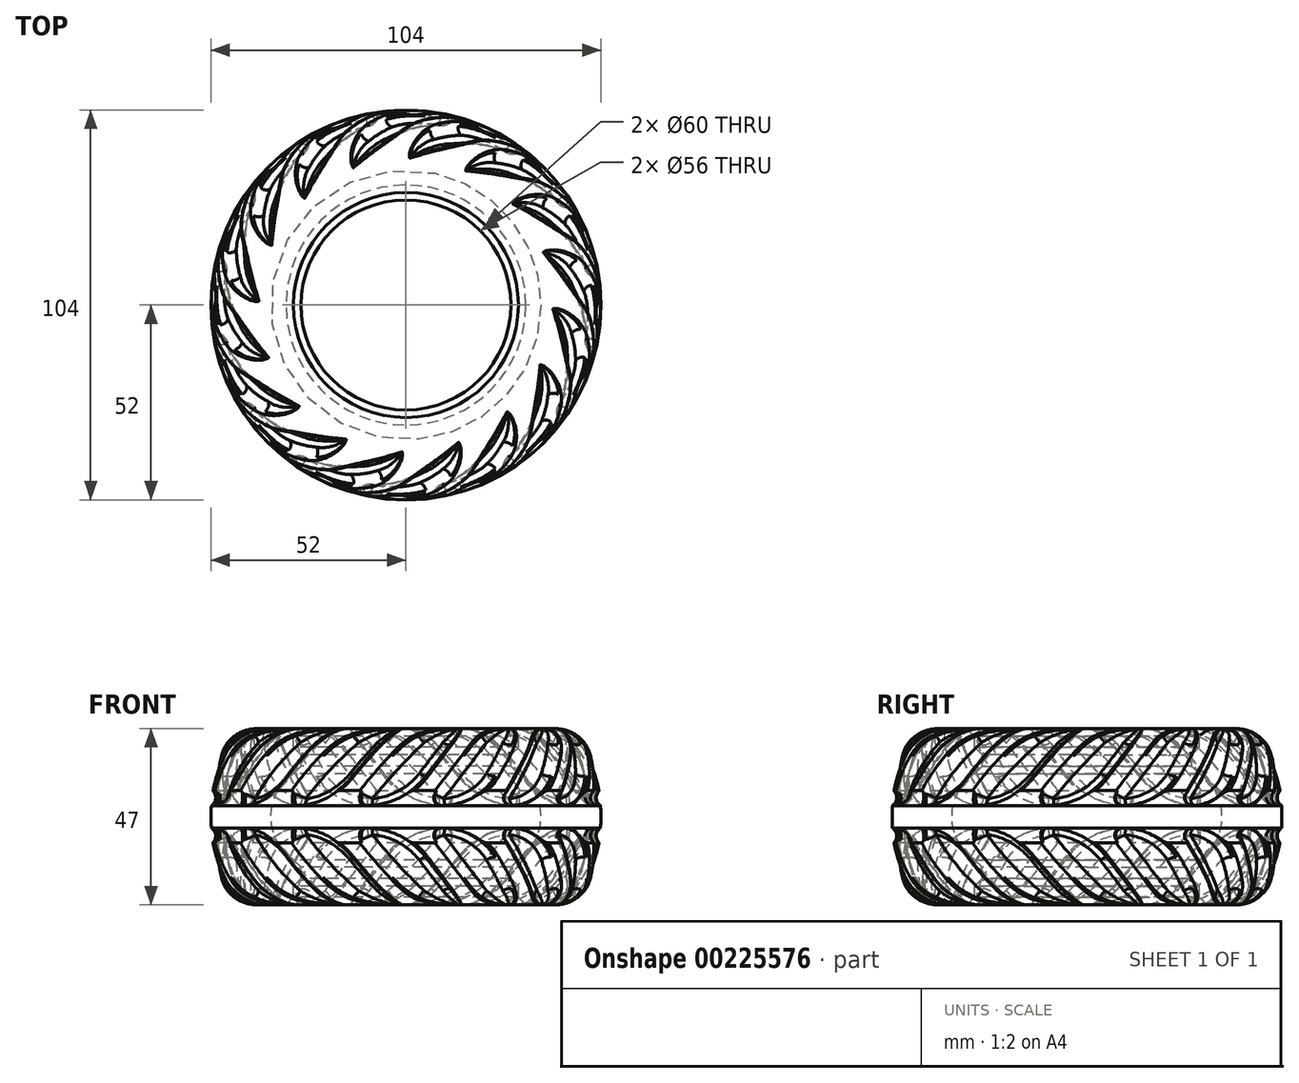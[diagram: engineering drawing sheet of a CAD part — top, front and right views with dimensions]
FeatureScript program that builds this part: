
annotation { "Feature Type Name" : "Feature", "Feature Type Description" : "" }
export const myFeature = defineFeature(function(context is Context, id is Id, definition is map)
    precondition{}
    {
        {
            var Q0;
            Q0=qCreatedBy(makeId("Front.planeOp"),FACE);
            var sketch = newSketch(context, id + "F0", { "sketchPlane" : qUnion([Q0])});
            skLineSegment(sketch, "E0", {"start": v(0, 0) * mm, "end": v(-62.9, 0) * mm, "construction": true});
            skCircle(sketch, "E1", {"center": v(-39.12, 17.25) * mm, "radius": 6.25 * mm});
            skCircle(sketch, "E2", {"center": v(0, 0) * mm, "radius": 55 * mm});
            skCircle(sketch, "E3", {"center": v(-39.12, -17.25) * mm, "radius": 6.25 * mm});
            skCircle(sketch, "E4", {"center": v(0, 0) * mm, "radius": 49 * mm});
            skLineSegment(sketch, "E5", {"start": v(-30, 23.5) * mm, "end": v(-39.12, 23.5) * mm});
            skLineSegment(sketch, "E6", {"start": v(-30, -23.5) * mm, "end": v(-39.12, -23.5) * mm});
            skLineSegment(sketch, "E7", {"start": v(0, 89.19) * mm, "end": v(0, -93.9) * mm, "construction": true});
            skLineSegment(sketch, "E8", {"start": v(-30, 23.5) * mm, "end": v(-30, 18.5) * mm});
            skLineSegment(sketch, "E9", {"start": v(-30, 18.5) * mm, "end": v(-28, 18.5) * mm});
            skLineSegment(sketch, "E10", {"start": v(-28, 18.5) * mm, "end": v(-28, 11.5) * mm});
            skLineSegment(sketch, "E11", {"start": v(-28, 11.5) * mm, "end": v(-30, 11.5) * mm});
            skLineSegment(sketch, "E12", {"start": v(-30, 11.5) * mm, "end": v(-30, -11.5) * mm});
            skLineSegment(sketch, "E13", {"start": v(-30, -11.5) * mm, "end": v(-28, -11.5) * mm});
            skLineSegment(sketch, "E14", {"start": v(-28, -11.5) * mm, "end": v(-28, -18.5) * mm});
            skLineSegment(sketch, "E15", {"start": v(-28, -18.5) * mm, "end": v(-30, -18.5) * mm});
            skLineSegment(sketch, "E16", {"start": v(-30, -18.5) * mm, "end": v(-30, -23.5) * mm});
            skArc(sketch, "E17", {"start": v(-30, 11.5) * mm, "mid": v(-36, 0) * mm, "end": v(-30, -11.5) * mm});
            skSolve(sketch);
        }
        {
            var Q0;
            {var subQ1=sQuery(id+"F0.wireOp",EDGE,"E5");Q0=makeQuery(id+"F0.imprint","IMPRINT",FACE,{"disambiguationData":[TD([[makeQuery(id+"F0.imprint","IMPRINT",EDGE,{"derivedFrom":subQ1}),1.0]])]});}
            var Q1;
            {var subQ0=sQuery(id+"F0.wireOp",EDGE,"E1");var subQ1=makeQuery(id+"F0.imprint","INTERSECT",VERTEX,{"derivedFrom":[subQ0,sQuery(id+"F0.wireOp",EDGE,"E5")]});Q1=makeQuery(id+"F0.imprint","IMPRINT",FACE,{"disambiguationData":[TD([[makeQuery(id+"F0.imprint","IMPRINT",EDGE,{"disambiguationData":[TD([[subQ1,-1.0]])],"derivedFrom":subQ0}),1.0]])]});}
            var Q2;
            {var subQ0=sQuery(id+"F0.wireOp",EDGE,"E3");var subQ1=makeQuery(id+"F0.imprint","INTERSECT",VERTEX,{"derivedFrom":[subQ0,sQuery(id+"F0.wireOp",EDGE,"E6")]});Q2=makeQuery(id+"F0.imprint","IMPRINT",FACE,{"disambiguationData":[TD([[makeQuery(id+"F0.imprint","IMPRINT",EDGE,{"disambiguationData":[TD([[subQ1,1.0]])],"derivedFrom":subQ0}),1.0]])]});}
            var Q3;
            Q3=sQuery(id+"F0.wireOp",EDGE,"E7");
            revolve(context, id + "F1", {"entities" : qUnion([Q0, Q1, Q2]), "axis" : qUnion([Q3]), "revolveType" : RevolveType.FULL});
        }
        {
            var Q0;
            Q0=qCreatedBy(makeId("Top.planeOp"),FACE);
            cPlane(context, id + "F2", {"entities" : qUnion([Q0]), "cplaneType" : CPlaneType.OFFSET, "offset" : 23.5 * mm, "width" : 150 * mm, "height" : 150 * mm});
        }
        {
            var Q0;
            Q0=qCreatedBy(makeId("Top.planeOp"),FACE);
            var sketch = newSketch(context, id + "F3", { "sketchPlane" : qUnion([Q0])});
            skLineSegment(sketch, "E18.bottom", {"start": v(-3, 40) * mm, "end": v(3, 40) * mm});
            skLineSegment(sketch, "E18.top", {"start": v(-3, 66) * mm, "end": v(3, 66) * mm});
            skLineSegment(sketch, "E18.left", {"start": v(-3, 40) * mm, "end": v(-3, 66) * mm});
            skLineSegment(sketch, "E18.right", {"start": v(3, 40) * mm, "end": v(3, 66) * mm});
            skLineSegment(sketch, "E19", {"start": v(0, 113.7) * mm, "end": v(0, -99.56) * mm, "construction": true});
            skLineSegment(sketch, "E20.1.0", {"start": v(-18.08, 35.8) * mm, "end": v(-28.03, 59.83) * mm});
            skLineSegment(sketch, "E20.1.1", {"start": v(-28.03, 59.83) * mm, "end": v(-22.49, 62.12) * mm});
            skLineSegment(sketch, "E20.1.2", {"start": v(-12.54, 38.1) * mm, "end": v(-22.49, 62.12) * mm});
            skLineSegment(sketch, "E20.1.3", {"start": v(-18.08, 35.8) * mm, "end": v(-12.54, 38.1) * mm});
            skLineSegment(sketch, "E20.2.0", {"start": v(-30.4, 26.16) * mm, "end": v(-48.8, 44.55) * mm});
            skLineSegment(sketch, "E20.2.1", {"start": v(-48.8, 44.55) * mm, "end": v(-44.55, 48.8) * mm});
            skLineSegment(sketch, "E20.2.2", {"start": v(-26.16, 30.4) * mm, "end": v(-44.55, 48.8) * mm});
            skLineSegment(sketch, "E20.2.3", {"start": v(-30.4, 26.16) * mm, "end": v(-26.16, 30.4) * mm});
            skLineSegment(sketch, "E20.3.0", {"start": v(-38.1, 12.54) * mm, "end": v(-62.12, 22.49) * mm});
            skLineSegment(sketch, "E20.3.1", {"start": v(-62.12, 22.49) * mm, "end": v(-59.83, 28.03) * mm});
            skLineSegment(sketch, "E20.3.2", {"start": v(-35.8, 18.08) * mm, "end": v(-59.83, 28.03) * mm});
            skLineSegment(sketch, "E20.3.3", {"start": v(-38.1, 12.54) * mm, "end": v(-35.8, 18.08) * mm});
            skLineSegment(sketch, "E20.4.0", {"start": v(-40, -3) * mm, "end": v(-66, -3) * mm});
            skLineSegment(sketch, "E20.4.1", {"start": v(-66, -3) * mm, "end": v(-66, 3) * mm});
            skLineSegment(sketch, "E20.4.2", {"start": v(-40, 3) * mm, "end": v(-66, 3) * mm});
            skLineSegment(sketch, "E20.4.3", {"start": v(-40, -3) * mm, "end": v(-40, 3) * mm});
            skLineSegment(sketch, "E20.5.0", {"start": v(-35.8, -18.08) * mm, "end": v(-59.83, -28.03) * mm});
            skLineSegment(sketch, "E20.5.1", {"start": v(-59.83, -28.03) * mm, "end": v(-62.12, -22.49) * mm});
            skLineSegment(sketch, "E20.5.2", {"start": v(-38.1, -12.54) * mm, "end": v(-62.12, -22.49) * mm});
            skLineSegment(sketch, "E20.5.3", {"start": v(-35.8, -18.08) * mm, "end": v(-38.1, -12.54) * mm});
            skLineSegment(sketch, "E20.6.0", {"start": v(-26.16, -30.4) * mm, "end": v(-44.55, -48.8) * mm});
            skLineSegment(sketch, "E20.6.1", {"start": v(-44.55, -48.8) * mm, "end": v(-48.8, -44.55) * mm});
            skLineSegment(sketch, "E20.6.2", {"start": v(-30.4, -26.16) * mm, "end": v(-48.8, -44.55) * mm});
            skLineSegment(sketch, "E20.6.3", {"start": v(-26.16, -30.4) * mm, "end": v(-30.4, -26.16) * mm});
            skLineSegment(sketch, "E20.7.0", {"start": v(-12.54, -38.1) * mm, "end": v(-22.49, -62.12) * mm});
            skLineSegment(sketch, "E20.7.1", {"start": v(-22.49, -62.12) * mm, "end": v(-28.03, -59.83) * mm});
            skLineSegment(sketch, "E20.7.2", {"start": v(-18.08, -35.8) * mm, "end": v(-28.03, -59.83) * mm});
            skLineSegment(sketch, "E20.7.3", {"start": v(-12.54, -38.1) * mm, "end": v(-18.08, -35.8) * mm});
            skLineSegment(sketch, "E20.8.0", {"start": v(3, -40) * mm, "end": v(3, -66) * mm});
            skLineSegment(sketch, "E20.8.1", {"start": v(3, -66) * mm, "end": v(-3, -66) * mm});
            skLineSegment(sketch, "E20.8.2", {"start": v(-3, -40) * mm, "end": v(-3, -66) * mm});
            skLineSegment(sketch, "E20.8.3", {"start": v(3, -40) * mm, "end": v(-3, -40) * mm});
            skLineSegment(sketch, "E20.9.0", {"start": v(18.08, -35.8) * mm, "end": v(28.03, -59.83) * mm});
            skLineSegment(sketch, "E20.9.1", {"start": v(28.03, -59.83) * mm, "end": v(22.49, -62.12) * mm});
            skLineSegment(sketch, "E20.9.2", {"start": v(12.54, -38.1) * mm, "end": v(22.49, -62.12) * mm});
            skLineSegment(sketch, "E20.9.3", {"start": v(18.08, -35.8) * mm, "end": v(12.54, -38.1) * mm});
            skLineSegment(sketch, "E20.10.0", {"start": v(30.4, -26.16) * mm, "end": v(48.8, -44.55) * mm});
            skLineSegment(sketch, "E20.10.1", {"start": v(48.8, -44.55) * mm, "end": v(44.55, -48.8) * mm});
            skLineSegment(sketch, "E20.10.2", {"start": v(26.16, -30.4) * mm, "end": v(44.55, -48.8) * mm});
            skLineSegment(sketch, "E20.10.3", {"start": v(30.4, -26.16) * mm, "end": v(26.16, -30.4) * mm});
            skLineSegment(sketch, "E20.11.0", {"start": v(38.1, -12.54) * mm, "end": v(62.12, -22.49) * mm});
            skLineSegment(sketch, "E20.11.1", {"start": v(62.12, -22.49) * mm, "end": v(59.83, -28.03) * mm});
            skLineSegment(sketch, "E20.11.2", {"start": v(35.8, -18.08) * mm, "end": v(59.83, -28.03) * mm});
            skLineSegment(sketch, "E20.11.3", {"start": v(38.1, -12.54) * mm, "end": v(35.8, -18.08) * mm});
            skLineSegment(sketch, "E20.12.0", {"start": v(40, 3) * mm, "end": v(66, 3) * mm});
            skLineSegment(sketch, "E20.12.1", {"start": v(66, 3) * mm, "end": v(66, -3) * mm});
            skLineSegment(sketch, "E20.12.2", {"start": v(40, -3) * mm, "end": v(66, -3) * mm});
            skLineSegment(sketch, "E20.12.3", {"start": v(40, 3) * mm, "end": v(40, -3) * mm});
            skLineSegment(sketch, "E20.13.0", {"start": v(35.8, 18.08) * mm, "end": v(59.83, 28.03) * mm});
            skLineSegment(sketch, "E20.13.1", {"start": v(59.83, 28.03) * mm, "end": v(62.12, 22.49) * mm});
            skLineSegment(sketch, "E20.13.2", {"start": v(38.1, 12.54) * mm, "end": v(62.12, 22.49) * mm});
            skLineSegment(sketch, "E20.13.3", {"start": v(35.8, 18.08) * mm, "end": v(38.1, 12.54) * mm});
            skLineSegment(sketch, "E20.14.0", {"start": v(26.16, 30.4) * mm, "end": v(44.55, 48.8) * mm});
            skLineSegment(sketch, "E20.14.1", {"start": v(44.55, 48.8) * mm, "end": v(48.8, 44.55) * mm});
            skLineSegment(sketch, "E20.14.2", {"start": v(30.4, 26.16) * mm, "end": v(48.8, 44.55) * mm});
            skLineSegment(sketch, "E20.14.3", {"start": v(26.16, 30.4) * mm, "end": v(30.4, 26.16) * mm});
            skLineSegment(sketch, "E20.15.0", {"start": v(12.54, 38.1) * mm, "end": v(22.49, 62.12) * mm});
            skLineSegment(sketch, "E20.15.1", {"start": v(22.49, 62.12) * mm, "end": v(28.03, 59.83) * mm});
            skLineSegment(sketch, "E20.15.2", {"start": v(18.08, 35.8) * mm, "end": v(28.03, 59.83) * mm});
            skLineSegment(sketch, "E20.15.3", {"start": v(12.54, 38.1) * mm, "end": v(18.08, 35.8) * mm});
            skPoint(sketch, "E20.center", {"position": v(0, 0) * mm});
            skSolve(sketch);
        }
        {
            var Q0;
            Q0=qCreatedBy(id+"F2.planeOp",FACE);
            var sketch = newSketch(context, id + "F4", { "sketchPlane" : qUnion([Q0])});
            skLineSegment(sketch, "E21", {"start": v(-21, 70) * mm, "end": v(-21, 30) * mm});
            skLineSegment(sketch, "E22", {"start": v(-21, 30) * mm, "end": v(-15, 30) * mm});
            skLineSegment(sketch, "E23", {"start": v(-21, 70) * mm, "end": v(-15, 70) * mm});
            skLineSegment(sketch, "E24", {"start": v(-15, 70) * mm, "end": v(-15, 30) * mm});
            skLineSegment(sketch, "E25", {"start": v(0, 99.7) * mm, "end": v(0, -107.8) * mm, "construction": true});
            skLineSegment(sketch, "E26.1.0", {"start": v(-46.19, 56.64) * mm, "end": v(-30.88, 19.68) * mm});
            skLineSegment(sketch, "E26.1.1", {"start": v(-40.65, 58.93) * mm, "end": v(-25.34, 21.98) * mm});
            skLineSegment(sketch, "E26.1.2", {"start": v(-30.88, 19.68) * mm, "end": v(-25.34, 21.98) * mm});
            skLineSegment(sketch, "E26.1.3", {"start": v(-46.19, 56.64) * mm, "end": v(-40.65, 58.93) * mm});
            skLineSegment(sketch, "E26.2.0", {"start": v(-64.35, 34.65) * mm, "end": v(-36.06, 6.36) * mm});
            skLineSegment(sketch, "E26.2.1", {"start": v(-60.1, 38.9) * mm, "end": v(-31.82, 10.6) * mm});
            skLineSegment(sketch, "E26.2.2", {"start": v(-36.06, 6.36) * mm, "end": v(-31.82, 10.6) * mm});
            skLineSegment(sketch, "E26.2.3", {"start": v(-64.35, 34.65) * mm, "end": v(-60.1, 38.9) * mm});
            skLineSegment(sketch, "E26.3.0", {"start": v(-72.7, 7.39) * mm, "end": v(-35.75, -7.92) * mm});
            skLineSegment(sketch, "E26.3.1", {"start": v(-70.41, 12.93) * mm, "end": v(-33.46, -2.38) * mm});
            skLineSegment(sketch, "E26.3.2", {"start": v(-35.75, -7.92) * mm, "end": v(-33.46, -2.38) * mm});
            skLineSegment(sketch, "E26.3.3", {"start": v(-72.7, 7.39) * mm, "end": v(-70.41, 12.93) * mm});
            skLineSegment(sketch, "E26.4.0", {"start": v(-70, -21) * mm, "end": v(-30, -21) * mm});
            skLineSegment(sketch, "E26.4.1", {"start": v(-70, -15) * mm, "end": v(-30, -15) * mm});
            skLineSegment(sketch, "E26.4.2", {"start": v(-30, -21) * mm, "end": v(-30, -15) * mm});
            skLineSegment(sketch, "E26.4.3", {"start": v(-70, -21) * mm, "end": v(-70, -15) * mm});
            skLineSegment(sketch, "E26.5.0", {"start": v(-56.64, -46.19) * mm, "end": v(-19.68, -30.88) * mm});
            skLineSegment(sketch, "E26.5.1", {"start": v(-58.93, -40.65) * mm, "end": v(-21.98, -25.34) * mm});
            skLineSegment(sketch, "E26.5.2", {"start": v(-19.68, -30.88) * mm, "end": v(-21.98, -25.34) * mm});
            skLineSegment(sketch, "E26.5.3", {"start": v(-56.64, -46.19) * mm, "end": v(-58.93, -40.65) * mm});
            skLineSegment(sketch, "E26.6.0", {"start": v(-34.65, -64.35) * mm, "end": v(-6.36, -36.06) * mm});
            skLineSegment(sketch, "E26.6.1", {"start": v(-38.9, -60.1) * mm, "end": v(-10.6, -31.82) * mm});
            skLineSegment(sketch, "E26.6.2", {"start": v(-6.36, -36.06) * mm, "end": v(-10.6, -31.82) * mm});
            skLineSegment(sketch, "E26.6.3", {"start": v(-34.65, -64.35) * mm, "end": v(-38.9, -60.1) * mm});
            skLineSegment(sketch, "E26.7.0", {"start": v(-7.39, -72.7) * mm, "end": v(7.92, -35.75) * mm});
            skLineSegment(sketch, "E26.7.1", {"start": v(-12.93, -70.41) * mm, "end": v(2.38, -33.46) * mm});
            skLineSegment(sketch, "E26.7.2", {"start": v(7.92, -35.75) * mm, "end": v(2.38, -33.46) * mm});
            skLineSegment(sketch, "E26.7.3", {"start": v(-7.39, -72.7) * mm, "end": v(-12.93, -70.41) * mm});
            skLineSegment(sketch, "E26.8.0", {"start": v(21, -70) * mm, "end": v(21, -30) * mm});
            skLineSegment(sketch, "E26.8.1", {"start": v(15, -70) * mm, "end": v(15, -30) * mm});
            skLineSegment(sketch, "E26.8.2", {"start": v(21, -30) * mm, "end": v(15, -30) * mm});
            skLineSegment(sketch, "E26.8.3", {"start": v(21, -70) * mm, "end": v(15, -70) * mm});
            skLineSegment(sketch, "E26.9.0", {"start": v(46.19, -56.64) * mm, "end": v(30.88, -19.68) * mm});
            skLineSegment(sketch, "E26.9.1", {"start": v(40.65, -58.93) * mm, "end": v(25.34, -21.98) * mm});
            skLineSegment(sketch, "E26.9.2", {"start": v(30.88, -19.68) * mm, "end": v(25.34, -21.98) * mm});
            skLineSegment(sketch, "E26.9.3", {"start": v(46.19, -56.64) * mm, "end": v(40.65, -58.93) * mm});
            skLineSegment(sketch, "E26.10.0", {"start": v(64.35, -34.65) * mm, "end": v(36.06, -6.36) * mm});
            skLineSegment(sketch, "E26.10.1", {"start": v(60.1, -38.9) * mm, "end": v(31.82, -10.6) * mm});
            skLineSegment(sketch, "E26.10.2", {"start": v(36.06, -6.36) * mm, "end": v(31.82, -10.6) * mm});
            skLineSegment(sketch, "E26.10.3", {"start": v(64.35, -34.65) * mm, "end": v(60.1, -38.9) * mm});
            skLineSegment(sketch, "E26.11.0", {"start": v(72.7, -7.39) * mm, "end": v(35.75, 7.92) * mm});
            skLineSegment(sketch, "E26.11.1", {"start": v(70.41, -12.93) * mm, "end": v(33.46, 2.38) * mm});
            skLineSegment(sketch, "E26.11.2", {"start": v(35.75, 7.92) * mm, "end": v(33.46, 2.38) * mm});
            skLineSegment(sketch, "E26.11.3", {"start": v(72.7, -7.39) * mm, "end": v(70.41, -12.93) * mm});
            skLineSegment(sketch, "E26.12.0", {"start": v(70, 21) * mm, "end": v(30, 21) * mm});
            skLineSegment(sketch, "E26.12.1", {"start": v(70, 15) * mm, "end": v(30, 15) * mm});
            skLineSegment(sketch, "E26.12.2", {"start": v(30, 21) * mm, "end": v(30, 15) * mm});
            skLineSegment(sketch, "E26.12.3", {"start": v(70, 21) * mm, "end": v(70, 15) * mm});
            skLineSegment(sketch, "E26.13.0", {"start": v(56.64, 46.19) * mm, "end": v(19.68, 30.88) * mm});
            skLineSegment(sketch, "E26.13.1", {"start": v(58.93, 40.65) * mm, "end": v(21.98, 25.34) * mm});
            skLineSegment(sketch, "E26.13.2", {"start": v(19.68, 30.88) * mm, "end": v(21.98, 25.34) * mm});
            skLineSegment(sketch, "E26.13.3", {"start": v(56.64, 46.19) * mm, "end": v(58.93, 40.65) * mm});
            skLineSegment(sketch, "E26.14.0", {"start": v(34.65, 64.35) * mm, "end": v(6.36, 36.06) * mm});
            skLineSegment(sketch, "E26.14.1", {"start": v(38.9, 60.1) * mm, "end": v(10.6, 31.82) * mm});
            skLineSegment(sketch, "E26.14.2", {"start": v(6.36, 36.06) * mm, "end": v(10.6, 31.82) * mm});
            skLineSegment(sketch, "E26.14.3", {"start": v(34.65, 64.35) * mm, "end": v(38.9, 60.1) * mm});
            skLineSegment(sketch, "E26.15.0", {"start": v(7.39, 72.7) * mm, "end": v(-7.92, 35.75) * mm});
            skLineSegment(sketch, "E26.15.1", {"start": v(12.93, 70.41) * mm, "end": v(-2.38, 33.46) * mm});
            skLineSegment(sketch, "E26.15.2", {"start": v(-7.92, 35.75) * mm, "end": v(-2.38, 33.46) * mm});
            skLineSegment(sketch, "E26.15.3", {"start": v(7.39, 72.7) * mm, "end": v(12.93, 70.41) * mm});
            skPoint(sketch, "E26.center", {"position": v(0, 0) * mm});
            skSolve(sketch);
        }
        {
            var Q2;
            Q2=makeQuery(id+"F3.imprint","IMPRINT",FACE,{"disambiguationData":[TD([[makeQuery(id+"F3.imprint","IMPRINT",EDGE,{"derivedFrom":sQuery(id+"F3.wireOp",EDGE,"E18.bottom")}),1.0]])]});
            var Q3;
            Q3=makeQuery(id+"F4.imprint","IMPRINT",FACE,{"disambiguationData":[TD([[makeQuery(id+"F4.imprint","IMPRINT",EDGE,{"derivedFrom":sQuery(id+"F4.wireOp",EDGE,"E21")}),1.0]])]});
            loft(context, id + "F5", {"operationType" : NewBodyOperationType.ADD, "sheetProfilesArray" : [{ "sheetProfileEntities" : qUnion([Q2]) }, { "sheetProfileEntities" : qUnion([Q3]) }]});
        }
        {
            var Q2;
            Q2=makeQuery(id+"F3.imprint","IMPRINT",FACE,{"disambiguationData":[TD([[makeQuery(id+"F3.imprint","IMPRINT",EDGE,{"derivedFrom":sQuery(id+"F3.wireOp",EDGE,"E20.15.0")}),-1.0]])]});
            var Q3;
            Q3=makeQuery(id+"F4.imprint","IMPRINT",FACE,{"disambiguationData":[TD([[makeQuery(id+"F4.imprint","IMPRINT",EDGE,{"derivedFrom":sQuery(id+"F4.wireOp",EDGE,"E26.15.0")}),1.0]])]});
            loft(context, id + "F6", {"operationType" : NewBodyOperationType.ADD, "sheetProfilesArray" : [{ "sheetProfileEntities" : qUnion([Q2]) }, { "sheetProfileEntities" : qUnion([Q3]) }]});
        }
        {
            var Q1;
            Q1=makeQuery(id+"F3.imprint","IMPRINT",FACE,{"disambiguationData":[TD([[makeQuery(id+"F3.imprint","IMPRINT",EDGE,{"derivedFrom":sQuery(id+"F3.wireOp",EDGE,"E20.14.0")}),-1.0]])]});
            var Q2;
            Q2=makeQuery(id+"F4.imprint","IMPRINT",FACE,{"disambiguationData":[TD([[makeQuery(id+"F4.imprint","IMPRINT",EDGE,{"derivedFrom":sQuery(id+"F4.wireOp",EDGE,"E26.14.0")}),1.0]])]});
            loft(context, id + "F7", {"operationType" : NewBodyOperationType.ADD, "sheetProfilesArray" : [{ "sheetProfileEntities" : qUnion([Q1]) }, { "sheetProfileEntities" : qUnion([Q2]) }]});
        }
        {
            var Q1;
            Q1=makeQuery(id+"F3.imprint","IMPRINT",FACE,{"disambiguationData":[TD([[makeQuery(id+"F3.imprint","IMPRINT",EDGE,{"derivedFrom":sQuery(id+"F3.wireOp",EDGE,"E20.13.0")}),-1.0]])]});
            var Q2;
            Q2=makeQuery(id+"F4.imprint","IMPRINT",FACE,{"disambiguationData":[TD([[makeQuery(id+"F4.imprint","IMPRINT",EDGE,{"derivedFrom":sQuery(id+"F4.wireOp",EDGE,"E26.13.0")}),1.0]])]});
            loft(context, id + "F8", {"operationType" : NewBodyOperationType.ADD, "sheetProfilesArray" : [{ "sheetProfileEntities" : qUnion([Q1]) }, { "sheetProfileEntities" : qUnion([Q2]) }]});
        }
        {
            var Q2;
            Q2=makeQuery(id+"F3.imprint","IMPRINT",FACE,{"disambiguationData":[TD([[makeQuery(id+"F3.imprint","IMPRINT",EDGE,{"derivedFrom":sQuery(id+"F3.wireOp",EDGE,"E20.12.0")}),-1.0]])]});
            var Q3;
            Q3=makeQuery(id+"F4.imprint","IMPRINT",FACE,{"disambiguationData":[TD([[makeQuery(id+"F4.imprint","IMPRINT",EDGE,{"derivedFrom":sQuery(id+"F4.wireOp",EDGE,"E26.12.0")}),1.0]])]});
            loft(context, id + "F9", {"operationType" : NewBodyOperationType.ADD, "sheetProfilesArray" : [{ "sheetProfileEntities" : qUnion([Q2]) }, { "sheetProfileEntities" : qUnion([Q3]) }]});
        }
        {
            var Q2;
            Q2=makeQuery(id+"F3.imprint","IMPRINT",FACE,{"disambiguationData":[TD([[makeQuery(id+"F3.imprint","IMPRINT",EDGE,{"derivedFrom":sQuery(id+"F3.wireOp",EDGE,"E20.11.0")}),-1.0]])]});
            var Q3;
            Q3=makeQuery(id+"F4.imprint","IMPRINT",FACE,{"disambiguationData":[TD([[makeQuery(id+"F4.imprint","IMPRINT",EDGE,{"derivedFrom":sQuery(id+"F4.wireOp",EDGE,"E26.11.0")}),1.0]])]});
            loft(context, id + "F10", {"operationType" : NewBodyOperationType.ADD, "sheetProfilesArray" : [{ "sheetProfileEntities" : qUnion([Q2]) }, { "sheetProfileEntities" : qUnion([Q3]) }]});
        }
        {
            var Q2;
            Q2=makeQuery(id+"F3.imprint","IMPRINT",FACE,{"disambiguationData":[TD([[makeQuery(id+"F3.imprint","IMPRINT",EDGE,{"derivedFrom":sQuery(id+"F3.wireOp",EDGE,"E20.10.0")}),-1.0]])]});
            var Q3;
            Q3=makeQuery(id+"F4.imprint","IMPRINT",FACE,{"disambiguationData":[TD([[makeQuery(id+"F4.imprint","IMPRINT",EDGE,{"derivedFrom":sQuery(id+"F4.wireOp",EDGE,"E26.10.0")}),1.0]])]});
            loft(context, id + "F11", {"operationType" : NewBodyOperationType.ADD, "sheetProfilesArray" : [{ "sheetProfileEntities" : qUnion([Q2]) }, { "sheetProfileEntities" : qUnion([Q3]) }]});
        }
        {
            var Q2;
            Q2=makeQuery(id+"F3.imprint","IMPRINT",FACE,{"disambiguationData":[TD([[makeQuery(id+"F3.imprint","IMPRINT",EDGE,{"derivedFrom":sQuery(id+"F3.wireOp",EDGE,"E20.9.0")}),-1.0]])]});
            var Q3;
            Q3=makeQuery(id+"F4.imprint","IMPRINT",FACE,{"disambiguationData":[TD([[makeQuery(id+"F4.imprint","IMPRINT",EDGE,{"derivedFrom":sQuery(id+"F4.wireOp",EDGE,"E26.9.0")}),1.0]])]});
            loft(context, id + "F12", {"operationType" : NewBodyOperationType.ADD, "sheetProfilesArray" : [{ "sheetProfileEntities" : qUnion([Q2]) }, { "sheetProfileEntities" : qUnion([Q3]) }]});
        }
        {
            var Q2;
            Q2=makeQuery(id+"F3.imprint","IMPRINT",FACE,{"disambiguationData":[TD([[makeQuery(id+"F3.imprint","IMPRINT",EDGE,{"derivedFrom":sQuery(id+"F3.wireOp",EDGE,"E20.8.0")}),-1.0]])]});
            var Q3;
            Q3=makeQuery(id+"F4.imprint","IMPRINT",FACE,{"disambiguationData":[TD([[makeQuery(id+"F4.imprint","IMPRINT",EDGE,{"derivedFrom":sQuery(id+"F4.wireOp",EDGE,"E26.8.0")}),1.0]])]});
            loft(context, id + "F13", {"operationType" : NewBodyOperationType.ADD, "sheetProfilesArray" : [{ "sheetProfileEntities" : qUnion([Q2]) }, { "sheetProfileEntities" : qUnion([Q3]) }]});
        }
        {
            var Q2;
            Q2=makeQuery(id+"F3.imprint","IMPRINT",FACE,{"disambiguationData":[TD([[makeQuery(id+"F3.imprint","IMPRINT",EDGE,{"derivedFrom":sQuery(id+"F3.wireOp",EDGE,"E20.7.0")}),-1.0]])]});
            var Q3;
            Q3=makeQuery(id+"F4.imprint","IMPRINT",FACE,{"disambiguationData":[TD([[makeQuery(id+"F4.imprint","IMPRINT",EDGE,{"derivedFrom":sQuery(id+"F4.wireOp",EDGE,"E26.7.0")}),1.0]])]});
            loft(context, id + "F14", {"operationType" : NewBodyOperationType.ADD, "sheetProfilesArray" : [{ "sheetProfileEntities" : qUnion([Q2]) }, { "sheetProfileEntities" : qUnion([Q3]) }]});
        }
        {
            var Q2;
            Q2=makeQuery(id+"F3.imprint","IMPRINT",FACE,{"disambiguationData":[TD([[makeQuery(id+"F3.imprint","IMPRINT",EDGE,{"derivedFrom":sQuery(id+"F3.wireOp",EDGE,"E20.6.0")}),-1.0]])]});
            var Q3;
            Q3=makeQuery(id+"F4.imprint","IMPRINT",FACE,{"disambiguationData":[TD([[makeQuery(id+"F4.imprint","IMPRINT",EDGE,{"derivedFrom":sQuery(id+"F4.wireOp",EDGE,"E26.6.0")}),1.0]])]});
            loft(context, id + "F15", {"operationType" : NewBodyOperationType.ADD, "sheetProfilesArray" : [{ "sheetProfileEntities" : qUnion([Q2]) }, { "sheetProfileEntities" : qUnion([Q3]) }]});
        }
        {
            var Q2;
            Q2=makeQuery(id+"F3.imprint","IMPRINT",FACE,{"disambiguationData":[TD([[makeQuery(id+"F3.imprint","IMPRINT",EDGE,{"derivedFrom":sQuery(id+"F3.wireOp",EDGE,"E20.5.0")}),-1.0]])]});
            var Q3;
            Q3=makeQuery(id+"F4.imprint","IMPRINT",FACE,{"disambiguationData":[TD([[makeQuery(id+"F4.imprint","IMPRINT",EDGE,{"derivedFrom":sQuery(id+"F4.wireOp",EDGE,"E26.5.0")}),1.0]])]});
            loft(context, id + "F16", {"operationType" : NewBodyOperationType.ADD, "sheetProfilesArray" : [{ "sheetProfileEntities" : qUnion([Q2]) }, { "sheetProfileEntities" : qUnion([Q3]) }]});
        }
        {
            var Q1;
            Q1=makeQuery(id+"F4.imprint","IMPRINT",FACE,{"disambiguationData":[TD([[makeQuery(id+"F4.imprint","IMPRINT",EDGE,{"derivedFrom":sQuery(id+"F4.wireOp",EDGE,"E26.4.0")}),1.0]])]});
            var Q2;
            Q2=makeQuery(id+"F3.imprint","IMPRINT",FACE,{"disambiguationData":[TD([[makeQuery(id+"F3.imprint","IMPRINT",EDGE,{"derivedFrom":sQuery(id+"F3.wireOp",EDGE,"E20.4.0")}),-1.0]])]});
            loft(context, id + "F17", {"operationType" : NewBodyOperationType.ADD, "sheetProfilesArray" : [{ "sheetProfileEntities" : qUnion([Q1]) }, { "sheetProfileEntities" : qUnion([Q2]) }]});
        }
        {
            var Q1;
            Q1=makeQuery(id+"F3.imprint","IMPRINT",FACE,{"disambiguationData":[TD([[makeQuery(id+"F3.imprint","IMPRINT",EDGE,{"derivedFrom":sQuery(id+"F3.wireOp",EDGE,"E20.3.0")}),-1.0]])]});
            var Q2;
            Q2=makeQuery(id+"F4.imprint","IMPRINT",FACE,{"disambiguationData":[TD([[makeQuery(id+"F4.imprint","IMPRINT",EDGE,{"derivedFrom":sQuery(id+"F4.wireOp",EDGE,"E26.3.0")}),1.0]])]});
            loft(context, id + "F18", {"operationType" : NewBodyOperationType.ADD, "sheetProfilesArray" : [{ "sheetProfileEntities" : qUnion([Q1]) }, { "sheetProfileEntities" : qUnion([Q2]) }]});
        }
        {
            var Q1;
            Q1=makeQuery(id+"F3.imprint","IMPRINT",FACE,{"disambiguationData":[TD([[makeQuery(id+"F3.imprint","IMPRINT",EDGE,{"derivedFrom":sQuery(id+"F3.wireOp",EDGE,"E20.2.0")}),-1.0]])]});
            var Q2;
            Q2=makeQuery(id+"F4.imprint","IMPRINT",FACE,{"disambiguationData":[TD([[makeQuery(id+"F4.imprint","IMPRINT",EDGE,{"derivedFrom":sQuery(id+"F4.wireOp",EDGE,"E26.2.0")}),1.0]])]});
            loft(context, id + "F19", {"operationType" : NewBodyOperationType.ADD, "sheetProfilesArray" : [{ "sheetProfileEntities" : qUnion([Q1]) }, { "sheetProfileEntities" : qUnion([Q2]) }]});
        }
        {
            var Q1;
            Q1=makeQuery(id+"F3.imprint","IMPRINT",FACE,{"disambiguationData":[TD([[makeQuery(id+"F3.imprint","IMPRINT",EDGE,{"derivedFrom":sQuery(id+"F3.wireOp",EDGE,"E20.1.0")}),-1.0]])]});
            var Q2;
            Q2=makeQuery(id+"F4.imprint","IMPRINT",FACE,{"disambiguationData":[TD([[makeQuery(id+"F4.imprint","IMPRINT",EDGE,{"derivedFrom":sQuery(id+"F4.wireOp",EDGE,"E26.1.0")}),1.0]])]});
            loft(context, id + "F20", {"operationType" : NewBodyOperationType.ADD, "sheetProfilesArray" : [{ "sheetProfileEntities" : qUnion([Q1]) }, { "sheetProfileEntities" : qUnion([Q2]) }]});
        }
        {
            var Q0;
            Q0=qCreatedBy(makeId("Top.planeOp"),FACE);
            cPlane(context, id + "F21", {"entities" : qUnion([Q0]), "cplaneType" : CPlaneType.OFFSET, "offset" : 23.5 * mm, "oppositeDirection" : true, "width" : 150 * mm, "height" : 150 * mm});
        }
        {
            var Q0;
            Q0=qCreatedBy(id+"F21.planeOp",FACE);
            var sketch = newSketch(context, id + "F22", { "sketchPlane" : qUnion([Q0])});
            skLineSegment(sketch, "E27.bottom", {"start": v(15, -70) * mm, "end": v(21, -70) * mm});
            skLineSegment(sketch, "E27.top", {"start": v(15, -30) * mm, "end": v(21, -30) * mm});
            skLineSegment(sketch, "E27.left", {"start": v(15, -70) * mm, "end": v(15, -30) * mm});
            skLineSegment(sketch, "E27.right", {"start": v(21, -70) * mm, "end": v(21, -30) * mm});
            skLineSegment(sketch, "E28.1.0", {"start": v(40.65, -58.93) * mm, "end": v(25.34, -21.98) * mm});
            skLineSegment(sketch, "E28.1.1", {"start": v(46.19, -56.64) * mm, "end": v(30.88, -19.68) * mm});
            skLineSegment(sketch, "E28.1.2", {"start": v(40.65, -58.93) * mm, "end": v(46.19, -56.64) * mm});
            skLineSegment(sketch, "E28.1.3", {"start": v(25.34, -21.98) * mm, "end": v(30.88, -19.68) * mm});
            skLineSegment(sketch, "E28.2.0", {"start": v(60.1, -38.9) * mm, "end": v(31.82, -10.6) * mm});
            skLineSegment(sketch, "E28.2.1", {"start": v(64.35, -34.65) * mm, "end": v(36.06, -6.36) * mm});
            skLineSegment(sketch, "E28.2.2", {"start": v(60.1, -38.9) * mm, "end": v(64.35, -34.65) * mm});
            skLineSegment(sketch, "E28.2.3", {"start": v(31.82, -10.6) * mm, "end": v(36.06, -6.36) * mm});
            skLineSegment(sketch, "E28.3.0", {"start": v(70.41, -12.93) * mm, "end": v(33.46, 2.38) * mm});
            skLineSegment(sketch, "E28.3.1", {"start": v(72.7, -7.39) * mm, "end": v(35.75, 7.92) * mm});
            skLineSegment(sketch, "E28.3.2", {"start": v(70.41, -12.93) * mm, "end": v(72.7, -7.39) * mm});
            skLineSegment(sketch, "E28.3.3", {"start": v(33.46, 2.38) * mm, "end": v(35.75, 7.92) * mm});
            skLineSegment(sketch, "E28.4.0", {"start": v(70, 15) * mm, "end": v(30, 15) * mm});
            skLineSegment(sketch, "E28.4.1", {"start": v(70, 21) * mm, "end": v(30, 21) * mm});
            skLineSegment(sketch, "E28.4.2", {"start": v(70, 15) * mm, "end": v(70, 21) * mm});
            skLineSegment(sketch, "E28.4.3", {"start": v(30, 15) * mm, "end": v(30, 21) * mm});
            skLineSegment(sketch, "E28.5.0", {"start": v(58.93, 40.65) * mm, "end": v(21.98, 25.34) * mm});
            skLineSegment(sketch, "E28.5.1", {"start": v(56.64, 46.19) * mm, "end": v(19.68, 30.88) * mm});
            skLineSegment(sketch, "E28.5.2", {"start": v(58.93, 40.65) * mm, "end": v(56.64, 46.19) * mm});
            skLineSegment(sketch, "E28.5.3", {"start": v(21.98, 25.34) * mm, "end": v(19.68, 30.88) * mm});
            skLineSegment(sketch, "E28.6.0", {"start": v(38.9, 60.1) * mm, "end": v(10.6, 31.82) * mm});
            skLineSegment(sketch, "E28.6.1", {"start": v(34.65, 64.35) * mm, "end": v(6.36, 36.06) * mm});
            skLineSegment(sketch, "E28.6.2", {"start": v(38.9, 60.1) * mm, "end": v(34.65, 64.35) * mm});
            skLineSegment(sketch, "E28.6.3", {"start": v(10.6, 31.82) * mm, "end": v(6.36, 36.06) * mm});
            skLineSegment(sketch, "E28.7.0", {"start": v(12.93, 70.41) * mm, "end": v(-2.38, 33.46) * mm});
            skLineSegment(sketch, "E28.7.1", {"start": v(7.39, 72.7) * mm, "end": v(-7.92, 35.75) * mm});
            skLineSegment(sketch, "E28.7.2", {"start": v(12.93, 70.41) * mm, "end": v(7.39, 72.7) * mm});
            skLineSegment(sketch, "E28.7.3", {"start": v(-2.38, 33.46) * mm, "end": v(-7.92, 35.75) * mm});
            skLineSegment(sketch, "E28.8.0", {"start": v(-15, 70) * mm, "end": v(-15, 30) * mm});
            skLineSegment(sketch, "E28.8.1", {"start": v(-21, 70) * mm, "end": v(-21, 30) * mm});
            skLineSegment(sketch, "E28.8.2", {"start": v(-15, 70) * mm, "end": v(-21, 70) * mm});
            skLineSegment(sketch, "E28.8.3", {"start": v(-15, 30) * mm, "end": v(-21, 30) * mm});
            skLineSegment(sketch, "E28.9.0", {"start": v(-40.65, 58.93) * mm, "end": v(-25.34, 21.98) * mm});
            skLineSegment(sketch, "E28.9.1", {"start": v(-46.19, 56.64) * mm, "end": v(-30.88, 19.68) * mm});
            skLineSegment(sketch, "E28.9.2", {"start": v(-40.65, 58.93) * mm, "end": v(-46.19, 56.64) * mm});
            skLineSegment(sketch, "E28.9.3", {"start": v(-25.34, 21.98) * mm, "end": v(-30.88, 19.68) * mm});
            skLineSegment(sketch, "E28.10.0", {"start": v(-60.1, 38.9) * mm, "end": v(-31.82, 10.6) * mm});
            skLineSegment(sketch, "E28.10.1", {"start": v(-64.35, 34.65) * mm, "end": v(-36.06, 6.36) * mm});
            skLineSegment(sketch, "E28.10.2", {"start": v(-60.1, 38.9) * mm, "end": v(-64.35, 34.65) * mm});
            skLineSegment(sketch, "E28.10.3", {"start": v(-31.82, 10.6) * mm, "end": v(-36.06, 6.36) * mm});
            skLineSegment(sketch, "E28.11.0", {"start": v(-70.41, 12.93) * mm, "end": v(-33.46, -2.38) * mm});
            skLineSegment(sketch, "E28.11.1", {"start": v(-72.7, 7.39) * mm, "end": v(-35.75, -7.92) * mm});
            skLineSegment(sketch, "E28.11.2", {"start": v(-70.41, 12.93) * mm, "end": v(-72.7, 7.39) * mm});
            skLineSegment(sketch, "E28.11.3", {"start": v(-33.46, -2.38) * mm, "end": v(-35.75, -7.92) * mm});
            skLineSegment(sketch, "E28.12.0", {"start": v(-70, -15) * mm, "end": v(-30, -15) * mm});
            skLineSegment(sketch, "E28.12.1", {"start": v(-70, -21) * mm, "end": v(-30, -21) * mm});
            skLineSegment(sketch, "E28.12.2", {"start": v(-70, -15) * mm, "end": v(-70, -21) * mm});
            skLineSegment(sketch, "E28.12.3", {"start": v(-30, -15) * mm, "end": v(-30, -21) * mm});
            skLineSegment(sketch, "E28.13.0", {"start": v(-58.93, -40.65) * mm, "end": v(-21.98, -25.34) * mm});
            skLineSegment(sketch, "E28.13.1", {"start": v(-56.64, -46.19) * mm, "end": v(-19.68, -30.88) * mm});
            skLineSegment(sketch, "E28.13.2", {"start": v(-58.93, -40.65) * mm, "end": v(-56.64, -46.19) * mm});
            skLineSegment(sketch, "E28.13.3", {"start": v(-21.98, -25.34) * mm, "end": v(-19.68, -30.88) * mm});
            skLineSegment(sketch, "E28.14.0", {"start": v(-38.9, -60.1) * mm, "end": v(-10.6, -31.82) * mm});
            skLineSegment(sketch, "E28.14.1", {"start": v(-34.65, -64.35) * mm, "end": v(-6.36, -36.06) * mm});
            skLineSegment(sketch, "E28.14.2", {"start": v(-38.9, -60.1) * mm, "end": v(-34.65, -64.35) * mm});
            skLineSegment(sketch, "E28.14.3", {"start": v(-10.6, -31.82) * mm, "end": v(-6.36, -36.06) * mm});
            skLineSegment(sketch, "E28.15.0", {"start": v(-12.93, -70.41) * mm, "end": v(2.38, -33.46) * mm});
            skLineSegment(sketch, "E28.15.1", {"start": v(-7.39, -72.7) * mm, "end": v(7.92, -35.75) * mm});
            skLineSegment(sketch, "E28.15.2", {"start": v(-12.93, -70.41) * mm, "end": v(-7.39, -72.7) * mm});
            skLineSegment(sketch, "E28.15.3", {"start": v(2.38, -33.46) * mm, "end": v(7.92, -35.75) * mm});
            skPoint(sketch, "E28.center", {"position": v(0, 0) * mm});
            skSolve(sketch);
        }
        {
            var Q1;
            Q1=makeQuery(id+"F22.imprint","IMPRINT",FACE,{"disambiguationData":[TD([[makeQuery(id+"F22.imprint","IMPRINT",EDGE,{"derivedFrom":sQuery(id+"F22.wireOp",EDGE,"E27.bottom")}),1.0]])]});
            var Q2;
            Q2=makeQuery(id+"F3.imprint","IMPRINT",FACE,{"disambiguationData":[TD([[makeQuery(id+"F3.imprint","IMPRINT",EDGE,{"derivedFrom":sQuery(id+"F3.wireOp",EDGE,"E20.8.0")}),-1.0]])]});
            loft(context, id + "F23", {"operationType" : NewBodyOperationType.ADD, "sheetProfilesArray" : [{ "sheetProfileEntities" : qUnion([Q1]) }, { "sheetProfileEntities" : qUnion([Q2]) }]});
        }
        {
            var Q1;
            Q1=makeQuery(id+"F22.imprint","IMPRINT",FACE,{"disambiguationData":[TD([[makeQuery(id+"F22.imprint","IMPRINT",EDGE,{"derivedFrom":sQuery(id+"F22.wireOp",EDGE,"E28.1.0")}),-1.0]])]});
            var Q2;
            Q2=makeQuery(id+"F3.imprint","IMPRINT",FACE,{"disambiguationData":[TD([[makeQuery(id+"F3.imprint","IMPRINT",EDGE,{"derivedFrom":sQuery(id+"F3.wireOp",EDGE,"E20.9.0")}),-1.0]])]});
            loft(context, id + "F24", {"operationType" : NewBodyOperationType.ADD, "sheetProfilesArray" : [{ "sheetProfileEntities" : qUnion([Q1]) }, { "sheetProfileEntities" : qUnion([Q2]) }]});
        }
        {
            var Q1;
            Q1=makeQuery(id+"F22.imprint","IMPRINT",FACE,{"disambiguationData":[TD([[makeQuery(id+"F22.imprint","IMPRINT",EDGE,{"derivedFrom":sQuery(id+"F22.wireOp",EDGE,"E28.2.0")}),-1.0]])]});
            var Q2;
            Q2=makeQuery(id+"F3.imprint","IMPRINT",FACE,{"disambiguationData":[TD([[makeQuery(id+"F3.imprint","IMPRINT",EDGE,{"derivedFrom":sQuery(id+"F3.wireOp",EDGE,"E20.10.0")}),-1.0]])]});
            loft(context, id + "F25", {"operationType" : NewBodyOperationType.ADD, "sheetProfilesArray" : [{ "sheetProfileEntities" : qUnion([Q1]) }, { "sheetProfileEntities" : qUnion([Q2]) }]});
        }
        {
            var Q1;
            Q1=makeQuery(id+"F22.imprint","IMPRINT",FACE,{"disambiguationData":[TD([[makeQuery(id+"F22.imprint","IMPRINT",EDGE,{"derivedFrom":sQuery(id+"F22.wireOp",EDGE,"E28.3.0")}),-1.0]])]});
            var Q2;
            Q2=makeQuery(id+"F3.imprint","IMPRINT",FACE,{"disambiguationData":[TD([[makeQuery(id+"F3.imprint","IMPRINT",EDGE,{"derivedFrom":sQuery(id+"F3.wireOp",EDGE,"E20.11.0")}),-1.0]])]});
            loft(context, id + "F26", {"operationType" : NewBodyOperationType.ADD, "sheetProfilesArray" : [{ "sheetProfileEntities" : qUnion([Q1]) }, { "sheetProfileEntities" : qUnion([Q2]) }]});
        }
        {
            var Q1;
            Q1=makeQuery(id+"F22.imprint","IMPRINT",FACE,{"disambiguationData":[TD([[makeQuery(id+"F22.imprint","IMPRINT",EDGE,{"derivedFrom":sQuery(id+"F22.wireOp",EDGE,"E28.4.0")}),-1.0]])]});
            var Q2;
            Q2=makeQuery(id+"F3.imprint","IMPRINT",FACE,{"disambiguationData":[TD([[makeQuery(id+"F3.imprint","IMPRINT",EDGE,{"derivedFrom":sQuery(id+"F3.wireOp",EDGE,"E20.12.0")}),-1.0]])]});
            loft(context, id + "F27", {"operationType" : NewBodyOperationType.ADD, "sheetProfilesArray" : [{ "sheetProfileEntities" : qUnion([Q1]) }, { "sheetProfileEntities" : qUnion([Q2]) }]});
        }
        {
            var Q1;
            Q1=makeQuery(id+"F22.imprint","IMPRINT",FACE,{"disambiguationData":[TD([[makeQuery(id+"F22.imprint","IMPRINT",EDGE,{"derivedFrom":sQuery(id+"F22.wireOp",EDGE,"E28.5.0")}),-1.0]])]});
            var Q2;
            Q2=makeQuery(id+"F3.imprint","IMPRINT",FACE,{"disambiguationData":[TD([[makeQuery(id+"F3.imprint","IMPRINT",EDGE,{"derivedFrom":sQuery(id+"F3.wireOp",EDGE,"E20.13.0")}),-1.0]])]});
            loft(context, id + "F28", {"operationType" : NewBodyOperationType.ADD, "sheetProfilesArray" : [{ "sheetProfileEntities" : qUnion([Q1]) }, { "sheetProfileEntities" : qUnion([Q2]) }]});
        }
        {
            var Q1;
            Q1=makeQuery(id+"F22.imprint","IMPRINT",FACE,{"disambiguationData":[TD([[makeQuery(id+"F22.imprint","IMPRINT",EDGE,{"derivedFrom":sQuery(id+"F22.wireOp",EDGE,"E28.6.0")}),-1.0]])]});
            var Q2;
            Q2=makeQuery(id+"F3.imprint","IMPRINT",FACE,{"disambiguationData":[TD([[makeQuery(id+"F3.imprint","IMPRINT",EDGE,{"derivedFrom":sQuery(id+"F3.wireOp",EDGE,"E20.14.0")}),-1.0]])]});
            loft(context, id + "F29", {"operationType" : NewBodyOperationType.ADD, "sheetProfilesArray" : [{ "sheetProfileEntities" : qUnion([Q1]) }, { "sheetProfileEntities" : qUnion([Q2]) }]});
        }
        {
            var Q1;
            Q1=makeQuery(id+"F22.imprint","IMPRINT",FACE,{"disambiguationData":[TD([[makeQuery(id+"F22.imprint","IMPRINT",EDGE,{"derivedFrom":sQuery(id+"F22.wireOp",EDGE,"E28.7.0")}),-1.0]])]});
            var Q2;
            Q2=makeQuery(id+"F3.imprint","IMPRINT",FACE,{"disambiguationData":[TD([[makeQuery(id+"F3.imprint","IMPRINT",EDGE,{"derivedFrom":sQuery(id+"F3.wireOp",EDGE,"E20.15.0")}),-1.0]])]});
            loft(context, id + "F30", {"operationType" : NewBodyOperationType.ADD, "sheetProfilesArray" : [{ "sheetProfileEntities" : qUnion([Q1]) }, { "sheetProfileEntities" : qUnion([Q2]) }]});
        }
        {
            var Q1;
            Q1=makeQuery(id+"F22.imprint","IMPRINT",FACE,{"disambiguationData":[TD([[makeQuery(id+"F22.imprint","IMPRINT",EDGE,{"derivedFrom":sQuery(id+"F22.wireOp",EDGE,"E28.8.0")}),-1.0]])]});
            var Q2;
            Q2=makeQuery(id+"F3.imprint","IMPRINT",FACE,{"disambiguationData":[TD([[makeQuery(id+"F3.imprint","IMPRINT",EDGE,{"derivedFrom":sQuery(id+"F3.wireOp",EDGE,"E18.bottom")}),1.0]])]});
            loft(context, id + "F31", {"operationType" : NewBodyOperationType.ADD, "sheetProfilesArray" : [{ "sheetProfileEntities" : qUnion([Q1]) }, { "sheetProfileEntities" : qUnion([Q2]) }]});
        }
        {
            var Q1;
            Q1=makeQuery(id+"F22.imprint","IMPRINT",FACE,{"disambiguationData":[TD([[makeQuery(id+"F22.imprint","IMPRINT",EDGE,{"derivedFrom":sQuery(id+"F22.wireOp",EDGE,"E28.9.0")}),-1.0]])]});
            var Q2;
            Q2=makeQuery(id+"F3.imprint","IMPRINT",FACE,{"disambiguationData":[TD([[makeQuery(id+"F3.imprint","IMPRINT",EDGE,{"derivedFrom":sQuery(id+"F3.wireOp",EDGE,"E20.1.0")}),-1.0]])]});
            loft(context, id + "F32", {"operationType" : NewBodyOperationType.ADD, "sheetProfilesArray" : [{ "sheetProfileEntities" : qUnion([Q1]) }, { "sheetProfileEntities" : qUnion([Q2]) }]});
        }
        {
            var Q1;
            Q1=makeQuery(id+"F22.imprint","IMPRINT",FACE,{"disambiguationData":[TD([[makeQuery(id+"F22.imprint","IMPRINT",EDGE,{"derivedFrom":sQuery(id+"F22.wireOp",EDGE,"E28.10.0")}),-1.0]])]});
            var Q2;
            Q2=makeQuery(id+"F3.imprint","IMPRINT",FACE,{"disambiguationData":[TD([[makeQuery(id+"F3.imprint","IMPRINT",EDGE,{"derivedFrom":sQuery(id+"F3.wireOp",EDGE,"E20.2.0")}),-1.0]])]});
            loft(context, id + "F33", {"operationType" : NewBodyOperationType.ADD, "sheetProfilesArray" : [{ "sheetProfileEntities" : qUnion([Q1]) }, { "sheetProfileEntities" : qUnion([Q2]) }]});
        }
        {
            var Q1;
            Q1=makeQuery(id+"F22.imprint","IMPRINT",FACE,{"disambiguationData":[TD([[makeQuery(id+"F22.imprint","IMPRINT",EDGE,{"derivedFrom":sQuery(id+"F22.wireOp",EDGE,"E28.11.0")}),-1.0]])]});
            var Q2;
            Q2=makeQuery(id+"F3.imprint","IMPRINT",FACE,{"disambiguationData":[TD([[makeQuery(id+"F3.imprint","IMPRINT",EDGE,{"derivedFrom":sQuery(id+"F3.wireOp",EDGE,"E20.3.0")}),-1.0]])]});
            loft(context, id + "F34", {"operationType" : NewBodyOperationType.ADD, "sheetProfilesArray" : [{ "sheetProfileEntities" : qUnion([Q1]) }, { "sheetProfileEntities" : qUnion([Q2]) }]});
        }
        {
            var Q1;
            Q1=makeQuery(id+"F22.imprint","IMPRINT",FACE,{"disambiguationData":[TD([[makeQuery(id+"F22.imprint","IMPRINT",EDGE,{"derivedFrom":sQuery(id+"F22.wireOp",EDGE,"E28.12.0")}),-1.0]])]});
            var Q2;
            Q2=makeQuery(id+"F3.imprint","IMPRINT",FACE,{"disambiguationData":[TD([[makeQuery(id+"F3.imprint","IMPRINT",EDGE,{"derivedFrom":sQuery(id+"F3.wireOp",EDGE,"E20.4.0")}),-1.0]])]});
            loft(context, id + "F35", {"operationType" : NewBodyOperationType.ADD, "sheetProfilesArray" : [{ "sheetProfileEntities" : qUnion([Q1]) }, { "sheetProfileEntities" : qUnion([Q2]) }]});
        }
        {
            var Q1;
            Q1=makeQuery(id+"F22.imprint","IMPRINT",FACE,{"disambiguationData":[TD([[makeQuery(id+"F22.imprint","IMPRINT",EDGE,{"derivedFrom":sQuery(id+"F22.wireOp",EDGE,"E28.13.0")}),-1.0]])]});
            var Q2;
            Q2=makeQuery(id+"F3.imprint","IMPRINT",FACE,{"disambiguationData":[TD([[makeQuery(id+"F3.imprint","IMPRINT",EDGE,{"derivedFrom":sQuery(id+"F3.wireOp",EDGE,"E20.5.0")}),-1.0]])]});
            loft(context, id + "F36", {"operationType" : NewBodyOperationType.ADD, "sheetProfilesArray" : [{ "sheetProfileEntities" : qUnion([Q1]) }, { "sheetProfileEntities" : qUnion([Q2]) }]});
        }
        {
            var Q1;
            Q1=makeQuery(id+"F22.imprint","IMPRINT",FACE,{"disambiguationData":[TD([[makeQuery(id+"F22.imprint","IMPRINT",EDGE,{"derivedFrom":sQuery(id+"F22.wireOp",EDGE,"E28.14.0")}),-1.0]])]});
            var Q2;
            Q2=makeQuery(id+"F3.imprint","IMPRINT",FACE,{"disambiguationData":[TD([[makeQuery(id+"F3.imprint","IMPRINT",EDGE,{"derivedFrom":sQuery(id+"F3.wireOp",EDGE,"E20.6.0")}),-1.0]])]});
            loft(context, id + "F37", {"operationType" : NewBodyOperationType.ADD, "sheetProfilesArray" : [{ "sheetProfileEntities" : qUnion([Q1]) }, { "sheetProfileEntities" : qUnion([Q2]) }]});
        }
        {
            var Q1;
            Q1=makeQuery(id+"F22.imprint","IMPRINT",FACE,{"disambiguationData":[TD([[makeQuery(id+"F22.imprint","IMPRINT",EDGE,{"derivedFrom":sQuery(id+"F22.wireOp",EDGE,"E28.15.0")}),-1.0]])]});
            var Q2;
            Q2=makeQuery(id+"F3.imprint","IMPRINT",FACE,{"disambiguationData":[TD([[makeQuery(id+"F3.imprint","IMPRINT",EDGE,{"derivedFrom":sQuery(id+"F3.wireOp",EDGE,"E20.7.0")}),-1.0]])]});
            loft(context, id + "F38", {"operationType" : NewBodyOperationType.ADD, "sheetProfilesArray" : [{ "sheetProfileEntities" : qUnion([Q1]) }, { "sheetProfileEntities" : qUnion([Q2]) }]});
        }
        {
            var Q0;
            Q0=qCreatedBy(makeId("Top.planeOp"),FACE);
            var sketch = newSketch(context, id + "F39", { "sketchPlane" : qUnion([Q0])});
            skCircle(sketch, "E29", {"center": v(0, 0) * mm, "radius": 47.5 * mm});
            skCircle(sketch, "E30", {"center": v(0, 0) * mm, "radius": 67.5 * mm});
            skSolve(sketch);
        }
        {
            var Q0;
            Q0=makeQuery(id+"F39.imprint","IMPRINT",FACE,{"disambiguationData":[TD([[makeQuery(id+"F39.imprint","IMPRINT",EDGE,{"derivedFrom":sQuery(id+"F39.wireOp",EDGE,"E29")}),-1.0]])]});
            extrude(context, id + "F40", {"entities" : qUnion([Q0]), "operationType" : NewBodyOperationType.ADD, "depth" : 6 * mm, "symmetric" : true});
        }
        {
            var Q0;
            Q0=qCreatedBy(makeId("Right.planeOp"),FACE);
            var sketch = newSketch(context, id + "F41", { "sketchPlane" : qUnion([Q0])});
            skLineSegment(sketch, "E31", {"start": v(0, 27) * mm, "end": v(0, -23.5) * mm, "construction": true});
            skCircle(sketch, "E32", {"center": v(0, 0) * mm, "radius": 52 * mm});
            skCircle(sketch, "E33", {"center": v(0, 0) * mm, "radius": 85 * mm});
            skLineSegment(sketch, "E34", {"start": v(0, 85) * mm, "end": v(0, -85) * mm});
            skLineSegment(sketch, "E35", {"start": v(51.53, 7) * mm, "end": v(48.91, 3) * mm});
            skLineSegment(sketch, "E36", {"start": v(48.91, 3) * mm, "end": v(51.91, 3) * mm});
            skLineSegment(sketch, "E37", {"start": v(51.91, -3) * mm, "end": v(48.91, -3) * mm});
            skLineSegment(sketch, "E38", {"start": v(48.91, -3) * mm, "end": v(51.53, -7) * mm});
            skSolve(sketch);
        }
        {
            var Q0;
            {var subQ0=sQuery(id+"F41.wireOp",EDGE,"E34");var subQ1=sQuery(id+"F41.wireOp",EDGE,"E32");var subQ2=makeQuery(id+"F41.imprint","INTERSECT",VERTEX,{"disambiguationData":[OD(0.0)],"derivedFrom":[subQ1,subQ0]});Q0=makeQuery(id+"F41.imprint","IMPRINT",FACE,{"disambiguationData":[TD([[makeQuery(id+"F41.imprint","IMPRINT",EDGE,{"disambiguationData":[TD([[subQ2,-1.0]])],"derivedFrom":subQ1}),-1.0]])]});}
            var Q1;
            {var subQ0=sQuery(id+"F41.wireOp",EDGE,"E37");Q1=makeQuery(id+"F41.imprint","IMPRINT",FACE,{"disambiguationData":[TD([[makeQuery(id+"F41.imprint","IMPRINT",EDGE,{"derivedFrom":subQ0}),1.0]])]});}
            var Q2;
            {var subQ0=sQuery(id+"F41.wireOp",EDGE,"E35");Q2=makeQuery(id+"F41.imprint","IMPRINT",FACE,{"disambiguationData":[TD([[makeQuery(id+"F41.imprint","IMPRINT",EDGE,{"derivedFrom":subQ0}),1.0]])]});}
            var Q3;
            Q3=sQuery(id+"F41.wireOp",EDGE,"E31");
            revolve(context, id + "F42", {"operationType" : NewBodyOperationType.REMOVE, "entities" : qUnion([Q0, Q1, Q2]), "axis" : qUnion([Q3]), "revolveType" : RevolveType.FULL, "oppositeDirection" : true});
        }
        {
            var Q0;
            Q0=makeQuery(id+"F42.boolean.opBoolean","INTERSECT",EDGE,{"disambiguationData":[OD(5.0)],"derivedFrom":[makeQuery(id+"F20.boolean.opBoolean","MERGE",FACE,{"derivedFrom":[makeQuery(id+"F19.boolean.opBoolean","MERGE",FACE,{"derivedFrom":[makeQuery(id+"F18.boolean.opBoolean","MERGE",FACE,{"derivedFrom":[makeQuery(id+"F17.boolean.opBoolean","MERGE",FACE,{"derivedFrom":[makeQuery(id+"F16.boolean.opBoolean","MERGE",FACE,{"derivedFrom":[makeQuery(id+"F15.boolean.opBoolean","MERGE",FACE,{"derivedFrom":[makeQuery(id+"F14.boolean.opBoolean","MERGE",FACE,{"derivedFrom":[makeQuery(id+"F13.boolean.opBoolean","MERGE",FACE,{"derivedFrom":[makeQuery(id+"F12.boolean.opBoolean","MERGE",FACE,{"derivedFrom":[makeQuery(id+"F11.boolean.opBoolean","MERGE",FACE,{"derivedFrom":[makeQuery(id+"F10.boolean.opBoolean","MERGE",FACE,{"derivedFrom":[makeQuery(id+"F9.boolean.opBoolean","MERGE",FACE,{"derivedFrom":[makeQuery(id+"F8.boolean.opBoolean","MERGE",FACE,{"derivedFrom":[makeQuery(id+"F7.boolean.opBoolean","MERGE",FACE,{"derivedFrom":[makeQuery(id+"F6.boolean.opBoolean","MERGE",FACE,{"derivedFrom":[makeQuery(id+"F5.boolean.opBoolean","MERGE",FACE,{"derivedFrom":[makeQuery(id+"F1.opRevolve","SWEPT_FACE",FACE,{"disambiguationData":[OSD([sQuery(id+"F0.wireOp",EDGE,"E5")])]}),makeQuery(id+"F5.opLoft","CAP_FACE",FACE,{"disambiguationData":[OSD([makeQuery(id+"F4.imprint","IMPRINT",FACE,{"disambiguationData":[TD([[makeQuery(id+"F4.imprint","IMPRINT",EDGE,{"derivedFrom":sQuery(id+"F4.wireOp",EDGE,"E21")}),1.0]])]})])],"isStart":true})]}),makeQuery(id+"F6.opLoft","CAP_FACE",FACE,{"disambiguationData":[OSD([makeQuery(id+"F4.imprint","IMPRINT",FACE,{"disambiguationData":[TD([[makeQuery(id+"F4.imprint","IMPRINT",EDGE,{"derivedFrom":sQuery(id+"F4.wireOp",EDGE,"E26.15.0")}),1.0]])]})])],"isStart":true})]}),makeQuery(id+"F7.opLoft","CAP_FACE",FACE,{"disambiguationData":[OSD([makeQuery(id+"F4.imprint","IMPRINT",FACE,{"disambiguationData":[TD([[makeQuery(id+"F4.imprint","IMPRINT",EDGE,{"derivedFrom":sQuery(id+"F4.wireOp",EDGE,"E26.14.0")}),1.0]])]})])],"isStart":true})]}),makeQuery(id+"F8.opLoft","CAP_FACE",FACE,{"disambiguationData":[OSD([makeQuery(id+"F4.imprint","IMPRINT",FACE,{"disambiguationData":[TD([[makeQuery(id+"F4.imprint","IMPRINT",EDGE,{"derivedFrom":sQuery(id+"F4.wireOp",EDGE,"E26.13.0")}),1.0]])]})])],"isStart":true})]}),makeQuery(id+"F9.opLoft","CAP_FACE",FACE,{"disambiguationData":[OSD([makeQuery(id+"F4.imprint","IMPRINT",FACE,{"disambiguationData":[TD([[makeQuery(id+"F4.imprint","IMPRINT",EDGE,{"derivedFrom":sQuery(id+"F4.wireOp",EDGE,"E26.12.0")}),1.0]])]})])],"isStart":true})]}),makeQuery(id+"F10.opLoft","CAP_FACE",FACE,{"disambiguationData":[OSD([makeQuery(id+"F4.imprint","IMPRINT",FACE,{"disambiguationData":[TD([[makeQuery(id+"F4.imprint","IMPRINT",EDGE,{"derivedFrom":sQuery(id+"F4.wireOp",EDGE,"E26.11.0")}),1.0]])]})])],"isStart":true})]}),makeQuery(id+"F11.opLoft","CAP_FACE",FACE,{"disambiguationData":[OSD([makeQuery(id+"F4.imprint","IMPRINT",FACE,{"disambiguationData":[TD([[makeQuery(id+"F4.imprint","IMPRINT",EDGE,{"derivedFrom":sQuery(id+"F4.wireOp",EDGE,"E26.10.0")}),1.0]])]})])],"isStart":true})]}),makeQuery(id+"F12.opLoft","CAP_FACE",FACE,{"disambiguationData":[OSD([makeQuery(id+"F4.imprint","IMPRINT",FACE,{"disambiguationData":[TD([[makeQuery(id+"F4.imprint","IMPRINT",EDGE,{"derivedFrom":sQuery(id+"F4.wireOp",EDGE,"E26.9.0")}),1.0]])]})])],"isStart":true})]}),makeQuery(id+"F13.opLoft","CAP_FACE",FACE,{"disambiguationData":[OSD([makeQuery(id+"F4.imprint","IMPRINT",FACE,{"disambiguationData":[TD([[makeQuery(id+"F4.imprint","IMPRINT",EDGE,{"derivedFrom":sQuery(id+"F4.wireOp",EDGE,"E26.8.0")}),1.0]])]})])],"isStart":true})]}),makeQuery(id+"F14.opLoft","CAP_FACE",FACE,{"disambiguationData":[OSD([makeQuery(id+"F4.imprint","IMPRINT",FACE,{"disambiguationData":[TD([[makeQuery(id+"F4.imprint","IMPRINT",EDGE,{"derivedFrom":sQuery(id+"F4.wireOp",EDGE,"E26.7.0")}),1.0]])]})])],"isStart":true})]}),makeQuery(id+"F15.opLoft","CAP_FACE",FACE,{"disambiguationData":[OSD([makeQuery(id+"F4.imprint","IMPRINT",FACE,{"disambiguationData":[TD([[makeQuery(id+"F4.imprint","IMPRINT",EDGE,{"derivedFrom":sQuery(id+"F4.wireOp",EDGE,"E26.6.0")}),1.0]])]})])],"isStart":true})]}),makeQuery(id+"F16.opLoft","CAP_FACE",FACE,{"disambiguationData":[OSD([makeQuery(id+"F4.imprint","IMPRINT",FACE,{"disambiguationData":[TD([[makeQuery(id+"F4.imprint","IMPRINT",EDGE,{"derivedFrom":sQuery(id+"F4.wireOp",EDGE,"E26.5.0")}),1.0]])]})])],"isStart":true})]}),makeQuery(id+"F17.opLoft","CAP_FACE",FACE,{"disambiguationData":[OSD([makeQuery(id+"F4.imprint","IMPRINT",FACE,{"disambiguationData":[TD([[makeQuery(id+"F4.imprint","IMPRINT",EDGE,{"derivedFrom":sQuery(id+"F4.wireOp",EDGE,"E26.4.0")}),1.0]])]})])],"isStart":true})]}),makeQuery(id+"F18.opLoft","CAP_FACE",FACE,{"disambiguationData":[OSD([makeQuery(id+"F4.imprint","IMPRINT",FACE,{"disambiguationData":[TD([[makeQuery(id+"F4.imprint","IMPRINT",EDGE,{"derivedFrom":sQuery(id+"F4.wireOp",EDGE,"E26.3.0")}),1.0]])]})])],"isStart":true})]}),makeQuery(id+"F19.opLoft","CAP_FACE",FACE,{"disambiguationData":[OSD([makeQuery(id+"F4.imprint","IMPRINT",FACE,{"disambiguationData":[TD([[makeQuery(id+"F4.imprint","IMPRINT",EDGE,{"derivedFrom":sQuery(id+"F4.wireOp",EDGE,"E26.2.0")}),1.0]])]})])],"isStart":true})]}),makeQuery(id+"F20.opLoft","CAP_FACE",FACE,{"disambiguationData":[OSD([makeQuery(id+"F4.imprint","IMPRINT",FACE,{"disambiguationData":[TD([[makeQuery(id+"F4.imprint","IMPRINT",EDGE,{"derivedFrom":sQuery(id+"F4.wireOp",EDGE,"E26.1.0")}),1.0]])]})])],"isStart":true})]}),makeQuery(id+"F42.opRevolve","SWEPT_FACE",FACE,{"disambiguationData":[OSD([sQuery(id+"F41.wireOp",EDGE,"E32")])]})]});
            var Q1;
            Q1=makeQuery(id+"F42.boolean.opBoolean","INTERSECT",EDGE,{"disambiguationData":[OD(4.0)],"derivedFrom":[makeQuery(id+"F20.boolean.opBoolean","MERGE",FACE,{"derivedFrom":[makeQuery(id+"F19.boolean.opBoolean","MERGE",FACE,{"derivedFrom":[makeQuery(id+"F18.boolean.opBoolean","MERGE",FACE,{"derivedFrom":[makeQuery(id+"F17.boolean.opBoolean","MERGE",FACE,{"derivedFrom":[makeQuery(id+"F16.boolean.opBoolean","MERGE",FACE,{"derivedFrom":[makeQuery(id+"F15.boolean.opBoolean","MERGE",FACE,{"derivedFrom":[makeQuery(id+"F14.boolean.opBoolean","MERGE",FACE,{"derivedFrom":[makeQuery(id+"F13.boolean.opBoolean","MERGE",FACE,{"derivedFrom":[makeQuery(id+"F12.boolean.opBoolean","MERGE",FACE,{"derivedFrom":[makeQuery(id+"F11.boolean.opBoolean","MERGE",FACE,{"derivedFrom":[makeQuery(id+"F10.boolean.opBoolean","MERGE",FACE,{"derivedFrom":[makeQuery(id+"F9.boolean.opBoolean","MERGE",FACE,{"derivedFrom":[makeQuery(id+"F8.boolean.opBoolean","MERGE",FACE,{"derivedFrom":[makeQuery(id+"F7.boolean.opBoolean","MERGE",FACE,{"derivedFrom":[makeQuery(id+"F6.boolean.opBoolean","MERGE",FACE,{"derivedFrom":[makeQuery(id+"F5.boolean.opBoolean","MERGE",FACE,{"derivedFrom":[makeQuery(id+"F1.opRevolve","SWEPT_FACE",FACE,{"disambiguationData":[OSD([sQuery(id+"F0.wireOp",EDGE,"E5")])]}),makeQuery(id+"F5.opLoft","CAP_FACE",FACE,{"disambiguationData":[OSD([makeQuery(id+"F4.imprint","IMPRINT",FACE,{"disambiguationData":[TD([[makeQuery(id+"F4.imprint","IMPRINT",EDGE,{"derivedFrom":sQuery(id+"F4.wireOp",EDGE,"E21")}),1.0]])]})])],"isStart":true})]}),makeQuery(id+"F6.opLoft","CAP_FACE",FACE,{"disambiguationData":[OSD([makeQuery(id+"F4.imprint","IMPRINT",FACE,{"disambiguationData":[TD([[makeQuery(id+"F4.imprint","IMPRINT",EDGE,{"derivedFrom":sQuery(id+"F4.wireOp",EDGE,"E26.15.0")}),1.0]])]})])],"isStart":true})]}),makeQuery(id+"F7.opLoft","CAP_FACE",FACE,{"disambiguationData":[OSD([makeQuery(id+"F4.imprint","IMPRINT",FACE,{"disambiguationData":[TD([[makeQuery(id+"F4.imprint","IMPRINT",EDGE,{"derivedFrom":sQuery(id+"F4.wireOp",EDGE,"E26.14.0")}),1.0]])]})])],"isStart":true})]}),makeQuery(id+"F8.opLoft","CAP_FACE",FACE,{"disambiguationData":[OSD([makeQuery(id+"F4.imprint","IMPRINT",FACE,{"disambiguationData":[TD([[makeQuery(id+"F4.imprint","IMPRINT",EDGE,{"derivedFrom":sQuery(id+"F4.wireOp",EDGE,"E26.13.0")}),1.0]])]})])],"isStart":true})]}),makeQuery(id+"F9.opLoft","CAP_FACE",FACE,{"disambiguationData":[OSD([makeQuery(id+"F4.imprint","IMPRINT",FACE,{"disambiguationData":[TD([[makeQuery(id+"F4.imprint","IMPRINT",EDGE,{"derivedFrom":sQuery(id+"F4.wireOp",EDGE,"E26.12.0")}),1.0]])]})])],"isStart":true})]}),makeQuery(id+"F10.opLoft","CAP_FACE",FACE,{"disambiguationData":[OSD([makeQuery(id+"F4.imprint","IMPRINT",FACE,{"disambiguationData":[TD([[makeQuery(id+"F4.imprint","IMPRINT",EDGE,{"derivedFrom":sQuery(id+"F4.wireOp",EDGE,"E26.11.0")}),1.0]])]})])],"isStart":true})]}),makeQuery(id+"F11.opLoft","CAP_FACE",FACE,{"disambiguationData":[OSD([makeQuery(id+"F4.imprint","IMPRINT",FACE,{"disambiguationData":[TD([[makeQuery(id+"F4.imprint","IMPRINT",EDGE,{"derivedFrom":sQuery(id+"F4.wireOp",EDGE,"E26.10.0")}),1.0]])]})])],"isStart":true})]}),makeQuery(id+"F12.opLoft","CAP_FACE",FACE,{"disambiguationData":[OSD([makeQuery(id+"F4.imprint","IMPRINT",FACE,{"disambiguationData":[TD([[makeQuery(id+"F4.imprint","IMPRINT",EDGE,{"derivedFrom":sQuery(id+"F4.wireOp",EDGE,"E26.9.0")}),1.0]])]})])],"isStart":true})]}),makeQuery(id+"F13.opLoft","CAP_FACE",FACE,{"disambiguationData":[OSD([makeQuery(id+"F4.imprint","IMPRINT",FACE,{"disambiguationData":[TD([[makeQuery(id+"F4.imprint","IMPRINT",EDGE,{"derivedFrom":sQuery(id+"F4.wireOp",EDGE,"E26.8.0")}),1.0]])]})])],"isStart":true})]}),makeQuery(id+"F14.opLoft","CAP_FACE",FACE,{"disambiguationData":[OSD([makeQuery(id+"F4.imprint","IMPRINT",FACE,{"disambiguationData":[TD([[makeQuery(id+"F4.imprint","IMPRINT",EDGE,{"derivedFrom":sQuery(id+"F4.wireOp",EDGE,"E26.7.0")}),1.0]])]})])],"isStart":true})]}),makeQuery(id+"F15.opLoft","CAP_FACE",FACE,{"disambiguationData":[OSD([makeQuery(id+"F4.imprint","IMPRINT",FACE,{"disambiguationData":[TD([[makeQuery(id+"F4.imprint","IMPRINT",EDGE,{"derivedFrom":sQuery(id+"F4.wireOp",EDGE,"E26.6.0")}),1.0]])]})])],"isStart":true})]}),makeQuery(id+"F16.opLoft","CAP_FACE",FACE,{"disambiguationData":[OSD([makeQuery(id+"F4.imprint","IMPRINT",FACE,{"disambiguationData":[TD([[makeQuery(id+"F4.imprint","IMPRINT",EDGE,{"derivedFrom":sQuery(id+"F4.wireOp",EDGE,"E26.5.0")}),1.0]])]})])],"isStart":true})]}),makeQuery(id+"F17.opLoft","CAP_FACE",FACE,{"disambiguationData":[OSD([makeQuery(id+"F4.imprint","IMPRINT",FACE,{"disambiguationData":[TD([[makeQuery(id+"F4.imprint","IMPRINT",EDGE,{"derivedFrom":sQuery(id+"F4.wireOp",EDGE,"E26.4.0")}),1.0]])]})])],"isStart":true})]}),makeQuery(id+"F18.opLoft","CAP_FACE",FACE,{"disambiguationData":[OSD([makeQuery(id+"F4.imprint","IMPRINT",FACE,{"disambiguationData":[TD([[makeQuery(id+"F4.imprint","IMPRINT",EDGE,{"derivedFrom":sQuery(id+"F4.wireOp",EDGE,"E26.3.0")}),1.0]])]})])],"isStart":true})]}),makeQuery(id+"F19.opLoft","CAP_FACE",FACE,{"disambiguationData":[OSD([makeQuery(id+"F4.imprint","IMPRINT",FACE,{"disambiguationData":[TD([[makeQuery(id+"F4.imprint","IMPRINT",EDGE,{"derivedFrom":sQuery(id+"F4.wireOp",EDGE,"E26.2.0")}),1.0]])]})])],"isStart":true})]}),makeQuery(id+"F20.opLoft","CAP_FACE",FACE,{"disambiguationData":[OSD([makeQuery(id+"F4.imprint","IMPRINT",FACE,{"disambiguationData":[TD([[makeQuery(id+"F4.imprint","IMPRINT",EDGE,{"derivedFrom":sQuery(id+"F4.wireOp",EDGE,"E26.1.0")}),1.0]])]})])],"isStart":true})]}),makeQuery(id+"F42.opRevolve","SWEPT_FACE",FACE,{"disambiguationData":[OSD([sQuery(id+"F41.wireOp",EDGE,"E32")])]})]});
            var Q2;
            Q2=makeQuery(id+"F42.boolean.opBoolean","INTERSECT",EDGE,{"disambiguationData":[OD(3.0)],"derivedFrom":[makeQuery(id+"F20.boolean.opBoolean","MERGE",FACE,{"derivedFrom":[makeQuery(id+"F19.boolean.opBoolean","MERGE",FACE,{"derivedFrom":[makeQuery(id+"F18.boolean.opBoolean","MERGE",FACE,{"derivedFrom":[makeQuery(id+"F17.boolean.opBoolean","MERGE",FACE,{"derivedFrom":[makeQuery(id+"F16.boolean.opBoolean","MERGE",FACE,{"derivedFrom":[makeQuery(id+"F15.boolean.opBoolean","MERGE",FACE,{"derivedFrom":[makeQuery(id+"F14.boolean.opBoolean","MERGE",FACE,{"derivedFrom":[makeQuery(id+"F13.boolean.opBoolean","MERGE",FACE,{"derivedFrom":[makeQuery(id+"F12.boolean.opBoolean","MERGE",FACE,{"derivedFrom":[makeQuery(id+"F11.boolean.opBoolean","MERGE",FACE,{"derivedFrom":[makeQuery(id+"F10.boolean.opBoolean","MERGE",FACE,{"derivedFrom":[makeQuery(id+"F9.boolean.opBoolean","MERGE",FACE,{"derivedFrom":[makeQuery(id+"F8.boolean.opBoolean","MERGE",FACE,{"derivedFrom":[makeQuery(id+"F7.boolean.opBoolean","MERGE",FACE,{"derivedFrom":[makeQuery(id+"F6.boolean.opBoolean","MERGE",FACE,{"derivedFrom":[makeQuery(id+"F5.boolean.opBoolean","MERGE",FACE,{"derivedFrom":[makeQuery(id+"F1.opRevolve","SWEPT_FACE",FACE,{"disambiguationData":[OSD([sQuery(id+"F0.wireOp",EDGE,"E5")])]}),makeQuery(id+"F5.opLoft","CAP_FACE",FACE,{"disambiguationData":[OSD([makeQuery(id+"F4.imprint","IMPRINT",FACE,{"disambiguationData":[TD([[makeQuery(id+"F4.imprint","IMPRINT",EDGE,{"derivedFrom":sQuery(id+"F4.wireOp",EDGE,"E21")}),1.0]])]})])],"isStart":true})]}),makeQuery(id+"F6.opLoft","CAP_FACE",FACE,{"disambiguationData":[OSD([makeQuery(id+"F4.imprint","IMPRINT",FACE,{"disambiguationData":[TD([[makeQuery(id+"F4.imprint","IMPRINT",EDGE,{"derivedFrom":sQuery(id+"F4.wireOp",EDGE,"E26.15.0")}),1.0]])]})])],"isStart":true})]}),makeQuery(id+"F7.opLoft","CAP_FACE",FACE,{"disambiguationData":[OSD([makeQuery(id+"F4.imprint","IMPRINT",FACE,{"disambiguationData":[TD([[makeQuery(id+"F4.imprint","IMPRINT",EDGE,{"derivedFrom":sQuery(id+"F4.wireOp",EDGE,"E26.14.0")}),1.0]])]})])],"isStart":true})]}),makeQuery(id+"F8.opLoft","CAP_FACE",FACE,{"disambiguationData":[OSD([makeQuery(id+"F4.imprint","IMPRINT",FACE,{"disambiguationData":[TD([[makeQuery(id+"F4.imprint","IMPRINT",EDGE,{"derivedFrom":sQuery(id+"F4.wireOp",EDGE,"E26.13.0")}),1.0]])]})])],"isStart":true})]}),makeQuery(id+"F9.opLoft","CAP_FACE",FACE,{"disambiguationData":[OSD([makeQuery(id+"F4.imprint","IMPRINT",FACE,{"disambiguationData":[TD([[makeQuery(id+"F4.imprint","IMPRINT",EDGE,{"derivedFrom":sQuery(id+"F4.wireOp",EDGE,"E26.12.0")}),1.0]])]})])],"isStart":true})]}),makeQuery(id+"F10.opLoft","CAP_FACE",FACE,{"disambiguationData":[OSD([makeQuery(id+"F4.imprint","IMPRINT",FACE,{"disambiguationData":[TD([[makeQuery(id+"F4.imprint","IMPRINT",EDGE,{"derivedFrom":sQuery(id+"F4.wireOp",EDGE,"E26.11.0")}),1.0]])]})])],"isStart":true})]}),makeQuery(id+"F11.opLoft","CAP_FACE",FACE,{"disambiguationData":[OSD([makeQuery(id+"F4.imprint","IMPRINT",FACE,{"disambiguationData":[TD([[makeQuery(id+"F4.imprint","IMPRINT",EDGE,{"derivedFrom":sQuery(id+"F4.wireOp",EDGE,"E26.10.0")}),1.0]])]})])],"isStart":true})]}),makeQuery(id+"F12.opLoft","CAP_FACE",FACE,{"disambiguationData":[OSD([makeQuery(id+"F4.imprint","IMPRINT",FACE,{"disambiguationData":[TD([[makeQuery(id+"F4.imprint","IMPRINT",EDGE,{"derivedFrom":sQuery(id+"F4.wireOp",EDGE,"E26.9.0")}),1.0]])]})])],"isStart":true})]}),makeQuery(id+"F13.opLoft","CAP_FACE",FACE,{"disambiguationData":[OSD([makeQuery(id+"F4.imprint","IMPRINT",FACE,{"disambiguationData":[TD([[makeQuery(id+"F4.imprint","IMPRINT",EDGE,{"derivedFrom":sQuery(id+"F4.wireOp",EDGE,"E26.8.0")}),1.0]])]})])],"isStart":true})]}),makeQuery(id+"F14.opLoft","CAP_FACE",FACE,{"disambiguationData":[OSD([makeQuery(id+"F4.imprint","IMPRINT",FACE,{"disambiguationData":[TD([[makeQuery(id+"F4.imprint","IMPRINT",EDGE,{"derivedFrom":sQuery(id+"F4.wireOp",EDGE,"E26.7.0")}),1.0]])]})])],"isStart":true})]}),makeQuery(id+"F15.opLoft","CAP_FACE",FACE,{"disambiguationData":[OSD([makeQuery(id+"F4.imprint","IMPRINT",FACE,{"disambiguationData":[TD([[makeQuery(id+"F4.imprint","IMPRINT",EDGE,{"derivedFrom":sQuery(id+"F4.wireOp",EDGE,"E26.6.0")}),1.0]])]})])],"isStart":true})]}),makeQuery(id+"F16.opLoft","CAP_FACE",FACE,{"disambiguationData":[OSD([makeQuery(id+"F4.imprint","IMPRINT",FACE,{"disambiguationData":[TD([[makeQuery(id+"F4.imprint","IMPRINT",EDGE,{"derivedFrom":sQuery(id+"F4.wireOp",EDGE,"E26.5.0")}),1.0]])]})])],"isStart":true})]}),makeQuery(id+"F17.opLoft","CAP_FACE",FACE,{"disambiguationData":[OSD([makeQuery(id+"F4.imprint","IMPRINT",FACE,{"disambiguationData":[TD([[makeQuery(id+"F4.imprint","IMPRINT",EDGE,{"derivedFrom":sQuery(id+"F4.wireOp",EDGE,"E26.4.0")}),1.0]])]})])],"isStart":true})]}),makeQuery(id+"F18.opLoft","CAP_FACE",FACE,{"disambiguationData":[OSD([makeQuery(id+"F4.imprint","IMPRINT",FACE,{"disambiguationData":[TD([[makeQuery(id+"F4.imprint","IMPRINT",EDGE,{"derivedFrom":sQuery(id+"F4.wireOp",EDGE,"E26.3.0")}),1.0]])]})])],"isStart":true})]}),makeQuery(id+"F19.opLoft","CAP_FACE",FACE,{"disambiguationData":[OSD([makeQuery(id+"F4.imprint","IMPRINT",FACE,{"disambiguationData":[TD([[makeQuery(id+"F4.imprint","IMPRINT",EDGE,{"derivedFrom":sQuery(id+"F4.wireOp",EDGE,"E26.2.0")}),1.0]])]})])],"isStart":true})]}),makeQuery(id+"F20.opLoft","CAP_FACE",FACE,{"disambiguationData":[OSD([makeQuery(id+"F4.imprint","IMPRINT",FACE,{"disambiguationData":[TD([[makeQuery(id+"F4.imprint","IMPRINT",EDGE,{"derivedFrom":sQuery(id+"F4.wireOp",EDGE,"E26.1.0")}),1.0]])]})])],"isStart":true})]}),makeQuery(id+"F42.opRevolve","SWEPT_FACE",FACE,{"disambiguationData":[OSD([sQuery(id+"F41.wireOp",EDGE,"E32")])]})]});
            var Q3;
            Q3=makeQuery(id+"F42.boolean.opBoolean","INTERSECT",EDGE,{"disambiguationData":[OD(2.0)],"derivedFrom":[makeQuery(id+"F20.boolean.opBoolean","MERGE",FACE,{"derivedFrom":[makeQuery(id+"F19.boolean.opBoolean","MERGE",FACE,{"derivedFrom":[makeQuery(id+"F18.boolean.opBoolean","MERGE",FACE,{"derivedFrom":[makeQuery(id+"F17.boolean.opBoolean","MERGE",FACE,{"derivedFrom":[makeQuery(id+"F16.boolean.opBoolean","MERGE",FACE,{"derivedFrom":[makeQuery(id+"F15.boolean.opBoolean","MERGE",FACE,{"derivedFrom":[makeQuery(id+"F14.boolean.opBoolean","MERGE",FACE,{"derivedFrom":[makeQuery(id+"F13.boolean.opBoolean","MERGE",FACE,{"derivedFrom":[makeQuery(id+"F12.boolean.opBoolean","MERGE",FACE,{"derivedFrom":[makeQuery(id+"F11.boolean.opBoolean","MERGE",FACE,{"derivedFrom":[makeQuery(id+"F10.boolean.opBoolean","MERGE",FACE,{"derivedFrom":[makeQuery(id+"F9.boolean.opBoolean","MERGE",FACE,{"derivedFrom":[makeQuery(id+"F8.boolean.opBoolean","MERGE",FACE,{"derivedFrom":[makeQuery(id+"F7.boolean.opBoolean","MERGE",FACE,{"derivedFrom":[makeQuery(id+"F6.boolean.opBoolean","MERGE",FACE,{"derivedFrom":[makeQuery(id+"F5.boolean.opBoolean","MERGE",FACE,{"derivedFrom":[makeQuery(id+"F1.opRevolve","SWEPT_FACE",FACE,{"disambiguationData":[OSD([sQuery(id+"F0.wireOp",EDGE,"E5")])]}),makeQuery(id+"F5.opLoft","CAP_FACE",FACE,{"disambiguationData":[OSD([makeQuery(id+"F4.imprint","IMPRINT",FACE,{"disambiguationData":[TD([[makeQuery(id+"F4.imprint","IMPRINT",EDGE,{"derivedFrom":sQuery(id+"F4.wireOp",EDGE,"E21")}),1.0]])]})])],"isStart":true})]}),makeQuery(id+"F6.opLoft","CAP_FACE",FACE,{"disambiguationData":[OSD([makeQuery(id+"F4.imprint","IMPRINT",FACE,{"disambiguationData":[TD([[makeQuery(id+"F4.imprint","IMPRINT",EDGE,{"derivedFrom":sQuery(id+"F4.wireOp",EDGE,"E26.15.0")}),1.0]])]})])],"isStart":true})]}),makeQuery(id+"F7.opLoft","CAP_FACE",FACE,{"disambiguationData":[OSD([makeQuery(id+"F4.imprint","IMPRINT",FACE,{"disambiguationData":[TD([[makeQuery(id+"F4.imprint","IMPRINT",EDGE,{"derivedFrom":sQuery(id+"F4.wireOp",EDGE,"E26.14.0")}),1.0]])]})])],"isStart":true})]}),makeQuery(id+"F8.opLoft","CAP_FACE",FACE,{"disambiguationData":[OSD([makeQuery(id+"F4.imprint","IMPRINT",FACE,{"disambiguationData":[TD([[makeQuery(id+"F4.imprint","IMPRINT",EDGE,{"derivedFrom":sQuery(id+"F4.wireOp",EDGE,"E26.13.0")}),1.0]])]})])],"isStart":true})]}),makeQuery(id+"F9.opLoft","CAP_FACE",FACE,{"disambiguationData":[OSD([makeQuery(id+"F4.imprint","IMPRINT",FACE,{"disambiguationData":[TD([[makeQuery(id+"F4.imprint","IMPRINT",EDGE,{"derivedFrom":sQuery(id+"F4.wireOp",EDGE,"E26.12.0")}),1.0]])]})])],"isStart":true})]}),makeQuery(id+"F10.opLoft","CAP_FACE",FACE,{"disambiguationData":[OSD([makeQuery(id+"F4.imprint","IMPRINT",FACE,{"disambiguationData":[TD([[makeQuery(id+"F4.imprint","IMPRINT",EDGE,{"derivedFrom":sQuery(id+"F4.wireOp",EDGE,"E26.11.0")}),1.0]])]})])],"isStart":true})]}),makeQuery(id+"F11.opLoft","CAP_FACE",FACE,{"disambiguationData":[OSD([makeQuery(id+"F4.imprint","IMPRINT",FACE,{"disambiguationData":[TD([[makeQuery(id+"F4.imprint","IMPRINT",EDGE,{"derivedFrom":sQuery(id+"F4.wireOp",EDGE,"E26.10.0")}),1.0]])]})])],"isStart":true})]}),makeQuery(id+"F12.opLoft","CAP_FACE",FACE,{"disambiguationData":[OSD([makeQuery(id+"F4.imprint","IMPRINT",FACE,{"disambiguationData":[TD([[makeQuery(id+"F4.imprint","IMPRINT",EDGE,{"derivedFrom":sQuery(id+"F4.wireOp",EDGE,"E26.9.0")}),1.0]])]})])],"isStart":true})]}),makeQuery(id+"F13.opLoft","CAP_FACE",FACE,{"disambiguationData":[OSD([makeQuery(id+"F4.imprint","IMPRINT",FACE,{"disambiguationData":[TD([[makeQuery(id+"F4.imprint","IMPRINT",EDGE,{"derivedFrom":sQuery(id+"F4.wireOp",EDGE,"E26.8.0")}),1.0]])]})])],"isStart":true})]}),makeQuery(id+"F14.opLoft","CAP_FACE",FACE,{"disambiguationData":[OSD([makeQuery(id+"F4.imprint","IMPRINT",FACE,{"disambiguationData":[TD([[makeQuery(id+"F4.imprint","IMPRINT",EDGE,{"derivedFrom":sQuery(id+"F4.wireOp",EDGE,"E26.7.0")}),1.0]])]})])],"isStart":true})]}),makeQuery(id+"F15.opLoft","CAP_FACE",FACE,{"disambiguationData":[OSD([makeQuery(id+"F4.imprint","IMPRINT",FACE,{"disambiguationData":[TD([[makeQuery(id+"F4.imprint","IMPRINT",EDGE,{"derivedFrom":sQuery(id+"F4.wireOp",EDGE,"E26.6.0")}),1.0]])]})])],"isStart":true})]}),makeQuery(id+"F16.opLoft","CAP_FACE",FACE,{"disambiguationData":[OSD([makeQuery(id+"F4.imprint","IMPRINT",FACE,{"disambiguationData":[TD([[makeQuery(id+"F4.imprint","IMPRINT",EDGE,{"derivedFrom":sQuery(id+"F4.wireOp",EDGE,"E26.5.0")}),1.0]])]})])],"isStart":true})]}),makeQuery(id+"F17.opLoft","CAP_FACE",FACE,{"disambiguationData":[OSD([makeQuery(id+"F4.imprint","IMPRINT",FACE,{"disambiguationData":[TD([[makeQuery(id+"F4.imprint","IMPRINT",EDGE,{"derivedFrom":sQuery(id+"F4.wireOp",EDGE,"E26.4.0")}),1.0]])]})])],"isStart":true})]}),makeQuery(id+"F18.opLoft","CAP_FACE",FACE,{"disambiguationData":[OSD([makeQuery(id+"F4.imprint","IMPRINT",FACE,{"disambiguationData":[TD([[makeQuery(id+"F4.imprint","IMPRINT",EDGE,{"derivedFrom":sQuery(id+"F4.wireOp",EDGE,"E26.3.0")}),1.0]])]})])],"isStart":true})]}),makeQuery(id+"F19.opLoft","CAP_FACE",FACE,{"disambiguationData":[OSD([makeQuery(id+"F4.imprint","IMPRINT",FACE,{"disambiguationData":[TD([[makeQuery(id+"F4.imprint","IMPRINT",EDGE,{"derivedFrom":sQuery(id+"F4.wireOp",EDGE,"E26.2.0")}),1.0]])]})])],"isStart":true})]}),makeQuery(id+"F20.opLoft","CAP_FACE",FACE,{"disambiguationData":[OSD([makeQuery(id+"F4.imprint","IMPRINT",FACE,{"disambiguationData":[TD([[makeQuery(id+"F4.imprint","IMPRINT",EDGE,{"derivedFrom":sQuery(id+"F4.wireOp",EDGE,"E26.1.0")}),1.0]])]})])],"isStart":true})]}),makeQuery(id+"F42.opRevolve","SWEPT_FACE",FACE,{"disambiguationData":[OSD([sQuery(id+"F41.wireOp",EDGE,"E32")])]})]});
            var Q4;
            Q4=makeQuery(id+"F42.boolean.opBoolean","INTERSECT",EDGE,{"disambiguationData":[OD(1.0)],"derivedFrom":[makeQuery(id+"F20.boolean.opBoolean","MERGE",FACE,{"derivedFrom":[makeQuery(id+"F19.boolean.opBoolean","MERGE",FACE,{"derivedFrom":[makeQuery(id+"F18.boolean.opBoolean","MERGE",FACE,{"derivedFrom":[makeQuery(id+"F17.boolean.opBoolean","MERGE",FACE,{"derivedFrom":[makeQuery(id+"F16.boolean.opBoolean","MERGE",FACE,{"derivedFrom":[makeQuery(id+"F15.boolean.opBoolean","MERGE",FACE,{"derivedFrom":[makeQuery(id+"F14.boolean.opBoolean","MERGE",FACE,{"derivedFrom":[makeQuery(id+"F13.boolean.opBoolean","MERGE",FACE,{"derivedFrom":[makeQuery(id+"F12.boolean.opBoolean","MERGE",FACE,{"derivedFrom":[makeQuery(id+"F11.boolean.opBoolean","MERGE",FACE,{"derivedFrom":[makeQuery(id+"F10.boolean.opBoolean","MERGE",FACE,{"derivedFrom":[makeQuery(id+"F9.boolean.opBoolean","MERGE",FACE,{"derivedFrom":[makeQuery(id+"F8.boolean.opBoolean","MERGE",FACE,{"derivedFrom":[makeQuery(id+"F7.boolean.opBoolean","MERGE",FACE,{"derivedFrom":[makeQuery(id+"F6.boolean.opBoolean","MERGE",FACE,{"derivedFrom":[makeQuery(id+"F5.boolean.opBoolean","MERGE",FACE,{"derivedFrom":[makeQuery(id+"F1.opRevolve","SWEPT_FACE",FACE,{"disambiguationData":[OSD([sQuery(id+"F0.wireOp",EDGE,"E5")])]}),makeQuery(id+"F5.opLoft","CAP_FACE",FACE,{"disambiguationData":[OSD([makeQuery(id+"F4.imprint","IMPRINT",FACE,{"disambiguationData":[TD([[makeQuery(id+"F4.imprint","IMPRINT",EDGE,{"derivedFrom":sQuery(id+"F4.wireOp",EDGE,"E21")}),1.0]])]})])],"isStart":true})]}),makeQuery(id+"F6.opLoft","CAP_FACE",FACE,{"disambiguationData":[OSD([makeQuery(id+"F4.imprint","IMPRINT",FACE,{"disambiguationData":[TD([[makeQuery(id+"F4.imprint","IMPRINT",EDGE,{"derivedFrom":sQuery(id+"F4.wireOp",EDGE,"E26.15.0")}),1.0]])]})])],"isStart":true})]}),makeQuery(id+"F7.opLoft","CAP_FACE",FACE,{"disambiguationData":[OSD([makeQuery(id+"F4.imprint","IMPRINT",FACE,{"disambiguationData":[TD([[makeQuery(id+"F4.imprint","IMPRINT",EDGE,{"derivedFrom":sQuery(id+"F4.wireOp",EDGE,"E26.14.0")}),1.0]])]})])],"isStart":true})]}),makeQuery(id+"F8.opLoft","CAP_FACE",FACE,{"disambiguationData":[OSD([makeQuery(id+"F4.imprint","IMPRINT",FACE,{"disambiguationData":[TD([[makeQuery(id+"F4.imprint","IMPRINT",EDGE,{"derivedFrom":sQuery(id+"F4.wireOp",EDGE,"E26.13.0")}),1.0]])]})])],"isStart":true})]}),makeQuery(id+"F9.opLoft","CAP_FACE",FACE,{"disambiguationData":[OSD([makeQuery(id+"F4.imprint","IMPRINT",FACE,{"disambiguationData":[TD([[makeQuery(id+"F4.imprint","IMPRINT",EDGE,{"derivedFrom":sQuery(id+"F4.wireOp",EDGE,"E26.12.0")}),1.0]])]})])],"isStart":true})]}),makeQuery(id+"F10.opLoft","CAP_FACE",FACE,{"disambiguationData":[OSD([makeQuery(id+"F4.imprint","IMPRINT",FACE,{"disambiguationData":[TD([[makeQuery(id+"F4.imprint","IMPRINT",EDGE,{"derivedFrom":sQuery(id+"F4.wireOp",EDGE,"E26.11.0")}),1.0]])]})])],"isStart":true})]}),makeQuery(id+"F11.opLoft","CAP_FACE",FACE,{"disambiguationData":[OSD([makeQuery(id+"F4.imprint","IMPRINT",FACE,{"disambiguationData":[TD([[makeQuery(id+"F4.imprint","IMPRINT",EDGE,{"derivedFrom":sQuery(id+"F4.wireOp",EDGE,"E26.10.0")}),1.0]])]})])],"isStart":true})]}),makeQuery(id+"F12.opLoft","CAP_FACE",FACE,{"disambiguationData":[OSD([makeQuery(id+"F4.imprint","IMPRINT",FACE,{"disambiguationData":[TD([[makeQuery(id+"F4.imprint","IMPRINT",EDGE,{"derivedFrom":sQuery(id+"F4.wireOp",EDGE,"E26.9.0")}),1.0]])]})])],"isStart":true})]}),makeQuery(id+"F13.opLoft","CAP_FACE",FACE,{"disambiguationData":[OSD([makeQuery(id+"F4.imprint","IMPRINT",FACE,{"disambiguationData":[TD([[makeQuery(id+"F4.imprint","IMPRINT",EDGE,{"derivedFrom":sQuery(id+"F4.wireOp",EDGE,"E26.8.0")}),1.0]])]})])],"isStart":true})]}),makeQuery(id+"F14.opLoft","CAP_FACE",FACE,{"disambiguationData":[OSD([makeQuery(id+"F4.imprint","IMPRINT",FACE,{"disambiguationData":[TD([[makeQuery(id+"F4.imprint","IMPRINT",EDGE,{"derivedFrom":sQuery(id+"F4.wireOp",EDGE,"E26.7.0")}),1.0]])]})])],"isStart":true})]}),makeQuery(id+"F15.opLoft","CAP_FACE",FACE,{"disambiguationData":[OSD([makeQuery(id+"F4.imprint","IMPRINT",FACE,{"disambiguationData":[TD([[makeQuery(id+"F4.imprint","IMPRINT",EDGE,{"derivedFrom":sQuery(id+"F4.wireOp",EDGE,"E26.6.0")}),1.0]])]})])],"isStart":true})]}),makeQuery(id+"F16.opLoft","CAP_FACE",FACE,{"disambiguationData":[OSD([makeQuery(id+"F4.imprint","IMPRINT",FACE,{"disambiguationData":[TD([[makeQuery(id+"F4.imprint","IMPRINT",EDGE,{"derivedFrom":sQuery(id+"F4.wireOp",EDGE,"E26.5.0")}),1.0]])]})])],"isStart":true})]}),makeQuery(id+"F17.opLoft","CAP_FACE",FACE,{"disambiguationData":[OSD([makeQuery(id+"F4.imprint","IMPRINT",FACE,{"disambiguationData":[TD([[makeQuery(id+"F4.imprint","IMPRINT",EDGE,{"derivedFrom":sQuery(id+"F4.wireOp",EDGE,"E26.4.0")}),1.0]])]})])],"isStart":true})]}),makeQuery(id+"F18.opLoft","CAP_FACE",FACE,{"disambiguationData":[OSD([makeQuery(id+"F4.imprint","IMPRINT",FACE,{"disambiguationData":[TD([[makeQuery(id+"F4.imprint","IMPRINT",EDGE,{"derivedFrom":sQuery(id+"F4.wireOp",EDGE,"E26.3.0")}),1.0]])]})])],"isStart":true})]}),makeQuery(id+"F19.opLoft","CAP_FACE",FACE,{"disambiguationData":[OSD([makeQuery(id+"F4.imprint","IMPRINT",FACE,{"disambiguationData":[TD([[makeQuery(id+"F4.imprint","IMPRINT",EDGE,{"derivedFrom":sQuery(id+"F4.wireOp",EDGE,"E26.2.0")}),1.0]])]})])],"isStart":true})]}),makeQuery(id+"F20.opLoft","CAP_FACE",FACE,{"disambiguationData":[OSD([makeQuery(id+"F4.imprint","IMPRINT",FACE,{"disambiguationData":[TD([[makeQuery(id+"F4.imprint","IMPRINT",EDGE,{"derivedFrom":sQuery(id+"F4.wireOp",EDGE,"E26.1.0")}),1.0]])]})])],"isStart":true})]}),makeQuery(id+"F42.opRevolve","SWEPT_FACE",FACE,{"disambiguationData":[OSD([sQuery(id+"F41.wireOp",EDGE,"E32")])]})]});
            var Q5;
            Q5=makeQuery(id+"F42.boolean.opBoolean","INTERSECT",EDGE,{"disambiguationData":[OD(0.0)],"derivedFrom":[makeQuery(id+"F20.boolean.opBoolean","MERGE",FACE,{"derivedFrom":[makeQuery(id+"F19.boolean.opBoolean","MERGE",FACE,{"derivedFrom":[makeQuery(id+"F18.boolean.opBoolean","MERGE",FACE,{"derivedFrom":[makeQuery(id+"F17.boolean.opBoolean","MERGE",FACE,{"derivedFrom":[makeQuery(id+"F16.boolean.opBoolean","MERGE",FACE,{"derivedFrom":[makeQuery(id+"F15.boolean.opBoolean","MERGE",FACE,{"derivedFrom":[makeQuery(id+"F14.boolean.opBoolean","MERGE",FACE,{"derivedFrom":[makeQuery(id+"F13.boolean.opBoolean","MERGE",FACE,{"derivedFrom":[makeQuery(id+"F12.boolean.opBoolean","MERGE",FACE,{"derivedFrom":[makeQuery(id+"F11.boolean.opBoolean","MERGE",FACE,{"derivedFrom":[makeQuery(id+"F10.boolean.opBoolean","MERGE",FACE,{"derivedFrom":[makeQuery(id+"F9.boolean.opBoolean","MERGE",FACE,{"derivedFrom":[makeQuery(id+"F8.boolean.opBoolean","MERGE",FACE,{"derivedFrom":[makeQuery(id+"F7.boolean.opBoolean","MERGE",FACE,{"derivedFrom":[makeQuery(id+"F6.boolean.opBoolean","MERGE",FACE,{"derivedFrom":[makeQuery(id+"F5.boolean.opBoolean","MERGE",FACE,{"derivedFrom":[makeQuery(id+"F1.opRevolve","SWEPT_FACE",FACE,{"disambiguationData":[OSD([sQuery(id+"F0.wireOp",EDGE,"E5")])]}),makeQuery(id+"F5.opLoft","CAP_FACE",FACE,{"disambiguationData":[OSD([makeQuery(id+"F4.imprint","IMPRINT",FACE,{"disambiguationData":[TD([[makeQuery(id+"F4.imprint","IMPRINT",EDGE,{"derivedFrom":sQuery(id+"F4.wireOp",EDGE,"E21")}),1.0]])]})])],"isStart":true})]}),makeQuery(id+"F6.opLoft","CAP_FACE",FACE,{"disambiguationData":[OSD([makeQuery(id+"F4.imprint","IMPRINT",FACE,{"disambiguationData":[TD([[makeQuery(id+"F4.imprint","IMPRINT",EDGE,{"derivedFrom":sQuery(id+"F4.wireOp",EDGE,"E26.15.0")}),1.0]])]})])],"isStart":true})]}),makeQuery(id+"F7.opLoft","CAP_FACE",FACE,{"disambiguationData":[OSD([makeQuery(id+"F4.imprint","IMPRINT",FACE,{"disambiguationData":[TD([[makeQuery(id+"F4.imprint","IMPRINT",EDGE,{"derivedFrom":sQuery(id+"F4.wireOp",EDGE,"E26.14.0")}),1.0]])]})])],"isStart":true})]}),makeQuery(id+"F8.opLoft","CAP_FACE",FACE,{"disambiguationData":[OSD([makeQuery(id+"F4.imprint","IMPRINT",FACE,{"disambiguationData":[TD([[makeQuery(id+"F4.imprint","IMPRINT",EDGE,{"derivedFrom":sQuery(id+"F4.wireOp",EDGE,"E26.13.0")}),1.0]])]})])],"isStart":true})]}),makeQuery(id+"F9.opLoft","CAP_FACE",FACE,{"disambiguationData":[OSD([makeQuery(id+"F4.imprint","IMPRINT",FACE,{"disambiguationData":[TD([[makeQuery(id+"F4.imprint","IMPRINT",EDGE,{"derivedFrom":sQuery(id+"F4.wireOp",EDGE,"E26.12.0")}),1.0]])]})])],"isStart":true})]}),makeQuery(id+"F10.opLoft","CAP_FACE",FACE,{"disambiguationData":[OSD([makeQuery(id+"F4.imprint","IMPRINT",FACE,{"disambiguationData":[TD([[makeQuery(id+"F4.imprint","IMPRINT",EDGE,{"derivedFrom":sQuery(id+"F4.wireOp",EDGE,"E26.11.0")}),1.0]])]})])],"isStart":true})]}),makeQuery(id+"F11.opLoft","CAP_FACE",FACE,{"disambiguationData":[OSD([makeQuery(id+"F4.imprint","IMPRINT",FACE,{"disambiguationData":[TD([[makeQuery(id+"F4.imprint","IMPRINT",EDGE,{"derivedFrom":sQuery(id+"F4.wireOp",EDGE,"E26.10.0")}),1.0]])]})])],"isStart":true})]}),makeQuery(id+"F12.opLoft","CAP_FACE",FACE,{"disambiguationData":[OSD([makeQuery(id+"F4.imprint","IMPRINT",FACE,{"disambiguationData":[TD([[makeQuery(id+"F4.imprint","IMPRINT",EDGE,{"derivedFrom":sQuery(id+"F4.wireOp",EDGE,"E26.9.0")}),1.0]])]})])],"isStart":true})]}),makeQuery(id+"F13.opLoft","CAP_FACE",FACE,{"disambiguationData":[OSD([makeQuery(id+"F4.imprint","IMPRINT",FACE,{"disambiguationData":[TD([[makeQuery(id+"F4.imprint","IMPRINT",EDGE,{"derivedFrom":sQuery(id+"F4.wireOp",EDGE,"E26.8.0")}),1.0]])]})])],"isStart":true})]}),makeQuery(id+"F14.opLoft","CAP_FACE",FACE,{"disambiguationData":[OSD([makeQuery(id+"F4.imprint","IMPRINT",FACE,{"disambiguationData":[TD([[makeQuery(id+"F4.imprint","IMPRINT",EDGE,{"derivedFrom":sQuery(id+"F4.wireOp",EDGE,"E26.7.0")}),1.0]])]})])],"isStart":true})]}),makeQuery(id+"F15.opLoft","CAP_FACE",FACE,{"disambiguationData":[OSD([makeQuery(id+"F4.imprint","IMPRINT",FACE,{"disambiguationData":[TD([[makeQuery(id+"F4.imprint","IMPRINT",EDGE,{"derivedFrom":sQuery(id+"F4.wireOp",EDGE,"E26.6.0")}),1.0]])]})])],"isStart":true})]}),makeQuery(id+"F16.opLoft","CAP_FACE",FACE,{"disambiguationData":[OSD([makeQuery(id+"F4.imprint","IMPRINT",FACE,{"disambiguationData":[TD([[makeQuery(id+"F4.imprint","IMPRINT",EDGE,{"derivedFrom":sQuery(id+"F4.wireOp",EDGE,"E26.5.0")}),1.0]])]})])],"isStart":true})]}),makeQuery(id+"F17.opLoft","CAP_FACE",FACE,{"disambiguationData":[OSD([makeQuery(id+"F4.imprint","IMPRINT",FACE,{"disambiguationData":[TD([[makeQuery(id+"F4.imprint","IMPRINT",EDGE,{"derivedFrom":sQuery(id+"F4.wireOp",EDGE,"E26.4.0")}),1.0]])]})])],"isStart":true})]}),makeQuery(id+"F18.opLoft","CAP_FACE",FACE,{"disambiguationData":[OSD([makeQuery(id+"F4.imprint","IMPRINT",FACE,{"disambiguationData":[TD([[makeQuery(id+"F4.imprint","IMPRINT",EDGE,{"derivedFrom":sQuery(id+"F4.wireOp",EDGE,"E26.3.0")}),1.0]])]})])],"isStart":true})]}),makeQuery(id+"F19.opLoft","CAP_FACE",FACE,{"disambiguationData":[OSD([makeQuery(id+"F4.imprint","IMPRINT",FACE,{"disambiguationData":[TD([[makeQuery(id+"F4.imprint","IMPRINT",EDGE,{"derivedFrom":sQuery(id+"F4.wireOp",EDGE,"E26.2.0")}),1.0]])]})])],"isStart":true})]}),makeQuery(id+"F20.opLoft","CAP_FACE",FACE,{"disambiguationData":[OSD([makeQuery(id+"F4.imprint","IMPRINT",FACE,{"disambiguationData":[TD([[makeQuery(id+"F4.imprint","IMPRINT",EDGE,{"derivedFrom":sQuery(id+"F4.wireOp",EDGE,"E26.1.0")}),1.0]])]})])],"isStart":true})]}),makeQuery(id+"F42.opRevolve","SWEPT_FACE",FACE,{"disambiguationData":[OSD([sQuery(id+"F41.wireOp",EDGE,"E32")])]})]});
            var Q6;
            Q6=makeQuery(id+"F42.boolean.opBoolean","INTERSECT",EDGE,{"disambiguationData":[OD(15.0)],"derivedFrom":[makeQuery(id+"F20.boolean.opBoolean","MERGE",FACE,{"derivedFrom":[makeQuery(id+"F19.boolean.opBoolean","MERGE",FACE,{"derivedFrom":[makeQuery(id+"F18.boolean.opBoolean","MERGE",FACE,{"derivedFrom":[makeQuery(id+"F17.boolean.opBoolean","MERGE",FACE,{"derivedFrom":[makeQuery(id+"F16.boolean.opBoolean","MERGE",FACE,{"derivedFrom":[makeQuery(id+"F15.boolean.opBoolean","MERGE",FACE,{"derivedFrom":[makeQuery(id+"F14.boolean.opBoolean","MERGE",FACE,{"derivedFrom":[makeQuery(id+"F13.boolean.opBoolean","MERGE",FACE,{"derivedFrom":[makeQuery(id+"F12.boolean.opBoolean","MERGE",FACE,{"derivedFrom":[makeQuery(id+"F11.boolean.opBoolean","MERGE",FACE,{"derivedFrom":[makeQuery(id+"F10.boolean.opBoolean","MERGE",FACE,{"derivedFrom":[makeQuery(id+"F9.boolean.opBoolean","MERGE",FACE,{"derivedFrom":[makeQuery(id+"F8.boolean.opBoolean","MERGE",FACE,{"derivedFrom":[makeQuery(id+"F7.boolean.opBoolean","MERGE",FACE,{"derivedFrom":[makeQuery(id+"F6.boolean.opBoolean","MERGE",FACE,{"derivedFrom":[makeQuery(id+"F5.boolean.opBoolean","MERGE",FACE,{"derivedFrom":[makeQuery(id+"F1.opRevolve","SWEPT_FACE",FACE,{"disambiguationData":[OSD([sQuery(id+"F0.wireOp",EDGE,"E5")])]}),makeQuery(id+"F5.opLoft","CAP_FACE",FACE,{"disambiguationData":[OSD([makeQuery(id+"F4.imprint","IMPRINT",FACE,{"disambiguationData":[TD([[makeQuery(id+"F4.imprint","IMPRINT",EDGE,{"derivedFrom":sQuery(id+"F4.wireOp",EDGE,"E21")}),1.0]])]})])],"isStart":true})]}),makeQuery(id+"F6.opLoft","CAP_FACE",FACE,{"disambiguationData":[OSD([makeQuery(id+"F4.imprint","IMPRINT",FACE,{"disambiguationData":[TD([[makeQuery(id+"F4.imprint","IMPRINT",EDGE,{"derivedFrom":sQuery(id+"F4.wireOp",EDGE,"E26.15.0")}),1.0]])]})])],"isStart":true})]}),makeQuery(id+"F7.opLoft","CAP_FACE",FACE,{"disambiguationData":[OSD([makeQuery(id+"F4.imprint","IMPRINT",FACE,{"disambiguationData":[TD([[makeQuery(id+"F4.imprint","IMPRINT",EDGE,{"derivedFrom":sQuery(id+"F4.wireOp",EDGE,"E26.14.0")}),1.0]])]})])],"isStart":true})]}),makeQuery(id+"F8.opLoft","CAP_FACE",FACE,{"disambiguationData":[OSD([makeQuery(id+"F4.imprint","IMPRINT",FACE,{"disambiguationData":[TD([[makeQuery(id+"F4.imprint","IMPRINT",EDGE,{"derivedFrom":sQuery(id+"F4.wireOp",EDGE,"E26.13.0")}),1.0]])]})])],"isStart":true})]}),makeQuery(id+"F9.opLoft","CAP_FACE",FACE,{"disambiguationData":[OSD([makeQuery(id+"F4.imprint","IMPRINT",FACE,{"disambiguationData":[TD([[makeQuery(id+"F4.imprint","IMPRINT",EDGE,{"derivedFrom":sQuery(id+"F4.wireOp",EDGE,"E26.12.0")}),1.0]])]})])],"isStart":true})]}),makeQuery(id+"F10.opLoft","CAP_FACE",FACE,{"disambiguationData":[OSD([makeQuery(id+"F4.imprint","IMPRINT",FACE,{"disambiguationData":[TD([[makeQuery(id+"F4.imprint","IMPRINT",EDGE,{"derivedFrom":sQuery(id+"F4.wireOp",EDGE,"E26.11.0")}),1.0]])]})])],"isStart":true})]}),makeQuery(id+"F11.opLoft","CAP_FACE",FACE,{"disambiguationData":[OSD([makeQuery(id+"F4.imprint","IMPRINT",FACE,{"disambiguationData":[TD([[makeQuery(id+"F4.imprint","IMPRINT",EDGE,{"derivedFrom":sQuery(id+"F4.wireOp",EDGE,"E26.10.0")}),1.0]])]})])],"isStart":true})]}),makeQuery(id+"F12.opLoft","CAP_FACE",FACE,{"disambiguationData":[OSD([makeQuery(id+"F4.imprint","IMPRINT",FACE,{"disambiguationData":[TD([[makeQuery(id+"F4.imprint","IMPRINT",EDGE,{"derivedFrom":sQuery(id+"F4.wireOp",EDGE,"E26.9.0")}),1.0]])]})])],"isStart":true})]}),makeQuery(id+"F13.opLoft","CAP_FACE",FACE,{"disambiguationData":[OSD([makeQuery(id+"F4.imprint","IMPRINT",FACE,{"disambiguationData":[TD([[makeQuery(id+"F4.imprint","IMPRINT",EDGE,{"derivedFrom":sQuery(id+"F4.wireOp",EDGE,"E26.8.0")}),1.0]])]})])],"isStart":true})]}),makeQuery(id+"F14.opLoft","CAP_FACE",FACE,{"disambiguationData":[OSD([makeQuery(id+"F4.imprint","IMPRINT",FACE,{"disambiguationData":[TD([[makeQuery(id+"F4.imprint","IMPRINT",EDGE,{"derivedFrom":sQuery(id+"F4.wireOp",EDGE,"E26.7.0")}),1.0]])]})])],"isStart":true})]}),makeQuery(id+"F15.opLoft","CAP_FACE",FACE,{"disambiguationData":[OSD([makeQuery(id+"F4.imprint","IMPRINT",FACE,{"disambiguationData":[TD([[makeQuery(id+"F4.imprint","IMPRINT",EDGE,{"derivedFrom":sQuery(id+"F4.wireOp",EDGE,"E26.6.0")}),1.0]])]})])],"isStart":true})]}),makeQuery(id+"F16.opLoft","CAP_FACE",FACE,{"disambiguationData":[OSD([makeQuery(id+"F4.imprint","IMPRINT",FACE,{"disambiguationData":[TD([[makeQuery(id+"F4.imprint","IMPRINT",EDGE,{"derivedFrom":sQuery(id+"F4.wireOp",EDGE,"E26.5.0")}),1.0]])]})])],"isStart":true})]}),makeQuery(id+"F17.opLoft","CAP_FACE",FACE,{"disambiguationData":[OSD([makeQuery(id+"F4.imprint","IMPRINT",FACE,{"disambiguationData":[TD([[makeQuery(id+"F4.imprint","IMPRINT",EDGE,{"derivedFrom":sQuery(id+"F4.wireOp",EDGE,"E26.4.0")}),1.0]])]})])],"isStart":true})]}),makeQuery(id+"F18.opLoft","CAP_FACE",FACE,{"disambiguationData":[OSD([makeQuery(id+"F4.imprint","IMPRINT",FACE,{"disambiguationData":[TD([[makeQuery(id+"F4.imprint","IMPRINT",EDGE,{"derivedFrom":sQuery(id+"F4.wireOp",EDGE,"E26.3.0")}),1.0]])]})])],"isStart":true})]}),makeQuery(id+"F19.opLoft","CAP_FACE",FACE,{"disambiguationData":[OSD([makeQuery(id+"F4.imprint","IMPRINT",FACE,{"disambiguationData":[TD([[makeQuery(id+"F4.imprint","IMPRINT",EDGE,{"derivedFrom":sQuery(id+"F4.wireOp",EDGE,"E26.2.0")}),1.0]])]})])],"isStart":true})]}),makeQuery(id+"F20.opLoft","CAP_FACE",FACE,{"disambiguationData":[OSD([makeQuery(id+"F4.imprint","IMPRINT",FACE,{"disambiguationData":[TD([[makeQuery(id+"F4.imprint","IMPRINT",EDGE,{"derivedFrom":sQuery(id+"F4.wireOp",EDGE,"E26.1.0")}),1.0]])]})])],"isStart":true})]}),makeQuery(id+"F42.opRevolve","SWEPT_FACE",FACE,{"disambiguationData":[OSD([sQuery(id+"F41.wireOp",EDGE,"E32")])]})]});
            var Q7;
            Q7=makeQuery(id+"F42.boolean.opBoolean","INTERSECT",EDGE,{"disambiguationData":[OD(14.0)],"derivedFrom":[makeQuery(id+"F20.boolean.opBoolean","MERGE",FACE,{"derivedFrom":[makeQuery(id+"F19.boolean.opBoolean","MERGE",FACE,{"derivedFrom":[makeQuery(id+"F18.boolean.opBoolean","MERGE",FACE,{"derivedFrom":[makeQuery(id+"F17.boolean.opBoolean","MERGE",FACE,{"derivedFrom":[makeQuery(id+"F16.boolean.opBoolean","MERGE",FACE,{"derivedFrom":[makeQuery(id+"F15.boolean.opBoolean","MERGE",FACE,{"derivedFrom":[makeQuery(id+"F14.boolean.opBoolean","MERGE",FACE,{"derivedFrom":[makeQuery(id+"F13.boolean.opBoolean","MERGE",FACE,{"derivedFrom":[makeQuery(id+"F12.boolean.opBoolean","MERGE",FACE,{"derivedFrom":[makeQuery(id+"F11.boolean.opBoolean","MERGE",FACE,{"derivedFrom":[makeQuery(id+"F10.boolean.opBoolean","MERGE",FACE,{"derivedFrom":[makeQuery(id+"F9.boolean.opBoolean","MERGE",FACE,{"derivedFrom":[makeQuery(id+"F8.boolean.opBoolean","MERGE",FACE,{"derivedFrom":[makeQuery(id+"F7.boolean.opBoolean","MERGE",FACE,{"derivedFrom":[makeQuery(id+"F6.boolean.opBoolean","MERGE",FACE,{"derivedFrom":[makeQuery(id+"F5.boolean.opBoolean","MERGE",FACE,{"derivedFrom":[makeQuery(id+"F1.opRevolve","SWEPT_FACE",FACE,{"disambiguationData":[OSD([sQuery(id+"F0.wireOp",EDGE,"E5")])]}),makeQuery(id+"F5.opLoft","CAP_FACE",FACE,{"disambiguationData":[OSD([makeQuery(id+"F4.imprint","IMPRINT",FACE,{"disambiguationData":[TD([[makeQuery(id+"F4.imprint","IMPRINT",EDGE,{"derivedFrom":sQuery(id+"F4.wireOp",EDGE,"E21")}),1.0]])]})])],"isStart":true})]}),makeQuery(id+"F6.opLoft","CAP_FACE",FACE,{"disambiguationData":[OSD([makeQuery(id+"F4.imprint","IMPRINT",FACE,{"disambiguationData":[TD([[makeQuery(id+"F4.imprint","IMPRINT",EDGE,{"derivedFrom":sQuery(id+"F4.wireOp",EDGE,"E26.15.0")}),1.0]])]})])],"isStart":true})]}),makeQuery(id+"F7.opLoft","CAP_FACE",FACE,{"disambiguationData":[OSD([makeQuery(id+"F4.imprint","IMPRINT",FACE,{"disambiguationData":[TD([[makeQuery(id+"F4.imprint","IMPRINT",EDGE,{"derivedFrom":sQuery(id+"F4.wireOp",EDGE,"E26.14.0")}),1.0]])]})])],"isStart":true})]}),makeQuery(id+"F8.opLoft","CAP_FACE",FACE,{"disambiguationData":[OSD([makeQuery(id+"F4.imprint","IMPRINT",FACE,{"disambiguationData":[TD([[makeQuery(id+"F4.imprint","IMPRINT",EDGE,{"derivedFrom":sQuery(id+"F4.wireOp",EDGE,"E26.13.0")}),1.0]])]})])],"isStart":true})]}),makeQuery(id+"F9.opLoft","CAP_FACE",FACE,{"disambiguationData":[OSD([makeQuery(id+"F4.imprint","IMPRINT",FACE,{"disambiguationData":[TD([[makeQuery(id+"F4.imprint","IMPRINT",EDGE,{"derivedFrom":sQuery(id+"F4.wireOp",EDGE,"E26.12.0")}),1.0]])]})])],"isStart":true})]}),makeQuery(id+"F10.opLoft","CAP_FACE",FACE,{"disambiguationData":[OSD([makeQuery(id+"F4.imprint","IMPRINT",FACE,{"disambiguationData":[TD([[makeQuery(id+"F4.imprint","IMPRINT",EDGE,{"derivedFrom":sQuery(id+"F4.wireOp",EDGE,"E26.11.0")}),1.0]])]})])],"isStart":true})]}),makeQuery(id+"F11.opLoft","CAP_FACE",FACE,{"disambiguationData":[OSD([makeQuery(id+"F4.imprint","IMPRINT",FACE,{"disambiguationData":[TD([[makeQuery(id+"F4.imprint","IMPRINT",EDGE,{"derivedFrom":sQuery(id+"F4.wireOp",EDGE,"E26.10.0")}),1.0]])]})])],"isStart":true})]}),makeQuery(id+"F12.opLoft","CAP_FACE",FACE,{"disambiguationData":[OSD([makeQuery(id+"F4.imprint","IMPRINT",FACE,{"disambiguationData":[TD([[makeQuery(id+"F4.imprint","IMPRINT",EDGE,{"derivedFrom":sQuery(id+"F4.wireOp",EDGE,"E26.9.0")}),1.0]])]})])],"isStart":true})]}),makeQuery(id+"F13.opLoft","CAP_FACE",FACE,{"disambiguationData":[OSD([makeQuery(id+"F4.imprint","IMPRINT",FACE,{"disambiguationData":[TD([[makeQuery(id+"F4.imprint","IMPRINT",EDGE,{"derivedFrom":sQuery(id+"F4.wireOp",EDGE,"E26.8.0")}),1.0]])]})])],"isStart":true})]}),makeQuery(id+"F14.opLoft","CAP_FACE",FACE,{"disambiguationData":[OSD([makeQuery(id+"F4.imprint","IMPRINT",FACE,{"disambiguationData":[TD([[makeQuery(id+"F4.imprint","IMPRINT",EDGE,{"derivedFrom":sQuery(id+"F4.wireOp",EDGE,"E26.7.0")}),1.0]])]})])],"isStart":true})]}),makeQuery(id+"F15.opLoft","CAP_FACE",FACE,{"disambiguationData":[OSD([makeQuery(id+"F4.imprint","IMPRINT",FACE,{"disambiguationData":[TD([[makeQuery(id+"F4.imprint","IMPRINT",EDGE,{"derivedFrom":sQuery(id+"F4.wireOp",EDGE,"E26.6.0")}),1.0]])]})])],"isStart":true})]}),makeQuery(id+"F16.opLoft","CAP_FACE",FACE,{"disambiguationData":[OSD([makeQuery(id+"F4.imprint","IMPRINT",FACE,{"disambiguationData":[TD([[makeQuery(id+"F4.imprint","IMPRINT",EDGE,{"derivedFrom":sQuery(id+"F4.wireOp",EDGE,"E26.5.0")}),1.0]])]})])],"isStart":true})]}),makeQuery(id+"F17.opLoft","CAP_FACE",FACE,{"disambiguationData":[OSD([makeQuery(id+"F4.imprint","IMPRINT",FACE,{"disambiguationData":[TD([[makeQuery(id+"F4.imprint","IMPRINT",EDGE,{"derivedFrom":sQuery(id+"F4.wireOp",EDGE,"E26.4.0")}),1.0]])]})])],"isStart":true})]}),makeQuery(id+"F18.opLoft","CAP_FACE",FACE,{"disambiguationData":[OSD([makeQuery(id+"F4.imprint","IMPRINT",FACE,{"disambiguationData":[TD([[makeQuery(id+"F4.imprint","IMPRINT",EDGE,{"derivedFrom":sQuery(id+"F4.wireOp",EDGE,"E26.3.0")}),1.0]])]})])],"isStart":true})]}),makeQuery(id+"F19.opLoft","CAP_FACE",FACE,{"disambiguationData":[OSD([makeQuery(id+"F4.imprint","IMPRINT",FACE,{"disambiguationData":[TD([[makeQuery(id+"F4.imprint","IMPRINT",EDGE,{"derivedFrom":sQuery(id+"F4.wireOp",EDGE,"E26.2.0")}),1.0]])]})])],"isStart":true})]}),makeQuery(id+"F20.opLoft","CAP_FACE",FACE,{"disambiguationData":[OSD([makeQuery(id+"F4.imprint","IMPRINT",FACE,{"disambiguationData":[TD([[makeQuery(id+"F4.imprint","IMPRINT",EDGE,{"derivedFrom":sQuery(id+"F4.wireOp",EDGE,"E26.1.0")}),1.0]])]})])],"isStart":true})]}),makeQuery(id+"F42.opRevolve","SWEPT_FACE",FACE,{"disambiguationData":[OSD([sQuery(id+"F41.wireOp",EDGE,"E32")])]})]});
            var Q8;
            Q8=makeQuery(id+"F42.boolean.opBoolean","INTERSECT",EDGE,{"disambiguationData":[OD(13.0)],"derivedFrom":[makeQuery(id+"F20.boolean.opBoolean","MERGE",FACE,{"derivedFrom":[makeQuery(id+"F19.boolean.opBoolean","MERGE",FACE,{"derivedFrom":[makeQuery(id+"F18.boolean.opBoolean","MERGE",FACE,{"derivedFrom":[makeQuery(id+"F17.boolean.opBoolean","MERGE",FACE,{"derivedFrom":[makeQuery(id+"F16.boolean.opBoolean","MERGE",FACE,{"derivedFrom":[makeQuery(id+"F15.boolean.opBoolean","MERGE",FACE,{"derivedFrom":[makeQuery(id+"F14.boolean.opBoolean","MERGE",FACE,{"derivedFrom":[makeQuery(id+"F13.boolean.opBoolean","MERGE",FACE,{"derivedFrom":[makeQuery(id+"F12.boolean.opBoolean","MERGE",FACE,{"derivedFrom":[makeQuery(id+"F11.boolean.opBoolean","MERGE",FACE,{"derivedFrom":[makeQuery(id+"F10.boolean.opBoolean","MERGE",FACE,{"derivedFrom":[makeQuery(id+"F9.boolean.opBoolean","MERGE",FACE,{"derivedFrom":[makeQuery(id+"F8.boolean.opBoolean","MERGE",FACE,{"derivedFrom":[makeQuery(id+"F7.boolean.opBoolean","MERGE",FACE,{"derivedFrom":[makeQuery(id+"F6.boolean.opBoolean","MERGE",FACE,{"derivedFrom":[makeQuery(id+"F5.boolean.opBoolean","MERGE",FACE,{"derivedFrom":[makeQuery(id+"F1.opRevolve","SWEPT_FACE",FACE,{"disambiguationData":[OSD([sQuery(id+"F0.wireOp",EDGE,"E5")])]}),makeQuery(id+"F5.opLoft","CAP_FACE",FACE,{"disambiguationData":[OSD([makeQuery(id+"F4.imprint","IMPRINT",FACE,{"disambiguationData":[TD([[makeQuery(id+"F4.imprint","IMPRINT",EDGE,{"derivedFrom":sQuery(id+"F4.wireOp",EDGE,"E21")}),1.0]])]})])],"isStart":true})]}),makeQuery(id+"F6.opLoft","CAP_FACE",FACE,{"disambiguationData":[OSD([makeQuery(id+"F4.imprint","IMPRINT",FACE,{"disambiguationData":[TD([[makeQuery(id+"F4.imprint","IMPRINT",EDGE,{"derivedFrom":sQuery(id+"F4.wireOp",EDGE,"E26.15.0")}),1.0]])]})])],"isStart":true})]}),makeQuery(id+"F7.opLoft","CAP_FACE",FACE,{"disambiguationData":[OSD([makeQuery(id+"F4.imprint","IMPRINT",FACE,{"disambiguationData":[TD([[makeQuery(id+"F4.imprint","IMPRINT",EDGE,{"derivedFrom":sQuery(id+"F4.wireOp",EDGE,"E26.14.0")}),1.0]])]})])],"isStart":true})]}),makeQuery(id+"F8.opLoft","CAP_FACE",FACE,{"disambiguationData":[OSD([makeQuery(id+"F4.imprint","IMPRINT",FACE,{"disambiguationData":[TD([[makeQuery(id+"F4.imprint","IMPRINT",EDGE,{"derivedFrom":sQuery(id+"F4.wireOp",EDGE,"E26.13.0")}),1.0]])]})])],"isStart":true})]}),makeQuery(id+"F9.opLoft","CAP_FACE",FACE,{"disambiguationData":[OSD([makeQuery(id+"F4.imprint","IMPRINT",FACE,{"disambiguationData":[TD([[makeQuery(id+"F4.imprint","IMPRINT",EDGE,{"derivedFrom":sQuery(id+"F4.wireOp",EDGE,"E26.12.0")}),1.0]])]})])],"isStart":true})]}),makeQuery(id+"F10.opLoft","CAP_FACE",FACE,{"disambiguationData":[OSD([makeQuery(id+"F4.imprint","IMPRINT",FACE,{"disambiguationData":[TD([[makeQuery(id+"F4.imprint","IMPRINT",EDGE,{"derivedFrom":sQuery(id+"F4.wireOp",EDGE,"E26.11.0")}),1.0]])]})])],"isStart":true})]}),makeQuery(id+"F11.opLoft","CAP_FACE",FACE,{"disambiguationData":[OSD([makeQuery(id+"F4.imprint","IMPRINT",FACE,{"disambiguationData":[TD([[makeQuery(id+"F4.imprint","IMPRINT",EDGE,{"derivedFrom":sQuery(id+"F4.wireOp",EDGE,"E26.10.0")}),1.0]])]})])],"isStart":true})]}),makeQuery(id+"F12.opLoft","CAP_FACE",FACE,{"disambiguationData":[OSD([makeQuery(id+"F4.imprint","IMPRINT",FACE,{"disambiguationData":[TD([[makeQuery(id+"F4.imprint","IMPRINT",EDGE,{"derivedFrom":sQuery(id+"F4.wireOp",EDGE,"E26.9.0")}),1.0]])]})])],"isStart":true})]}),makeQuery(id+"F13.opLoft","CAP_FACE",FACE,{"disambiguationData":[OSD([makeQuery(id+"F4.imprint","IMPRINT",FACE,{"disambiguationData":[TD([[makeQuery(id+"F4.imprint","IMPRINT",EDGE,{"derivedFrom":sQuery(id+"F4.wireOp",EDGE,"E26.8.0")}),1.0]])]})])],"isStart":true})]}),makeQuery(id+"F14.opLoft","CAP_FACE",FACE,{"disambiguationData":[OSD([makeQuery(id+"F4.imprint","IMPRINT",FACE,{"disambiguationData":[TD([[makeQuery(id+"F4.imprint","IMPRINT",EDGE,{"derivedFrom":sQuery(id+"F4.wireOp",EDGE,"E26.7.0")}),1.0]])]})])],"isStart":true})]}),makeQuery(id+"F15.opLoft","CAP_FACE",FACE,{"disambiguationData":[OSD([makeQuery(id+"F4.imprint","IMPRINT",FACE,{"disambiguationData":[TD([[makeQuery(id+"F4.imprint","IMPRINT",EDGE,{"derivedFrom":sQuery(id+"F4.wireOp",EDGE,"E26.6.0")}),1.0]])]})])],"isStart":true})]}),makeQuery(id+"F16.opLoft","CAP_FACE",FACE,{"disambiguationData":[OSD([makeQuery(id+"F4.imprint","IMPRINT",FACE,{"disambiguationData":[TD([[makeQuery(id+"F4.imprint","IMPRINT",EDGE,{"derivedFrom":sQuery(id+"F4.wireOp",EDGE,"E26.5.0")}),1.0]])]})])],"isStart":true})]}),makeQuery(id+"F17.opLoft","CAP_FACE",FACE,{"disambiguationData":[OSD([makeQuery(id+"F4.imprint","IMPRINT",FACE,{"disambiguationData":[TD([[makeQuery(id+"F4.imprint","IMPRINT",EDGE,{"derivedFrom":sQuery(id+"F4.wireOp",EDGE,"E26.4.0")}),1.0]])]})])],"isStart":true})]}),makeQuery(id+"F18.opLoft","CAP_FACE",FACE,{"disambiguationData":[OSD([makeQuery(id+"F4.imprint","IMPRINT",FACE,{"disambiguationData":[TD([[makeQuery(id+"F4.imprint","IMPRINT",EDGE,{"derivedFrom":sQuery(id+"F4.wireOp",EDGE,"E26.3.0")}),1.0]])]})])],"isStart":true})]}),makeQuery(id+"F19.opLoft","CAP_FACE",FACE,{"disambiguationData":[OSD([makeQuery(id+"F4.imprint","IMPRINT",FACE,{"disambiguationData":[TD([[makeQuery(id+"F4.imprint","IMPRINT",EDGE,{"derivedFrom":sQuery(id+"F4.wireOp",EDGE,"E26.2.0")}),1.0]])]})])],"isStart":true})]}),makeQuery(id+"F20.opLoft","CAP_FACE",FACE,{"disambiguationData":[OSD([makeQuery(id+"F4.imprint","IMPRINT",FACE,{"disambiguationData":[TD([[makeQuery(id+"F4.imprint","IMPRINT",EDGE,{"derivedFrom":sQuery(id+"F4.wireOp",EDGE,"E26.1.0")}),1.0]])]})])],"isStart":true})]}),makeQuery(id+"F42.opRevolve","SWEPT_FACE",FACE,{"disambiguationData":[OSD([sQuery(id+"F41.wireOp",EDGE,"E32")])]})]});
            var Q9;
            Q9=makeQuery(id+"F42.boolean.opBoolean","INTERSECT",EDGE,{"disambiguationData":[OD(12.0)],"derivedFrom":[makeQuery(id+"F20.boolean.opBoolean","MERGE",FACE,{"derivedFrom":[makeQuery(id+"F19.boolean.opBoolean","MERGE",FACE,{"derivedFrom":[makeQuery(id+"F18.boolean.opBoolean","MERGE",FACE,{"derivedFrom":[makeQuery(id+"F17.boolean.opBoolean","MERGE",FACE,{"derivedFrom":[makeQuery(id+"F16.boolean.opBoolean","MERGE",FACE,{"derivedFrom":[makeQuery(id+"F15.boolean.opBoolean","MERGE",FACE,{"derivedFrom":[makeQuery(id+"F14.boolean.opBoolean","MERGE",FACE,{"derivedFrom":[makeQuery(id+"F13.boolean.opBoolean","MERGE",FACE,{"derivedFrom":[makeQuery(id+"F12.boolean.opBoolean","MERGE",FACE,{"derivedFrom":[makeQuery(id+"F11.boolean.opBoolean","MERGE",FACE,{"derivedFrom":[makeQuery(id+"F10.boolean.opBoolean","MERGE",FACE,{"derivedFrom":[makeQuery(id+"F9.boolean.opBoolean","MERGE",FACE,{"derivedFrom":[makeQuery(id+"F8.boolean.opBoolean","MERGE",FACE,{"derivedFrom":[makeQuery(id+"F7.boolean.opBoolean","MERGE",FACE,{"derivedFrom":[makeQuery(id+"F6.boolean.opBoolean","MERGE",FACE,{"derivedFrom":[makeQuery(id+"F5.boolean.opBoolean","MERGE",FACE,{"derivedFrom":[makeQuery(id+"F1.opRevolve","SWEPT_FACE",FACE,{"disambiguationData":[OSD([sQuery(id+"F0.wireOp",EDGE,"E5")])]}),makeQuery(id+"F5.opLoft","CAP_FACE",FACE,{"disambiguationData":[OSD([makeQuery(id+"F4.imprint","IMPRINT",FACE,{"disambiguationData":[TD([[makeQuery(id+"F4.imprint","IMPRINT",EDGE,{"derivedFrom":sQuery(id+"F4.wireOp",EDGE,"E21")}),1.0]])]})])],"isStart":true})]}),makeQuery(id+"F6.opLoft","CAP_FACE",FACE,{"disambiguationData":[OSD([makeQuery(id+"F4.imprint","IMPRINT",FACE,{"disambiguationData":[TD([[makeQuery(id+"F4.imprint","IMPRINT",EDGE,{"derivedFrom":sQuery(id+"F4.wireOp",EDGE,"E26.15.0")}),1.0]])]})])],"isStart":true})]}),makeQuery(id+"F7.opLoft","CAP_FACE",FACE,{"disambiguationData":[OSD([makeQuery(id+"F4.imprint","IMPRINT",FACE,{"disambiguationData":[TD([[makeQuery(id+"F4.imprint","IMPRINT",EDGE,{"derivedFrom":sQuery(id+"F4.wireOp",EDGE,"E26.14.0")}),1.0]])]})])],"isStart":true})]}),makeQuery(id+"F8.opLoft","CAP_FACE",FACE,{"disambiguationData":[OSD([makeQuery(id+"F4.imprint","IMPRINT",FACE,{"disambiguationData":[TD([[makeQuery(id+"F4.imprint","IMPRINT",EDGE,{"derivedFrom":sQuery(id+"F4.wireOp",EDGE,"E26.13.0")}),1.0]])]})])],"isStart":true})]}),makeQuery(id+"F9.opLoft","CAP_FACE",FACE,{"disambiguationData":[OSD([makeQuery(id+"F4.imprint","IMPRINT",FACE,{"disambiguationData":[TD([[makeQuery(id+"F4.imprint","IMPRINT",EDGE,{"derivedFrom":sQuery(id+"F4.wireOp",EDGE,"E26.12.0")}),1.0]])]})])],"isStart":true})]}),makeQuery(id+"F10.opLoft","CAP_FACE",FACE,{"disambiguationData":[OSD([makeQuery(id+"F4.imprint","IMPRINT",FACE,{"disambiguationData":[TD([[makeQuery(id+"F4.imprint","IMPRINT",EDGE,{"derivedFrom":sQuery(id+"F4.wireOp",EDGE,"E26.11.0")}),1.0]])]})])],"isStart":true})]}),makeQuery(id+"F11.opLoft","CAP_FACE",FACE,{"disambiguationData":[OSD([makeQuery(id+"F4.imprint","IMPRINT",FACE,{"disambiguationData":[TD([[makeQuery(id+"F4.imprint","IMPRINT",EDGE,{"derivedFrom":sQuery(id+"F4.wireOp",EDGE,"E26.10.0")}),1.0]])]})])],"isStart":true})]}),makeQuery(id+"F12.opLoft","CAP_FACE",FACE,{"disambiguationData":[OSD([makeQuery(id+"F4.imprint","IMPRINT",FACE,{"disambiguationData":[TD([[makeQuery(id+"F4.imprint","IMPRINT",EDGE,{"derivedFrom":sQuery(id+"F4.wireOp",EDGE,"E26.9.0")}),1.0]])]})])],"isStart":true})]}),makeQuery(id+"F13.opLoft","CAP_FACE",FACE,{"disambiguationData":[OSD([makeQuery(id+"F4.imprint","IMPRINT",FACE,{"disambiguationData":[TD([[makeQuery(id+"F4.imprint","IMPRINT",EDGE,{"derivedFrom":sQuery(id+"F4.wireOp",EDGE,"E26.8.0")}),1.0]])]})])],"isStart":true})]}),makeQuery(id+"F14.opLoft","CAP_FACE",FACE,{"disambiguationData":[OSD([makeQuery(id+"F4.imprint","IMPRINT",FACE,{"disambiguationData":[TD([[makeQuery(id+"F4.imprint","IMPRINT",EDGE,{"derivedFrom":sQuery(id+"F4.wireOp",EDGE,"E26.7.0")}),1.0]])]})])],"isStart":true})]}),makeQuery(id+"F15.opLoft","CAP_FACE",FACE,{"disambiguationData":[OSD([makeQuery(id+"F4.imprint","IMPRINT",FACE,{"disambiguationData":[TD([[makeQuery(id+"F4.imprint","IMPRINT",EDGE,{"derivedFrom":sQuery(id+"F4.wireOp",EDGE,"E26.6.0")}),1.0]])]})])],"isStart":true})]}),makeQuery(id+"F16.opLoft","CAP_FACE",FACE,{"disambiguationData":[OSD([makeQuery(id+"F4.imprint","IMPRINT",FACE,{"disambiguationData":[TD([[makeQuery(id+"F4.imprint","IMPRINT",EDGE,{"derivedFrom":sQuery(id+"F4.wireOp",EDGE,"E26.5.0")}),1.0]])]})])],"isStart":true})]}),makeQuery(id+"F17.opLoft","CAP_FACE",FACE,{"disambiguationData":[OSD([makeQuery(id+"F4.imprint","IMPRINT",FACE,{"disambiguationData":[TD([[makeQuery(id+"F4.imprint","IMPRINT",EDGE,{"derivedFrom":sQuery(id+"F4.wireOp",EDGE,"E26.4.0")}),1.0]])]})])],"isStart":true})]}),makeQuery(id+"F18.opLoft","CAP_FACE",FACE,{"disambiguationData":[OSD([makeQuery(id+"F4.imprint","IMPRINT",FACE,{"disambiguationData":[TD([[makeQuery(id+"F4.imprint","IMPRINT",EDGE,{"derivedFrom":sQuery(id+"F4.wireOp",EDGE,"E26.3.0")}),1.0]])]})])],"isStart":true})]}),makeQuery(id+"F19.opLoft","CAP_FACE",FACE,{"disambiguationData":[OSD([makeQuery(id+"F4.imprint","IMPRINT",FACE,{"disambiguationData":[TD([[makeQuery(id+"F4.imprint","IMPRINT",EDGE,{"derivedFrom":sQuery(id+"F4.wireOp",EDGE,"E26.2.0")}),1.0]])]})])],"isStart":true})]}),makeQuery(id+"F20.opLoft","CAP_FACE",FACE,{"disambiguationData":[OSD([makeQuery(id+"F4.imprint","IMPRINT",FACE,{"disambiguationData":[TD([[makeQuery(id+"F4.imprint","IMPRINT",EDGE,{"derivedFrom":sQuery(id+"F4.wireOp",EDGE,"E26.1.0")}),1.0]])]})])],"isStart":true})]}),makeQuery(id+"F42.opRevolve","SWEPT_FACE",FACE,{"disambiguationData":[OSD([sQuery(id+"F41.wireOp",EDGE,"E32")])]})]});
            var Q10;
            Q10=makeQuery(id+"F42.boolean.opBoolean","INTERSECT",EDGE,{"disambiguationData":[OD(11.0)],"derivedFrom":[makeQuery(id+"F20.boolean.opBoolean","MERGE",FACE,{"derivedFrom":[makeQuery(id+"F19.boolean.opBoolean","MERGE",FACE,{"derivedFrom":[makeQuery(id+"F18.boolean.opBoolean","MERGE",FACE,{"derivedFrom":[makeQuery(id+"F17.boolean.opBoolean","MERGE",FACE,{"derivedFrom":[makeQuery(id+"F16.boolean.opBoolean","MERGE",FACE,{"derivedFrom":[makeQuery(id+"F15.boolean.opBoolean","MERGE",FACE,{"derivedFrom":[makeQuery(id+"F14.boolean.opBoolean","MERGE",FACE,{"derivedFrom":[makeQuery(id+"F13.boolean.opBoolean","MERGE",FACE,{"derivedFrom":[makeQuery(id+"F12.boolean.opBoolean","MERGE",FACE,{"derivedFrom":[makeQuery(id+"F11.boolean.opBoolean","MERGE",FACE,{"derivedFrom":[makeQuery(id+"F10.boolean.opBoolean","MERGE",FACE,{"derivedFrom":[makeQuery(id+"F9.boolean.opBoolean","MERGE",FACE,{"derivedFrom":[makeQuery(id+"F8.boolean.opBoolean","MERGE",FACE,{"derivedFrom":[makeQuery(id+"F7.boolean.opBoolean","MERGE",FACE,{"derivedFrom":[makeQuery(id+"F6.boolean.opBoolean","MERGE",FACE,{"derivedFrom":[makeQuery(id+"F5.boolean.opBoolean","MERGE",FACE,{"derivedFrom":[makeQuery(id+"F1.opRevolve","SWEPT_FACE",FACE,{"disambiguationData":[OSD([sQuery(id+"F0.wireOp",EDGE,"E5")])]}),makeQuery(id+"F5.opLoft","CAP_FACE",FACE,{"disambiguationData":[OSD([makeQuery(id+"F4.imprint","IMPRINT",FACE,{"disambiguationData":[TD([[makeQuery(id+"F4.imprint","IMPRINT",EDGE,{"derivedFrom":sQuery(id+"F4.wireOp",EDGE,"E21")}),1.0]])]})])],"isStart":true})]}),makeQuery(id+"F6.opLoft","CAP_FACE",FACE,{"disambiguationData":[OSD([makeQuery(id+"F4.imprint","IMPRINT",FACE,{"disambiguationData":[TD([[makeQuery(id+"F4.imprint","IMPRINT",EDGE,{"derivedFrom":sQuery(id+"F4.wireOp",EDGE,"E26.15.0")}),1.0]])]})])],"isStart":true})]}),makeQuery(id+"F7.opLoft","CAP_FACE",FACE,{"disambiguationData":[OSD([makeQuery(id+"F4.imprint","IMPRINT",FACE,{"disambiguationData":[TD([[makeQuery(id+"F4.imprint","IMPRINT",EDGE,{"derivedFrom":sQuery(id+"F4.wireOp",EDGE,"E26.14.0")}),1.0]])]})])],"isStart":true})]}),makeQuery(id+"F8.opLoft","CAP_FACE",FACE,{"disambiguationData":[OSD([makeQuery(id+"F4.imprint","IMPRINT",FACE,{"disambiguationData":[TD([[makeQuery(id+"F4.imprint","IMPRINT",EDGE,{"derivedFrom":sQuery(id+"F4.wireOp",EDGE,"E26.13.0")}),1.0]])]})])],"isStart":true})]}),makeQuery(id+"F9.opLoft","CAP_FACE",FACE,{"disambiguationData":[OSD([makeQuery(id+"F4.imprint","IMPRINT",FACE,{"disambiguationData":[TD([[makeQuery(id+"F4.imprint","IMPRINT",EDGE,{"derivedFrom":sQuery(id+"F4.wireOp",EDGE,"E26.12.0")}),1.0]])]})])],"isStart":true})]}),makeQuery(id+"F10.opLoft","CAP_FACE",FACE,{"disambiguationData":[OSD([makeQuery(id+"F4.imprint","IMPRINT",FACE,{"disambiguationData":[TD([[makeQuery(id+"F4.imprint","IMPRINT",EDGE,{"derivedFrom":sQuery(id+"F4.wireOp",EDGE,"E26.11.0")}),1.0]])]})])],"isStart":true})]}),makeQuery(id+"F11.opLoft","CAP_FACE",FACE,{"disambiguationData":[OSD([makeQuery(id+"F4.imprint","IMPRINT",FACE,{"disambiguationData":[TD([[makeQuery(id+"F4.imprint","IMPRINT",EDGE,{"derivedFrom":sQuery(id+"F4.wireOp",EDGE,"E26.10.0")}),1.0]])]})])],"isStart":true})]}),makeQuery(id+"F12.opLoft","CAP_FACE",FACE,{"disambiguationData":[OSD([makeQuery(id+"F4.imprint","IMPRINT",FACE,{"disambiguationData":[TD([[makeQuery(id+"F4.imprint","IMPRINT",EDGE,{"derivedFrom":sQuery(id+"F4.wireOp",EDGE,"E26.9.0")}),1.0]])]})])],"isStart":true})]}),makeQuery(id+"F13.opLoft","CAP_FACE",FACE,{"disambiguationData":[OSD([makeQuery(id+"F4.imprint","IMPRINT",FACE,{"disambiguationData":[TD([[makeQuery(id+"F4.imprint","IMPRINT",EDGE,{"derivedFrom":sQuery(id+"F4.wireOp",EDGE,"E26.8.0")}),1.0]])]})])],"isStart":true})]}),makeQuery(id+"F14.opLoft","CAP_FACE",FACE,{"disambiguationData":[OSD([makeQuery(id+"F4.imprint","IMPRINT",FACE,{"disambiguationData":[TD([[makeQuery(id+"F4.imprint","IMPRINT",EDGE,{"derivedFrom":sQuery(id+"F4.wireOp",EDGE,"E26.7.0")}),1.0]])]})])],"isStart":true})]}),makeQuery(id+"F15.opLoft","CAP_FACE",FACE,{"disambiguationData":[OSD([makeQuery(id+"F4.imprint","IMPRINT",FACE,{"disambiguationData":[TD([[makeQuery(id+"F4.imprint","IMPRINT",EDGE,{"derivedFrom":sQuery(id+"F4.wireOp",EDGE,"E26.6.0")}),1.0]])]})])],"isStart":true})]}),makeQuery(id+"F16.opLoft","CAP_FACE",FACE,{"disambiguationData":[OSD([makeQuery(id+"F4.imprint","IMPRINT",FACE,{"disambiguationData":[TD([[makeQuery(id+"F4.imprint","IMPRINT",EDGE,{"derivedFrom":sQuery(id+"F4.wireOp",EDGE,"E26.5.0")}),1.0]])]})])],"isStart":true})]}),makeQuery(id+"F17.opLoft","CAP_FACE",FACE,{"disambiguationData":[OSD([makeQuery(id+"F4.imprint","IMPRINT",FACE,{"disambiguationData":[TD([[makeQuery(id+"F4.imprint","IMPRINT",EDGE,{"derivedFrom":sQuery(id+"F4.wireOp",EDGE,"E26.4.0")}),1.0]])]})])],"isStart":true})]}),makeQuery(id+"F18.opLoft","CAP_FACE",FACE,{"disambiguationData":[OSD([makeQuery(id+"F4.imprint","IMPRINT",FACE,{"disambiguationData":[TD([[makeQuery(id+"F4.imprint","IMPRINT",EDGE,{"derivedFrom":sQuery(id+"F4.wireOp",EDGE,"E26.3.0")}),1.0]])]})])],"isStart":true})]}),makeQuery(id+"F19.opLoft","CAP_FACE",FACE,{"disambiguationData":[OSD([makeQuery(id+"F4.imprint","IMPRINT",FACE,{"disambiguationData":[TD([[makeQuery(id+"F4.imprint","IMPRINT",EDGE,{"derivedFrom":sQuery(id+"F4.wireOp",EDGE,"E26.2.0")}),1.0]])]})])],"isStart":true})]}),makeQuery(id+"F20.opLoft","CAP_FACE",FACE,{"disambiguationData":[OSD([makeQuery(id+"F4.imprint","IMPRINT",FACE,{"disambiguationData":[TD([[makeQuery(id+"F4.imprint","IMPRINT",EDGE,{"derivedFrom":sQuery(id+"F4.wireOp",EDGE,"E26.1.0")}),1.0]])]})])],"isStart":true})]}),makeQuery(id+"F42.opRevolve","SWEPT_FACE",FACE,{"disambiguationData":[OSD([sQuery(id+"F41.wireOp",EDGE,"E32")])]})]});
            var Q11;
            Q11=makeQuery(id+"F42.boolean.opBoolean","INTERSECT",EDGE,{"disambiguationData":[OD(10.0)],"derivedFrom":[makeQuery(id+"F20.boolean.opBoolean","MERGE",FACE,{"derivedFrom":[makeQuery(id+"F19.boolean.opBoolean","MERGE",FACE,{"derivedFrom":[makeQuery(id+"F18.boolean.opBoolean","MERGE",FACE,{"derivedFrom":[makeQuery(id+"F17.boolean.opBoolean","MERGE",FACE,{"derivedFrom":[makeQuery(id+"F16.boolean.opBoolean","MERGE",FACE,{"derivedFrom":[makeQuery(id+"F15.boolean.opBoolean","MERGE",FACE,{"derivedFrom":[makeQuery(id+"F14.boolean.opBoolean","MERGE",FACE,{"derivedFrom":[makeQuery(id+"F13.boolean.opBoolean","MERGE",FACE,{"derivedFrom":[makeQuery(id+"F12.boolean.opBoolean","MERGE",FACE,{"derivedFrom":[makeQuery(id+"F11.boolean.opBoolean","MERGE",FACE,{"derivedFrom":[makeQuery(id+"F10.boolean.opBoolean","MERGE",FACE,{"derivedFrom":[makeQuery(id+"F9.boolean.opBoolean","MERGE",FACE,{"derivedFrom":[makeQuery(id+"F8.boolean.opBoolean","MERGE",FACE,{"derivedFrom":[makeQuery(id+"F7.boolean.opBoolean","MERGE",FACE,{"derivedFrom":[makeQuery(id+"F6.boolean.opBoolean","MERGE",FACE,{"derivedFrom":[makeQuery(id+"F5.boolean.opBoolean","MERGE",FACE,{"derivedFrom":[makeQuery(id+"F1.opRevolve","SWEPT_FACE",FACE,{"disambiguationData":[OSD([sQuery(id+"F0.wireOp",EDGE,"E5")])]}),makeQuery(id+"F5.opLoft","CAP_FACE",FACE,{"disambiguationData":[OSD([makeQuery(id+"F4.imprint","IMPRINT",FACE,{"disambiguationData":[TD([[makeQuery(id+"F4.imprint","IMPRINT",EDGE,{"derivedFrom":sQuery(id+"F4.wireOp",EDGE,"E21")}),1.0]])]})])],"isStart":true})]}),makeQuery(id+"F6.opLoft","CAP_FACE",FACE,{"disambiguationData":[OSD([makeQuery(id+"F4.imprint","IMPRINT",FACE,{"disambiguationData":[TD([[makeQuery(id+"F4.imprint","IMPRINT",EDGE,{"derivedFrom":sQuery(id+"F4.wireOp",EDGE,"E26.15.0")}),1.0]])]})])],"isStart":true})]}),makeQuery(id+"F7.opLoft","CAP_FACE",FACE,{"disambiguationData":[OSD([makeQuery(id+"F4.imprint","IMPRINT",FACE,{"disambiguationData":[TD([[makeQuery(id+"F4.imprint","IMPRINT",EDGE,{"derivedFrom":sQuery(id+"F4.wireOp",EDGE,"E26.14.0")}),1.0]])]})])],"isStart":true})]}),makeQuery(id+"F8.opLoft","CAP_FACE",FACE,{"disambiguationData":[OSD([makeQuery(id+"F4.imprint","IMPRINT",FACE,{"disambiguationData":[TD([[makeQuery(id+"F4.imprint","IMPRINT",EDGE,{"derivedFrom":sQuery(id+"F4.wireOp",EDGE,"E26.13.0")}),1.0]])]})])],"isStart":true})]}),makeQuery(id+"F9.opLoft","CAP_FACE",FACE,{"disambiguationData":[OSD([makeQuery(id+"F4.imprint","IMPRINT",FACE,{"disambiguationData":[TD([[makeQuery(id+"F4.imprint","IMPRINT",EDGE,{"derivedFrom":sQuery(id+"F4.wireOp",EDGE,"E26.12.0")}),1.0]])]})])],"isStart":true})]}),makeQuery(id+"F10.opLoft","CAP_FACE",FACE,{"disambiguationData":[OSD([makeQuery(id+"F4.imprint","IMPRINT",FACE,{"disambiguationData":[TD([[makeQuery(id+"F4.imprint","IMPRINT",EDGE,{"derivedFrom":sQuery(id+"F4.wireOp",EDGE,"E26.11.0")}),1.0]])]})])],"isStart":true})]}),makeQuery(id+"F11.opLoft","CAP_FACE",FACE,{"disambiguationData":[OSD([makeQuery(id+"F4.imprint","IMPRINT",FACE,{"disambiguationData":[TD([[makeQuery(id+"F4.imprint","IMPRINT",EDGE,{"derivedFrom":sQuery(id+"F4.wireOp",EDGE,"E26.10.0")}),1.0]])]})])],"isStart":true})]}),makeQuery(id+"F12.opLoft","CAP_FACE",FACE,{"disambiguationData":[OSD([makeQuery(id+"F4.imprint","IMPRINT",FACE,{"disambiguationData":[TD([[makeQuery(id+"F4.imprint","IMPRINT",EDGE,{"derivedFrom":sQuery(id+"F4.wireOp",EDGE,"E26.9.0")}),1.0]])]})])],"isStart":true})]}),makeQuery(id+"F13.opLoft","CAP_FACE",FACE,{"disambiguationData":[OSD([makeQuery(id+"F4.imprint","IMPRINT",FACE,{"disambiguationData":[TD([[makeQuery(id+"F4.imprint","IMPRINT",EDGE,{"derivedFrom":sQuery(id+"F4.wireOp",EDGE,"E26.8.0")}),1.0]])]})])],"isStart":true})]}),makeQuery(id+"F14.opLoft","CAP_FACE",FACE,{"disambiguationData":[OSD([makeQuery(id+"F4.imprint","IMPRINT",FACE,{"disambiguationData":[TD([[makeQuery(id+"F4.imprint","IMPRINT",EDGE,{"derivedFrom":sQuery(id+"F4.wireOp",EDGE,"E26.7.0")}),1.0]])]})])],"isStart":true})]}),makeQuery(id+"F15.opLoft","CAP_FACE",FACE,{"disambiguationData":[OSD([makeQuery(id+"F4.imprint","IMPRINT",FACE,{"disambiguationData":[TD([[makeQuery(id+"F4.imprint","IMPRINT",EDGE,{"derivedFrom":sQuery(id+"F4.wireOp",EDGE,"E26.6.0")}),1.0]])]})])],"isStart":true})]}),makeQuery(id+"F16.opLoft","CAP_FACE",FACE,{"disambiguationData":[OSD([makeQuery(id+"F4.imprint","IMPRINT",FACE,{"disambiguationData":[TD([[makeQuery(id+"F4.imprint","IMPRINT",EDGE,{"derivedFrom":sQuery(id+"F4.wireOp",EDGE,"E26.5.0")}),1.0]])]})])],"isStart":true})]}),makeQuery(id+"F17.opLoft","CAP_FACE",FACE,{"disambiguationData":[OSD([makeQuery(id+"F4.imprint","IMPRINT",FACE,{"disambiguationData":[TD([[makeQuery(id+"F4.imprint","IMPRINT",EDGE,{"derivedFrom":sQuery(id+"F4.wireOp",EDGE,"E26.4.0")}),1.0]])]})])],"isStart":true})]}),makeQuery(id+"F18.opLoft","CAP_FACE",FACE,{"disambiguationData":[OSD([makeQuery(id+"F4.imprint","IMPRINT",FACE,{"disambiguationData":[TD([[makeQuery(id+"F4.imprint","IMPRINT",EDGE,{"derivedFrom":sQuery(id+"F4.wireOp",EDGE,"E26.3.0")}),1.0]])]})])],"isStart":true})]}),makeQuery(id+"F19.opLoft","CAP_FACE",FACE,{"disambiguationData":[OSD([makeQuery(id+"F4.imprint","IMPRINT",FACE,{"disambiguationData":[TD([[makeQuery(id+"F4.imprint","IMPRINT",EDGE,{"derivedFrom":sQuery(id+"F4.wireOp",EDGE,"E26.2.0")}),1.0]])]})])],"isStart":true})]}),makeQuery(id+"F20.opLoft","CAP_FACE",FACE,{"disambiguationData":[OSD([makeQuery(id+"F4.imprint","IMPRINT",FACE,{"disambiguationData":[TD([[makeQuery(id+"F4.imprint","IMPRINT",EDGE,{"derivedFrom":sQuery(id+"F4.wireOp",EDGE,"E26.1.0")}),1.0]])]})])],"isStart":true})]}),makeQuery(id+"F42.opRevolve","SWEPT_FACE",FACE,{"disambiguationData":[OSD([sQuery(id+"F41.wireOp",EDGE,"E32")])]})]});
            var Q12;
            Q12=makeQuery(id+"F42.boolean.opBoolean","INTERSECT",EDGE,{"disambiguationData":[OD(9.0)],"derivedFrom":[makeQuery(id+"F20.boolean.opBoolean","MERGE",FACE,{"derivedFrom":[makeQuery(id+"F19.boolean.opBoolean","MERGE",FACE,{"derivedFrom":[makeQuery(id+"F18.boolean.opBoolean","MERGE",FACE,{"derivedFrom":[makeQuery(id+"F17.boolean.opBoolean","MERGE",FACE,{"derivedFrom":[makeQuery(id+"F16.boolean.opBoolean","MERGE",FACE,{"derivedFrom":[makeQuery(id+"F15.boolean.opBoolean","MERGE",FACE,{"derivedFrom":[makeQuery(id+"F14.boolean.opBoolean","MERGE",FACE,{"derivedFrom":[makeQuery(id+"F13.boolean.opBoolean","MERGE",FACE,{"derivedFrom":[makeQuery(id+"F12.boolean.opBoolean","MERGE",FACE,{"derivedFrom":[makeQuery(id+"F11.boolean.opBoolean","MERGE",FACE,{"derivedFrom":[makeQuery(id+"F10.boolean.opBoolean","MERGE",FACE,{"derivedFrom":[makeQuery(id+"F9.boolean.opBoolean","MERGE",FACE,{"derivedFrom":[makeQuery(id+"F8.boolean.opBoolean","MERGE",FACE,{"derivedFrom":[makeQuery(id+"F7.boolean.opBoolean","MERGE",FACE,{"derivedFrom":[makeQuery(id+"F6.boolean.opBoolean","MERGE",FACE,{"derivedFrom":[makeQuery(id+"F5.boolean.opBoolean","MERGE",FACE,{"derivedFrom":[makeQuery(id+"F1.opRevolve","SWEPT_FACE",FACE,{"disambiguationData":[OSD([sQuery(id+"F0.wireOp",EDGE,"E5")])]}),makeQuery(id+"F5.opLoft","CAP_FACE",FACE,{"disambiguationData":[OSD([makeQuery(id+"F4.imprint","IMPRINT",FACE,{"disambiguationData":[TD([[makeQuery(id+"F4.imprint","IMPRINT",EDGE,{"derivedFrom":sQuery(id+"F4.wireOp",EDGE,"E21")}),1.0]])]})])],"isStart":true})]}),makeQuery(id+"F6.opLoft","CAP_FACE",FACE,{"disambiguationData":[OSD([makeQuery(id+"F4.imprint","IMPRINT",FACE,{"disambiguationData":[TD([[makeQuery(id+"F4.imprint","IMPRINT",EDGE,{"derivedFrom":sQuery(id+"F4.wireOp",EDGE,"E26.15.0")}),1.0]])]})])],"isStart":true})]}),makeQuery(id+"F7.opLoft","CAP_FACE",FACE,{"disambiguationData":[OSD([makeQuery(id+"F4.imprint","IMPRINT",FACE,{"disambiguationData":[TD([[makeQuery(id+"F4.imprint","IMPRINT",EDGE,{"derivedFrom":sQuery(id+"F4.wireOp",EDGE,"E26.14.0")}),1.0]])]})])],"isStart":true})]}),makeQuery(id+"F8.opLoft","CAP_FACE",FACE,{"disambiguationData":[OSD([makeQuery(id+"F4.imprint","IMPRINT",FACE,{"disambiguationData":[TD([[makeQuery(id+"F4.imprint","IMPRINT",EDGE,{"derivedFrom":sQuery(id+"F4.wireOp",EDGE,"E26.13.0")}),1.0]])]})])],"isStart":true})]}),makeQuery(id+"F9.opLoft","CAP_FACE",FACE,{"disambiguationData":[OSD([makeQuery(id+"F4.imprint","IMPRINT",FACE,{"disambiguationData":[TD([[makeQuery(id+"F4.imprint","IMPRINT",EDGE,{"derivedFrom":sQuery(id+"F4.wireOp",EDGE,"E26.12.0")}),1.0]])]})])],"isStart":true})]}),makeQuery(id+"F10.opLoft","CAP_FACE",FACE,{"disambiguationData":[OSD([makeQuery(id+"F4.imprint","IMPRINT",FACE,{"disambiguationData":[TD([[makeQuery(id+"F4.imprint","IMPRINT",EDGE,{"derivedFrom":sQuery(id+"F4.wireOp",EDGE,"E26.11.0")}),1.0]])]})])],"isStart":true})]}),makeQuery(id+"F11.opLoft","CAP_FACE",FACE,{"disambiguationData":[OSD([makeQuery(id+"F4.imprint","IMPRINT",FACE,{"disambiguationData":[TD([[makeQuery(id+"F4.imprint","IMPRINT",EDGE,{"derivedFrom":sQuery(id+"F4.wireOp",EDGE,"E26.10.0")}),1.0]])]})])],"isStart":true})]}),makeQuery(id+"F12.opLoft","CAP_FACE",FACE,{"disambiguationData":[OSD([makeQuery(id+"F4.imprint","IMPRINT",FACE,{"disambiguationData":[TD([[makeQuery(id+"F4.imprint","IMPRINT",EDGE,{"derivedFrom":sQuery(id+"F4.wireOp",EDGE,"E26.9.0")}),1.0]])]})])],"isStart":true})]}),makeQuery(id+"F13.opLoft","CAP_FACE",FACE,{"disambiguationData":[OSD([makeQuery(id+"F4.imprint","IMPRINT",FACE,{"disambiguationData":[TD([[makeQuery(id+"F4.imprint","IMPRINT",EDGE,{"derivedFrom":sQuery(id+"F4.wireOp",EDGE,"E26.8.0")}),1.0]])]})])],"isStart":true})]}),makeQuery(id+"F14.opLoft","CAP_FACE",FACE,{"disambiguationData":[OSD([makeQuery(id+"F4.imprint","IMPRINT",FACE,{"disambiguationData":[TD([[makeQuery(id+"F4.imprint","IMPRINT",EDGE,{"derivedFrom":sQuery(id+"F4.wireOp",EDGE,"E26.7.0")}),1.0]])]})])],"isStart":true})]}),makeQuery(id+"F15.opLoft","CAP_FACE",FACE,{"disambiguationData":[OSD([makeQuery(id+"F4.imprint","IMPRINT",FACE,{"disambiguationData":[TD([[makeQuery(id+"F4.imprint","IMPRINT",EDGE,{"derivedFrom":sQuery(id+"F4.wireOp",EDGE,"E26.6.0")}),1.0]])]})])],"isStart":true})]}),makeQuery(id+"F16.opLoft","CAP_FACE",FACE,{"disambiguationData":[OSD([makeQuery(id+"F4.imprint","IMPRINT",FACE,{"disambiguationData":[TD([[makeQuery(id+"F4.imprint","IMPRINT",EDGE,{"derivedFrom":sQuery(id+"F4.wireOp",EDGE,"E26.5.0")}),1.0]])]})])],"isStart":true})]}),makeQuery(id+"F17.opLoft","CAP_FACE",FACE,{"disambiguationData":[OSD([makeQuery(id+"F4.imprint","IMPRINT",FACE,{"disambiguationData":[TD([[makeQuery(id+"F4.imprint","IMPRINT",EDGE,{"derivedFrom":sQuery(id+"F4.wireOp",EDGE,"E26.4.0")}),1.0]])]})])],"isStart":true})]}),makeQuery(id+"F18.opLoft","CAP_FACE",FACE,{"disambiguationData":[OSD([makeQuery(id+"F4.imprint","IMPRINT",FACE,{"disambiguationData":[TD([[makeQuery(id+"F4.imprint","IMPRINT",EDGE,{"derivedFrom":sQuery(id+"F4.wireOp",EDGE,"E26.3.0")}),1.0]])]})])],"isStart":true})]}),makeQuery(id+"F19.opLoft","CAP_FACE",FACE,{"disambiguationData":[OSD([makeQuery(id+"F4.imprint","IMPRINT",FACE,{"disambiguationData":[TD([[makeQuery(id+"F4.imprint","IMPRINT",EDGE,{"derivedFrom":sQuery(id+"F4.wireOp",EDGE,"E26.2.0")}),1.0]])]})])],"isStart":true})]}),makeQuery(id+"F20.opLoft","CAP_FACE",FACE,{"disambiguationData":[OSD([makeQuery(id+"F4.imprint","IMPRINT",FACE,{"disambiguationData":[TD([[makeQuery(id+"F4.imprint","IMPRINT",EDGE,{"derivedFrom":sQuery(id+"F4.wireOp",EDGE,"E26.1.0")}),1.0]])]})])],"isStart":true})]}),makeQuery(id+"F42.opRevolve","SWEPT_FACE",FACE,{"disambiguationData":[OSD([sQuery(id+"F41.wireOp",EDGE,"E32")])]})]});
            var Q13;
            Q13=makeQuery(id+"F42.boolean.opBoolean","INTERSECT",EDGE,{"disambiguationData":[OD(8.0)],"derivedFrom":[makeQuery(id+"F20.boolean.opBoolean","MERGE",FACE,{"derivedFrom":[makeQuery(id+"F19.boolean.opBoolean","MERGE",FACE,{"derivedFrom":[makeQuery(id+"F18.boolean.opBoolean","MERGE",FACE,{"derivedFrom":[makeQuery(id+"F17.boolean.opBoolean","MERGE",FACE,{"derivedFrom":[makeQuery(id+"F16.boolean.opBoolean","MERGE",FACE,{"derivedFrom":[makeQuery(id+"F15.boolean.opBoolean","MERGE",FACE,{"derivedFrom":[makeQuery(id+"F14.boolean.opBoolean","MERGE",FACE,{"derivedFrom":[makeQuery(id+"F13.boolean.opBoolean","MERGE",FACE,{"derivedFrom":[makeQuery(id+"F12.boolean.opBoolean","MERGE",FACE,{"derivedFrom":[makeQuery(id+"F11.boolean.opBoolean","MERGE",FACE,{"derivedFrom":[makeQuery(id+"F10.boolean.opBoolean","MERGE",FACE,{"derivedFrom":[makeQuery(id+"F9.boolean.opBoolean","MERGE",FACE,{"derivedFrom":[makeQuery(id+"F8.boolean.opBoolean","MERGE",FACE,{"derivedFrom":[makeQuery(id+"F7.boolean.opBoolean","MERGE",FACE,{"derivedFrom":[makeQuery(id+"F6.boolean.opBoolean","MERGE",FACE,{"derivedFrom":[makeQuery(id+"F5.boolean.opBoolean","MERGE",FACE,{"derivedFrom":[makeQuery(id+"F1.opRevolve","SWEPT_FACE",FACE,{"disambiguationData":[OSD([sQuery(id+"F0.wireOp",EDGE,"E5")])]}),makeQuery(id+"F5.opLoft","CAP_FACE",FACE,{"disambiguationData":[OSD([makeQuery(id+"F4.imprint","IMPRINT",FACE,{"disambiguationData":[TD([[makeQuery(id+"F4.imprint","IMPRINT",EDGE,{"derivedFrom":sQuery(id+"F4.wireOp",EDGE,"E21")}),1.0]])]})])],"isStart":true})]}),makeQuery(id+"F6.opLoft","CAP_FACE",FACE,{"disambiguationData":[OSD([makeQuery(id+"F4.imprint","IMPRINT",FACE,{"disambiguationData":[TD([[makeQuery(id+"F4.imprint","IMPRINT",EDGE,{"derivedFrom":sQuery(id+"F4.wireOp",EDGE,"E26.15.0")}),1.0]])]})])],"isStart":true})]}),makeQuery(id+"F7.opLoft","CAP_FACE",FACE,{"disambiguationData":[OSD([makeQuery(id+"F4.imprint","IMPRINT",FACE,{"disambiguationData":[TD([[makeQuery(id+"F4.imprint","IMPRINT",EDGE,{"derivedFrom":sQuery(id+"F4.wireOp",EDGE,"E26.14.0")}),1.0]])]})])],"isStart":true})]}),makeQuery(id+"F8.opLoft","CAP_FACE",FACE,{"disambiguationData":[OSD([makeQuery(id+"F4.imprint","IMPRINT",FACE,{"disambiguationData":[TD([[makeQuery(id+"F4.imprint","IMPRINT",EDGE,{"derivedFrom":sQuery(id+"F4.wireOp",EDGE,"E26.13.0")}),1.0]])]})])],"isStart":true})]}),makeQuery(id+"F9.opLoft","CAP_FACE",FACE,{"disambiguationData":[OSD([makeQuery(id+"F4.imprint","IMPRINT",FACE,{"disambiguationData":[TD([[makeQuery(id+"F4.imprint","IMPRINT",EDGE,{"derivedFrom":sQuery(id+"F4.wireOp",EDGE,"E26.12.0")}),1.0]])]})])],"isStart":true})]}),makeQuery(id+"F10.opLoft","CAP_FACE",FACE,{"disambiguationData":[OSD([makeQuery(id+"F4.imprint","IMPRINT",FACE,{"disambiguationData":[TD([[makeQuery(id+"F4.imprint","IMPRINT",EDGE,{"derivedFrom":sQuery(id+"F4.wireOp",EDGE,"E26.11.0")}),1.0]])]})])],"isStart":true})]}),makeQuery(id+"F11.opLoft","CAP_FACE",FACE,{"disambiguationData":[OSD([makeQuery(id+"F4.imprint","IMPRINT",FACE,{"disambiguationData":[TD([[makeQuery(id+"F4.imprint","IMPRINT",EDGE,{"derivedFrom":sQuery(id+"F4.wireOp",EDGE,"E26.10.0")}),1.0]])]})])],"isStart":true})]}),makeQuery(id+"F12.opLoft","CAP_FACE",FACE,{"disambiguationData":[OSD([makeQuery(id+"F4.imprint","IMPRINT",FACE,{"disambiguationData":[TD([[makeQuery(id+"F4.imprint","IMPRINT",EDGE,{"derivedFrom":sQuery(id+"F4.wireOp",EDGE,"E26.9.0")}),1.0]])]})])],"isStart":true})]}),makeQuery(id+"F13.opLoft","CAP_FACE",FACE,{"disambiguationData":[OSD([makeQuery(id+"F4.imprint","IMPRINT",FACE,{"disambiguationData":[TD([[makeQuery(id+"F4.imprint","IMPRINT",EDGE,{"derivedFrom":sQuery(id+"F4.wireOp",EDGE,"E26.8.0")}),1.0]])]})])],"isStart":true})]}),makeQuery(id+"F14.opLoft","CAP_FACE",FACE,{"disambiguationData":[OSD([makeQuery(id+"F4.imprint","IMPRINT",FACE,{"disambiguationData":[TD([[makeQuery(id+"F4.imprint","IMPRINT",EDGE,{"derivedFrom":sQuery(id+"F4.wireOp",EDGE,"E26.7.0")}),1.0]])]})])],"isStart":true})]}),makeQuery(id+"F15.opLoft","CAP_FACE",FACE,{"disambiguationData":[OSD([makeQuery(id+"F4.imprint","IMPRINT",FACE,{"disambiguationData":[TD([[makeQuery(id+"F4.imprint","IMPRINT",EDGE,{"derivedFrom":sQuery(id+"F4.wireOp",EDGE,"E26.6.0")}),1.0]])]})])],"isStart":true})]}),makeQuery(id+"F16.opLoft","CAP_FACE",FACE,{"disambiguationData":[OSD([makeQuery(id+"F4.imprint","IMPRINT",FACE,{"disambiguationData":[TD([[makeQuery(id+"F4.imprint","IMPRINT",EDGE,{"derivedFrom":sQuery(id+"F4.wireOp",EDGE,"E26.5.0")}),1.0]])]})])],"isStart":true})]}),makeQuery(id+"F17.opLoft","CAP_FACE",FACE,{"disambiguationData":[OSD([makeQuery(id+"F4.imprint","IMPRINT",FACE,{"disambiguationData":[TD([[makeQuery(id+"F4.imprint","IMPRINT",EDGE,{"derivedFrom":sQuery(id+"F4.wireOp",EDGE,"E26.4.0")}),1.0]])]})])],"isStart":true})]}),makeQuery(id+"F18.opLoft","CAP_FACE",FACE,{"disambiguationData":[OSD([makeQuery(id+"F4.imprint","IMPRINT",FACE,{"disambiguationData":[TD([[makeQuery(id+"F4.imprint","IMPRINT",EDGE,{"derivedFrom":sQuery(id+"F4.wireOp",EDGE,"E26.3.0")}),1.0]])]})])],"isStart":true})]}),makeQuery(id+"F19.opLoft","CAP_FACE",FACE,{"disambiguationData":[OSD([makeQuery(id+"F4.imprint","IMPRINT",FACE,{"disambiguationData":[TD([[makeQuery(id+"F4.imprint","IMPRINT",EDGE,{"derivedFrom":sQuery(id+"F4.wireOp",EDGE,"E26.2.0")}),1.0]])]})])],"isStart":true})]}),makeQuery(id+"F20.opLoft","CAP_FACE",FACE,{"disambiguationData":[OSD([makeQuery(id+"F4.imprint","IMPRINT",FACE,{"disambiguationData":[TD([[makeQuery(id+"F4.imprint","IMPRINT",EDGE,{"derivedFrom":sQuery(id+"F4.wireOp",EDGE,"E26.1.0")}),1.0]])]})])],"isStart":true})]}),makeQuery(id+"F42.opRevolve","SWEPT_FACE",FACE,{"disambiguationData":[OSD([sQuery(id+"F41.wireOp",EDGE,"E32")])]})]});
            var Q14;
            Q14=makeQuery(id+"F42.boolean.opBoolean","INTERSECT",EDGE,{"disambiguationData":[OD(7.0)],"derivedFrom":[makeQuery(id+"F20.boolean.opBoolean","MERGE",FACE,{"derivedFrom":[makeQuery(id+"F19.boolean.opBoolean","MERGE",FACE,{"derivedFrom":[makeQuery(id+"F18.boolean.opBoolean","MERGE",FACE,{"derivedFrom":[makeQuery(id+"F17.boolean.opBoolean","MERGE",FACE,{"derivedFrom":[makeQuery(id+"F16.boolean.opBoolean","MERGE",FACE,{"derivedFrom":[makeQuery(id+"F15.boolean.opBoolean","MERGE",FACE,{"derivedFrom":[makeQuery(id+"F14.boolean.opBoolean","MERGE",FACE,{"derivedFrom":[makeQuery(id+"F13.boolean.opBoolean","MERGE",FACE,{"derivedFrom":[makeQuery(id+"F12.boolean.opBoolean","MERGE",FACE,{"derivedFrom":[makeQuery(id+"F11.boolean.opBoolean","MERGE",FACE,{"derivedFrom":[makeQuery(id+"F10.boolean.opBoolean","MERGE",FACE,{"derivedFrom":[makeQuery(id+"F9.boolean.opBoolean","MERGE",FACE,{"derivedFrom":[makeQuery(id+"F8.boolean.opBoolean","MERGE",FACE,{"derivedFrom":[makeQuery(id+"F7.boolean.opBoolean","MERGE",FACE,{"derivedFrom":[makeQuery(id+"F6.boolean.opBoolean","MERGE",FACE,{"derivedFrom":[makeQuery(id+"F5.boolean.opBoolean","MERGE",FACE,{"derivedFrom":[makeQuery(id+"F1.opRevolve","SWEPT_FACE",FACE,{"disambiguationData":[OSD([sQuery(id+"F0.wireOp",EDGE,"E5")])]}),makeQuery(id+"F5.opLoft","CAP_FACE",FACE,{"disambiguationData":[OSD([makeQuery(id+"F4.imprint","IMPRINT",FACE,{"disambiguationData":[TD([[makeQuery(id+"F4.imprint","IMPRINT",EDGE,{"derivedFrom":sQuery(id+"F4.wireOp",EDGE,"E21")}),1.0]])]})])],"isStart":true})]}),makeQuery(id+"F6.opLoft","CAP_FACE",FACE,{"disambiguationData":[OSD([makeQuery(id+"F4.imprint","IMPRINT",FACE,{"disambiguationData":[TD([[makeQuery(id+"F4.imprint","IMPRINT",EDGE,{"derivedFrom":sQuery(id+"F4.wireOp",EDGE,"E26.15.0")}),1.0]])]})])],"isStart":true})]}),makeQuery(id+"F7.opLoft","CAP_FACE",FACE,{"disambiguationData":[OSD([makeQuery(id+"F4.imprint","IMPRINT",FACE,{"disambiguationData":[TD([[makeQuery(id+"F4.imprint","IMPRINT",EDGE,{"derivedFrom":sQuery(id+"F4.wireOp",EDGE,"E26.14.0")}),1.0]])]})])],"isStart":true})]}),makeQuery(id+"F8.opLoft","CAP_FACE",FACE,{"disambiguationData":[OSD([makeQuery(id+"F4.imprint","IMPRINT",FACE,{"disambiguationData":[TD([[makeQuery(id+"F4.imprint","IMPRINT",EDGE,{"derivedFrom":sQuery(id+"F4.wireOp",EDGE,"E26.13.0")}),1.0]])]})])],"isStart":true})]}),makeQuery(id+"F9.opLoft","CAP_FACE",FACE,{"disambiguationData":[OSD([makeQuery(id+"F4.imprint","IMPRINT",FACE,{"disambiguationData":[TD([[makeQuery(id+"F4.imprint","IMPRINT",EDGE,{"derivedFrom":sQuery(id+"F4.wireOp",EDGE,"E26.12.0")}),1.0]])]})])],"isStart":true})]}),makeQuery(id+"F10.opLoft","CAP_FACE",FACE,{"disambiguationData":[OSD([makeQuery(id+"F4.imprint","IMPRINT",FACE,{"disambiguationData":[TD([[makeQuery(id+"F4.imprint","IMPRINT",EDGE,{"derivedFrom":sQuery(id+"F4.wireOp",EDGE,"E26.11.0")}),1.0]])]})])],"isStart":true})]}),makeQuery(id+"F11.opLoft","CAP_FACE",FACE,{"disambiguationData":[OSD([makeQuery(id+"F4.imprint","IMPRINT",FACE,{"disambiguationData":[TD([[makeQuery(id+"F4.imprint","IMPRINT",EDGE,{"derivedFrom":sQuery(id+"F4.wireOp",EDGE,"E26.10.0")}),1.0]])]})])],"isStart":true})]}),makeQuery(id+"F12.opLoft","CAP_FACE",FACE,{"disambiguationData":[OSD([makeQuery(id+"F4.imprint","IMPRINT",FACE,{"disambiguationData":[TD([[makeQuery(id+"F4.imprint","IMPRINT",EDGE,{"derivedFrom":sQuery(id+"F4.wireOp",EDGE,"E26.9.0")}),1.0]])]})])],"isStart":true})]}),makeQuery(id+"F13.opLoft","CAP_FACE",FACE,{"disambiguationData":[OSD([makeQuery(id+"F4.imprint","IMPRINT",FACE,{"disambiguationData":[TD([[makeQuery(id+"F4.imprint","IMPRINT",EDGE,{"derivedFrom":sQuery(id+"F4.wireOp",EDGE,"E26.8.0")}),1.0]])]})])],"isStart":true})]}),makeQuery(id+"F14.opLoft","CAP_FACE",FACE,{"disambiguationData":[OSD([makeQuery(id+"F4.imprint","IMPRINT",FACE,{"disambiguationData":[TD([[makeQuery(id+"F4.imprint","IMPRINT",EDGE,{"derivedFrom":sQuery(id+"F4.wireOp",EDGE,"E26.7.0")}),1.0]])]})])],"isStart":true})]}),makeQuery(id+"F15.opLoft","CAP_FACE",FACE,{"disambiguationData":[OSD([makeQuery(id+"F4.imprint","IMPRINT",FACE,{"disambiguationData":[TD([[makeQuery(id+"F4.imprint","IMPRINT",EDGE,{"derivedFrom":sQuery(id+"F4.wireOp",EDGE,"E26.6.0")}),1.0]])]})])],"isStart":true})]}),makeQuery(id+"F16.opLoft","CAP_FACE",FACE,{"disambiguationData":[OSD([makeQuery(id+"F4.imprint","IMPRINT",FACE,{"disambiguationData":[TD([[makeQuery(id+"F4.imprint","IMPRINT",EDGE,{"derivedFrom":sQuery(id+"F4.wireOp",EDGE,"E26.5.0")}),1.0]])]})])],"isStart":true})]}),makeQuery(id+"F17.opLoft","CAP_FACE",FACE,{"disambiguationData":[OSD([makeQuery(id+"F4.imprint","IMPRINT",FACE,{"disambiguationData":[TD([[makeQuery(id+"F4.imprint","IMPRINT",EDGE,{"derivedFrom":sQuery(id+"F4.wireOp",EDGE,"E26.4.0")}),1.0]])]})])],"isStart":true})]}),makeQuery(id+"F18.opLoft","CAP_FACE",FACE,{"disambiguationData":[OSD([makeQuery(id+"F4.imprint","IMPRINT",FACE,{"disambiguationData":[TD([[makeQuery(id+"F4.imprint","IMPRINT",EDGE,{"derivedFrom":sQuery(id+"F4.wireOp",EDGE,"E26.3.0")}),1.0]])]})])],"isStart":true})]}),makeQuery(id+"F19.opLoft","CAP_FACE",FACE,{"disambiguationData":[OSD([makeQuery(id+"F4.imprint","IMPRINT",FACE,{"disambiguationData":[TD([[makeQuery(id+"F4.imprint","IMPRINT",EDGE,{"derivedFrom":sQuery(id+"F4.wireOp",EDGE,"E26.2.0")}),1.0]])]})])],"isStart":true})]}),makeQuery(id+"F20.opLoft","CAP_FACE",FACE,{"disambiguationData":[OSD([makeQuery(id+"F4.imprint","IMPRINT",FACE,{"disambiguationData":[TD([[makeQuery(id+"F4.imprint","IMPRINT",EDGE,{"derivedFrom":sQuery(id+"F4.wireOp",EDGE,"E26.1.0")}),1.0]])]})])],"isStart":true})]}),makeQuery(id+"F42.opRevolve","SWEPT_FACE",FACE,{"disambiguationData":[OSD([sQuery(id+"F41.wireOp",EDGE,"E32")])]})]});
            var Q15;
            Q15=makeQuery(id+"F42.boolean.opBoolean","INTERSECT",EDGE,{"disambiguationData":[OD(6.0)],"derivedFrom":[makeQuery(id+"F20.boolean.opBoolean","MERGE",FACE,{"derivedFrom":[makeQuery(id+"F19.boolean.opBoolean","MERGE",FACE,{"derivedFrom":[makeQuery(id+"F18.boolean.opBoolean","MERGE",FACE,{"derivedFrom":[makeQuery(id+"F17.boolean.opBoolean","MERGE",FACE,{"derivedFrom":[makeQuery(id+"F16.boolean.opBoolean","MERGE",FACE,{"derivedFrom":[makeQuery(id+"F15.boolean.opBoolean","MERGE",FACE,{"derivedFrom":[makeQuery(id+"F14.boolean.opBoolean","MERGE",FACE,{"derivedFrom":[makeQuery(id+"F13.boolean.opBoolean","MERGE",FACE,{"derivedFrom":[makeQuery(id+"F12.boolean.opBoolean","MERGE",FACE,{"derivedFrom":[makeQuery(id+"F11.boolean.opBoolean","MERGE",FACE,{"derivedFrom":[makeQuery(id+"F10.boolean.opBoolean","MERGE",FACE,{"derivedFrom":[makeQuery(id+"F9.boolean.opBoolean","MERGE",FACE,{"derivedFrom":[makeQuery(id+"F8.boolean.opBoolean","MERGE",FACE,{"derivedFrom":[makeQuery(id+"F7.boolean.opBoolean","MERGE",FACE,{"derivedFrom":[makeQuery(id+"F6.boolean.opBoolean","MERGE",FACE,{"derivedFrom":[makeQuery(id+"F5.boolean.opBoolean","MERGE",FACE,{"derivedFrom":[makeQuery(id+"F1.opRevolve","SWEPT_FACE",FACE,{"disambiguationData":[OSD([sQuery(id+"F0.wireOp",EDGE,"E5")])]}),makeQuery(id+"F5.opLoft","CAP_FACE",FACE,{"disambiguationData":[OSD([makeQuery(id+"F4.imprint","IMPRINT",FACE,{"disambiguationData":[TD([[makeQuery(id+"F4.imprint","IMPRINT",EDGE,{"derivedFrom":sQuery(id+"F4.wireOp",EDGE,"E21")}),1.0]])]})])],"isStart":true})]}),makeQuery(id+"F6.opLoft","CAP_FACE",FACE,{"disambiguationData":[OSD([makeQuery(id+"F4.imprint","IMPRINT",FACE,{"disambiguationData":[TD([[makeQuery(id+"F4.imprint","IMPRINT",EDGE,{"derivedFrom":sQuery(id+"F4.wireOp",EDGE,"E26.15.0")}),1.0]])]})])],"isStart":true})]}),makeQuery(id+"F7.opLoft","CAP_FACE",FACE,{"disambiguationData":[OSD([makeQuery(id+"F4.imprint","IMPRINT",FACE,{"disambiguationData":[TD([[makeQuery(id+"F4.imprint","IMPRINT",EDGE,{"derivedFrom":sQuery(id+"F4.wireOp",EDGE,"E26.14.0")}),1.0]])]})])],"isStart":true})]}),makeQuery(id+"F8.opLoft","CAP_FACE",FACE,{"disambiguationData":[OSD([makeQuery(id+"F4.imprint","IMPRINT",FACE,{"disambiguationData":[TD([[makeQuery(id+"F4.imprint","IMPRINT",EDGE,{"derivedFrom":sQuery(id+"F4.wireOp",EDGE,"E26.13.0")}),1.0]])]})])],"isStart":true})]}),makeQuery(id+"F9.opLoft","CAP_FACE",FACE,{"disambiguationData":[OSD([makeQuery(id+"F4.imprint","IMPRINT",FACE,{"disambiguationData":[TD([[makeQuery(id+"F4.imprint","IMPRINT",EDGE,{"derivedFrom":sQuery(id+"F4.wireOp",EDGE,"E26.12.0")}),1.0]])]})])],"isStart":true})]}),makeQuery(id+"F10.opLoft","CAP_FACE",FACE,{"disambiguationData":[OSD([makeQuery(id+"F4.imprint","IMPRINT",FACE,{"disambiguationData":[TD([[makeQuery(id+"F4.imprint","IMPRINT",EDGE,{"derivedFrom":sQuery(id+"F4.wireOp",EDGE,"E26.11.0")}),1.0]])]})])],"isStart":true})]}),makeQuery(id+"F11.opLoft","CAP_FACE",FACE,{"disambiguationData":[OSD([makeQuery(id+"F4.imprint","IMPRINT",FACE,{"disambiguationData":[TD([[makeQuery(id+"F4.imprint","IMPRINT",EDGE,{"derivedFrom":sQuery(id+"F4.wireOp",EDGE,"E26.10.0")}),1.0]])]})])],"isStart":true})]}),makeQuery(id+"F12.opLoft","CAP_FACE",FACE,{"disambiguationData":[OSD([makeQuery(id+"F4.imprint","IMPRINT",FACE,{"disambiguationData":[TD([[makeQuery(id+"F4.imprint","IMPRINT",EDGE,{"derivedFrom":sQuery(id+"F4.wireOp",EDGE,"E26.9.0")}),1.0]])]})])],"isStart":true})]}),makeQuery(id+"F13.opLoft","CAP_FACE",FACE,{"disambiguationData":[OSD([makeQuery(id+"F4.imprint","IMPRINT",FACE,{"disambiguationData":[TD([[makeQuery(id+"F4.imprint","IMPRINT",EDGE,{"derivedFrom":sQuery(id+"F4.wireOp",EDGE,"E26.8.0")}),1.0]])]})])],"isStart":true})]}),makeQuery(id+"F14.opLoft","CAP_FACE",FACE,{"disambiguationData":[OSD([makeQuery(id+"F4.imprint","IMPRINT",FACE,{"disambiguationData":[TD([[makeQuery(id+"F4.imprint","IMPRINT",EDGE,{"derivedFrom":sQuery(id+"F4.wireOp",EDGE,"E26.7.0")}),1.0]])]})])],"isStart":true})]}),makeQuery(id+"F15.opLoft","CAP_FACE",FACE,{"disambiguationData":[OSD([makeQuery(id+"F4.imprint","IMPRINT",FACE,{"disambiguationData":[TD([[makeQuery(id+"F4.imprint","IMPRINT",EDGE,{"derivedFrom":sQuery(id+"F4.wireOp",EDGE,"E26.6.0")}),1.0]])]})])],"isStart":true})]}),makeQuery(id+"F16.opLoft","CAP_FACE",FACE,{"disambiguationData":[OSD([makeQuery(id+"F4.imprint","IMPRINT",FACE,{"disambiguationData":[TD([[makeQuery(id+"F4.imprint","IMPRINT",EDGE,{"derivedFrom":sQuery(id+"F4.wireOp",EDGE,"E26.5.0")}),1.0]])]})])],"isStart":true})]}),makeQuery(id+"F17.opLoft","CAP_FACE",FACE,{"disambiguationData":[OSD([makeQuery(id+"F4.imprint","IMPRINT",FACE,{"disambiguationData":[TD([[makeQuery(id+"F4.imprint","IMPRINT",EDGE,{"derivedFrom":sQuery(id+"F4.wireOp",EDGE,"E26.4.0")}),1.0]])]})])],"isStart":true})]}),makeQuery(id+"F18.opLoft","CAP_FACE",FACE,{"disambiguationData":[OSD([makeQuery(id+"F4.imprint","IMPRINT",FACE,{"disambiguationData":[TD([[makeQuery(id+"F4.imprint","IMPRINT",EDGE,{"derivedFrom":sQuery(id+"F4.wireOp",EDGE,"E26.3.0")}),1.0]])]})])],"isStart":true})]}),makeQuery(id+"F19.opLoft","CAP_FACE",FACE,{"disambiguationData":[OSD([makeQuery(id+"F4.imprint","IMPRINT",FACE,{"disambiguationData":[TD([[makeQuery(id+"F4.imprint","IMPRINT",EDGE,{"derivedFrom":sQuery(id+"F4.wireOp",EDGE,"E26.2.0")}),1.0]])]})])],"isStart":true})]}),makeQuery(id+"F20.opLoft","CAP_FACE",FACE,{"disambiguationData":[OSD([makeQuery(id+"F4.imprint","IMPRINT",FACE,{"disambiguationData":[TD([[makeQuery(id+"F4.imprint","IMPRINT",EDGE,{"derivedFrom":sQuery(id+"F4.wireOp",EDGE,"E26.1.0")}),1.0]])]})])],"isStart":true})]}),makeQuery(id+"F42.opRevolve","SWEPT_FACE",FACE,{"disambiguationData":[OSD([sQuery(id+"F41.wireOp",EDGE,"E32")])]})]});
            var Q16;
            Q16=makeQuery(id+"F42.boolean.opBoolean","INTERSECT",EDGE,{"derivedFrom":[makeQuery(id+"F27.opLoft","CAP_FACE",FACE,{"disambiguationData":[OSD([makeQuery(id+"F22.imprint","IMPRINT",FACE,{"disambiguationData":[TD([[makeQuery(id+"F22.imprint","IMPRINT",EDGE,{"derivedFrom":sQuery(id+"F22.wireOp",EDGE,"E28.4.0")}),-1.0]])]})])],"isStart":true}),makeQuery(id+"F42.opRevolve","SWEPT_FACE",FACE,{"disambiguationData":[OSD([sQuery(id+"F41.wireOp",EDGE,"E32")])]})]});
            var Q17;
            Q17=makeQuery(id+"F42.boolean.opBoolean","INTERSECT",EDGE,{"derivedFrom":[makeQuery(id+"F26.opLoft","CAP_FACE",FACE,{"disambiguationData":[OSD([makeQuery(id+"F22.imprint","IMPRINT",FACE,{"disambiguationData":[TD([[makeQuery(id+"F22.imprint","IMPRINT",EDGE,{"derivedFrom":sQuery(id+"F22.wireOp",EDGE,"E28.3.0")}),-1.0]])]})])],"isStart":true}),makeQuery(id+"F42.opRevolve","SWEPT_FACE",FACE,{"disambiguationData":[OSD([sQuery(id+"F41.wireOp",EDGE,"E32")])]})]});
            var Q18;
            Q18=makeQuery(id+"F42.boolean.opBoolean","INTERSECT",EDGE,{"derivedFrom":[makeQuery(id+"F25.opLoft","CAP_FACE",FACE,{"disambiguationData":[OSD([makeQuery(id+"F22.imprint","IMPRINT",FACE,{"disambiguationData":[TD([[makeQuery(id+"F22.imprint","IMPRINT",EDGE,{"derivedFrom":sQuery(id+"F22.wireOp",EDGE,"E28.2.0")}),-1.0]])]})])],"isStart":true}),makeQuery(id+"F42.opRevolve","SWEPT_FACE",FACE,{"disambiguationData":[OSD([sQuery(id+"F41.wireOp",EDGE,"E32")])]})]});
            var Q19;
            Q19=makeQuery(id+"F42.boolean.opBoolean","INTERSECT",EDGE,{"derivedFrom":[makeQuery(id+"F24.opLoft","CAP_FACE",FACE,{"disambiguationData":[OSD([makeQuery(id+"F22.imprint","IMPRINT",FACE,{"disambiguationData":[TD([[makeQuery(id+"F22.imprint","IMPRINT",EDGE,{"derivedFrom":sQuery(id+"F22.wireOp",EDGE,"E28.1.0")}),-1.0]])]})])],"isStart":true}),makeQuery(id+"F42.opRevolve","SWEPT_FACE",FACE,{"disambiguationData":[OSD([sQuery(id+"F41.wireOp",EDGE,"E32")])]})]});
            var Q20;
            Q20=makeQuery(id+"F42.boolean.opBoolean","INTERSECT",EDGE,{"derivedFrom":[makeQuery(id+"F23.opLoft","CAP_FACE",FACE,{"disambiguationData":[OSD([makeQuery(id+"F22.imprint","IMPRINT",FACE,{"disambiguationData":[TD([[makeQuery(id+"F22.imprint","IMPRINT",EDGE,{"derivedFrom":sQuery(id+"F22.wireOp",EDGE,"E27.bottom")}),1.0]])]})])],"isStart":true}),makeQuery(id+"F42.opRevolve","SWEPT_FACE",FACE,{"disambiguationData":[OSD([sQuery(id+"F41.wireOp",EDGE,"E32")])]})]});
            var Q21;
            Q21=makeQuery(id+"F42.boolean.opBoolean","INTERSECT",EDGE,{"derivedFrom":[makeQuery(id+"F38.opLoft","CAP_FACE",FACE,{"disambiguationData":[OSD([makeQuery(id+"F22.imprint","IMPRINT",FACE,{"disambiguationData":[TD([[makeQuery(id+"F22.imprint","IMPRINT",EDGE,{"derivedFrom":sQuery(id+"F22.wireOp",EDGE,"E28.15.0")}),-1.0]])]})])],"isStart":true}),makeQuery(id+"F42.opRevolve","SWEPT_FACE",FACE,{"disambiguationData":[OSD([sQuery(id+"F41.wireOp",EDGE,"E32")])]})]});
            var Q22;
            Q22=makeQuery(id+"F42.boolean.opBoolean","INTERSECT",EDGE,{"derivedFrom":[makeQuery(id+"F37.opLoft","CAP_FACE",FACE,{"disambiguationData":[OSD([makeQuery(id+"F22.imprint","IMPRINT",FACE,{"disambiguationData":[TD([[makeQuery(id+"F22.imprint","IMPRINT",EDGE,{"derivedFrom":sQuery(id+"F22.wireOp",EDGE,"E28.14.0")}),-1.0]])]})])],"isStart":true}),makeQuery(id+"F42.opRevolve","SWEPT_FACE",FACE,{"disambiguationData":[OSD([sQuery(id+"F41.wireOp",EDGE,"E32")])]})]});
            var Q23;
            Q23=makeQuery(id+"F42.boolean.opBoolean","INTERSECT",EDGE,{"derivedFrom":[makeQuery(id+"F36.opLoft","CAP_FACE",FACE,{"disambiguationData":[OSD([makeQuery(id+"F22.imprint","IMPRINT",FACE,{"disambiguationData":[TD([[makeQuery(id+"F22.imprint","IMPRINT",EDGE,{"derivedFrom":sQuery(id+"F22.wireOp",EDGE,"E28.13.0")}),-1.0]])]})])],"isStart":true}),makeQuery(id+"F42.opRevolve","SWEPT_FACE",FACE,{"disambiguationData":[OSD([sQuery(id+"F41.wireOp",EDGE,"E32")])]})]});
            var Q24;
            Q24=makeQuery(id+"F42.boolean.opBoolean","INTERSECT",EDGE,{"derivedFrom":[makeQuery(id+"F35.opLoft","CAP_FACE",FACE,{"disambiguationData":[OSD([makeQuery(id+"F22.imprint","IMPRINT",FACE,{"disambiguationData":[TD([[makeQuery(id+"F22.imprint","IMPRINT",EDGE,{"derivedFrom":sQuery(id+"F22.wireOp",EDGE,"E28.12.0")}),-1.0]])]})])],"isStart":true}),makeQuery(id+"F42.opRevolve","SWEPT_FACE",FACE,{"disambiguationData":[OSD([sQuery(id+"F41.wireOp",EDGE,"E32")])]})]});
            var Q25;
            Q25=makeQuery(id+"F42.boolean.opBoolean","INTERSECT",EDGE,{"derivedFrom":[makeQuery(id+"F34.opLoft","CAP_FACE",FACE,{"disambiguationData":[OSD([makeQuery(id+"F22.imprint","IMPRINT",FACE,{"disambiguationData":[TD([[makeQuery(id+"F22.imprint","IMPRINT",EDGE,{"derivedFrom":sQuery(id+"F22.wireOp",EDGE,"E28.11.0")}),-1.0]])]})])],"isStart":true}),makeQuery(id+"F42.opRevolve","SWEPT_FACE",FACE,{"disambiguationData":[OSD([sQuery(id+"F41.wireOp",EDGE,"E32")])]})]});
            var Q26;
            Q26=makeQuery(id+"F42.boolean.opBoolean","INTERSECT",EDGE,{"derivedFrom":[makeQuery(id+"F33.opLoft","CAP_FACE",FACE,{"disambiguationData":[OSD([makeQuery(id+"F22.imprint","IMPRINT",FACE,{"disambiguationData":[TD([[makeQuery(id+"F22.imprint","IMPRINT",EDGE,{"derivedFrom":sQuery(id+"F22.wireOp",EDGE,"E28.10.0")}),-1.0]])]})])],"isStart":true}),makeQuery(id+"F42.opRevolve","SWEPT_FACE",FACE,{"disambiguationData":[OSD([sQuery(id+"F41.wireOp",EDGE,"E32")])]})]});
            var Q27;
            Q27=makeQuery(id+"F42.boolean.opBoolean","INTERSECT",EDGE,{"derivedFrom":[makeQuery(id+"F32.opLoft","CAP_FACE",FACE,{"disambiguationData":[OSD([makeQuery(id+"F22.imprint","IMPRINT",FACE,{"disambiguationData":[TD([[makeQuery(id+"F22.imprint","IMPRINT",EDGE,{"derivedFrom":sQuery(id+"F22.wireOp",EDGE,"E28.9.0")}),-1.0]])]})])],"isStart":true}),makeQuery(id+"F42.opRevolve","SWEPT_FACE",FACE,{"disambiguationData":[OSD([sQuery(id+"F41.wireOp",EDGE,"E32")])]})]});
            var Q28;
            Q28=makeQuery(id+"F42.boolean.opBoolean","INTERSECT",EDGE,{"derivedFrom":[makeQuery(id+"F31.opLoft","CAP_FACE",FACE,{"disambiguationData":[OSD([makeQuery(id+"F22.imprint","IMPRINT",FACE,{"disambiguationData":[TD([[makeQuery(id+"F22.imprint","IMPRINT",EDGE,{"derivedFrom":sQuery(id+"F22.wireOp",EDGE,"E28.8.0")}),-1.0]])]})])],"isStart":true}),makeQuery(id+"F42.opRevolve","SWEPT_FACE",FACE,{"disambiguationData":[OSD([sQuery(id+"F41.wireOp",EDGE,"E32")])]})]});
            var Q29;
            Q29=makeQuery(id+"F42.boolean.opBoolean","INTERSECT",EDGE,{"derivedFrom":[makeQuery(id+"F30.opLoft","CAP_FACE",FACE,{"disambiguationData":[OSD([makeQuery(id+"F22.imprint","IMPRINT",FACE,{"disambiguationData":[TD([[makeQuery(id+"F22.imprint","IMPRINT",EDGE,{"derivedFrom":sQuery(id+"F22.wireOp",EDGE,"E28.7.0")}),-1.0]])]})])],"isStart":true}),makeQuery(id+"F42.opRevolve","SWEPT_FACE",FACE,{"disambiguationData":[OSD([sQuery(id+"F41.wireOp",EDGE,"E32")])]})]});
            var Q30;
            Q30=makeQuery(id+"F42.boolean.opBoolean","INTERSECT",EDGE,{"derivedFrom":[makeQuery(id+"F29.opLoft","CAP_FACE",FACE,{"disambiguationData":[OSD([makeQuery(id+"F22.imprint","IMPRINT",FACE,{"disambiguationData":[TD([[makeQuery(id+"F22.imprint","IMPRINT",EDGE,{"derivedFrom":sQuery(id+"F22.wireOp",EDGE,"E28.6.0")}),-1.0]])]})])],"isStart":true}),makeQuery(id+"F42.opRevolve","SWEPT_FACE",FACE,{"disambiguationData":[OSD([sQuery(id+"F41.wireOp",EDGE,"E32")])]})]});
            var Q31;
            Q31=makeQuery(id+"F42.boolean.opBoolean","INTERSECT",EDGE,{"derivedFrom":[makeQuery(id+"F28.opLoft","CAP_FACE",FACE,{"disambiguationData":[OSD([makeQuery(id+"F22.imprint","IMPRINT",FACE,{"disambiguationData":[TD([[makeQuery(id+"F22.imprint","IMPRINT",EDGE,{"derivedFrom":sQuery(id+"F22.wireOp",EDGE,"E28.5.0")}),-1.0]])]})])],"isStart":true}),makeQuery(id+"F42.opRevolve","SWEPT_FACE",FACE,{"disambiguationData":[OSD([sQuery(id+"F41.wireOp",EDGE,"E32")])]})]});
            fillet(context, id + "F43", {"entities" : qUnion([Q0, Q1, Q2, Q3, Q4, Q5, Q6, Q7, Q8, Q9, Q10, Q11, Q12, Q13, Q14, Q15, Q16, Q17, Q18, Q19, Q20, Q21, Q22, Q23, Q24, Q25, Q26, Q27, Q28, Q29, Q30, Q31]), "radius" : 10 * mm, "tangentPropagation" : true, "allowEdgeOverflow" : false});
        }
        {
            var Q0;
            Q0=makeQuery(id+"F40.boolean.opBoolean","INTERSECT",EDGE,{"derivedFrom":[makeQuery(id+"F20.opLoft","SWEPT_FACE",FACE,{"disambiguationData":[OSD([sQuery(id+"F3.wireOp",EDGE,"E20.1.1"),sQuery(id+"F3.wireOp",EDGE,"E20.1.2"),sQuery(id+"F3.wireOp",EDGE,"E20.1.3"),sQuery(id+"F4.wireOp",EDGE,"E26.1.1"),sQuery(id+"F4.wireOp",EDGE,"E26.1.2"),sQuery(id+"F4.wireOp",EDGE,"E26.1.3")])]}),makeQuery(id+"F40.opExtrude","CAP_FACE",FACE,{"disambiguationData":[OSD([sQuery(id+"F39.wireOp",EDGE,"E29"),sQuery(id+"F39.wireOp",EDGE,"E30")])],"isStart":false})]});
            var Q1;
            Q1=makeQuery(id+"F40.boolean.opBoolean","INTERSECT",EDGE,{"derivedFrom":[makeQuery(id+"F32.opLoft","SWEPT_FACE",FACE,{"disambiguationData":[OSD([sQuery(id+"F3.wireOp",EDGE,"E20.1.1"),sQuery(id+"F3.wireOp",EDGE,"E20.1.2"),sQuery(id+"F3.wireOp",EDGE,"E20.1.3"),sQuery(id+"F22.wireOp",EDGE,"E28.9.0"),sQuery(id+"F22.wireOp",EDGE,"E28.9.2"),sQuery(id+"F22.wireOp",EDGE,"E28.9.3")])]}),makeQuery(id+"F40.opExtrude","CAP_FACE",FACE,{"disambiguationData":[OSD([sQuery(id+"F39.wireOp",EDGE,"E29"),sQuery(id+"F39.wireOp",EDGE,"E30")])],"isStart":true})]});
            var Q2;
            Q2=makeQuery(id+"F40.boolean.opBoolean","INTERSECT",EDGE,{"derivedFrom":[makeQuery(id+"F5.opLoft","SWEPT_FACE",FACE,{"disambiguationData":[OSD([sQuery(id+"F3.wireOp",EDGE,"E18.bottom"),sQuery(id+"F3.wireOp",EDGE,"E18.top"),sQuery(id+"F3.wireOp",EDGE,"E18.right"),sQuery(id+"F4.wireOp",EDGE,"E22"),sQuery(id+"F4.wireOp",EDGE,"E23"),sQuery(id+"F4.wireOp",EDGE,"E24")])]}),makeQuery(id+"F40.opExtrude","CAP_FACE",FACE,{"disambiguationData":[OSD([sQuery(id+"F39.wireOp",EDGE,"E29"),sQuery(id+"F39.wireOp",EDGE,"E30")])],"isStart":false})]});
            var Q3;
            Q3=makeQuery(id+"F40.boolean.opBoolean","INTERSECT",EDGE,{"derivedFrom":[makeQuery(id+"F31.opLoft","SWEPT_FACE",FACE,{"disambiguationData":[OSD([sQuery(id+"F3.wireOp",EDGE,"E18.bottom"),sQuery(id+"F3.wireOp",EDGE,"E18.top"),sQuery(id+"F3.wireOp",EDGE,"E18.right"),sQuery(id+"F22.wireOp",EDGE,"E28.8.0"),sQuery(id+"F22.wireOp",EDGE,"E28.8.2"),sQuery(id+"F22.wireOp",EDGE,"E28.8.3")])]}),makeQuery(id+"F40.opExtrude","CAP_FACE",FACE,{"disambiguationData":[OSD([sQuery(id+"F39.wireOp",EDGE,"E29"),sQuery(id+"F39.wireOp",EDGE,"E30")])],"isStart":true})]});
            var Q4;
            Q4=makeQuery(id+"F40.boolean.opBoolean","INTERSECT",EDGE,{"derivedFrom":[makeQuery(id+"F6.opLoft","SWEPT_FACE",FACE,{"disambiguationData":[OSD([sQuery(id+"F3.wireOp",EDGE,"E20.15.1"),sQuery(id+"F3.wireOp",EDGE,"E20.15.2"),sQuery(id+"F3.wireOp",EDGE,"E20.15.3"),sQuery(id+"F4.wireOp",EDGE,"E26.15.1"),sQuery(id+"F4.wireOp",EDGE,"E26.15.2"),sQuery(id+"F4.wireOp",EDGE,"E26.15.3")])]}),makeQuery(id+"F40.opExtrude","CAP_FACE",FACE,{"disambiguationData":[OSD([sQuery(id+"F39.wireOp",EDGE,"E29"),sQuery(id+"F39.wireOp",EDGE,"E30")])],"isStart":false})]});
            var Q5;
            Q5=makeQuery(id+"F40.boolean.opBoolean","INTERSECT",EDGE,{"derivedFrom":[makeQuery(id+"F30.opLoft","SWEPT_FACE",FACE,{"disambiguationData":[OSD([sQuery(id+"F3.wireOp",EDGE,"E20.15.1"),sQuery(id+"F3.wireOp",EDGE,"E20.15.2"),sQuery(id+"F3.wireOp",EDGE,"E20.15.3"),sQuery(id+"F22.wireOp",EDGE,"E28.7.0"),sQuery(id+"F22.wireOp",EDGE,"E28.7.2"),sQuery(id+"F22.wireOp",EDGE,"E28.7.3")])]}),makeQuery(id+"F40.opExtrude","CAP_FACE",FACE,{"disambiguationData":[OSD([sQuery(id+"F39.wireOp",EDGE,"E29"),sQuery(id+"F39.wireOp",EDGE,"E30")])],"isStart":true})]});
            var Q6;
            Q6=makeQuery(id+"F40.boolean.opBoolean","INTERSECT",EDGE,{"derivedFrom":[makeQuery(id+"F29.opLoft","SWEPT_FACE",FACE,{"disambiguationData":[OSD([sQuery(id+"F3.wireOp",EDGE,"E20.14.1"),sQuery(id+"F3.wireOp",EDGE,"E20.14.2"),sQuery(id+"F3.wireOp",EDGE,"E20.14.3"),sQuery(id+"F22.wireOp",EDGE,"E28.6.0"),sQuery(id+"F22.wireOp",EDGE,"E28.6.2"),sQuery(id+"F22.wireOp",EDGE,"E28.6.3")])]}),makeQuery(id+"F40.opExtrude","CAP_FACE",FACE,{"disambiguationData":[OSD([sQuery(id+"F39.wireOp",EDGE,"E29"),sQuery(id+"F39.wireOp",EDGE,"E30")])],"isStart":true})]});
            var Q7;
            Q7=makeQuery(id+"F40.boolean.opBoolean","INTERSECT",EDGE,{"derivedFrom":[makeQuery(id+"F28.opLoft","SWEPT_FACE",FACE,{"disambiguationData":[OSD([sQuery(id+"F3.wireOp",EDGE,"E20.13.1"),sQuery(id+"F3.wireOp",EDGE,"E20.13.2"),sQuery(id+"F3.wireOp",EDGE,"E20.13.3"),sQuery(id+"F22.wireOp",EDGE,"E28.5.0"),sQuery(id+"F22.wireOp",EDGE,"E28.5.2"),sQuery(id+"F22.wireOp",EDGE,"E28.5.3")])]}),makeQuery(id+"F40.opExtrude","CAP_FACE",FACE,{"disambiguationData":[OSD([sQuery(id+"F39.wireOp",EDGE,"E29"),sQuery(id+"F39.wireOp",EDGE,"E30")])],"isStart":true})]});
            var Q8;
            Q8=makeQuery(id+"F40.boolean.opBoolean","INTERSECT",EDGE,{"derivedFrom":[makeQuery(id+"F27.opLoft","SWEPT_FACE",FACE,{"disambiguationData":[OSD([sQuery(id+"F3.wireOp",EDGE,"E20.12.1"),sQuery(id+"F3.wireOp",EDGE,"E20.12.2"),sQuery(id+"F3.wireOp",EDGE,"E20.12.3"),sQuery(id+"F22.wireOp",EDGE,"E28.4.0"),sQuery(id+"F22.wireOp",EDGE,"E28.4.2"),sQuery(id+"F22.wireOp",EDGE,"E28.4.3")])]}),makeQuery(id+"F40.opExtrude","CAP_FACE",FACE,{"disambiguationData":[OSD([sQuery(id+"F39.wireOp",EDGE,"E29"),sQuery(id+"F39.wireOp",EDGE,"E30")])],"isStart":true})]});
            var Q9;
            Q9=makeQuery(id+"F40.boolean.opBoolean","INTERSECT",EDGE,{"derivedFrom":[makeQuery(id+"F26.opLoft","SWEPT_FACE",FACE,{"disambiguationData":[OSD([sQuery(id+"F3.wireOp",EDGE,"E20.11.1"),sQuery(id+"F3.wireOp",EDGE,"E20.11.2"),sQuery(id+"F3.wireOp",EDGE,"E20.11.3"),sQuery(id+"F22.wireOp",EDGE,"E28.3.0"),sQuery(id+"F22.wireOp",EDGE,"E28.3.2"),sQuery(id+"F22.wireOp",EDGE,"E28.3.3")])]}),makeQuery(id+"F40.opExtrude","CAP_FACE",FACE,{"disambiguationData":[OSD([sQuery(id+"F39.wireOp",EDGE,"E29"),sQuery(id+"F39.wireOp",EDGE,"E30")])],"isStart":true})]});
            var Q10;
            Q10=makeQuery(id+"F40.boolean.opBoolean","INTERSECT",EDGE,{"derivedFrom":[makeQuery(id+"F25.opLoft","SWEPT_FACE",FACE,{"disambiguationData":[OSD([sQuery(id+"F3.wireOp",EDGE,"E20.10.1"),sQuery(id+"F3.wireOp",EDGE,"E20.10.2"),sQuery(id+"F3.wireOp",EDGE,"E20.10.3"),sQuery(id+"F22.wireOp",EDGE,"E28.2.0"),sQuery(id+"F22.wireOp",EDGE,"E28.2.2"),sQuery(id+"F22.wireOp",EDGE,"E28.2.3")])]}),makeQuery(id+"F40.opExtrude","CAP_FACE",FACE,{"disambiguationData":[OSD([sQuery(id+"F39.wireOp",EDGE,"E29"),sQuery(id+"F39.wireOp",EDGE,"E30")])],"isStart":true})]});
            var Q11;
            Q11=makeQuery(id+"F40.boolean.opBoolean","INTERSECT",EDGE,{"derivedFrom":[makeQuery(id+"F24.opLoft","SWEPT_FACE",FACE,{"disambiguationData":[OSD([sQuery(id+"F3.wireOp",EDGE,"E20.9.1"),sQuery(id+"F3.wireOp",EDGE,"E20.9.2"),sQuery(id+"F3.wireOp",EDGE,"E20.9.3"),sQuery(id+"F22.wireOp",EDGE,"E28.1.0"),sQuery(id+"F22.wireOp",EDGE,"E28.1.2"),sQuery(id+"F22.wireOp",EDGE,"E28.1.3")])]}),makeQuery(id+"F40.opExtrude","CAP_FACE",FACE,{"disambiguationData":[OSD([sQuery(id+"F39.wireOp",EDGE,"E29"),sQuery(id+"F39.wireOp",EDGE,"E30")])],"isStart":true})]});
            var Q12;
            Q12=makeQuery(id+"F40.boolean.opBoolean","INTERSECT",EDGE,{"derivedFrom":[makeQuery(id+"F23.opLoft","SWEPT_FACE",FACE,{"disambiguationData":[OSD([sQuery(id+"F3.wireOp",EDGE,"E20.8.1"),sQuery(id+"F3.wireOp",EDGE,"E20.8.2"),sQuery(id+"F3.wireOp",EDGE,"E20.8.3"),sQuery(id+"F22.wireOp",EDGE,"E27.bottom"),sQuery(id+"F22.wireOp",EDGE,"E27.top"),sQuery(id+"F22.wireOp",EDGE,"E27.left")])]}),makeQuery(id+"F40.opExtrude","CAP_FACE",FACE,{"disambiguationData":[OSD([sQuery(id+"F39.wireOp",EDGE,"E29"),sQuery(id+"F39.wireOp",EDGE,"E30")])],"isStart":true})]});
            var Q13;
            Q13=makeQuery(id+"F40.boolean.opBoolean","INTERSECT",EDGE,{"derivedFrom":[makeQuery(id+"F38.opLoft","SWEPT_FACE",FACE,{"disambiguationData":[OSD([sQuery(id+"F3.wireOp",EDGE,"E20.7.1"),sQuery(id+"F3.wireOp",EDGE,"E20.7.2"),sQuery(id+"F3.wireOp",EDGE,"E20.7.3"),sQuery(id+"F22.wireOp",EDGE,"E28.15.0"),sQuery(id+"F22.wireOp",EDGE,"E28.15.2"),sQuery(id+"F22.wireOp",EDGE,"E28.15.3")])]}),makeQuery(id+"F40.opExtrude","CAP_FACE",FACE,{"disambiguationData":[OSD([sQuery(id+"F39.wireOp",EDGE,"E29"),sQuery(id+"F39.wireOp",EDGE,"E30")])],"isStart":true})]});
            var Q14;
            Q14=makeQuery(id+"F40.boolean.opBoolean","INTERSECT",EDGE,{"derivedFrom":[makeQuery(id+"F37.opLoft","SWEPT_FACE",FACE,{"disambiguationData":[OSD([sQuery(id+"F3.wireOp",EDGE,"E20.6.1"),sQuery(id+"F3.wireOp",EDGE,"E20.6.2"),sQuery(id+"F3.wireOp",EDGE,"E20.6.3"),sQuery(id+"F22.wireOp",EDGE,"E28.14.0"),sQuery(id+"F22.wireOp",EDGE,"E28.14.2"),sQuery(id+"F22.wireOp",EDGE,"E28.14.3")])]}),makeQuery(id+"F40.opExtrude","CAP_FACE",FACE,{"disambiguationData":[OSD([sQuery(id+"F39.wireOp",EDGE,"E29"),sQuery(id+"F39.wireOp",EDGE,"E30")])],"isStart":true})]});
            var Q15;
            Q15=makeQuery(id+"F40.boolean.opBoolean","INTERSECT",EDGE,{"derivedFrom":[makeQuery(id+"F36.opLoft","SWEPT_FACE",FACE,{"disambiguationData":[OSD([sQuery(id+"F3.wireOp",EDGE,"E20.5.1"),sQuery(id+"F3.wireOp",EDGE,"E20.5.2"),sQuery(id+"F3.wireOp",EDGE,"E20.5.3"),sQuery(id+"F22.wireOp",EDGE,"E28.13.0"),sQuery(id+"F22.wireOp",EDGE,"E28.13.2"),sQuery(id+"F22.wireOp",EDGE,"E28.13.3")])]}),makeQuery(id+"F40.opExtrude","CAP_FACE",FACE,{"disambiguationData":[OSD([sQuery(id+"F39.wireOp",EDGE,"E29"),sQuery(id+"F39.wireOp",EDGE,"E30")])],"isStart":true})]});
            var Q16;
            Q16=makeQuery(id+"F40.boolean.opBoolean","INTERSECT",EDGE,{"derivedFrom":[makeQuery(id+"F35.opLoft","SWEPT_FACE",FACE,{"disambiguationData":[OSD([sQuery(id+"F3.wireOp",EDGE,"E20.4.1"),sQuery(id+"F3.wireOp",EDGE,"E20.4.2"),sQuery(id+"F3.wireOp",EDGE,"E20.4.3"),sQuery(id+"F22.wireOp",EDGE,"E28.12.0"),sQuery(id+"F22.wireOp",EDGE,"E28.12.2"),sQuery(id+"F22.wireOp",EDGE,"E28.12.3")])]}),makeQuery(id+"F40.opExtrude","CAP_FACE",FACE,{"disambiguationData":[OSD([sQuery(id+"F39.wireOp",EDGE,"E29"),sQuery(id+"F39.wireOp",EDGE,"E30")])],"isStart":true})]});
            var Q17;
            Q17=makeQuery(id+"F40.boolean.opBoolean","INTERSECT",EDGE,{"derivedFrom":[makeQuery(id+"F34.opLoft","SWEPT_FACE",FACE,{"disambiguationData":[OSD([sQuery(id+"F3.wireOp",EDGE,"E20.3.1"),sQuery(id+"F3.wireOp",EDGE,"E20.3.2"),sQuery(id+"F3.wireOp",EDGE,"E20.3.3"),sQuery(id+"F22.wireOp",EDGE,"E28.11.0"),sQuery(id+"F22.wireOp",EDGE,"E28.11.2"),sQuery(id+"F22.wireOp",EDGE,"E28.11.3")])]}),makeQuery(id+"F40.opExtrude","CAP_FACE",FACE,{"disambiguationData":[OSD([sQuery(id+"F39.wireOp",EDGE,"E29"),sQuery(id+"F39.wireOp",EDGE,"E30")])],"isStart":true})]});
            var Q18;
            Q18=makeQuery(id+"F40.boolean.opBoolean","INTERSECT",EDGE,{"derivedFrom":[makeQuery(id+"F33.opLoft","SWEPT_FACE",FACE,{"disambiguationData":[OSD([sQuery(id+"F3.wireOp",EDGE,"E20.2.1"),sQuery(id+"F3.wireOp",EDGE,"E20.2.2"),sQuery(id+"F3.wireOp",EDGE,"E20.2.3"),sQuery(id+"F22.wireOp",EDGE,"E28.10.0"),sQuery(id+"F22.wireOp",EDGE,"E28.10.2"),sQuery(id+"F22.wireOp",EDGE,"E28.10.3")])]}),makeQuery(id+"F40.opExtrude","CAP_FACE",FACE,{"disambiguationData":[OSD([sQuery(id+"F39.wireOp",EDGE,"E29"),sQuery(id+"F39.wireOp",EDGE,"E30")])],"isStart":true})]});
            var Q19;
            Q19=makeQuery(id+"F40.boolean.opBoolean","INTERSECT",EDGE,{"derivedFrom":[makeQuery(id+"F19.opLoft","SWEPT_FACE",FACE,{"disambiguationData":[OSD([sQuery(id+"F3.wireOp",EDGE,"E20.2.1"),sQuery(id+"F3.wireOp",EDGE,"E20.2.2"),sQuery(id+"F3.wireOp",EDGE,"E20.2.3"),sQuery(id+"F4.wireOp",EDGE,"E26.2.1"),sQuery(id+"F4.wireOp",EDGE,"E26.2.2"),sQuery(id+"F4.wireOp",EDGE,"E26.2.3")])]}),makeQuery(id+"F40.opExtrude","CAP_FACE",FACE,{"disambiguationData":[OSD([sQuery(id+"F39.wireOp",EDGE,"E29"),sQuery(id+"F39.wireOp",EDGE,"E30")])],"isStart":false})]});
            var Q20;
            Q20=makeQuery(id+"F40.boolean.opBoolean","INTERSECT",EDGE,{"derivedFrom":[makeQuery(id+"F18.opLoft","SWEPT_FACE",FACE,{"disambiguationData":[OSD([sQuery(id+"F3.wireOp",EDGE,"E20.3.1"),sQuery(id+"F3.wireOp",EDGE,"E20.3.2"),sQuery(id+"F3.wireOp",EDGE,"E20.3.3"),sQuery(id+"F4.wireOp",EDGE,"E26.3.1"),sQuery(id+"F4.wireOp",EDGE,"E26.3.2"),sQuery(id+"F4.wireOp",EDGE,"E26.3.3")])]}),makeQuery(id+"F40.opExtrude","CAP_FACE",FACE,{"disambiguationData":[OSD([sQuery(id+"F39.wireOp",EDGE,"E29"),sQuery(id+"F39.wireOp",EDGE,"E30")])],"isStart":false})]});
            var Q21;
            Q21=makeQuery(id+"F40.boolean.opBoolean","INTERSECT",EDGE,{"derivedFrom":[makeQuery(id+"F17.opLoft","SWEPT_FACE",FACE,{"disambiguationData":[OSD([sQuery(id+"F3.wireOp",EDGE,"E20.4.1"),sQuery(id+"F3.wireOp",EDGE,"E20.4.2"),sQuery(id+"F3.wireOp",EDGE,"E20.4.3"),sQuery(id+"F4.wireOp",EDGE,"E26.4.1"),sQuery(id+"F4.wireOp",EDGE,"E26.4.2"),sQuery(id+"F4.wireOp",EDGE,"E26.4.3")])]}),makeQuery(id+"F40.opExtrude","CAP_FACE",FACE,{"disambiguationData":[OSD([sQuery(id+"F39.wireOp",EDGE,"E29"),sQuery(id+"F39.wireOp",EDGE,"E30")])],"isStart":false})]});
            var Q22;
            Q22=makeQuery(id+"F40.boolean.opBoolean","INTERSECT",EDGE,{"derivedFrom":[makeQuery(id+"F16.opLoft","SWEPT_FACE",FACE,{"disambiguationData":[OSD([sQuery(id+"F3.wireOp",EDGE,"E20.5.1"),sQuery(id+"F3.wireOp",EDGE,"E20.5.2"),sQuery(id+"F3.wireOp",EDGE,"E20.5.3"),sQuery(id+"F4.wireOp",EDGE,"E26.5.1"),sQuery(id+"F4.wireOp",EDGE,"E26.5.2"),sQuery(id+"F4.wireOp",EDGE,"E26.5.3")])]}),makeQuery(id+"F40.opExtrude","CAP_FACE",FACE,{"disambiguationData":[OSD([sQuery(id+"F39.wireOp",EDGE,"E29"),sQuery(id+"F39.wireOp",EDGE,"E30")])],"isStart":false})]});
            var Q23;
            Q23=makeQuery(id+"F40.boolean.opBoolean","INTERSECT",EDGE,{"derivedFrom":[makeQuery(id+"F15.opLoft","SWEPT_FACE",FACE,{"disambiguationData":[OSD([sQuery(id+"F3.wireOp",EDGE,"E20.6.1"),sQuery(id+"F3.wireOp",EDGE,"E20.6.2"),sQuery(id+"F3.wireOp",EDGE,"E20.6.3"),sQuery(id+"F4.wireOp",EDGE,"E26.6.1"),sQuery(id+"F4.wireOp",EDGE,"E26.6.2"),sQuery(id+"F4.wireOp",EDGE,"E26.6.3")])]}),makeQuery(id+"F40.opExtrude","CAP_FACE",FACE,{"disambiguationData":[OSD([sQuery(id+"F39.wireOp",EDGE,"E29"),sQuery(id+"F39.wireOp",EDGE,"E30")])],"isStart":false})]});
            var Q24;
            Q24=makeQuery(id+"F40.boolean.opBoolean","INTERSECT",EDGE,{"derivedFrom":[makeQuery(id+"F14.opLoft","SWEPT_FACE",FACE,{"disambiguationData":[OSD([sQuery(id+"F3.wireOp",EDGE,"E20.7.1"),sQuery(id+"F3.wireOp",EDGE,"E20.7.2"),sQuery(id+"F3.wireOp",EDGE,"E20.7.3"),sQuery(id+"F4.wireOp",EDGE,"E26.7.1"),sQuery(id+"F4.wireOp",EDGE,"E26.7.2"),sQuery(id+"F4.wireOp",EDGE,"E26.7.3")])]}),makeQuery(id+"F40.opExtrude","CAP_FACE",FACE,{"disambiguationData":[OSD([sQuery(id+"F39.wireOp",EDGE,"E29"),sQuery(id+"F39.wireOp",EDGE,"E30")])],"isStart":false})]});
            var Q25;
            Q25=makeQuery(id+"F40.boolean.opBoolean","INTERSECT",EDGE,{"derivedFrom":[makeQuery(id+"F13.opLoft","SWEPT_FACE",FACE,{"disambiguationData":[OSD([sQuery(id+"F3.wireOp",EDGE,"E20.8.1"),sQuery(id+"F3.wireOp",EDGE,"E20.8.2"),sQuery(id+"F3.wireOp",EDGE,"E20.8.3"),sQuery(id+"F4.wireOp",EDGE,"E26.8.1"),sQuery(id+"F4.wireOp",EDGE,"E26.8.2"),sQuery(id+"F4.wireOp",EDGE,"E26.8.3")])]}),makeQuery(id+"F40.opExtrude","CAP_FACE",FACE,{"disambiguationData":[OSD([sQuery(id+"F39.wireOp",EDGE,"E29"),sQuery(id+"F39.wireOp",EDGE,"E30")])],"isStart":false})]});
            var Q26;
            Q26=makeQuery(id+"F40.boolean.opBoolean","INTERSECT",EDGE,{"derivedFrom":[makeQuery(id+"F12.opLoft","SWEPT_FACE",FACE,{"disambiguationData":[OSD([sQuery(id+"F3.wireOp",EDGE,"E20.9.1"),sQuery(id+"F3.wireOp",EDGE,"E20.9.2"),sQuery(id+"F3.wireOp",EDGE,"E20.9.3"),sQuery(id+"F4.wireOp",EDGE,"E26.9.1"),sQuery(id+"F4.wireOp",EDGE,"E26.9.2"),sQuery(id+"F4.wireOp",EDGE,"E26.9.3")])]}),makeQuery(id+"F40.opExtrude","CAP_FACE",FACE,{"disambiguationData":[OSD([sQuery(id+"F39.wireOp",EDGE,"E29"),sQuery(id+"F39.wireOp",EDGE,"E30")])],"isStart":false})]});
            var Q27;
            Q27=makeQuery(id+"F40.boolean.opBoolean","INTERSECT",EDGE,{"derivedFrom":[makeQuery(id+"F11.opLoft","SWEPT_FACE",FACE,{"disambiguationData":[OSD([sQuery(id+"F3.wireOp",EDGE,"E20.10.1"),sQuery(id+"F3.wireOp",EDGE,"E20.10.2"),sQuery(id+"F3.wireOp",EDGE,"E20.10.3"),sQuery(id+"F4.wireOp",EDGE,"E26.10.1"),sQuery(id+"F4.wireOp",EDGE,"E26.10.2"),sQuery(id+"F4.wireOp",EDGE,"E26.10.3")])]}),makeQuery(id+"F40.opExtrude","CAP_FACE",FACE,{"disambiguationData":[OSD([sQuery(id+"F39.wireOp",EDGE,"E29"),sQuery(id+"F39.wireOp",EDGE,"E30")])],"isStart":false})]});
            var Q28;
            Q28=makeQuery(id+"F40.boolean.opBoolean","INTERSECT",EDGE,{"derivedFrom":[makeQuery(id+"F10.opLoft","SWEPT_FACE",FACE,{"disambiguationData":[OSD([sQuery(id+"F3.wireOp",EDGE,"E20.11.1"),sQuery(id+"F3.wireOp",EDGE,"E20.11.2"),sQuery(id+"F3.wireOp",EDGE,"E20.11.3"),sQuery(id+"F4.wireOp",EDGE,"E26.11.1"),sQuery(id+"F4.wireOp",EDGE,"E26.11.2"),sQuery(id+"F4.wireOp",EDGE,"E26.11.3")])]}),makeQuery(id+"F40.opExtrude","CAP_FACE",FACE,{"disambiguationData":[OSD([sQuery(id+"F39.wireOp",EDGE,"E29"),sQuery(id+"F39.wireOp",EDGE,"E30")])],"isStart":false})]});
            var Q29;
            Q29=makeQuery(id+"F40.boolean.opBoolean","INTERSECT",EDGE,{"derivedFrom":[makeQuery(id+"F9.opLoft","SWEPT_FACE",FACE,{"disambiguationData":[OSD([sQuery(id+"F3.wireOp",EDGE,"E20.12.1"),sQuery(id+"F3.wireOp",EDGE,"E20.12.2"),sQuery(id+"F3.wireOp",EDGE,"E20.12.3"),sQuery(id+"F4.wireOp",EDGE,"E26.12.1"),sQuery(id+"F4.wireOp",EDGE,"E26.12.2"),sQuery(id+"F4.wireOp",EDGE,"E26.12.3")])]}),makeQuery(id+"F40.opExtrude","CAP_FACE",FACE,{"disambiguationData":[OSD([sQuery(id+"F39.wireOp",EDGE,"E29"),sQuery(id+"F39.wireOp",EDGE,"E30")])],"isStart":false})]});
            var Q30;
            Q30=makeQuery(id+"F40.boolean.opBoolean","INTERSECT",EDGE,{"derivedFrom":[makeQuery(id+"F8.opLoft","SWEPT_FACE",FACE,{"disambiguationData":[OSD([sQuery(id+"F3.wireOp",EDGE,"E20.13.1"),sQuery(id+"F3.wireOp",EDGE,"E20.13.2"),sQuery(id+"F3.wireOp",EDGE,"E20.13.3"),sQuery(id+"F4.wireOp",EDGE,"E26.13.1"),sQuery(id+"F4.wireOp",EDGE,"E26.13.2"),sQuery(id+"F4.wireOp",EDGE,"E26.13.3")])]}),makeQuery(id+"F40.opExtrude","CAP_FACE",FACE,{"disambiguationData":[OSD([sQuery(id+"F39.wireOp",EDGE,"E29"),sQuery(id+"F39.wireOp",EDGE,"E30")])],"isStart":false})]});
            var Q31;
            Q31=makeQuery(id+"F40.boolean.opBoolean","INTERSECT",EDGE,{"derivedFrom":[makeQuery(id+"F7.opLoft","SWEPT_FACE",FACE,{"disambiguationData":[OSD([sQuery(id+"F3.wireOp",EDGE,"E20.14.1"),sQuery(id+"F3.wireOp",EDGE,"E20.14.2"),sQuery(id+"F3.wireOp",EDGE,"E20.14.3"),sQuery(id+"F4.wireOp",EDGE,"E26.14.1"),sQuery(id+"F4.wireOp",EDGE,"E26.14.2"),sQuery(id+"F4.wireOp",EDGE,"E26.14.3")])]}),makeQuery(id+"F40.opExtrude","CAP_FACE",FACE,{"disambiguationData":[OSD([sQuery(id+"F39.wireOp",EDGE,"E29"),sQuery(id+"F39.wireOp",EDGE,"E30")])],"isStart":false})]});
            fillet(context, id + "F44", {"entities" : qUnion([Q0, Q1, Q2, Q3, Q4, Q5, Q6, Q7, Q8, Q9, Q10, Q11, Q12, Q13, Q14, Q15, Q16, Q17, Q18, Q19, Q20, Q21, Q22, Q23, Q24, Q25, Q26, Q27, Q28, Q29, Q30, Q31]), "radius" : 20 * mm, "tangentPropagation" : true, "allowEdgeOverflow" : false});
        }
        {
            var Q0;
            Q0=makeQuery(id+"F19.boolean.opBoolean","INTERSECT",EDGE,{"derivedFrom":[makeQuery(id+"F1.opRevolve","SWEPT_FACE",FACE,{"disambiguationData":[OSD([sQuery(id+"F0.wireOp",EDGE,"E4")])]}),makeQuery(id+"F19.opLoft","SWEPT_FACE",FACE,{"disambiguationData":[OSD([sQuery(id+"F3.wireOp",EDGE,"E20.2.0"),sQuery(id+"F3.wireOp",EDGE,"E20.2.1"),sQuery(id+"F3.wireOp",EDGE,"E20.2.3"),sQuery(id+"F4.wireOp",EDGE,"E26.2.0"),sQuery(id+"F4.wireOp",EDGE,"E26.2.2"),sQuery(id+"F4.wireOp",EDGE,"E26.2.3")])]})]});
            var Q1;
            Q1=makeQuery(id+"F20.boolean.opBoolean","INTERSECT",EDGE,{"derivedFrom":[makeQuery(id+"F1.opRevolve","SWEPT_FACE",FACE,{"disambiguationData":[OSD([sQuery(id+"F0.wireOp",EDGE,"E4")])]}),makeQuery(id+"F20.opLoft","SWEPT_FACE",FACE,{"disambiguationData":[OSD([sQuery(id+"F3.wireOp",EDGE,"E20.1.0"),sQuery(id+"F3.wireOp",EDGE,"E20.1.1"),sQuery(id+"F3.wireOp",EDGE,"E20.1.3"),sQuery(id+"F4.wireOp",EDGE,"E26.1.0"),sQuery(id+"F4.wireOp",EDGE,"E26.1.2"),sQuery(id+"F4.wireOp",EDGE,"E26.1.3")])]})]});
            var Q2;
            {var subQ0=sQuery(id+"F3.wireOp",EDGE,"E20.1.3");var subQ1=sQuery(id+"F3.wireOp",EDGE,"E20.1.1");var subQ2=sQuery(id+"F3.wireOp",EDGE,"E20.1.0");var subQ51=sQuery(id+"F3.wireOp",EDGE,"E18.bottom");var subQ62=sQuery(id+"F3.wireOp",EDGE,"E20.7.0");var subQ70=makeQuery(id+"F14.opLoft","CAP_FACE",FACE,{"disambiguationData":[OSD([makeQuery(id+"F3.imprint","IMPRINT",FACE,{"disambiguationData":[TD([[makeQuery(id+"F3.imprint","IMPRINT",EDGE,{"derivedFrom":subQ62}),-1.0]])]})])],"isStart":true});var subQ78=makeQuery(id+"F5.opLoft","CAP_FACE",FACE,{"disambiguationData":[OSD([makeQuery(id+"F3.imprint","IMPRINT",FACE,{"disambiguationData":[TD([[makeQuery(id+"F3.imprint","IMPRINT",EDGE,{"derivedFrom":subQ51}),1.0]])]})])],"isStart":true});Q2=makeQuery(id+"F32.boolean.opBoolean","INTERSECT",EDGE,{"derivedFrom":[makeQuery(id+"F31.boolean.opBoolean","SPLIT",FACE,{"disambiguationData":[TD([subQ70])],"derivedFrom":makeQuery(id+"F30.boolean.opBoolean","SPLIT",FACE,{"disambiguationData":[TD([subQ78])],"derivedFrom":makeQuery(id+"F29.boolean.opBoolean","SPLIT",FACE,{"disambiguationData":[TD([subQ78])],"derivedFrom":makeQuery(id+"F28.boolean.opBoolean","SPLIT",FACE,{"disambiguationData":[TD([subQ78])],"derivedFrom":makeQuery(id+"F27.boolean.opBoolean","SPLIT",FACE,{"disambiguationData":[TD([subQ78])],"derivedFrom":makeQuery(id+"F26.boolean.opBoolean","SPLIT",FACE,{"disambiguationData":[TD([subQ78])],"derivedFrom":makeQuery(id+"F25.boolean.opBoolean","SPLIT",FACE,{"disambiguationData":[TD([subQ78])],"derivedFrom":makeQuery(id+"F24.boolean.opBoolean","SPLIT",FACE,{"disambiguationData":[TD([subQ78])],"derivedFrom":makeQuery(id+"F1.opRevolve","SWEPT_FACE",FACE,{"disambiguationData":[OSD([sQuery(id+"F0.wireOp",EDGE,"E4")])]})})})})})})})})}),makeQuery(id+"F32.opLoft","SWEPT_FACE",FACE,{"disambiguationData":[OSD([subQ2,subQ1,subQ0,sQuery(id+"F22.wireOp",EDGE,"E28.9.1"),sQuery(id+"F22.wireOp",EDGE,"E28.9.2"),sQuery(id+"F22.wireOp",EDGE,"E28.9.3")])]})]});}
            var Q3;
            {var subQ0=sQuery(id+"F3.wireOp",EDGE,"E20.2.3");var subQ1=sQuery(id+"F3.wireOp",EDGE,"E20.2.1");var subQ2=sQuery(id+"F3.wireOp",EDGE,"E20.2.0");var subQ51=sQuery(id+"F3.wireOp",EDGE,"E20.7.0");var subQ60=makeQuery(id+"F14.opLoft","CAP_FACE",FACE,{"disambiguationData":[OSD([makeQuery(id+"F3.imprint","IMPRINT",FACE,{"disambiguationData":[TD([[makeQuery(id+"F3.imprint","IMPRINT",EDGE,{"derivedFrom":subQ51}),-1.0]])]})])],"isStart":true});var subQ73=sQuery(id+"F3.wireOp",EDGE,"E18.bottom");var subQ78=makeQuery(id+"F5.opLoft","CAP_FACE",FACE,{"disambiguationData":[OSD([makeQuery(id+"F3.imprint","IMPRINT",FACE,{"disambiguationData":[TD([[makeQuery(id+"F3.imprint","IMPRINT",EDGE,{"derivedFrom":subQ73}),1.0]])]})])],"isStart":true});Q3=makeQuery(id+"F33.boolean.opBoolean","INTERSECT",EDGE,{"derivedFrom":[makeQuery(id+"F32.boolean.opBoolean","SPLIT",FACE,{"disambiguationData":[TD([subQ60])],"derivedFrom":makeQuery(id+"F31.boolean.opBoolean","SPLIT",FACE,{"disambiguationData":[TD([subQ60])],"derivedFrom":makeQuery(id+"F30.boolean.opBoolean","SPLIT",FACE,{"disambiguationData":[TD([subQ78])],"derivedFrom":makeQuery(id+"F29.boolean.opBoolean","SPLIT",FACE,{"disambiguationData":[TD([subQ78])],"derivedFrom":makeQuery(id+"F28.boolean.opBoolean","SPLIT",FACE,{"disambiguationData":[TD([subQ78])],"derivedFrom":makeQuery(id+"F27.boolean.opBoolean","SPLIT",FACE,{"disambiguationData":[TD([subQ78])],"derivedFrom":makeQuery(id+"F26.boolean.opBoolean","SPLIT",FACE,{"disambiguationData":[TD([subQ78])],"derivedFrom":makeQuery(id+"F25.boolean.opBoolean","SPLIT",FACE,{"disambiguationData":[TD([subQ78])],"derivedFrom":makeQuery(id+"F24.boolean.opBoolean","SPLIT",FACE,{"disambiguationData":[TD([subQ78])],"derivedFrom":makeQuery(id+"F1.opRevolve","SWEPT_FACE",FACE,{"disambiguationData":[OSD([sQuery(id+"F0.wireOp",EDGE,"E4")])]})})})})})})})})})}),makeQuery(id+"F33.opLoft","SWEPT_FACE",FACE,{"disambiguationData":[OSD([subQ2,subQ1,subQ0,sQuery(id+"F22.wireOp",EDGE,"E28.10.1"),sQuery(id+"F22.wireOp",EDGE,"E28.10.2"),sQuery(id+"F22.wireOp",EDGE,"E28.10.3")])]})]});}
            var Q4;
            {var subQ0=sQuery(id+"F3.wireOp",EDGE,"E20.3.3");var subQ1=sQuery(id+"F3.wireOp",EDGE,"E20.3.1");var subQ2=sQuery(id+"F3.wireOp",EDGE,"E20.3.0");var subQ22=sQuery(id+"F3.wireOp",EDGE,"E20.7.0");var subQ26=makeQuery(id+"F14.opLoft","CAP_FACE",FACE,{"disambiguationData":[OSD([makeQuery(id+"F3.imprint","IMPRINT",FACE,{"disambiguationData":[TD([[makeQuery(id+"F3.imprint","IMPRINT",EDGE,{"derivedFrom":subQ22}),-1.0]])]})])],"isStart":true});var subQ73=sQuery(id+"F3.wireOp",EDGE,"E18.bottom");var subQ78=makeQuery(id+"F5.opLoft","CAP_FACE",FACE,{"disambiguationData":[OSD([makeQuery(id+"F3.imprint","IMPRINT",FACE,{"disambiguationData":[TD([[makeQuery(id+"F3.imprint","IMPRINT",EDGE,{"derivedFrom":subQ73}),1.0]])]})])],"isStart":true});Q4=makeQuery(id+"F34.boolean.opBoolean","INTERSECT",EDGE,{"derivedFrom":[makeQuery(id+"F33.boolean.opBoolean","SPLIT",FACE,{"disambiguationData":[TD([subQ26])],"derivedFrom":makeQuery(id+"F32.boolean.opBoolean","SPLIT",FACE,{"disambiguationData":[TD([subQ26])],"derivedFrom":makeQuery(id+"F31.boolean.opBoolean","SPLIT",FACE,{"disambiguationData":[TD([subQ26])],"derivedFrom":makeQuery(id+"F30.boolean.opBoolean","SPLIT",FACE,{"disambiguationData":[TD([subQ78])],"derivedFrom":makeQuery(id+"F29.boolean.opBoolean","SPLIT",FACE,{"disambiguationData":[TD([subQ78])],"derivedFrom":makeQuery(id+"F28.boolean.opBoolean","SPLIT",FACE,{"disambiguationData":[TD([subQ78])],"derivedFrom":makeQuery(id+"F27.boolean.opBoolean","SPLIT",FACE,{"disambiguationData":[TD([subQ78])],"derivedFrom":makeQuery(id+"F26.boolean.opBoolean","SPLIT",FACE,{"disambiguationData":[TD([subQ78])],"derivedFrom":makeQuery(id+"F25.boolean.opBoolean","SPLIT",FACE,{"disambiguationData":[TD([subQ78])],"derivedFrom":makeQuery(id+"F24.boolean.opBoolean","SPLIT",FACE,{"disambiguationData":[TD([subQ78])],"derivedFrom":makeQuery(id+"F1.opRevolve","SWEPT_FACE",FACE,{"disambiguationData":[OSD([sQuery(id+"F0.wireOp",EDGE,"E4")])]})})})})})})})})})})}),makeQuery(id+"F34.opLoft","SWEPT_FACE",FACE,{"disambiguationData":[OSD([subQ2,subQ1,subQ0,sQuery(id+"F22.wireOp",EDGE,"E28.11.1"),sQuery(id+"F22.wireOp",EDGE,"E28.11.2"),sQuery(id+"F22.wireOp",EDGE,"E28.11.3")])]})]});}
            var Q5;
            {var subQ0=sQuery(id+"F3.wireOp",EDGE,"E20.4.3");var subQ1=sQuery(id+"F3.wireOp",EDGE,"E20.4.1");var subQ2=sQuery(id+"F3.wireOp",EDGE,"E20.4.0");var subQ19=sQuery(id+"F3.wireOp",EDGE,"E20.7.0");var subQ23=makeQuery(id+"F14.opLoft","CAP_FACE",FACE,{"disambiguationData":[OSD([makeQuery(id+"F3.imprint","IMPRINT",FACE,{"disambiguationData":[TD([[makeQuery(id+"F3.imprint","IMPRINT",EDGE,{"derivedFrom":subQ19}),-1.0]])]})])],"isStart":true});var subQ73=sQuery(id+"F3.wireOp",EDGE,"E18.bottom");var subQ78=makeQuery(id+"F5.opLoft","CAP_FACE",FACE,{"disambiguationData":[OSD([makeQuery(id+"F3.imprint","IMPRINT",FACE,{"disambiguationData":[TD([[makeQuery(id+"F3.imprint","IMPRINT",EDGE,{"derivedFrom":subQ73}),1.0]])]})])],"isStart":true});Q5=makeQuery(id+"F35.boolean.opBoolean","INTERSECT",EDGE,{"derivedFrom":[makeQuery(id+"F34.boolean.opBoolean","SPLIT",FACE,{"disambiguationData":[TD([subQ23])],"derivedFrom":makeQuery(id+"F33.boolean.opBoolean","SPLIT",FACE,{"disambiguationData":[TD([subQ23])],"derivedFrom":makeQuery(id+"F32.boolean.opBoolean","SPLIT",FACE,{"disambiguationData":[TD([subQ23])],"derivedFrom":makeQuery(id+"F31.boolean.opBoolean","SPLIT",FACE,{"disambiguationData":[TD([subQ23])],"derivedFrom":makeQuery(id+"F30.boolean.opBoolean","SPLIT",FACE,{"disambiguationData":[TD([subQ78])],"derivedFrom":makeQuery(id+"F29.boolean.opBoolean","SPLIT",FACE,{"disambiguationData":[TD([subQ78])],"derivedFrom":makeQuery(id+"F28.boolean.opBoolean","SPLIT",FACE,{"disambiguationData":[TD([subQ78])],"derivedFrom":makeQuery(id+"F27.boolean.opBoolean","SPLIT",FACE,{"disambiguationData":[TD([subQ78])],"derivedFrom":makeQuery(id+"F26.boolean.opBoolean","SPLIT",FACE,{"disambiguationData":[TD([subQ78])],"derivedFrom":makeQuery(id+"F25.boolean.opBoolean","SPLIT",FACE,{"disambiguationData":[TD([subQ78])],"derivedFrom":makeQuery(id+"F24.boolean.opBoolean","SPLIT",FACE,{"disambiguationData":[TD([subQ78])],"derivedFrom":makeQuery(id+"F1.opRevolve","SWEPT_FACE",FACE,{"disambiguationData":[OSD([sQuery(id+"F0.wireOp",EDGE,"E4")])]})})})})})})})})})})})}),makeQuery(id+"F35.opLoft","SWEPT_FACE",FACE,{"disambiguationData":[OSD([subQ2,subQ1,subQ0,sQuery(id+"F22.wireOp",EDGE,"E28.12.1"),sQuery(id+"F22.wireOp",EDGE,"E28.12.2"),sQuery(id+"F22.wireOp",EDGE,"E28.12.3")])]})]});}
            var Q6;
            {var subQ0=sQuery(id+"F3.wireOp",EDGE,"E20.5.3");var subQ1=sQuery(id+"F3.wireOp",EDGE,"E20.5.1");var subQ2=sQuery(id+"F3.wireOp",EDGE,"E20.5.0");var subQ14=sQuery(id+"F3.wireOp",EDGE,"E20.7.0");var subQ18=makeQuery(id+"F14.opLoft","CAP_FACE",FACE,{"disambiguationData":[OSD([makeQuery(id+"F3.imprint","IMPRINT",FACE,{"disambiguationData":[TD([[makeQuery(id+"F3.imprint","IMPRINT",EDGE,{"derivedFrom":subQ14}),-1.0]])]})])],"isStart":true});var subQ73=sQuery(id+"F3.wireOp",EDGE,"E18.bottom");var subQ78=makeQuery(id+"F5.opLoft","CAP_FACE",FACE,{"disambiguationData":[OSD([makeQuery(id+"F3.imprint","IMPRINT",FACE,{"disambiguationData":[TD([[makeQuery(id+"F3.imprint","IMPRINT",EDGE,{"derivedFrom":subQ73}),1.0]])]})])],"isStart":true});Q6=makeQuery(id+"F36.boolean.opBoolean","INTERSECT",EDGE,{"derivedFrom":[makeQuery(id+"F35.boolean.opBoolean","SPLIT",FACE,{"disambiguationData":[TD([subQ18])],"derivedFrom":makeQuery(id+"F34.boolean.opBoolean","SPLIT",FACE,{"disambiguationData":[TD([subQ18])],"derivedFrom":makeQuery(id+"F33.boolean.opBoolean","SPLIT",FACE,{"disambiguationData":[TD([subQ18])],"derivedFrom":makeQuery(id+"F32.boolean.opBoolean","SPLIT",FACE,{"disambiguationData":[TD([subQ18])],"derivedFrom":makeQuery(id+"F31.boolean.opBoolean","SPLIT",FACE,{"disambiguationData":[TD([subQ18])],"derivedFrom":makeQuery(id+"F30.boolean.opBoolean","SPLIT",FACE,{"disambiguationData":[TD([subQ78])],"derivedFrom":makeQuery(id+"F29.boolean.opBoolean","SPLIT",FACE,{"disambiguationData":[TD([subQ78])],"derivedFrom":makeQuery(id+"F28.boolean.opBoolean","SPLIT",FACE,{"disambiguationData":[TD([subQ78])],"derivedFrom":makeQuery(id+"F27.boolean.opBoolean","SPLIT",FACE,{"disambiguationData":[TD([subQ78])],"derivedFrom":makeQuery(id+"F26.boolean.opBoolean","SPLIT",FACE,{"disambiguationData":[TD([subQ78])],"derivedFrom":makeQuery(id+"F25.boolean.opBoolean","SPLIT",FACE,{"disambiguationData":[TD([subQ78])],"derivedFrom":makeQuery(id+"F24.boolean.opBoolean","SPLIT",FACE,{"disambiguationData":[TD([subQ78])],"derivedFrom":makeQuery(id+"F1.opRevolve","SWEPT_FACE",FACE,{"disambiguationData":[OSD([sQuery(id+"F0.wireOp",EDGE,"E4")])]})})})})})})})})})})})})}),makeQuery(id+"F36.opLoft","SWEPT_FACE",FACE,{"disambiguationData":[OSD([subQ2,subQ1,subQ0,sQuery(id+"F22.wireOp",EDGE,"E28.13.1"),sQuery(id+"F22.wireOp",EDGE,"E28.13.2"),sQuery(id+"F22.wireOp",EDGE,"E28.13.3")])]})]});}
            var Q7;
            {var subQ0=sQuery(id+"F3.wireOp",EDGE,"E20.6.3");var subQ1=sQuery(id+"F3.wireOp",EDGE,"E20.6.1");var subQ2=sQuery(id+"F3.wireOp",EDGE,"E20.6.0");var subQ14=sQuery(id+"F3.wireOp",EDGE,"E20.7.0");var subQ18=makeQuery(id+"F14.opLoft","CAP_FACE",FACE,{"disambiguationData":[OSD([makeQuery(id+"F3.imprint","IMPRINT",FACE,{"disambiguationData":[TD([[makeQuery(id+"F3.imprint","IMPRINT",EDGE,{"derivedFrom":subQ14}),-1.0]])]})])],"isStart":true});var subQ73=sQuery(id+"F3.wireOp",EDGE,"E18.bottom");var subQ78=makeQuery(id+"F5.opLoft","CAP_FACE",FACE,{"disambiguationData":[OSD([makeQuery(id+"F3.imprint","IMPRINT",FACE,{"disambiguationData":[TD([[makeQuery(id+"F3.imprint","IMPRINT",EDGE,{"derivedFrom":subQ73}),1.0]])]})])],"isStart":true});Q7=makeQuery(id+"F37.boolean.opBoolean","INTERSECT",EDGE,{"derivedFrom":[makeQuery(id+"F36.boolean.opBoolean","SPLIT",FACE,{"disambiguationData":[TD([subQ18])],"derivedFrom":makeQuery(id+"F35.boolean.opBoolean","SPLIT",FACE,{"disambiguationData":[TD([subQ18])],"derivedFrom":makeQuery(id+"F34.boolean.opBoolean","SPLIT",FACE,{"disambiguationData":[TD([subQ18])],"derivedFrom":makeQuery(id+"F33.boolean.opBoolean","SPLIT",FACE,{"disambiguationData":[TD([subQ18])],"derivedFrom":makeQuery(id+"F32.boolean.opBoolean","SPLIT",FACE,{"disambiguationData":[TD([subQ18])],"derivedFrom":makeQuery(id+"F31.boolean.opBoolean","SPLIT",FACE,{"disambiguationData":[TD([subQ18])],"derivedFrom":makeQuery(id+"F30.boolean.opBoolean","SPLIT",FACE,{"disambiguationData":[TD([subQ78])],"derivedFrom":makeQuery(id+"F29.boolean.opBoolean","SPLIT",FACE,{"disambiguationData":[TD([subQ78])],"derivedFrom":makeQuery(id+"F28.boolean.opBoolean","SPLIT",FACE,{"disambiguationData":[TD([subQ78])],"derivedFrom":makeQuery(id+"F27.boolean.opBoolean","SPLIT",FACE,{"disambiguationData":[TD([subQ78])],"derivedFrom":makeQuery(id+"F26.boolean.opBoolean","SPLIT",FACE,{"disambiguationData":[TD([subQ78])],"derivedFrom":makeQuery(id+"F25.boolean.opBoolean","SPLIT",FACE,{"disambiguationData":[TD([subQ78])],"derivedFrom":makeQuery(id+"F24.boolean.opBoolean","SPLIT",FACE,{"disambiguationData":[TD([subQ78])],"derivedFrom":makeQuery(id+"F1.opRevolve","SWEPT_FACE",FACE,{"disambiguationData":[OSD([sQuery(id+"F0.wireOp",EDGE,"E4")])]})})})})})})})})})})})})})}),makeQuery(id+"F37.opLoft","SWEPT_FACE",FACE,{"disambiguationData":[OSD([subQ2,subQ1,subQ0,sQuery(id+"F22.wireOp",EDGE,"E28.14.1"),sQuery(id+"F22.wireOp",EDGE,"E28.14.2"),sQuery(id+"F22.wireOp",EDGE,"E28.14.3")])]})]});}
            var Q8;
            {var subQ0=sQuery(id+"F3.wireOp",EDGE,"E20.7.3");var subQ1=sQuery(id+"F3.wireOp",EDGE,"E20.7.1");var subQ2=sQuery(id+"F3.wireOp",EDGE,"E20.7.0");var subQ14=makeQuery(id+"F14.opLoft","CAP_FACE",FACE,{"disambiguationData":[OSD([makeQuery(id+"F3.imprint","IMPRINT",FACE,{"disambiguationData":[TD([[makeQuery(id+"F3.imprint","IMPRINT",EDGE,{"derivedFrom":subQ2}),-1.0]])]})])],"isStart":true});var subQ73=sQuery(id+"F3.wireOp",EDGE,"E18.bottom");var subQ78=makeQuery(id+"F5.opLoft","CAP_FACE",FACE,{"disambiguationData":[OSD([makeQuery(id+"F3.imprint","IMPRINT",FACE,{"disambiguationData":[TD([[makeQuery(id+"F3.imprint","IMPRINT",EDGE,{"derivedFrom":subQ73}),1.0]])]})])],"isStart":true});Q8=makeQuery(id+"F38.boolean.opBoolean","INTERSECT",EDGE,{"derivedFrom":[makeQuery(id+"F37.boolean.opBoolean","SPLIT",FACE,{"disambiguationData":[TD([subQ14])],"derivedFrom":makeQuery(id+"F36.boolean.opBoolean","SPLIT",FACE,{"disambiguationData":[TD([subQ14])],"derivedFrom":makeQuery(id+"F35.boolean.opBoolean","SPLIT",FACE,{"disambiguationData":[TD([subQ14])],"derivedFrom":makeQuery(id+"F34.boolean.opBoolean","SPLIT",FACE,{"disambiguationData":[TD([subQ14])],"derivedFrom":makeQuery(id+"F33.boolean.opBoolean","SPLIT",FACE,{"disambiguationData":[TD([subQ14])],"derivedFrom":makeQuery(id+"F32.boolean.opBoolean","SPLIT",FACE,{"disambiguationData":[TD([subQ14])],"derivedFrom":makeQuery(id+"F31.boolean.opBoolean","SPLIT",FACE,{"disambiguationData":[TD([subQ14])],"derivedFrom":makeQuery(id+"F30.boolean.opBoolean","SPLIT",FACE,{"disambiguationData":[TD([subQ78])],"derivedFrom":makeQuery(id+"F29.boolean.opBoolean","SPLIT",FACE,{"disambiguationData":[TD([subQ78])],"derivedFrom":makeQuery(id+"F28.boolean.opBoolean","SPLIT",FACE,{"disambiguationData":[TD([subQ78])],"derivedFrom":makeQuery(id+"F27.boolean.opBoolean","SPLIT",FACE,{"disambiguationData":[TD([subQ78])],"derivedFrom":makeQuery(id+"F26.boolean.opBoolean","SPLIT",FACE,{"disambiguationData":[TD([subQ78])],"derivedFrom":makeQuery(id+"F25.boolean.opBoolean","SPLIT",FACE,{"disambiguationData":[TD([subQ78])],"derivedFrom":makeQuery(id+"F24.boolean.opBoolean","SPLIT",FACE,{"disambiguationData":[TD([subQ78])],"derivedFrom":makeQuery(id+"F1.opRevolve","SWEPT_FACE",FACE,{"disambiguationData":[OSD([sQuery(id+"F0.wireOp",EDGE,"E4")])]})})})})})})})})})})})})})})}),makeQuery(id+"F38.opLoft","SWEPT_FACE",FACE,{"disambiguationData":[OSD([subQ2,subQ1,subQ0,sQuery(id+"F22.wireOp",EDGE,"E28.15.1"),sQuery(id+"F22.wireOp",EDGE,"E28.15.2"),sQuery(id+"F22.wireOp",EDGE,"E28.15.3")])]})]});}
            var Q9;
            Q9=makeQuery(id+"F23.boolean.opBoolean","INTERSECT",EDGE,{"derivedFrom":[makeQuery(id+"F1.opRevolve","SWEPT_FACE",FACE,{"disambiguationData":[OSD([sQuery(id+"F0.wireOp",EDGE,"E4")])]}),makeQuery(id+"F23.opLoft","SWEPT_FACE",FACE,{"disambiguationData":[OSD([sQuery(id+"F3.wireOp",EDGE,"E20.8.0"),sQuery(id+"F3.wireOp",EDGE,"E20.8.1"),sQuery(id+"F3.wireOp",EDGE,"E20.8.3"),sQuery(id+"F22.wireOp",EDGE,"E27.bottom"),sQuery(id+"F22.wireOp",EDGE,"E27.top"),sQuery(id+"F22.wireOp",EDGE,"E27.right")])]})]});
            var Q10;
            Q10=makeQuery(id+"F24.boolean.opBoolean","INTERSECT",EDGE,{"derivedFrom":[makeQuery(id+"F1.opRevolve","SWEPT_FACE",FACE,{"disambiguationData":[OSD([sQuery(id+"F0.wireOp",EDGE,"E4")])]}),makeQuery(id+"F24.opLoft","SWEPT_FACE",FACE,{"disambiguationData":[OSD([sQuery(id+"F3.wireOp",EDGE,"E20.9.0"),sQuery(id+"F3.wireOp",EDGE,"E20.9.1"),sQuery(id+"F3.wireOp",EDGE,"E20.9.3"),sQuery(id+"F22.wireOp",EDGE,"E28.1.1"),sQuery(id+"F22.wireOp",EDGE,"E28.1.2"),sQuery(id+"F22.wireOp",EDGE,"E28.1.3")])]})]});
            var Q11;
            {var subQ0=sQuery(id+"F3.wireOp",EDGE,"E20.10.3");var subQ1=sQuery(id+"F3.wireOp",EDGE,"E20.10.1");var subQ2=sQuery(id+"F3.wireOp",EDGE,"E20.10.0");var subQ81=sQuery(id+"F3.wireOp",EDGE,"E18.bottom");Q11=makeQuery(id+"F25.boolean.opBoolean","INTERSECT",EDGE,{"derivedFrom":[makeQuery(id+"F24.boolean.opBoolean","SPLIT",FACE,{"disambiguationData":[TD([makeQuery(id+"F5.opLoft","CAP_FACE",FACE,{"disambiguationData":[OSD([makeQuery(id+"F3.imprint","IMPRINT",FACE,{"disambiguationData":[TD([[makeQuery(id+"F3.imprint","IMPRINT",EDGE,{"derivedFrom":subQ81}),1.0]])]})])],"isStart":true})])],"derivedFrom":makeQuery(id+"F1.opRevolve","SWEPT_FACE",FACE,{"disambiguationData":[OSD([sQuery(id+"F0.wireOp",EDGE,"E4")])]})}),makeQuery(id+"F25.opLoft","SWEPT_FACE",FACE,{"disambiguationData":[OSD([subQ2,subQ1,subQ0,sQuery(id+"F22.wireOp",EDGE,"E28.2.1"),sQuery(id+"F22.wireOp",EDGE,"E28.2.2"),sQuery(id+"F22.wireOp",EDGE,"E28.2.3")])]})]});}
            var Q12;
            {var subQ0=sQuery(id+"F3.wireOp",EDGE,"E20.11.3");var subQ1=sQuery(id+"F3.wireOp",EDGE,"E20.11.1");var subQ2=sQuery(id+"F3.wireOp",EDGE,"E20.11.0");var subQ74=sQuery(id+"F3.wireOp",EDGE,"E18.bottom");var subQ77=makeQuery(id+"F5.opLoft","CAP_FACE",FACE,{"disambiguationData":[OSD([makeQuery(id+"F3.imprint","IMPRINT",FACE,{"disambiguationData":[TD([[makeQuery(id+"F3.imprint","IMPRINT",EDGE,{"derivedFrom":subQ74}),1.0]])]})])],"isStart":true});Q12=makeQuery(id+"F26.boolean.opBoolean","INTERSECT",EDGE,{"derivedFrom":[makeQuery(id+"F25.boolean.opBoolean","SPLIT",FACE,{"disambiguationData":[TD([subQ77])],"derivedFrom":makeQuery(id+"F24.boolean.opBoolean","SPLIT",FACE,{"disambiguationData":[TD([subQ77])],"derivedFrom":makeQuery(id+"F1.opRevolve","SWEPT_FACE",FACE,{"disambiguationData":[OSD([sQuery(id+"F0.wireOp",EDGE,"E4")])]})})}),makeQuery(id+"F26.opLoft","SWEPT_FACE",FACE,{"disambiguationData":[OSD([subQ2,subQ1,subQ0,sQuery(id+"F22.wireOp",EDGE,"E28.3.1"),sQuery(id+"F22.wireOp",EDGE,"E28.3.2"),sQuery(id+"F22.wireOp",EDGE,"E28.3.3")])]})]});}
            var Q13;
            {var subQ0=sQuery(id+"F3.wireOp",EDGE,"E20.12.3");var subQ1=sQuery(id+"F3.wireOp",EDGE,"E20.12.1");var subQ2=sQuery(id+"F3.wireOp",EDGE,"E20.12.0");var subQ70=sQuery(id+"F3.wireOp",EDGE,"E18.bottom");var subQ73=makeQuery(id+"F5.opLoft","CAP_FACE",FACE,{"disambiguationData":[OSD([makeQuery(id+"F3.imprint","IMPRINT",FACE,{"disambiguationData":[TD([[makeQuery(id+"F3.imprint","IMPRINT",EDGE,{"derivedFrom":subQ70}),1.0]])]})])],"isStart":true});Q13=makeQuery(id+"F27.boolean.opBoolean","INTERSECT",EDGE,{"derivedFrom":[makeQuery(id+"F26.boolean.opBoolean","SPLIT",FACE,{"disambiguationData":[TD([subQ73])],"derivedFrom":makeQuery(id+"F25.boolean.opBoolean","SPLIT",FACE,{"disambiguationData":[TD([subQ73])],"derivedFrom":makeQuery(id+"F24.boolean.opBoolean","SPLIT",FACE,{"disambiguationData":[TD([subQ73])],"derivedFrom":makeQuery(id+"F1.opRevolve","SWEPT_FACE",FACE,{"disambiguationData":[OSD([sQuery(id+"F0.wireOp",EDGE,"E4")])]})})})}),makeQuery(id+"F27.opLoft","SWEPT_FACE",FACE,{"disambiguationData":[OSD([subQ2,subQ1,subQ0,sQuery(id+"F22.wireOp",EDGE,"E28.4.1"),sQuery(id+"F22.wireOp",EDGE,"E28.4.2"),sQuery(id+"F22.wireOp",EDGE,"E28.4.3")])]})]});}
            var Q14;
            {var subQ0=sQuery(id+"F3.wireOp",EDGE,"E20.13.3");var subQ1=sQuery(id+"F3.wireOp",EDGE,"E20.13.1");var subQ2=sQuery(id+"F3.wireOp",EDGE,"E20.13.0");var subQ52=sQuery(id+"F3.wireOp",EDGE,"E18.bottom");var subQ55=makeQuery(id+"F5.opLoft","CAP_FACE",FACE,{"disambiguationData":[OSD([makeQuery(id+"F3.imprint","IMPRINT",FACE,{"disambiguationData":[TD([[makeQuery(id+"F3.imprint","IMPRINT",EDGE,{"derivedFrom":subQ52}),1.0]])]})])],"isStart":true});Q14=makeQuery(id+"F28.boolean.opBoolean","INTERSECT",EDGE,{"derivedFrom":[makeQuery(id+"F27.boolean.opBoolean","SPLIT",FACE,{"disambiguationData":[TD([subQ55])],"derivedFrom":makeQuery(id+"F26.boolean.opBoolean","SPLIT",FACE,{"disambiguationData":[TD([subQ55])],"derivedFrom":makeQuery(id+"F25.boolean.opBoolean","SPLIT",FACE,{"disambiguationData":[TD([subQ55])],"derivedFrom":makeQuery(id+"F24.boolean.opBoolean","SPLIT",FACE,{"disambiguationData":[TD([subQ55])],"derivedFrom":makeQuery(id+"F1.opRevolve","SWEPT_FACE",FACE,{"disambiguationData":[OSD([sQuery(id+"F0.wireOp",EDGE,"E4")])]})})})})}),makeQuery(id+"F28.opLoft","SWEPT_FACE",FACE,{"disambiguationData":[OSD([subQ2,subQ1,subQ0,sQuery(id+"F22.wireOp",EDGE,"E28.5.1"),sQuery(id+"F22.wireOp",EDGE,"E28.5.2"),sQuery(id+"F22.wireOp",EDGE,"E28.5.3")])]})]});}
            var Q15;
            {var subQ0=sQuery(id+"F3.wireOp",EDGE,"E20.14.3");var subQ1=sQuery(id+"F3.wireOp",EDGE,"E20.14.1");var subQ2=sQuery(id+"F3.wireOp",EDGE,"E20.14.0");var subQ41=sQuery(id+"F3.wireOp",EDGE,"E18.bottom");var subQ44=makeQuery(id+"F5.opLoft","CAP_FACE",FACE,{"disambiguationData":[OSD([makeQuery(id+"F3.imprint","IMPRINT",FACE,{"disambiguationData":[TD([[makeQuery(id+"F3.imprint","IMPRINT",EDGE,{"derivedFrom":subQ41}),1.0]])]})])],"isStart":true});Q15=makeQuery(id+"F29.boolean.opBoolean","INTERSECT",EDGE,{"derivedFrom":[makeQuery(id+"F28.boolean.opBoolean","SPLIT",FACE,{"disambiguationData":[TD([subQ44])],"derivedFrom":makeQuery(id+"F27.boolean.opBoolean","SPLIT",FACE,{"disambiguationData":[TD([subQ44])],"derivedFrom":makeQuery(id+"F26.boolean.opBoolean","SPLIT",FACE,{"disambiguationData":[TD([subQ44])],"derivedFrom":makeQuery(id+"F25.boolean.opBoolean","SPLIT",FACE,{"disambiguationData":[TD([subQ44])],"derivedFrom":makeQuery(id+"F24.boolean.opBoolean","SPLIT",FACE,{"disambiguationData":[TD([subQ44])],"derivedFrom":makeQuery(id+"F1.opRevolve","SWEPT_FACE",FACE,{"disambiguationData":[OSD([sQuery(id+"F0.wireOp",EDGE,"E4")])]})})})})})}),makeQuery(id+"F29.opLoft","SWEPT_FACE",FACE,{"disambiguationData":[OSD([subQ2,subQ1,subQ0,sQuery(id+"F22.wireOp",EDGE,"E28.6.1"),sQuery(id+"F22.wireOp",EDGE,"E28.6.2"),sQuery(id+"F22.wireOp",EDGE,"E28.6.3")])]})]});}
            var Q16;
            {var subQ0=sQuery(id+"F3.wireOp",EDGE,"E20.15.3");var subQ1=sQuery(id+"F3.wireOp",EDGE,"E20.15.1");var subQ2=sQuery(id+"F3.wireOp",EDGE,"E20.15.0");var subQ34=sQuery(id+"F3.wireOp",EDGE,"E18.bottom");var subQ37=makeQuery(id+"F5.opLoft","CAP_FACE",FACE,{"disambiguationData":[OSD([makeQuery(id+"F3.imprint","IMPRINT",FACE,{"disambiguationData":[TD([[makeQuery(id+"F3.imprint","IMPRINT",EDGE,{"derivedFrom":subQ34}),1.0]])]})])],"isStart":true});Q16=makeQuery(id+"F30.boolean.opBoolean","INTERSECT",EDGE,{"derivedFrom":[makeQuery(id+"F29.boolean.opBoolean","SPLIT",FACE,{"disambiguationData":[TD([subQ37])],"derivedFrom":makeQuery(id+"F28.boolean.opBoolean","SPLIT",FACE,{"disambiguationData":[TD([subQ37])],"derivedFrom":makeQuery(id+"F27.boolean.opBoolean","SPLIT",FACE,{"disambiguationData":[TD([subQ37])],"derivedFrom":makeQuery(id+"F26.boolean.opBoolean","SPLIT",FACE,{"disambiguationData":[TD([subQ37])],"derivedFrom":makeQuery(id+"F25.boolean.opBoolean","SPLIT",FACE,{"disambiguationData":[TD([subQ37])],"derivedFrom":makeQuery(id+"F24.boolean.opBoolean","SPLIT",FACE,{"disambiguationData":[TD([subQ37])],"derivedFrom":makeQuery(id+"F1.opRevolve","SWEPT_FACE",FACE,{"disambiguationData":[OSD([sQuery(id+"F0.wireOp",EDGE,"E4")])]})})})})})})}),makeQuery(id+"F30.opLoft","SWEPT_FACE",FACE,{"disambiguationData":[OSD([subQ2,subQ1,subQ0,sQuery(id+"F22.wireOp",EDGE,"E28.7.1"),sQuery(id+"F22.wireOp",EDGE,"E28.7.2"),sQuery(id+"F22.wireOp",EDGE,"E28.7.3")])]})]});}
            var Q17;
            {var subQ0=sQuery(id+"F3.wireOp",EDGE,"E18.left");var subQ1=sQuery(id+"F3.wireOp",EDGE,"E18.top");var subQ2=sQuery(id+"F3.wireOp",EDGE,"E18.bottom");var subQ48=makeQuery(id+"F5.opLoft","CAP_FACE",FACE,{"disambiguationData":[OSD([makeQuery(id+"F3.imprint","IMPRINT",FACE,{"disambiguationData":[TD([[makeQuery(id+"F3.imprint","IMPRINT",EDGE,{"derivedFrom":subQ2}),1.0]])]})])],"isStart":true});Q17=makeQuery(id+"F31.boolean.opBoolean","INTERSECT",EDGE,{"derivedFrom":[makeQuery(id+"F30.boolean.opBoolean","SPLIT",FACE,{"disambiguationData":[TD([subQ48])],"derivedFrom":makeQuery(id+"F29.boolean.opBoolean","SPLIT",FACE,{"disambiguationData":[TD([subQ48])],"derivedFrom":makeQuery(id+"F28.boolean.opBoolean","SPLIT",FACE,{"disambiguationData":[TD([subQ48])],"derivedFrom":makeQuery(id+"F27.boolean.opBoolean","SPLIT",FACE,{"disambiguationData":[TD([subQ48])],"derivedFrom":makeQuery(id+"F26.boolean.opBoolean","SPLIT",FACE,{"disambiguationData":[TD([subQ48])],"derivedFrom":makeQuery(id+"F25.boolean.opBoolean","SPLIT",FACE,{"disambiguationData":[TD([subQ48])],"derivedFrom":makeQuery(id+"F24.boolean.opBoolean","SPLIT",FACE,{"disambiguationData":[TD([subQ48])],"derivedFrom":makeQuery(id+"F1.opRevolve","SWEPT_FACE",FACE,{"disambiguationData":[OSD([sQuery(id+"F0.wireOp",EDGE,"E4")])]})})})})})})})}),makeQuery(id+"F31.opLoft","SWEPT_FACE",FACE,{"disambiguationData":[OSD([subQ2,subQ1,subQ0,sQuery(id+"F22.wireOp",EDGE,"E28.8.1"),sQuery(id+"F22.wireOp",EDGE,"E28.8.2"),sQuery(id+"F22.wireOp",EDGE,"E28.8.3")])]})]});}
            var Q18;
            Q18=makeQuery(id+"F5.boolean.opBoolean","INTERSECT",EDGE,{"derivedFrom":[makeQuery(id+"F1.opRevolve","SWEPT_FACE",FACE,{"disambiguationData":[OSD([sQuery(id+"F0.wireOp",EDGE,"E4")])]}),makeQuery(id+"F5.opLoft","SWEPT_FACE",FACE,{"disambiguationData":[OSD([sQuery(id+"F3.wireOp",EDGE,"E18.bottom"),sQuery(id+"F3.wireOp",EDGE,"E18.top"),sQuery(id+"F3.wireOp",EDGE,"E18.left"),sQuery(id+"F4.wireOp",EDGE,"E21"),sQuery(id+"F4.wireOp",EDGE,"E22"),sQuery(id+"F4.wireOp",EDGE,"E23")])]})]});
            var Q19;
            Q19=makeQuery(id+"F6.boolean.opBoolean","INTERSECT",EDGE,{"derivedFrom":[makeQuery(id+"F1.opRevolve","SWEPT_FACE",FACE,{"disambiguationData":[OSD([sQuery(id+"F0.wireOp",EDGE,"E4")])]}),makeQuery(id+"F6.opLoft","SWEPT_FACE",FACE,{"disambiguationData":[OSD([sQuery(id+"F3.wireOp",EDGE,"E20.15.0"),sQuery(id+"F3.wireOp",EDGE,"E20.15.1"),sQuery(id+"F3.wireOp",EDGE,"E20.15.3"),sQuery(id+"F4.wireOp",EDGE,"E26.15.0"),sQuery(id+"F4.wireOp",EDGE,"E26.15.2"),sQuery(id+"F4.wireOp",EDGE,"E26.15.3")])]})]});
            var Q20;
            Q20=makeQuery(id+"F7.boolean.opBoolean","INTERSECT",EDGE,{"derivedFrom":[makeQuery(id+"F1.opRevolve","SWEPT_FACE",FACE,{"disambiguationData":[OSD([sQuery(id+"F0.wireOp",EDGE,"E4")])]}),makeQuery(id+"F7.opLoft","SWEPT_FACE",FACE,{"disambiguationData":[OSD([sQuery(id+"F3.wireOp",EDGE,"E20.14.0"),sQuery(id+"F3.wireOp",EDGE,"E20.14.1"),sQuery(id+"F3.wireOp",EDGE,"E20.14.3"),sQuery(id+"F4.wireOp",EDGE,"E26.14.0"),sQuery(id+"F4.wireOp",EDGE,"E26.14.2"),sQuery(id+"F4.wireOp",EDGE,"E26.14.3")])]})]});
            var Q21;
            Q21=makeQuery(id+"F8.boolean.opBoolean","INTERSECT",EDGE,{"derivedFrom":[makeQuery(id+"F1.opRevolve","SWEPT_FACE",FACE,{"disambiguationData":[OSD([sQuery(id+"F0.wireOp",EDGE,"E4")])]}),makeQuery(id+"F8.opLoft","SWEPT_FACE",FACE,{"disambiguationData":[OSD([sQuery(id+"F3.wireOp",EDGE,"E20.13.0"),sQuery(id+"F3.wireOp",EDGE,"E20.13.1"),sQuery(id+"F3.wireOp",EDGE,"E20.13.3"),sQuery(id+"F4.wireOp",EDGE,"E26.13.0"),sQuery(id+"F4.wireOp",EDGE,"E26.13.2"),sQuery(id+"F4.wireOp",EDGE,"E26.13.3")])]})]});
            var Q22;
            Q22=makeQuery(id+"F9.boolean.opBoolean","INTERSECT",EDGE,{"derivedFrom":[makeQuery(id+"F1.opRevolve","SWEPT_FACE",FACE,{"disambiguationData":[OSD([sQuery(id+"F0.wireOp",EDGE,"E4")])]}),makeQuery(id+"F9.opLoft","SWEPT_FACE",FACE,{"disambiguationData":[OSD([sQuery(id+"F3.wireOp",EDGE,"E20.12.0"),sQuery(id+"F3.wireOp",EDGE,"E20.12.1"),sQuery(id+"F3.wireOp",EDGE,"E20.12.3"),sQuery(id+"F4.wireOp",EDGE,"E26.12.0"),sQuery(id+"F4.wireOp",EDGE,"E26.12.2"),sQuery(id+"F4.wireOp",EDGE,"E26.12.3")])]})]});
            var Q23;
            Q23=makeQuery(id+"F10.boolean.opBoolean","INTERSECT",EDGE,{"derivedFrom":[makeQuery(id+"F1.opRevolve","SWEPT_FACE",FACE,{"disambiguationData":[OSD([sQuery(id+"F0.wireOp",EDGE,"E4")])]}),makeQuery(id+"F10.opLoft","SWEPT_FACE",FACE,{"disambiguationData":[OSD([sQuery(id+"F3.wireOp",EDGE,"E20.11.0"),sQuery(id+"F3.wireOp",EDGE,"E20.11.1"),sQuery(id+"F3.wireOp",EDGE,"E20.11.3"),sQuery(id+"F4.wireOp",EDGE,"E26.11.0"),sQuery(id+"F4.wireOp",EDGE,"E26.11.2"),sQuery(id+"F4.wireOp",EDGE,"E26.11.3")])]})]});
            var Q24;
            Q24=makeQuery(id+"F11.boolean.opBoolean","INTERSECT",EDGE,{"derivedFrom":[makeQuery(id+"F1.opRevolve","SWEPT_FACE",FACE,{"disambiguationData":[OSD([sQuery(id+"F0.wireOp",EDGE,"E4")])]}),makeQuery(id+"F11.opLoft","SWEPT_FACE",FACE,{"disambiguationData":[OSD([sQuery(id+"F3.wireOp",EDGE,"E20.10.0"),sQuery(id+"F3.wireOp",EDGE,"E20.10.1"),sQuery(id+"F3.wireOp",EDGE,"E20.10.3"),sQuery(id+"F4.wireOp",EDGE,"E26.10.0"),sQuery(id+"F4.wireOp",EDGE,"E26.10.2"),sQuery(id+"F4.wireOp",EDGE,"E26.10.3")])]})]});
            var Q25;
            Q25=makeQuery(id+"F12.boolean.opBoolean","INTERSECT",EDGE,{"derivedFrom":[makeQuery(id+"F1.opRevolve","SWEPT_FACE",FACE,{"disambiguationData":[OSD([sQuery(id+"F0.wireOp",EDGE,"E4")])]}),makeQuery(id+"F12.opLoft","SWEPT_FACE",FACE,{"disambiguationData":[OSD([sQuery(id+"F3.wireOp",EDGE,"E20.9.0"),sQuery(id+"F3.wireOp",EDGE,"E20.9.1"),sQuery(id+"F3.wireOp",EDGE,"E20.9.3"),sQuery(id+"F4.wireOp",EDGE,"E26.9.0"),sQuery(id+"F4.wireOp",EDGE,"E26.9.2"),sQuery(id+"F4.wireOp",EDGE,"E26.9.3")])]})]});
            var Q26;
            Q26=makeQuery(id+"F13.boolean.opBoolean","INTERSECT",EDGE,{"derivedFrom":[makeQuery(id+"F1.opRevolve","SWEPT_FACE",FACE,{"disambiguationData":[OSD([sQuery(id+"F0.wireOp",EDGE,"E4")])]}),makeQuery(id+"F13.opLoft","SWEPT_FACE",FACE,{"disambiguationData":[OSD([sQuery(id+"F3.wireOp",EDGE,"E20.8.0"),sQuery(id+"F3.wireOp",EDGE,"E20.8.1"),sQuery(id+"F3.wireOp",EDGE,"E20.8.3"),sQuery(id+"F4.wireOp",EDGE,"E26.8.0"),sQuery(id+"F4.wireOp",EDGE,"E26.8.2"),sQuery(id+"F4.wireOp",EDGE,"E26.8.3")])]})]});
            var Q27;
            Q27=makeQuery(id+"F14.boolean.opBoolean","INTERSECT",EDGE,{"derivedFrom":[makeQuery(id+"F1.opRevolve","SWEPT_FACE",FACE,{"disambiguationData":[OSD([sQuery(id+"F0.wireOp",EDGE,"E4")])]}),makeQuery(id+"F14.opLoft","SWEPT_FACE",FACE,{"disambiguationData":[OSD([sQuery(id+"F3.wireOp",EDGE,"E20.7.0"),sQuery(id+"F3.wireOp",EDGE,"E20.7.1"),sQuery(id+"F3.wireOp",EDGE,"E20.7.3"),sQuery(id+"F4.wireOp",EDGE,"E26.7.0"),sQuery(id+"F4.wireOp",EDGE,"E26.7.2"),sQuery(id+"F4.wireOp",EDGE,"E26.7.3")])]})]});
            var Q28;
            Q28=makeQuery(id+"F15.boolean.opBoolean","INTERSECT",EDGE,{"derivedFrom":[makeQuery(id+"F1.opRevolve","SWEPT_FACE",FACE,{"disambiguationData":[OSD([sQuery(id+"F0.wireOp",EDGE,"E4")])]}),makeQuery(id+"F15.opLoft","SWEPT_FACE",FACE,{"disambiguationData":[OSD([sQuery(id+"F3.wireOp",EDGE,"E20.6.0"),sQuery(id+"F3.wireOp",EDGE,"E20.6.1"),sQuery(id+"F3.wireOp",EDGE,"E20.6.3"),sQuery(id+"F4.wireOp",EDGE,"E26.6.0"),sQuery(id+"F4.wireOp",EDGE,"E26.6.2"),sQuery(id+"F4.wireOp",EDGE,"E26.6.3")])]})]});
            var Q29;
            Q29=makeQuery(id+"F16.boolean.opBoolean","INTERSECT",EDGE,{"derivedFrom":[makeQuery(id+"F1.opRevolve","SWEPT_FACE",FACE,{"disambiguationData":[OSD([sQuery(id+"F0.wireOp",EDGE,"E4")])]}),makeQuery(id+"F16.opLoft","SWEPT_FACE",FACE,{"disambiguationData":[OSD([sQuery(id+"F3.wireOp",EDGE,"E20.5.0"),sQuery(id+"F3.wireOp",EDGE,"E20.5.1"),sQuery(id+"F3.wireOp",EDGE,"E20.5.3"),sQuery(id+"F4.wireOp",EDGE,"E26.5.0"),sQuery(id+"F4.wireOp",EDGE,"E26.5.2"),sQuery(id+"F4.wireOp",EDGE,"E26.5.3")])]})]});
            var Q30;
            Q30=makeQuery(id+"F17.boolean.opBoolean","INTERSECT",EDGE,{"derivedFrom":[makeQuery(id+"F1.opRevolve","SWEPT_FACE",FACE,{"disambiguationData":[OSD([sQuery(id+"F0.wireOp",EDGE,"E4")])]}),makeQuery(id+"F17.opLoft","SWEPT_FACE",FACE,{"disambiguationData":[OSD([sQuery(id+"F3.wireOp",EDGE,"E20.4.0"),sQuery(id+"F3.wireOp",EDGE,"E20.4.1"),sQuery(id+"F3.wireOp",EDGE,"E20.4.3"),sQuery(id+"F4.wireOp",EDGE,"E26.4.0"),sQuery(id+"F4.wireOp",EDGE,"E26.4.2"),sQuery(id+"F4.wireOp",EDGE,"E26.4.3")])]})]});
            var Q31;
            Q31=makeQuery(id+"F18.boolean.opBoolean","INTERSECT",EDGE,{"derivedFrom":[makeQuery(id+"F1.opRevolve","SWEPT_FACE",FACE,{"disambiguationData":[OSD([sQuery(id+"F0.wireOp",EDGE,"E4")])]}),makeQuery(id+"F18.opLoft","SWEPT_FACE",FACE,{"disambiguationData":[OSD([sQuery(id+"F3.wireOp",EDGE,"E20.3.0"),sQuery(id+"F3.wireOp",EDGE,"E20.3.1"),sQuery(id+"F3.wireOp",EDGE,"E20.3.3"),sQuery(id+"F4.wireOp",EDGE,"E26.3.0"),sQuery(id+"F4.wireOp",EDGE,"E26.3.2"),sQuery(id+"F4.wireOp",EDGE,"E26.3.3")])]})]});
            fillet(context, id + "F45", {"entities" : qUnion([Q0, Q1, Q2, Q3, Q4, Q5, Q6, Q7, Q8, Q9, Q10, Q11, Q12, Q13, Q14, Q15, Q16, Q17, Q18, Q19, Q20, Q21, Q22, Q23, Q24, Q25, Q26, Q27, Q28, Q29, Q30, Q31]), "radius" : 3 * mm, "tangentPropagation" : true, "allowEdgeOverflow" : false});
        }
        {
            var Q0;
            Q0=makeQuery(id+"F1.opRevolve","SWEPT_EDGE",EDGE,{"disambiguationData":[OSD([sQuery(id+"F0.wireOp",EDGE,"M0De9DZ8-1zJs-ubri-npQ8-jmgKs2AWA0kd"),sQuery(id+"F0.wireOp",EDGE,"E5")])]});
            var Q1;
            Q1=makeQuery(id+"F1.opRevolve","SWEPT_EDGE",EDGE,{"disambiguationData":[OSD([sQuery(id+"F0.wireOp",EDGE,"cHHVOKxT-xBtR-EdTY-fGsc-esJYpbiU2zwx"),sQuery(id+"F0.wireOp",EDGE,"E6")])]});
            chamfer(context, id + "F46", {"entities" : qUnion([Q0, Q1]), "width" : 2 * mm, "tangentPropagation" : true});
        }
        {
            var Q0;
            {var subQ0=sQuery(id+"F41.wireOp",EDGE,"E35");var subQ1=sQuery(id+"F4.wireOp",EDGE,"E26.3.3");var subQ2=sQuery(id+"F4.wireOp",EDGE,"E26.3.2");var subQ3=sQuery(id+"F3.wireOp",EDGE,"E20.3.3");var subQ4=sQuery(id+"F3.wireOp",EDGE,"E20.3.1");var subQ5=sQuery(id+"F41.wireOp",EDGE,"E36");Q0=makeQuery(id+"F42.boolean.opBoolean","COPY",EDGE,{"disambiguationData":[TD([makeQuery(id+"F18.opLoft","SWEPT_FACE",FACE,{"disambiguationData":[OSD([sQuery(id+"F3.wireOp",EDGE,"E20.3.0"),subQ4,subQ3,sQuery(id+"F4.wireOp",EDGE,"E26.3.0"),subQ2,subQ1])]})])],"derivedFrom":makeQuery(id+"F42.opRevolve","SWEPT_EDGE",EDGE,{"disambiguationData":[OSD([subQ0,subQ5])]})});}
            var Q1;
            {var subQ0=sQuery(id+"F4.wireOp",EDGE,"E26.2.3");var subQ1=sQuery(id+"F4.wireOp",EDGE,"E26.2.2");var subQ2=sQuery(id+"F3.wireOp",EDGE,"E20.2.3");var subQ3=sQuery(id+"F3.wireOp",EDGE,"E20.2.1");var subQ4=sQuery(id+"F41.wireOp",EDGE,"E36");var subQ5=sQuery(id+"F41.wireOp",EDGE,"E35");Q1=makeQuery(id+"F42.boolean.opBoolean","COPY",EDGE,{"disambiguationData":[TD([makeQuery(id+"F19.opLoft","SWEPT_FACE",FACE,{"disambiguationData":[OSD([sQuery(id+"F3.wireOp",EDGE,"E20.2.0"),subQ3,subQ2,sQuery(id+"F4.wireOp",EDGE,"E26.2.0"),subQ1,subQ0])]})])],"derivedFrom":makeQuery(id+"F42.opRevolve","SWEPT_EDGE",EDGE,{"disambiguationData":[OSD([subQ5,subQ4])]})});}
            var Q2;
            {var subQ0=sQuery(id+"F4.wireOp",EDGE,"E26.1.3");var subQ1=sQuery(id+"F4.wireOp",EDGE,"E26.1.2");var subQ2=sQuery(id+"F3.wireOp",EDGE,"E20.1.3");var subQ3=sQuery(id+"F3.wireOp",EDGE,"E20.1.1");var subQ4=sQuery(id+"F41.wireOp",EDGE,"E35");var subQ5=sQuery(id+"F41.wireOp",EDGE,"E36");Q2=makeQuery(id+"F42.boolean.opBoolean","COPY",EDGE,{"disambiguationData":[TD([makeQuery(id+"F20.opLoft","SWEPT_FACE",FACE,{"disambiguationData":[OSD([sQuery(id+"F3.wireOp",EDGE,"E20.1.0"),subQ3,subQ2,sQuery(id+"F4.wireOp",EDGE,"E26.1.0"),subQ1,subQ0])]})])],"derivedFrom":makeQuery(id+"F42.opRevolve","SWEPT_EDGE",EDGE,{"disambiguationData":[OSD([subQ4,subQ5])]})});}
            var Q3;
            {var subQ0=sQuery(id+"F41.wireOp",EDGE,"E35");var subQ1=sQuery(id+"F4.wireOp",EDGE,"E23");var subQ2=sQuery(id+"F4.wireOp",EDGE,"E22");var subQ3=sQuery(id+"F3.wireOp",EDGE,"E18.top");var subQ4=sQuery(id+"F3.wireOp",EDGE,"E18.bottom");var subQ5=sQuery(id+"F41.wireOp",EDGE,"E36");Q3=makeQuery(id+"F42.boolean.opBoolean","COPY",EDGE,{"disambiguationData":[TD([makeQuery(id+"F5.opLoft","SWEPT_FACE",FACE,{"disambiguationData":[OSD([subQ4,subQ3,sQuery(id+"F3.wireOp",EDGE,"E18.left"),sQuery(id+"F4.wireOp",EDGE,"E21"),subQ2,subQ1])]})])],"derivedFrom":makeQuery(id+"F42.opRevolve","SWEPT_EDGE",EDGE,{"disambiguationData":[OSD([subQ0,subQ5])]})});}
            var Q4;
            {var subQ0=sQuery(id+"F41.wireOp",EDGE,"E35");var subQ1=sQuery(id+"F4.wireOp",EDGE,"E26.4.3");var subQ2=sQuery(id+"F4.wireOp",EDGE,"E26.4.2");var subQ3=sQuery(id+"F3.wireOp",EDGE,"E20.4.3");var subQ4=sQuery(id+"F3.wireOp",EDGE,"E20.4.1");var subQ5=sQuery(id+"F41.wireOp",EDGE,"E36");Q4=makeQuery(id+"F42.boolean.opBoolean","COPY",EDGE,{"disambiguationData":[TD([makeQuery(id+"F17.opLoft","SWEPT_FACE",FACE,{"disambiguationData":[OSD([sQuery(id+"F3.wireOp",EDGE,"E20.4.0"),subQ4,subQ3,sQuery(id+"F4.wireOp",EDGE,"E26.4.0"),subQ2,subQ1])]})])],"derivedFrom":makeQuery(id+"F42.opRevolve","SWEPT_EDGE",EDGE,{"disambiguationData":[OSD([subQ0,subQ5])]})});}
            var Q5;
            {var subQ0=sQuery(id+"F41.wireOp",EDGE,"E35");var subQ1=sQuery(id+"F4.wireOp",EDGE,"E26.5.3");var subQ2=sQuery(id+"F4.wireOp",EDGE,"E26.5.2");var subQ3=sQuery(id+"F3.wireOp",EDGE,"E20.5.3");var subQ4=sQuery(id+"F3.wireOp",EDGE,"E20.5.1");var subQ5=sQuery(id+"F41.wireOp",EDGE,"E36");Q5=makeQuery(id+"F42.boolean.opBoolean","COPY",EDGE,{"disambiguationData":[TD([makeQuery(id+"F16.opLoft","SWEPT_FACE",FACE,{"disambiguationData":[OSD([sQuery(id+"F3.wireOp",EDGE,"E20.5.0"),subQ4,subQ3,sQuery(id+"F4.wireOp",EDGE,"E26.5.0"),subQ2,subQ1])]})])],"derivedFrom":makeQuery(id+"F42.opRevolve","SWEPT_EDGE",EDGE,{"disambiguationData":[OSD([subQ0,subQ5])]})});}
            var Q6;
            {var subQ0=sQuery(id+"F41.wireOp",EDGE,"E35");var subQ1=sQuery(id+"F4.wireOp",EDGE,"E26.6.3");var subQ2=sQuery(id+"F4.wireOp",EDGE,"E26.6.2");var subQ3=sQuery(id+"F3.wireOp",EDGE,"E20.6.3");var subQ4=sQuery(id+"F3.wireOp",EDGE,"E20.6.1");var subQ5=sQuery(id+"F41.wireOp",EDGE,"E36");Q6=makeQuery(id+"F42.boolean.opBoolean","COPY",EDGE,{"disambiguationData":[TD([makeQuery(id+"F15.opLoft","SWEPT_FACE",FACE,{"disambiguationData":[OSD([sQuery(id+"F3.wireOp",EDGE,"E20.6.0"),subQ4,subQ3,sQuery(id+"F4.wireOp",EDGE,"E26.6.0"),subQ2,subQ1])]})])],"derivedFrom":makeQuery(id+"F42.opRevolve","SWEPT_EDGE",EDGE,{"disambiguationData":[OSD([subQ0,subQ5])]})});}
            var Q7;
            {var subQ0=sQuery(id+"F41.wireOp",EDGE,"E35");var subQ1=sQuery(id+"F4.wireOp",EDGE,"E26.7.3");var subQ2=sQuery(id+"F4.wireOp",EDGE,"E26.7.2");var subQ3=sQuery(id+"F3.wireOp",EDGE,"E20.7.3");var subQ4=sQuery(id+"F3.wireOp",EDGE,"E20.7.1");var subQ5=sQuery(id+"F41.wireOp",EDGE,"E36");Q7=makeQuery(id+"F42.boolean.opBoolean","COPY",EDGE,{"disambiguationData":[TD([makeQuery(id+"F14.opLoft","SWEPT_FACE",FACE,{"disambiguationData":[OSD([sQuery(id+"F3.wireOp",EDGE,"E20.7.0"),subQ4,subQ3,sQuery(id+"F4.wireOp",EDGE,"E26.7.0"),subQ2,subQ1])]})])],"derivedFrom":makeQuery(id+"F42.opRevolve","SWEPT_EDGE",EDGE,{"disambiguationData":[OSD([subQ0,subQ5])]})});}
            var Q8;
            {var subQ0=sQuery(id+"F41.wireOp",EDGE,"E35");var subQ1=sQuery(id+"F4.wireOp",EDGE,"E26.8.3");var subQ2=sQuery(id+"F4.wireOp",EDGE,"E26.8.2");var subQ3=sQuery(id+"F3.wireOp",EDGE,"E20.8.3");var subQ4=sQuery(id+"F3.wireOp",EDGE,"E20.8.1");var subQ5=sQuery(id+"F41.wireOp",EDGE,"E36");Q8=makeQuery(id+"F42.boolean.opBoolean","COPY",EDGE,{"disambiguationData":[TD([makeQuery(id+"F13.opLoft","SWEPT_FACE",FACE,{"disambiguationData":[OSD([sQuery(id+"F3.wireOp",EDGE,"E20.8.0"),subQ4,subQ3,sQuery(id+"F4.wireOp",EDGE,"E26.8.0"),subQ2,subQ1])]})])],"derivedFrom":makeQuery(id+"F42.opRevolve","SWEPT_EDGE",EDGE,{"disambiguationData":[OSD([subQ0,subQ5])]})});}
            var Q9;
            {var subQ0=sQuery(id+"F41.wireOp",EDGE,"E35");var subQ1=sQuery(id+"F4.wireOp",EDGE,"E26.9.3");var subQ2=sQuery(id+"F4.wireOp",EDGE,"E26.9.2");var subQ3=sQuery(id+"F3.wireOp",EDGE,"E20.9.3");var subQ4=sQuery(id+"F3.wireOp",EDGE,"E20.9.1");var subQ5=sQuery(id+"F41.wireOp",EDGE,"E36");Q9=makeQuery(id+"F42.boolean.opBoolean","COPY",EDGE,{"disambiguationData":[TD([makeQuery(id+"F12.opLoft","SWEPT_FACE",FACE,{"disambiguationData":[OSD([sQuery(id+"F3.wireOp",EDGE,"E20.9.0"),subQ4,subQ3,sQuery(id+"F4.wireOp",EDGE,"E26.9.0"),subQ2,subQ1])]})])],"derivedFrom":makeQuery(id+"F42.opRevolve","SWEPT_EDGE",EDGE,{"disambiguationData":[OSD([subQ0,subQ5])]})});}
            var Q10;
            {var subQ0=sQuery(id+"F41.wireOp",EDGE,"E35");var subQ1=sQuery(id+"F4.wireOp",EDGE,"E26.10.3");var subQ2=sQuery(id+"F4.wireOp",EDGE,"E26.10.2");var subQ3=sQuery(id+"F3.wireOp",EDGE,"E20.10.3");var subQ4=sQuery(id+"F3.wireOp",EDGE,"E20.10.1");var subQ5=sQuery(id+"F41.wireOp",EDGE,"E36");Q10=makeQuery(id+"F42.boolean.opBoolean","COPY",EDGE,{"disambiguationData":[TD([makeQuery(id+"F11.opLoft","SWEPT_FACE",FACE,{"disambiguationData":[OSD([sQuery(id+"F3.wireOp",EDGE,"E20.10.0"),subQ4,subQ3,sQuery(id+"F4.wireOp",EDGE,"E26.10.0"),subQ2,subQ1])]})])],"derivedFrom":makeQuery(id+"F42.opRevolve","SWEPT_EDGE",EDGE,{"disambiguationData":[OSD([subQ0,subQ5])]})});}
            var Q11;
            {var subQ0=sQuery(id+"F4.wireOp",EDGE,"E26.11.3");var subQ1=sQuery(id+"F4.wireOp",EDGE,"E26.11.2");var subQ2=sQuery(id+"F3.wireOp",EDGE,"E20.11.3");var subQ3=sQuery(id+"F3.wireOp",EDGE,"E20.11.1");var subQ4=sQuery(id+"F41.wireOp",EDGE,"E35");var subQ5=sQuery(id+"F41.wireOp",EDGE,"E36");Q11=makeQuery(id+"F42.boolean.opBoolean","COPY",EDGE,{"disambiguationData":[TD([makeQuery(id+"F10.opLoft","SWEPT_FACE",FACE,{"disambiguationData":[OSD([sQuery(id+"F3.wireOp",EDGE,"E20.11.0"),subQ3,subQ2,sQuery(id+"F4.wireOp",EDGE,"E26.11.0"),subQ1,subQ0])]})])],"derivedFrom":makeQuery(id+"F42.opRevolve","SWEPT_EDGE",EDGE,{"disambiguationData":[OSD([subQ4,subQ5])]})});}
            var Q12;
            {var subQ0=sQuery(id+"F4.wireOp",EDGE,"E26.12.3");var subQ1=sQuery(id+"F4.wireOp",EDGE,"E26.12.2");var subQ2=sQuery(id+"F3.wireOp",EDGE,"E20.12.3");var subQ3=sQuery(id+"F3.wireOp",EDGE,"E20.12.1");var subQ4=sQuery(id+"F41.wireOp",EDGE,"E35");var subQ5=sQuery(id+"F41.wireOp",EDGE,"E36");Q12=makeQuery(id+"F42.boolean.opBoolean","COPY",EDGE,{"disambiguationData":[TD([makeQuery(id+"F9.opLoft","SWEPT_FACE",FACE,{"disambiguationData":[OSD([sQuery(id+"F3.wireOp",EDGE,"E20.12.0"),subQ3,subQ2,sQuery(id+"F4.wireOp",EDGE,"E26.12.0"),subQ1,subQ0])]})])],"derivedFrom":makeQuery(id+"F42.opRevolve","SWEPT_EDGE",EDGE,{"disambiguationData":[OSD([subQ4,subQ5])]})});}
            var Q13;
            {var subQ0=sQuery(id+"F41.wireOp",EDGE,"E35");var subQ1=sQuery(id+"F4.wireOp",EDGE,"E26.13.3");var subQ2=sQuery(id+"F4.wireOp",EDGE,"E26.13.2");var subQ3=sQuery(id+"F3.wireOp",EDGE,"E20.13.3");var subQ4=sQuery(id+"F3.wireOp",EDGE,"E20.13.1");var subQ5=sQuery(id+"F41.wireOp",EDGE,"E36");Q13=makeQuery(id+"F42.boolean.opBoolean","COPY",EDGE,{"disambiguationData":[TD([makeQuery(id+"F8.opLoft","SWEPT_FACE",FACE,{"disambiguationData":[OSD([sQuery(id+"F3.wireOp",EDGE,"E20.13.0"),subQ4,subQ3,sQuery(id+"F4.wireOp",EDGE,"E26.13.0"),subQ2,subQ1])]})])],"derivedFrom":makeQuery(id+"F42.opRevolve","SWEPT_EDGE",EDGE,{"disambiguationData":[OSD([subQ0,subQ5])]})});}
            var Q14;
            {var subQ0=sQuery(id+"F41.wireOp",EDGE,"E35");var subQ1=sQuery(id+"F4.wireOp",EDGE,"E26.14.3");var subQ2=sQuery(id+"F4.wireOp",EDGE,"E26.14.2");var subQ3=sQuery(id+"F3.wireOp",EDGE,"E20.14.3");var subQ4=sQuery(id+"F3.wireOp",EDGE,"E20.14.1");var subQ5=sQuery(id+"F41.wireOp",EDGE,"E36");Q14=makeQuery(id+"F42.boolean.opBoolean","COPY",EDGE,{"disambiguationData":[TD([makeQuery(id+"F7.opLoft","SWEPT_FACE",FACE,{"disambiguationData":[OSD([sQuery(id+"F3.wireOp",EDGE,"E20.14.0"),subQ4,subQ3,sQuery(id+"F4.wireOp",EDGE,"E26.14.0"),subQ2,subQ1])]})])],"derivedFrom":makeQuery(id+"F42.opRevolve","SWEPT_EDGE",EDGE,{"disambiguationData":[OSD([subQ0,subQ5])]})});}
            var Q15;
            {var subQ0=sQuery(id+"F4.wireOp",EDGE,"E26.15.3");var subQ1=sQuery(id+"F4.wireOp",EDGE,"E26.15.2");var subQ2=sQuery(id+"F3.wireOp",EDGE,"E20.15.3");var subQ3=sQuery(id+"F3.wireOp",EDGE,"E20.15.1");var subQ4=sQuery(id+"F41.wireOp",EDGE,"E35");var subQ5=sQuery(id+"F41.wireOp",EDGE,"E36");Q15=makeQuery(id+"F42.boolean.opBoolean","COPY",EDGE,{"disambiguationData":[TD([makeQuery(id+"F6.opLoft","SWEPT_FACE",FACE,{"disambiguationData":[OSD([sQuery(id+"F3.wireOp",EDGE,"E20.15.0"),subQ3,subQ2,sQuery(id+"F4.wireOp",EDGE,"E26.15.0"),subQ1,subQ0])]})])],"derivedFrom":makeQuery(id+"F42.opRevolve","SWEPT_EDGE",EDGE,{"disambiguationData":[OSD([subQ4,subQ5])]})});}
            var Q16;
            {var subQ0=sQuery(id+"F41.wireOp",EDGE,"E37");var subQ1=sQuery(id+"F22.wireOp",EDGE,"E28.7.3");var subQ2=sQuery(id+"F22.wireOp",EDGE,"E28.7.2");var subQ3=sQuery(id+"F3.wireOp",EDGE,"E20.15.3");var subQ4=sQuery(id+"F3.wireOp",EDGE,"E20.15.1");var subQ5=sQuery(id+"F41.wireOp",EDGE,"E38");Q16=makeQuery(id+"F42.boolean.opBoolean","COPY",EDGE,{"disambiguationData":[TD([makeQuery(id+"F30.opLoft","SWEPT_FACE",FACE,{"disambiguationData":[OSD([sQuery(id+"F3.wireOp",EDGE,"E20.15.0"),subQ4,subQ3,sQuery(id+"F22.wireOp",EDGE,"E28.7.1"),subQ2,subQ1])]})])],"derivedFrom":makeQuery(id+"F42.opRevolve","SWEPT_EDGE",EDGE,{"disambiguationData":[OSD([subQ0,subQ5])]})});}
            var Q17;
            {var subQ0=sQuery(id+"F41.wireOp",EDGE,"E37");var subQ1=sQuery(id+"F22.wireOp",EDGE,"E28.6.3");var subQ2=sQuery(id+"F22.wireOp",EDGE,"E28.6.2");var subQ3=sQuery(id+"F3.wireOp",EDGE,"E20.14.3");var subQ4=sQuery(id+"F3.wireOp",EDGE,"E20.14.1");var subQ5=sQuery(id+"F41.wireOp",EDGE,"E38");Q17=makeQuery(id+"F42.boolean.opBoolean","COPY",EDGE,{"disambiguationData":[TD([makeQuery(id+"F29.opLoft","SWEPT_FACE",FACE,{"disambiguationData":[OSD([sQuery(id+"F3.wireOp",EDGE,"E20.14.0"),subQ4,subQ3,sQuery(id+"F22.wireOp",EDGE,"E28.6.1"),subQ2,subQ1])]})])],"derivedFrom":makeQuery(id+"F42.opRevolve","SWEPT_EDGE",EDGE,{"disambiguationData":[OSD([subQ0,subQ5])]})});}
            var Q18;
            {var subQ0=sQuery(id+"F41.wireOp",EDGE,"E37");var subQ1=sQuery(id+"F22.wireOp",EDGE,"E28.5.3");var subQ2=sQuery(id+"F22.wireOp",EDGE,"E28.5.2");var subQ3=sQuery(id+"F3.wireOp",EDGE,"E20.13.3");var subQ4=sQuery(id+"F3.wireOp",EDGE,"E20.13.1");var subQ5=sQuery(id+"F41.wireOp",EDGE,"E38");Q18=makeQuery(id+"F42.boolean.opBoolean","COPY",EDGE,{"disambiguationData":[TD([makeQuery(id+"F28.opLoft","SWEPT_FACE",FACE,{"disambiguationData":[OSD([sQuery(id+"F3.wireOp",EDGE,"E20.13.0"),subQ4,subQ3,sQuery(id+"F22.wireOp",EDGE,"E28.5.1"),subQ2,subQ1])]})])],"derivedFrom":makeQuery(id+"F42.opRevolve","SWEPT_EDGE",EDGE,{"disambiguationData":[OSD([subQ0,subQ5])]})});}
            var Q19;
            {var subQ0=sQuery(id+"F41.wireOp",EDGE,"E37");var subQ1=sQuery(id+"F22.wireOp",EDGE,"E28.4.3");var subQ2=sQuery(id+"F22.wireOp",EDGE,"E28.4.2");var subQ3=sQuery(id+"F3.wireOp",EDGE,"E20.12.3");var subQ4=sQuery(id+"F3.wireOp",EDGE,"E20.12.1");var subQ5=sQuery(id+"F41.wireOp",EDGE,"E38");Q19=makeQuery(id+"F42.boolean.opBoolean","COPY",EDGE,{"disambiguationData":[TD([makeQuery(id+"F27.opLoft","SWEPT_FACE",FACE,{"disambiguationData":[OSD([sQuery(id+"F3.wireOp",EDGE,"E20.12.0"),subQ4,subQ3,sQuery(id+"F22.wireOp",EDGE,"E28.4.1"),subQ2,subQ1])]})])],"derivedFrom":makeQuery(id+"F42.opRevolve","SWEPT_EDGE",EDGE,{"disambiguationData":[OSD([subQ0,subQ5])]})});}
            var Q20;
            {var subQ0=sQuery(id+"F41.wireOp",EDGE,"E37");var subQ1=sQuery(id+"F22.wireOp",EDGE,"E28.3.3");var subQ2=sQuery(id+"F22.wireOp",EDGE,"E28.3.2");var subQ3=sQuery(id+"F3.wireOp",EDGE,"E20.11.3");var subQ4=sQuery(id+"F3.wireOp",EDGE,"E20.11.1");var subQ5=sQuery(id+"F41.wireOp",EDGE,"E38");Q20=makeQuery(id+"F42.boolean.opBoolean","COPY",EDGE,{"disambiguationData":[TD([makeQuery(id+"F26.opLoft","SWEPT_FACE",FACE,{"disambiguationData":[OSD([sQuery(id+"F3.wireOp",EDGE,"E20.11.0"),subQ4,subQ3,sQuery(id+"F22.wireOp",EDGE,"E28.3.1"),subQ2,subQ1])]})])],"derivedFrom":makeQuery(id+"F42.opRevolve","SWEPT_EDGE",EDGE,{"disambiguationData":[OSD([subQ0,subQ5])]})});}
            var Q21;
            {var subQ0=sQuery(id+"F41.wireOp",EDGE,"E37");var subQ1=sQuery(id+"F22.wireOp",EDGE,"E28.2.3");var subQ2=sQuery(id+"F22.wireOp",EDGE,"E28.2.2");var subQ3=sQuery(id+"F3.wireOp",EDGE,"E20.10.3");var subQ4=sQuery(id+"F3.wireOp",EDGE,"E20.10.1");var subQ5=sQuery(id+"F41.wireOp",EDGE,"E38");Q21=makeQuery(id+"F42.boolean.opBoolean","COPY",EDGE,{"disambiguationData":[TD([makeQuery(id+"F25.opLoft","SWEPT_FACE",FACE,{"disambiguationData":[OSD([sQuery(id+"F3.wireOp",EDGE,"E20.10.0"),subQ4,subQ3,sQuery(id+"F22.wireOp",EDGE,"E28.2.1"),subQ2,subQ1])]})])],"derivedFrom":makeQuery(id+"F42.opRevolve","SWEPT_EDGE",EDGE,{"disambiguationData":[OSD([subQ0,subQ5])]})});}
            var Q22;
            {var subQ0=sQuery(id+"F41.wireOp",EDGE,"E37");var subQ1=sQuery(id+"F22.wireOp",EDGE,"E28.1.3");var subQ2=sQuery(id+"F22.wireOp",EDGE,"E28.1.2");var subQ3=sQuery(id+"F3.wireOp",EDGE,"E20.9.3");var subQ4=sQuery(id+"F3.wireOp",EDGE,"E20.9.1");var subQ5=sQuery(id+"F41.wireOp",EDGE,"E38");Q22=makeQuery(id+"F42.boolean.opBoolean","COPY",EDGE,{"disambiguationData":[TD([makeQuery(id+"F24.opLoft","SWEPT_FACE",FACE,{"disambiguationData":[OSD([sQuery(id+"F3.wireOp",EDGE,"E20.9.0"),subQ4,subQ3,sQuery(id+"F22.wireOp",EDGE,"E28.1.1"),subQ2,subQ1])]})])],"derivedFrom":makeQuery(id+"F42.opRevolve","SWEPT_EDGE",EDGE,{"disambiguationData":[OSD([subQ0,subQ5])]})});}
            var Q23;
            {var subQ0=sQuery(id+"F22.wireOp",EDGE,"E27.top");var subQ1=sQuery(id+"F22.wireOp",EDGE,"E27.bottom");var subQ2=sQuery(id+"F3.wireOp",EDGE,"E20.8.3");var subQ3=sQuery(id+"F3.wireOp",EDGE,"E20.8.1");var subQ4=sQuery(id+"F41.wireOp",EDGE,"E37");var subQ5=sQuery(id+"F41.wireOp",EDGE,"E38");Q23=makeQuery(id+"F42.boolean.opBoolean","COPY",EDGE,{"disambiguationData":[TD([makeQuery(id+"F23.opLoft","SWEPT_FACE",FACE,{"disambiguationData":[OSD([sQuery(id+"F3.wireOp",EDGE,"E20.8.0"),subQ3,subQ2,subQ1,subQ0,sQuery(id+"F22.wireOp",EDGE,"E27.right")])]})])],"derivedFrom":makeQuery(id+"F42.opRevolve","SWEPT_EDGE",EDGE,{"disambiguationData":[OSD([subQ4,subQ5])]})});}
            var Q24;
            {var subQ0=sQuery(id+"F41.wireOp",EDGE,"E37");var subQ1=sQuery(id+"F22.wireOp",EDGE,"E28.15.3");var subQ2=sQuery(id+"F22.wireOp",EDGE,"E28.15.2");var subQ3=sQuery(id+"F3.wireOp",EDGE,"E20.7.3");var subQ4=sQuery(id+"F3.wireOp",EDGE,"E20.7.1");var subQ5=sQuery(id+"F41.wireOp",EDGE,"E38");Q24=makeQuery(id+"F42.boolean.opBoolean","COPY",EDGE,{"disambiguationData":[TD([makeQuery(id+"F38.opLoft","SWEPT_FACE",FACE,{"disambiguationData":[OSD([sQuery(id+"F3.wireOp",EDGE,"E20.7.0"),subQ4,subQ3,sQuery(id+"F22.wireOp",EDGE,"E28.15.1"),subQ2,subQ1])]})])],"derivedFrom":makeQuery(id+"F42.opRevolve","SWEPT_EDGE",EDGE,{"disambiguationData":[OSD([subQ0,subQ5])]})});}
            var Q25;
            {var subQ0=sQuery(id+"F41.wireOp",EDGE,"E37");var subQ1=sQuery(id+"F22.wireOp",EDGE,"E28.14.3");var subQ2=sQuery(id+"F22.wireOp",EDGE,"E28.14.2");var subQ3=sQuery(id+"F3.wireOp",EDGE,"E20.6.3");var subQ4=sQuery(id+"F3.wireOp",EDGE,"E20.6.1");var subQ5=sQuery(id+"F41.wireOp",EDGE,"E38");Q25=makeQuery(id+"F42.boolean.opBoolean","COPY",EDGE,{"disambiguationData":[TD([makeQuery(id+"F37.opLoft","SWEPT_FACE",FACE,{"disambiguationData":[OSD([sQuery(id+"F3.wireOp",EDGE,"E20.6.0"),subQ4,subQ3,sQuery(id+"F22.wireOp",EDGE,"E28.14.1"),subQ2,subQ1])]})])],"derivedFrom":makeQuery(id+"F42.opRevolve","SWEPT_EDGE",EDGE,{"disambiguationData":[OSD([subQ0,subQ5])]})});}
            var Q26;
            {var subQ0=sQuery(id+"F41.wireOp",EDGE,"E37");var subQ1=sQuery(id+"F22.wireOp",EDGE,"E28.13.3");var subQ2=sQuery(id+"F22.wireOp",EDGE,"E28.13.2");var subQ3=sQuery(id+"F3.wireOp",EDGE,"E20.5.3");var subQ4=sQuery(id+"F3.wireOp",EDGE,"E20.5.1");var subQ5=sQuery(id+"F41.wireOp",EDGE,"E38");Q26=makeQuery(id+"F42.boolean.opBoolean","COPY",EDGE,{"disambiguationData":[TD([makeQuery(id+"F36.opLoft","SWEPT_FACE",FACE,{"disambiguationData":[OSD([sQuery(id+"F3.wireOp",EDGE,"E20.5.0"),subQ4,subQ3,sQuery(id+"F22.wireOp",EDGE,"E28.13.1"),subQ2,subQ1])]})])],"derivedFrom":makeQuery(id+"F42.opRevolve","SWEPT_EDGE",EDGE,{"disambiguationData":[OSD([subQ0,subQ5])]})});}
            var Q27;
            {var subQ0=sQuery(id+"F41.wireOp",EDGE,"E37");var subQ1=sQuery(id+"F22.wireOp",EDGE,"E28.12.3");var subQ2=sQuery(id+"F22.wireOp",EDGE,"E28.12.2");var subQ3=sQuery(id+"F3.wireOp",EDGE,"E20.4.3");var subQ4=sQuery(id+"F3.wireOp",EDGE,"E20.4.1");var subQ5=sQuery(id+"F41.wireOp",EDGE,"E38");Q27=makeQuery(id+"F42.boolean.opBoolean","COPY",EDGE,{"disambiguationData":[TD([makeQuery(id+"F35.opLoft","SWEPT_FACE",FACE,{"disambiguationData":[OSD([sQuery(id+"F3.wireOp",EDGE,"E20.4.0"),subQ4,subQ3,sQuery(id+"F22.wireOp",EDGE,"E28.12.1"),subQ2,subQ1])]})])],"derivedFrom":makeQuery(id+"F42.opRevolve","SWEPT_EDGE",EDGE,{"disambiguationData":[OSD([subQ0,subQ5])]})});}
            var Q28;
            {var subQ0=sQuery(id+"F41.wireOp",EDGE,"E37");var subQ1=sQuery(id+"F22.wireOp",EDGE,"E28.11.3");var subQ2=sQuery(id+"F22.wireOp",EDGE,"E28.11.2");var subQ3=sQuery(id+"F3.wireOp",EDGE,"E20.3.3");var subQ4=sQuery(id+"F3.wireOp",EDGE,"E20.3.1");var subQ5=sQuery(id+"F41.wireOp",EDGE,"E38");Q28=makeQuery(id+"F42.boolean.opBoolean","COPY",EDGE,{"disambiguationData":[TD([makeQuery(id+"F34.opLoft","SWEPT_FACE",FACE,{"disambiguationData":[OSD([sQuery(id+"F3.wireOp",EDGE,"E20.3.0"),subQ4,subQ3,sQuery(id+"F22.wireOp",EDGE,"E28.11.1"),subQ2,subQ1])]})])],"derivedFrom":makeQuery(id+"F42.opRevolve","SWEPT_EDGE",EDGE,{"disambiguationData":[OSD([subQ0,subQ5])]})});}
            var Q29;
            {var subQ0=sQuery(id+"F41.wireOp",EDGE,"E37");var subQ1=sQuery(id+"F22.wireOp",EDGE,"E28.10.3");var subQ2=sQuery(id+"F22.wireOp",EDGE,"E28.10.2");var subQ3=sQuery(id+"F3.wireOp",EDGE,"E20.2.3");var subQ4=sQuery(id+"F3.wireOp",EDGE,"E20.2.1");var subQ5=sQuery(id+"F41.wireOp",EDGE,"E38");Q29=makeQuery(id+"F42.boolean.opBoolean","COPY",EDGE,{"disambiguationData":[TD([makeQuery(id+"F33.opLoft","SWEPT_FACE",FACE,{"disambiguationData":[OSD([sQuery(id+"F3.wireOp",EDGE,"E20.2.0"),subQ4,subQ3,sQuery(id+"F22.wireOp",EDGE,"E28.10.1"),subQ2,subQ1])]})])],"derivedFrom":makeQuery(id+"F42.opRevolve","SWEPT_EDGE",EDGE,{"disambiguationData":[OSD([subQ0,subQ5])]})});}
            var Q30;
            {var subQ0=sQuery(id+"F22.wireOp",EDGE,"E28.9.3");var subQ1=sQuery(id+"F22.wireOp",EDGE,"E28.9.2");var subQ2=sQuery(id+"F3.wireOp",EDGE,"E20.1.3");var subQ3=sQuery(id+"F3.wireOp",EDGE,"E20.1.1");var subQ4=sQuery(id+"F41.wireOp",EDGE,"E37");var subQ5=sQuery(id+"F41.wireOp",EDGE,"E38");Q30=makeQuery(id+"F42.boolean.opBoolean","COPY",EDGE,{"disambiguationData":[TD([makeQuery(id+"F32.opLoft","SWEPT_FACE",FACE,{"disambiguationData":[OSD([sQuery(id+"F3.wireOp",EDGE,"E20.1.0"),subQ3,subQ2,sQuery(id+"F22.wireOp",EDGE,"E28.9.1"),subQ1,subQ0])]})])],"derivedFrom":makeQuery(id+"F42.opRevolve","SWEPT_EDGE",EDGE,{"disambiguationData":[OSD([subQ4,subQ5])]})});}
            var Q31;
            {var subQ0=sQuery(id+"F22.wireOp",EDGE,"E28.8.3");var subQ1=sQuery(id+"F22.wireOp",EDGE,"E28.8.2");var subQ2=sQuery(id+"F3.wireOp",EDGE,"E18.top");var subQ3=sQuery(id+"F3.wireOp",EDGE,"E18.bottom");var subQ4=sQuery(id+"F41.wireOp",EDGE,"E37");var subQ5=sQuery(id+"F41.wireOp",EDGE,"E38");Q31=makeQuery(id+"F42.boolean.opBoolean","COPY",EDGE,{"disambiguationData":[TD([makeQuery(id+"F31.opLoft","SWEPT_FACE",FACE,{"disambiguationData":[OSD([subQ3,subQ2,sQuery(id+"F3.wireOp",EDGE,"E18.left"),sQuery(id+"F22.wireOp",EDGE,"E28.8.1"),subQ1,subQ0])]})])],"derivedFrom":makeQuery(id+"F42.opRevolve","SWEPT_EDGE",EDGE,{"disambiguationData":[OSD([subQ4,subQ5])]})});}
            fillet(context, id + "F47", {"entities" : qUnion([Q0, Q1, Q2, Q3, Q4, Q5, Q6, Q7, Q8, Q9, Q10, Q11, Q12, Q13, Q14, Q15, Q16, Q17, Q18, Q19, Q20, Q21, Q22, Q23, Q24, Q25, Q26, Q27, Q28, Q29, Q30, Q31]), "radius" : 2.5 * mm, "tangentPropagation" : true, "allowEdgeOverflow" : false});
        }
        {
            var Q0;
            {var subQ0=makeQuery(id+"F1.opRevolve","SWEPT_FACE",FACE,{"disambiguationData":[OSD([sQuery(id+"F0.wireOp",EDGE,"E1")])]});var subQ1=sQuery(id+"F3.wireOp",EDGE,"E20.9.3");var subQ2=sQuery(id+"F3.wireOp",EDGE,"E20.9.2");var subQ3=sQuery(id+"F3.wireOp",EDGE,"E20.9.1");var subQ4=makeQuery(id+"F12.opLoft","SWEPT_FACE",FACE,{"disambiguationData":[OSD([subQ3,subQ2,subQ1,sQuery(id+"F4.wireOp",EDGE,"E26.9.1"),sQuery(id+"F4.wireOp",EDGE,"E26.9.2"),sQuery(id+"F4.wireOp",EDGE,"E26.9.3")])]});var subQ9=makeQuery(id+"F40.opExtrude","CAP_FACE",FACE,{"disambiguationData":[OSD([sQuery(id+"F39.wireOp",EDGE,"E29"),sQuery(id+"F39.wireOp",EDGE,"E30")])],"isStart":false});Q0=makeQuery(id+"F44.opFillet","BLEND_EDGE",EDGE,{"blendedFrom":[makeQuery(id+"F40.boolean.opBoolean","INTERSECT",EDGE,{"derivedFrom":[subQ4,subQ9]}),makeQuery(id+"F40.boolean.opBoolean","SPLIT",FACE,{"disambiguationData":[TD([subQ0])],"derivedFrom":makeQuery(id+"F24.boolean.opBoolean","SPLIT",FACE,{"disambiguationData":[TD([subQ4])],"derivedFrom":makeQuery(id+"F1.opRevolve","SWEPT_FACE",FACE,{"disambiguationData":[OSD([sQuery(id+"F0.wireOp",EDGE,"E4")])]})})})],"blendedInto":[makeQuery(id+"F40.boolean.opBoolean","SPLIT",FACE,{"disambiguationData":[TD([subQ0])],"derivedFrom":makeQuery(id+"F24.boolean.opBoolean","SPLIT",FACE,{"disambiguationData":[TD([subQ4])],"derivedFrom":makeQuery(id+"F1.opRevolve","SWEPT_FACE",FACE,{"disambiguationData":[OSD([sQuery(id+"F0.wireOp",EDGE,"E4")])]})})})]});}
            var Q1;
            {var subQ0=makeQuery(id+"F1.opRevolve","SWEPT_FACE",FACE,{"disambiguationData":[OSD([sQuery(id+"F0.wireOp",EDGE,"E1")])]});var subQ1=sQuery(id+"F4.wireOp",EDGE,"E26.10.3");var subQ2=sQuery(id+"F4.wireOp",EDGE,"E26.10.2");var subQ3=sQuery(id+"F3.wireOp",EDGE,"E20.10.3");var subQ4=sQuery(id+"F3.wireOp",EDGE,"E20.10.2");var subQ5=sQuery(id+"F3.wireOp",EDGE,"E20.10.1");var subQ6=makeQuery(id+"F11.opLoft","SWEPT_FACE",FACE,{"disambiguationData":[OSD([subQ5,subQ4,subQ3,sQuery(id+"F4.wireOp",EDGE,"E26.10.1"),subQ2,subQ1])]});var subQ11=makeQuery(id+"F40.opExtrude","CAP_FACE",FACE,{"disambiguationData":[OSD([sQuery(id+"F39.wireOp",EDGE,"E29"),sQuery(id+"F39.wireOp",EDGE,"E30")])],"isStart":false});var subQ89=sQuery(id+"F3.wireOp",EDGE,"E18.bottom");Q1=makeQuery(id+"F44.opFillet","BLEND_EDGE",EDGE,{"blendedFrom":[makeQuery(id+"F40.boolean.opBoolean","INTERSECT",EDGE,{"derivedFrom":[subQ6,subQ11]}),makeQuery(id+"F40.boolean.opBoolean","SPLIT",FACE,{"disambiguationData":[TD([subQ0])],"derivedFrom":makeQuery(id+"F25.boolean.opBoolean","SPLIT",FACE,{"disambiguationData":[TD([subQ6])],"derivedFrom":makeQuery(id+"F24.boolean.opBoolean","SPLIT",FACE,{"disambiguationData":[TD([makeQuery(id+"F5.opLoft","CAP_FACE",FACE,{"disambiguationData":[OSD([makeQuery(id+"F3.imprint","IMPRINT",FACE,{"disambiguationData":[TD([[makeQuery(id+"F3.imprint","IMPRINT",EDGE,{"derivedFrom":subQ89}),1.0]])]})])],"isStart":true})])],"derivedFrom":makeQuery(id+"F1.opRevolve","SWEPT_FACE",FACE,{"disambiguationData":[OSD([sQuery(id+"F0.wireOp",EDGE,"E4")])]})})})})],"blendedInto":[makeQuery(id+"F40.boolean.opBoolean","SPLIT",FACE,{"disambiguationData":[TD([subQ0])],"derivedFrom":makeQuery(id+"F25.boolean.opBoolean","SPLIT",FACE,{"disambiguationData":[TD([subQ6])],"derivedFrom":makeQuery(id+"F24.boolean.opBoolean","SPLIT",FACE,{"disambiguationData":[TD([makeQuery(id+"F5.opLoft","CAP_FACE",FACE,{"disambiguationData":[OSD([makeQuery(id+"F3.imprint","IMPRINT",FACE,{"disambiguationData":[TD([[makeQuery(id+"F3.imprint","IMPRINT",EDGE,{"derivedFrom":subQ89}),1.0]])]})])],"isStart":true})])],"derivedFrom":makeQuery(id+"F1.opRevolve","SWEPT_FACE",FACE,{"disambiguationData":[OSD([sQuery(id+"F0.wireOp",EDGE,"E4")])]})})})})]});}
            var Q2;
            {var subQ0=makeQuery(id+"F1.opRevolve","SWEPT_FACE",FACE,{"disambiguationData":[OSD([sQuery(id+"F0.wireOp",EDGE,"E1")])]});var subQ1=sQuery(id+"F4.wireOp",EDGE,"E26.11.3");var subQ2=sQuery(id+"F4.wireOp",EDGE,"E26.11.2");var subQ3=sQuery(id+"F3.wireOp",EDGE,"E20.11.3");var subQ4=sQuery(id+"F3.wireOp",EDGE,"E20.11.2");var subQ5=sQuery(id+"F3.wireOp",EDGE,"E20.11.1");var subQ6=makeQuery(id+"F10.opLoft","SWEPT_FACE",FACE,{"disambiguationData":[OSD([subQ5,subQ4,subQ3,sQuery(id+"F4.wireOp",EDGE,"E26.11.1"),subQ2,subQ1])]});var subQ13=makeQuery(id+"F40.opExtrude","CAP_FACE",FACE,{"disambiguationData":[OSD([sQuery(id+"F39.wireOp",EDGE,"E29"),sQuery(id+"F39.wireOp",EDGE,"E30")])],"isStart":false});var subQ79=sQuery(id+"F3.wireOp",EDGE,"E18.bottom");var subQ82=makeQuery(id+"F5.opLoft","CAP_FACE",FACE,{"disambiguationData":[OSD([makeQuery(id+"F3.imprint","IMPRINT",FACE,{"disambiguationData":[TD([[makeQuery(id+"F3.imprint","IMPRINT",EDGE,{"derivedFrom":subQ79}),1.0]])]})])],"isStart":true});Q2=makeQuery(id+"F44.opFillet","BLEND_EDGE",EDGE,{"blendedFrom":[makeQuery(id+"F40.boolean.opBoolean","INTERSECT",EDGE,{"derivedFrom":[subQ6,subQ13]}),makeQuery(id+"F40.boolean.opBoolean","SPLIT",FACE,{"disambiguationData":[TD([subQ0])],"derivedFrom":makeQuery(id+"F26.boolean.opBoolean","SPLIT",FACE,{"disambiguationData":[TD([subQ6])],"derivedFrom":makeQuery(id+"F25.boolean.opBoolean","SPLIT",FACE,{"disambiguationData":[TD([subQ82])],"derivedFrom":makeQuery(id+"F24.boolean.opBoolean","SPLIT",FACE,{"disambiguationData":[TD([subQ82])],"derivedFrom":makeQuery(id+"F1.opRevolve","SWEPT_FACE",FACE,{"disambiguationData":[OSD([sQuery(id+"F0.wireOp",EDGE,"E4")])]})})})})})],"blendedInto":[makeQuery(id+"F40.boolean.opBoolean","SPLIT",FACE,{"disambiguationData":[TD([subQ0])],"derivedFrom":makeQuery(id+"F26.boolean.opBoolean","SPLIT",FACE,{"disambiguationData":[TD([subQ6])],"derivedFrom":makeQuery(id+"F25.boolean.opBoolean","SPLIT",FACE,{"disambiguationData":[TD([subQ82])],"derivedFrom":makeQuery(id+"F24.boolean.opBoolean","SPLIT",FACE,{"disambiguationData":[TD([subQ82])],"derivedFrom":makeQuery(id+"F1.opRevolve","SWEPT_FACE",FACE,{"disambiguationData":[OSD([sQuery(id+"F0.wireOp",EDGE,"E4")])]})})})})})]});}
            var Q3;
            {var subQ0=makeQuery(id+"F1.opRevolve","SWEPT_FACE",FACE,{"disambiguationData":[OSD([sQuery(id+"F0.wireOp",EDGE,"E1")])]});var subQ1=sQuery(id+"F4.wireOp",EDGE,"E26.12.3");var subQ2=sQuery(id+"F4.wireOp",EDGE,"E26.12.2");var subQ3=sQuery(id+"F3.wireOp",EDGE,"E20.12.3");var subQ4=sQuery(id+"F3.wireOp",EDGE,"E20.12.2");var subQ5=sQuery(id+"F3.wireOp",EDGE,"E20.12.1");var subQ6=makeQuery(id+"F9.opLoft","SWEPT_FACE",FACE,{"disambiguationData":[OSD([subQ5,subQ4,subQ3,sQuery(id+"F4.wireOp",EDGE,"E26.12.1"),subQ2,subQ1])]});var subQ7=makeQuery(id+"F40.opExtrude","CAP_FACE",FACE,{"disambiguationData":[OSD([sQuery(id+"F39.wireOp",EDGE,"E29"),sQuery(id+"F39.wireOp",EDGE,"E30")])],"isStart":false});var subQ74=sQuery(id+"F3.wireOp",EDGE,"E18.bottom");var subQ77=makeQuery(id+"F5.opLoft","CAP_FACE",FACE,{"disambiguationData":[OSD([makeQuery(id+"F3.imprint","IMPRINT",FACE,{"disambiguationData":[TD([[makeQuery(id+"F3.imprint","IMPRINT",EDGE,{"derivedFrom":subQ74}),1.0]])]})])],"isStart":true});Q3=makeQuery(id+"F44.opFillet","BLEND_EDGE",EDGE,{"blendedFrom":[makeQuery(id+"F40.boolean.opBoolean","INTERSECT",EDGE,{"derivedFrom":[subQ6,subQ7]}),makeQuery(id+"F40.boolean.opBoolean","SPLIT",FACE,{"disambiguationData":[TD([subQ0])],"derivedFrom":makeQuery(id+"F27.boolean.opBoolean","SPLIT",FACE,{"disambiguationData":[TD([subQ6])],"derivedFrom":makeQuery(id+"F26.boolean.opBoolean","SPLIT",FACE,{"disambiguationData":[TD([subQ77])],"derivedFrom":makeQuery(id+"F25.boolean.opBoolean","SPLIT",FACE,{"disambiguationData":[TD([subQ77])],"derivedFrom":makeQuery(id+"F24.boolean.opBoolean","SPLIT",FACE,{"disambiguationData":[TD([subQ77])],"derivedFrom":makeQuery(id+"F1.opRevolve","SWEPT_FACE",FACE,{"disambiguationData":[OSD([sQuery(id+"F0.wireOp",EDGE,"E4")])]})})})})})})],"blendedInto":[makeQuery(id+"F40.boolean.opBoolean","SPLIT",FACE,{"disambiguationData":[TD([subQ0])],"derivedFrom":makeQuery(id+"F27.boolean.opBoolean","SPLIT",FACE,{"disambiguationData":[TD([subQ6])],"derivedFrom":makeQuery(id+"F26.boolean.opBoolean","SPLIT",FACE,{"disambiguationData":[TD([subQ77])],"derivedFrom":makeQuery(id+"F25.boolean.opBoolean","SPLIT",FACE,{"disambiguationData":[TD([subQ77])],"derivedFrom":makeQuery(id+"F24.boolean.opBoolean","SPLIT",FACE,{"disambiguationData":[TD([subQ77])],"derivedFrom":makeQuery(id+"F1.opRevolve","SWEPT_FACE",FACE,{"disambiguationData":[OSD([sQuery(id+"F0.wireOp",EDGE,"E4")])]})})})})})})]});}
            var Q4;
            {var subQ0=makeQuery(id+"F1.opRevolve","SWEPT_FACE",FACE,{"disambiguationData":[OSD([sQuery(id+"F0.wireOp",EDGE,"E1")])]});var subQ1=sQuery(id+"F4.wireOp",EDGE,"E26.13.3");var subQ2=sQuery(id+"F4.wireOp",EDGE,"E26.13.2");var subQ3=sQuery(id+"F3.wireOp",EDGE,"E20.13.3");var subQ4=sQuery(id+"F3.wireOp",EDGE,"E20.13.2");var subQ5=sQuery(id+"F3.wireOp",EDGE,"E20.13.1");var subQ6=makeQuery(id+"F8.opLoft","SWEPT_FACE",FACE,{"disambiguationData":[OSD([subQ5,subQ4,subQ3,sQuery(id+"F4.wireOp",EDGE,"E26.13.1"),subQ2,subQ1])]});var subQ13=makeQuery(id+"F40.opExtrude","CAP_FACE",FACE,{"disambiguationData":[OSD([sQuery(id+"F39.wireOp",EDGE,"E29"),sQuery(id+"F39.wireOp",EDGE,"E30")])],"isStart":false});var subQ56=sQuery(id+"F3.wireOp",EDGE,"E18.bottom");var subQ59=makeQuery(id+"F5.opLoft","CAP_FACE",FACE,{"disambiguationData":[OSD([makeQuery(id+"F3.imprint","IMPRINT",FACE,{"disambiguationData":[TD([[makeQuery(id+"F3.imprint","IMPRINT",EDGE,{"derivedFrom":subQ56}),1.0]])]})])],"isStart":true});Q4=makeQuery(id+"F44.opFillet","BLEND_EDGE",EDGE,{"blendedFrom":[makeQuery(id+"F40.boolean.opBoolean","INTERSECT",EDGE,{"derivedFrom":[subQ6,subQ13]}),makeQuery(id+"F40.boolean.opBoolean","SPLIT",FACE,{"disambiguationData":[TD([subQ0])],"derivedFrom":makeQuery(id+"F28.boolean.opBoolean","SPLIT",FACE,{"disambiguationData":[TD([subQ6])],"derivedFrom":makeQuery(id+"F27.boolean.opBoolean","SPLIT",FACE,{"disambiguationData":[TD([subQ59])],"derivedFrom":makeQuery(id+"F26.boolean.opBoolean","SPLIT",FACE,{"disambiguationData":[TD([subQ59])],"derivedFrom":makeQuery(id+"F25.boolean.opBoolean","SPLIT",FACE,{"disambiguationData":[TD([subQ59])],"derivedFrom":makeQuery(id+"F24.boolean.opBoolean","SPLIT",FACE,{"disambiguationData":[TD([subQ59])],"derivedFrom":makeQuery(id+"F1.opRevolve","SWEPT_FACE",FACE,{"disambiguationData":[OSD([sQuery(id+"F0.wireOp",EDGE,"E4")])]})})})})})})})],"blendedInto":[makeQuery(id+"F40.boolean.opBoolean","SPLIT",FACE,{"disambiguationData":[TD([subQ0])],"derivedFrom":makeQuery(id+"F28.boolean.opBoolean","SPLIT",FACE,{"disambiguationData":[TD([subQ6])],"derivedFrom":makeQuery(id+"F27.boolean.opBoolean","SPLIT",FACE,{"disambiguationData":[TD([subQ59])],"derivedFrom":makeQuery(id+"F26.boolean.opBoolean","SPLIT",FACE,{"disambiguationData":[TD([subQ59])],"derivedFrom":makeQuery(id+"F25.boolean.opBoolean","SPLIT",FACE,{"disambiguationData":[TD([subQ59])],"derivedFrom":makeQuery(id+"F24.boolean.opBoolean","SPLIT",FACE,{"disambiguationData":[TD([subQ59])],"derivedFrom":makeQuery(id+"F1.opRevolve","SWEPT_FACE",FACE,{"disambiguationData":[OSD([sQuery(id+"F0.wireOp",EDGE,"E4")])]})})})})})})})]});}
            var Q5;
            {var subQ0=makeQuery(id+"F1.opRevolve","SWEPT_FACE",FACE,{"disambiguationData":[OSD([sQuery(id+"F0.wireOp",EDGE,"E1")])]});var subQ1=sQuery(id+"F4.wireOp",EDGE,"E26.14.3");var subQ2=sQuery(id+"F4.wireOp",EDGE,"E26.14.2");var subQ3=sQuery(id+"F3.wireOp",EDGE,"E20.14.3");var subQ4=sQuery(id+"F3.wireOp",EDGE,"E20.14.2");var subQ5=sQuery(id+"F3.wireOp",EDGE,"E20.14.1");var subQ6=makeQuery(id+"F7.opLoft","SWEPT_FACE",FACE,{"disambiguationData":[OSD([subQ5,subQ4,subQ3,sQuery(id+"F4.wireOp",EDGE,"E26.14.1"),subQ2,subQ1])]});var subQ13=makeQuery(id+"F40.opExtrude","CAP_FACE",FACE,{"disambiguationData":[OSD([sQuery(id+"F39.wireOp",EDGE,"E29"),sQuery(id+"F39.wireOp",EDGE,"E30")])],"isStart":false});var subQ48=sQuery(id+"F3.wireOp",EDGE,"E18.bottom");var subQ51=makeQuery(id+"F5.opLoft","CAP_FACE",FACE,{"disambiguationData":[OSD([makeQuery(id+"F3.imprint","IMPRINT",FACE,{"disambiguationData":[TD([[makeQuery(id+"F3.imprint","IMPRINT",EDGE,{"derivedFrom":subQ48}),1.0]])]})])],"isStart":true});Q5=makeQuery(id+"F44.opFillet","BLEND_EDGE",EDGE,{"blendedFrom":[makeQuery(id+"F40.boolean.opBoolean","INTERSECT",EDGE,{"derivedFrom":[subQ6,subQ13]}),makeQuery(id+"F40.boolean.opBoolean","SPLIT",FACE,{"disambiguationData":[TD([subQ0])],"derivedFrom":makeQuery(id+"F29.boolean.opBoolean","SPLIT",FACE,{"disambiguationData":[TD([subQ6])],"derivedFrom":makeQuery(id+"F28.boolean.opBoolean","SPLIT",FACE,{"disambiguationData":[TD([subQ51])],"derivedFrom":makeQuery(id+"F27.boolean.opBoolean","SPLIT",FACE,{"disambiguationData":[TD([subQ51])],"derivedFrom":makeQuery(id+"F26.boolean.opBoolean","SPLIT",FACE,{"disambiguationData":[TD([subQ51])],"derivedFrom":makeQuery(id+"F25.boolean.opBoolean","SPLIT",FACE,{"disambiguationData":[TD([subQ51])],"derivedFrom":makeQuery(id+"F24.boolean.opBoolean","SPLIT",FACE,{"disambiguationData":[TD([subQ51])],"derivedFrom":makeQuery(id+"F1.opRevolve","SWEPT_FACE",FACE,{"disambiguationData":[OSD([sQuery(id+"F0.wireOp",EDGE,"E4")])]})})})})})})})})],"blendedInto":[makeQuery(id+"F40.boolean.opBoolean","SPLIT",FACE,{"disambiguationData":[TD([subQ0])],"derivedFrom":makeQuery(id+"F29.boolean.opBoolean","SPLIT",FACE,{"disambiguationData":[TD([subQ6])],"derivedFrom":makeQuery(id+"F28.boolean.opBoolean","SPLIT",FACE,{"disambiguationData":[TD([subQ51])],"derivedFrom":makeQuery(id+"F27.boolean.opBoolean","SPLIT",FACE,{"disambiguationData":[TD([subQ51])],"derivedFrom":makeQuery(id+"F26.boolean.opBoolean","SPLIT",FACE,{"disambiguationData":[TD([subQ51])],"derivedFrom":makeQuery(id+"F25.boolean.opBoolean","SPLIT",FACE,{"disambiguationData":[TD([subQ51])],"derivedFrom":makeQuery(id+"F24.boolean.opBoolean","SPLIT",FACE,{"disambiguationData":[TD([subQ51])],"derivedFrom":makeQuery(id+"F1.opRevolve","SWEPT_FACE",FACE,{"disambiguationData":[OSD([sQuery(id+"F0.wireOp",EDGE,"E4")])]})})})})})})})})]});}
            var Q6;
            {var subQ0=makeQuery(id+"F1.opRevolve","SWEPT_FACE",FACE,{"disambiguationData":[OSD([sQuery(id+"F0.wireOp",EDGE,"E1")])]});var subQ7=sQuery(id+"F4.wireOp",EDGE,"E26.15.3");var subQ8=sQuery(id+"F4.wireOp",EDGE,"E26.15.2");var subQ9=sQuery(id+"F3.wireOp",EDGE,"E20.15.3");var subQ10=sQuery(id+"F3.wireOp",EDGE,"E20.15.2");var subQ11=sQuery(id+"F3.wireOp",EDGE,"E20.15.1");var subQ12=makeQuery(id+"F6.opLoft","SWEPT_FACE",FACE,{"disambiguationData":[OSD([subQ11,subQ10,subQ9,sQuery(id+"F4.wireOp",EDGE,"E26.15.1"),subQ8,subQ7])]});var subQ13=makeQuery(id+"F40.opExtrude","CAP_FACE",FACE,{"disambiguationData":[OSD([sQuery(id+"F39.wireOp",EDGE,"E29"),sQuery(id+"F39.wireOp",EDGE,"E30")])],"isStart":false});var subQ47=sQuery(id+"F3.wireOp",EDGE,"E18.bottom");var subQ50=makeQuery(id+"F5.opLoft","CAP_FACE",FACE,{"disambiguationData":[OSD([makeQuery(id+"F3.imprint","IMPRINT",FACE,{"disambiguationData":[TD([[makeQuery(id+"F3.imprint","IMPRINT",EDGE,{"derivedFrom":subQ47}),1.0]])]})])],"isStart":true});Q6=makeQuery(id+"F44.opFillet","BLEND_EDGE",EDGE,{"blendedFrom":[makeQuery(id+"F40.boolean.opBoolean","INTERSECT",EDGE,{"derivedFrom":[subQ12,subQ13]}),makeQuery(id+"F40.boolean.opBoolean","SPLIT",FACE,{"disambiguationData":[TD([subQ0])],"derivedFrom":makeQuery(id+"F30.boolean.opBoolean","SPLIT",FACE,{"disambiguationData":[TD([subQ12])],"derivedFrom":makeQuery(id+"F29.boolean.opBoolean","SPLIT",FACE,{"disambiguationData":[TD([subQ50])],"derivedFrom":makeQuery(id+"F28.boolean.opBoolean","SPLIT",FACE,{"disambiguationData":[TD([subQ50])],"derivedFrom":makeQuery(id+"F27.boolean.opBoolean","SPLIT",FACE,{"disambiguationData":[TD([subQ50])],"derivedFrom":makeQuery(id+"F26.boolean.opBoolean","SPLIT",FACE,{"disambiguationData":[TD([subQ50])],"derivedFrom":makeQuery(id+"F25.boolean.opBoolean","SPLIT",FACE,{"disambiguationData":[TD([subQ50])],"derivedFrom":makeQuery(id+"F24.boolean.opBoolean","SPLIT",FACE,{"disambiguationData":[TD([subQ50])],"derivedFrom":makeQuery(id+"F1.opRevolve","SWEPT_FACE",FACE,{"disambiguationData":[OSD([sQuery(id+"F0.wireOp",EDGE,"E4")])]})})})})})})})})})],"blendedInto":[makeQuery(id+"F40.boolean.opBoolean","SPLIT",FACE,{"disambiguationData":[TD([subQ0])],"derivedFrom":makeQuery(id+"F30.boolean.opBoolean","SPLIT",FACE,{"disambiguationData":[TD([subQ12])],"derivedFrom":makeQuery(id+"F29.boolean.opBoolean","SPLIT",FACE,{"disambiguationData":[TD([subQ50])],"derivedFrom":makeQuery(id+"F28.boolean.opBoolean","SPLIT",FACE,{"disambiguationData":[TD([subQ50])],"derivedFrom":makeQuery(id+"F27.boolean.opBoolean","SPLIT",FACE,{"disambiguationData":[TD([subQ50])],"derivedFrom":makeQuery(id+"F26.boolean.opBoolean","SPLIT",FACE,{"disambiguationData":[TD([subQ50])],"derivedFrom":makeQuery(id+"F25.boolean.opBoolean","SPLIT",FACE,{"disambiguationData":[TD([subQ50])],"derivedFrom":makeQuery(id+"F24.boolean.opBoolean","SPLIT",FACE,{"disambiguationData":[TD([subQ50])],"derivedFrom":makeQuery(id+"F1.opRevolve","SWEPT_FACE",FACE,{"disambiguationData":[OSD([sQuery(id+"F0.wireOp",EDGE,"E4")])]})})})})})})})})})]});}
            var Q7;
            {var subQ0=makeQuery(id+"F1.opRevolve","SWEPT_FACE",FACE,{"disambiguationData":[OSD([sQuery(id+"F0.wireOp",EDGE,"E1")])]});var subQ1=sQuery(id+"F4.wireOp",EDGE,"E23");var subQ2=sQuery(id+"F4.wireOp",EDGE,"E22");var subQ3=sQuery(id+"F3.wireOp",EDGE,"E18.right");var subQ4=sQuery(id+"F3.wireOp",EDGE,"E18.top");var subQ5=sQuery(id+"F3.wireOp",EDGE,"E18.bottom");var subQ6=makeQuery(id+"F5.opLoft","SWEPT_FACE",FACE,{"disambiguationData":[OSD([subQ5,subQ4,subQ3,subQ2,subQ1,sQuery(id+"F4.wireOp",EDGE,"E24")])]});var subQ13=makeQuery(id+"F40.opExtrude","CAP_FACE",FACE,{"disambiguationData":[OSD([sQuery(id+"F39.wireOp",EDGE,"E29"),sQuery(id+"F39.wireOp",EDGE,"E30")])],"isStart":false});var subQ58=makeQuery(id+"F5.opLoft","CAP_FACE",FACE,{"disambiguationData":[OSD([makeQuery(id+"F3.imprint","IMPRINT",FACE,{"disambiguationData":[TD([[makeQuery(id+"F3.imprint","IMPRINT",EDGE,{"derivedFrom":subQ5}),1.0]])]})])],"isStart":true});Q7=makeQuery(id+"F44.opFillet","BLEND_EDGE",EDGE,{"blendedFrom":[makeQuery(id+"F40.boolean.opBoolean","INTERSECT",EDGE,{"derivedFrom":[subQ6,subQ13]}),makeQuery(id+"F40.boolean.opBoolean","SPLIT",FACE,{"disambiguationData":[TD([subQ0])],"derivedFrom":makeQuery(id+"F31.boolean.opBoolean","SPLIT",FACE,{"disambiguationData":[TD([subQ6])],"derivedFrom":makeQuery(id+"F30.boolean.opBoolean","SPLIT",FACE,{"disambiguationData":[TD([subQ58])],"derivedFrom":makeQuery(id+"F29.boolean.opBoolean","SPLIT",FACE,{"disambiguationData":[TD([subQ58])],"derivedFrom":makeQuery(id+"F28.boolean.opBoolean","SPLIT",FACE,{"disambiguationData":[TD([subQ58])],"derivedFrom":makeQuery(id+"F27.boolean.opBoolean","SPLIT",FACE,{"disambiguationData":[TD([subQ58])],"derivedFrom":makeQuery(id+"F26.boolean.opBoolean","SPLIT",FACE,{"disambiguationData":[TD([subQ58])],"derivedFrom":makeQuery(id+"F25.boolean.opBoolean","SPLIT",FACE,{"disambiguationData":[TD([subQ58])],"derivedFrom":makeQuery(id+"F24.boolean.opBoolean","SPLIT",FACE,{"disambiguationData":[TD([subQ58])],"derivedFrom":makeQuery(id+"F1.opRevolve","SWEPT_FACE",FACE,{"disambiguationData":[OSD([sQuery(id+"F0.wireOp",EDGE,"E4")])]})})})})})})})})})})],"blendedInto":[makeQuery(id+"F40.boolean.opBoolean","SPLIT",FACE,{"disambiguationData":[TD([subQ0])],"derivedFrom":makeQuery(id+"F31.boolean.opBoolean","SPLIT",FACE,{"disambiguationData":[TD([subQ6])],"derivedFrom":makeQuery(id+"F30.boolean.opBoolean","SPLIT",FACE,{"disambiguationData":[TD([subQ58])],"derivedFrom":makeQuery(id+"F29.boolean.opBoolean","SPLIT",FACE,{"disambiguationData":[TD([subQ58])],"derivedFrom":makeQuery(id+"F28.boolean.opBoolean","SPLIT",FACE,{"disambiguationData":[TD([subQ58])],"derivedFrom":makeQuery(id+"F27.boolean.opBoolean","SPLIT",FACE,{"disambiguationData":[TD([subQ58])],"derivedFrom":makeQuery(id+"F26.boolean.opBoolean","SPLIT",FACE,{"disambiguationData":[TD([subQ58])],"derivedFrom":makeQuery(id+"F25.boolean.opBoolean","SPLIT",FACE,{"disambiguationData":[TD([subQ58])],"derivedFrom":makeQuery(id+"F24.boolean.opBoolean","SPLIT",FACE,{"disambiguationData":[TD([subQ58])],"derivedFrom":makeQuery(id+"F1.opRevolve","SWEPT_FACE",FACE,{"disambiguationData":[OSD([sQuery(id+"F0.wireOp",EDGE,"E4")])]})})})})})})})})})})]});}
            var Q8;
            {var subQ0=makeQuery(id+"F1.opRevolve","SWEPT_FACE",FACE,{"disambiguationData":[OSD([sQuery(id+"F0.wireOp",EDGE,"E1")])]});var subQ1=sQuery(id+"F4.wireOp",EDGE,"E23");var subQ2=sQuery(id+"F4.wireOp",EDGE,"E22");var subQ3=sQuery(id+"F3.wireOp",EDGE,"E18.left");var subQ4=sQuery(id+"F3.wireOp",EDGE,"E18.top");var subQ5=sQuery(id+"F3.wireOp",EDGE,"E18.bottom");var subQ6=makeQuery(id+"F5.opLoft","SWEPT_FACE",FACE,{"disambiguationData":[OSD([subQ5,subQ4,subQ3,sQuery(id+"F4.wireOp",EDGE,"E21"),subQ2,subQ1])]});var subQ7=sQuery(id+"F4.wireOp",EDGE,"E26.1.3");var subQ8=sQuery(id+"F4.wireOp",EDGE,"E26.1.2");var subQ9=sQuery(id+"F3.wireOp",EDGE,"E20.1.3");var subQ10=sQuery(id+"F3.wireOp",EDGE,"E20.1.2");var subQ11=sQuery(id+"F3.wireOp",EDGE,"E20.1.1");var subQ12=makeQuery(id+"F20.opLoft","SWEPT_FACE",FACE,{"disambiguationData":[OSD([subQ11,subQ10,subQ9,sQuery(id+"F4.wireOp",EDGE,"E26.1.1"),subQ8,subQ7])]});var subQ13=makeQuery(id+"F40.opExtrude","CAP_FACE",FACE,{"disambiguationData":[OSD([sQuery(id+"F39.wireOp",EDGE,"E29"),sQuery(id+"F39.wireOp",EDGE,"E30")])],"isStart":false});var subQ64=sQuery(id+"F3.wireOp",EDGE,"E20.7.0");var subQ72=makeQuery(id+"F14.opLoft","CAP_FACE",FACE,{"disambiguationData":[OSD([makeQuery(id+"F3.imprint","IMPRINT",FACE,{"disambiguationData":[TD([[makeQuery(id+"F3.imprint","IMPRINT",EDGE,{"derivedFrom":subQ64}),-1.0]])]})])],"isStart":true});var subQ80=makeQuery(id+"F5.opLoft","CAP_FACE",FACE,{"disambiguationData":[OSD([makeQuery(id+"F3.imprint","IMPRINT",FACE,{"disambiguationData":[TD([[makeQuery(id+"F3.imprint","IMPRINT",EDGE,{"derivedFrom":subQ5}),1.0]])]})])],"isStart":true});Q8=makeQuery(id+"F44.opFillet","BLEND_EDGE",EDGE,{"blendedFrom":[makeQuery(id+"F40.boolean.opBoolean","INTERSECT",EDGE,{"derivedFrom":[subQ12,subQ13]}),makeQuery(id+"F40.boolean.opBoolean","SPLIT",FACE,{"disambiguationData":[TD([subQ0])],"derivedFrom":makeQuery(id+"F32.boolean.opBoolean","SPLIT",FACE,{"disambiguationData":[TD([subQ6])],"derivedFrom":makeQuery(id+"F31.boolean.opBoolean","SPLIT",FACE,{"disambiguationData":[TD([subQ72])],"derivedFrom":makeQuery(id+"F30.boolean.opBoolean","SPLIT",FACE,{"disambiguationData":[TD([subQ80])],"derivedFrom":makeQuery(id+"F29.boolean.opBoolean","SPLIT",FACE,{"disambiguationData":[TD([subQ80])],"derivedFrom":makeQuery(id+"F28.boolean.opBoolean","SPLIT",FACE,{"disambiguationData":[TD([subQ80])],"derivedFrom":makeQuery(id+"F27.boolean.opBoolean","SPLIT",FACE,{"disambiguationData":[TD([subQ80])],"derivedFrom":makeQuery(id+"F26.boolean.opBoolean","SPLIT",FACE,{"disambiguationData":[TD([subQ80])],"derivedFrom":makeQuery(id+"F25.boolean.opBoolean","SPLIT",FACE,{"disambiguationData":[TD([subQ80])],"derivedFrom":makeQuery(id+"F24.boolean.opBoolean","SPLIT",FACE,{"disambiguationData":[TD([subQ80])],"derivedFrom":makeQuery(id+"F1.opRevolve","SWEPT_FACE",FACE,{"disambiguationData":[OSD([sQuery(id+"F0.wireOp",EDGE,"E4")])]})})})})})})})})})})})],"blendedInto":[makeQuery(id+"F40.boolean.opBoolean","SPLIT",FACE,{"disambiguationData":[TD([subQ0])],"derivedFrom":makeQuery(id+"F32.boolean.opBoolean","SPLIT",FACE,{"disambiguationData":[TD([subQ6])],"derivedFrom":makeQuery(id+"F31.boolean.opBoolean","SPLIT",FACE,{"disambiguationData":[TD([subQ72])],"derivedFrom":makeQuery(id+"F30.boolean.opBoolean","SPLIT",FACE,{"disambiguationData":[TD([subQ80])],"derivedFrom":makeQuery(id+"F29.boolean.opBoolean","SPLIT",FACE,{"disambiguationData":[TD([subQ80])],"derivedFrom":makeQuery(id+"F28.boolean.opBoolean","SPLIT",FACE,{"disambiguationData":[TD([subQ80])],"derivedFrom":makeQuery(id+"F27.boolean.opBoolean","SPLIT",FACE,{"disambiguationData":[TD([subQ80])],"derivedFrom":makeQuery(id+"F26.boolean.opBoolean","SPLIT",FACE,{"disambiguationData":[TD([subQ80])],"derivedFrom":makeQuery(id+"F25.boolean.opBoolean","SPLIT",FACE,{"disambiguationData":[TD([subQ80])],"derivedFrom":makeQuery(id+"F24.boolean.opBoolean","SPLIT",FACE,{"disambiguationData":[TD([subQ80])],"derivedFrom":makeQuery(id+"F1.opRevolve","SWEPT_FACE",FACE,{"disambiguationData":[OSD([sQuery(id+"F0.wireOp",EDGE,"E4")])]})})})})})})})})})})})]});}
            var Q9;
            {var subQ0=makeQuery(id+"F1.opRevolve","SWEPT_FACE",FACE,{"disambiguationData":[OSD([sQuery(id+"F0.wireOp",EDGE,"E1")])]});var subQ1=sQuery(id+"F4.wireOp",EDGE,"E26.2.3");var subQ2=sQuery(id+"F4.wireOp",EDGE,"E26.2.2");var subQ3=sQuery(id+"F3.wireOp",EDGE,"E20.2.3");var subQ4=sQuery(id+"F3.wireOp",EDGE,"E20.2.2");var subQ5=sQuery(id+"F3.wireOp",EDGE,"E20.2.1");var subQ6=makeQuery(id+"F19.opLoft","SWEPT_FACE",FACE,{"disambiguationData":[OSD([subQ5,subQ4,subQ3,sQuery(id+"F4.wireOp",EDGE,"E26.2.1"),subQ2,subQ1])]});var subQ13=makeQuery(id+"F40.opExtrude","CAP_FACE",FACE,{"disambiguationData":[OSD([sQuery(id+"F39.wireOp",EDGE,"E29"),sQuery(id+"F39.wireOp",EDGE,"E30")])],"isStart":false});var subQ55=sQuery(id+"F3.wireOp",EDGE,"E20.7.0");var subQ62=makeQuery(id+"F14.opLoft","CAP_FACE",FACE,{"disambiguationData":[OSD([makeQuery(id+"F3.imprint","IMPRINT",FACE,{"disambiguationData":[TD([[makeQuery(id+"F3.imprint","IMPRINT",EDGE,{"derivedFrom":subQ55}),-1.0]])]})])],"isStart":true});var subQ75=sQuery(id+"F3.wireOp",EDGE,"E18.bottom");var subQ80=makeQuery(id+"F5.opLoft","CAP_FACE",FACE,{"disambiguationData":[OSD([makeQuery(id+"F3.imprint","IMPRINT",FACE,{"disambiguationData":[TD([[makeQuery(id+"F3.imprint","IMPRINT",EDGE,{"derivedFrom":subQ75}),1.0]])]})])],"isStart":true});Q9=makeQuery(id+"F44.opFillet","BLEND_EDGE",EDGE,{"blendedFrom":[makeQuery(id+"F40.boolean.opBoolean","INTERSECT",EDGE,{"derivedFrom":[subQ6,subQ13]}),makeQuery(id+"F40.boolean.opBoolean","SPLIT",FACE,{"disambiguationData":[TD([subQ0])],"derivedFrom":makeQuery(id+"F33.boolean.opBoolean","SPLIT",FACE,{"disambiguationData":[TD([subQ6])],"derivedFrom":makeQuery(id+"F32.boolean.opBoolean","SPLIT",FACE,{"disambiguationData":[TD([subQ62])],"derivedFrom":makeQuery(id+"F31.boolean.opBoolean","SPLIT",FACE,{"disambiguationData":[TD([subQ62])],"derivedFrom":makeQuery(id+"F30.boolean.opBoolean","SPLIT",FACE,{"disambiguationData":[TD([subQ80])],"derivedFrom":makeQuery(id+"F29.boolean.opBoolean","SPLIT",FACE,{"disambiguationData":[TD([subQ80])],"derivedFrom":makeQuery(id+"F28.boolean.opBoolean","SPLIT",FACE,{"disambiguationData":[TD([subQ80])],"derivedFrom":makeQuery(id+"F27.boolean.opBoolean","SPLIT",FACE,{"disambiguationData":[TD([subQ80])],"derivedFrom":makeQuery(id+"F26.boolean.opBoolean","SPLIT",FACE,{"disambiguationData":[TD([subQ80])],"derivedFrom":makeQuery(id+"F25.boolean.opBoolean","SPLIT",FACE,{"disambiguationData":[TD([subQ80])],"derivedFrom":makeQuery(id+"F24.boolean.opBoolean","SPLIT",FACE,{"disambiguationData":[TD([subQ80])],"derivedFrom":makeQuery(id+"F1.opRevolve","SWEPT_FACE",FACE,{"disambiguationData":[OSD([sQuery(id+"F0.wireOp",EDGE,"E4")])]})})})})})})})})})})})})],"blendedInto":[makeQuery(id+"F40.boolean.opBoolean","SPLIT",FACE,{"disambiguationData":[TD([subQ0])],"derivedFrom":makeQuery(id+"F33.boolean.opBoolean","SPLIT",FACE,{"disambiguationData":[TD([subQ6])],"derivedFrom":makeQuery(id+"F32.boolean.opBoolean","SPLIT",FACE,{"disambiguationData":[TD([subQ62])],"derivedFrom":makeQuery(id+"F31.boolean.opBoolean","SPLIT",FACE,{"disambiguationData":[TD([subQ62])],"derivedFrom":makeQuery(id+"F30.boolean.opBoolean","SPLIT",FACE,{"disambiguationData":[TD([subQ80])],"derivedFrom":makeQuery(id+"F29.boolean.opBoolean","SPLIT",FACE,{"disambiguationData":[TD([subQ80])],"derivedFrom":makeQuery(id+"F28.boolean.opBoolean","SPLIT",FACE,{"disambiguationData":[TD([subQ80])],"derivedFrom":makeQuery(id+"F27.boolean.opBoolean","SPLIT",FACE,{"disambiguationData":[TD([subQ80])],"derivedFrom":makeQuery(id+"F26.boolean.opBoolean","SPLIT",FACE,{"disambiguationData":[TD([subQ80])],"derivedFrom":makeQuery(id+"F25.boolean.opBoolean","SPLIT",FACE,{"disambiguationData":[TD([subQ80])],"derivedFrom":makeQuery(id+"F24.boolean.opBoolean","SPLIT",FACE,{"disambiguationData":[TD([subQ80])],"derivedFrom":makeQuery(id+"F1.opRevolve","SWEPT_FACE",FACE,{"disambiguationData":[OSD([sQuery(id+"F0.wireOp",EDGE,"E4")])]})})})})})})})})})})})})]});}
            var Q10;
            {var subQ0=makeQuery(id+"F1.opRevolve","SWEPT_FACE",FACE,{"disambiguationData":[OSD([sQuery(id+"F0.wireOp",EDGE,"E1")])]});var subQ1=sQuery(id+"F4.wireOp",EDGE,"E26.3.3");var subQ2=sQuery(id+"F4.wireOp",EDGE,"E26.3.2");var subQ3=sQuery(id+"F3.wireOp",EDGE,"E20.3.3");var subQ4=sQuery(id+"F3.wireOp",EDGE,"E20.3.2");var subQ5=sQuery(id+"F3.wireOp",EDGE,"E20.3.1");var subQ6=makeQuery(id+"F18.opLoft","SWEPT_FACE",FACE,{"disambiguationData":[OSD([subQ5,subQ4,subQ3,sQuery(id+"F4.wireOp",EDGE,"E26.3.1"),subQ2,subQ1])]});var subQ13=makeQuery(id+"F40.opExtrude","CAP_FACE",FACE,{"disambiguationData":[OSD([sQuery(id+"F39.wireOp",EDGE,"E29"),sQuery(id+"F39.wireOp",EDGE,"E30")])],"isStart":false});var subQ35=sQuery(id+"F3.wireOp",EDGE,"E20.7.0");var subQ39=makeQuery(id+"F14.opLoft","CAP_FACE",FACE,{"disambiguationData":[OSD([makeQuery(id+"F3.imprint","IMPRINT",FACE,{"disambiguationData":[TD([[makeQuery(id+"F3.imprint","IMPRINT",EDGE,{"derivedFrom":subQ35}),-1.0]])]})])],"isStart":true});var subQ75=sQuery(id+"F3.wireOp",EDGE,"E18.bottom");var subQ80=makeQuery(id+"F5.opLoft","CAP_FACE",FACE,{"disambiguationData":[OSD([makeQuery(id+"F3.imprint","IMPRINT",FACE,{"disambiguationData":[TD([[makeQuery(id+"F3.imprint","IMPRINT",EDGE,{"derivedFrom":subQ75}),1.0]])]})])],"isStart":true});Q10=makeQuery(id+"F44.opFillet","BLEND_EDGE",EDGE,{"blendedFrom":[makeQuery(id+"F40.boolean.opBoolean","INTERSECT",EDGE,{"derivedFrom":[subQ6,subQ13]}),makeQuery(id+"F40.boolean.opBoolean","SPLIT",FACE,{"disambiguationData":[TD([subQ0])],"derivedFrom":makeQuery(id+"F34.boolean.opBoolean","SPLIT",FACE,{"disambiguationData":[TD([subQ6])],"derivedFrom":makeQuery(id+"F33.boolean.opBoolean","SPLIT",FACE,{"disambiguationData":[TD([subQ39])],"derivedFrom":makeQuery(id+"F32.boolean.opBoolean","SPLIT",FACE,{"disambiguationData":[TD([subQ39])],"derivedFrom":makeQuery(id+"F31.boolean.opBoolean","SPLIT",FACE,{"disambiguationData":[TD([subQ39])],"derivedFrom":makeQuery(id+"F30.boolean.opBoolean","SPLIT",FACE,{"disambiguationData":[TD([subQ80])],"derivedFrom":makeQuery(id+"F29.boolean.opBoolean","SPLIT",FACE,{"disambiguationData":[TD([subQ80])],"derivedFrom":makeQuery(id+"F28.boolean.opBoolean","SPLIT",FACE,{"disambiguationData":[TD([subQ80])],"derivedFrom":makeQuery(id+"F27.boolean.opBoolean","SPLIT",FACE,{"disambiguationData":[TD([subQ80])],"derivedFrom":makeQuery(id+"F26.boolean.opBoolean","SPLIT",FACE,{"disambiguationData":[TD([subQ80])],"derivedFrom":makeQuery(id+"F25.boolean.opBoolean","SPLIT",FACE,{"disambiguationData":[TD([subQ80])],"derivedFrom":makeQuery(id+"F24.boolean.opBoolean","SPLIT",FACE,{"disambiguationData":[TD([subQ80])],"derivedFrom":makeQuery(id+"F1.opRevolve","SWEPT_FACE",FACE,{"disambiguationData":[OSD([sQuery(id+"F0.wireOp",EDGE,"E4")])]})})})})})})})})})})})})})],"blendedInto":[makeQuery(id+"F40.boolean.opBoolean","SPLIT",FACE,{"disambiguationData":[TD([subQ0])],"derivedFrom":makeQuery(id+"F34.boolean.opBoolean","SPLIT",FACE,{"disambiguationData":[TD([subQ6])],"derivedFrom":makeQuery(id+"F33.boolean.opBoolean","SPLIT",FACE,{"disambiguationData":[TD([subQ39])],"derivedFrom":makeQuery(id+"F32.boolean.opBoolean","SPLIT",FACE,{"disambiguationData":[TD([subQ39])],"derivedFrom":makeQuery(id+"F31.boolean.opBoolean","SPLIT",FACE,{"disambiguationData":[TD([subQ39])],"derivedFrom":makeQuery(id+"F30.boolean.opBoolean","SPLIT",FACE,{"disambiguationData":[TD([subQ80])],"derivedFrom":makeQuery(id+"F29.boolean.opBoolean","SPLIT",FACE,{"disambiguationData":[TD([subQ80])],"derivedFrom":makeQuery(id+"F28.boolean.opBoolean","SPLIT",FACE,{"disambiguationData":[TD([subQ80])],"derivedFrom":makeQuery(id+"F27.boolean.opBoolean","SPLIT",FACE,{"disambiguationData":[TD([subQ80])],"derivedFrom":makeQuery(id+"F26.boolean.opBoolean","SPLIT",FACE,{"disambiguationData":[TD([subQ80])],"derivedFrom":makeQuery(id+"F25.boolean.opBoolean","SPLIT",FACE,{"disambiguationData":[TD([subQ80])],"derivedFrom":makeQuery(id+"F24.boolean.opBoolean","SPLIT",FACE,{"disambiguationData":[TD([subQ80])],"derivedFrom":makeQuery(id+"F1.opRevolve","SWEPT_FACE",FACE,{"disambiguationData":[OSD([sQuery(id+"F0.wireOp",EDGE,"E4")])]})})})})})})})})})})})})})]});}
            var Q11;
            {var subQ0=makeQuery(id+"F1.opRevolve","SWEPT_FACE",FACE,{"disambiguationData":[OSD([sQuery(id+"F0.wireOp",EDGE,"E1")])]});var subQ7=sQuery(id+"F4.wireOp",EDGE,"E26.4.3");var subQ8=sQuery(id+"F4.wireOp",EDGE,"E26.4.2");var subQ9=sQuery(id+"F3.wireOp",EDGE,"E20.4.3");var subQ10=sQuery(id+"F3.wireOp",EDGE,"E20.4.2");var subQ11=sQuery(id+"F3.wireOp",EDGE,"E20.4.1");var subQ12=makeQuery(id+"F17.opLoft","SWEPT_FACE",FACE,{"disambiguationData":[OSD([subQ11,subQ10,subQ9,sQuery(id+"F4.wireOp",EDGE,"E26.4.1"),subQ8,subQ7])]});var subQ13=makeQuery(id+"F40.opExtrude","CAP_FACE",FACE,{"disambiguationData":[OSD([sQuery(id+"F39.wireOp",EDGE,"E29"),sQuery(id+"F39.wireOp",EDGE,"E30")])],"isStart":false});var subQ32=sQuery(id+"F3.wireOp",EDGE,"E20.7.0");var subQ36=makeQuery(id+"F14.opLoft","CAP_FACE",FACE,{"disambiguationData":[OSD([makeQuery(id+"F3.imprint","IMPRINT",FACE,{"disambiguationData":[TD([[makeQuery(id+"F3.imprint","IMPRINT",EDGE,{"derivedFrom":subQ32}),-1.0]])]})])],"isStart":true});var subQ75=sQuery(id+"F3.wireOp",EDGE,"E18.bottom");var subQ80=makeQuery(id+"F5.opLoft","CAP_FACE",FACE,{"disambiguationData":[OSD([makeQuery(id+"F3.imprint","IMPRINT",FACE,{"disambiguationData":[TD([[makeQuery(id+"F3.imprint","IMPRINT",EDGE,{"derivedFrom":subQ75}),1.0]])]})])],"isStart":true});Q11=makeQuery(id+"F44.opFillet","BLEND_EDGE",EDGE,{"blendedFrom":[makeQuery(id+"F40.boolean.opBoolean","INTERSECT",EDGE,{"derivedFrom":[subQ12,subQ13]}),makeQuery(id+"F40.boolean.opBoolean","SPLIT",FACE,{"disambiguationData":[TD([subQ0])],"derivedFrom":makeQuery(id+"F35.boolean.opBoolean","SPLIT",FACE,{"disambiguationData":[TD([subQ12])],"derivedFrom":makeQuery(id+"F34.boolean.opBoolean","SPLIT",FACE,{"disambiguationData":[TD([subQ36])],"derivedFrom":makeQuery(id+"F33.boolean.opBoolean","SPLIT",FACE,{"disambiguationData":[TD([subQ36])],"derivedFrom":makeQuery(id+"F32.boolean.opBoolean","SPLIT",FACE,{"disambiguationData":[TD([subQ36])],"derivedFrom":makeQuery(id+"F31.boolean.opBoolean","SPLIT",FACE,{"disambiguationData":[TD([subQ36])],"derivedFrom":makeQuery(id+"F30.boolean.opBoolean","SPLIT",FACE,{"disambiguationData":[TD([subQ80])],"derivedFrom":makeQuery(id+"F29.boolean.opBoolean","SPLIT",FACE,{"disambiguationData":[TD([subQ80])],"derivedFrom":makeQuery(id+"F28.boolean.opBoolean","SPLIT",FACE,{"disambiguationData":[TD([subQ80])],"derivedFrom":makeQuery(id+"F27.boolean.opBoolean","SPLIT",FACE,{"disambiguationData":[TD([subQ80])],"derivedFrom":makeQuery(id+"F26.boolean.opBoolean","SPLIT",FACE,{"disambiguationData":[TD([subQ80])],"derivedFrom":makeQuery(id+"F25.boolean.opBoolean","SPLIT",FACE,{"disambiguationData":[TD([subQ80])],"derivedFrom":makeQuery(id+"F24.boolean.opBoolean","SPLIT",FACE,{"disambiguationData":[TD([subQ80])],"derivedFrom":makeQuery(id+"F1.opRevolve","SWEPT_FACE",FACE,{"disambiguationData":[OSD([sQuery(id+"F0.wireOp",EDGE,"E4")])]})})})})})})})})})})})})})})],"blendedInto":[makeQuery(id+"F40.boolean.opBoolean","SPLIT",FACE,{"disambiguationData":[TD([subQ0])],"derivedFrom":makeQuery(id+"F35.boolean.opBoolean","SPLIT",FACE,{"disambiguationData":[TD([subQ12])],"derivedFrom":makeQuery(id+"F34.boolean.opBoolean","SPLIT",FACE,{"disambiguationData":[TD([subQ36])],"derivedFrom":makeQuery(id+"F33.boolean.opBoolean","SPLIT",FACE,{"disambiguationData":[TD([subQ36])],"derivedFrom":makeQuery(id+"F32.boolean.opBoolean","SPLIT",FACE,{"disambiguationData":[TD([subQ36])],"derivedFrom":makeQuery(id+"F31.boolean.opBoolean","SPLIT",FACE,{"disambiguationData":[TD([subQ36])],"derivedFrom":makeQuery(id+"F30.boolean.opBoolean","SPLIT",FACE,{"disambiguationData":[TD([subQ80])],"derivedFrom":makeQuery(id+"F29.boolean.opBoolean","SPLIT",FACE,{"disambiguationData":[TD([subQ80])],"derivedFrom":makeQuery(id+"F28.boolean.opBoolean","SPLIT",FACE,{"disambiguationData":[TD([subQ80])],"derivedFrom":makeQuery(id+"F27.boolean.opBoolean","SPLIT",FACE,{"disambiguationData":[TD([subQ80])],"derivedFrom":makeQuery(id+"F26.boolean.opBoolean","SPLIT",FACE,{"disambiguationData":[TD([subQ80])],"derivedFrom":makeQuery(id+"F25.boolean.opBoolean","SPLIT",FACE,{"disambiguationData":[TD([subQ80])],"derivedFrom":makeQuery(id+"F24.boolean.opBoolean","SPLIT",FACE,{"disambiguationData":[TD([subQ80])],"derivedFrom":makeQuery(id+"F1.opRevolve","SWEPT_FACE",FACE,{"disambiguationData":[OSD([sQuery(id+"F0.wireOp",EDGE,"E4")])]})})})})})})})})})})})})})})]});}
            var Q12;
            {var subQ0=makeQuery(id+"F1.opRevolve","SWEPT_FACE",FACE,{"disambiguationData":[OSD([sQuery(id+"F0.wireOp",EDGE,"E1")])]});var subQ7=sQuery(id+"F4.wireOp",EDGE,"E26.5.3");var subQ8=sQuery(id+"F4.wireOp",EDGE,"E26.5.2");var subQ9=sQuery(id+"F3.wireOp",EDGE,"E20.5.3");var subQ10=sQuery(id+"F3.wireOp",EDGE,"E20.5.2");var subQ11=sQuery(id+"F3.wireOp",EDGE,"E20.5.1");var subQ12=makeQuery(id+"F16.opLoft","SWEPT_FACE",FACE,{"disambiguationData":[OSD([subQ11,subQ10,subQ9,sQuery(id+"F4.wireOp",EDGE,"E26.5.1"),subQ8,subQ7])]});var subQ13=makeQuery(id+"F40.opExtrude","CAP_FACE",FACE,{"disambiguationData":[OSD([sQuery(id+"F39.wireOp",EDGE,"E29"),sQuery(id+"F39.wireOp",EDGE,"E30")])],"isStart":false});var subQ26=sQuery(id+"F3.wireOp",EDGE,"E20.7.0");var subQ30=makeQuery(id+"F14.opLoft","CAP_FACE",FACE,{"disambiguationData":[OSD([makeQuery(id+"F3.imprint","IMPRINT",FACE,{"disambiguationData":[TD([[makeQuery(id+"F3.imprint","IMPRINT",EDGE,{"derivedFrom":subQ26}),-1.0]])]})])],"isStart":true});var subQ75=sQuery(id+"F3.wireOp",EDGE,"E18.bottom");var subQ80=makeQuery(id+"F5.opLoft","CAP_FACE",FACE,{"disambiguationData":[OSD([makeQuery(id+"F3.imprint","IMPRINT",FACE,{"disambiguationData":[TD([[makeQuery(id+"F3.imprint","IMPRINT",EDGE,{"derivedFrom":subQ75}),1.0]])]})])],"isStart":true});Q12=makeQuery(id+"F44.opFillet","BLEND_EDGE",EDGE,{"blendedFrom":[makeQuery(id+"F40.boolean.opBoolean","INTERSECT",EDGE,{"derivedFrom":[subQ12,subQ13]}),makeQuery(id+"F40.boolean.opBoolean","SPLIT",FACE,{"disambiguationData":[TD([subQ0])],"derivedFrom":makeQuery(id+"F36.boolean.opBoolean","SPLIT",FACE,{"disambiguationData":[TD([subQ12])],"derivedFrom":makeQuery(id+"F35.boolean.opBoolean","SPLIT",FACE,{"disambiguationData":[TD([subQ30])],"derivedFrom":makeQuery(id+"F34.boolean.opBoolean","SPLIT",FACE,{"disambiguationData":[TD([subQ30])],"derivedFrom":makeQuery(id+"F33.boolean.opBoolean","SPLIT",FACE,{"disambiguationData":[TD([subQ30])],"derivedFrom":makeQuery(id+"F32.boolean.opBoolean","SPLIT",FACE,{"disambiguationData":[TD([subQ30])],"derivedFrom":makeQuery(id+"F31.boolean.opBoolean","SPLIT",FACE,{"disambiguationData":[TD([subQ30])],"derivedFrom":makeQuery(id+"F30.boolean.opBoolean","SPLIT",FACE,{"disambiguationData":[TD([subQ80])],"derivedFrom":makeQuery(id+"F29.boolean.opBoolean","SPLIT",FACE,{"disambiguationData":[TD([subQ80])],"derivedFrom":makeQuery(id+"F28.boolean.opBoolean","SPLIT",FACE,{"disambiguationData":[TD([subQ80])],"derivedFrom":makeQuery(id+"F27.boolean.opBoolean","SPLIT",FACE,{"disambiguationData":[TD([subQ80])],"derivedFrom":makeQuery(id+"F26.boolean.opBoolean","SPLIT",FACE,{"disambiguationData":[TD([subQ80])],"derivedFrom":makeQuery(id+"F25.boolean.opBoolean","SPLIT",FACE,{"disambiguationData":[TD([subQ80])],"derivedFrom":makeQuery(id+"F24.boolean.opBoolean","SPLIT",FACE,{"disambiguationData":[TD([subQ80])],"derivedFrom":makeQuery(id+"F1.opRevolve","SWEPT_FACE",FACE,{"disambiguationData":[OSD([sQuery(id+"F0.wireOp",EDGE,"E4")])]})})})})})})})})})})})})})})})],"blendedInto":[makeQuery(id+"F40.boolean.opBoolean","SPLIT",FACE,{"disambiguationData":[TD([subQ0])],"derivedFrom":makeQuery(id+"F36.boolean.opBoolean","SPLIT",FACE,{"disambiguationData":[TD([subQ12])],"derivedFrom":makeQuery(id+"F35.boolean.opBoolean","SPLIT",FACE,{"disambiguationData":[TD([subQ30])],"derivedFrom":makeQuery(id+"F34.boolean.opBoolean","SPLIT",FACE,{"disambiguationData":[TD([subQ30])],"derivedFrom":makeQuery(id+"F33.boolean.opBoolean","SPLIT",FACE,{"disambiguationData":[TD([subQ30])],"derivedFrom":makeQuery(id+"F32.boolean.opBoolean","SPLIT",FACE,{"disambiguationData":[TD([subQ30])],"derivedFrom":makeQuery(id+"F31.boolean.opBoolean","SPLIT",FACE,{"disambiguationData":[TD([subQ30])],"derivedFrom":makeQuery(id+"F30.boolean.opBoolean","SPLIT",FACE,{"disambiguationData":[TD([subQ80])],"derivedFrom":makeQuery(id+"F29.boolean.opBoolean","SPLIT",FACE,{"disambiguationData":[TD([subQ80])],"derivedFrom":makeQuery(id+"F28.boolean.opBoolean","SPLIT",FACE,{"disambiguationData":[TD([subQ80])],"derivedFrom":makeQuery(id+"F27.boolean.opBoolean","SPLIT",FACE,{"disambiguationData":[TD([subQ80])],"derivedFrom":makeQuery(id+"F26.boolean.opBoolean","SPLIT",FACE,{"disambiguationData":[TD([subQ80])],"derivedFrom":makeQuery(id+"F25.boolean.opBoolean","SPLIT",FACE,{"disambiguationData":[TD([subQ80])],"derivedFrom":makeQuery(id+"F24.boolean.opBoolean","SPLIT",FACE,{"disambiguationData":[TD([subQ80])],"derivedFrom":makeQuery(id+"F1.opRevolve","SWEPT_FACE",FACE,{"disambiguationData":[OSD([sQuery(id+"F0.wireOp",EDGE,"E4")])]})})})})})})})})})})})})})})})]});}
            var Q13;
            {var subQ0=makeQuery(id+"F1.opRevolve","SWEPT_FACE",FACE,{"disambiguationData":[OSD([sQuery(id+"F0.wireOp",EDGE,"E1")])]});var subQ1=sQuery(id+"F4.wireOp",EDGE,"E26.6.3");var subQ2=sQuery(id+"F4.wireOp",EDGE,"E26.6.2");var subQ3=sQuery(id+"F3.wireOp",EDGE,"E20.6.3");var subQ4=sQuery(id+"F3.wireOp",EDGE,"E20.6.2");var subQ5=sQuery(id+"F3.wireOp",EDGE,"E20.6.1");var subQ6=makeQuery(id+"F15.opLoft","SWEPT_FACE",FACE,{"disambiguationData":[OSD([subQ5,subQ4,subQ3,sQuery(id+"F4.wireOp",EDGE,"E26.6.1"),subQ2,subQ1])]});var subQ13=makeQuery(id+"F40.opExtrude","CAP_FACE",FACE,{"disambiguationData":[OSD([sQuery(id+"F39.wireOp",EDGE,"E29"),sQuery(id+"F39.wireOp",EDGE,"E30")])],"isStart":false});var subQ19=sQuery(id+"F3.wireOp",EDGE,"E20.7.0");var subQ23=makeQuery(id+"F14.opLoft","CAP_FACE",FACE,{"disambiguationData":[OSD([makeQuery(id+"F3.imprint","IMPRINT",FACE,{"disambiguationData":[TD([[makeQuery(id+"F3.imprint","IMPRINT",EDGE,{"derivedFrom":subQ19}),-1.0]])]})])],"isStart":true});var subQ75=sQuery(id+"F3.wireOp",EDGE,"E18.bottom");var subQ80=makeQuery(id+"F5.opLoft","CAP_FACE",FACE,{"disambiguationData":[OSD([makeQuery(id+"F3.imprint","IMPRINT",FACE,{"disambiguationData":[TD([[makeQuery(id+"F3.imprint","IMPRINT",EDGE,{"derivedFrom":subQ75}),1.0]])]})])],"isStart":true});Q13=makeQuery(id+"F44.opFillet","BLEND_EDGE",EDGE,{"blendedFrom":[makeQuery(id+"F40.boolean.opBoolean","INTERSECT",EDGE,{"derivedFrom":[subQ6,subQ13]}),makeQuery(id+"F40.boolean.opBoolean","SPLIT",FACE,{"disambiguationData":[TD([subQ0])],"derivedFrom":makeQuery(id+"F37.boolean.opBoolean","SPLIT",FACE,{"disambiguationData":[TD([subQ6])],"derivedFrom":makeQuery(id+"F36.boolean.opBoolean","SPLIT",FACE,{"disambiguationData":[TD([subQ23])],"derivedFrom":makeQuery(id+"F35.boolean.opBoolean","SPLIT",FACE,{"disambiguationData":[TD([subQ23])],"derivedFrom":makeQuery(id+"F34.boolean.opBoolean","SPLIT",FACE,{"disambiguationData":[TD([subQ23])],"derivedFrom":makeQuery(id+"F33.boolean.opBoolean","SPLIT",FACE,{"disambiguationData":[TD([subQ23])],"derivedFrom":makeQuery(id+"F32.boolean.opBoolean","SPLIT",FACE,{"disambiguationData":[TD([subQ23])],"derivedFrom":makeQuery(id+"F31.boolean.opBoolean","SPLIT",FACE,{"disambiguationData":[TD([subQ23])],"derivedFrom":makeQuery(id+"F30.boolean.opBoolean","SPLIT",FACE,{"disambiguationData":[TD([subQ80])],"derivedFrom":makeQuery(id+"F29.boolean.opBoolean","SPLIT",FACE,{"disambiguationData":[TD([subQ80])],"derivedFrom":makeQuery(id+"F28.boolean.opBoolean","SPLIT",FACE,{"disambiguationData":[TD([subQ80])],"derivedFrom":makeQuery(id+"F27.boolean.opBoolean","SPLIT",FACE,{"disambiguationData":[TD([subQ80])],"derivedFrom":makeQuery(id+"F26.boolean.opBoolean","SPLIT",FACE,{"disambiguationData":[TD([subQ80])],"derivedFrom":makeQuery(id+"F25.boolean.opBoolean","SPLIT",FACE,{"disambiguationData":[TD([subQ80])],"derivedFrom":makeQuery(id+"F24.boolean.opBoolean","SPLIT",FACE,{"disambiguationData":[TD([subQ80])],"derivedFrom":makeQuery(id+"F1.opRevolve","SWEPT_FACE",FACE,{"disambiguationData":[OSD([sQuery(id+"F0.wireOp",EDGE,"E4")])]})})})})})})})})})})})})})})})})],"blendedInto":[makeQuery(id+"F40.boolean.opBoolean","SPLIT",FACE,{"disambiguationData":[TD([subQ0])],"derivedFrom":makeQuery(id+"F37.boolean.opBoolean","SPLIT",FACE,{"disambiguationData":[TD([subQ6])],"derivedFrom":makeQuery(id+"F36.boolean.opBoolean","SPLIT",FACE,{"disambiguationData":[TD([subQ23])],"derivedFrom":makeQuery(id+"F35.boolean.opBoolean","SPLIT",FACE,{"disambiguationData":[TD([subQ23])],"derivedFrom":makeQuery(id+"F34.boolean.opBoolean","SPLIT",FACE,{"disambiguationData":[TD([subQ23])],"derivedFrom":makeQuery(id+"F33.boolean.opBoolean","SPLIT",FACE,{"disambiguationData":[TD([subQ23])],"derivedFrom":makeQuery(id+"F32.boolean.opBoolean","SPLIT",FACE,{"disambiguationData":[TD([subQ23])],"derivedFrom":makeQuery(id+"F31.boolean.opBoolean","SPLIT",FACE,{"disambiguationData":[TD([subQ23])],"derivedFrom":makeQuery(id+"F30.boolean.opBoolean","SPLIT",FACE,{"disambiguationData":[TD([subQ80])],"derivedFrom":makeQuery(id+"F29.boolean.opBoolean","SPLIT",FACE,{"disambiguationData":[TD([subQ80])],"derivedFrom":makeQuery(id+"F28.boolean.opBoolean","SPLIT",FACE,{"disambiguationData":[TD([subQ80])],"derivedFrom":makeQuery(id+"F27.boolean.opBoolean","SPLIT",FACE,{"disambiguationData":[TD([subQ80])],"derivedFrom":makeQuery(id+"F26.boolean.opBoolean","SPLIT",FACE,{"disambiguationData":[TD([subQ80])],"derivedFrom":makeQuery(id+"F25.boolean.opBoolean","SPLIT",FACE,{"disambiguationData":[TD([subQ80])],"derivedFrom":makeQuery(id+"F24.boolean.opBoolean","SPLIT",FACE,{"disambiguationData":[TD([subQ80])],"derivedFrom":makeQuery(id+"F1.opRevolve","SWEPT_FACE",FACE,{"disambiguationData":[OSD([sQuery(id+"F0.wireOp",EDGE,"E4")])]})})})})})})})})})})})})})})})})]});}
            var Q14;
            {var subQ0=makeQuery(id+"F1.opRevolve","SWEPT_FACE",FACE,{"disambiguationData":[OSD([sQuery(id+"F0.wireOp",EDGE,"E1")])]});var subQ7=sQuery(id+"F4.wireOp",EDGE,"E26.5.3");var subQ8=sQuery(id+"F4.wireOp",EDGE,"E26.5.2");var subQ9=sQuery(id+"F3.wireOp",EDGE,"E20.5.3");var subQ10=sQuery(id+"F3.wireOp",EDGE,"E20.5.2");var subQ11=sQuery(id+"F3.wireOp",EDGE,"E20.5.1");var subQ12=makeQuery(id+"F16.opLoft","SWEPT_FACE",FACE,{"disambiguationData":[OSD([subQ11,subQ10,subQ9,sQuery(id+"F4.wireOp",EDGE,"E26.5.1"),subQ8,subQ7])]});var subQ13=makeQuery(id+"F40.opExtrude","CAP_FACE",FACE,{"disambiguationData":[OSD([sQuery(id+"F39.wireOp",EDGE,"E29"),sQuery(id+"F39.wireOp",EDGE,"E30")])],"isStart":false});var subQ26=sQuery(id+"F3.wireOp",EDGE,"E20.7.0");var subQ30=makeQuery(id+"F14.opLoft","CAP_FACE",FACE,{"disambiguationData":[OSD([makeQuery(id+"F3.imprint","IMPRINT",FACE,{"disambiguationData":[TD([[makeQuery(id+"F3.imprint","IMPRINT",EDGE,{"derivedFrom":subQ26}),-1.0]])]})])],"isStart":true});var subQ75=sQuery(id+"F3.wireOp",EDGE,"E18.bottom");var subQ80=makeQuery(id+"F5.opLoft","CAP_FACE",FACE,{"disambiguationData":[OSD([makeQuery(id+"F3.imprint","IMPRINT",FACE,{"disambiguationData":[TD([[makeQuery(id+"F3.imprint","IMPRINT",EDGE,{"derivedFrom":subQ75}),1.0]])]})])],"isStart":true});Q14=makeQuery(id+"F44.opFillet","BLEND_EDGE",EDGE,{"blendedFrom":[makeQuery(id+"F40.boolean.opBoolean","INTERSECT",EDGE,{"derivedFrom":[subQ12,subQ13]}),makeQuery(id+"F40.boolean.opBoolean","SPLIT",FACE,{"disambiguationData":[TD([subQ0])],"derivedFrom":makeQuery(id+"F36.boolean.opBoolean","SPLIT",FACE,{"disambiguationData":[TD([subQ12])],"derivedFrom":makeQuery(id+"F35.boolean.opBoolean","SPLIT",FACE,{"disambiguationData":[TD([subQ30])],"derivedFrom":makeQuery(id+"F34.boolean.opBoolean","SPLIT",FACE,{"disambiguationData":[TD([subQ30])],"derivedFrom":makeQuery(id+"F33.boolean.opBoolean","SPLIT",FACE,{"disambiguationData":[TD([subQ30])],"derivedFrom":makeQuery(id+"F32.boolean.opBoolean","SPLIT",FACE,{"disambiguationData":[TD([subQ30])],"derivedFrom":makeQuery(id+"F31.boolean.opBoolean","SPLIT",FACE,{"disambiguationData":[TD([subQ30])],"derivedFrom":makeQuery(id+"F30.boolean.opBoolean","SPLIT",FACE,{"disambiguationData":[TD([subQ80])],"derivedFrom":makeQuery(id+"F29.boolean.opBoolean","SPLIT",FACE,{"disambiguationData":[TD([subQ80])],"derivedFrom":makeQuery(id+"F28.boolean.opBoolean","SPLIT",FACE,{"disambiguationData":[TD([subQ80])],"derivedFrom":makeQuery(id+"F27.boolean.opBoolean","SPLIT",FACE,{"disambiguationData":[TD([subQ80])],"derivedFrom":makeQuery(id+"F26.boolean.opBoolean","SPLIT",FACE,{"disambiguationData":[TD([subQ80])],"derivedFrom":makeQuery(id+"F25.boolean.opBoolean","SPLIT",FACE,{"disambiguationData":[TD([subQ80])],"derivedFrom":makeQuery(id+"F24.boolean.opBoolean","SPLIT",FACE,{"disambiguationData":[TD([subQ80])],"derivedFrom":makeQuery(id+"F1.opRevolve","SWEPT_FACE",FACE,{"disambiguationData":[OSD([sQuery(id+"F0.wireOp",EDGE,"E4")])]})})})})})})})})})})})})})})})],"blendedInto":[makeQuery(id+"F40.boolean.opBoolean","SPLIT",FACE,{"disambiguationData":[TD([subQ0])],"derivedFrom":makeQuery(id+"F36.boolean.opBoolean","SPLIT",FACE,{"disambiguationData":[TD([subQ12])],"derivedFrom":makeQuery(id+"F35.boolean.opBoolean","SPLIT",FACE,{"disambiguationData":[TD([subQ30])],"derivedFrom":makeQuery(id+"F34.boolean.opBoolean","SPLIT",FACE,{"disambiguationData":[TD([subQ30])],"derivedFrom":makeQuery(id+"F33.boolean.opBoolean","SPLIT",FACE,{"disambiguationData":[TD([subQ30])],"derivedFrom":makeQuery(id+"F32.boolean.opBoolean","SPLIT",FACE,{"disambiguationData":[TD([subQ30])],"derivedFrom":makeQuery(id+"F31.boolean.opBoolean","SPLIT",FACE,{"disambiguationData":[TD([subQ30])],"derivedFrom":makeQuery(id+"F30.boolean.opBoolean","SPLIT",FACE,{"disambiguationData":[TD([subQ80])],"derivedFrom":makeQuery(id+"F29.boolean.opBoolean","SPLIT",FACE,{"disambiguationData":[TD([subQ80])],"derivedFrom":makeQuery(id+"F28.boolean.opBoolean","SPLIT",FACE,{"disambiguationData":[TD([subQ80])],"derivedFrom":makeQuery(id+"F27.boolean.opBoolean","SPLIT",FACE,{"disambiguationData":[TD([subQ80])],"derivedFrom":makeQuery(id+"F26.boolean.opBoolean","SPLIT",FACE,{"disambiguationData":[TD([subQ80])],"derivedFrom":makeQuery(id+"F25.boolean.opBoolean","SPLIT",FACE,{"disambiguationData":[TD([subQ80])],"derivedFrom":makeQuery(id+"F24.boolean.opBoolean","SPLIT",FACE,{"disambiguationData":[TD([subQ80])],"derivedFrom":makeQuery(id+"F1.opRevolve","SWEPT_FACE",FACE,{"disambiguationData":[OSD([sQuery(id+"F0.wireOp",EDGE,"E4")])]})})})})})})})})})})})})})})})]});}
            var Q15;
            {var subQ0=makeQuery(id+"F1.opRevolve","SWEPT_FACE",FACE,{"disambiguationData":[OSD([sQuery(id+"F0.wireOp",EDGE,"E1")])]});var subQ1=sQuery(id+"F4.wireOp",EDGE,"E26.7.3");var subQ2=sQuery(id+"F4.wireOp",EDGE,"E26.7.2");var subQ3=sQuery(id+"F3.wireOp",EDGE,"E20.7.3");var subQ4=sQuery(id+"F3.wireOp",EDGE,"E20.7.2");var subQ5=sQuery(id+"F3.wireOp",EDGE,"E20.7.1");var subQ6=makeQuery(id+"F14.opLoft","SWEPT_FACE",FACE,{"disambiguationData":[OSD([subQ5,subQ4,subQ3,sQuery(id+"F4.wireOp",EDGE,"E26.7.1"),subQ2,subQ1])]});var subQ13=makeQuery(id+"F40.opExtrude","CAP_FACE",FACE,{"disambiguationData":[OSD([sQuery(id+"F39.wireOp",EDGE,"E29"),sQuery(id+"F39.wireOp",EDGE,"E30")])],"isStart":false});var subQ20=sQuery(id+"F3.wireOp",EDGE,"E20.7.0");var subQ22=makeQuery(id+"F14.opLoft","CAP_FACE",FACE,{"disambiguationData":[OSD([makeQuery(id+"F3.imprint","IMPRINT",FACE,{"disambiguationData":[TD([[makeQuery(id+"F3.imprint","IMPRINT",EDGE,{"derivedFrom":subQ20}),-1.0]])]})])],"isStart":true});var subQ75=sQuery(id+"F3.wireOp",EDGE,"E18.bottom");var subQ80=makeQuery(id+"F5.opLoft","CAP_FACE",FACE,{"disambiguationData":[OSD([makeQuery(id+"F3.imprint","IMPRINT",FACE,{"disambiguationData":[TD([[makeQuery(id+"F3.imprint","IMPRINT",EDGE,{"derivedFrom":subQ75}),1.0]])]})])],"isStart":true});Q15=makeQuery(id+"F44.opFillet","BLEND_EDGE",EDGE,{"blendedFrom":[makeQuery(id+"F40.boolean.opBoolean","INTERSECT",EDGE,{"derivedFrom":[subQ6,subQ13]}),makeQuery(id+"F40.boolean.opBoolean","SPLIT",FACE,{"disambiguationData":[TD([subQ0])],"derivedFrom":makeQuery(id+"F38.boolean.opBoolean","SPLIT",FACE,{"disambiguationData":[TD([subQ6])],"derivedFrom":makeQuery(id+"F37.boolean.opBoolean","SPLIT",FACE,{"disambiguationData":[TD([subQ22])],"derivedFrom":makeQuery(id+"F36.boolean.opBoolean","SPLIT",FACE,{"disambiguationData":[TD([subQ22])],"derivedFrom":makeQuery(id+"F35.boolean.opBoolean","SPLIT",FACE,{"disambiguationData":[TD([subQ22])],"derivedFrom":makeQuery(id+"F34.boolean.opBoolean","SPLIT",FACE,{"disambiguationData":[TD([subQ22])],"derivedFrom":makeQuery(id+"F33.boolean.opBoolean","SPLIT",FACE,{"disambiguationData":[TD([subQ22])],"derivedFrom":makeQuery(id+"F32.boolean.opBoolean","SPLIT",FACE,{"disambiguationData":[TD([subQ22])],"derivedFrom":makeQuery(id+"F31.boolean.opBoolean","SPLIT",FACE,{"disambiguationData":[TD([subQ22])],"derivedFrom":makeQuery(id+"F30.boolean.opBoolean","SPLIT",FACE,{"disambiguationData":[TD([subQ80])],"derivedFrom":makeQuery(id+"F29.boolean.opBoolean","SPLIT",FACE,{"disambiguationData":[TD([subQ80])],"derivedFrom":makeQuery(id+"F28.boolean.opBoolean","SPLIT",FACE,{"disambiguationData":[TD([subQ80])],"derivedFrom":makeQuery(id+"F27.boolean.opBoolean","SPLIT",FACE,{"disambiguationData":[TD([subQ80])],"derivedFrom":makeQuery(id+"F26.boolean.opBoolean","SPLIT",FACE,{"disambiguationData":[TD([subQ80])],"derivedFrom":makeQuery(id+"F25.boolean.opBoolean","SPLIT",FACE,{"disambiguationData":[TD([subQ80])],"derivedFrom":makeQuery(id+"F24.boolean.opBoolean","SPLIT",FACE,{"disambiguationData":[TD([subQ80])],"derivedFrom":makeQuery(id+"F1.opRevolve","SWEPT_FACE",FACE,{"disambiguationData":[OSD([sQuery(id+"F0.wireOp",EDGE,"E4")])]})})})})})})})})})})})})})})})})})],"blendedInto":[makeQuery(id+"F40.boolean.opBoolean","SPLIT",FACE,{"disambiguationData":[TD([subQ0])],"derivedFrom":makeQuery(id+"F38.boolean.opBoolean","SPLIT",FACE,{"disambiguationData":[TD([subQ6])],"derivedFrom":makeQuery(id+"F37.boolean.opBoolean","SPLIT",FACE,{"disambiguationData":[TD([subQ22])],"derivedFrom":makeQuery(id+"F36.boolean.opBoolean","SPLIT",FACE,{"disambiguationData":[TD([subQ22])],"derivedFrom":makeQuery(id+"F35.boolean.opBoolean","SPLIT",FACE,{"disambiguationData":[TD([subQ22])],"derivedFrom":makeQuery(id+"F34.boolean.opBoolean","SPLIT",FACE,{"disambiguationData":[TD([subQ22])],"derivedFrom":makeQuery(id+"F33.boolean.opBoolean","SPLIT",FACE,{"disambiguationData":[TD([subQ22])],"derivedFrom":makeQuery(id+"F32.boolean.opBoolean","SPLIT",FACE,{"disambiguationData":[TD([subQ22])],"derivedFrom":makeQuery(id+"F31.boolean.opBoolean","SPLIT",FACE,{"disambiguationData":[TD([subQ22])],"derivedFrom":makeQuery(id+"F30.boolean.opBoolean","SPLIT",FACE,{"disambiguationData":[TD([subQ80])],"derivedFrom":makeQuery(id+"F29.boolean.opBoolean","SPLIT",FACE,{"disambiguationData":[TD([subQ80])],"derivedFrom":makeQuery(id+"F28.boolean.opBoolean","SPLIT",FACE,{"disambiguationData":[TD([subQ80])],"derivedFrom":makeQuery(id+"F27.boolean.opBoolean","SPLIT",FACE,{"disambiguationData":[TD([subQ80])],"derivedFrom":makeQuery(id+"F26.boolean.opBoolean","SPLIT",FACE,{"disambiguationData":[TD([subQ80])],"derivedFrom":makeQuery(id+"F25.boolean.opBoolean","SPLIT",FACE,{"disambiguationData":[TD([subQ80])],"derivedFrom":makeQuery(id+"F24.boolean.opBoolean","SPLIT",FACE,{"disambiguationData":[TD([subQ80])],"derivedFrom":makeQuery(id+"F1.opRevolve","SWEPT_FACE",FACE,{"disambiguationData":[OSD([sQuery(id+"F0.wireOp",EDGE,"E4")])]})})})})})})})})})})})})})})})})})]});}
            var Q16;
            {var subQ0=makeQuery(id+"F1.opRevolve","SWEPT_FACE",FACE,{"disambiguationData":[OSD([sQuery(id+"F0.wireOp",EDGE,"E1")])]});var subQ1=sQuery(id+"F3.wireOp",EDGE,"E20.8.3");var subQ2=sQuery(id+"F3.wireOp",EDGE,"E20.8.2");var subQ3=sQuery(id+"F3.wireOp",EDGE,"E20.8.1");var subQ4=makeQuery(id+"F13.opLoft","SWEPT_FACE",FACE,{"disambiguationData":[OSD([subQ3,subQ2,subQ1,sQuery(id+"F4.wireOp",EDGE,"E26.8.1"),sQuery(id+"F4.wireOp",EDGE,"E26.8.2"),sQuery(id+"F4.wireOp",EDGE,"E26.8.3")])]});var subQ5=makeQuery(id+"F40.opExtrude","CAP_FACE",FACE,{"disambiguationData":[OSD([sQuery(id+"F39.wireOp",EDGE,"E29"),sQuery(id+"F39.wireOp",EDGE,"E30")])],"isStart":false});var subQ10=sQuery(id+"F3.wireOp",EDGE,"E20.7.0");var subQ16=makeQuery(id+"F14.opLoft","CAP_FACE",FACE,{"disambiguationData":[OSD([makeQuery(id+"F3.imprint","IMPRINT",FACE,{"disambiguationData":[TD([[makeQuery(id+"F3.imprint","IMPRINT",EDGE,{"derivedFrom":subQ10}),-1.0]])]})])],"isStart":true});var subQ74=sQuery(id+"F3.wireOp",EDGE,"E18.bottom");var subQ79=makeQuery(id+"F5.opLoft","CAP_FACE",FACE,{"disambiguationData":[OSD([makeQuery(id+"F3.imprint","IMPRINT",FACE,{"disambiguationData":[TD([[makeQuery(id+"F3.imprint","IMPRINT",EDGE,{"derivedFrom":subQ74}),1.0]])]})])],"isStart":true});Q16=makeQuery(id+"F44.opFillet","BLEND_EDGE",EDGE,{"blendedFrom":[makeQuery(id+"F40.boolean.opBoolean","INTERSECT",EDGE,{"derivedFrom":[subQ4,subQ5]}),makeQuery(id+"F40.boolean.opBoolean","SPLIT",FACE,{"disambiguationData":[TD([subQ0])],"derivedFrom":makeQuery(id+"F38.boolean.opBoolean","SPLIT",FACE,{"disambiguationData":[TD([subQ4])],"derivedFrom":makeQuery(id+"F37.boolean.opBoolean","SPLIT",FACE,{"disambiguationData":[TD([subQ16])],"derivedFrom":makeQuery(id+"F36.boolean.opBoolean","SPLIT",FACE,{"disambiguationData":[TD([subQ16])],"derivedFrom":makeQuery(id+"F35.boolean.opBoolean","SPLIT",FACE,{"disambiguationData":[TD([subQ16])],"derivedFrom":makeQuery(id+"F34.boolean.opBoolean","SPLIT",FACE,{"disambiguationData":[TD([subQ16])],"derivedFrom":makeQuery(id+"F33.boolean.opBoolean","SPLIT",FACE,{"disambiguationData":[TD([subQ16])],"derivedFrom":makeQuery(id+"F32.boolean.opBoolean","SPLIT",FACE,{"disambiguationData":[TD([subQ16])],"derivedFrom":makeQuery(id+"F31.boolean.opBoolean","SPLIT",FACE,{"disambiguationData":[TD([subQ16])],"derivedFrom":makeQuery(id+"F30.boolean.opBoolean","SPLIT",FACE,{"disambiguationData":[TD([subQ79])],"derivedFrom":makeQuery(id+"F29.boolean.opBoolean","SPLIT",FACE,{"disambiguationData":[TD([subQ79])],"derivedFrom":makeQuery(id+"F28.boolean.opBoolean","SPLIT",FACE,{"disambiguationData":[TD([subQ79])],"derivedFrom":makeQuery(id+"F27.boolean.opBoolean","SPLIT",FACE,{"disambiguationData":[TD([subQ79])],"derivedFrom":makeQuery(id+"F26.boolean.opBoolean","SPLIT",FACE,{"disambiguationData":[TD([subQ79])],"derivedFrom":makeQuery(id+"F25.boolean.opBoolean","SPLIT",FACE,{"disambiguationData":[TD([subQ79])],"derivedFrom":makeQuery(id+"F24.boolean.opBoolean","SPLIT",FACE,{"disambiguationData":[TD([subQ79])],"derivedFrom":makeQuery(id+"F1.opRevolve","SWEPT_FACE",FACE,{"disambiguationData":[OSD([sQuery(id+"F0.wireOp",EDGE,"E4")])]})})})})})})})})})})})})})})})})})],"blendedInto":[makeQuery(id+"F40.boolean.opBoolean","SPLIT",FACE,{"disambiguationData":[TD([subQ0])],"derivedFrom":makeQuery(id+"F38.boolean.opBoolean","SPLIT",FACE,{"disambiguationData":[TD([subQ4])],"derivedFrom":makeQuery(id+"F37.boolean.opBoolean","SPLIT",FACE,{"disambiguationData":[TD([subQ16])],"derivedFrom":makeQuery(id+"F36.boolean.opBoolean","SPLIT",FACE,{"disambiguationData":[TD([subQ16])],"derivedFrom":makeQuery(id+"F35.boolean.opBoolean","SPLIT",FACE,{"disambiguationData":[TD([subQ16])],"derivedFrom":makeQuery(id+"F34.boolean.opBoolean","SPLIT",FACE,{"disambiguationData":[TD([subQ16])],"derivedFrom":makeQuery(id+"F33.boolean.opBoolean","SPLIT",FACE,{"disambiguationData":[TD([subQ16])],"derivedFrom":makeQuery(id+"F32.boolean.opBoolean","SPLIT",FACE,{"disambiguationData":[TD([subQ16])],"derivedFrom":makeQuery(id+"F31.boolean.opBoolean","SPLIT",FACE,{"disambiguationData":[TD([subQ16])],"derivedFrom":makeQuery(id+"F30.boolean.opBoolean","SPLIT",FACE,{"disambiguationData":[TD([subQ79])],"derivedFrom":makeQuery(id+"F29.boolean.opBoolean","SPLIT",FACE,{"disambiguationData":[TD([subQ79])],"derivedFrom":makeQuery(id+"F28.boolean.opBoolean","SPLIT",FACE,{"disambiguationData":[TD([subQ79])],"derivedFrom":makeQuery(id+"F27.boolean.opBoolean","SPLIT",FACE,{"disambiguationData":[TD([subQ79])],"derivedFrom":makeQuery(id+"F26.boolean.opBoolean","SPLIT",FACE,{"disambiguationData":[TD([subQ79])],"derivedFrom":makeQuery(id+"F25.boolean.opBoolean","SPLIT",FACE,{"disambiguationData":[TD([subQ79])],"derivedFrom":makeQuery(id+"F24.boolean.opBoolean","SPLIT",FACE,{"disambiguationData":[TD([subQ79])],"derivedFrom":makeQuery(id+"F1.opRevolve","SWEPT_FACE",FACE,{"disambiguationData":[OSD([sQuery(id+"F0.wireOp",EDGE,"E4")])]})})})})})})})})})})})})})})})})})]});}
            var Q17;
            {var subQ0=makeQuery(id+"F1.opRevolve","SWEPT_FACE",FACE,{"disambiguationData":[OSD([sQuery(id+"F0.wireOp",EDGE,"E3")])]});var subQ1=sQuery(id+"F3.wireOp",EDGE,"E20.8.3");var subQ2=sQuery(id+"F3.wireOp",EDGE,"E20.8.2");var subQ3=sQuery(id+"F3.wireOp",EDGE,"E20.8.1");var subQ4=makeQuery(id+"F23.opLoft","SWEPT_FACE",FACE,{"disambiguationData":[OSD([subQ3,subQ2,subQ1,sQuery(id+"F22.wireOp",EDGE,"E27.bottom"),sQuery(id+"F22.wireOp",EDGE,"E27.top"),sQuery(id+"F22.wireOp",EDGE,"E27.left")])]});var subQ7=sQuery(id+"F3.wireOp",EDGE,"E20.7.0");var subQ9=makeQuery(id+"F40.opExtrude","CAP_FACE",FACE,{"disambiguationData":[OSD([sQuery(id+"F39.wireOp",EDGE,"E29"),sQuery(id+"F39.wireOp",EDGE,"E30")])],"isStart":true});var subQ10=makeQuery(id+"F13.opLoft","SWEPT_FACE",FACE,{"disambiguationData":[OSD([subQ3,subQ2,subQ1,sQuery(id+"F4.wireOp",EDGE,"E26.8.1"),sQuery(id+"F4.wireOp",EDGE,"E26.8.2"),sQuery(id+"F4.wireOp",EDGE,"E26.8.3")])]});var subQ17=makeQuery(id+"F14.opLoft","CAP_FACE",FACE,{"disambiguationData":[OSD([makeQuery(id+"F3.imprint","IMPRINT",FACE,{"disambiguationData":[TD([[makeQuery(id+"F3.imprint","IMPRINT",EDGE,{"derivedFrom":subQ7}),-1.0]])]})])],"isStart":true});var subQ75=sQuery(id+"F3.wireOp",EDGE,"E18.bottom");var subQ80=makeQuery(id+"F5.opLoft","CAP_FACE",FACE,{"disambiguationData":[OSD([makeQuery(id+"F3.imprint","IMPRINT",FACE,{"disambiguationData":[TD([[makeQuery(id+"F3.imprint","IMPRINT",EDGE,{"derivedFrom":subQ75}),1.0]])]})])],"isStart":true});Q17=makeQuery(id+"F44.opFillet","BLEND_EDGE",EDGE,{"blendedFrom":[makeQuery(id+"F40.boolean.opBoolean","INTERSECT",EDGE,{"derivedFrom":[subQ4,subQ9]}),makeQuery(id+"F40.boolean.opBoolean","SPLIT",FACE,{"disambiguationData":[TD([subQ0])],"derivedFrom":makeQuery(id+"F38.boolean.opBoolean","SPLIT",FACE,{"disambiguationData":[TD([subQ10])],"derivedFrom":makeQuery(id+"F37.boolean.opBoolean","SPLIT",FACE,{"disambiguationData":[TD([subQ17])],"derivedFrom":makeQuery(id+"F36.boolean.opBoolean","SPLIT",FACE,{"disambiguationData":[TD([subQ17])],"derivedFrom":makeQuery(id+"F35.boolean.opBoolean","SPLIT",FACE,{"disambiguationData":[TD([subQ17])],"derivedFrom":makeQuery(id+"F34.boolean.opBoolean","SPLIT",FACE,{"disambiguationData":[TD([subQ17])],"derivedFrom":makeQuery(id+"F33.boolean.opBoolean","SPLIT",FACE,{"disambiguationData":[TD([subQ17])],"derivedFrom":makeQuery(id+"F32.boolean.opBoolean","SPLIT",FACE,{"disambiguationData":[TD([subQ17])],"derivedFrom":makeQuery(id+"F31.boolean.opBoolean","SPLIT",FACE,{"disambiguationData":[TD([subQ17])],"derivedFrom":makeQuery(id+"F30.boolean.opBoolean","SPLIT",FACE,{"disambiguationData":[TD([subQ80])],"derivedFrom":makeQuery(id+"F29.boolean.opBoolean","SPLIT",FACE,{"disambiguationData":[TD([subQ80])],"derivedFrom":makeQuery(id+"F28.boolean.opBoolean","SPLIT",FACE,{"disambiguationData":[TD([subQ80])],"derivedFrom":makeQuery(id+"F27.boolean.opBoolean","SPLIT",FACE,{"disambiguationData":[TD([subQ80])],"derivedFrom":makeQuery(id+"F26.boolean.opBoolean","SPLIT",FACE,{"disambiguationData":[TD([subQ80])],"derivedFrom":makeQuery(id+"F25.boolean.opBoolean","SPLIT",FACE,{"disambiguationData":[TD([subQ80])],"derivedFrom":makeQuery(id+"F24.boolean.opBoolean","SPLIT",FACE,{"disambiguationData":[TD([subQ80])],"derivedFrom":makeQuery(id+"F1.opRevolve","SWEPT_FACE",FACE,{"disambiguationData":[OSD([sQuery(id+"F0.wireOp",EDGE,"E4")])]})})})})})})})})})})})})})})})})})],"blendedInto":[makeQuery(id+"F40.boolean.opBoolean","SPLIT",FACE,{"disambiguationData":[TD([subQ0])],"derivedFrom":makeQuery(id+"F38.boolean.opBoolean","SPLIT",FACE,{"disambiguationData":[TD([subQ10])],"derivedFrom":makeQuery(id+"F37.boolean.opBoolean","SPLIT",FACE,{"disambiguationData":[TD([subQ17])],"derivedFrom":makeQuery(id+"F36.boolean.opBoolean","SPLIT",FACE,{"disambiguationData":[TD([subQ17])],"derivedFrom":makeQuery(id+"F35.boolean.opBoolean","SPLIT",FACE,{"disambiguationData":[TD([subQ17])],"derivedFrom":makeQuery(id+"F34.boolean.opBoolean","SPLIT",FACE,{"disambiguationData":[TD([subQ17])],"derivedFrom":makeQuery(id+"F33.boolean.opBoolean","SPLIT",FACE,{"disambiguationData":[TD([subQ17])],"derivedFrom":makeQuery(id+"F32.boolean.opBoolean","SPLIT",FACE,{"disambiguationData":[TD([subQ17])],"derivedFrom":makeQuery(id+"F31.boolean.opBoolean","SPLIT",FACE,{"disambiguationData":[TD([subQ17])],"derivedFrom":makeQuery(id+"F30.boolean.opBoolean","SPLIT",FACE,{"disambiguationData":[TD([subQ80])],"derivedFrom":makeQuery(id+"F29.boolean.opBoolean","SPLIT",FACE,{"disambiguationData":[TD([subQ80])],"derivedFrom":makeQuery(id+"F28.boolean.opBoolean","SPLIT",FACE,{"disambiguationData":[TD([subQ80])],"derivedFrom":makeQuery(id+"F27.boolean.opBoolean","SPLIT",FACE,{"disambiguationData":[TD([subQ80])],"derivedFrom":makeQuery(id+"F26.boolean.opBoolean","SPLIT",FACE,{"disambiguationData":[TD([subQ80])],"derivedFrom":makeQuery(id+"F25.boolean.opBoolean","SPLIT",FACE,{"disambiguationData":[TD([subQ80])],"derivedFrom":makeQuery(id+"F24.boolean.opBoolean","SPLIT",FACE,{"disambiguationData":[TD([subQ80])],"derivedFrom":makeQuery(id+"F1.opRevolve","SWEPT_FACE",FACE,{"disambiguationData":[OSD([sQuery(id+"F0.wireOp",EDGE,"E4")])]})})})})})})})})})})})})})})})})})]});}
            var Q18;
            {var subQ0=makeQuery(id+"F1.opRevolve","SWEPT_FACE",FACE,{"disambiguationData":[OSD([sQuery(id+"F0.wireOp",EDGE,"E3")])]});var subQ5=sQuery(id+"F3.wireOp",EDGE,"E20.7.3");var subQ6=sQuery(id+"F3.wireOp",EDGE,"E20.7.2");var subQ7=sQuery(id+"F3.wireOp",EDGE,"E20.7.1");var subQ8=makeQuery(id+"F38.opLoft","SWEPT_FACE",FACE,{"disambiguationData":[OSD([subQ7,subQ6,subQ5,sQuery(id+"F22.wireOp",EDGE,"E28.15.0"),sQuery(id+"F22.wireOp",EDGE,"E28.15.2"),sQuery(id+"F22.wireOp",EDGE,"E28.15.3")])]});var subQ9=makeQuery(id+"F40.opExtrude","CAP_FACE",FACE,{"disambiguationData":[OSD([sQuery(id+"F39.wireOp",EDGE,"E29"),sQuery(id+"F39.wireOp",EDGE,"E30")])],"isStart":true});var subQ13=sQuery(id+"F4.wireOp",EDGE,"E26.7.3");var subQ14=sQuery(id+"F4.wireOp",EDGE,"E26.7.2");var subQ15=makeQuery(id+"F14.opLoft","SWEPT_FACE",FACE,{"disambiguationData":[OSD([subQ7,subQ6,subQ5,sQuery(id+"F4.wireOp",EDGE,"E26.7.1"),subQ14,subQ13])]});var subQ21=sQuery(id+"F3.wireOp",EDGE,"E20.7.0");var subQ23=makeQuery(id+"F14.opLoft","CAP_FACE",FACE,{"disambiguationData":[OSD([makeQuery(id+"F3.imprint","IMPRINT",FACE,{"disambiguationData":[TD([[makeQuery(id+"F3.imprint","IMPRINT",EDGE,{"derivedFrom":subQ21}),-1.0]])]})])],"isStart":true});var subQ76=sQuery(id+"F3.wireOp",EDGE,"E18.bottom");var subQ81=makeQuery(id+"F5.opLoft","CAP_FACE",FACE,{"disambiguationData":[OSD([makeQuery(id+"F3.imprint","IMPRINT",FACE,{"disambiguationData":[TD([[makeQuery(id+"F3.imprint","IMPRINT",EDGE,{"derivedFrom":subQ76}),1.0]])]})])],"isStart":true});Q18=makeQuery(id+"F44.opFillet","BLEND_EDGE",EDGE,{"blendedFrom":[makeQuery(id+"F40.boolean.opBoolean","INTERSECT",EDGE,{"derivedFrom":[subQ8,subQ9]}),makeQuery(id+"F40.boolean.opBoolean","SPLIT",FACE,{"disambiguationData":[TD([subQ0])],"derivedFrom":makeQuery(id+"F38.boolean.opBoolean","SPLIT",FACE,{"disambiguationData":[TD([subQ15])],"derivedFrom":makeQuery(id+"F37.boolean.opBoolean","SPLIT",FACE,{"disambiguationData":[TD([subQ23])],"derivedFrom":makeQuery(id+"F36.boolean.opBoolean","SPLIT",FACE,{"disambiguationData":[TD([subQ23])],"derivedFrom":makeQuery(id+"F35.boolean.opBoolean","SPLIT",FACE,{"disambiguationData":[TD([subQ23])],"derivedFrom":makeQuery(id+"F34.boolean.opBoolean","SPLIT",FACE,{"disambiguationData":[TD([subQ23])],"derivedFrom":makeQuery(id+"F33.boolean.opBoolean","SPLIT",FACE,{"disambiguationData":[TD([subQ23])],"derivedFrom":makeQuery(id+"F32.boolean.opBoolean","SPLIT",FACE,{"disambiguationData":[TD([subQ23])],"derivedFrom":makeQuery(id+"F31.boolean.opBoolean","SPLIT",FACE,{"disambiguationData":[TD([subQ23])],"derivedFrom":makeQuery(id+"F30.boolean.opBoolean","SPLIT",FACE,{"disambiguationData":[TD([subQ81])],"derivedFrom":makeQuery(id+"F29.boolean.opBoolean","SPLIT",FACE,{"disambiguationData":[TD([subQ81])],"derivedFrom":makeQuery(id+"F28.boolean.opBoolean","SPLIT",FACE,{"disambiguationData":[TD([subQ81])],"derivedFrom":makeQuery(id+"F27.boolean.opBoolean","SPLIT",FACE,{"disambiguationData":[TD([subQ81])],"derivedFrom":makeQuery(id+"F26.boolean.opBoolean","SPLIT",FACE,{"disambiguationData":[TD([subQ81])],"derivedFrom":makeQuery(id+"F25.boolean.opBoolean","SPLIT",FACE,{"disambiguationData":[TD([subQ81])],"derivedFrom":makeQuery(id+"F24.boolean.opBoolean","SPLIT",FACE,{"disambiguationData":[TD([subQ81])],"derivedFrom":makeQuery(id+"F1.opRevolve","SWEPT_FACE",FACE,{"disambiguationData":[OSD([sQuery(id+"F0.wireOp",EDGE,"E4")])]})})})})})})})})})})})})})})})})})],"blendedInto":[makeQuery(id+"F40.boolean.opBoolean","SPLIT",FACE,{"disambiguationData":[TD([subQ0])],"derivedFrom":makeQuery(id+"F38.boolean.opBoolean","SPLIT",FACE,{"disambiguationData":[TD([subQ15])],"derivedFrom":makeQuery(id+"F37.boolean.opBoolean","SPLIT",FACE,{"disambiguationData":[TD([subQ23])],"derivedFrom":makeQuery(id+"F36.boolean.opBoolean","SPLIT",FACE,{"disambiguationData":[TD([subQ23])],"derivedFrom":makeQuery(id+"F35.boolean.opBoolean","SPLIT",FACE,{"disambiguationData":[TD([subQ23])],"derivedFrom":makeQuery(id+"F34.boolean.opBoolean","SPLIT",FACE,{"disambiguationData":[TD([subQ23])],"derivedFrom":makeQuery(id+"F33.boolean.opBoolean","SPLIT",FACE,{"disambiguationData":[TD([subQ23])],"derivedFrom":makeQuery(id+"F32.boolean.opBoolean","SPLIT",FACE,{"disambiguationData":[TD([subQ23])],"derivedFrom":makeQuery(id+"F31.boolean.opBoolean","SPLIT",FACE,{"disambiguationData":[TD([subQ23])],"derivedFrom":makeQuery(id+"F30.boolean.opBoolean","SPLIT",FACE,{"disambiguationData":[TD([subQ81])],"derivedFrom":makeQuery(id+"F29.boolean.opBoolean","SPLIT",FACE,{"disambiguationData":[TD([subQ81])],"derivedFrom":makeQuery(id+"F28.boolean.opBoolean","SPLIT",FACE,{"disambiguationData":[TD([subQ81])],"derivedFrom":makeQuery(id+"F27.boolean.opBoolean","SPLIT",FACE,{"disambiguationData":[TD([subQ81])],"derivedFrom":makeQuery(id+"F26.boolean.opBoolean","SPLIT",FACE,{"disambiguationData":[TD([subQ81])],"derivedFrom":makeQuery(id+"F25.boolean.opBoolean","SPLIT",FACE,{"disambiguationData":[TD([subQ81])],"derivedFrom":makeQuery(id+"F24.boolean.opBoolean","SPLIT",FACE,{"disambiguationData":[TD([subQ81])],"derivedFrom":makeQuery(id+"F1.opRevolve","SWEPT_FACE",FACE,{"disambiguationData":[OSD([sQuery(id+"F0.wireOp",EDGE,"E4")])]})})})})})})})})})})})})})})})})})]});}
            var Q19;
            {var subQ0=makeQuery(id+"F1.opRevolve","SWEPT_FACE",FACE,{"disambiguationData":[OSD([sQuery(id+"F0.wireOp",EDGE,"E3")])]});var subQ5=sQuery(id+"F3.wireOp",EDGE,"E20.6.3");var subQ6=sQuery(id+"F3.wireOp",EDGE,"E20.6.2");var subQ7=sQuery(id+"F3.wireOp",EDGE,"E20.6.1");var subQ8=makeQuery(id+"F37.opLoft","SWEPT_FACE",FACE,{"disambiguationData":[OSD([subQ7,subQ6,subQ5,sQuery(id+"F22.wireOp",EDGE,"E28.14.0"),sQuery(id+"F22.wireOp",EDGE,"E28.14.2"),sQuery(id+"F22.wireOp",EDGE,"E28.14.3")])]});var subQ9=makeQuery(id+"F40.opExtrude","CAP_FACE",FACE,{"disambiguationData":[OSD([sQuery(id+"F39.wireOp",EDGE,"E29"),sQuery(id+"F39.wireOp",EDGE,"E30")])],"isStart":true});var subQ13=sQuery(id+"F4.wireOp",EDGE,"E26.6.3");var subQ14=sQuery(id+"F4.wireOp",EDGE,"E26.6.2");var subQ15=makeQuery(id+"F15.opLoft","SWEPT_FACE",FACE,{"disambiguationData":[OSD([subQ7,subQ6,subQ5,sQuery(id+"F4.wireOp",EDGE,"E26.6.1"),subQ14,subQ13])]});var subQ20=sQuery(id+"F3.wireOp",EDGE,"E20.7.0");var subQ24=makeQuery(id+"F14.opLoft","CAP_FACE",FACE,{"disambiguationData":[OSD([makeQuery(id+"F3.imprint","IMPRINT",FACE,{"disambiguationData":[TD([[makeQuery(id+"F3.imprint","IMPRINT",EDGE,{"derivedFrom":subQ20}),-1.0]])]})])],"isStart":true});var subQ76=sQuery(id+"F3.wireOp",EDGE,"E18.bottom");var subQ81=makeQuery(id+"F5.opLoft","CAP_FACE",FACE,{"disambiguationData":[OSD([makeQuery(id+"F3.imprint","IMPRINT",FACE,{"disambiguationData":[TD([[makeQuery(id+"F3.imprint","IMPRINT",EDGE,{"derivedFrom":subQ76}),1.0]])]})])],"isStart":true});Q19=makeQuery(id+"F44.opFillet","BLEND_EDGE",EDGE,{"blendedFrom":[makeQuery(id+"F40.boolean.opBoolean","INTERSECT",EDGE,{"derivedFrom":[subQ8,subQ9]}),makeQuery(id+"F40.boolean.opBoolean","SPLIT",FACE,{"disambiguationData":[TD([subQ0])],"derivedFrom":makeQuery(id+"F37.boolean.opBoolean","SPLIT",FACE,{"disambiguationData":[TD([subQ15])],"derivedFrom":makeQuery(id+"F36.boolean.opBoolean","SPLIT",FACE,{"disambiguationData":[TD([subQ24])],"derivedFrom":makeQuery(id+"F35.boolean.opBoolean","SPLIT",FACE,{"disambiguationData":[TD([subQ24])],"derivedFrom":makeQuery(id+"F34.boolean.opBoolean","SPLIT",FACE,{"disambiguationData":[TD([subQ24])],"derivedFrom":makeQuery(id+"F33.boolean.opBoolean","SPLIT",FACE,{"disambiguationData":[TD([subQ24])],"derivedFrom":makeQuery(id+"F32.boolean.opBoolean","SPLIT",FACE,{"disambiguationData":[TD([subQ24])],"derivedFrom":makeQuery(id+"F31.boolean.opBoolean","SPLIT",FACE,{"disambiguationData":[TD([subQ24])],"derivedFrom":makeQuery(id+"F30.boolean.opBoolean","SPLIT",FACE,{"disambiguationData":[TD([subQ81])],"derivedFrom":makeQuery(id+"F29.boolean.opBoolean","SPLIT",FACE,{"disambiguationData":[TD([subQ81])],"derivedFrom":makeQuery(id+"F28.boolean.opBoolean","SPLIT",FACE,{"disambiguationData":[TD([subQ81])],"derivedFrom":makeQuery(id+"F27.boolean.opBoolean","SPLIT",FACE,{"disambiguationData":[TD([subQ81])],"derivedFrom":makeQuery(id+"F26.boolean.opBoolean","SPLIT",FACE,{"disambiguationData":[TD([subQ81])],"derivedFrom":makeQuery(id+"F25.boolean.opBoolean","SPLIT",FACE,{"disambiguationData":[TD([subQ81])],"derivedFrom":makeQuery(id+"F24.boolean.opBoolean","SPLIT",FACE,{"disambiguationData":[TD([subQ81])],"derivedFrom":makeQuery(id+"F1.opRevolve","SWEPT_FACE",FACE,{"disambiguationData":[OSD([sQuery(id+"F0.wireOp",EDGE,"E4")])]})})})})})})})})})})})})})})})})],"blendedInto":[makeQuery(id+"F40.boolean.opBoolean","SPLIT",FACE,{"disambiguationData":[TD([subQ0])],"derivedFrom":makeQuery(id+"F37.boolean.opBoolean","SPLIT",FACE,{"disambiguationData":[TD([subQ15])],"derivedFrom":makeQuery(id+"F36.boolean.opBoolean","SPLIT",FACE,{"disambiguationData":[TD([subQ24])],"derivedFrom":makeQuery(id+"F35.boolean.opBoolean","SPLIT",FACE,{"disambiguationData":[TD([subQ24])],"derivedFrom":makeQuery(id+"F34.boolean.opBoolean","SPLIT",FACE,{"disambiguationData":[TD([subQ24])],"derivedFrom":makeQuery(id+"F33.boolean.opBoolean","SPLIT",FACE,{"disambiguationData":[TD([subQ24])],"derivedFrom":makeQuery(id+"F32.boolean.opBoolean","SPLIT",FACE,{"disambiguationData":[TD([subQ24])],"derivedFrom":makeQuery(id+"F31.boolean.opBoolean","SPLIT",FACE,{"disambiguationData":[TD([subQ24])],"derivedFrom":makeQuery(id+"F30.boolean.opBoolean","SPLIT",FACE,{"disambiguationData":[TD([subQ81])],"derivedFrom":makeQuery(id+"F29.boolean.opBoolean","SPLIT",FACE,{"disambiguationData":[TD([subQ81])],"derivedFrom":makeQuery(id+"F28.boolean.opBoolean","SPLIT",FACE,{"disambiguationData":[TD([subQ81])],"derivedFrom":makeQuery(id+"F27.boolean.opBoolean","SPLIT",FACE,{"disambiguationData":[TD([subQ81])],"derivedFrom":makeQuery(id+"F26.boolean.opBoolean","SPLIT",FACE,{"disambiguationData":[TD([subQ81])],"derivedFrom":makeQuery(id+"F25.boolean.opBoolean","SPLIT",FACE,{"disambiguationData":[TD([subQ81])],"derivedFrom":makeQuery(id+"F24.boolean.opBoolean","SPLIT",FACE,{"disambiguationData":[TD([subQ81])],"derivedFrom":makeQuery(id+"F1.opRevolve","SWEPT_FACE",FACE,{"disambiguationData":[OSD([sQuery(id+"F0.wireOp",EDGE,"E4")])]})})})})})})})})})})})})})})})})]});}
            var Q20;
            {var subQ0=makeQuery(id+"F1.opRevolve","SWEPT_FACE",FACE,{"disambiguationData":[OSD([sQuery(id+"F0.wireOp",EDGE,"E3")])]});var subQ1=sQuery(id+"F3.wireOp",EDGE,"E20.5.3");var subQ2=sQuery(id+"F3.wireOp",EDGE,"E20.5.2");var subQ3=sQuery(id+"F3.wireOp",EDGE,"E20.5.1");var subQ4=makeQuery(id+"F36.opLoft","SWEPT_FACE",FACE,{"disambiguationData":[OSD([subQ3,subQ2,subQ1,sQuery(id+"F22.wireOp",EDGE,"E28.13.0"),sQuery(id+"F22.wireOp",EDGE,"E28.13.2"),sQuery(id+"F22.wireOp",EDGE,"E28.13.3")])]});var subQ9=makeQuery(id+"F40.opExtrude","CAP_FACE",FACE,{"disambiguationData":[OSD([sQuery(id+"F39.wireOp",EDGE,"E29"),sQuery(id+"F39.wireOp",EDGE,"E30")])],"isStart":true});var subQ10=sQuery(id+"F4.wireOp",EDGE,"E26.5.3");var subQ11=sQuery(id+"F4.wireOp",EDGE,"E26.5.2");var subQ12=makeQuery(id+"F16.opLoft","SWEPT_FACE",FACE,{"disambiguationData":[OSD([subQ3,subQ2,subQ1,sQuery(id+"F4.wireOp",EDGE,"E26.5.1"),subQ11,subQ10])]});var subQ27=sQuery(id+"F3.wireOp",EDGE,"E20.7.0");var subQ31=makeQuery(id+"F14.opLoft","CAP_FACE",FACE,{"disambiguationData":[OSD([makeQuery(id+"F3.imprint","IMPRINT",FACE,{"disambiguationData":[TD([[makeQuery(id+"F3.imprint","IMPRINT",EDGE,{"derivedFrom":subQ27}),-1.0]])]})])],"isStart":true});var subQ76=sQuery(id+"F3.wireOp",EDGE,"E18.bottom");var subQ81=makeQuery(id+"F5.opLoft","CAP_FACE",FACE,{"disambiguationData":[OSD([makeQuery(id+"F3.imprint","IMPRINT",FACE,{"disambiguationData":[TD([[makeQuery(id+"F3.imprint","IMPRINT",EDGE,{"derivedFrom":subQ76}),1.0]])]})])],"isStart":true});Q20=makeQuery(id+"F44.opFillet","BLEND_EDGE",EDGE,{"blendedFrom":[makeQuery(id+"F40.boolean.opBoolean","INTERSECT",EDGE,{"derivedFrom":[subQ4,subQ9]}),makeQuery(id+"F40.boolean.opBoolean","SPLIT",FACE,{"disambiguationData":[TD([subQ0])],"derivedFrom":makeQuery(id+"F36.boolean.opBoolean","SPLIT",FACE,{"disambiguationData":[TD([subQ12])],"derivedFrom":makeQuery(id+"F35.boolean.opBoolean","SPLIT",FACE,{"disambiguationData":[TD([subQ31])],"derivedFrom":makeQuery(id+"F34.boolean.opBoolean","SPLIT",FACE,{"disambiguationData":[TD([subQ31])],"derivedFrom":makeQuery(id+"F33.boolean.opBoolean","SPLIT",FACE,{"disambiguationData":[TD([subQ31])],"derivedFrom":makeQuery(id+"F32.boolean.opBoolean","SPLIT",FACE,{"disambiguationData":[TD([subQ31])],"derivedFrom":makeQuery(id+"F31.boolean.opBoolean","SPLIT",FACE,{"disambiguationData":[TD([subQ31])],"derivedFrom":makeQuery(id+"F30.boolean.opBoolean","SPLIT",FACE,{"disambiguationData":[TD([subQ81])],"derivedFrom":makeQuery(id+"F29.boolean.opBoolean","SPLIT",FACE,{"disambiguationData":[TD([subQ81])],"derivedFrom":makeQuery(id+"F28.boolean.opBoolean","SPLIT",FACE,{"disambiguationData":[TD([subQ81])],"derivedFrom":makeQuery(id+"F27.boolean.opBoolean","SPLIT",FACE,{"disambiguationData":[TD([subQ81])],"derivedFrom":makeQuery(id+"F26.boolean.opBoolean","SPLIT",FACE,{"disambiguationData":[TD([subQ81])],"derivedFrom":makeQuery(id+"F25.boolean.opBoolean","SPLIT",FACE,{"disambiguationData":[TD([subQ81])],"derivedFrom":makeQuery(id+"F24.boolean.opBoolean","SPLIT",FACE,{"disambiguationData":[TD([subQ81])],"derivedFrom":makeQuery(id+"F1.opRevolve","SWEPT_FACE",FACE,{"disambiguationData":[OSD([sQuery(id+"F0.wireOp",EDGE,"E4")])]})})})})})})})})})})})})})})})],"blendedInto":[makeQuery(id+"F40.boolean.opBoolean","SPLIT",FACE,{"disambiguationData":[TD([subQ0])],"derivedFrom":makeQuery(id+"F36.boolean.opBoolean","SPLIT",FACE,{"disambiguationData":[TD([subQ12])],"derivedFrom":makeQuery(id+"F35.boolean.opBoolean","SPLIT",FACE,{"disambiguationData":[TD([subQ31])],"derivedFrom":makeQuery(id+"F34.boolean.opBoolean","SPLIT",FACE,{"disambiguationData":[TD([subQ31])],"derivedFrom":makeQuery(id+"F33.boolean.opBoolean","SPLIT",FACE,{"disambiguationData":[TD([subQ31])],"derivedFrom":makeQuery(id+"F32.boolean.opBoolean","SPLIT",FACE,{"disambiguationData":[TD([subQ31])],"derivedFrom":makeQuery(id+"F31.boolean.opBoolean","SPLIT",FACE,{"disambiguationData":[TD([subQ31])],"derivedFrom":makeQuery(id+"F30.boolean.opBoolean","SPLIT",FACE,{"disambiguationData":[TD([subQ81])],"derivedFrom":makeQuery(id+"F29.boolean.opBoolean","SPLIT",FACE,{"disambiguationData":[TD([subQ81])],"derivedFrom":makeQuery(id+"F28.boolean.opBoolean","SPLIT",FACE,{"disambiguationData":[TD([subQ81])],"derivedFrom":makeQuery(id+"F27.boolean.opBoolean","SPLIT",FACE,{"disambiguationData":[TD([subQ81])],"derivedFrom":makeQuery(id+"F26.boolean.opBoolean","SPLIT",FACE,{"disambiguationData":[TD([subQ81])],"derivedFrom":makeQuery(id+"F25.boolean.opBoolean","SPLIT",FACE,{"disambiguationData":[TD([subQ81])],"derivedFrom":makeQuery(id+"F24.boolean.opBoolean","SPLIT",FACE,{"disambiguationData":[TD([subQ81])],"derivedFrom":makeQuery(id+"F1.opRevolve","SWEPT_FACE",FACE,{"disambiguationData":[OSD([sQuery(id+"F0.wireOp",EDGE,"E4")])]})})})})})})})})})})})})})})})]});}
            var Q21;
            {var subQ0=makeQuery(id+"F1.opRevolve","SWEPT_FACE",FACE,{"disambiguationData":[OSD([sQuery(id+"F0.wireOp",EDGE,"E3")])]});var subQ5=sQuery(id+"F3.wireOp",EDGE,"E20.4.3");var subQ6=sQuery(id+"F3.wireOp",EDGE,"E20.4.2");var subQ7=sQuery(id+"F3.wireOp",EDGE,"E20.4.1");var subQ8=makeQuery(id+"F35.opLoft","SWEPT_FACE",FACE,{"disambiguationData":[OSD([subQ7,subQ6,subQ5,sQuery(id+"F22.wireOp",EDGE,"E28.12.0"),sQuery(id+"F22.wireOp",EDGE,"E28.12.2"),sQuery(id+"F22.wireOp",EDGE,"E28.12.3")])]});var subQ9=makeQuery(id+"F40.opExtrude","CAP_FACE",FACE,{"disambiguationData":[OSD([sQuery(id+"F39.wireOp",EDGE,"E29"),sQuery(id+"F39.wireOp",EDGE,"E30")])],"isStart":true});var subQ10=sQuery(id+"F4.wireOp",EDGE,"E26.4.3");var subQ11=sQuery(id+"F4.wireOp",EDGE,"E26.4.2");var subQ12=makeQuery(id+"F17.opLoft","SWEPT_FACE",FACE,{"disambiguationData":[OSD([subQ7,subQ6,subQ5,sQuery(id+"F4.wireOp",EDGE,"E26.4.1"),subQ11,subQ10])]});var subQ33=sQuery(id+"F3.wireOp",EDGE,"E20.7.0");var subQ37=makeQuery(id+"F14.opLoft","CAP_FACE",FACE,{"disambiguationData":[OSD([makeQuery(id+"F3.imprint","IMPRINT",FACE,{"disambiguationData":[TD([[makeQuery(id+"F3.imprint","IMPRINT",EDGE,{"derivedFrom":subQ33}),-1.0]])]})])],"isStart":true});var subQ76=sQuery(id+"F3.wireOp",EDGE,"E18.bottom");var subQ81=makeQuery(id+"F5.opLoft","CAP_FACE",FACE,{"disambiguationData":[OSD([makeQuery(id+"F3.imprint","IMPRINT",FACE,{"disambiguationData":[TD([[makeQuery(id+"F3.imprint","IMPRINT",EDGE,{"derivedFrom":subQ76}),1.0]])]})])],"isStart":true});Q21=makeQuery(id+"F44.opFillet","BLEND_EDGE",EDGE,{"blendedFrom":[makeQuery(id+"F40.boolean.opBoolean","INTERSECT",EDGE,{"derivedFrom":[subQ8,subQ9]}),makeQuery(id+"F40.boolean.opBoolean","SPLIT",FACE,{"disambiguationData":[TD([subQ0])],"derivedFrom":makeQuery(id+"F35.boolean.opBoolean","SPLIT",FACE,{"disambiguationData":[TD([subQ12])],"derivedFrom":makeQuery(id+"F34.boolean.opBoolean","SPLIT",FACE,{"disambiguationData":[TD([subQ37])],"derivedFrom":makeQuery(id+"F33.boolean.opBoolean","SPLIT",FACE,{"disambiguationData":[TD([subQ37])],"derivedFrom":makeQuery(id+"F32.boolean.opBoolean","SPLIT",FACE,{"disambiguationData":[TD([subQ37])],"derivedFrom":makeQuery(id+"F31.boolean.opBoolean","SPLIT",FACE,{"disambiguationData":[TD([subQ37])],"derivedFrom":makeQuery(id+"F30.boolean.opBoolean","SPLIT",FACE,{"disambiguationData":[TD([subQ81])],"derivedFrom":makeQuery(id+"F29.boolean.opBoolean","SPLIT",FACE,{"disambiguationData":[TD([subQ81])],"derivedFrom":makeQuery(id+"F28.boolean.opBoolean","SPLIT",FACE,{"disambiguationData":[TD([subQ81])],"derivedFrom":makeQuery(id+"F27.boolean.opBoolean","SPLIT",FACE,{"disambiguationData":[TD([subQ81])],"derivedFrom":makeQuery(id+"F26.boolean.opBoolean","SPLIT",FACE,{"disambiguationData":[TD([subQ81])],"derivedFrom":makeQuery(id+"F25.boolean.opBoolean","SPLIT",FACE,{"disambiguationData":[TD([subQ81])],"derivedFrom":makeQuery(id+"F24.boolean.opBoolean","SPLIT",FACE,{"disambiguationData":[TD([subQ81])],"derivedFrom":makeQuery(id+"F1.opRevolve","SWEPT_FACE",FACE,{"disambiguationData":[OSD([sQuery(id+"F0.wireOp",EDGE,"E4")])]})})})})})})})})})})})})})})],"blendedInto":[makeQuery(id+"F40.boolean.opBoolean","SPLIT",FACE,{"disambiguationData":[TD([subQ0])],"derivedFrom":makeQuery(id+"F35.boolean.opBoolean","SPLIT",FACE,{"disambiguationData":[TD([subQ12])],"derivedFrom":makeQuery(id+"F34.boolean.opBoolean","SPLIT",FACE,{"disambiguationData":[TD([subQ37])],"derivedFrom":makeQuery(id+"F33.boolean.opBoolean","SPLIT",FACE,{"disambiguationData":[TD([subQ37])],"derivedFrom":makeQuery(id+"F32.boolean.opBoolean","SPLIT",FACE,{"disambiguationData":[TD([subQ37])],"derivedFrom":makeQuery(id+"F31.boolean.opBoolean","SPLIT",FACE,{"disambiguationData":[TD([subQ37])],"derivedFrom":makeQuery(id+"F30.boolean.opBoolean","SPLIT",FACE,{"disambiguationData":[TD([subQ81])],"derivedFrom":makeQuery(id+"F29.boolean.opBoolean","SPLIT",FACE,{"disambiguationData":[TD([subQ81])],"derivedFrom":makeQuery(id+"F28.boolean.opBoolean","SPLIT",FACE,{"disambiguationData":[TD([subQ81])],"derivedFrom":makeQuery(id+"F27.boolean.opBoolean","SPLIT",FACE,{"disambiguationData":[TD([subQ81])],"derivedFrom":makeQuery(id+"F26.boolean.opBoolean","SPLIT",FACE,{"disambiguationData":[TD([subQ81])],"derivedFrom":makeQuery(id+"F25.boolean.opBoolean","SPLIT",FACE,{"disambiguationData":[TD([subQ81])],"derivedFrom":makeQuery(id+"F24.boolean.opBoolean","SPLIT",FACE,{"disambiguationData":[TD([subQ81])],"derivedFrom":makeQuery(id+"F1.opRevolve","SWEPT_FACE",FACE,{"disambiguationData":[OSD([sQuery(id+"F0.wireOp",EDGE,"E4")])]})})})})})})})})})})})})})})]});}
            var Q22;
            {var subQ0=makeQuery(id+"F1.opRevolve","SWEPT_FACE",FACE,{"disambiguationData":[OSD([sQuery(id+"F0.wireOp",EDGE,"E3")])]});var subQ5=makeQuery(id+"F40.opExtrude","CAP_FACE",FACE,{"disambiguationData":[OSD([sQuery(id+"F39.wireOp",EDGE,"E29"),sQuery(id+"F39.wireOp",EDGE,"E30")])],"isStart":true});var subQ6=sQuery(id+"F3.wireOp",EDGE,"E20.3.3");var subQ7=sQuery(id+"F3.wireOp",EDGE,"E20.3.2");var subQ8=sQuery(id+"F3.wireOp",EDGE,"E20.3.1");var subQ9=makeQuery(id+"F34.opLoft","SWEPT_FACE",FACE,{"disambiguationData":[OSD([subQ8,subQ7,subQ6,sQuery(id+"F22.wireOp",EDGE,"E28.11.0"),sQuery(id+"F22.wireOp",EDGE,"E28.11.2"),sQuery(id+"F22.wireOp",EDGE,"E28.11.3")])]});var subQ13=sQuery(id+"F4.wireOp",EDGE,"E26.3.3");var subQ14=sQuery(id+"F4.wireOp",EDGE,"E26.3.2");var subQ15=makeQuery(id+"F18.opLoft","SWEPT_FACE",FACE,{"disambiguationData":[OSD([subQ8,subQ7,subQ6,sQuery(id+"F4.wireOp",EDGE,"E26.3.1"),subQ14,subQ13])]});var subQ36=sQuery(id+"F3.wireOp",EDGE,"E20.7.0");var subQ40=makeQuery(id+"F14.opLoft","CAP_FACE",FACE,{"disambiguationData":[OSD([makeQuery(id+"F3.imprint","IMPRINT",FACE,{"disambiguationData":[TD([[makeQuery(id+"F3.imprint","IMPRINT",EDGE,{"derivedFrom":subQ36}),-1.0]])]})])],"isStart":true});var subQ76=sQuery(id+"F3.wireOp",EDGE,"E18.bottom");var subQ81=makeQuery(id+"F5.opLoft","CAP_FACE",FACE,{"disambiguationData":[OSD([makeQuery(id+"F3.imprint","IMPRINT",FACE,{"disambiguationData":[TD([[makeQuery(id+"F3.imprint","IMPRINT",EDGE,{"derivedFrom":subQ76}),1.0]])]})])],"isStart":true});Q22=makeQuery(id+"F44.opFillet","BLEND_EDGE",EDGE,{"blendedFrom":[makeQuery(id+"F40.boolean.opBoolean","INTERSECT",EDGE,{"derivedFrom":[subQ9,subQ5]}),makeQuery(id+"F40.boolean.opBoolean","SPLIT",FACE,{"disambiguationData":[TD([subQ0])],"derivedFrom":makeQuery(id+"F34.boolean.opBoolean","SPLIT",FACE,{"disambiguationData":[TD([subQ15])],"derivedFrom":makeQuery(id+"F33.boolean.opBoolean","SPLIT",FACE,{"disambiguationData":[TD([subQ40])],"derivedFrom":makeQuery(id+"F32.boolean.opBoolean","SPLIT",FACE,{"disambiguationData":[TD([subQ40])],"derivedFrom":makeQuery(id+"F31.boolean.opBoolean","SPLIT",FACE,{"disambiguationData":[TD([subQ40])],"derivedFrom":makeQuery(id+"F30.boolean.opBoolean","SPLIT",FACE,{"disambiguationData":[TD([subQ81])],"derivedFrom":makeQuery(id+"F29.boolean.opBoolean","SPLIT",FACE,{"disambiguationData":[TD([subQ81])],"derivedFrom":makeQuery(id+"F28.boolean.opBoolean","SPLIT",FACE,{"disambiguationData":[TD([subQ81])],"derivedFrom":makeQuery(id+"F27.boolean.opBoolean","SPLIT",FACE,{"disambiguationData":[TD([subQ81])],"derivedFrom":makeQuery(id+"F26.boolean.opBoolean","SPLIT",FACE,{"disambiguationData":[TD([subQ81])],"derivedFrom":makeQuery(id+"F25.boolean.opBoolean","SPLIT",FACE,{"disambiguationData":[TD([subQ81])],"derivedFrom":makeQuery(id+"F24.boolean.opBoolean","SPLIT",FACE,{"disambiguationData":[TD([subQ81])],"derivedFrom":makeQuery(id+"F1.opRevolve","SWEPT_FACE",FACE,{"disambiguationData":[OSD([sQuery(id+"F0.wireOp",EDGE,"E4")])]})})})})})})})})})})})})})],"blendedInto":[makeQuery(id+"F40.boolean.opBoolean","SPLIT",FACE,{"disambiguationData":[TD([subQ0])],"derivedFrom":makeQuery(id+"F34.boolean.opBoolean","SPLIT",FACE,{"disambiguationData":[TD([subQ15])],"derivedFrom":makeQuery(id+"F33.boolean.opBoolean","SPLIT",FACE,{"disambiguationData":[TD([subQ40])],"derivedFrom":makeQuery(id+"F32.boolean.opBoolean","SPLIT",FACE,{"disambiguationData":[TD([subQ40])],"derivedFrom":makeQuery(id+"F31.boolean.opBoolean","SPLIT",FACE,{"disambiguationData":[TD([subQ40])],"derivedFrom":makeQuery(id+"F30.boolean.opBoolean","SPLIT",FACE,{"disambiguationData":[TD([subQ81])],"derivedFrom":makeQuery(id+"F29.boolean.opBoolean","SPLIT",FACE,{"disambiguationData":[TD([subQ81])],"derivedFrom":makeQuery(id+"F28.boolean.opBoolean","SPLIT",FACE,{"disambiguationData":[TD([subQ81])],"derivedFrom":makeQuery(id+"F27.boolean.opBoolean","SPLIT",FACE,{"disambiguationData":[TD([subQ81])],"derivedFrom":makeQuery(id+"F26.boolean.opBoolean","SPLIT",FACE,{"disambiguationData":[TD([subQ81])],"derivedFrom":makeQuery(id+"F25.boolean.opBoolean","SPLIT",FACE,{"disambiguationData":[TD([subQ81])],"derivedFrom":makeQuery(id+"F24.boolean.opBoolean","SPLIT",FACE,{"disambiguationData":[TD([subQ81])],"derivedFrom":makeQuery(id+"F1.opRevolve","SWEPT_FACE",FACE,{"disambiguationData":[OSD([sQuery(id+"F0.wireOp",EDGE,"E4")])]})})})})})})})})})})})})})]});}
            var Q23;
            {var subQ0=makeQuery(id+"F1.opRevolve","SWEPT_FACE",FACE,{"disambiguationData":[OSD([sQuery(id+"F0.wireOp",EDGE,"E3")])]});var subQ5=sQuery(id+"F3.wireOp",EDGE,"E20.2.3");var subQ6=sQuery(id+"F3.wireOp",EDGE,"E20.2.2");var subQ7=sQuery(id+"F3.wireOp",EDGE,"E20.2.1");var subQ8=makeQuery(id+"F33.opLoft","SWEPT_FACE",FACE,{"disambiguationData":[OSD([subQ7,subQ6,subQ5,sQuery(id+"F22.wireOp",EDGE,"E28.10.0"),sQuery(id+"F22.wireOp",EDGE,"E28.10.2"),sQuery(id+"F22.wireOp",EDGE,"E28.10.3")])]});var subQ9=makeQuery(id+"F40.opExtrude","CAP_FACE",FACE,{"disambiguationData":[OSD([sQuery(id+"F39.wireOp",EDGE,"E29"),sQuery(id+"F39.wireOp",EDGE,"E30")])],"isStart":true});var subQ13=sQuery(id+"F4.wireOp",EDGE,"E26.2.3");var subQ14=sQuery(id+"F4.wireOp",EDGE,"E26.2.2");var subQ15=makeQuery(id+"F19.opLoft","SWEPT_FACE",FACE,{"disambiguationData":[OSD([subQ7,subQ6,subQ5,sQuery(id+"F4.wireOp",EDGE,"E26.2.1"),subQ14,subQ13])]});var subQ56=sQuery(id+"F3.wireOp",EDGE,"E20.7.0");var subQ63=makeQuery(id+"F14.opLoft","CAP_FACE",FACE,{"disambiguationData":[OSD([makeQuery(id+"F3.imprint","IMPRINT",FACE,{"disambiguationData":[TD([[makeQuery(id+"F3.imprint","IMPRINT",EDGE,{"derivedFrom":subQ56}),-1.0]])]})])],"isStart":true});var subQ76=sQuery(id+"F3.wireOp",EDGE,"E18.bottom");var subQ81=makeQuery(id+"F5.opLoft","CAP_FACE",FACE,{"disambiguationData":[OSD([makeQuery(id+"F3.imprint","IMPRINT",FACE,{"disambiguationData":[TD([[makeQuery(id+"F3.imprint","IMPRINT",EDGE,{"derivedFrom":subQ76}),1.0]])]})])],"isStart":true});Q23=makeQuery(id+"F44.opFillet","BLEND_EDGE",EDGE,{"blendedFrom":[makeQuery(id+"F40.boolean.opBoolean","INTERSECT",EDGE,{"derivedFrom":[subQ8,subQ9]}),makeQuery(id+"F40.boolean.opBoolean","SPLIT",FACE,{"disambiguationData":[TD([subQ0])],"derivedFrom":makeQuery(id+"F33.boolean.opBoolean","SPLIT",FACE,{"disambiguationData":[TD([subQ15])],"derivedFrom":makeQuery(id+"F32.boolean.opBoolean","SPLIT",FACE,{"disambiguationData":[TD([subQ63])],"derivedFrom":makeQuery(id+"F31.boolean.opBoolean","SPLIT",FACE,{"disambiguationData":[TD([subQ63])],"derivedFrom":makeQuery(id+"F30.boolean.opBoolean","SPLIT",FACE,{"disambiguationData":[TD([subQ81])],"derivedFrom":makeQuery(id+"F29.boolean.opBoolean","SPLIT",FACE,{"disambiguationData":[TD([subQ81])],"derivedFrom":makeQuery(id+"F28.boolean.opBoolean","SPLIT",FACE,{"disambiguationData":[TD([subQ81])],"derivedFrom":makeQuery(id+"F27.boolean.opBoolean","SPLIT",FACE,{"disambiguationData":[TD([subQ81])],"derivedFrom":makeQuery(id+"F26.boolean.opBoolean","SPLIT",FACE,{"disambiguationData":[TD([subQ81])],"derivedFrom":makeQuery(id+"F25.boolean.opBoolean","SPLIT",FACE,{"disambiguationData":[TD([subQ81])],"derivedFrom":makeQuery(id+"F24.boolean.opBoolean","SPLIT",FACE,{"disambiguationData":[TD([subQ81])],"derivedFrom":makeQuery(id+"F1.opRevolve","SWEPT_FACE",FACE,{"disambiguationData":[OSD([sQuery(id+"F0.wireOp",EDGE,"E4")])]})})})})})})})})})})})})],"blendedInto":[makeQuery(id+"F40.boolean.opBoolean","SPLIT",FACE,{"disambiguationData":[TD([subQ0])],"derivedFrom":makeQuery(id+"F33.boolean.opBoolean","SPLIT",FACE,{"disambiguationData":[TD([subQ15])],"derivedFrom":makeQuery(id+"F32.boolean.opBoolean","SPLIT",FACE,{"disambiguationData":[TD([subQ63])],"derivedFrom":makeQuery(id+"F31.boolean.opBoolean","SPLIT",FACE,{"disambiguationData":[TD([subQ63])],"derivedFrom":makeQuery(id+"F30.boolean.opBoolean","SPLIT",FACE,{"disambiguationData":[TD([subQ81])],"derivedFrom":makeQuery(id+"F29.boolean.opBoolean","SPLIT",FACE,{"disambiguationData":[TD([subQ81])],"derivedFrom":makeQuery(id+"F28.boolean.opBoolean","SPLIT",FACE,{"disambiguationData":[TD([subQ81])],"derivedFrom":makeQuery(id+"F27.boolean.opBoolean","SPLIT",FACE,{"disambiguationData":[TD([subQ81])],"derivedFrom":makeQuery(id+"F26.boolean.opBoolean","SPLIT",FACE,{"disambiguationData":[TD([subQ81])],"derivedFrom":makeQuery(id+"F25.boolean.opBoolean","SPLIT",FACE,{"disambiguationData":[TD([subQ81])],"derivedFrom":makeQuery(id+"F24.boolean.opBoolean","SPLIT",FACE,{"disambiguationData":[TD([subQ81])],"derivedFrom":makeQuery(id+"F1.opRevolve","SWEPT_FACE",FACE,{"disambiguationData":[OSD([sQuery(id+"F0.wireOp",EDGE,"E4")])]})})})})})})})})})})})})]});}
            var Q24;
            {var subQ0=makeQuery(id+"F1.opRevolve","SWEPT_FACE",FACE,{"disambiguationData":[OSD([sQuery(id+"F0.wireOp",EDGE,"E3")])]});var subQ1=sQuery(id+"F3.wireOp",EDGE,"E20.1.3");var subQ2=sQuery(id+"F3.wireOp",EDGE,"E20.1.2");var subQ3=sQuery(id+"F3.wireOp",EDGE,"E20.1.1");var subQ4=makeQuery(id+"F32.opLoft","SWEPT_FACE",FACE,{"disambiguationData":[OSD([subQ3,subQ2,subQ1,sQuery(id+"F22.wireOp",EDGE,"E28.9.0"),sQuery(id+"F22.wireOp",EDGE,"E28.9.2"),sQuery(id+"F22.wireOp",EDGE,"E28.9.3")])]});var subQ5=sQuery(id+"F3.wireOp",EDGE,"E18.left");var subQ6=sQuery(id+"F3.wireOp",EDGE,"E18.top");var subQ7=sQuery(id+"F3.wireOp",EDGE,"E18.bottom");var subQ9=makeQuery(id+"F40.opExtrude","CAP_FACE",FACE,{"disambiguationData":[OSD([sQuery(id+"F39.wireOp",EDGE,"E29"),sQuery(id+"F39.wireOp",EDGE,"E30")])],"isStart":true});var subQ13=sQuery(id+"F4.wireOp",EDGE,"E23");var subQ14=sQuery(id+"F4.wireOp",EDGE,"E22");var subQ15=makeQuery(id+"F5.opLoft","SWEPT_FACE",FACE,{"disambiguationData":[OSD([subQ7,subQ6,subQ5,sQuery(id+"F4.wireOp",EDGE,"E21"),subQ14,subQ13])]});var subQ65=sQuery(id+"F3.wireOp",EDGE,"E20.7.0");var subQ73=makeQuery(id+"F14.opLoft","CAP_FACE",FACE,{"disambiguationData":[OSD([makeQuery(id+"F3.imprint","IMPRINT",FACE,{"disambiguationData":[TD([[makeQuery(id+"F3.imprint","IMPRINT",EDGE,{"derivedFrom":subQ65}),-1.0]])]})])],"isStart":true});var subQ81=makeQuery(id+"F5.opLoft","CAP_FACE",FACE,{"disambiguationData":[OSD([makeQuery(id+"F3.imprint","IMPRINT",FACE,{"disambiguationData":[TD([[makeQuery(id+"F3.imprint","IMPRINT",EDGE,{"derivedFrom":subQ7}),1.0]])]})])],"isStart":true});Q24=makeQuery(id+"F44.opFillet","BLEND_EDGE",EDGE,{"blendedFrom":[makeQuery(id+"F40.boolean.opBoolean","INTERSECT",EDGE,{"derivedFrom":[subQ4,subQ9]}),makeQuery(id+"F40.boolean.opBoolean","SPLIT",FACE,{"disambiguationData":[TD([subQ0])],"derivedFrom":makeQuery(id+"F32.boolean.opBoolean","SPLIT",FACE,{"disambiguationData":[TD([subQ15])],"derivedFrom":makeQuery(id+"F31.boolean.opBoolean","SPLIT",FACE,{"disambiguationData":[TD([subQ73])],"derivedFrom":makeQuery(id+"F30.boolean.opBoolean","SPLIT",FACE,{"disambiguationData":[TD([subQ81])],"derivedFrom":makeQuery(id+"F29.boolean.opBoolean","SPLIT",FACE,{"disambiguationData":[TD([subQ81])],"derivedFrom":makeQuery(id+"F28.boolean.opBoolean","SPLIT",FACE,{"disambiguationData":[TD([subQ81])],"derivedFrom":makeQuery(id+"F27.boolean.opBoolean","SPLIT",FACE,{"disambiguationData":[TD([subQ81])],"derivedFrom":makeQuery(id+"F26.boolean.opBoolean","SPLIT",FACE,{"disambiguationData":[TD([subQ81])],"derivedFrom":makeQuery(id+"F25.boolean.opBoolean","SPLIT",FACE,{"disambiguationData":[TD([subQ81])],"derivedFrom":makeQuery(id+"F24.boolean.opBoolean","SPLIT",FACE,{"disambiguationData":[TD([subQ81])],"derivedFrom":makeQuery(id+"F1.opRevolve","SWEPT_FACE",FACE,{"disambiguationData":[OSD([sQuery(id+"F0.wireOp",EDGE,"E4")])]})})})})})})})})})})})],"blendedInto":[makeQuery(id+"F40.boolean.opBoolean","SPLIT",FACE,{"disambiguationData":[TD([subQ0])],"derivedFrom":makeQuery(id+"F32.boolean.opBoolean","SPLIT",FACE,{"disambiguationData":[TD([subQ15])],"derivedFrom":makeQuery(id+"F31.boolean.opBoolean","SPLIT",FACE,{"disambiguationData":[TD([subQ73])],"derivedFrom":makeQuery(id+"F30.boolean.opBoolean","SPLIT",FACE,{"disambiguationData":[TD([subQ81])],"derivedFrom":makeQuery(id+"F29.boolean.opBoolean","SPLIT",FACE,{"disambiguationData":[TD([subQ81])],"derivedFrom":makeQuery(id+"F28.boolean.opBoolean","SPLIT",FACE,{"disambiguationData":[TD([subQ81])],"derivedFrom":makeQuery(id+"F27.boolean.opBoolean","SPLIT",FACE,{"disambiguationData":[TD([subQ81])],"derivedFrom":makeQuery(id+"F26.boolean.opBoolean","SPLIT",FACE,{"disambiguationData":[TD([subQ81])],"derivedFrom":makeQuery(id+"F25.boolean.opBoolean","SPLIT",FACE,{"disambiguationData":[TD([subQ81])],"derivedFrom":makeQuery(id+"F24.boolean.opBoolean","SPLIT",FACE,{"disambiguationData":[TD([subQ81])],"derivedFrom":makeQuery(id+"F1.opRevolve","SWEPT_FACE",FACE,{"disambiguationData":[OSD([sQuery(id+"F0.wireOp",EDGE,"E4")])]})})})})})})})})})})})]});}
            var Q25;
            {var subQ0=makeQuery(id+"F1.opRevolve","SWEPT_FACE",FACE,{"disambiguationData":[OSD([sQuery(id+"F0.wireOp",EDGE,"E3")])]});var subQ1=sQuery(id+"F3.wireOp",EDGE,"E18.right");var subQ2=sQuery(id+"F3.wireOp",EDGE,"E18.top");var subQ3=sQuery(id+"F3.wireOp",EDGE,"E18.bottom");var subQ4=makeQuery(id+"F31.opLoft","SWEPT_FACE",FACE,{"disambiguationData":[OSD([subQ3,subQ2,subQ1,sQuery(id+"F22.wireOp",EDGE,"E28.8.0"),sQuery(id+"F22.wireOp",EDGE,"E28.8.2"),sQuery(id+"F22.wireOp",EDGE,"E28.8.3")])]});var subQ9=makeQuery(id+"F40.opExtrude","CAP_FACE",FACE,{"disambiguationData":[OSD([sQuery(id+"F39.wireOp",EDGE,"E29"),sQuery(id+"F39.wireOp",EDGE,"E30")])],"isStart":true});var subQ13=sQuery(id+"F4.wireOp",EDGE,"E23");var subQ14=sQuery(id+"F4.wireOp",EDGE,"E22");var subQ15=makeQuery(id+"F5.opLoft","SWEPT_FACE",FACE,{"disambiguationData":[OSD([subQ3,subQ2,subQ1,subQ14,subQ13,sQuery(id+"F4.wireOp",EDGE,"E24")])]});var subQ59=makeQuery(id+"F5.opLoft","CAP_FACE",FACE,{"disambiguationData":[OSD([makeQuery(id+"F3.imprint","IMPRINT",FACE,{"disambiguationData":[TD([[makeQuery(id+"F3.imprint","IMPRINT",EDGE,{"derivedFrom":subQ3}),1.0]])]})])],"isStart":true});Q25=makeQuery(id+"F44.opFillet","BLEND_EDGE",EDGE,{"blendedFrom":[makeQuery(id+"F40.boolean.opBoolean","INTERSECT",EDGE,{"derivedFrom":[subQ4,subQ9]}),makeQuery(id+"F40.boolean.opBoolean","SPLIT",FACE,{"disambiguationData":[TD([subQ0])],"derivedFrom":makeQuery(id+"F31.boolean.opBoolean","SPLIT",FACE,{"disambiguationData":[TD([subQ15])],"derivedFrom":makeQuery(id+"F30.boolean.opBoolean","SPLIT",FACE,{"disambiguationData":[TD([subQ59])],"derivedFrom":makeQuery(id+"F29.boolean.opBoolean","SPLIT",FACE,{"disambiguationData":[TD([subQ59])],"derivedFrom":makeQuery(id+"F28.boolean.opBoolean","SPLIT",FACE,{"disambiguationData":[TD([subQ59])],"derivedFrom":makeQuery(id+"F27.boolean.opBoolean","SPLIT",FACE,{"disambiguationData":[TD([subQ59])],"derivedFrom":makeQuery(id+"F26.boolean.opBoolean","SPLIT",FACE,{"disambiguationData":[TD([subQ59])],"derivedFrom":makeQuery(id+"F25.boolean.opBoolean","SPLIT",FACE,{"disambiguationData":[TD([subQ59])],"derivedFrom":makeQuery(id+"F24.boolean.opBoolean","SPLIT",FACE,{"disambiguationData":[TD([subQ59])],"derivedFrom":makeQuery(id+"F1.opRevolve","SWEPT_FACE",FACE,{"disambiguationData":[OSD([sQuery(id+"F0.wireOp",EDGE,"E4")])]})})})})})})})})})})],"blendedInto":[makeQuery(id+"F40.boolean.opBoolean","SPLIT",FACE,{"disambiguationData":[TD([subQ0])],"derivedFrom":makeQuery(id+"F31.boolean.opBoolean","SPLIT",FACE,{"disambiguationData":[TD([subQ15])],"derivedFrom":makeQuery(id+"F30.boolean.opBoolean","SPLIT",FACE,{"disambiguationData":[TD([subQ59])],"derivedFrom":makeQuery(id+"F29.boolean.opBoolean","SPLIT",FACE,{"disambiguationData":[TD([subQ59])],"derivedFrom":makeQuery(id+"F28.boolean.opBoolean","SPLIT",FACE,{"disambiguationData":[TD([subQ59])],"derivedFrom":makeQuery(id+"F27.boolean.opBoolean","SPLIT",FACE,{"disambiguationData":[TD([subQ59])],"derivedFrom":makeQuery(id+"F26.boolean.opBoolean","SPLIT",FACE,{"disambiguationData":[TD([subQ59])],"derivedFrom":makeQuery(id+"F25.boolean.opBoolean","SPLIT",FACE,{"disambiguationData":[TD([subQ59])],"derivedFrom":makeQuery(id+"F24.boolean.opBoolean","SPLIT",FACE,{"disambiguationData":[TD([subQ59])],"derivedFrom":makeQuery(id+"F1.opRevolve","SWEPT_FACE",FACE,{"disambiguationData":[OSD([sQuery(id+"F0.wireOp",EDGE,"E4")])]})})})})})})})})})})]});}
            var Q26;
            {var subQ0=makeQuery(id+"F1.opRevolve","SWEPT_FACE",FACE,{"disambiguationData":[OSD([sQuery(id+"F0.wireOp",EDGE,"E3")])]});var subQ5=sQuery(id+"F3.wireOp",EDGE,"E20.15.3");var subQ6=sQuery(id+"F3.wireOp",EDGE,"E20.15.2");var subQ7=sQuery(id+"F3.wireOp",EDGE,"E20.15.1");var subQ8=makeQuery(id+"F30.opLoft","SWEPT_FACE",FACE,{"disambiguationData":[OSD([subQ7,subQ6,subQ5,sQuery(id+"F22.wireOp",EDGE,"E28.7.0"),sQuery(id+"F22.wireOp",EDGE,"E28.7.2"),sQuery(id+"F22.wireOp",EDGE,"E28.7.3")])]});var subQ9=makeQuery(id+"F40.opExtrude","CAP_FACE",FACE,{"disambiguationData":[OSD([sQuery(id+"F39.wireOp",EDGE,"E29"),sQuery(id+"F39.wireOp",EDGE,"E30")])],"isStart":true});var subQ10=sQuery(id+"F4.wireOp",EDGE,"E26.15.3");var subQ11=sQuery(id+"F4.wireOp",EDGE,"E26.15.2");var subQ12=makeQuery(id+"F6.opLoft","SWEPT_FACE",FACE,{"disambiguationData":[OSD([subQ7,subQ6,subQ5,sQuery(id+"F4.wireOp",EDGE,"E26.15.1"),subQ11,subQ10])]});var subQ48=sQuery(id+"F3.wireOp",EDGE,"E18.bottom");var subQ51=makeQuery(id+"F5.opLoft","CAP_FACE",FACE,{"disambiguationData":[OSD([makeQuery(id+"F3.imprint","IMPRINT",FACE,{"disambiguationData":[TD([[makeQuery(id+"F3.imprint","IMPRINT",EDGE,{"derivedFrom":subQ48}),1.0]])]})])],"isStart":true});Q26=makeQuery(id+"F44.opFillet","BLEND_EDGE",EDGE,{"blendedFrom":[makeQuery(id+"F40.boolean.opBoolean","INTERSECT",EDGE,{"derivedFrom":[subQ8,subQ9]}),makeQuery(id+"F40.boolean.opBoolean","SPLIT",FACE,{"disambiguationData":[TD([subQ0])],"derivedFrom":makeQuery(id+"F30.boolean.opBoolean","SPLIT",FACE,{"disambiguationData":[TD([subQ12])],"derivedFrom":makeQuery(id+"F29.boolean.opBoolean","SPLIT",FACE,{"disambiguationData":[TD([subQ51])],"derivedFrom":makeQuery(id+"F28.boolean.opBoolean","SPLIT",FACE,{"disambiguationData":[TD([subQ51])],"derivedFrom":makeQuery(id+"F27.boolean.opBoolean","SPLIT",FACE,{"disambiguationData":[TD([subQ51])],"derivedFrom":makeQuery(id+"F26.boolean.opBoolean","SPLIT",FACE,{"disambiguationData":[TD([subQ51])],"derivedFrom":makeQuery(id+"F25.boolean.opBoolean","SPLIT",FACE,{"disambiguationData":[TD([subQ51])],"derivedFrom":makeQuery(id+"F24.boolean.opBoolean","SPLIT",FACE,{"disambiguationData":[TD([subQ51])],"derivedFrom":makeQuery(id+"F1.opRevolve","SWEPT_FACE",FACE,{"disambiguationData":[OSD([sQuery(id+"F0.wireOp",EDGE,"E4")])]})})})})})})})})})],"blendedInto":[makeQuery(id+"F40.boolean.opBoolean","SPLIT",FACE,{"disambiguationData":[TD([subQ0])],"derivedFrom":makeQuery(id+"F30.boolean.opBoolean","SPLIT",FACE,{"disambiguationData":[TD([subQ12])],"derivedFrom":makeQuery(id+"F29.boolean.opBoolean","SPLIT",FACE,{"disambiguationData":[TD([subQ51])],"derivedFrom":makeQuery(id+"F28.boolean.opBoolean","SPLIT",FACE,{"disambiguationData":[TD([subQ51])],"derivedFrom":makeQuery(id+"F27.boolean.opBoolean","SPLIT",FACE,{"disambiguationData":[TD([subQ51])],"derivedFrom":makeQuery(id+"F26.boolean.opBoolean","SPLIT",FACE,{"disambiguationData":[TD([subQ51])],"derivedFrom":makeQuery(id+"F25.boolean.opBoolean","SPLIT",FACE,{"disambiguationData":[TD([subQ51])],"derivedFrom":makeQuery(id+"F24.boolean.opBoolean","SPLIT",FACE,{"disambiguationData":[TD([subQ51])],"derivedFrom":makeQuery(id+"F1.opRevolve","SWEPT_FACE",FACE,{"disambiguationData":[OSD([sQuery(id+"F0.wireOp",EDGE,"E4")])]})})})})})})})})})]});}
            var Q27;
            {var subQ0=makeQuery(id+"F1.opRevolve","SWEPT_FACE",FACE,{"disambiguationData":[OSD([sQuery(id+"F0.wireOp",EDGE,"E3")])]});var subQ5=sQuery(id+"F3.wireOp",EDGE,"E20.14.3");var subQ6=sQuery(id+"F3.wireOp",EDGE,"E20.14.2");var subQ7=sQuery(id+"F3.wireOp",EDGE,"E20.14.1");var subQ8=makeQuery(id+"F29.opLoft","SWEPT_FACE",FACE,{"disambiguationData":[OSD([subQ7,subQ6,subQ5,sQuery(id+"F22.wireOp",EDGE,"E28.6.0"),sQuery(id+"F22.wireOp",EDGE,"E28.6.2"),sQuery(id+"F22.wireOp",EDGE,"E28.6.3")])]});var subQ9=makeQuery(id+"F40.opExtrude","CAP_FACE",FACE,{"disambiguationData":[OSD([sQuery(id+"F39.wireOp",EDGE,"E29"),sQuery(id+"F39.wireOp",EDGE,"E30")])],"isStart":true});var subQ13=sQuery(id+"F4.wireOp",EDGE,"E26.14.3");var subQ14=sQuery(id+"F4.wireOp",EDGE,"E26.14.2");var subQ15=makeQuery(id+"F7.opLoft","SWEPT_FACE",FACE,{"disambiguationData":[OSD([subQ7,subQ6,subQ5,sQuery(id+"F4.wireOp",EDGE,"E26.14.1"),subQ14,subQ13])]});var subQ49=sQuery(id+"F3.wireOp",EDGE,"E18.bottom");var subQ52=makeQuery(id+"F5.opLoft","CAP_FACE",FACE,{"disambiguationData":[OSD([makeQuery(id+"F3.imprint","IMPRINT",FACE,{"disambiguationData":[TD([[makeQuery(id+"F3.imprint","IMPRINT",EDGE,{"derivedFrom":subQ49}),1.0]])]})])],"isStart":true});Q27=makeQuery(id+"F44.opFillet","BLEND_EDGE",EDGE,{"blendedFrom":[makeQuery(id+"F40.boolean.opBoolean","INTERSECT",EDGE,{"derivedFrom":[subQ8,subQ9]}),makeQuery(id+"F40.boolean.opBoolean","SPLIT",FACE,{"disambiguationData":[TD([subQ0])],"derivedFrom":makeQuery(id+"F29.boolean.opBoolean","SPLIT",FACE,{"disambiguationData":[TD([subQ15])],"derivedFrom":makeQuery(id+"F28.boolean.opBoolean","SPLIT",FACE,{"disambiguationData":[TD([subQ52])],"derivedFrom":makeQuery(id+"F27.boolean.opBoolean","SPLIT",FACE,{"disambiguationData":[TD([subQ52])],"derivedFrom":makeQuery(id+"F26.boolean.opBoolean","SPLIT",FACE,{"disambiguationData":[TD([subQ52])],"derivedFrom":makeQuery(id+"F25.boolean.opBoolean","SPLIT",FACE,{"disambiguationData":[TD([subQ52])],"derivedFrom":makeQuery(id+"F24.boolean.opBoolean","SPLIT",FACE,{"disambiguationData":[TD([subQ52])],"derivedFrom":makeQuery(id+"F1.opRevolve","SWEPT_FACE",FACE,{"disambiguationData":[OSD([sQuery(id+"F0.wireOp",EDGE,"E4")])]})})})})})})})})],"blendedInto":[makeQuery(id+"F40.boolean.opBoolean","SPLIT",FACE,{"disambiguationData":[TD([subQ0])],"derivedFrom":makeQuery(id+"F29.boolean.opBoolean","SPLIT",FACE,{"disambiguationData":[TD([subQ15])],"derivedFrom":makeQuery(id+"F28.boolean.opBoolean","SPLIT",FACE,{"disambiguationData":[TD([subQ52])],"derivedFrom":makeQuery(id+"F27.boolean.opBoolean","SPLIT",FACE,{"disambiguationData":[TD([subQ52])],"derivedFrom":makeQuery(id+"F26.boolean.opBoolean","SPLIT",FACE,{"disambiguationData":[TD([subQ52])],"derivedFrom":makeQuery(id+"F25.boolean.opBoolean","SPLIT",FACE,{"disambiguationData":[TD([subQ52])],"derivedFrom":makeQuery(id+"F24.boolean.opBoolean","SPLIT",FACE,{"disambiguationData":[TD([subQ52])],"derivedFrom":makeQuery(id+"F1.opRevolve","SWEPT_FACE",FACE,{"disambiguationData":[OSD([sQuery(id+"F0.wireOp",EDGE,"E4")])]})})})})})})})})]});}
            var Q28;
            {var subQ0=makeQuery(id+"F1.opRevolve","SWEPT_FACE",FACE,{"disambiguationData":[OSD([sQuery(id+"F0.wireOp",EDGE,"E3")])]});var subQ5=sQuery(id+"F3.wireOp",EDGE,"E20.13.3");var subQ6=sQuery(id+"F3.wireOp",EDGE,"E20.13.2");var subQ7=sQuery(id+"F3.wireOp",EDGE,"E20.13.1");var subQ8=makeQuery(id+"F28.opLoft","SWEPT_FACE",FACE,{"disambiguationData":[OSD([subQ7,subQ6,subQ5,sQuery(id+"F22.wireOp",EDGE,"E28.5.0"),sQuery(id+"F22.wireOp",EDGE,"E28.5.2"),sQuery(id+"F22.wireOp",EDGE,"E28.5.3")])]});var subQ9=makeQuery(id+"F40.opExtrude","CAP_FACE",FACE,{"disambiguationData":[OSD([sQuery(id+"F39.wireOp",EDGE,"E29"),sQuery(id+"F39.wireOp",EDGE,"E30")])],"isStart":true});var subQ13=sQuery(id+"F4.wireOp",EDGE,"E26.13.3");var subQ14=sQuery(id+"F4.wireOp",EDGE,"E26.13.2");var subQ15=makeQuery(id+"F8.opLoft","SWEPT_FACE",FACE,{"disambiguationData":[OSD([subQ7,subQ6,subQ5,sQuery(id+"F4.wireOp",EDGE,"E26.13.1"),subQ14,subQ13])]});var subQ57=sQuery(id+"F3.wireOp",EDGE,"E18.bottom");var subQ60=makeQuery(id+"F5.opLoft","CAP_FACE",FACE,{"disambiguationData":[OSD([makeQuery(id+"F3.imprint","IMPRINT",FACE,{"disambiguationData":[TD([[makeQuery(id+"F3.imprint","IMPRINT",EDGE,{"derivedFrom":subQ57}),1.0]])]})])],"isStart":true});Q28=makeQuery(id+"F44.opFillet","BLEND_EDGE",EDGE,{"blendedFrom":[makeQuery(id+"F40.boolean.opBoolean","INTERSECT",EDGE,{"derivedFrom":[subQ8,subQ9]}),makeQuery(id+"F40.boolean.opBoolean","SPLIT",FACE,{"disambiguationData":[TD([subQ0])],"derivedFrom":makeQuery(id+"F28.boolean.opBoolean","SPLIT",FACE,{"disambiguationData":[TD([subQ15])],"derivedFrom":makeQuery(id+"F27.boolean.opBoolean","SPLIT",FACE,{"disambiguationData":[TD([subQ60])],"derivedFrom":makeQuery(id+"F26.boolean.opBoolean","SPLIT",FACE,{"disambiguationData":[TD([subQ60])],"derivedFrom":makeQuery(id+"F25.boolean.opBoolean","SPLIT",FACE,{"disambiguationData":[TD([subQ60])],"derivedFrom":makeQuery(id+"F24.boolean.opBoolean","SPLIT",FACE,{"disambiguationData":[TD([subQ60])],"derivedFrom":makeQuery(id+"F1.opRevolve","SWEPT_FACE",FACE,{"disambiguationData":[OSD([sQuery(id+"F0.wireOp",EDGE,"E4")])]})})})})})})})],"blendedInto":[makeQuery(id+"F40.boolean.opBoolean","SPLIT",FACE,{"disambiguationData":[TD([subQ0])],"derivedFrom":makeQuery(id+"F28.boolean.opBoolean","SPLIT",FACE,{"disambiguationData":[TD([subQ15])],"derivedFrom":makeQuery(id+"F27.boolean.opBoolean","SPLIT",FACE,{"disambiguationData":[TD([subQ60])],"derivedFrom":makeQuery(id+"F26.boolean.opBoolean","SPLIT",FACE,{"disambiguationData":[TD([subQ60])],"derivedFrom":makeQuery(id+"F25.boolean.opBoolean","SPLIT",FACE,{"disambiguationData":[TD([subQ60])],"derivedFrom":makeQuery(id+"F24.boolean.opBoolean","SPLIT",FACE,{"disambiguationData":[TD([subQ60])],"derivedFrom":makeQuery(id+"F1.opRevolve","SWEPT_FACE",FACE,{"disambiguationData":[OSD([sQuery(id+"F0.wireOp",EDGE,"E4")])]})})})})})})})]});}
            var Q29;
            {var subQ0=makeQuery(id+"F1.opRevolve","SWEPT_FACE",FACE,{"disambiguationData":[OSD([sQuery(id+"F0.wireOp",EDGE,"E3")])]});var subQ5=sQuery(id+"F3.wireOp",EDGE,"E20.12.3");var subQ6=sQuery(id+"F3.wireOp",EDGE,"E20.12.2");var subQ7=sQuery(id+"F3.wireOp",EDGE,"E20.12.1");var subQ8=makeQuery(id+"F27.opLoft","SWEPT_FACE",FACE,{"disambiguationData":[OSD([subQ7,subQ6,subQ5,sQuery(id+"F22.wireOp",EDGE,"E28.4.0"),sQuery(id+"F22.wireOp",EDGE,"E28.4.2"),sQuery(id+"F22.wireOp",EDGE,"E28.4.3")])]});var subQ9=makeQuery(id+"F40.opExtrude","CAP_FACE",FACE,{"disambiguationData":[OSD([sQuery(id+"F39.wireOp",EDGE,"E29"),sQuery(id+"F39.wireOp",EDGE,"E30")])],"isStart":true});var subQ13=sQuery(id+"F4.wireOp",EDGE,"E26.12.3");var subQ14=sQuery(id+"F4.wireOp",EDGE,"E26.12.2");var subQ15=makeQuery(id+"F9.opLoft","SWEPT_FACE",FACE,{"disambiguationData":[OSD([subQ7,subQ6,subQ5,sQuery(id+"F4.wireOp",EDGE,"E26.12.1"),subQ14,subQ13])]});var subQ75=sQuery(id+"F3.wireOp",EDGE,"E18.bottom");var subQ78=makeQuery(id+"F5.opLoft","CAP_FACE",FACE,{"disambiguationData":[OSD([makeQuery(id+"F3.imprint","IMPRINT",FACE,{"disambiguationData":[TD([[makeQuery(id+"F3.imprint","IMPRINT",EDGE,{"derivedFrom":subQ75}),1.0]])]})])],"isStart":true});Q29=makeQuery(id+"F44.opFillet","BLEND_EDGE",EDGE,{"blendedFrom":[makeQuery(id+"F40.boolean.opBoolean","INTERSECT",EDGE,{"derivedFrom":[subQ8,subQ9]}),makeQuery(id+"F40.boolean.opBoolean","SPLIT",FACE,{"disambiguationData":[TD([subQ0])],"derivedFrom":makeQuery(id+"F27.boolean.opBoolean","SPLIT",FACE,{"disambiguationData":[TD([subQ15])],"derivedFrom":makeQuery(id+"F26.boolean.opBoolean","SPLIT",FACE,{"disambiguationData":[TD([subQ78])],"derivedFrom":makeQuery(id+"F25.boolean.opBoolean","SPLIT",FACE,{"disambiguationData":[TD([subQ78])],"derivedFrom":makeQuery(id+"F24.boolean.opBoolean","SPLIT",FACE,{"disambiguationData":[TD([subQ78])],"derivedFrom":makeQuery(id+"F1.opRevolve","SWEPT_FACE",FACE,{"disambiguationData":[OSD([sQuery(id+"F0.wireOp",EDGE,"E4")])]})})})})})})],"blendedInto":[makeQuery(id+"F40.boolean.opBoolean","SPLIT",FACE,{"disambiguationData":[TD([subQ0])],"derivedFrom":makeQuery(id+"F27.boolean.opBoolean","SPLIT",FACE,{"disambiguationData":[TD([subQ15])],"derivedFrom":makeQuery(id+"F26.boolean.opBoolean","SPLIT",FACE,{"disambiguationData":[TD([subQ78])],"derivedFrom":makeQuery(id+"F25.boolean.opBoolean","SPLIT",FACE,{"disambiguationData":[TD([subQ78])],"derivedFrom":makeQuery(id+"F24.boolean.opBoolean","SPLIT",FACE,{"disambiguationData":[TD([subQ78])],"derivedFrom":makeQuery(id+"F1.opRevolve","SWEPT_FACE",FACE,{"disambiguationData":[OSD([sQuery(id+"F0.wireOp",EDGE,"E4")])]})})})})})})]});}
            var Q30;
            {var subQ0=makeQuery(id+"F1.opRevolve","SWEPT_FACE",FACE,{"disambiguationData":[OSD([sQuery(id+"F0.wireOp",EDGE,"E3")])]});var subQ5=sQuery(id+"F3.wireOp",EDGE,"E20.11.3");var subQ6=sQuery(id+"F3.wireOp",EDGE,"E20.11.2");var subQ7=sQuery(id+"F3.wireOp",EDGE,"E20.11.1");var subQ8=makeQuery(id+"F26.opLoft","SWEPT_FACE",FACE,{"disambiguationData":[OSD([subQ7,subQ6,subQ5,sQuery(id+"F22.wireOp",EDGE,"E28.3.0"),sQuery(id+"F22.wireOp",EDGE,"E28.3.2"),sQuery(id+"F22.wireOp",EDGE,"E28.3.3")])]});var subQ9=makeQuery(id+"F40.opExtrude","CAP_FACE",FACE,{"disambiguationData":[OSD([sQuery(id+"F39.wireOp",EDGE,"E29"),sQuery(id+"F39.wireOp",EDGE,"E30")])],"isStart":true});var subQ13=sQuery(id+"F4.wireOp",EDGE,"E26.11.3");var subQ14=sQuery(id+"F4.wireOp",EDGE,"E26.11.2");var subQ15=makeQuery(id+"F10.opLoft","SWEPT_FACE",FACE,{"disambiguationData":[OSD([subQ7,subQ6,subQ5,sQuery(id+"F4.wireOp",EDGE,"E26.11.1"),subQ14,subQ13])]});var subQ80=sQuery(id+"F3.wireOp",EDGE,"E18.bottom");var subQ83=makeQuery(id+"F5.opLoft","CAP_FACE",FACE,{"disambiguationData":[OSD([makeQuery(id+"F3.imprint","IMPRINT",FACE,{"disambiguationData":[TD([[makeQuery(id+"F3.imprint","IMPRINT",EDGE,{"derivedFrom":subQ80}),1.0]])]})])],"isStart":true});Q30=makeQuery(id+"F44.opFillet","BLEND_EDGE",EDGE,{"blendedFrom":[makeQuery(id+"F40.boolean.opBoolean","INTERSECT",EDGE,{"derivedFrom":[subQ8,subQ9]}),makeQuery(id+"F40.boolean.opBoolean","SPLIT",FACE,{"disambiguationData":[TD([subQ0])],"derivedFrom":makeQuery(id+"F26.boolean.opBoolean","SPLIT",FACE,{"disambiguationData":[TD([subQ15])],"derivedFrom":makeQuery(id+"F25.boolean.opBoolean","SPLIT",FACE,{"disambiguationData":[TD([subQ83])],"derivedFrom":makeQuery(id+"F24.boolean.opBoolean","SPLIT",FACE,{"disambiguationData":[TD([subQ83])],"derivedFrom":makeQuery(id+"F1.opRevolve","SWEPT_FACE",FACE,{"disambiguationData":[OSD([sQuery(id+"F0.wireOp",EDGE,"E4")])]})})})})})],"blendedInto":[makeQuery(id+"F40.boolean.opBoolean","SPLIT",FACE,{"disambiguationData":[TD([subQ0])],"derivedFrom":makeQuery(id+"F26.boolean.opBoolean","SPLIT",FACE,{"disambiguationData":[TD([subQ15])],"derivedFrom":makeQuery(id+"F25.boolean.opBoolean","SPLIT",FACE,{"disambiguationData":[TD([subQ83])],"derivedFrom":makeQuery(id+"F24.boolean.opBoolean","SPLIT",FACE,{"disambiguationData":[TD([subQ83])],"derivedFrom":makeQuery(id+"F1.opRevolve","SWEPT_FACE",FACE,{"disambiguationData":[OSD([sQuery(id+"F0.wireOp",EDGE,"E4")])]})})})})})]});}
            var Q31;
            {var subQ0=makeQuery(id+"F1.opRevolve","SWEPT_FACE",FACE,{"disambiguationData":[OSD([sQuery(id+"F0.wireOp",EDGE,"E3")])]});var subQ5=sQuery(id+"F3.wireOp",EDGE,"E20.10.3");var subQ6=sQuery(id+"F3.wireOp",EDGE,"E20.10.2");var subQ7=sQuery(id+"F3.wireOp",EDGE,"E20.10.1");var subQ8=makeQuery(id+"F25.opLoft","SWEPT_FACE",FACE,{"disambiguationData":[OSD([subQ7,subQ6,subQ5,sQuery(id+"F22.wireOp",EDGE,"E28.2.0"),sQuery(id+"F22.wireOp",EDGE,"E28.2.2"),sQuery(id+"F22.wireOp",EDGE,"E28.2.3")])]});var subQ9=makeQuery(id+"F40.opExtrude","CAP_FACE",FACE,{"disambiguationData":[OSD([sQuery(id+"F39.wireOp",EDGE,"E29"),sQuery(id+"F39.wireOp",EDGE,"E30")])],"isStart":true});var subQ12=sQuery(id+"F4.wireOp",EDGE,"E26.10.3");var subQ13=sQuery(id+"F4.wireOp",EDGE,"E26.10.2");var subQ14=makeQuery(id+"F11.opLoft","SWEPT_FACE",FACE,{"disambiguationData":[OSD([subQ7,subQ6,subQ5,sQuery(id+"F4.wireOp",EDGE,"E26.10.1"),subQ13,subQ12])]});var subQ90=sQuery(id+"F3.wireOp",EDGE,"E18.bottom");Q31=makeQuery(id+"F44.opFillet","BLEND_EDGE",EDGE,{"blendedFrom":[makeQuery(id+"F40.boolean.opBoolean","INTERSECT",EDGE,{"derivedFrom":[subQ8,subQ9]}),makeQuery(id+"F40.boolean.opBoolean","SPLIT",FACE,{"disambiguationData":[TD([subQ0])],"derivedFrom":makeQuery(id+"F25.boolean.opBoolean","SPLIT",FACE,{"disambiguationData":[TD([subQ14])],"derivedFrom":makeQuery(id+"F24.boolean.opBoolean","SPLIT",FACE,{"disambiguationData":[TD([makeQuery(id+"F5.opLoft","CAP_FACE",FACE,{"disambiguationData":[OSD([makeQuery(id+"F3.imprint","IMPRINT",FACE,{"disambiguationData":[TD([[makeQuery(id+"F3.imprint","IMPRINT",EDGE,{"derivedFrom":subQ90}),1.0]])]})])],"isStart":true})])],"derivedFrom":makeQuery(id+"F1.opRevolve","SWEPT_FACE",FACE,{"disambiguationData":[OSD([sQuery(id+"F0.wireOp",EDGE,"E4")])]})})})})],"blendedInto":[makeQuery(id+"F40.boolean.opBoolean","SPLIT",FACE,{"disambiguationData":[TD([subQ0])],"derivedFrom":makeQuery(id+"F25.boolean.opBoolean","SPLIT",FACE,{"disambiguationData":[TD([subQ14])],"derivedFrom":makeQuery(id+"F24.boolean.opBoolean","SPLIT",FACE,{"disambiguationData":[TD([makeQuery(id+"F5.opLoft","CAP_FACE",FACE,{"disambiguationData":[OSD([makeQuery(id+"F3.imprint","IMPRINT",FACE,{"disambiguationData":[TD([[makeQuery(id+"F3.imprint","IMPRINT",EDGE,{"derivedFrom":subQ90}),1.0]])]})])],"isStart":true})])],"derivedFrom":makeQuery(id+"F1.opRevolve","SWEPT_FACE",FACE,{"disambiguationData":[OSD([sQuery(id+"F0.wireOp",EDGE,"E4")])]})})})})]});}
            var Q32;
            {var subQ0=makeQuery(id+"F1.opRevolve","SWEPT_FACE",FACE,{"disambiguationData":[OSD([sQuery(id+"F0.wireOp",EDGE,"E3")])]});var subQ1=sQuery(id+"F3.wireOp",EDGE,"E20.9.3");var subQ2=sQuery(id+"F3.wireOp",EDGE,"E20.9.2");var subQ3=sQuery(id+"F3.wireOp",EDGE,"E20.9.1");var subQ4=makeQuery(id+"F24.opLoft","SWEPT_FACE",FACE,{"disambiguationData":[OSD([subQ3,subQ2,subQ1,sQuery(id+"F22.wireOp",EDGE,"E28.1.0"),sQuery(id+"F22.wireOp",EDGE,"E28.1.2"),sQuery(id+"F22.wireOp",EDGE,"E28.1.3")])]});var subQ9=makeQuery(id+"F40.opExtrude","CAP_FACE",FACE,{"disambiguationData":[OSD([sQuery(id+"F39.wireOp",EDGE,"E29"),sQuery(id+"F39.wireOp",EDGE,"E30")])],"isStart":true});Q32=makeQuery(id+"F44.opFillet","BLEND_EDGE",EDGE,{"blendedFrom":[makeQuery(id+"F40.boolean.opBoolean","INTERSECT",EDGE,{"derivedFrom":[subQ4,subQ9]}),makeQuery(id+"F40.boolean.opBoolean","SPLIT",FACE,{"disambiguationData":[TD([subQ0])],"derivedFrom":makeQuery(id+"F24.boolean.opBoolean","SPLIT",FACE,{"disambiguationData":[TD([makeQuery(id+"F12.opLoft","SWEPT_FACE",FACE,{"disambiguationData":[OSD([subQ3,subQ2,subQ1,sQuery(id+"F4.wireOp",EDGE,"E26.9.1"),sQuery(id+"F4.wireOp",EDGE,"E26.9.2"),sQuery(id+"F4.wireOp",EDGE,"E26.9.3")])]})])],"derivedFrom":makeQuery(id+"F1.opRevolve","SWEPT_FACE",FACE,{"disambiguationData":[OSD([sQuery(id+"F0.wireOp",EDGE,"E4")])]})})})],"blendedInto":[makeQuery(id+"F40.boolean.opBoolean","SPLIT",FACE,{"disambiguationData":[TD([subQ0])],"derivedFrom":makeQuery(id+"F24.boolean.opBoolean","SPLIT",FACE,{"disambiguationData":[TD([makeQuery(id+"F12.opLoft","SWEPT_FACE",FACE,{"disambiguationData":[OSD([subQ3,subQ2,subQ1,sQuery(id+"F4.wireOp",EDGE,"E26.9.1"),sQuery(id+"F4.wireOp",EDGE,"E26.9.2"),sQuery(id+"F4.wireOp",EDGE,"E26.9.3")])]})])],"derivedFrom":makeQuery(id+"F1.opRevolve","SWEPT_FACE",FACE,{"disambiguationData":[OSD([sQuery(id+"F0.wireOp",EDGE,"E4")])]})})})]});}
            fillet(context, id + "F48", {"entities" : qUnion([Q0, Q1, Q2, Q3, Q4, Q5, Q6, Q7, Q8, Q9, Q10, Q11, Q12, Q13, Q14, Q15, Q16, Q17, Q18, Q19, Q20, Q21, Q22, Q23, Q24, Q25, Q26, Q27, Q28, Q29, Q30, Q31, Q32]), "radius" : 2 * mm, "tangentPropagation" : true, "allowEdgeOverflow" : false});
        }
        {
            var Q0;
            {var subQ0=sQuery(id+"F41.wireOp",EDGE,"E34");var subQ1=sQuery(id+"F41.wireOp",EDGE,"E32");Q0=makeQuery(id+"F42.boolean.opBoolean","INTERSECT",EDGE,{"derivedFrom":[makeQuery(id+"F35.opLoft","SWEPT_FACE",FACE,{"disambiguationData":[OSD([sQuery(id+"F3.wireOp",EDGE,"E20.4.0"),sQuery(id+"F3.wireOp",EDGE,"E20.4.1"),sQuery(id+"F3.wireOp",EDGE,"E20.4.3"),sQuery(id+"F22.wireOp",EDGE,"E28.12.1"),sQuery(id+"F22.wireOp",EDGE,"E28.12.2"),sQuery(id+"F22.wireOp",EDGE,"E28.12.3")])]}),makeQuery(id+"F42.opRevolve","SWEPT_FACE",FACE,{"disambiguationData":[OSD([subQ1]),TDD([makeQuery(id+"F41.imprint","IMPRINT",EDGE,{"disambiguationData":[TD([[makeQuery(id+"F41.imprint","INTERSECT",VERTEX,{"disambiguationData":[OD(0.0)],"derivedFrom":[subQ1,subQ0]}),-1.0]])],"derivedFrom":subQ1})])]})]});}
            var Q1;
            {var subQ0=sQuery(id+"F22.wireOp",EDGE,"E28.12.3");var subQ1=sQuery(id+"F22.wireOp",EDGE,"E28.12.2");var subQ2=sQuery(id+"F22.wireOp",EDGE,"E28.12.0");var subQ3=sQuery(id+"F3.wireOp",EDGE,"E20.4.3");var subQ4=sQuery(id+"F3.wireOp",EDGE,"E20.4.1");var subQ5=makeQuery(id+"F35.opLoft","SWEPT_FACE",FACE,{"disambiguationData":[OSD([subQ4,sQuery(id+"F3.wireOp",EDGE,"E20.4.2"),subQ3,subQ2,subQ1,subQ0])]});var subQ6=sQuery(id+"F22.wireOp",EDGE,"E28.12.1");var subQ7=sQuery(id+"F41.wireOp",EDGE,"E34");var subQ8=sQuery(id+"F41.wireOp",EDGE,"E32");Q1=makeQuery(id+"F44.opFillet","BLEND_EDGE",EDGE,{"blendedFrom":[makeQuery(id+"F40.boolean.opBoolean","INTERSECT",EDGE,{"derivedFrom":[subQ5,makeQuery(id+"F40.opExtrude","CAP_FACE",FACE,{"disambiguationData":[OSD([sQuery(id+"F39.wireOp",EDGE,"E29"),sQuery(id+"F39.wireOp",EDGE,"E30")])],"isStart":true})]}),makeQuery(id+"F42.boolean.opBoolean","COPY",FACE,{"disambiguationData":[TD([makeQuery(id+"F35.opLoft","SWEPT_FACE",FACE,{"disambiguationData":[OSD([sQuery(id+"F3.wireOp",EDGE,"E20.4.0"),subQ4,subQ3,subQ6,subQ1,subQ0])]})])],"derivedFrom":makeQuery(id+"F42.opRevolve","SWEPT_FACE",FACE,{"disambiguationData":[OSD([subQ8]),TDD([makeQuery(id+"F41.imprint","IMPRINT",EDGE,{"disambiguationData":[TD([[makeQuery(id+"F41.imprint","INTERSECT",VERTEX,{"disambiguationData":[OD(0.0)],"derivedFrom":[subQ8,subQ7]}),-1.0]])],"derivedFrom":subQ8})])]})})],"blendedInto":[makeQuery(id+"F42.boolean.opBoolean","COPY",FACE,{"disambiguationData":[TD([makeQuery(id+"F35.opLoft","SWEPT_FACE",FACE,{"disambiguationData":[OSD([sQuery(id+"F3.wireOp",EDGE,"E20.4.0"),subQ4,subQ3,subQ6,subQ1,subQ0])]})])],"derivedFrom":makeQuery(id+"F42.opRevolve","SWEPT_FACE",FACE,{"disambiguationData":[OSD([subQ8]),TDD([makeQuery(id+"F41.imprint","IMPRINT",EDGE,{"disambiguationData":[TD([[makeQuery(id+"F41.imprint","INTERSECT",VERTEX,{"disambiguationData":[OD(0.0)],"derivedFrom":[subQ8,subQ7]}),-1.0]])],"derivedFrom":subQ8})])]})})]});}
            var Q2;
            {var subQ0=sQuery(id+"F41.wireOp",EDGE,"E37");var subQ1=makeQuery(id+"F42.opRevolve","SWEPT_FACE",FACE,{"disambiguationData":[OSD([subQ0])]});var subQ2=makeQuery(id+"F40.opExtrude","CAP_FACE",FACE,{"disambiguationData":[OSD([sQuery(id+"F39.wireOp",EDGE,"E29"),sQuery(id+"F39.wireOp",EDGE,"E30")])],"isStart":true});var subQ3=sQuery(id+"F22.wireOp",EDGE,"E28.15.3");var subQ4=sQuery(id+"F22.wireOp",EDGE,"E28.15.2");var subQ5=sQuery(id+"F3.wireOp",EDGE,"E20.7.3");var subQ7=sQuery(id+"F3.wireOp",EDGE,"E20.7.1");var subQ8=sQuery(id+"F3.wireOp",EDGE,"E20.7.0");var subQ9=sQuery(id+"F41.wireOp",EDGE,"E38");var subQ10=makeQuery(id+"F42.opRevolve","SWEPT_FACE",FACE,{"disambiguationData":[OSD([subQ9])]});var subQ11=makeQuery(id+"F42.opRevolve","SWEPT_EDGE",EDGE,{"disambiguationData":[OSD([subQ0,subQ9])]});var subQ12=sQuery(id+"F22.wireOp",EDGE,"E28.14.3");var subQ13=sQuery(id+"F22.wireOp",EDGE,"E28.14.2");var subQ14=sQuery(id+"F3.wireOp",EDGE,"E20.6.3");var subQ15=sQuery(id+"F3.wireOp",EDGE,"E20.6.1");var subQ16=sQuery(id+"F3.wireOp",EDGE,"E20.6.0");var subQ18=sQuery(id+"F22.wireOp",EDGE,"E28.13.3");var subQ19=sQuery(id+"F22.wireOp",EDGE,"E28.13.2");var subQ20=sQuery(id+"F3.wireOp",EDGE,"E20.5.3");var subQ22=sQuery(id+"F3.wireOp",EDGE,"E20.5.1");var subQ23=sQuery(id+"F3.wireOp",EDGE,"E20.5.0");var subQ24=sQuery(id+"F22.wireOp",EDGE,"E28.12.3");var subQ25=sQuery(id+"F22.wireOp",EDGE,"E28.12.2");var subQ26=sQuery(id+"F3.wireOp",EDGE,"E20.4.3");var subQ28=sQuery(id+"F3.wireOp",EDGE,"E20.4.1");var subQ30=sQuery(id+"F3.wireOp",EDGE,"E20.4.0");var subQ31=makeQuery(id+"F35.opLoft","SWEPT_FACE",FACE,{"disambiguationData":[OSD([subQ30,subQ28,subQ26,sQuery(id+"F22.wireOp",EDGE,"E28.12.1"),subQ25,subQ24])]});var subQ32=sQuery(id+"F22.wireOp",EDGE,"E28.11.3");var subQ33=sQuery(id+"F22.wireOp",EDGE,"E28.11.2");var subQ34=sQuery(id+"F3.wireOp",EDGE,"E20.3.3");var subQ36=sQuery(id+"F3.wireOp",EDGE,"E20.3.1");var subQ37=sQuery(id+"F3.wireOp",EDGE,"E20.3.0");var subQ38=makeQuery(id+"F34.opLoft","SWEPT_FACE",FACE,{"disambiguationData":[OSD([subQ37,subQ36,subQ34,sQuery(id+"F22.wireOp",EDGE,"E28.11.1"),subQ33,subQ32])]});var subQ39=sQuery(id+"F22.wireOp",EDGE,"E28.10.3");var subQ40=sQuery(id+"F22.wireOp",EDGE,"E28.10.2");var subQ41=sQuery(id+"F3.wireOp",EDGE,"E20.2.3");var subQ43=sQuery(id+"F3.wireOp",EDGE,"E20.2.1");var subQ44=sQuery(id+"F3.wireOp",EDGE,"E20.2.0");var subQ45=makeQuery(id+"F33.opLoft","SWEPT_FACE",FACE,{"disambiguationData":[OSD([subQ44,subQ43,subQ41,sQuery(id+"F22.wireOp",EDGE,"E28.10.1"),subQ40,subQ39])]});var subQ46=sQuery(id+"F22.wireOp",EDGE,"E28.9.3");var subQ47=sQuery(id+"F22.wireOp",EDGE,"E28.9.2");var subQ48=sQuery(id+"F3.wireOp",EDGE,"E20.1.3");var subQ50=sQuery(id+"F3.wireOp",EDGE,"E20.1.1");var subQ51=sQuery(id+"F3.wireOp",EDGE,"E20.1.0");var subQ52=makeQuery(id+"F32.opLoft","SWEPT_FACE",FACE,{"disambiguationData":[OSD([subQ51,subQ50,subQ48,sQuery(id+"F22.wireOp",EDGE,"E28.9.1"),subQ47,subQ46])]});var subQ53=sQuery(id+"F22.wireOp",EDGE,"E28.8.3");var subQ54=sQuery(id+"F22.wireOp",EDGE,"E28.8.2");var subQ56=sQuery(id+"F3.wireOp",EDGE,"E18.top");var subQ57=sQuery(id+"F3.wireOp",EDGE,"E18.bottom");var subQ58=sQuery(id+"F3.wireOp",EDGE,"E18.left");var subQ59=makeQuery(id+"F31.opLoft","SWEPT_FACE",FACE,{"disambiguationData":[OSD([subQ57,subQ56,subQ58,sQuery(id+"F22.wireOp",EDGE,"E28.8.1"),subQ54,subQ53])]});var subQ60=sQuery(id+"F22.wireOp",EDGE,"E28.7.3");var subQ61=sQuery(id+"F22.wireOp",EDGE,"E28.7.2");var subQ62=sQuery(id+"F3.wireOp",EDGE,"E20.15.3");var subQ63=sQuery(id+"F3.wireOp",EDGE,"E20.15.1");var subQ64=sQuery(id+"F3.wireOp",EDGE,"E20.15.0");var subQ65=makeQuery(id+"F30.opLoft","SWEPT_FACE",FACE,{"disambiguationData":[OSD([subQ64,subQ63,subQ62,sQuery(id+"F22.wireOp",EDGE,"E28.7.1"),subQ61,subQ60])]});var subQ67=sQuery(id+"F22.wireOp",EDGE,"E28.6.3");var subQ68=sQuery(id+"F22.wireOp",EDGE,"E28.6.2");var subQ69=sQuery(id+"F3.wireOp",EDGE,"E20.14.3");var subQ71=sQuery(id+"F3.wireOp",EDGE,"E20.14.1");var subQ72=sQuery(id+"F3.wireOp",EDGE,"E20.14.0");var subQ73=makeQuery(id+"F29.opLoft","SWEPT_FACE",FACE,{"disambiguationData":[OSD([subQ72,subQ71,subQ69,sQuery(id+"F22.wireOp",EDGE,"E28.6.1"),subQ68,subQ67])]});var subQ74=sQuery(id+"F22.wireOp",EDGE,"E28.5.3");var subQ75=sQuery(id+"F22.wireOp",EDGE,"E28.5.2");var subQ76=sQuery(id+"F3.wireOp",EDGE,"E20.13.3");var subQ78=sQuery(id+"F3.wireOp",EDGE,"E20.13.1");var subQ79=sQuery(id+"F3.wireOp",EDGE,"E20.13.0");var subQ80=makeQuery(id+"F28.opLoft","SWEPT_FACE",FACE,{"disambiguationData":[OSD([subQ79,subQ78,subQ76,sQuery(id+"F22.wireOp",EDGE,"E28.5.1"),subQ75,subQ74])]});var subQ81=sQuery(id+"F22.wireOp",EDGE,"E28.4.3");var subQ82=sQuery(id+"F22.wireOp",EDGE,"E28.4.2");var subQ83=sQuery(id+"F3.wireOp",EDGE,"E20.12.3");var subQ85=sQuery(id+"F3.wireOp",EDGE,"E20.12.1");var subQ86=sQuery(id+"F3.wireOp",EDGE,"E20.12.0");var subQ87=makeQuery(id+"F27.opLoft","SWEPT_FACE",FACE,{"disambiguationData":[OSD([subQ86,subQ85,subQ83,sQuery(id+"F22.wireOp",EDGE,"E28.4.1"),subQ82,subQ81])]});var subQ88=sQuery(id+"F22.wireOp",EDGE,"E28.3.3");var subQ89=sQuery(id+"F22.wireOp",EDGE,"E28.3.2");var subQ90=sQuery(id+"F3.wireOp",EDGE,"E20.11.3");var subQ92=sQuery(id+"F3.wireOp",EDGE,"E20.11.1");var subQ93=sQuery(id+"F3.wireOp",EDGE,"E20.11.0");var subQ94=makeQuery(id+"F26.opLoft","SWEPT_FACE",FACE,{"disambiguationData":[OSD([subQ93,subQ92,subQ90,sQuery(id+"F22.wireOp",EDGE,"E28.3.1"),subQ89,subQ88])]});var subQ95=sQuery(id+"F22.wireOp",EDGE,"E28.2.3");var subQ96=sQuery(id+"F22.wireOp",EDGE,"E28.2.2");var subQ97=sQuery(id+"F3.wireOp",EDGE,"E20.10.3");var subQ98=sQuery(id+"F3.wireOp",EDGE,"E20.10.1");var subQ99=sQuery(id+"F3.wireOp",EDGE,"E20.10.0");var subQ100=makeQuery(id+"F25.opLoft","SWEPT_FACE",FACE,{"disambiguationData":[OSD([subQ99,subQ98,subQ97,sQuery(id+"F22.wireOp",EDGE,"E28.2.1"),subQ96,subQ95])]});var subQ102=sQuery(id+"F22.wireOp",EDGE,"E28.1.3");var subQ103=sQuery(id+"F22.wireOp",EDGE,"E28.1.2");var subQ104=sQuery(id+"F3.wireOp",EDGE,"E20.9.3");var subQ105=sQuery(id+"F3.wireOp",EDGE,"E20.9.1");var subQ106=sQuery(id+"F3.wireOp",EDGE,"E20.9.0");var subQ107=makeQuery(id+"F24.opLoft","SWEPT_FACE",FACE,{"disambiguationData":[OSD([subQ106,subQ105,subQ104,sQuery(id+"F22.wireOp",EDGE,"E28.1.1"),subQ103,subQ102])]});var subQ108=sQuery(id+"F22.wireOp",EDGE,"E27.top");var subQ109=sQuery(id+"F22.wireOp",EDGE,"E27.bottom");var subQ110=sQuery(id+"F3.wireOp",EDGE,"E20.8.3");var subQ112=sQuery(id+"F3.wireOp",EDGE,"E20.8.1");var subQ116=makeQuery(id+"F42.boolean.opBoolean","COPY",FACE,{"disambiguationData":[TD([subQ31])],"derivedFrom":subQ10});var subQ125=makeQuery(id+"F14.opLoft","CAP_FACE",FACE,{"disambiguationData":[OSD([makeQuery(id+"F3.imprint","IMPRINT",FACE,{"disambiguationData":[TD([[makeQuery(id+"F3.imprint","IMPRINT",EDGE,{"derivedFrom":subQ8}),-1.0]])]})])],"isStart":true});var subQ159=makeQuery(id+"F5.opLoft","CAP_FACE",FACE,{"disambiguationData":[OSD([makeQuery(id+"F3.imprint","IMPRINT",FACE,{"disambiguationData":[TD([[makeQuery(id+"F3.imprint","IMPRINT",EDGE,{"derivedFrom":subQ57}),1.0]])]})])],"isStart":true});var subQ188=makeQuery(id+"F35.boolean.opBoolean","INTERSECT",EDGE,{"derivedFrom":[makeQuery(id+"F34.boolean.opBoolean","SPLIT",FACE,{"disambiguationData":[TD([subQ125])],"derivedFrom":makeQuery(id+"F33.boolean.opBoolean","SPLIT",FACE,{"disambiguationData":[TD([subQ125])],"derivedFrom":makeQuery(id+"F32.boolean.opBoolean","SPLIT",FACE,{"disambiguationData":[TD([subQ125])],"derivedFrom":makeQuery(id+"F31.boolean.opBoolean","SPLIT",FACE,{"disambiguationData":[TD([subQ125])],"derivedFrom":makeQuery(id+"F30.boolean.opBoolean","SPLIT",FACE,{"disambiguationData":[TD([subQ159])],"derivedFrom":makeQuery(id+"F29.boolean.opBoolean","SPLIT",FACE,{"disambiguationData":[TD([subQ159])],"derivedFrom":makeQuery(id+"F28.boolean.opBoolean","SPLIT",FACE,{"disambiguationData":[TD([subQ159])],"derivedFrom":makeQuery(id+"F27.boolean.opBoolean","SPLIT",FACE,{"disambiguationData":[TD([subQ159])],"derivedFrom":makeQuery(id+"F26.boolean.opBoolean","SPLIT",FACE,{"disambiguationData":[TD([subQ159])],"derivedFrom":makeQuery(id+"F25.boolean.opBoolean","SPLIT",FACE,{"disambiguationData":[TD([subQ159])],"derivedFrom":makeQuery(id+"F24.boolean.opBoolean","SPLIT",FACE,{"disambiguationData":[TD([subQ159])],"derivedFrom":makeQuery(id+"F1.opRevolve","SWEPT_FACE",FACE,{"disambiguationData":[OSD([sQuery(id+"F0.wireOp",EDGE,"E4")])]})})})})})})})})})})})}),subQ31]});Q2=makeQuery(id+"F48.opFillet","BLEND_EDGE",EDGE,{"blendedFrom":[makeQuery(id+"F47.opFillet","TWEAK_EDGE",EDGE,{"derivedFrom":[makeQuery(id+"F45.opFillet","BLEND_VERTEX",VERTEX,{"blendedFrom":[subQ188,subQ31,subQ116],"blendedInto":[subQ31,subQ116]}),makeQuery(id+"F45.opFillet","BLEND_VERTEX",VERTEX,{"blendedFrom":[subQ188,makeQuery(id+"F42.boolean.opBoolean","MERGE",FACE,{"derivedFrom":[subQ2,subQ1]}),subQ116],"blendedInto":[makeQuery(id+"F42.boolean.opBoolean","MERGE",FACE,{"derivedFrom":[subQ2,subQ1]}),subQ116]})]}),makeQuery(id+"F47.opFillet","BLEND_FACE",FACE,{"disambiguationData":[OSD([subQ0,subQ9]),TDD([makeQuery(id+"F42.boolean.opBoolean","COPY",EDGE,{"disambiguationData":[TD([makeQuery(id+"F23.opLoft","SWEPT_FACE",FACE,{"disambiguationData":[OSD([sQuery(id+"F3.wireOp",EDGE,"E20.8.0"),subQ112,subQ110,subQ109,subQ108,sQuery(id+"F22.wireOp",EDGE,"E27.right")])]})])],"derivedFrom":subQ11})])]}),makeQuery(id+"F47.opFillet","BLEND_FACE",FACE,{"disambiguationData":[OSD([subQ0,subQ9]),TDD([makeQuery(id+"F42.boolean.opBoolean","COPY",EDGE,{"disambiguationData":[TD([subQ107])],"derivedFrom":subQ11})])]}),makeQuery(id+"F47.opFillet","BLEND_FACE",FACE,{"disambiguationData":[OSD([subQ0,subQ9]),TDD([makeQuery(id+"F42.boolean.opBoolean","COPY",EDGE,{"disambiguationData":[TD([subQ100])],"derivedFrom":subQ11})])]}),makeQuery(id+"F47.opFillet","BLEND_FACE",FACE,{"disambiguationData":[OSD([subQ0,subQ9]),TDD([makeQuery(id+"F42.boolean.opBoolean","COPY",EDGE,{"disambiguationData":[TD([subQ94])],"derivedFrom":subQ11})])]}),makeQuery(id+"F47.opFillet","BLEND_FACE",FACE,{"disambiguationData":[OSD([subQ0,subQ9]),TDD([makeQuery(id+"F42.boolean.opBoolean","COPY",EDGE,{"disambiguationData":[TD([subQ87])],"derivedFrom":subQ11})])]}),makeQuery(id+"F47.opFillet","BLEND_FACE",FACE,{"disambiguationData":[OSD([subQ0,subQ9]),TDD([makeQuery(id+"F42.boolean.opBoolean","COPY",EDGE,{"disambiguationData":[TD([subQ80])],"derivedFrom":subQ11})])]}),makeQuery(id+"F47.opFillet","BLEND_FACE",FACE,{"disambiguationData":[OSD([subQ0,subQ9]),TDD([makeQuery(id+"F42.boolean.opBoolean","COPY",EDGE,{"disambiguationData":[TD([subQ73])],"derivedFrom":subQ11})])]}),makeQuery(id+"F47.opFillet","BLEND_FACE",FACE,{"disambiguationData":[OSD([subQ0,subQ9]),TDD([makeQuery(id+"F42.boolean.opBoolean","COPY",EDGE,{"disambiguationData":[TD([subQ65])],"derivedFrom":subQ11})])]}),makeQuery(id+"F47.opFillet","BLEND_FACE",FACE,{"disambiguationData":[OSD([subQ0,subQ9]),TDD([makeQuery(id+"F42.boolean.opBoolean","COPY",EDGE,{"disambiguationData":[TD([subQ59])],"derivedFrom":subQ11})])]}),makeQuery(id+"F47.opFillet","BLEND_FACE",FACE,{"disambiguationData":[OSD([subQ0,subQ9]),TDD([makeQuery(id+"F42.boolean.opBoolean","COPY",EDGE,{"disambiguationData":[TD([subQ52])],"derivedFrom":subQ11})])]}),makeQuery(id+"F47.opFillet","BLEND_FACE",FACE,{"disambiguationData":[OSD([subQ0,subQ9]),TDD([makeQuery(id+"F42.boolean.opBoolean","COPY",EDGE,{"disambiguationData":[TD([subQ45])],"derivedFrom":subQ11})])]}),makeQuery(id+"F47.opFillet","BLEND_FACE",FACE,{"disambiguationData":[OSD([subQ0,subQ9]),TDD([makeQuery(id+"F42.boolean.opBoolean","COPY",EDGE,{"disambiguationData":[TD([subQ38])],"derivedFrom":subQ11})])]}),makeQuery(id+"F47.opFillet","BLEND_FACE",FACE,{"disambiguationData":[OSD([subQ0,subQ9]),TDD([makeQuery(id+"F42.boolean.opBoolean","COPY",EDGE,{"disambiguationData":[TD([subQ31])],"derivedFrom":subQ11})])]}),makeQuery(id+"F47.opFillet","BLEND_FACE",FACE,{"disambiguationData":[OSD([subQ0,subQ9]),TDD([makeQuery(id+"F42.boolean.opBoolean","COPY",EDGE,{"disambiguationData":[TD([makeQuery(id+"F36.opLoft","SWEPT_FACE",FACE,{"disambiguationData":[OSD([subQ23,subQ22,subQ20,sQuery(id+"F22.wireOp",EDGE,"E28.13.1"),subQ19,subQ18])]})])],"derivedFrom":subQ11})])]}),makeQuery(id+"F47.opFillet","BLEND_FACE",FACE,{"disambiguationData":[OSD([subQ0,subQ9]),TDD([makeQuery(id+"F42.boolean.opBoolean","COPY",EDGE,{"disambiguationData":[TD([makeQuery(id+"F37.opLoft","SWEPT_FACE",FACE,{"disambiguationData":[OSD([subQ16,subQ15,subQ14,sQuery(id+"F22.wireOp",EDGE,"E28.14.1"),subQ13,subQ12])]})])],"derivedFrom":subQ11})])]}),makeQuery(id+"F47.opFillet","BLEND_FACE",FACE,{"disambiguationData":[OSD([subQ0,subQ9]),TDD([makeQuery(id+"F42.boolean.opBoolean","COPY",EDGE,{"disambiguationData":[TD([makeQuery(id+"F38.opLoft","SWEPT_FACE",FACE,{"disambiguationData":[OSD([subQ8,subQ7,subQ5,sQuery(id+"F22.wireOp",EDGE,"E28.15.1"),subQ4,subQ3])]})])],"derivedFrom":subQ11})])]})],"blendedInto":[makeQuery(id+"F47.opFillet","BLEND_FACE",FACE,{"disambiguationData":[OSD([subQ0,subQ9]),TDD([makeQuery(id+"F42.boolean.opBoolean","COPY",EDGE,{"disambiguationData":[TD([makeQuery(id+"F23.opLoft","SWEPT_FACE",FACE,{"disambiguationData":[OSD([sQuery(id+"F3.wireOp",EDGE,"E20.8.0"),subQ112,subQ110,subQ109,subQ108,sQuery(id+"F22.wireOp",EDGE,"E27.right")])]})])],"derivedFrom":subQ11})])]}),makeQuery(id+"F47.opFillet","BLEND_FACE",FACE,{"disambiguationData":[OSD([subQ0,subQ9]),TDD([makeQuery(id+"F42.boolean.opBoolean","COPY",EDGE,{"disambiguationData":[TD([subQ107])],"derivedFrom":subQ11})])]}),makeQuery(id+"F47.opFillet","BLEND_FACE",FACE,{"disambiguationData":[OSD([subQ0,subQ9]),TDD([makeQuery(id+"F42.boolean.opBoolean","COPY",EDGE,{"disambiguationData":[TD([subQ100])],"derivedFrom":subQ11})])]}),makeQuery(id+"F47.opFillet","BLEND_FACE",FACE,{"disambiguationData":[OSD([subQ0,subQ9]),TDD([makeQuery(id+"F42.boolean.opBoolean","COPY",EDGE,{"disambiguationData":[TD([subQ94])],"derivedFrom":subQ11})])]}),makeQuery(id+"F47.opFillet","BLEND_FACE",FACE,{"disambiguationData":[OSD([subQ0,subQ9]),TDD([makeQuery(id+"F42.boolean.opBoolean","COPY",EDGE,{"disambiguationData":[TD([subQ87])],"derivedFrom":subQ11})])]}),makeQuery(id+"F47.opFillet","BLEND_FACE",FACE,{"disambiguationData":[OSD([subQ0,subQ9]),TDD([makeQuery(id+"F42.boolean.opBoolean","COPY",EDGE,{"disambiguationData":[TD([subQ80])],"derivedFrom":subQ11})])]}),makeQuery(id+"F47.opFillet","BLEND_FACE",FACE,{"disambiguationData":[OSD([subQ0,subQ9]),TDD([makeQuery(id+"F42.boolean.opBoolean","COPY",EDGE,{"disambiguationData":[TD([subQ73])],"derivedFrom":subQ11})])]}),makeQuery(id+"F47.opFillet","BLEND_FACE",FACE,{"disambiguationData":[OSD([subQ0,subQ9]),TDD([makeQuery(id+"F42.boolean.opBoolean","COPY",EDGE,{"disambiguationData":[TD([subQ65])],"derivedFrom":subQ11})])]}),makeQuery(id+"F47.opFillet","BLEND_FACE",FACE,{"disambiguationData":[OSD([subQ0,subQ9]),TDD([makeQuery(id+"F42.boolean.opBoolean","COPY",EDGE,{"disambiguationData":[TD([subQ59])],"derivedFrom":subQ11})])]}),makeQuery(id+"F47.opFillet","BLEND_FACE",FACE,{"disambiguationData":[OSD([subQ0,subQ9]),TDD([makeQuery(id+"F42.boolean.opBoolean","COPY",EDGE,{"disambiguationData":[TD([subQ52])],"derivedFrom":subQ11})])]}),makeQuery(id+"F47.opFillet","BLEND_FACE",FACE,{"disambiguationData":[OSD([subQ0,subQ9]),TDD([makeQuery(id+"F42.boolean.opBoolean","COPY",EDGE,{"disambiguationData":[TD([subQ45])],"derivedFrom":subQ11})])]}),makeQuery(id+"F47.opFillet","BLEND_FACE",FACE,{"disambiguationData":[OSD([subQ0,subQ9]),TDD([makeQuery(id+"F42.boolean.opBoolean","COPY",EDGE,{"disambiguationData":[TD([subQ38])],"derivedFrom":subQ11})])]}),makeQuery(id+"F47.opFillet","BLEND_FACE",FACE,{"disambiguationData":[OSD([subQ0,subQ9]),TDD([makeQuery(id+"F42.boolean.opBoolean","COPY",EDGE,{"disambiguationData":[TD([subQ31])],"derivedFrom":subQ11})])]}),makeQuery(id+"F47.opFillet","BLEND_FACE",FACE,{"disambiguationData":[OSD([subQ0,subQ9]),TDD([makeQuery(id+"F42.boolean.opBoolean","COPY",EDGE,{"disambiguationData":[TD([makeQuery(id+"F36.opLoft","SWEPT_FACE",FACE,{"disambiguationData":[OSD([subQ23,subQ22,subQ20,sQuery(id+"F22.wireOp",EDGE,"E28.13.1"),subQ19,subQ18])]})])],"derivedFrom":subQ11})])]}),makeQuery(id+"F47.opFillet","BLEND_FACE",FACE,{"disambiguationData":[OSD([subQ0,subQ9]),TDD([makeQuery(id+"F42.boolean.opBoolean","COPY",EDGE,{"disambiguationData":[TD([makeQuery(id+"F37.opLoft","SWEPT_FACE",FACE,{"disambiguationData":[OSD([subQ16,subQ15,subQ14,sQuery(id+"F22.wireOp",EDGE,"E28.14.1"),subQ13,subQ12])]})])],"derivedFrom":subQ11})])]}),makeQuery(id+"F47.opFillet","BLEND_FACE",FACE,{"disambiguationData":[OSD([subQ0,subQ9]),TDD([makeQuery(id+"F42.boolean.opBoolean","COPY",EDGE,{"disambiguationData":[TD([makeQuery(id+"F38.opLoft","SWEPT_FACE",FACE,{"disambiguationData":[OSD([subQ8,subQ7,subQ5,sQuery(id+"F22.wireOp",EDGE,"E28.15.1"),subQ4,subQ3])]})])],"derivedFrom":subQ11})])]})]});}
            var Q3;
            {var subQ0=sQuery(id+"F22.wireOp",EDGE,"E28.13.3");var subQ1=sQuery(id+"F22.wireOp",EDGE,"E28.13.2");var subQ2=sQuery(id+"F22.wireOp",EDGE,"E28.13.0");var subQ3=sQuery(id+"F3.wireOp",EDGE,"E20.5.3");var subQ4=sQuery(id+"F3.wireOp",EDGE,"E20.5.1");var subQ5=makeQuery(id+"F36.opLoft","SWEPT_FACE",FACE,{"disambiguationData":[OSD([subQ4,sQuery(id+"F3.wireOp",EDGE,"E20.5.2"),subQ3,subQ2,subQ1,subQ0])]});var subQ6=sQuery(id+"F22.wireOp",EDGE,"E28.13.1");var subQ7=sQuery(id+"F41.wireOp",EDGE,"E34");var subQ8=sQuery(id+"F41.wireOp",EDGE,"E32");Q3=makeQuery(id+"F44.opFillet","BLEND_EDGE",EDGE,{"blendedFrom":[makeQuery(id+"F40.boolean.opBoolean","INTERSECT",EDGE,{"derivedFrom":[subQ5,makeQuery(id+"F40.opExtrude","CAP_FACE",FACE,{"disambiguationData":[OSD([sQuery(id+"F39.wireOp",EDGE,"E29"),sQuery(id+"F39.wireOp",EDGE,"E30")])],"isStart":true})]}),makeQuery(id+"F42.boolean.opBoolean","COPY",FACE,{"disambiguationData":[TD([makeQuery(id+"F36.opLoft","SWEPT_FACE",FACE,{"disambiguationData":[OSD([sQuery(id+"F3.wireOp",EDGE,"E20.5.0"),subQ4,subQ3,subQ6,subQ1,subQ0])]})])],"derivedFrom":makeQuery(id+"F42.opRevolve","SWEPT_FACE",FACE,{"disambiguationData":[OSD([subQ8]),TDD([makeQuery(id+"F41.imprint","IMPRINT",EDGE,{"disambiguationData":[TD([[makeQuery(id+"F41.imprint","INTERSECT",VERTEX,{"disambiguationData":[OD(0.0)],"derivedFrom":[subQ8,subQ7]}),-1.0]])],"derivedFrom":subQ8})])]})})],"blendedInto":[makeQuery(id+"F42.boolean.opBoolean","COPY",FACE,{"disambiguationData":[TD([makeQuery(id+"F36.opLoft","SWEPT_FACE",FACE,{"disambiguationData":[OSD([sQuery(id+"F3.wireOp",EDGE,"E20.5.0"),subQ4,subQ3,subQ6,subQ1,subQ0])]})])],"derivedFrom":makeQuery(id+"F42.opRevolve","SWEPT_FACE",FACE,{"disambiguationData":[OSD([subQ8]),TDD([makeQuery(id+"F41.imprint","IMPRINT",EDGE,{"disambiguationData":[TD([[makeQuery(id+"F41.imprint","INTERSECT",VERTEX,{"disambiguationData":[OD(0.0)],"derivedFrom":[subQ8,subQ7]}),-1.0]])],"derivedFrom":subQ8})])]})})]});}
            var Q4;
            {var subQ0=sQuery(id+"F41.wireOp",EDGE,"E34");var subQ1=sQuery(id+"F41.wireOp",EDGE,"E32");Q4=makeQuery(id+"F42.boolean.opBoolean","INTERSECT",EDGE,{"derivedFrom":[makeQuery(id+"F36.opLoft","SWEPT_FACE",FACE,{"disambiguationData":[OSD([sQuery(id+"F3.wireOp",EDGE,"E20.5.0"),sQuery(id+"F3.wireOp",EDGE,"E20.5.1"),sQuery(id+"F3.wireOp",EDGE,"E20.5.3"),sQuery(id+"F22.wireOp",EDGE,"E28.13.1"),sQuery(id+"F22.wireOp",EDGE,"E28.13.2"),sQuery(id+"F22.wireOp",EDGE,"E28.13.3")])]}),makeQuery(id+"F42.opRevolve","SWEPT_FACE",FACE,{"disambiguationData":[OSD([subQ1]),TDD([makeQuery(id+"F41.imprint","IMPRINT",EDGE,{"disambiguationData":[TD([[makeQuery(id+"F41.imprint","INTERSECT",VERTEX,{"disambiguationData":[OD(0.0)],"derivedFrom":[subQ1,subQ0]}),-1.0]])],"derivedFrom":subQ1})])]})]});}
            var Q5;
            {var subQ0=sQuery(id+"F41.wireOp",EDGE,"E37");var subQ1=makeQuery(id+"F42.opRevolve","SWEPT_FACE",FACE,{"disambiguationData":[OSD([subQ0])]});var subQ2=makeQuery(id+"F40.opExtrude","CAP_FACE",FACE,{"disambiguationData":[OSD([sQuery(id+"F39.wireOp",EDGE,"E29"),sQuery(id+"F39.wireOp",EDGE,"E30")])],"isStart":true});var subQ3=sQuery(id+"F22.wireOp",EDGE,"E28.15.3");var subQ4=sQuery(id+"F22.wireOp",EDGE,"E28.15.2");var subQ5=sQuery(id+"F3.wireOp",EDGE,"E20.7.3");var subQ7=sQuery(id+"F3.wireOp",EDGE,"E20.7.1");var subQ8=sQuery(id+"F3.wireOp",EDGE,"E20.7.0");var subQ9=sQuery(id+"F41.wireOp",EDGE,"E38");var subQ10=makeQuery(id+"F42.opRevolve","SWEPT_FACE",FACE,{"disambiguationData":[OSD([subQ9])]});var subQ11=makeQuery(id+"F42.opRevolve","SWEPT_EDGE",EDGE,{"disambiguationData":[OSD([subQ0,subQ9])]});var subQ12=sQuery(id+"F22.wireOp",EDGE,"E28.14.3");var subQ13=sQuery(id+"F22.wireOp",EDGE,"E28.14.2");var subQ14=sQuery(id+"F3.wireOp",EDGE,"E20.6.3");var subQ15=sQuery(id+"F3.wireOp",EDGE,"E20.6.1");var subQ16=sQuery(id+"F3.wireOp",EDGE,"E20.6.0");var subQ18=sQuery(id+"F22.wireOp",EDGE,"E28.13.3");var subQ19=sQuery(id+"F22.wireOp",EDGE,"E28.13.2");var subQ20=sQuery(id+"F3.wireOp",EDGE,"E20.5.3");var subQ22=sQuery(id+"F3.wireOp",EDGE,"E20.5.1");var subQ24=sQuery(id+"F3.wireOp",EDGE,"E20.5.0");var subQ25=makeQuery(id+"F36.opLoft","SWEPT_FACE",FACE,{"disambiguationData":[OSD([subQ24,subQ22,subQ20,sQuery(id+"F22.wireOp",EDGE,"E28.13.1"),subQ19,subQ18])]});var subQ26=sQuery(id+"F22.wireOp",EDGE,"E28.12.3");var subQ27=sQuery(id+"F22.wireOp",EDGE,"E28.12.2");var subQ28=sQuery(id+"F3.wireOp",EDGE,"E20.4.3");var subQ30=sQuery(id+"F3.wireOp",EDGE,"E20.4.1");var subQ31=sQuery(id+"F3.wireOp",EDGE,"E20.4.0");var subQ32=makeQuery(id+"F35.opLoft","SWEPT_FACE",FACE,{"disambiguationData":[OSD([subQ31,subQ30,subQ28,sQuery(id+"F22.wireOp",EDGE,"E28.12.1"),subQ27,subQ26])]});var subQ33=sQuery(id+"F22.wireOp",EDGE,"E28.11.3");var subQ34=sQuery(id+"F22.wireOp",EDGE,"E28.11.2");var subQ35=sQuery(id+"F3.wireOp",EDGE,"E20.3.3");var subQ37=sQuery(id+"F3.wireOp",EDGE,"E20.3.1");var subQ38=sQuery(id+"F3.wireOp",EDGE,"E20.3.0");var subQ39=makeQuery(id+"F34.opLoft","SWEPT_FACE",FACE,{"disambiguationData":[OSD([subQ38,subQ37,subQ35,sQuery(id+"F22.wireOp",EDGE,"E28.11.1"),subQ34,subQ33])]});var subQ40=sQuery(id+"F22.wireOp",EDGE,"E28.10.3");var subQ41=sQuery(id+"F22.wireOp",EDGE,"E28.10.2");var subQ42=sQuery(id+"F3.wireOp",EDGE,"E20.2.3");var subQ44=sQuery(id+"F3.wireOp",EDGE,"E20.2.1");var subQ45=sQuery(id+"F3.wireOp",EDGE,"E20.2.0");var subQ46=makeQuery(id+"F33.opLoft","SWEPT_FACE",FACE,{"disambiguationData":[OSD([subQ45,subQ44,subQ42,sQuery(id+"F22.wireOp",EDGE,"E28.10.1"),subQ41,subQ40])]});var subQ47=sQuery(id+"F22.wireOp",EDGE,"E28.9.3");var subQ48=sQuery(id+"F22.wireOp",EDGE,"E28.9.2");var subQ49=sQuery(id+"F3.wireOp",EDGE,"E20.1.3");var subQ51=sQuery(id+"F3.wireOp",EDGE,"E20.1.1");var subQ52=sQuery(id+"F3.wireOp",EDGE,"E20.1.0");var subQ53=makeQuery(id+"F32.opLoft","SWEPT_FACE",FACE,{"disambiguationData":[OSD([subQ52,subQ51,subQ49,sQuery(id+"F22.wireOp",EDGE,"E28.9.1"),subQ48,subQ47])]});var subQ54=sQuery(id+"F22.wireOp",EDGE,"E28.8.3");var subQ55=sQuery(id+"F22.wireOp",EDGE,"E28.8.2");var subQ57=sQuery(id+"F3.wireOp",EDGE,"E18.top");var subQ58=sQuery(id+"F3.wireOp",EDGE,"E18.bottom");var subQ59=sQuery(id+"F3.wireOp",EDGE,"E18.left");var subQ60=makeQuery(id+"F31.opLoft","SWEPT_FACE",FACE,{"disambiguationData":[OSD([subQ58,subQ57,subQ59,sQuery(id+"F22.wireOp",EDGE,"E28.8.1"),subQ55,subQ54])]});var subQ61=sQuery(id+"F22.wireOp",EDGE,"E28.7.3");var subQ62=sQuery(id+"F22.wireOp",EDGE,"E28.7.2");var subQ63=sQuery(id+"F3.wireOp",EDGE,"E20.15.3");var subQ64=sQuery(id+"F3.wireOp",EDGE,"E20.15.1");var subQ65=sQuery(id+"F3.wireOp",EDGE,"E20.15.0");var subQ66=makeQuery(id+"F30.opLoft","SWEPT_FACE",FACE,{"disambiguationData":[OSD([subQ65,subQ64,subQ63,sQuery(id+"F22.wireOp",EDGE,"E28.7.1"),subQ62,subQ61])]});var subQ68=sQuery(id+"F22.wireOp",EDGE,"E28.6.3");var subQ69=sQuery(id+"F22.wireOp",EDGE,"E28.6.2");var subQ70=sQuery(id+"F3.wireOp",EDGE,"E20.14.3");var subQ72=sQuery(id+"F3.wireOp",EDGE,"E20.14.1");var subQ73=sQuery(id+"F3.wireOp",EDGE,"E20.14.0");var subQ74=makeQuery(id+"F29.opLoft","SWEPT_FACE",FACE,{"disambiguationData":[OSD([subQ73,subQ72,subQ70,sQuery(id+"F22.wireOp",EDGE,"E28.6.1"),subQ69,subQ68])]});var subQ75=sQuery(id+"F22.wireOp",EDGE,"E28.5.3");var subQ76=sQuery(id+"F22.wireOp",EDGE,"E28.5.2");var subQ77=sQuery(id+"F3.wireOp",EDGE,"E20.13.3");var subQ79=sQuery(id+"F3.wireOp",EDGE,"E20.13.1");var subQ80=sQuery(id+"F3.wireOp",EDGE,"E20.13.0");var subQ81=makeQuery(id+"F28.opLoft","SWEPT_FACE",FACE,{"disambiguationData":[OSD([subQ80,subQ79,subQ77,sQuery(id+"F22.wireOp",EDGE,"E28.5.1"),subQ76,subQ75])]});var subQ82=sQuery(id+"F22.wireOp",EDGE,"E28.4.3");var subQ83=sQuery(id+"F22.wireOp",EDGE,"E28.4.2");var subQ84=sQuery(id+"F3.wireOp",EDGE,"E20.12.3");var subQ86=sQuery(id+"F3.wireOp",EDGE,"E20.12.1");var subQ87=sQuery(id+"F3.wireOp",EDGE,"E20.12.0");var subQ88=makeQuery(id+"F27.opLoft","SWEPT_FACE",FACE,{"disambiguationData":[OSD([subQ87,subQ86,subQ84,sQuery(id+"F22.wireOp",EDGE,"E28.4.1"),subQ83,subQ82])]});var subQ89=sQuery(id+"F22.wireOp",EDGE,"E28.3.3");var subQ90=sQuery(id+"F22.wireOp",EDGE,"E28.3.2");var subQ91=sQuery(id+"F3.wireOp",EDGE,"E20.11.3");var subQ93=sQuery(id+"F3.wireOp",EDGE,"E20.11.1");var subQ94=sQuery(id+"F3.wireOp",EDGE,"E20.11.0");var subQ95=makeQuery(id+"F26.opLoft","SWEPT_FACE",FACE,{"disambiguationData":[OSD([subQ94,subQ93,subQ91,sQuery(id+"F22.wireOp",EDGE,"E28.3.1"),subQ90,subQ89])]});var subQ96=sQuery(id+"F22.wireOp",EDGE,"E28.2.3");var subQ97=sQuery(id+"F22.wireOp",EDGE,"E28.2.2");var subQ98=sQuery(id+"F3.wireOp",EDGE,"E20.10.3");var subQ99=sQuery(id+"F3.wireOp",EDGE,"E20.10.1");var subQ100=sQuery(id+"F3.wireOp",EDGE,"E20.10.0");var subQ101=makeQuery(id+"F25.opLoft","SWEPT_FACE",FACE,{"disambiguationData":[OSD([subQ100,subQ99,subQ98,sQuery(id+"F22.wireOp",EDGE,"E28.2.1"),subQ97,subQ96])]});var subQ103=sQuery(id+"F22.wireOp",EDGE,"E28.1.3");var subQ104=sQuery(id+"F22.wireOp",EDGE,"E28.1.2");var subQ105=sQuery(id+"F3.wireOp",EDGE,"E20.9.3");var subQ106=sQuery(id+"F3.wireOp",EDGE,"E20.9.1");var subQ107=sQuery(id+"F3.wireOp",EDGE,"E20.9.0");var subQ108=makeQuery(id+"F24.opLoft","SWEPT_FACE",FACE,{"disambiguationData":[OSD([subQ107,subQ106,subQ105,sQuery(id+"F22.wireOp",EDGE,"E28.1.1"),subQ104,subQ103])]});var subQ109=sQuery(id+"F22.wireOp",EDGE,"E27.top");var subQ110=sQuery(id+"F22.wireOp",EDGE,"E27.bottom");var subQ111=sQuery(id+"F3.wireOp",EDGE,"E20.8.3");var subQ113=sQuery(id+"F3.wireOp",EDGE,"E20.8.1");var subQ117=makeQuery(id+"F42.boolean.opBoolean","COPY",FACE,{"disambiguationData":[TD([subQ25])],"derivedFrom":subQ10});var subQ125=makeQuery(id+"F14.opLoft","CAP_FACE",FACE,{"disambiguationData":[OSD([makeQuery(id+"F3.imprint","IMPRINT",FACE,{"disambiguationData":[TD([[makeQuery(id+"F3.imprint","IMPRINT",EDGE,{"derivedFrom":subQ8}),-1.0]])]})])],"isStart":true});var subQ160=makeQuery(id+"F5.opLoft","CAP_FACE",FACE,{"disambiguationData":[OSD([makeQuery(id+"F3.imprint","IMPRINT",FACE,{"disambiguationData":[TD([[makeQuery(id+"F3.imprint","IMPRINT",EDGE,{"derivedFrom":subQ58}),1.0]])]})])],"isStart":true});var subQ189=makeQuery(id+"F36.boolean.opBoolean","INTERSECT",EDGE,{"derivedFrom":[makeQuery(id+"F35.boolean.opBoolean","SPLIT",FACE,{"disambiguationData":[TD([subQ125])],"derivedFrom":makeQuery(id+"F34.boolean.opBoolean","SPLIT",FACE,{"disambiguationData":[TD([subQ125])],"derivedFrom":makeQuery(id+"F33.boolean.opBoolean","SPLIT",FACE,{"disambiguationData":[TD([subQ125])],"derivedFrom":makeQuery(id+"F32.boolean.opBoolean","SPLIT",FACE,{"disambiguationData":[TD([subQ125])],"derivedFrom":makeQuery(id+"F31.boolean.opBoolean","SPLIT",FACE,{"disambiguationData":[TD([subQ125])],"derivedFrom":makeQuery(id+"F30.boolean.opBoolean","SPLIT",FACE,{"disambiguationData":[TD([subQ160])],"derivedFrom":makeQuery(id+"F29.boolean.opBoolean","SPLIT",FACE,{"disambiguationData":[TD([subQ160])],"derivedFrom":makeQuery(id+"F28.boolean.opBoolean","SPLIT",FACE,{"disambiguationData":[TD([subQ160])],"derivedFrom":makeQuery(id+"F27.boolean.opBoolean","SPLIT",FACE,{"disambiguationData":[TD([subQ160])],"derivedFrom":makeQuery(id+"F26.boolean.opBoolean","SPLIT",FACE,{"disambiguationData":[TD([subQ160])],"derivedFrom":makeQuery(id+"F25.boolean.opBoolean","SPLIT",FACE,{"disambiguationData":[TD([subQ160])],"derivedFrom":makeQuery(id+"F24.boolean.opBoolean","SPLIT",FACE,{"disambiguationData":[TD([subQ160])],"derivedFrom":makeQuery(id+"F1.opRevolve","SWEPT_FACE",FACE,{"disambiguationData":[OSD([sQuery(id+"F0.wireOp",EDGE,"E4")])]})})})})})})})})})})})})}),subQ25]});Q5=makeQuery(id+"F48.opFillet","BLEND_EDGE",EDGE,{"blendedFrom":[makeQuery(id+"F47.opFillet","TWEAK_EDGE",EDGE,{"derivedFrom":[makeQuery(id+"F45.opFillet","BLEND_VERTEX",VERTEX,{"blendedFrom":[subQ189,subQ25,subQ117],"blendedInto":[subQ25,subQ117]}),makeQuery(id+"F45.opFillet","BLEND_VERTEX",VERTEX,{"blendedFrom":[subQ189,makeQuery(id+"F42.boolean.opBoolean","MERGE",FACE,{"derivedFrom":[subQ2,subQ1]}),subQ117],"blendedInto":[makeQuery(id+"F42.boolean.opBoolean","MERGE",FACE,{"derivedFrom":[subQ2,subQ1]}),subQ117]})]}),makeQuery(id+"F47.opFillet","BLEND_FACE",FACE,{"disambiguationData":[OSD([subQ0,subQ9]),TDD([makeQuery(id+"F42.boolean.opBoolean","COPY",EDGE,{"disambiguationData":[TD([makeQuery(id+"F23.opLoft","SWEPT_FACE",FACE,{"disambiguationData":[OSD([sQuery(id+"F3.wireOp",EDGE,"E20.8.0"),subQ113,subQ111,subQ110,subQ109,sQuery(id+"F22.wireOp",EDGE,"E27.right")])]})])],"derivedFrom":subQ11})])]}),makeQuery(id+"F47.opFillet","BLEND_FACE",FACE,{"disambiguationData":[OSD([subQ0,subQ9]),TDD([makeQuery(id+"F42.boolean.opBoolean","COPY",EDGE,{"disambiguationData":[TD([subQ108])],"derivedFrom":subQ11})])]}),makeQuery(id+"F47.opFillet","BLEND_FACE",FACE,{"disambiguationData":[OSD([subQ0,subQ9]),TDD([makeQuery(id+"F42.boolean.opBoolean","COPY",EDGE,{"disambiguationData":[TD([subQ101])],"derivedFrom":subQ11})])]}),makeQuery(id+"F47.opFillet","BLEND_FACE",FACE,{"disambiguationData":[OSD([subQ0,subQ9]),TDD([makeQuery(id+"F42.boolean.opBoolean","COPY",EDGE,{"disambiguationData":[TD([subQ95])],"derivedFrom":subQ11})])]}),makeQuery(id+"F47.opFillet","BLEND_FACE",FACE,{"disambiguationData":[OSD([subQ0,subQ9]),TDD([makeQuery(id+"F42.boolean.opBoolean","COPY",EDGE,{"disambiguationData":[TD([subQ88])],"derivedFrom":subQ11})])]}),makeQuery(id+"F47.opFillet","BLEND_FACE",FACE,{"disambiguationData":[OSD([subQ0,subQ9]),TDD([makeQuery(id+"F42.boolean.opBoolean","COPY",EDGE,{"disambiguationData":[TD([subQ81])],"derivedFrom":subQ11})])]}),makeQuery(id+"F47.opFillet","BLEND_FACE",FACE,{"disambiguationData":[OSD([subQ0,subQ9]),TDD([makeQuery(id+"F42.boolean.opBoolean","COPY",EDGE,{"disambiguationData":[TD([subQ74])],"derivedFrom":subQ11})])]}),makeQuery(id+"F47.opFillet","BLEND_FACE",FACE,{"disambiguationData":[OSD([subQ0,subQ9]),TDD([makeQuery(id+"F42.boolean.opBoolean","COPY",EDGE,{"disambiguationData":[TD([subQ66])],"derivedFrom":subQ11})])]}),makeQuery(id+"F47.opFillet","BLEND_FACE",FACE,{"disambiguationData":[OSD([subQ0,subQ9]),TDD([makeQuery(id+"F42.boolean.opBoolean","COPY",EDGE,{"disambiguationData":[TD([subQ60])],"derivedFrom":subQ11})])]}),makeQuery(id+"F47.opFillet","BLEND_FACE",FACE,{"disambiguationData":[OSD([subQ0,subQ9]),TDD([makeQuery(id+"F42.boolean.opBoolean","COPY",EDGE,{"disambiguationData":[TD([subQ53])],"derivedFrom":subQ11})])]}),makeQuery(id+"F47.opFillet","BLEND_FACE",FACE,{"disambiguationData":[OSD([subQ0,subQ9]),TDD([makeQuery(id+"F42.boolean.opBoolean","COPY",EDGE,{"disambiguationData":[TD([subQ46])],"derivedFrom":subQ11})])]}),makeQuery(id+"F47.opFillet","BLEND_FACE",FACE,{"disambiguationData":[OSD([subQ0,subQ9]),TDD([makeQuery(id+"F42.boolean.opBoolean","COPY",EDGE,{"disambiguationData":[TD([subQ39])],"derivedFrom":subQ11})])]}),makeQuery(id+"F47.opFillet","BLEND_FACE",FACE,{"disambiguationData":[OSD([subQ0,subQ9]),TDD([makeQuery(id+"F42.boolean.opBoolean","COPY",EDGE,{"disambiguationData":[TD([subQ32])],"derivedFrom":subQ11})])]}),makeQuery(id+"F47.opFillet","BLEND_FACE",FACE,{"disambiguationData":[OSD([subQ0,subQ9]),TDD([makeQuery(id+"F42.boolean.opBoolean","COPY",EDGE,{"disambiguationData":[TD([subQ25])],"derivedFrom":subQ11})])]}),makeQuery(id+"F47.opFillet","BLEND_FACE",FACE,{"disambiguationData":[OSD([subQ0,subQ9]),TDD([makeQuery(id+"F42.boolean.opBoolean","COPY",EDGE,{"disambiguationData":[TD([makeQuery(id+"F37.opLoft","SWEPT_FACE",FACE,{"disambiguationData":[OSD([subQ16,subQ15,subQ14,sQuery(id+"F22.wireOp",EDGE,"E28.14.1"),subQ13,subQ12])]})])],"derivedFrom":subQ11})])]}),makeQuery(id+"F47.opFillet","BLEND_FACE",FACE,{"disambiguationData":[OSD([subQ0,subQ9]),TDD([makeQuery(id+"F42.boolean.opBoolean","COPY",EDGE,{"disambiguationData":[TD([makeQuery(id+"F38.opLoft","SWEPT_FACE",FACE,{"disambiguationData":[OSD([subQ8,subQ7,subQ5,sQuery(id+"F22.wireOp",EDGE,"E28.15.1"),subQ4,subQ3])]})])],"derivedFrom":subQ11})])]})],"blendedInto":[makeQuery(id+"F47.opFillet","BLEND_FACE",FACE,{"disambiguationData":[OSD([subQ0,subQ9]),TDD([makeQuery(id+"F42.boolean.opBoolean","COPY",EDGE,{"disambiguationData":[TD([makeQuery(id+"F23.opLoft","SWEPT_FACE",FACE,{"disambiguationData":[OSD([sQuery(id+"F3.wireOp",EDGE,"E20.8.0"),subQ113,subQ111,subQ110,subQ109,sQuery(id+"F22.wireOp",EDGE,"E27.right")])]})])],"derivedFrom":subQ11})])]}),makeQuery(id+"F47.opFillet","BLEND_FACE",FACE,{"disambiguationData":[OSD([subQ0,subQ9]),TDD([makeQuery(id+"F42.boolean.opBoolean","COPY",EDGE,{"disambiguationData":[TD([subQ108])],"derivedFrom":subQ11})])]}),makeQuery(id+"F47.opFillet","BLEND_FACE",FACE,{"disambiguationData":[OSD([subQ0,subQ9]),TDD([makeQuery(id+"F42.boolean.opBoolean","COPY",EDGE,{"disambiguationData":[TD([subQ101])],"derivedFrom":subQ11})])]}),makeQuery(id+"F47.opFillet","BLEND_FACE",FACE,{"disambiguationData":[OSD([subQ0,subQ9]),TDD([makeQuery(id+"F42.boolean.opBoolean","COPY",EDGE,{"disambiguationData":[TD([subQ95])],"derivedFrom":subQ11})])]}),makeQuery(id+"F47.opFillet","BLEND_FACE",FACE,{"disambiguationData":[OSD([subQ0,subQ9]),TDD([makeQuery(id+"F42.boolean.opBoolean","COPY",EDGE,{"disambiguationData":[TD([subQ88])],"derivedFrom":subQ11})])]}),makeQuery(id+"F47.opFillet","BLEND_FACE",FACE,{"disambiguationData":[OSD([subQ0,subQ9]),TDD([makeQuery(id+"F42.boolean.opBoolean","COPY",EDGE,{"disambiguationData":[TD([subQ81])],"derivedFrom":subQ11})])]}),makeQuery(id+"F47.opFillet","BLEND_FACE",FACE,{"disambiguationData":[OSD([subQ0,subQ9]),TDD([makeQuery(id+"F42.boolean.opBoolean","COPY",EDGE,{"disambiguationData":[TD([subQ74])],"derivedFrom":subQ11})])]}),makeQuery(id+"F47.opFillet","BLEND_FACE",FACE,{"disambiguationData":[OSD([subQ0,subQ9]),TDD([makeQuery(id+"F42.boolean.opBoolean","COPY",EDGE,{"disambiguationData":[TD([subQ66])],"derivedFrom":subQ11})])]}),makeQuery(id+"F47.opFillet","BLEND_FACE",FACE,{"disambiguationData":[OSD([subQ0,subQ9]),TDD([makeQuery(id+"F42.boolean.opBoolean","COPY",EDGE,{"disambiguationData":[TD([subQ60])],"derivedFrom":subQ11})])]}),makeQuery(id+"F47.opFillet","BLEND_FACE",FACE,{"disambiguationData":[OSD([subQ0,subQ9]),TDD([makeQuery(id+"F42.boolean.opBoolean","COPY",EDGE,{"disambiguationData":[TD([subQ53])],"derivedFrom":subQ11})])]}),makeQuery(id+"F47.opFillet","BLEND_FACE",FACE,{"disambiguationData":[OSD([subQ0,subQ9]),TDD([makeQuery(id+"F42.boolean.opBoolean","COPY",EDGE,{"disambiguationData":[TD([subQ46])],"derivedFrom":subQ11})])]}),makeQuery(id+"F47.opFillet","BLEND_FACE",FACE,{"disambiguationData":[OSD([subQ0,subQ9]),TDD([makeQuery(id+"F42.boolean.opBoolean","COPY",EDGE,{"disambiguationData":[TD([subQ39])],"derivedFrom":subQ11})])]}),makeQuery(id+"F47.opFillet","BLEND_FACE",FACE,{"disambiguationData":[OSD([subQ0,subQ9]),TDD([makeQuery(id+"F42.boolean.opBoolean","COPY",EDGE,{"disambiguationData":[TD([subQ32])],"derivedFrom":subQ11})])]}),makeQuery(id+"F47.opFillet","BLEND_FACE",FACE,{"disambiguationData":[OSD([subQ0,subQ9]),TDD([makeQuery(id+"F42.boolean.opBoolean","COPY",EDGE,{"disambiguationData":[TD([subQ25])],"derivedFrom":subQ11})])]}),makeQuery(id+"F47.opFillet","BLEND_FACE",FACE,{"disambiguationData":[OSD([subQ0,subQ9]),TDD([makeQuery(id+"F42.boolean.opBoolean","COPY",EDGE,{"disambiguationData":[TD([makeQuery(id+"F37.opLoft","SWEPT_FACE",FACE,{"disambiguationData":[OSD([subQ16,subQ15,subQ14,sQuery(id+"F22.wireOp",EDGE,"E28.14.1"),subQ13,subQ12])]})])],"derivedFrom":subQ11})])]}),makeQuery(id+"F47.opFillet","BLEND_FACE",FACE,{"disambiguationData":[OSD([subQ0,subQ9]),TDD([makeQuery(id+"F42.boolean.opBoolean","COPY",EDGE,{"disambiguationData":[TD([makeQuery(id+"F38.opLoft","SWEPT_FACE",FACE,{"disambiguationData":[OSD([subQ8,subQ7,subQ5,sQuery(id+"F22.wireOp",EDGE,"E28.15.1"),subQ4,subQ3])]})])],"derivedFrom":subQ11})])]})]});}
            var Q6;
            {var subQ0=sQuery(id+"F22.wireOp",EDGE,"E28.14.0");var subQ1=sQuery(id+"F22.wireOp",EDGE,"E28.14.3");var subQ2=sQuery(id+"F22.wireOp",EDGE,"E28.14.1");var subQ3=sQuery(id+"F22.wireOp",EDGE,"E28.14.2");var subQ4=sQuery(id+"F3.wireOp",EDGE,"E20.6.3");var subQ5=sQuery(id+"F3.wireOp",EDGE,"E20.6.1");var subQ6=makeQuery(id+"F37.opLoft","SWEPT_FACE",FACE,{"disambiguationData":[OSD([subQ5,sQuery(id+"F3.wireOp",EDGE,"E20.6.2"),subQ4,subQ0,subQ3,subQ1])]});var subQ7=sQuery(id+"F41.wireOp",EDGE,"E34");var subQ8=sQuery(id+"F41.wireOp",EDGE,"E32");Q6=makeQuery(id+"F44.opFillet","BLEND_EDGE",EDGE,{"blendedFrom":[makeQuery(id+"F40.boolean.opBoolean","INTERSECT",EDGE,{"derivedFrom":[subQ6,makeQuery(id+"F40.opExtrude","CAP_FACE",FACE,{"disambiguationData":[OSD([sQuery(id+"F39.wireOp",EDGE,"E29"),sQuery(id+"F39.wireOp",EDGE,"E30")])],"isStart":true})]}),makeQuery(id+"F42.boolean.opBoolean","COPY",FACE,{"disambiguationData":[TD([makeQuery(id+"F37.opLoft","SWEPT_FACE",FACE,{"disambiguationData":[OSD([sQuery(id+"F3.wireOp",EDGE,"E20.6.0"),subQ5,subQ4,subQ2,subQ3,subQ1])]})])],"derivedFrom":makeQuery(id+"F42.opRevolve","SWEPT_FACE",FACE,{"disambiguationData":[OSD([subQ8]),TDD([makeQuery(id+"F41.imprint","IMPRINT",EDGE,{"disambiguationData":[TD([[makeQuery(id+"F41.imprint","INTERSECT",VERTEX,{"disambiguationData":[OD(0.0)],"derivedFrom":[subQ8,subQ7]}),-1.0]])],"derivedFrom":subQ8})])]})})],"blendedInto":[makeQuery(id+"F42.boolean.opBoolean","COPY",FACE,{"disambiguationData":[TD([makeQuery(id+"F37.opLoft","SWEPT_FACE",FACE,{"disambiguationData":[OSD([sQuery(id+"F3.wireOp",EDGE,"E20.6.0"),subQ5,subQ4,subQ2,subQ3,subQ1])]})])],"derivedFrom":makeQuery(id+"F42.opRevolve","SWEPT_FACE",FACE,{"disambiguationData":[OSD([subQ8]),TDD([makeQuery(id+"F41.imprint","IMPRINT",EDGE,{"disambiguationData":[TD([[makeQuery(id+"F41.imprint","INTERSECT",VERTEX,{"disambiguationData":[OD(0.0)],"derivedFrom":[subQ8,subQ7]}),-1.0]])],"derivedFrom":subQ8})])]})})]});}
            var Q7;
            {var subQ0=sQuery(id+"F41.wireOp",EDGE,"E37");var subQ1=makeQuery(id+"F42.opRevolve","SWEPT_FACE",FACE,{"disambiguationData":[OSD([subQ0])]});var subQ2=makeQuery(id+"F40.opExtrude","CAP_FACE",FACE,{"disambiguationData":[OSD([sQuery(id+"F39.wireOp",EDGE,"E29"),sQuery(id+"F39.wireOp",EDGE,"E30")])],"isStart":true});var subQ3=sQuery(id+"F22.wireOp",EDGE,"E28.15.3");var subQ4=sQuery(id+"F22.wireOp",EDGE,"E28.15.2");var subQ5=sQuery(id+"F3.wireOp",EDGE,"E20.7.3");var subQ7=sQuery(id+"F3.wireOp",EDGE,"E20.7.1");var subQ8=sQuery(id+"F3.wireOp",EDGE,"E20.7.0");var subQ9=sQuery(id+"F41.wireOp",EDGE,"E38");var subQ10=makeQuery(id+"F42.opRevolve","SWEPT_FACE",FACE,{"disambiguationData":[OSD([subQ9])]});var subQ11=makeQuery(id+"F42.opRevolve","SWEPT_EDGE",EDGE,{"disambiguationData":[OSD([subQ0,subQ9])]});var subQ12=sQuery(id+"F22.wireOp",EDGE,"E28.14.3");var subQ13=sQuery(id+"F22.wireOp",EDGE,"E28.14.2");var subQ14=sQuery(id+"F3.wireOp",EDGE,"E20.6.3");var subQ15=sQuery(id+"F3.wireOp",EDGE,"E20.6.1");var subQ16=sQuery(id+"F3.wireOp",EDGE,"E20.6.0");var subQ18=sQuery(id+"F22.wireOp",EDGE,"E28.13.3");var subQ19=sQuery(id+"F22.wireOp",EDGE,"E28.13.2");var subQ20=sQuery(id+"F3.wireOp",EDGE,"E20.5.3");var subQ22=sQuery(id+"F3.wireOp",EDGE,"E20.5.1");var subQ23=sQuery(id+"F3.wireOp",EDGE,"E20.5.0");var subQ24=sQuery(id+"F22.wireOp",EDGE,"E28.12.3");var subQ25=sQuery(id+"F22.wireOp",EDGE,"E28.12.2");var subQ26=sQuery(id+"F3.wireOp",EDGE,"E20.4.3");var subQ28=sQuery(id+"F3.wireOp",EDGE,"E20.4.1");var subQ29=sQuery(id+"F3.wireOp",EDGE,"E20.4.0");var subQ30=sQuery(id+"F22.wireOp",EDGE,"E28.11.3");var subQ31=sQuery(id+"F22.wireOp",EDGE,"E28.11.2");var subQ32=sQuery(id+"F3.wireOp",EDGE,"E20.3.3");var subQ34=sQuery(id+"F3.wireOp",EDGE,"E20.3.1");var subQ36=sQuery(id+"F3.wireOp",EDGE,"E20.3.0");var subQ37=makeQuery(id+"F34.opLoft","SWEPT_FACE",FACE,{"disambiguationData":[OSD([subQ36,subQ34,subQ32,sQuery(id+"F22.wireOp",EDGE,"E28.11.1"),subQ31,subQ30])]});var subQ38=sQuery(id+"F22.wireOp",EDGE,"E28.10.3");var subQ39=sQuery(id+"F22.wireOp",EDGE,"E28.10.2");var subQ40=sQuery(id+"F3.wireOp",EDGE,"E20.2.3");var subQ42=sQuery(id+"F3.wireOp",EDGE,"E20.2.1");var subQ43=sQuery(id+"F3.wireOp",EDGE,"E20.2.0");var subQ44=makeQuery(id+"F33.opLoft","SWEPT_FACE",FACE,{"disambiguationData":[OSD([subQ43,subQ42,subQ40,sQuery(id+"F22.wireOp",EDGE,"E28.10.1"),subQ39,subQ38])]});var subQ45=sQuery(id+"F22.wireOp",EDGE,"E28.9.3");var subQ46=sQuery(id+"F22.wireOp",EDGE,"E28.9.2");var subQ47=sQuery(id+"F3.wireOp",EDGE,"E20.1.3");var subQ49=sQuery(id+"F3.wireOp",EDGE,"E20.1.1");var subQ50=sQuery(id+"F3.wireOp",EDGE,"E20.1.0");var subQ51=makeQuery(id+"F32.opLoft","SWEPT_FACE",FACE,{"disambiguationData":[OSD([subQ50,subQ49,subQ47,sQuery(id+"F22.wireOp",EDGE,"E28.9.1"),subQ46,subQ45])]});var subQ52=sQuery(id+"F22.wireOp",EDGE,"E28.8.3");var subQ53=sQuery(id+"F22.wireOp",EDGE,"E28.8.2");var subQ55=sQuery(id+"F3.wireOp",EDGE,"E18.top");var subQ56=sQuery(id+"F3.wireOp",EDGE,"E18.bottom");var subQ57=sQuery(id+"F3.wireOp",EDGE,"E18.left");var subQ58=makeQuery(id+"F31.opLoft","SWEPT_FACE",FACE,{"disambiguationData":[OSD([subQ56,subQ55,subQ57,sQuery(id+"F22.wireOp",EDGE,"E28.8.1"),subQ53,subQ52])]});var subQ59=sQuery(id+"F22.wireOp",EDGE,"E28.7.3");var subQ60=sQuery(id+"F22.wireOp",EDGE,"E28.7.2");var subQ61=sQuery(id+"F3.wireOp",EDGE,"E20.15.3");var subQ62=sQuery(id+"F3.wireOp",EDGE,"E20.15.1");var subQ63=sQuery(id+"F3.wireOp",EDGE,"E20.15.0");var subQ64=makeQuery(id+"F30.opLoft","SWEPT_FACE",FACE,{"disambiguationData":[OSD([subQ63,subQ62,subQ61,sQuery(id+"F22.wireOp",EDGE,"E28.7.1"),subQ60,subQ59])]});var subQ66=sQuery(id+"F22.wireOp",EDGE,"E28.6.3");var subQ67=sQuery(id+"F22.wireOp",EDGE,"E28.6.2");var subQ68=sQuery(id+"F3.wireOp",EDGE,"E20.14.3");var subQ70=sQuery(id+"F3.wireOp",EDGE,"E20.14.1");var subQ71=sQuery(id+"F3.wireOp",EDGE,"E20.14.0");var subQ72=makeQuery(id+"F29.opLoft","SWEPT_FACE",FACE,{"disambiguationData":[OSD([subQ71,subQ70,subQ68,sQuery(id+"F22.wireOp",EDGE,"E28.6.1"),subQ67,subQ66])]});var subQ73=sQuery(id+"F22.wireOp",EDGE,"E28.5.3");var subQ74=sQuery(id+"F22.wireOp",EDGE,"E28.5.2");var subQ75=sQuery(id+"F3.wireOp",EDGE,"E20.13.3");var subQ77=sQuery(id+"F3.wireOp",EDGE,"E20.13.1");var subQ78=sQuery(id+"F3.wireOp",EDGE,"E20.13.0");var subQ79=makeQuery(id+"F28.opLoft","SWEPT_FACE",FACE,{"disambiguationData":[OSD([subQ78,subQ77,subQ75,sQuery(id+"F22.wireOp",EDGE,"E28.5.1"),subQ74,subQ73])]});var subQ80=sQuery(id+"F22.wireOp",EDGE,"E28.4.3");var subQ81=sQuery(id+"F22.wireOp",EDGE,"E28.4.2");var subQ82=sQuery(id+"F3.wireOp",EDGE,"E20.12.3");var subQ84=sQuery(id+"F3.wireOp",EDGE,"E20.12.1");var subQ85=sQuery(id+"F3.wireOp",EDGE,"E20.12.0");var subQ86=makeQuery(id+"F27.opLoft","SWEPT_FACE",FACE,{"disambiguationData":[OSD([subQ85,subQ84,subQ82,sQuery(id+"F22.wireOp",EDGE,"E28.4.1"),subQ81,subQ80])]});var subQ87=sQuery(id+"F22.wireOp",EDGE,"E28.3.3");var subQ88=sQuery(id+"F22.wireOp",EDGE,"E28.3.2");var subQ89=sQuery(id+"F3.wireOp",EDGE,"E20.11.3");var subQ91=sQuery(id+"F3.wireOp",EDGE,"E20.11.1");var subQ92=sQuery(id+"F3.wireOp",EDGE,"E20.11.0");var subQ93=makeQuery(id+"F26.opLoft","SWEPT_FACE",FACE,{"disambiguationData":[OSD([subQ92,subQ91,subQ89,sQuery(id+"F22.wireOp",EDGE,"E28.3.1"),subQ88,subQ87])]});var subQ94=sQuery(id+"F22.wireOp",EDGE,"E28.2.3");var subQ95=sQuery(id+"F22.wireOp",EDGE,"E28.2.2");var subQ96=sQuery(id+"F3.wireOp",EDGE,"E20.10.3");var subQ97=sQuery(id+"F3.wireOp",EDGE,"E20.10.1");var subQ98=sQuery(id+"F3.wireOp",EDGE,"E20.10.0");var subQ99=makeQuery(id+"F25.opLoft","SWEPT_FACE",FACE,{"disambiguationData":[OSD([subQ98,subQ97,subQ96,sQuery(id+"F22.wireOp",EDGE,"E28.2.1"),subQ95,subQ94])]});var subQ101=sQuery(id+"F22.wireOp",EDGE,"E28.1.3");var subQ102=sQuery(id+"F22.wireOp",EDGE,"E28.1.2");var subQ103=sQuery(id+"F3.wireOp",EDGE,"E20.9.3");var subQ104=sQuery(id+"F3.wireOp",EDGE,"E20.9.1");var subQ105=sQuery(id+"F3.wireOp",EDGE,"E20.9.0");var subQ106=makeQuery(id+"F24.opLoft","SWEPT_FACE",FACE,{"disambiguationData":[OSD([subQ105,subQ104,subQ103,sQuery(id+"F22.wireOp",EDGE,"E28.1.1"),subQ102,subQ101])]});var subQ107=sQuery(id+"F22.wireOp",EDGE,"E27.top");var subQ108=sQuery(id+"F22.wireOp",EDGE,"E27.bottom");var subQ109=sQuery(id+"F3.wireOp",EDGE,"E20.8.3");var subQ111=sQuery(id+"F3.wireOp",EDGE,"E20.8.1");var subQ115=makeQuery(id+"F42.boolean.opBoolean","COPY",FACE,{"disambiguationData":[TD([subQ37])],"derivedFrom":subQ10});var subQ124=makeQuery(id+"F14.opLoft","CAP_FACE",FACE,{"disambiguationData":[OSD([makeQuery(id+"F3.imprint","IMPRINT",FACE,{"disambiguationData":[TD([[makeQuery(id+"F3.imprint","IMPRINT",EDGE,{"derivedFrom":subQ8}),-1.0]])]})])],"isStart":true});var subQ158=makeQuery(id+"F5.opLoft","CAP_FACE",FACE,{"disambiguationData":[OSD([makeQuery(id+"F3.imprint","IMPRINT",FACE,{"disambiguationData":[TD([[makeQuery(id+"F3.imprint","IMPRINT",EDGE,{"derivedFrom":subQ56}),1.0]])]})])],"isStart":true});var subQ187=makeQuery(id+"F34.boolean.opBoolean","INTERSECT",EDGE,{"derivedFrom":[makeQuery(id+"F33.boolean.opBoolean","SPLIT",FACE,{"disambiguationData":[TD([subQ124])],"derivedFrom":makeQuery(id+"F32.boolean.opBoolean","SPLIT",FACE,{"disambiguationData":[TD([subQ124])],"derivedFrom":makeQuery(id+"F31.boolean.opBoolean","SPLIT",FACE,{"disambiguationData":[TD([subQ124])],"derivedFrom":makeQuery(id+"F30.boolean.opBoolean","SPLIT",FACE,{"disambiguationData":[TD([subQ158])],"derivedFrom":makeQuery(id+"F29.boolean.opBoolean","SPLIT",FACE,{"disambiguationData":[TD([subQ158])],"derivedFrom":makeQuery(id+"F28.boolean.opBoolean","SPLIT",FACE,{"disambiguationData":[TD([subQ158])],"derivedFrom":makeQuery(id+"F27.boolean.opBoolean","SPLIT",FACE,{"disambiguationData":[TD([subQ158])],"derivedFrom":makeQuery(id+"F26.boolean.opBoolean","SPLIT",FACE,{"disambiguationData":[TD([subQ158])],"derivedFrom":makeQuery(id+"F25.boolean.opBoolean","SPLIT",FACE,{"disambiguationData":[TD([subQ158])],"derivedFrom":makeQuery(id+"F24.boolean.opBoolean","SPLIT",FACE,{"disambiguationData":[TD([subQ158])],"derivedFrom":makeQuery(id+"F1.opRevolve","SWEPT_FACE",FACE,{"disambiguationData":[OSD([sQuery(id+"F0.wireOp",EDGE,"E4")])]})})})})})})})})})})}),subQ37]});Q7=makeQuery(id+"F48.opFillet","BLEND_EDGE",EDGE,{"blendedFrom":[makeQuery(id+"F47.opFillet","TWEAK_EDGE",EDGE,{"derivedFrom":[makeQuery(id+"F45.opFillet","BLEND_VERTEX",VERTEX,{"blendedFrom":[subQ187,subQ37,subQ115],"blendedInto":[subQ37,subQ115]}),makeQuery(id+"F45.opFillet","BLEND_VERTEX",VERTEX,{"blendedFrom":[subQ187,makeQuery(id+"F42.boolean.opBoolean","MERGE",FACE,{"derivedFrom":[subQ2,subQ1]}),subQ115],"blendedInto":[makeQuery(id+"F42.boolean.opBoolean","MERGE",FACE,{"derivedFrom":[subQ2,subQ1]}),subQ115]})]}),makeQuery(id+"F47.opFillet","BLEND_FACE",FACE,{"disambiguationData":[OSD([subQ0,subQ9]),TDD([makeQuery(id+"F42.boolean.opBoolean","COPY",EDGE,{"disambiguationData":[TD([makeQuery(id+"F23.opLoft","SWEPT_FACE",FACE,{"disambiguationData":[OSD([sQuery(id+"F3.wireOp",EDGE,"E20.8.0"),subQ111,subQ109,subQ108,subQ107,sQuery(id+"F22.wireOp",EDGE,"E27.right")])]})])],"derivedFrom":subQ11})])]}),makeQuery(id+"F47.opFillet","BLEND_FACE",FACE,{"disambiguationData":[OSD([subQ0,subQ9]),TDD([makeQuery(id+"F42.boolean.opBoolean","COPY",EDGE,{"disambiguationData":[TD([subQ106])],"derivedFrom":subQ11})])]}),makeQuery(id+"F47.opFillet","BLEND_FACE",FACE,{"disambiguationData":[OSD([subQ0,subQ9]),TDD([makeQuery(id+"F42.boolean.opBoolean","COPY",EDGE,{"disambiguationData":[TD([subQ99])],"derivedFrom":subQ11})])]}),makeQuery(id+"F47.opFillet","BLEND_FACE",FACE,{"disambiguationData":[OSD([subQ0,subQ9]),TDD([makeQuery(id+"F42.boolean.opBoolean","COPY",EDGE,{"disambiguationData":[TD([subQ93])],"derivedFrom":subQ11})])]}),makeQuery(id+"F47.opFillet","BLEND_FACE",FACE,{"disambiguationData":[OSD([subQ0,subQ9]),TDD([makeQuery(id+"F42.boolean.opBoolean","COPY",EDGE,{"disambiguationData":[TD([subQ86])],"derivedFrom":subQ11})])]}),makeQuery(id+"F47.opFillet","BLEND_FACE",FACE,{"disambiguationData":[OSD([subQ0,subQ9]),TDD([makeQuery(id+"F42.boolean.opBoolean","COPY",EDGE,{"disambiguationData":[TD([subQ79])],"derivedFrom":subQ11})])]}),makeQuery(id+"F47.opFillet","BLEND_FACE",FACE,{"disambiguationData":[OSD([subQ0,subQ9]),TDD([makeQuery(id+"F42.boolean.opBoolean","COPY",EDGE,{"disambiguationData":[TD([subQ72])],"derivedFrom":subQ11})])]}),makeQuery(id+"F47.opFillet","BLEND_FACE",FACE,{"disambiguationData":[OSD([subQ0,subQ9]),TDD([makeQuery(id+"F42.boolean.opBoolean","COPY",EDGE,{"disambiguationData":[TD([subQ64])],"derivedFrom":subQ11})])]}),makeQuery(id+"F47.opFillet","BLEND_FACE",FACE,{"disambiguationData":[OSD([subQ0,subQ9]),TDD([makeQuery(id+"F42.boolean.opBoolean","COPY",EDGE,{"disambiguationData":[TD([subQ58])],"derivedFrom":subQ11})])]}),makeQuery(id+"F47.opFillet","BLEND_FACE",FACE,{"disambiguationData":[OSD([subQ0,subQ9]),TDD([makeQuery(id+"F42.boolean.opBoolean","COPY",EDGE,{"disambiguationData":[TD([subQ51])],"derivedFrom":subQ11})])]}),makeQuery(id+"F47.opFillet","BLEND_FACE",FACE,{"disambiguationData":[OSD([subQ0,subQ9]),TDD([makeQuery(id+"F42.boolean.opBoolean","COPY",EDGE,{"disambiguationData":[TD([subQ44])],"derivedFrom":subQ11})])]}),makeQuery(id+"F47.opFillet","BLEND_FACE",FACE,{"disambiguationData":[OSD([subQ0,subQ9]),TDD([makeQuery(id+"F42.boolean.opBoolean","COPY",EDGE,{"disambiguationData":[TD([subQ37])],"derivedFrom":subQ11})])]}),makeQuery(id+"F47.opFillet","BLEND_FACE",FACE,{"disambiguationData":[OSD([subQ0,subQ9]),TDD([makeQuery(id+"F42.boolean.opBoolean","COPY",EDGE,{"disambiguationData":[TD([makeQuery(id+"F35.opLoft","SWEPT_FACE",FACE,{"disambiguationData":[OSD([subQ29,subQ28,subQ26,sQuery(id+"F22.wireOp",EDGE,"E28.12.1"),subQ25,subQ24])]})])],"derivedFrom":subQ11})])]}),makeQuery(id+"F47.opFillet","BLEND_FACE",FACE,{"disambiguationData":[OSD([subQ0,subQ9]),TDD([makeQuery(id+"F42.boolean.opBoolean","COPY",EDGE,{"disambiguationData":[TD([makeQuery(id+"F36.opLoft","SWEPT_FACE",FACE,{"disambiguationData":[OSD([subQ23,subQ22,subQ20,sQuery(id+"F22.wireOp",EDGE,"E28.13.1"),subQ19,subQ18])]})])],"derivedFrom":subQ11})])]}),makeQuery(id+"F47.opFillet","BLEND_FACE",FACE,{"disambiguationData":[OSD([subQ0,subQ9]),TDD([makeQuery(id+"F42.boolean.opBoolean","COPY",EDGE,{"disambiguationData":[TD([makeQuery(id+"F37.opLoft","SWEPT_FACE",FACE,{"disambiguationData":[OSD([subQ16,subQ15,subQ14,sQuery(id+"F22.wireOp",EDGE,"E28.14.1"),subQ13,subQ12])]})])],"derivedFrom":subQ11})])]}),makeQuery(id+"F47.opFillet","BLEND_FACE",FACE,{"disambiguationData":[OSD([subQ0,subQ9]),TDD([makeQuery(id+"F42.boolean.opBoolean","COPY",EDGE,{"disambiguationData":[TD([makeQuery(id+"F38.opLoft","SWEPT_FACE",FACE,{"disambiguationData":[OSD([subQ8,subQ7,subQ5,sQuery(id+"F22.wireOp",EDGE,"E28.15.1"),subQ4,subQ3])]})])],"derivedFrom":subQ11})])]})],"blendedInto":[makeQuery(id+"F47.opFillet","BLEND_FACE",FACE,{"disambiguationData":[OSD([subQ0,subQ9]),TDD([makeQuery(id+"F42.boolean.opBoolean","COPY",EDGE,{"disambiguationData":[TD([makeQuery(id+"F23.opLoft","SWEPT_FACE",FACE,{"disambiguationData":[OSD([sQuery(id+"F3.wireOp",EDGE,"E20.8.0"),subQ111,subQ109,subQ108,subQ107,sQuery(id+"F22.wireOp",EDGE,"E27.right")])]})])],"derivedFrom":subQ11})])]}),makeQuery(id+"F47.opFillet","BLEND_FACE",FACE,{"disambiguationData":[OSD([subQ0,subQ9]),TDD([makeQuery(id+"F42.boolean.opBoolean","COPY",EDGE,{"disambiguationData":[TD([subQ106])],"derivedFrom":subQ11})])]}),makeQuery(id+"F47.opFillet","BLEND_FACE",FACE,{"disambiguationData":[OSD([subQ0,subQ9]),TDD([makeQuery(id+"F42.boolean.opBoolean","COPY",EDGE,{"disambiguationData":[TD([subQ99])],"derivedFrom":subQ11})])]}),makeQuery(id+"F47.opFillet","BLEND_FACE",FACE,{"disambiguationData":[OSD([subQ0,subQ9]),TDD([makeQuery(id+"F42.boolean.opBoolean","COPY",EDGE,{"disambiguationData":[TD([subQ93])],"derivedFrom":subQ11})])]}),makeQuery(id+"F47.opFillet","BLEND_FACE",FACE,{"disambiguationData":[OSD([subQ0,subQ9]),TDD([makeQuery(id+"F42.boolean.opBoolean","COPY",EDGE,{"disambiguationData":[TD([subQ86])],"derivedFrom":subQ11})])]}),makeQuery(id+"F47.opFillet","BLEND_FACE",FACE,{"disambiguationData":[OSD([subQ0,subQ9]),TDD([makeQuery(id+"F42.boolean.opBoolean","COPY",EDGE,{"disambiguationData":[TD([subQ79])],"derivedFrom":subQ11})])]}),makeQuery(id+"F47.opFillet","BLEND_FACE",FACE,{"disambiguationData":[OSD([subQ0,subQ9]),TDD([makeQuery(id+"F42.boolean.opBoolean","COPY",EDGE,{"disambiguationData":[TD([subQ72])],"derivedFrom":subQ11})])]}),makeQuery(id+"F47.opFillet","BLEND_FACE",FACE,{"disambiguationData":[OSD([subQ0,subQ9]),TDD([makeQuery(id+"F42.boolean.opBoolean","COPY",EDGE,{"disambiguationData":[TD([subQ64])],"derivedFrom":subQ11})])]}),makeQuery(id+"F47.opFillet","BLEND_FACE",FACE,{"disambiguationData":[OSD([subQ0,subQ9]),TDD([makeQuery(id+"F42.boolean.opBoolean","COPY",EDGE,{"disambiguationData":[TD([subQ58])],"derivedFrom":subQ11})])]}),makeQuery(id+"F47.opFillet","BLEND_FACE",FACE,{"disambiguationData":[OSD([subQ0,subQ9]),TDD([makeQuery(id+"F42.boolean.opBoolean","COPY",EDGE,{"disambiguationData":[TD([subQ51])],"derivedFrom":subQ11})])]}),makeQuery(id+"F47.opFillet","BLEND_FACE",FACE,{"disambiguationData":[OSD([subQ0,subQ9]),TDD([makeQuery(id+"F42.boolean.opBoolean","COPY",EDGE,{"disambiguationData":[TD([subQ44])],"derivedFrom":subQ11})])]}),makeQuery(id+"F47.opFillet","BLEND_FACE",FACE,{"disambiguationData":[OSD([subQ0,subQ9]),TDD([makeQuery(id+"F42.boolean.opBoolean","COPY",EDGE,{"disambiguationData":[TD([subQ37])],"derivedFrom":subQ11})])]}),makeQuery(id+"F47.opFillet","BLEND_FACE",FACE,{"disambiguationData":[OSD([subQ0,subQ9]),TDD([makeQuery(id+"F42.boolean.opBoolean","COPY",EDGE,{"disambiguationData":[TD([makeQuery(id+"F35.opLoft","SWEPT_FACE",FACE,{"disambiguationData":[OSD([subQ29,subQ28,subQ26,sQuery(id+"F22.wireOp",EDGE,"E28.12.1"),subQ25,subQ24])]})])],"derivedFrom":subQ11})])]}),makeQuery(id+"F47.opFillet","BLEND_FACE",FACE,{"disambiguationData":[OSD([subQ0,subQ9]),TDD([makeQuery(id+"F42.boolean.opBoolean","COPY",EDGE,{"disambiguationData":[TD([makeQuery(id+"F36.opLoft","SWEPT_FACE",FACE,{"disambiguationData":[OSD([subQ23,subQ22,subQ20,sQuery(id+"F22.wireOp",EDGE,"E28.13.1"),subQ19,subQ18])]})])],"derivedFrom":subQ11})])]}),makeQuery(id+"F47.opFillet","BLEND_FACE",FACE,{"disambiguationData":[OSD([subQ0,subQ9]),TDD([makeQuery(id+"F42.boolean.opBoolean","COPY",EDGE,{"disambiguationData":[TD([makeQuery(id+"F37.opLoft","SWEPT_FACE",FACE,{"disambiguationData":[OSD([subQ16,subQ15,subQ14,sQuery(id+"F22.wireOp",EDGE,"E28.14.1"),subQ13,subQ12])]})])],"derivedFrom":subQ11})])]}),makeQuery(id+"F47.opFillet","BLEND_FACE",FACE,{"disambiguationData":[OSD([subQ0,subQ9]),TDD([makeQuery(id+"F42.boolean.opBoolean","COPY",EDGE,{"disambiguationData":[TD([makeQuery(id+"F38.opLoft","SWEPT_FACE",FACE,{"disambiguationData":[OSD([subQ8,subQ7,subQ5,sQuery(id+"F22.wireOp",EDGE,"E28.15.1"),subQ4,subQ3])]})])],"derivedFrom":subQ11})])]})]});}
            var Q8;
            {var subQ0=sQuery(id+"F41.wireOp",EDGE,"E34");var subQ1=sQuery(id+"F41.wireOp",EDGE,"E32");Q8=makeQuery(id+"F42.boolean.opBoolean","INTERSECT",EDGE,{"derivedFrom":[makeQuery(id+"F34.opLoft","SWEPT_FACE",FACE,{"disambiguationData":[OSD([sQuery(id+"F3.wireOp",EDGE,"E20.3.0"),sQuery(id+"F3.wireOp",EDGE,"E20.3.1"),sQuery(id+"F3.wireOp",EDGE,"E20.3.3"),sQuery(id+"F22.wireOp",EDGE,"E28.11.1"),sQuery(id+"F22.wireOp",EDGE,"E28.11.2"),sQuery(id+"F22.wireOp",EDGE,"E28.11.3")])]}),makeQuery(id+"F42.opRevolve","SWEPT_FACE",FACE,{"disambiguationData":[OSD([subQ1]),TDD([makeQuery(id+"F41.imprint","IMPRINT",EDGE,{"disambiguationData":[TD([[makeQuery(id+"F41.imprint","INTERSECT",VERTEX,{"disambiguationData":[OD(0.0)],"derivedFrom":[subQ1,subQ0]}),-1.0]])],"derivedFrom":subQ1})])]})]});}
            var Q9;
            {var subQ0=sQuery(id+"F22.wireOp",EDGE,"E28.11.3");var subQ1=sQuery(id+"F22.wireOp",EDGE,"E28.11.2");var subQ2=sQuery(id+"F22.wireOp",EDGE,"E28.11.0");var subQ3=sQuery(id+"F3.wireOp",EDGE,"E20.3.3");var subQ4=sQuery(id+"F3.wireOp",EDGE,"E20.3.1");var subQ5=makeQuery(id+"F34.opLoft","SWEPT_FACE",FACE,{"disambiguationData":[OSD([subQ4,sQuery(id+"F3.wireOp",EDGE,"E20.3.2"),subQ3,subQ2,subQ1,subQ0])]});var subQ6=sQuery(id+"F22.wireOp",EDGE,"E28.11.1");var subQ7=sQuery(id+"F41.wireOp",EDGE,"E34");var subQ8=sQuery(id+"F41.wireOp",EDGE,"E32");Q9=makeQuery(id+"F44.opFillet","BLEND_EDGE",EDGE,{"blendedFrom":[makeQuery(id+"F40.boolean.opBoolean","INTERSECT",EDGE,{"derivedFrom":[subQ5,makeQuery(id+"F40.opExtrude","CAP_FACE",FACE,{"disambiguationData":[OSD([sQuery(id+"F39.wireOp",EDGE,"E29"),sQuery(id+"F39.wireOp",EDGE,"E30")])],"isStart":true})]}),makeQuery(id+"F42.boolean.opBoolean","COPY",FACE,{"disambiguationData":[TD([makeQuery(id+"F34.opLoft","SWEPT_FACE",FACE,{"disambiguationData":[OSD([sQuery(id+"F3.wireOp",EDGE,"E20.3.0"),subQ4,subQ3,subQ6,subQ1,subQ0])]})])],"derivedFrom":makeQuery(id+"F42.opRevolve","SWEPT_FACE",FACE,{"disambiguationData":[OSD([subQ8]),TDD([makeQuery(id+"F41.imprint","IMPRINT",EDGE,{"disambiguationData":[TD([[makeQuery(id+"F41.imprint","INTERSECT",VERTEX,{"disambiguationData":[OD(0.0)],"derivedFrom":[subQ8,subQ7]}),-1.0]])],"derivedFrom":subQ8})])]})})],"blendedInto":[makeQuery(id+"F42.boolean.opBoolean","COPY",FACE,{"disambiguationData":[TD([makeQuery(id+"F34.opLoft","SWEPT_FACE",FACE,{"disambiguationData":[OSD([sQuery(id+"F3.wireOp",EDGE,"E20.3.0"),subQ4,subQ3,subQ6,subQ1,subQ0])]})])],"derivedFrom":makeQuery(id+"F42.opRevolve","SWEPT_FACE",FACE,{"disambiguationData":[OSD([subQ8]),TDD([makeQuery(id+"F41.imprint","IMPRINT",EDGE,{"disambiguationData":[TD([[makeQuery(id+"F41.imprint","INTERSECT",VERTEX,{"disambiguationData":[OD(0.0)],"derivedFrom":[subQ8,subQ7]}),-1.0]])],"derivedFrom":subQ8})])]})})]});}
            var Q10;
            {var subQ0=sQuery(id+"F3.wireOp",EDGE,"E20.2.3");var subQ1=sQuery(id+"F3.wireOp",EDGE,"E20.2.1");var subQ2=sQuery(id+"F3.wireOp",EDGE,"E20.2.0");var subQ3=makeQuery(id+"F33.opLoft","SWEPT_FACE",FACE,{"disambiguationData":[OSD([subQ2,subQ1,subQ0,sQuery(id+"F22.wireOp",EDGE,"E28.10.1"),sQuery(id+"F22.wireOp",EDGE,"E28.10.2"),sQuery(id+"F22.wireOp",EDGE,"E28.10.3")])]});var subQ52=sQuery(id+"F3.wireOp",EDGE,"E20.7.0");var subQ61=makeQuery(id+"F14.opLoft","CAP_FACE",FACE,{"disambiguationData":[OSD([makeQuery(id+"F3.imprint","IMPRINT",FACE,{"disambiguationData":[TD([[makeQuery(id+"F3.imprint","IMPRINT",EDGE,{"derivedFrom":subQ52}),-1.0]])]})])],"isStart":true});var subQ74=sQuery(id+"F3.wireOp",EDGE,"E18.bottom");var subQ79=makeQuery(id+"F5.opLoft","CAP_FACE",FACE,{"disambiguationData":[OSD([makeQuery(id+"F3.imprint","IMPRINT",FACE,{"disambiguationData":[TD([[makeQuery(id+"F3.imprint","IMPRINT",EDGE,{"derivedFrom":subQ74}),1.0]])]})])],"isStart":true});Q10=makeQuery(id+"F45.opFillet","BLEND_EDGE",EDGE,{"blendedFrom":[makeQuery(id+"F33.boolean.opBoolean","INTERSECT",EDGE,{"derivedFrom":[makeQuery(id+"F32.boolean.opBoolean","SPLIT",FACE,{"disambiguationData":[TD([subQ61])],"derivedFrom":makeQuery(id+"F31.boolean.opBoolean","SPLIT",FACE,{"disambiguationData":[TD([subQ61])],"derivedFrom":makeQuery(id+"F30.boolean.opBoolean","SPLIT",FACE,{"disambiguationData":[TD([subQ79])],"derivedFrom":makeQuery(id+"F29.boolean.opBoolean","SPLIT",FACE,{"disambiguationData":[TD([subQ79])],"derivedFrom":makeQuery(id+"F28.boolean.opBoolean","SPLIT",FACE,{"disambiguationData":[TD([subQ79])],"derivedFrom":makeQuery(id+"F27.boolean.opBoolean","SPLIT",FACE,{"disambiguationData":[TD([subQ79])],"derivedFrom":makeQuery(id+"F26.boolean.opBoolean","SPLIT",FACE,{"disambiguationData":[TD([subQ79])],"derivedFrom":makeQuery(id+"F25.boolean.opBoolean","SPLIT",FACE,{"disambiguationData":[TD([subQ79])],"derivedFrom":makeQuery(id+"F24.boolean.opBoolean","SPLIT",FACE,{"disambiguationData":[TD([subQ79])],"derivedFrom":makeQuery(id+"F1.opRevolve","SWEPT_FACE",FACE,{"disambiguationData":[OSD([sQuery(id+"F0.wireOp",EDGE,"E4")])]})})})})})})})})})}),subQ3]}),subQ3],"blendedInto":[subQ3]});}
            var Q11;
            {var subQ0=sQuery(id+"F41.wireOp",EDGE,"E37");var subQ1=makeQuery(id+"F42.opRevolve","SWEPT_FACE",FACE,{"disambiguationData":[OSD([subQ0])]});var subQ2=makeQuery(id+"F40.opExtrude","CAP_FACE",FACE,{"disambiguationData":[OSD([sQuery(id+"F39.wireOp",EDGE,"E29"),sQuery(id+"F39.wireOp",EDGE,"E30")])],"isStart":true});var subQ3=sQuery(id+"F22.wireOp",EDGE,"E28.15.3");var subQ4=sQuery(id+"F22.wireOp",EDGE,"E28.15.2");var subQ5=sQuery(id+"F3.wireOp",EDGE,"E20.7.3");var subQ7=sQuery(id+"F3.wireOp",EDGE,"E20.7.1");var subQ8=sQuery(id+"F3.wireOp",EDGE,"E20.7.0");var subQ9=sQuery(id+"F41.wireOp",EDGE,"E38");var subQ10=makeQuery(id+"F42.opRevolve","SWEPT_FACE",FACE,{"disambiguationData":[OSD([subQ9])]});var subQ11=makeQuery(id+"F42.opRevolve","SWEPT_EDGE",EDGE,{"disambiguationData":[OSD([subQ0,subQ9])]});var subQ12=sQuery(id+"F22.wireOp",EDGE,"E28.14.3");var subQ13=sQuery(id+"F22.wireOp",EDGE,"E28.14.2");var subQ14=sQuery(id+"F3.wireOp",EDGE,"E20.6.3");var subQ15=sQuery(id+"F3.wireOp",EDGE,"E20.6.1");var subQ16=sQuery(id+"F3.wireOp",EDGE,"E20.6.0");var subQ18=sQuery(id+"F22.wireOp",EDGE,"E28.13.3");var subQ19=sQuery(id+"F22.wireOp",EDGE,"E28.13.2");var subQ20=sQuery(id+"F3.wireOp",EDGE,"E20.5.3");var subQ22=sQuery(id+"F3.wireOp",EDGE,"E20.5.1");var subQ23=sQuery(id+"F3.wireOp",EDGE,"E20.5.0");var subQ24=sQuery(id+"F22.wireOp",EDGE,"E28.12.3");var subQ25=sQuery(id+"F22.wireOp",EDGE,"E28.12.2");var subQ26=sQuery(id+"F3.wireOp",EDGE,"E20.4.3");var subQ28=sQuery(id+"F3.wireOp",EDGE,"E20.4.1");var subQ29=sQuery(id+"F3.wireOp",EDGE,"E20.4.0");var subQ30=sQuery(id+"F22.wireOp",EDGE,"E28.11.3");var subQ31=sQuery(id+"F22.wireOp",EDGE,"E28.11.2");var subQ32=sQuery(id+"F3.wireOp",EDGE,"E20.3.3");var subQ34=sQuery(id+"F3.wireOp",EDGE,"E20.3.1");var subQ35=sQuery(id+"F3.wireOp",EDGE,"E20.3.0");var subQ36=sQuery(id+"F22.wireOp",EDGE,"E28.10.3");var subQ37=sQuery(id+"F22.wireOp",EDGE,"E28.10.2");var subQ38=sQuery(id+"F3.wireOp",EDGE,"E20.2.3");var subQ40=sQuery(id+"F3.wireOp",EDGE,"E20.2.1");var subQ42=sQuery(id+"F3.wireOp",EDGE,"E20.2.0");var subQ43=makeQuery(id+"F33.opLoft","SWEPT_FACE",FACE,{"disambiguationData":[OSD([subQ42,subQ40,subQ38,sQuery(id+"F22.wireOp",EDGE,"E28.10.1"),subQ37,subQ36])]});var subQ44=sQuery(id+"F22.wireOp",EDGE,"E28.9.3");var subQ45=sQuery(id+"F22.wireOp",EDGE,"E28.9.2");var subQ46=sQuery(id+"F3.wireOp",EDGE,"E20.1.3");var subQ48=sQuery(id+"F3.wireOp",EDGE,"E20.1.1");var subQ49=sQuery(id+"F3.wireOp",EDGE,"E20.1.0");var subQ50=makeQuery(id+"F32.opLoft","SWEPT_FACE",FACE,{"disambiguationData":[OSD([subQ49,subQ48,subQ46,sQuery(id+"F22.wireOp",EDGE,"E28.9.1"),subQ45,subQ44])]});var subQ51=sQuery(id+"F22.wireOp",EDGE,"E28.8.3");var subQ52=sQuery(id+"F22.wireOp",EDGE,"E28.8.2");var subQ54=sQuery(id+"F3.wireOp",EDGE,"E18.top");var subQ55=sQuery(id+"F3.wireOp",EDGE,"E18.bottom");var subQ56=sQuery(id+"F3.wireOp",EDGE,"E18.left");var subQ57=makeQuery(id+"F31.opLoft","SWEPT_FACE",FACE,{"disambiguationData":[OSD([subQ55,subQ54,subQ56,sQuery(id+"F22.wireOp",EDGE,"E28.8.1"),subQ52,subQ51])]});var subQ58=sQuery(id+"F22.wireOp",EDGE,"E28.7.3");var subQ59=sQuery(id+"F22.wireOp",EDGE,"E28.7.2");var subQ60=sQuery(id+"F3.wireOp",EDGE,"E20.15.3");var subQ61=sQuery(id+"F3.wireOp",EDGE,"E20.15.1");var subQ62=sQuery(id+"F3.wireOp",EDGE,"E20.15.0");var subQ63=makeQuery(id+"F30.opLoft","SWEPT_FACE",FACE,{"disambiguationData":[OSD([subQ62,subQ61,subQ60,sQuery(id+"F22.wireOp",EDGE,"E28.7.1"),subQ59,subQ58])]});var subQ65=sQuery(id+"F22.wireOp",EDGE,"E28.6.3");var subQ66=sQuery(id+"F22.wireOp",EDGE,"E28.6.2");var subQ67=sQuery(id+"F3.wireOp",EDGE,"E20.14.3");var subQ69=sQuery(id+"F3.wireOp",EDGE,"E20.14.1");var subQ70=sQuery(id+"F3.wireOp",EDGE,"E20.14.0");var subQ71=makeQuery(id+"F29.opLoft","SWEPT_FACE",FACE,{"disambiguationData":[OSD([subQ70,subQ69,subQ67,sQuery(id+"F22.wireOp",EDGE,"E28.6.1"),subQ66,subQ65])]});var subQ72=sQuery(id+"F22.wireOp",EDGE,"E28.5.3");var subQ73=sQuery(id+"F22.wireOp",EDGE,"E28.5.2");var subQ74=sQuery(id+"F3.wireOp",EDGE,"E20.13.3");var subQ76=sQuery(id+"F3.wireOp",EDGE,"E20.13.1");var subQ77=sQuery(id+"F3.wireOp",EDGE,"E20.13.0");var subQ78=makeQuery(id+"F28.opLoft","SWEPT_FACE",FACE,{"disambiguationData":[OSD([subQ77,subQ76,subQ74,sQuery(id+"F22.wireOp",EDGE,"E28.5.1"),subQ73,subQ72])]});var subQ79=sQuery(id+"F22.wireOp",EDGE,"E28.4.3");var subQ80=sQuery(id+"F22.wireOp",EDGE,"E28.4.2");var subQ81=sQuery(id+"F3.wireOp",EDGE,"E20.12.3");var subQ83=sQuery(id+"F3.wireOp",EDGE,"E20.12.1");var subQ84=sQuery(id+"F3.wireOp",EDGE,"E20.12.0");var subQ85=makeQuery(id+"F27.opLoft","SWEPT_FACE",FACE,{"disambiguationData":[OSD([subQ84,subQ83,subQ81,sQuery(id+"F22.wireOp",EDGE,"E28.4.1"),subQ80,subQ79])]});var subQ86=sQuery(id+"F22.wireOp",EDGE,"E28.3.3");var subQ87=sQuery(id+"F22.wireOp",EDGE,"E28.3.2");var subQ88=sQuery(id+"F3.wireOp",EDGE,"E20.11.3");var subQ90=sQuery(id+"F3.wireOp",EDGE,"E20.11.1");var subQ91=sQuery(id+"F3.wireOp",EDGE,"E20.11.0");var subQ92=makeQuery(id+"F26.opLoft","SWEPT_FACE",FACE,{"disambiguationData":[OSD([subQ91,subQ90,subQ88,sQuery(id+"F22.wireOp",EDGE,"E28.3.1"),subQ87,subQ86])]});var subQ93=sQuery(id+"F22.wireOp",EDGE,"E28.2.3");var subQ94=sQuery(id+"F22.wireOp",EDGE,"E28.2.2");var subQ95=sQuery(id+"F3.wireOp",EDGE,"E20.10.3");var subQ96=sQuery(id+"F3.wireOp",EDGE,"E20.10.1");var subQ97=sQuery(id+"F3.wireOp",EDGE,"E20.10.0");var subQ98=makeQuery(id+"F25.opLoft","SWEPT_FACE",FACE,{"disambiguationData":[OSD([subQ97,subQ96,subQ95,sQuery(id+"F22.wireOp",EDGE,"E28.2.1"),subQ94,subQ93])]});var subQ100=sQuery(id+"F22.wireOp",EDGE,"E28.1.3");var subQ101=sQuery(id+"F22.wireOp",EDGE,"E28.1.2");var subQ102=sQuery(id+"F3.wireOp",EDGE,"E20.9.3");var subQ103=sQuery(id+"F3.wireOp",EDGE,"E20.9.1");var subQ104=sQuery(id+"F3.wireOp",EDGE,"E20.9.0");var subQ105=makeQuery(id+"F24.opLoft","SWEPT_FACE",FACE,{"disambiguationData":[OSD([subQ104,subQ103,subQ102,sQuery(id+"F22.wireOp",EDGE,"E28.1.1"),subQ101,subQ100])]});var subQ106=sQuery(id+"F22.wireOp",EDGE,"E27.top");var subQ107=sQuery(id+"F22.wireOp",EDGE,"E27.bottom");var subQ108=sQuery(id+"F3.wireOp",EDGE,"E20.8.3");var subQ110=sQuery(id+"F3.wireOp",EDGE,"E20.8.1");var subQ114=makeQuery(id+"F42.boolean.opBoolean","COPY",FACE,{"disambiguationData":[TD([subQ43])],"derivedFrom":subQ10});var subQ146=makeQuery(id+"F14.opLoft","CAP_FACE",FACE,{"disambiguationData":[OSD([makeQuery(id+"F3.imprint","IMPRINT",FACE,{"disambiguationData":[TD([[makeQuery(id+"F3.imprint","IMPRINT",EDGE,{"derivedFrom":subQ8}),-1.0]])]})])],"isStart":true});var subQ157=makeQuery(id+"F5.opLoft","CAP_FACE",FACE,{"disambiguationData":[OSD([makeQuery(id+"F3.imprint","IMPRINT",FACE,{"disambiguationData":[TD([[makeQuery(id+"F3.imprint","IMPRINT",EDGE,{"derivedFrom":subQ55}),1.0]])]})])],"isStart":true});var subQ186=makeQuery(id+"F33.boolean.opBoolean","INTERSECT",EDGE,{"derivedFrom":[makeQuery(id+"F32.boolean.opBoolean","SPLIT",FACE,{"disambiguationData":[TD([subQ146])],"derivedFrom":makeQuery(id+"F31.boolean.opBoolean","SPLIT",FACE,{"disambiguationData":[TD([subQ146])],"derivedFrom":makeQuery(id+"F30.boolean.opBoolean","SPLIT",FACE,{"disambiguationData":[TD([subQ157])],"derivedFrom":makeQuery(id+"F29.boolean.opBoolean","SPLIT",FACE,{"disambiguationData":[TD([subQ157])],"derivedFrom":makeQuery(id+"F28.boolean.opBoolean","SPLIT",FACE,{"disambiguationData":[TD([subQ157])],"derivedFrom":makeQuery(id+"F27.boolean.opBoolean","SPLIT",FACE,{"disambiguationData":[TD([subQ157])],"derivedFrom":makeQuery(id+"F26.boolean.opBoolean","SPLIT",FACE,{"disambiguationData":[TD([subQ157])],"derivedFrom":makeQuery(id+"F25.boolean.opBoolean","SPLIT",FACE,{"disambiguationData":[TD([subQ157])],"derivedFrom":makeQuery(id+"F24.boolean.opBoolean","SPLIT",FACE,{"disambiguationData":[TD([subQ157])],"derivedFrom":makeQuery(id+"F1.opRevolve","SWEPT_FACE",FACE,{"disambiguationData":[OSD([sQuery(id+"F0.wireOp",EDGE,"E4")])]})})})})})})})})})}),subQ43]});Q11=makeQuery(id+"F48.opFillet","BLEND_EDGE",EDGE,{"blendedFrom":[makeQuery(id+"F47.opFillet","TWEAK_EDGE",EDGE,{"derivedFrom":[makeQuery(id+"F45.opFillet","BLEND_VERTEX",VERTEX,{"blendedFrom":[subQ186,subQ43,subQ114],"blendedInto":[subQ43,subQ114]}),makeQuery(id+"F45.opFillet","BLEND_VERTEX",VERTEX,{"blendedFrom":[subQ186,makeQuery(id+"F42.boolean.opBoolean","MERGE",FACE,{"derivedFrom":[subQ2,subQ1]}),subQ114],"blendedInto":[makeQuery(id+"F42.boolean.opBoolean","MERGE",FACE,{"derivedFrom":[subQ2,subQ1]}),subQ114]})]}),makeQuery(id+"F47.opFillet","BLEND_FACE",FACE,{"disambiguationData":[OSD([subQ0,subQ9]),TDD([makeQuery(id+"F42.boolean.opBoolean","COPY",EDGE,{"disambiguationData":[TD([makeQuery(id+"F23.opLoft","SWEPT_FACE",FACE,{"disambiguationData":[OSD([sQuery(id+"F3.wireOp",EDGE,"E20.8.0"),subQ110,subQ108,subQ107,subQ106,sQuery(id+"F22.wireOp",EDGE,"E27.right")])]})])],"derivedFrom":subQ11})])]}),makeQuery(id+"F47.opFillet","BLEND_FACE",FACE,{"disambiguationData":[OSD([subQ0,subQ9]),TDD([makeQuery(id+"F42.boolean.opBoolean","COPY",EDGE,{"disambiguationData":[TD([subQ105])],"derivedFrom":subQ11})])]}),makeQuery(id+"F47.opFillet","BLEND_FACE",FACE,{"disambiguationData":[OSD([subQ0,subQ9]),TDD([makeQuery(id+"F42.boolean.opBoolean","COPY",EDGE,{"disambiguationData":[TD([subQ98])],"derivedFrom":subQ11})])]}),makeQuery(id+"F47.opFillet","BLEND_FACE",FACE,{"disambiguationData":[OSD([subQ0,subQ9]),TDD([makeQuery(id+"F42.boolean.opBoolean","COPY",EDGE,{"disambiguationData":[TD([subQ92])],"derivedFrom":subQ11})])]}),makeQuery(id+"F47.opFillet","BLEND_FACE",FACE,{"disambiguationData":[OSD([subQ0,subQ9]),TDD([makeQuery(id+"F42.boolean.opBoolean","COPY",EDGE,{"disambiguationData":[TD([subQ85])],"derivedFrom":subQ11})])]}),makeQuery(id+"F47.opFillet","BLEND_FACE",FACE,{"disambiguationData":[OSD([subQ0,subQ9]),TDD([makeQuery(id+"F42.boolean.opBoolean","COPY",EDGE,{"disambiguationData":[TD([subQ78])],"derivedFrom":subQ11})])]}),makeQuery(id+"F47.opFillet","BLEND_FACE",FACE,{"disambiguationData":[OSD([subQ0,subQ9]),TDD([makeQuery(id+"F42.boolean.opBoolean","COPY",EDGE,{"disambiguationData":[TD([subQ71])],"derivedFrom":subQ11})])]}),makeQuery(id+"F47.opFillet","BLEND_FACE",FACE,{"disambiguationData":[OSD([subQ0,subQ9]),TDD([makeQuery(id+"F42.boolean.opBoolean","COPY",EDGE,{"disambiguationData":[TD([subQ63])],"derivedFrom":subQ11})])]}),makeQuery(id+"F47.opFillet","BLEND_FACE",FACE,{"disambiguationData":[OSD([subQ0,subQ9]),TDD([makeQuery(id+"F42.boolean.opBoolean","COPY",EDGE,{"disambiguationData":[TD([subQ57])],"derivedFrom":subQ11})])]}),makeQuery(id+"F47.opFillet","BLEND_FACE",FACE,{"disambiguationData":[OSD([subQ0,subQ9]),TDD([makeQuery(id+"F42.boolean.opBoolean","COPY",EDGE,{"disambiguationData":[TD([subQ50])],"derivedFrom":subQ11})])]}),makeQuery(id+"F47.opFillet","BLEND_FACE",FACE,{"disambiguationData":[OSD([subQ0,subQ9]),TDD([makeQuery(id+"F42.boolean.opBoolean","COPY",EDGE,{"disambiguationData":[TD([subQ43])],"derivedFrom":subQ11})])]}),makeQuery(id+"F47.opFillet","BLEND_FACE",FACE,{"disambiguationData":[OSD([subQ0,subQ9]),TDD([makeQuery(id+"F42.boolean.opBoolean","COPY",EDGE,{"disambiguationData":[TD([makeQuery(id+"F34.opLoft","SWEPT_FACE",FACE,{"disambiguationData":[OSD([subQ35,subQ34,subQ32,sQuery(id+"F22.wireOp",EDGE,"E28.11.1"),subQ31,subQ30])]})])],"derivedFrom":subQ11})])]}),makeQuery(id+"F47.opFillet","BLEND_FACE",FACE,{"disambiguationData":[OSD([subQ0,subQ9]),TDD([makeQuery(id+"F42.boolean.opBoolean","COPY",EDGE,{"disambiguationData":[TD([makeQuery(id+"F35.opLoft","SWEPT_FACE",FACE,{"disambiguationData":[OSD([subQ29,subQ28,subQ26,sQuery(id+"F22.wireOp",EDGE,"E28.12.1"),subQ25,subQ24])]})])],"derivedFrom":subQ11})])]}),makeQuery(id+"F47.opFillet","BLEND_FACE",FACE,{"disambiguationData":[OSD([subQ0,subQ9]),TDD([makeQuery(id+"F42.boolean.opBoolean","COPY",EDGE,{"disambiguationData":[TD([makeQuery(id+"F36.opLoft","SWEPT_FACE",FACE,{"disambiguationData":[OSD([subQ23,subQ22,subQ20,sQuery(id+"F22.wireOp",EDGE,"E28.13.1"),subQ19,subQ18])]})])],"derivedFrom":subQ11})])]}),makeQuery(id+"F47.opFillet","BLEND_FACE",FACE,{"disambiguationData":[OSD([subQ0,subQ9]),TDD([makeQuery(id+"F42.boolean.opBoolean","COPY",EDGE,{"disambiguationData":[TD([makeQuery(id+"F37.opLoft","SWEPT_FACE",FACE,{"disambiguationData":[OSD([subQ16,subQ15,subQ14,sQuery(id+"F22.wireOp",EDGE,"E28.14.1"),subQ13,subQ12])]})])],"derivedFrom":subQ11})])]}),makeQuery(id+"F47.opFillet","BLEND_FACE",FACE,{"disambiguationData":[OSD([subQ0,subQ9]),TDD([makeQuery(id+"F42.boolean.opBoolean","COPY",EDGE,{"disambiguationData":[TD([makeQuery(id+"F38.opLoft","SWEPT_FACE",FACE,{"disambiguationData":[OSD([subQ8,subQ7,subQ5,sQuery(id+"F22.wireOp",EDGE,"E28.15.1"),subQ4,subQ3])]})])],"derivedFrom":subQ11})])]})],"blendedInto":[makeQuery(id+"F47.opFillet","BLEND_FACE",FACE,{"disambiguationData":[OSD([subQ0,subQ9]),TDD([makeQuery(id+"F42.boolean.opBoolean","COPY",EDGE,{"disambiguationData":[TD([makeQuery(id+"F23.opLoft","SWEPT_FACE",FACE,{"disambiguationData":[OSD([sQuery(id+"F3.wireOp",EDGE,"E20.8.0"),subQ110,subQ108,subQ107,subQ106,sQuery(id+"F22.wireOp",EDGE,"E27.right")])]})])],"derivedFrom":subQ11})])]}),makeQuery(id+"F47.opFillet","BLEND_FACE",FACE,{"disambiguationData":[OSD([subQ0,subQ9]),TDD([makeQuery(id+"F42.boolean.opBoolean","COPY",EDGE,{"disambiguationData":[TD([subQ105])],"derivedFrom":subQ11})])]}),makeQuery(id+"F47.opFillet","BLEND_FACE",FACE,{"disambiguationData":[OSD([subQ0,subQ9]),TDD([makeQuery(id+"F42.boolean.opBoolean","COPY",EDGE,{"disambiguationData":[TD([subQ98])],"derivedFrom":subQ11})])]}),makeQuery(id+"F47.opFillet","BLEND_FACE",FACE,{"disambiguationData":[OSD([subQ0,subQ9]),TDD([makeQuery(id+"F42.boolean.opBoolean","COPY",EDGE,{"disambiguationData":[TD([subQ92])],"derivedFrom":subQ11})])]}),makeQuery(id+"F47.opFillet","BLEND_FACE",FACE,{"disambiguationData":[OSD([subQ0,subQ9]),TDD([makeQuery(id+"F42.boolean.opBoolean","COPY",EDGE,{"disambiguationData":[TD([subQ85])],"derivedFrom":subQ11})])]}),makeQuery(id+"F47.opFillet","BLEND_FACE",FACE,{"disambiguationData":[OSD([subQ0,subQ9]),TDD([makeQuery(id+"F42.boolean.opBoolean","COPY",EDGE,{"disambiguationData":[TD([subQ78])],"derivedFrom":subQ11})])]}),makeQuery(id+"F47.opFillet","BLEND_FACE",FACE,{"disambiguationData":[OSD([subQ0,subQ9]),TDD([makeQuery(id+"F42.boolean.opBoolean","COPY",EDGE,{"disambiguationData":[TD([subQ71])],"derivedFrom":subQ11})])]}),makeQuery(id+"F47.opFillet","BLEND_FACE",FACE,{"disambiguationData":[OSD([subQ0,subQ9]),TDD([makeQuery(id+"F42.boolean.opBoolean","COPY",EDGE,{"disambiguationData":[TD([subQ63])],"derivedFrom":subQ11})])]}),makeQuery(id+"F47.opFillet","BLEND_FACE",FACE,{"disambiguationData":[OSD([subQ0,subQ9]),TDD([makeQuery(id+"F42.boolean.opBoolean","COPY",EDGE,{"disambiguationData":[TD([subQ57])],"derivedFrom":subQ11})])]}),makeQuery(id+"F47.opFillet","BLEND_FACE",FACE,{"disambiguationData":[OSD([subQ0,subQ9]),TDD([makeQuery(id+"F42.boolean.opBoolean","COPY",EDGE,{"disambiguationData":[TD([subQ50])],"derivedFrom":subQ11})])]}),makeQuery(id+"F47.opFillet","BLEND_FACE",FACE,{"disambiguationData":[OSD([subQ0,subQ9]),TDD([makeQuery(id+"F42.boolean.opBoolean","COPY",EDGE,{"disambiguationData":[TD([subQ43])],"derivedFrom":subQ11})])]}),makeQuery(id+"F47.opFillet","BLEND_FACE",FACE,{"disambiguationData":[OSD([subQ0,subQ9]),TDD([makeQuery(id+"F42.boolean.opBoolean","COPY",EDGE,{"disambiguationData":[TD([makeQuery(id+"F34.opLoft","SWEPT_FACE",FACE,{"disambiguationData":[OSD([subQ35,subQ34,subQ32,sQuery(id+"F22.wireOp",EDGE,"E28.11.1"),subQ31,subQ30])]})])],"derivedFrom":subQ11})])]}),makeQuery(id+"F47.opFillet","BLEND_FACE",FACE,{"disambiguationData":[OSD([subQ0,subQ9]),TDD([makeQuery(id+"F42.boolean.opBoolean","COPY",EDGE,{"disambiguationData":[TD([makeQuery(id+"F35.opLoft","SWEPT_FACE",FACE,{"disambiguationData":[OSD([subQ29,subQ28,subQ26,sQuery(id+"F22.wireOp",EDGE,"E28.12.1"),subQ25,subQ24])]})])],"derivedFrom":subQ11})])]}),makeQuery(id+"F47.opFillet","BLEND_FACE",FACE,{"disambiguationData":[OSD([subQ0,subQ9]),TDD([makeQuery(id+"F42.boolean.opBoolean","COPY",EDGE,{"disambiguationData":[TD([makeQuery(id+"F36.opLoft","SWEPT_FACE",FACE,{"disambiguationData":[OSD([subQ23,subQ22,subQ20,sQuery(id+"F22.wireOp",EDGE,"E28.13.1"),subQ19,subQ18])]})])],"derivedFrom":subQ11})])]}),makeQuery(id+"F47.opFillet","BLEND_FACE",FACE,{"disambiguationData":[OSD([subQ0,subQ9]),TDD([makeQuery(id+"F42.boolean.opBoolean","COPY",EDGE,{"disambiguationData":[TD([makeQuery(id+"F37.opLoft","SWEPT_FACE",FACE,{"disambiguationData":[OSD([subQ16,subQ15,subQ14,sQuery(id+"F22.wireOp",EDGE,"E28.14.1"),subQ13,subQ12])]})])],"derivedFrom":subQ11})])]}),makeQuery(id+"F47.opFillet","BLEND_FACE",FACE,{"disambiguationData":[OSD([subQ0,subQ9]),TDD([makeQuery(id+"F42.boolean.opBoolean","COPY",EDGE,{"disambiguationData":[TD([makeQuery(id+"F38.opLoft","SWEPT_FACE",FACE,{"disambiguationData":[OSD([subQ8,subQ7,subQ5,sQuery(id+"F22.wireOp",EDGE,"E28.15.1"),subQ4,subQ3])]})])],"derivedFrom":subQ11})])]})]});}
            var Q12;
            {var subQ0=sQuery(id+"F22.wireOp",EDGE,"E28.10.0");var subQ1=sQuery(id+"F22.wireOp",EDGE,"E28.10.1");var subQ2=sQuery(id+"F22.wireOp",EDGE,"E28.10.2");var subQ3=sQuery(id+"F22.wireOp",EDGE,"E28.10.3");var subQ4=sQuery(id+"F3.wireOp",EDGE,"E20.2.3");var subQ5=sQuery(id+"F3.wireOp",EDGE,"E20.2.1");var subQ6=makeQuery(id+"F33.opLoft","SWEPT_FACE",FACE,{"disambiguationData":[OSD([subQ5,sQuery(id+"F3.wireOp",EDGE,"E20.2.2"),subQ4,subQ0,subQ2,subQ3])]});var subQ7=sQuery(id+"F41.wireOp",EDGE,"E34");var subQ8=sQuery(id+"F41.wireOp",EDGE,"E32");Q12=makeQuery(id+"F44.opFillet","BLEND_EDGE",EDGE,{"blendedFrom":[makeQuery(id+"F40.boolean.opBoolean","INTERSECT",EDGE,{"derivedFrom":[subQ6,makeQuery(id+"F40.opExtrude","CAP_FACE",FACE,{"disambiguationData":[OSD([sQuery(id+"F39.wireOp",EDGE,"E29"),sQuery(id+"F39.wireOp",EDGE,"E30")])],"isStart":true})]}),makeQuery(id+"F42.boolean.opBoolean","COPY",FACE,{"disambiguationData":[TD([makeQuery(id+"F33.opLoft","SWEPT_FACE",FACE,{"disambiguationData":[OSD([sQuery(id+"F3.wireOp",EDGE,"E20.2.0"),subQ5,subQ4,subQ1,subQ2,subQ3])]})])],"derivedFrom":makeQuery(id+"F42.opRevolve","SWEPT_FACE",FACE,{"disambiguationData":[OSD([subQ8]),TDD([makeQuery(id+"F41.imprint","IMPRINT",EDGE,{"disambiguationData":[TD([[makeQuery(id+"F41.imprint","INTERSECT",VERTEX,{"disambiguationData":[OD(0.0)],"derivedFrom":[subQ8,subQ7]}),-1.0]])],"derivedFrom":subQ8})])]})})],"blendedInto":[makeQuery(id+"F42.boolean.opBoolean","COPY",FACE,{"disambiguationData":[TD([makeQuery(id+"F33.opLoft","SWEPT_FACE",FACE,{"disambiguationData":[OSD([sQuery(id+"F3.wireOp",EDGE,"E20.2.0"),subQ5,subQ4,subQ1,subQ2,subQ3])]})])],"derivedFrom":makeQuery(id+"F42.opRevolve","SWEPT_FACE",FACE,{"disambiguationData":[OSD([subQ8]),TDD([makeQuery(id+"F41.imprint","IMPRINT",EDGE,{"disambiguationData":[TD([[makeQuery(id+"F41.imprint","INTERSECT",VERTEX,{"disambiguationData":[OD(0.0)],"derivedFrom":[subQ8,subQ7]}),-1.0]])],"derivedFrom":subQ8})])]})})]});}
            var Q13;
            {var subQ0=sQuery(id+"F41.wireOp",EDGE,"E34");var subQ1=sQuery(id+"F41.wireOp",EDGE,"E32");Q13=makeQuery(id+"F42.boolean.opBoolean","INTERSECT",EDGE,{"derivedFrom":[makeQuery(id+"F32.opLoft","SWEPT_FACE",FACE,{"disambiguationData":[OSD([sQuery(id+"F3.wireOp",EDGE,"E20.1.0"),sQuery(id+"F3.wireOp",EDGE,"E20.1.1"),sQuery(id+"F3.wireOp",EDGE,"E20.1.3"),sQuery(id+"F22.wireOp",EDGE,"E28.9.1"),sQuery(id+"F22.wireOp",EDGE,"E28.9.2"),sQuery(id+"F22.wireOp",EDGE,"E28.9.3")])]}),makeQuery(id+"F42.opRevolve","SWEPT_FACE",FACE,{"disambiguationData":[OSD([subQ1]),TDD([makeQuery(id+"F41.imprint","IMPRINT",EDGE,{"disambiguationData":[TD([[makeQuery(id+"F41.imprint","INTERSECT",VERTEX,{"disambiguationData":[OD(0.0)],"derivedFrom":[subQ1,subQ0]}),-1.0]])],"derivedFrom":subQ1})])]})]});}
            var Q14;
            {var subQ0=sQuery(id+"F41.wireOp",EDGE,"E37");var subQ1=makeQuery(id+"F42.opRevolve","SWEPT_FACE",FACE,{"disambiguationData":[OSD([subQ0])]});var subQ2=makeQuery(id+"F40.opExtrude","CAP_FACE",FACE,{"disambiguationData":[OSD([sQuery(id+"F39.wireOp",EDGE,"E29"),sQuery(id+"F39.wireOp",EDGE,"E30")])],"isStart":true});var subQ3=sQuery(id+"F22.wireOp",EDGE,"E28.15.3");var subQ4=sQuery(id+"F22.wireOp",EDGE,"E28.15.2");var subQ5=sQuery(id+"F3.wireOp",EDGE,"E20.7.3");var subQ7=sQuery(id+"F3.wireOp",EDGE,"E20.7.1");var subQ8=sQuery(id+"F3.wireOp",EDGE,"E20.7.0");var subQ9=sQuery(id+"F41.wireOp",EDGE,"E38");var subQ10=makeQuery(id+"F42.opRevolve","SWEPT_FACE",FACE,{"disambiguationData":[OSD([subQ9])]});var subQ11=makeQuery(id+"F42.opRevolve","SWEPT_EDGE",EDGE,{"disambiguationData":[OSD([subQ0,subQ9])]});var subQ12=sQuery(id+"F22.wireOp",EDGE,"E28.14.3");var subQ13=sQuery(id+"F22.wireOp",EDGE,"E28.14.2");var subQ14=sQuery(id+"F3.wireOp",EDGE,"E20.6.3");var subQ15=sQuery(id+"F3.wireOp",EDGE,"E20.6.1");var subQ16=sQuery(id+"F3.wireOp",EDGE,"E20.6.0");var subQ18=sQuery(id+"F22.wireOp",EDGE,"E28.13.3");var subQ19=sQuery(id+"F22.wireOp",EDGE,"E28.13.2");var subQ20=sQuery(id+"F3.wireOp",EDGE,"E20.5.3");var subQ22=sQuery(id+"F3.wireOp",EDGE,"E20.5.1");var subQ23=sQuery(id+"F3.wireOp",EDGE,"E20.5.0");var subQ24=sQuery(id+"F22.wireOp",EDGE,"E28.12.3");var subQ25=sQuery(id+"F22.wireOp",EDGE,"E28.12.2");var subQ26=sQuery(id+"F3.wireOp",EDGE,"E20.4.3");var subQ28=sQuery(id+"F3.wireOp",EDGE,"E20.4.1");var subQ29=sQuery(id+"F3.wireOp",EDGE,"E20.4.0");var subQ30=sQuery(id+"F22.wireOp",EDGE,"E28.11.3");var subQ31=sQuery(id+"F22.wireOp",EDGE,"E28.11.2");var subQ32=sQuery(id+"F3.wireOp",EDGE,"E20.3.3");var subQ34=sQuery(id+"F3.wireOp",EDGE,"E20.3.1");var subQ35=sQuery(id+"F3.wireOp",EDGE,"E20.3.0");var subQ36=sQuery(id+"F22.wireOp",EDGE,"E28.10.3");var subQ37=sQuery(id+"F22.wireOp",EDGE,"E28.10.2");var subQ38=sQuery(id+"F3.wireOp",EDGE,"E20.2.3");var subQ40=sQuery(id+"F3.wireOp",EDGE,"E20.2.1");var subQ41=sQuery(id+"F3.wireOp",EDGE,"E20.2.0");var subQ42=sQuery(id+"F22.wireOp",EDGE,"E28.9.3");var subQ43=sQuery(id+"F22.wireOp",EDGE,"E28.9.2");var subQ44=sQuery(id+"F3.wireOp",EDGE,"E20.1.3");var subQ46=sQuery(id+"F3.wireOp",EDGE,"E20.1.1");var subQ48=sQuery(id+"F3.wireOp",EDGE,"E20.1.0");var subQ49=makeQuery(id+"F32.opLoft","SWEPT_FACE",FACE,{"disambiguationData":[OSD([subQ48,subQ46,subQ44,sQuery(id+"F22.wireOp",EDGE,"E28.9.1"),subQ43,subQ42])]});var subQ50=sQuery(id+"F22.wireOp",EDGE,"E28.8.3");var subQ51=sQuery(id+"F22.wireOp",EDGE,"E28.8.2");var subQ53=sQuery(id+"F3.wireOp",EDGE,"E18.top");var subQ54=sQuery(id+"F3.wireOp",EDGE,"E18.bottom");var subQ55=sQuery(id+"F3.wireOp",EDGE,"E18.left");var subQ56=makeQuery(id+"F31.opLoft","SWEPT_FACE",FACE,{"disambiguationData":[OSD([subQ54,subQ53,subQ55,sQuery(id+"F22.wireOp",EDGE,"E28.8.1"),subQ51,subQ50])]});var subQ57=sQuery(id+"F22.wireOp",EDGE,"E28.7.3");var subQ58=sQuery(id+"F22.wireOp",EDGE,"E28.7.2");var subQ59=sQuery(id+"F3.wireOp",EDGE,"E20.15.3");var subQ60=sQuery(id+"F3.wireOp",EDGE,"E20.15.1");var subQ61=sQuery(id+"F3.wireOp",EDGE,"E20.15.0");var subQ62=makeQuery(id+"F30.opLoft","SWEPT_FACE",FACE,{"disambiguationData":[OSD([subQ61,subQ60,subQ59,sQuery(id+"F22.wireOp",EDGE,"E28.7.1"),subQ58,subQ57])]});var subQ64=sQuery(id+"F22.wireOp",EDGE,"E28.6.3");var subQ65=sQuery(id+"F22.wireOp",EDGE,"E28.6.2");var subQ66=sQuery(id+"F3.wireOp",EDGE,"E20.14.3");var subQ68=sQuery(id+"F3.wireOp",EDGE,"E20.14.1");var subQ69=sQuery(id+"F3.wireOp",EDGE,"E20.14.0");var subQ70=makeQuery(id+"F29.opLoft","SWEPT_FACE",FACE,{"disambiguationData":[OSD([subQ69,subQ68,subQ66,sQuery(id+"F22.wireOp",EDGE,"E28.6.1"),subQ65,subQ64])]});var subQ71=sQuery(id+"F22.wireOp",EDGE,"E28.5.3");var subQ72=sQuery(id+"F22.wireOp",EDGE,"E28.5.2");var subQ73=sQuery(id+"F3.wireOp",EDGE,"E20.13.3");var subQ75=sQuery(id+"F3.wireOp",EDGE,"E20.13.1");var subQ76=sQuery(id+"F3.wireOp",EDGE,"E20.13.0");var subQ77=makeQuery(id+"F28.opLoft","SWEPT_FACE",FACE,{"disambiguationData":[OSD([subQ76,subQ75,subQ73,sQuery(id+"F22.wireOp",EDGE,"E28.5.1"),subQ72,subQ71])]});var subQ78=sQuery(id+"F22.wireOp",EDGE,"E28.4.3");var subQ79=sQuery(id+"F22.wireOp",EDGE,"E28.4.2");var subQ80=sQuery(id+"F3.wireOp",EDGE,"E20.12.3");var subQ82=sQuery(id+"F3.wireOp",EDGE,"E20.12.1");var subQ83=sQuery(id+"F3.wireOp",EDGE,"E20.12.0");var subQ84=makeQuery(id+"F27.opLoft","SWEPT_FACE",FACE,{"disambiguationData":[OSD([subQ83,subQ82,subQ80,sQuery(id+"F22.wireOp",EDGE,"E28.4.1"),subQ79,subQ78])]});var subQ85=sQuery(id+"F22.wireOp",EDGE,"E28.3.3");var subQ86=sQuery(id+"F22.wireOp",EDGE,"E28.3.2");var subQ87=sQuery(id+"F3.wireOp",EDGE,"E20.11.3");var subQ89=sQuery(id+"F3.wireOp",EDGE,"E20.11.1");var subQ90=sQuery(id+"F3.wireOp",EDGE,"E20.11.0");var subQ91=makeQuery(id+"F26.opLoft","SWEPT_FACE",FACE,{"disambiguationData":[OSD([subQ90,subQ89,subQ87,sQuery(id+"F22.wireOp",EDGE,"E28.3.1"),subQ86,subQ85])]});var subQ92=sQuery(id+"F22.wireOp",EDGE,"E28.2.3");var subQ93=sQuery(id+"F22.wireOp",EDGE,"E28.2.2");var subQ94=sQuery(id+"F3.wireOp",EDGE,"E20.10.3");var subQ95=sQuery(id+"F3.wireOp",EDGE,"E20.10.1");var subQ96=sQuery(id+"F3.wireOp",EDGE,"E20.10.0");var subQ97=makeQuery(id+"F25.opLoft","SWEPT_FACE",FACE,{"disambiguationData":[OSD([subQ96,subQ95,subQ94,sQuery(id+"F22.wireOp",EDGE,"E28.2.1"),subQ93,subQ92])]});var subQ99=sQuery(id+"F22.wireOp",EDGE,"E28.1.3");var subQ100=sQuery(id+"F22.wireOp",EDGE,"E28.1.2");var subQ101=sQuery(id+"F3.wireOp",EDGE,"E20.9.3");var subQ102=sQuery(id+"F3.wireOp",EDGE,"E20.9.1");var subQ103=sQuery(id+"F3.wireOp",EDGE,"E20.9.0");var subQ104=makeQuery(id+"F24.opLoft","SWEPT_FACE",FACE,{"disambiguationData":[OSD([subQ103,subQ102,subQ101,sQuery(id+"F22.wireOp",EDGE,"E28.1.1"),subQ100,subQ99])]});var subQ105=sQuery(id+"F22.wireOp",EDGE,"E27.top");var subQ106=sQuery(id+"F22.wireOp",EDGE,"E27.bottom");var subQ107=sQuery(id+"F3.wireOp",EDGE,"E20.8.3");var subQ109=sQuery(id+"F3.wireOp",EDGE,"E20.8.1");var subQ113=makeQuery(id+"F42.boolean.opBoolean","COPY",FACE,{"disambiguationData":[TD([subQ49])],"derivedFrom":subQ10});var subQ151=makeQuery(id+"F14.opLoft","CAP_FACE",FACE,{"disambiguationData":[OSD([makeQuery(id+"F3.imprint","IMPRINT",FACE,{"disambiguationData":[TD([[makeQuery(id+"F3.imprint","IMPRINT",EDGE,{"derivedFrom":subQ8}),-1.0]])]})])],"isStart":true});var subQ156=makeQuery(id+"F5.opLoft","CAP_FACE",FACE,{"disambiguationData":[OSD([makeQuery(id+"F3.imprint","IMPRINT",FACE,{"disambiguationData":[TD([[makeQuery(id+"F3.imprint","IMPRINT",EDGE,{"derivedFrom":subQ54}),1.0]])]})])],"isStart":true});var subQ185=makeQuery(id+"F32.boolean.opBoolean","INTERSECT",EDGE,{"derivedFrom":[makeQuery(id+"F31.boolean.opBoolean","SPLIT",FACE,{"disambiguationData":[TD([subQ151])],"derivedFrom":makeQuery(id+"F30.boolean.opBoolean","SPLIT",FACE,{"disambiguationData":[TD([subQ156])],"derivedFrom":makeQuery(id+"F29.boolean.opBoolean","SPLIT",FACE,{"disambiguationData":[TD([subQ156])],"derivedFrom":makeQuery(id+"F28.boolean.opBoolean","SPLIT",FACE,{"disambiguationData":[TD([subQ156])],"derivedFrom":makeQuery(id+"F27.boolean.opBoolean","SPLIT",FACE,{"disambiguationData":[TD([subQ156])],"derivedFrom":makeQuery(id+"F26.boolean.opBoolean","SPLIT",FACE,{"disambiguationData":[TD([subQ156])],"derivedFrom":makeQuery(id+"F25.boolean.opBoolean","SPLIT",FACE,{"disambiguationData":[TD([subQ156])],"derivedFrom":makeQuery(id+"F24.boolean.opBoolean","SPLIT",FACE,{"disambiguationData":[TD([subQ156])],"derivedFrom":makeQuery(id+"F1.opRevolve","SWEPT_FACE",FACE,{"disambiguationData":[OSD([sQuery(id+"F0.wireOp",EDGE,"E4")])]})})})})})})})})}),subQ49]});Q14=makeQuery(id+"F48.opFillet","BLEND_EDGE",EDGE,{"blendedFrom":[makeQuery(id+"F47.opFillet","TWEAK_EDGE",EDGE,{"derivedFrom":[makeQuery(id+"F45.opFillet","BLEND_VERTEX",VERTEX,{"blendedFrom":[subQ185,subQ49,subQ113],"blendedInto":[subQ49,subQ113]}),makeQuery(id+"F45.opFillet","BLEND_VERTEX",VERTEX,{"blendedFrom":[subQ185,makeQuery(id+"F42.boolean.opBoolean","MERGE",FACE,{"derivedFrom":[subQ2,subQ1]}),subQ113],"blendedInto":[makeQuery(id+"F42.boolean.opBoolean","MERGE",FACE,{"derivedFrom":[subQ2,subQ1]}),subQ113]})]}),makeQuery(id+"F47.opFillet","BLEND_FACE",FACE,{"disambiguationData":[OSD([subQ0,subQ9]),TDD([makeQuery(id+"F42.boolean.opBoolean","COPY",EDGE,{"disambiguationData":[TD([makeQuery(id+"F23.opLoft","SWEPT_FACE",FACE,{"disambiguationData":[OSD([sQuery(id+"F3.wireOp",EDGE,"E20.8.0"),subQ109,subQ107,subQ106,subQ105,sQuery(id+"F22.wireOp",EDGE,"E27.right")])]})])],"derivedFrom":subQ11})])]}),makeQuery(id+"F47.opFillet","BLEND_FACE",FACE,{"disambiguationData":[OSD([subQ0,subQ9]),TDD([makeQuery(id+"F42.boolean.opBoolean","COPY",EDGE,{"disambiguationData":[TD([subQ104])],"derivedFrom":subQ11})])]}),makeQuery(id+"F47.opFillet","BLEND_FACE",FACE,{"disambiguationData":[OSD([subQ0,subQ9]),TDD([makeQuery(id+"F42.boolean.opBoolean","COPY",EDGE,{"disambiguationData":[TD([subQ97])],"derivedFrom":subQ11})])]}),makeQuery(id+"F47.opFillet","BLEND_FACE",FACE,{"disambiguationData":[OSD([subQ0,subQ9]),TDD([makeQuery(id+"F42.boolean.opBoolean","COPY",EDGE,{"disambiguationData":[TD([subQ91])],"derivedFrom":subQ11})])]}),makeQuery(id+"F47.opFillet","BLEND_FACE",FACE,{"disambiguationData":[OSD([subQ0,subQ9]),TDD([makeQuery(id+"F42.boolean.opBoolean","COPY",EDGE,{"disambiguationData":[TD([subQ84])],"derivedFrom":subQ11})])]}),makeQuery(id+"F47.opFillet","BLEND_FACE",FACE,{"disambiguationData":[OSD([subQ0,subQ9]),TDD([makeQuery(id+"F42.boolean.opBoolean","COPY",EDGE,{"disambiguationData":[TD([subQ77])],"derivedFrom":subQ11})])]}),makeQuery(id+"F47.opFillet","BLEND_FACE",FACE,{"disambiguationData":[OSD([subQ0,subQ9]),TDD([makeQuery(id+"F42.boolean.opBoolean","COPY",EDGE,{"disambiguationData":[TD([subQ70])],"derivedFrom":subQ11})])]}),makeQuery(id+"F47.opFillet","BLEND_FACE",FACE,{"disambiguationData":[OSD([subQ0,subQ9]),TDD([makeQuery(id+"F42.boolean.opBoolean","COPY",EDGE,{"disambiguationData":[TD([subQ62])],"derivedFrom":subQ11})])]}),makeQuery(id+"F47.opFillet","BLEND_FACE",FACE,{"disambiguationData":[OSD([subQ0,subQ9]),TDD([makeQuery(id+"F42.boolean.opBoolean","COPY",EDGE,{"disambiguationData":[TD([subQ56])],"derivedFrom":subQ11})])]}),makeQuery(id+"F47.opFillet","BLEND_FACE",FACE,{"disambiguationData":[OSD([subQ0,subQ9]),TDD([makeQuery(id+"F42.boolean.opBoolean","COPY",EDGE,{"disambiguationData":[TD([subQ49])],"derivedFrom":subQ11})])]}),makeQuery(id+"F47.opFillet","BLEND_FACE",FACE,{"disambiguationData":[OSD([subQ0,subQ9]),TDD([makeQuery(id+"F42.boolean.opBoolean","COPY",EDGE,{"disambiguationData":[TD([makeQuery(id+"F33.opLoft","SWEPT_FACE",FACE,{"disambiguationData":[OSD([subQ41,subQ40,subQ38,sQuery(id+"F22.wireOp",EDGE,"E28.10.1"),subQ37,subQ36])]})])],"derivedFrom":subQ11})])]}),makeQuery(id+"F47.opFillet","BLEND_FACE",FACE,{"disambiguationData":[OSD([subQ0,subQ9]),TDD([makeQuery(id+"F42.boolean.opBoolean","COPY",EDGE,{"disambiguationData":[TD([makeQuery(id+"F34.opLoft","SWEPT_FACE",FACE,{"disambiguationData":[OSD([subQ35,subQ34,subQ32,sQuery(id+"F22.wireOp",EDGE,"E28.11.1"),subQ31,subQ30])]})])],"derivedFrom":subQ11})])]}),makeQuery(id+"F47.opFillet","BLEND_FACE",FACE,{"disambiguationData":[OSD([subQ0,subQ9]),TDD([makeQuery(id+"F42.boolean.opBoolean","COPY",EDGE,{"disambiguationData":[TD([makeQuery(id+"F35.opLoft","SWEPT_FACE",FACE,{"disambiguationData":[OSD([subQ29,subQ28,subQ26,sQuery(id+"F22.wireOp",EDGE,"E28.12.1"),subQ25,subQ24])]})])],"derivedFrom":subQ11})])]}),makeQuery(id+"F47.opFillet","BLEND_FACE",FACE,{"disambiguationData":[OSD([subQ0,subQ9]),TDD([makeQuery(id+"F42.boolean.opBoolean","COPY",EDGE,{"disambiguationData":[TD([makeQuery(id+"F36.opLoft","SWEPT_FACE",FACE,{"disambiguationData":[OSD([subQ23,subQ22,subQ20,sQuery(id+"F22.wireOp",EDGE,"E28.13.1"),subQ19,subQ18])]})])],"derivedFrom":subQ11})])]}),makeQuery(id+"F47.opFillet","BLEND_FACE",FACE,{"disambiguationData":[OSD([subQ0,subQ9]),TDD([makeQuery(id+"F42.boolean.opBoolean","COPY",EDGE,{"disambiguationData":[TD([makeQuery(id+"F37.opLoft","SWEPT_FACE",FACE,{"disambiguationData":[OSD([subQ16,subQ15,subQ14,sQuery(id+"F22.wireOp",EDGE,"E28.14.1"),subQ13,subQ12])]})])],"derivedFrom":subQ11})])]}),makeQuery(id+"F47.opFillet","BLEND_FACE",FACE,{"disambiguationData":[OSD([subQ0,subQ9]),TDD([makeQuery(id+"F42.boolean.opBoolean","COPY",EDGE,{"disambiguationData":[TD([makeQuery(id+"F38.opLoft","SWEPT_FACE",FACE,{"disambiguationData":[OSD([subQ8,subQ7,subQ5,sQuery(id+"F22.wireOp",EDGE,"E28.15.1"),subQ4,subQ3])]})])],"derivedFrom":subQ11})])]})],"blendedInto":[makeQuery(id+"F47.opFillet","BLEND_FACE",FACE,{"disambiguationData":[OSD([subQ0,subQ9]),TDD([makeQuery(id+"F42.boolean.opBoolean","COPY",EDGE,{"disambiguationData":[TD([makeQuery(id+"F23.opLoft","SWEPT_FACE",FACE,{"disambiguationData":[OSD([sQuery(id+"F3.wireOp",EDGE,"E20.8.0"),subQ109,subQ107,subQ106,subQ105,sQuery(id+"F22.wireOp",EDGE,"E27.right")])]})])],"derivedFrom":subQ11})])]}),makeQuery(id+"F47.opFillet","BLEND_FACE",FACE,{"disambiguationData":[OSD([subQ0,subQ9]),TDD([makeQuery(id+"F42.boolean.opBoolean","COPY",EDGE,{"disambiguationData":[TD([subQ104])],"derivedFrom":subQ11})])]}),makeQuery(id+"F47.opFillet","BLEND_FACE",FACE,{"disambiguationData":[OSD([subQ0,subQ9]),TDD([makeQuery(id+"F42.boolean.opBoolean","COPY",EDGE,{"disambiguationData":[TD([subQ97])],"derivedFrom":subQ11})])]}),makeQuery(id+"F47.opFillet","BLEND_FACE",FACE,{"disambiguationData":[OSD([subQ0,subQ9]),TDD([makeQuery(id+"F42.boolean.opBoolean","COPY",EDGE,{"disambiguationData":[TD([subQ91])],"derivedFrom":subQ11})])]}),makeQuery(id+"F47.opFillet","BLEND_FACE",FACE,{"disambiguationData":[OSD([subQ0,subQ9]),TDD([makeQuery(id+"F42.boolean.opBoolean","COPY",EDGE,{"disambiguationData":[TD([subQ84])],"derivedFrom":subQ11})])]}),makeQuery(id+"F47.opFillet","BLEND_FACE",FACE,{"disambiguationData":[OSD([subQ0,subQ9]),TDD([makeQuery(id+"F42.boolean.opBoolean","COPY",EDGE,{"disambiguationData":[TD([subQ77])],"derivedFrom":subQ11})])]}),makeQuery(id+"F47.opFillet","BLEND_FACE",FACE,{"disambiguationData":[OSD([subQ0,subQ9]),TDD([makeQuery(id+"F42.boolean.opBoolean","COPY",EDGE,{"disambiguationData":[TD([subQ70])],"derivedFrom":subQ11})])]}),makeQuery(id+"F47.opFillet","BLEND_FACE",FACE,{"disambiguationData":[OSD([subQ0,subQ9]),TDD([makeQuery(id+"F42.boolean.opBoolean","COPY",EDGE,{"disambiguationData":[TD([subQ62])],"derivedFrom":subQ11})])]}),makeQuery(id+"F47.opFillet","BLEND_FACE",FACE,{"disambiguationData":[OSD([subQ0,subQ9]),TDD([makeQuery(id+"F42.boolean.opBoolean","COPY",EDGE,{"disambiguationData":[TD([subQ56])],"derivedFrom":subQ11})])]}),makeQuery(id+"F47.opFillet","BLEND_FACE",FACE,{"disambiguationData":[OSD([subQ0,subQ9]),TDD([makeQuery(id+"F42.boolean.opBoolean","COPY",EDGE,{"disambiguationData":[TD([subQ49])],"derivedFrom":subQ11})])]}),makeQuery(id+"F47.opFillet","BLEND_FACE",FACE,{"disambiguationData":[OSD([subQ0,subQ9]),TDD([makeQuery(id+"F42.boolean.opBoolean","COPY",EDGE,{"disambiguationData":[TD([makeQuery(id+"F33.opLoft","SWEPT_FACE",FACE,{"disambiguationData":[OSD([subQ41,subQ40,subQ38,sQuery(id+"F22.wireOp",EDGE,"E28.10.1"),subQ37,subQ36])]})])],"derivedFrom":subQ11})])]}),makeQuery(id+"F47.opFillet","BLEND_FACE",FACE,{"disambiguationData":[OSD([subQ0,subQ9]),TDD([makeQuery(id+"F42.boolean.opBoolean","COPY",EDGE,{"disambiguationData":[TD([makeQuery(id+"F34.opLoft","SWEPT_FACE",FACE,{"disambiguationData":[OSD([subQ35,subQ34,subQ32,sQuery(id+"F22.wireOp",EDGE,"E28.11.1"),subQ31,subQ30])]})])],"derivedFrom":subQ11})])]}),makeQuery(id+"F47.opFillet","BLEND_FACE",FACE,{"disambiguationData":[OSD([subQ0,subQ9]),TDD([makeQuery(id+"F42.boolean.opBoolean","COPY",EDGE,{"disambiguationData":[TD([makeQuery(id+"F35.opLoft","SWEPT_FACE",FACE,{"disambiguationData":[OSD([subQ29,subQ28,subQ26,sQuery(id+"F22.wireOp",EDGE,"E28.12.1"),subQ25,subQ24])]})])],"derivedFrom":subQ11})])]}),makeQuery(id+"F47.opFillet","BLEND_FACE",FACE,{"disambiguationData":[OSD([subQ0,subQ9]),TDD([makeQuery(id+"F42.boolean.opBoolean","COPY",EDGE,{"disambiguationData":[TD([makeQuery(id+"F36.opLoft","SWEPT_FACE",FACE,{"disambiguationData":[OSD([subQ23,subQ22,subQ20,sQuery(id+"F22.wireOp",EDGE,"E28.13.1"),subQ19,subQ18])]})])],"derivedFrom":subQ11})])]}),makeQuery(id+"F47.opFillet","BLEND_FACE",FACE,{"disambiguationData":[OSD([subQ0,subQ9]),TDD([makeQuery(id+"F42.boolean.opBoolean","COPY",EDGE,{"disambiguationData":[TD([makeQuery(id+"F37.opLoft","SWEPT_FACE",FACE,{"disambiguationData":[OSD([subQ16,subQ15,subQ14,sQuery(id+"F22.wireOp",EDGE,"E28.14.1"),subQ13,subQ12])]})])],"derivedFrom":subQ11})])]}),makeQuery(id+"F47.opFillet","BLEND_FACE",FACE,{"disambiguationData":[OSD([subQ0,subQ9]),TDD([makeQuery(id+"F42.boolean.opBoolean","COPY",EDGE,{"disambiguationData":[TD([makeQuery(id+"F38.opLoft","SWEPT_FACE",FACE,{"disambiguationData":[OSD([subQ8,subQ7,subQ5,sQuery(id+"F22.wireOp",EDGE,"E28.15.1"),subQ4,subQ3])]})])],"derivedFrom":subQ11})])]})]});}
            var Q15;
            {var subQ0=sQuery(id+"F41.wireOp",EDGE,"E37");var subQ1=makeQuery(id+"F42.opRevolve","SWEPT_FACE",FACE,{"disambiguationData":[OSD([subQ0])]});var subQ2=makeQuery(id+"F40.opExtrude","CAP_FACE",FACE,{"disambiguationData":[OSD([sQuery(id+"F39.wireOp",EDGE,"E29"),sQuery(id+"F39.wireOp",EDGE,"E30")])],"isStart":true});var subQ3=sQuery(id+"F22.wireOp",EDGE,"E28.15.3");var subQ4=sQuery(id+"F22.wireOp",EDGE,"E28.15.2");var subQ5=sQuery(id+"F3.wireOp",EDGE,"E20.7.3");var subQ7=sQuery(id+"F3.wireOp",EDGE,"E20.7.1");var subQ8=sQuery(id+"F3.wireOp",EDGE,"E20.7.0");var subQ9=sQuery(id+"F41.wireOp",EDGE,"E38");var subQ10=makeQuery(id+"F42.opRevolve","SWEPT_FACE",FACE,{"disambiguationData":[OSD([subQ9])]});var subQ11=makeQuery(id+"F42.opRevolve","SWEPT_EDGE",EDGE,{"disambiguationData":[OSD([subQ0,subQ9])]});var subQ12=sQuery(id+"F22.wireOp",EDGE,"E28.14.3");var subQ13=sQuery(id+"F22.wireOp",EDGE,"E28.14.2");var subQ14=sQuery(id+"F3.wireOp",EDGE,"E20.6.3");var subQ15=sQuery(id+"F3.wireOp",EDGE,"E20.6.1");var subQ16=sQuery(id+"F3.wireOp",EDGE,"E20.6.0");var subQ18=sQuery(id+"F22.wireOp",EDGE,"E28.13.3");var subQ19=sQuery(id+"F22.wireOp",EDGE,"E28.13.2");var subQ20=sQuery(id+"F3.wireOp",EDGE,"E20.5.3");var subQ22=sQuery(id+"F3.wireOp",EDGE,"E20.5.1");var subQ23=sQuery(id+"F3.wireOp",EDGE,"E20.5.0");var subQ24=sQuery(id+"F22.wireOp",EDGE,"E28.12.3");var subQ25=sQuery(id+"F22.wireOp",EDGE,"E28.12.2");var subQ26=sQuery(id+"F3.wireOp",EDGE,"E20.4.3");var subQ28=sQuery(id+"F3.wireOp",EDGE,"E20.4.1");var subQ29=sQuery(id+"F3.wireOp",EDGE,"E20.4.0");var subQ30=sQuery(id+"F22.wireOp",EDGE,"E28.11.3");var subQ31=sQuery(id+"F22.wireOp",EDGE,"E28.11.2");var subQ32=sQuery(id+"F3.wireOp",EDGE,"E20.3.3");var subQ34=sQuery(id+"F3.wireOp",EDGE,"E20.3.1");var subQ35=sQuery(id+"F3.wireOp",EDGE,"E20.3.0");var subQ36=sQuery(id+"F22.wireOp",EDGE,"E28.10.3");var subQ37=sQuery(id+"F22.wireOp",EDGE,"E28.10.2");var subQ38=sQuery(id+"F3.wireOp",EDGE,"E20.2.3");var subQ40=sQuery(id+"F3.wireOp",EDGE,"E20.2.1");var subQ41=sQuery(id+"F3.wireOp",EDGE,"E20.2.0");var subQ42=sQuery(id+"F22.wireOp",EDGE,"E28.9.3");var subQ43=sQuery(id+"F22.wireOp",EDGE,"E28.9.2");var subQ44=sQuery(id+"F3.wireOp",EDGE,"E20.1.3");var subQ46=sQuery(id+"F3.wireOp",EDGE,"E20.1.1");var subQ47=sQuery(id+"F3.wireOp",EDGE,"E20.1.0");var subQ48=sQuery(id+"F22.wireOp",EDGE,"E28.8.3");var subQ49=sQuery(id+"F22.wireOp",EDGE,"E28.8.2");var subQ51=sQuery(id+"F3.wireOp",EDGE,"E18.top");var subQ52=sQuery(id+"F3.wireOp",EDGE,"E18.bottom");var subQ54=sQuery(id+"F3.wireOp",EDGE,"E18.left");var subQ55=makeQuery(id+"F31.opLoft","SWEPT_FACE",FACE,{"disambiguationData":[OSD([subQ52,subQ51,subQ54,sQuery(id+"F22.wireOp",EDGE,"E28.8.1"),subQ49,subQ48])]});var subQ56=sQuery(id+"F22.wireOp",EDGE,"E28.7.3");var subQ57=sQuery(id+"F22.wireOp",EDGE,"E28.7.2");var subQ58=sQuery(id+"F3.wireOp",EDGE,"E20.15.3");var subQ59=sQuery(id+"F3.wireOp",EDGE,"E20.15.1");var subQ60=sQuery(id+"F3.wireOp",EDGE,"E20.15.0");var subQ61=makeQuery(id+"F30.opLoft","SWEPT_FACE",FACE,{"disambiguationData":[OSD([subQ60,subQ59,subQ58,sQuery(id+"F22.wireOp",EDGE,"E28.7.1"),subQ57,subQ56])]});var subQ63=sQuery(id+"F22.wireOp",EDGE,"E28.6.3");var subQ64=sQuery(id+"F22.wireOp",EDGE,"E28.6.2");var subQ65=sQuery(id+"F3.wireOp",EDGE,"E20.14.3");var subQ67=sQuery(id+"F3.wireOp",EDGE,"E20.14.1");var subQ68=sQuery(id+"F3.wireOp",EDGE,"E20.14.0");var subQ69=makeQuery(id+"F29.opLoft","SWEPT_FACE",FACE,{"disambiguationData":[OSD([subQ68,subQ67,subQ65,sQuery(id+"F22.wireOp",EDGE,"E28.6.1"),subQ64,subQ63])]});var subQ70=sQuery(id+"F22.wireOp",EDGE,"E28.5.3");var subQ71=sQuery(id+"F22.wireOp",EDGE,"E28.5.2");var subQ72=sQuery(id+"F3.wireOp",EDGE,"E20.13.3");var subQ74=sQuery(id+"F3.wireOp",EDGE,"E20.13.1");var subQ75=sQuery(id+"F3.wireOp",EDGE,"E20.13.0");var subQ76=makeQuery(id+"F28.opLoft","SWEPT_FACE",FACE,{"disambiguationData":[OSD([subQ75,subQ74,subQ72,sQuery(id+"F22.wireOp",EDGE,"E28.5.1"),subQ71,subQ70])]});var subQ77=sQuery(id+"F22.wireOp",EDGE,"E28.4.3");var subQ78=sQuery(id+"F22.wireOp",EDGE,"E28.4.2");var subQ79=sQuery(id+"F3.wireOp",EDGE,"E20.12.3");var subQ81=sQuery(id+"F3.wireOp",EDGE,"E20.12.1");var subQ82=sQuery(id+"F3.wireOp",EDGE,"E20.12.0");var subQ83=makeQuery(id+"F27.opLoft","SWEPT_FACE",FACE,{"disambiguationData":[OSD([subQ82,subQ81,subQ79,sQuery(id+"F22.wireOp",EDGE,"E28.4.1"),subQ78,subQ77])]});var subQ84=sQuery(id+"F22.wireOp",EDGE,"E28.3.3");var subQ85=sQuery(id+"F22.wireOp",EDGE,"E28.3.2");var subQ86=sQuery(id+"F3.wireOp",EDGE,"E20.11.3");var subQ88=sQuery(id+"F3.wireOp",EDGE,"E20.11.1");var subQ89=sQuery(id+"F3.wireOp",EDGE,"E20.11.0");var subQ90=makeQuery(id+"F26.opLoft","SWEPT_FACE",FACE,{"disambiguationData":[OSD([subQ89,subQ88,subQ86,sQuery(id+"F22.wireOp",EDGE,"E28.3.1"),subQ85,subQ84])]});var subQ91=sQuery(id+"F22.wireOp",EDGE,"E28.2.3");var subQ92=sQuery(id+"F22.wireOp",EDGE,"E28.2.2");var subQ93=sQuery(id+"F3.wireOp",EDGE,"E20.10.3");var subQ94=sQuery(id+"F3.wireOp",EDGE,"E20.10.1");var subQ95=sQuery(id+"F3.wireOp",EDGE,"E20.10.0");var subQ96=makeQuery(id+"F25.opLoft","SWEPT_FACE",FACE,{"disambiguationData":[OSD([subQ95,subQ94,subQ93,sQuery(id+"F22.wireOp",EDGE,"E28.2.1"),subQ92,subQ91])]});var subQ98=sQuery(id+"F22.wireOp",EDGE,"E28.1.3");var subQ99=sQuery(id+"F22.wireOp",EDGE,"E28.1.2");var subQ100=sQuery(id+"F3.wireOp",EDGE,"E20.9.3");var subQ101=sQuery(id+"F3.wireOp",EDGE,"E20.9.1");var subQ102=sQuery(id+"F3.wireOp",EDGE,"E20.9.0");var subQ103=makeQuery(id+"F24.opLoft","SWEPT_FACE",FACE,{"disambiguationData":[OSD([subQ102,subQ101,subQ100,sQuery(id+"F22.wireOp",EDGE,"E28.1.1"),subQ99,subQ98])]});var subQ104=sQuery(id+"F22.wireOp",EDGE,"E27.top");var subQ105=sQuery(id+"F22.wireOp",EDGE,"E27.bottom");var subQ106=sQuery(id+"F3.wireOp",EDGE,"E20.8.3");var subQ108=sQuery(id+"F3.wireOp",EDGE,"E20.8.1");var subQ112=makeQuery(id+"F42.boolean.opBoolean","COPY",FACE,{"disambiguationData":[TD([subQ55])],"derivedFrom":subQ10});var subQ138=makeQuery(id+"F5.opLoft","CAP_FACE",FACE,{"disambiguationData":[OSD([makeQuery(id+"F3.imprint","IMPRINT",FACE,{"disambiguationData":[TD([[makeQuery(id+"F3.imprint","IMPRINT",EDGE,{"derivedFrom":subQ52}),1.0]])]})])],"isStart":true});var subQ184=makeQuery(id+"F31.boolean.opBoolean","INTERSECT",EDGE,{"derivedFrom":[makeQuery(id+"F30.boolean.opBoolean","SPLIT",FACE,{"disambiguationData":[TD([subQ138])],"derivedFrom":makeQuery(id+"F29.boolean.opBoolean","SPLIT",FACE,{"disambiguationData":[TD([subQ138])],"derivedFrom":makeQuery(id+"F28.boolean.opBoolean","SPLIT",FACE,{"disambiguationData":[TD([subQ138])],"derivedFrom":makeQuery(id+"F27.boolean.opBoolean","SPLIT",FACE,{"disambiguationData":[TD([subQ138])],"derivedFrom":makeQuery(id+"F26.boolean.opBoolean","SPLIT",FACE,{"disambiguationData":[TD([subQ138])],"derivedFrom":makeQuery(id+"F25.boolean.opBoolean","SPLIT",FACE,{"disambiguationData":[TD([subQ138])],"derivedFrom":makeQuery(id+"F24.boolean.opBoolean","SPLIT",FACE,{"disambiguationData":[TD([subQ138])],"derivedFrom":makeQuery(id+"F1.opRevolve","SWEPT_FACE",FACE,{"disambiguationData":[OSD([sQuery(id+"F0.wireOp",EDGE,"E4")])]})})})})})})})}),subQ55]});Q15=makeQuery(id+"F48.opFillet","BLEND_EDGE",EDGE,{"blendedFrom":[makeQuery(id+"F47.opFillet","TWEAK_EDGE",EDGE,{"derivedFrom":[makeQuery(id+"F45.opFillet","BLEND_VERTEX",VERTEX,{"blendedFrom":[subQ184,subQ55,subQ112],"blendedInto":[subQ55,subQ112]}),makeQuery(id+"F45.opFillet","BLEND_VERTEX",VERTEX,{"blendedFrom":[subQ184,makeQuery(id+"F42.boolean.opBoolean","MERGE",FACE,{"derivedFrom":[subQ2,subQ1]}),subQ112],"blendedInto":[makeQuery(id+"F42.boolean.opBoolean","MERGE",FACE,{"derivedFrom":[subQ2,subQ1]}),subQ112]})]}),makeQuery(id+"F47.opFillet","BLEND_FACE",FACE,{"disambiguationData":[OSD([subQ0,subQ9]),TDD([makeQuery(id+"F42.boolean.opBoolean","COPY",EDGE,{"disambiguationData":[TD([makeQuery(id+"F23.opLoft","SWEPT_FACE",FACE,{"disambiguationData":[OSD([sQuery(id+"F3.wireOp",EDGE,"E20.8.0"),subQ108,subQ106,subQ105,subQ104,sQuery(id+"F22.wireOp",EDGE,"E27.right")])]})])],"derivedFrom":subQ11})])]}),makeQuery(id+"F47.opFillet","BLEND_FACE",FACE,{"disambiguationData":[OSD([subQ0,subQ9]),TDD([makeQuery(id+"F42.boolean.opBoolean","COPY",EDGE,{"disambiguationData":[TD([subQ103])],"derivedFrom":subQ11})])]}),makeQuery(id+"F47.opFillet","BLEND_FACE",FACE,{"disambiguationData":[OSD([subQ0,subQ9]),TDD([makeQuery(id+"F42.boolean.opBoolean","COPY",EDGE,{"disambiguationData":[TD([subQ96])],"derivedFrom":subQ11})])]}),makeQuery(id+"F47.opFillet","BLEND_FACE",FACE,{"disambiguationData":[OSD([subQ0,subQ9]),TDD([makeQuery(id+"F42.boolean.opBoolean","COPY",EDGE,{"disambiguationData":[TD([subQ90])],"derivedFrom":subQ11})])]}),makeQuery(id+"F47.opFillet","BLEND_FACE",FACE,{"disambiguationData":[OSD([subQ0,subQ9]),TDD([makeQuery(id+"F42.boolean.opBoolean","COPY",EDGE,{"disambiguationData":[TD([subQ83])],"derivedFrom":subQ11})])]}),makeQuery(id+"F47.opFillet","BLEND_FACE",FACE,{"disambiguationData":[OSD([subQ0,subQ9]),TDD([makeQuery(id+"F42.boolean.opBoolean","COPY",EDGE,{"disambiguationData":[TD([subQ76])],"derivedFrom":subQ11})])]}),makeQuery(id+"F47.opFillet","BLEND_FACE",FACE,{"disambiguationData":[OSD([subQ0,subQ9]),TDD([makeQuery(id+"F42.boolean.opBoolean","COPY",EDGE,{"disambiguationData":[TD([subQ69])],"derivedFrom":subQ11})])]}),makeQuery(id+"F47.opFillet","BLEND_FACE",FACE,{"disambiguationData":[OSD([subQ0,subQ9]),TDD([makeQuery(id+"F42.boolean.opBoolean","COPY",EDGE,{"disambiguationData":[TD([subQ61])],"derivedFrom":subQ11})])]}),makeQuery(id+"F47.opFillet","BLEND_FACE",FACE,{"disambiguationData":[OSD([subQ0,subQ9]),TDD([makeQuery(id+"F42.boolean.opBoolean","COPY",EDGE,{"disambiguationData":[TD([subQ55])],"derivedFrom":subQ11})])]}),makeQuery(id+"F47.opFillet","BLEND_FACE",FACE,{"disambiguationData":[OSD([subQ0,subQ9]),TDD([makeQuery(id+"F42.boolean.opBoolean","COPY",EDGE,{"disambiguationData":[TD([makeQuery(id+"F32.opLoft","SWEPT_FACE",FACE,{"disambiguationData":[OSD([subQ47,subQ46,subQ44,sQuery(id+"F22.wireOp",EDGE,"E28.9.1"),subQ43,subQ42])]})])],"derivedFrom":subQ11})])]}),makeQuery(id+"F47.opFillet","BLEND_FACE",FACE,{"disambiguationData":[OSD([subQ0,subQ9]),TDD([makeQuery(id+"F42.boolean.opBoolean","COPY",EDGE,{"disambiguationData":[TD([makeQuery(id+"F33.opLoft","SWEPT_FACE",FACE,{"disambiguationData":[OSD([subQ41,subQ40,subQ38,sQuery(id+"F22.wireOp",EDGE,"E28.10.1"),subQ37,subQ36])]})])],"derivedFrom":subQ11})])]}),makeQuery(id+"F47.opFillet","BLEND_FACE",FACE,{"disambiguationData":[OSD([subQ0,subQ9]),TDD([makeQuery(id+"F42.boolean.opBoolean","COPY",EDGE,{"disambiguationData":[TD([makeQuery(id+"F34.opLoft","SWEPT_FACE",FACE,{"disambiguationData":[OSD([subQ35,subQ34,subQ32,sQuery(id+"F22.wireOp",EDGE,"E28.11.1"),subQ31,subQ30])]})])],"derivedFrom":subQ11})])]}),makeQuery(id+"F47.opFillet","BLEND_FACE",FACE,{"disambiguationData":[OSD([subQ0,subQ9]),TDD([makeQuery(id+"F42.boolean.opBoolean","COPY",EDGE,{"disambiguationData":[TD([makeQuery(id+"F35.opLoft","SWEPT_FACE",FACE,{"disambiguationData":[OSD([subQ29,subQ28,subQ26,sQuery(id+"F22.wireOp",EDGE,"E28.12.1"),subQ25,subQ24])]})])],"derivedFrom":subQ11})])]}),makeQuery(id+"F47.opFillet","BLEND_FACE",FACE,{"disambiguationData":[OSD([subQ0,subQ9]),TDD([makeQuery(id+"F42.boolean.opBoolean","COPY",EDGE,{"disambiguationData":[TD([makeQuery(id+"F36.opLoft","SWEPT_FACE",FACE,{"disambiguationData":[OSD([subQ23,subQ22,subQ20,sQuery(id+"F22.wireOp",EDGE,"E28.13.1"),subQ19,subQ18])]})])],"derivedFrom":subQ11})])]}),makeQuery(id+"F47.opFillet","BLEND_FACE",FACE,{"disambiguationData":[OSD([subQ0,subQ9]),TDD([makeQuery(id+"F42.boolean.opBoolean","COPY",EDGE,{"disambiguationData":[TD([makeQuery(id+"F37.opLoft","SWEPT_FACE",FACE,{"disambiguationData":[OSD([subQ16,subQ15,subQ14,sQuery(id+"F22.wireOp",EDGE,"E28.14.1"),subQ13,subQ12])]})])],"derivedFrom":subQ11})])]}),makeQuery(id+"F47.opFillet","BLEND_FACE",FACE,{"disambiguationData":[OSD([subQ0,subQ9]),TDD([makeQuery(id+"F42.boolean.opBoolean","COPY",EDGE,{"disambiguationData":[TD([makeQuery(id+"F38.opLoft","SWEPT_FACE",FACE,{"disambiguationData":[OSD([subQ8,subQ7,subQ5,sQuery(id+"F22.wireOp",EDGE,"E28.15.1"),subQ4,subQ3])]})])],"derivedFrom":subQ11})])]})],"blendedInto":[makeQuery(id+"F47.opFillet","BLEND_FACE",FACE,{"disambiguationData":[OSD([subQ0,subQ9]),TDD([makeQuery(id+"F42.boolean.opBoolean","COPY",EDGE,{"disambiguationData":[TD([makeQuery(id+"F23.opLoft","SWEPT_FACE",FACE,{"disambiguationData":[OSD([sQuery(id+"F3.wireOp",EDGE,"E20.8.0"),subQ108,subQ106,subQ105,subQ104,sQuery(id+"F22.wireOp",EDGE,"E27.right")])]})])],"derivedFrom":subQ11})])]}),makeQuery(id+"F47.opFillet","BLEND_FACE",FACE,{"disambiguationData":[OSD([subQ0,subQ9]),TDD([makeQuery(id+"F42.boolean.opBoolean","COPY",EDGE,{"disambiguationData":[TD([subQ103])],"derivedFrom":subQ11})])]}),makeQuery(id+"F47.opFillet","BLEND_FACE",FACE,{"disambiguationData":[OSD([subQ0,subQ9]),TDD([makeQuery(id+"F42.boolean.opBoolean","COPY",EDGE,{"disambiguationData":[TD([subQ96])],"derivedFrom":subQ11})])]}),makeQuery(id+"F47.opFillet","BLEND_FACE",FACE,{"disambiguationData":[OSD([subQ0,subQ9]),TDD([makeQuery(id+"F42.boolean.opBoolean","COPY",EDGE,{"disambiguationData":[TD([subQ90])],"derivedFrom":subQ11})])]}),makeQuery(id+"F47.opFillet","BLEND_FACE",FACE,{"disambiguationData":[OSD([subQ0,subQ9]),TDD([makeQuery(id+"F42.boolean.opBoolean","COPY",EDGE,{"disambiguationData":[TD([subQ83])],"derivedFrom":subQ11})])]}),makeQuery(id+"F47.opFillet","BLEND_FACE",FACE,{"disambiguationData":[OSD([subQ0,subQ9]),TDD([makeQuery(id+"F42.boolean.opBoolean","COPY",EDGE,{"disambiguationData":[TD([subQ76])],"derivedFrom":subQ11})])]}),makeQuery(id+"F47.opFillet","BLEND_FACE",FACE,{"disambiguationData":[OSD([subQ0,subQ9]),TDD([makeQuery(id+"F42.boolean.opBoolean","COPY",EDGE,{"disambiguationData":[TD([subQ69])],"derivedFrom":subQ11})])]}),makeQuery(id+"F47.opFillet","BLEND_FACE",FACE,{"disambiguationData":[OSD([subQ0,subQ9]),TDD([makeQuery(id+"F42.boolean.opBoolean","COPY",EDGE,{"disambiguationData":[TD([subQ61])],"derivedFrom":subQ11})])]}),makeQuery(id+"F47.opFillet","BLEND_FACE",FACE,{"disambiguationData":[OSD([subQ0,subQ9]),TDD([makeQuery(id+"F42.boolean.opBoolean","COPY",EDGE,{"disambiguationData":[TD([subQ55])],"derivedFrom":subQ11})])]}),makeQuery(id+"F47.opFillet","BLEND_FACE",FACE,{"disambiguationData":[OSD([subQ0,subQ9]),TDD([makeQuery(id+"F42.boolean.opBoolean","COPY",EDGE,{"disambiguationData":[TD([makeQuery(id+"F32.opLoft","SWEPT_FACE",FACE,{"disambiguationData":[OSD([subQ47,subQ46,subQ44,sQuery(id+"F22.wireOp",EDGE,"E28.9.1"),subQ43,subQ42])]})])],"derivedFrom":subQ11})])]}),makeQuery(id+"F47.opFillet","BLEND_FACE",FACE,{"disambiguationData":[OSD([subQ0,subQ9]),TDD([makeQuery(id+"F42.boolean.opBoolean","COPY",EDGE,{"disambiguationData":[TD([makeQuery(id+"F33.opLoft","SWEPT_FACE",FACE,{"disambiguationData":[OSD([subQ41,subQ40,subQ38,sQuery(id+"F22.wireOp",EDGE,"E28.10.1"),subQ37,subQ36])]})])],"derivedFrom":subQ11})])]}),makeQuery(id+"F47.opFillet","BLEND_FACE",FACE,{"disambiguationData":[OSD([subQ0,subQ9]),TDD([makeQuery(id+"F42.boolean.opBoolean","COPY",EDGE,{"disambiguationData":[TD([makeQuery(id+"F34.opLoft","SWEPT_FACE",FACE,{"disambiguationData":[OSD([subQ35,subQ34,subQ32,sQuery(id+"F22.wireOp",EDGE,"E28.11.1"),subQ31,subQ30])]})])],"derivedFrom":subQ11})])]}),makeQuery(id+"F47.opFillet","BLEND_FACE",FACE,{"disambiguationData":[OSD([subQ0,subQ9]),TDD([makeQuery(id+"F42.boolean.opBoolean","COPY",EDGE,{"disambiguationData":[TD([makeQuery(id+"F35.opLoft","SWEPT_FACE",FACE,{"disambiguationData":[OSD([subQ29,subQ28,subQ26,sQuery(id+"F22.wireOp",EDGE,"E28.12.1"),subQ25,subQ24])]})])],"derivedFrom":subQ11})])]}),makeQuery(id+"F47.opFillet","BLEND_FACE",FACE,{"disambiguationData":[OSD([subQ0,subQ9]),TDD([makeQuery(id+"F42.boolean.opBoolean","COPY",EDGE,{"disambiguationData":[TD([makeQuery(id+"F36.opLoft","SWEPT_FACE",FACE,{"disambiguationData":[OSD([subQ23,subQ22,subQ20,sQuery(id+"F22.wireOp",EDGE,"E28.13.1"),subQ19,subQ18])]})])],"derivedFrom":subQ11})])]}),makeQuery(id+"F47.opFillet","BLEND_FACE",FACE,{"disambiguationData":[OSD([subQ0,subQ9]),TDD([makeQuery(id+"F42.boolean.opBoolean","COPY",EDGE,{"disambiguationData":[TD([makeQuery(id+"F37.opLoft","SWEPT_FACE",FACE,{"disambiguationData":[OSD([subQ16,subQ15,subQ14,sQuery(id+"F22.wireOp",EDGE,"E28.14.1"),subQ13,subQ12])]})])],"derivedFrom":subQ11})])]}),makeQuery(id+"F47.opFillet","BLEND_FACE",FACE,{"disambiguationData":[OSD([subQ0,subQ9]),TDD([makeQuery(id+"F42.boolean.opBoolean","COPY",EDGE,{"disambiguationData":[TD([makeQuery(id+"F38.opLoft","SWEPT_FACE",FACE,{"disambiguationData":[OSD([subQ8,subQ7,subQ5,sQuery(id+"F22.wireOp",EDGE,"E28.15.1"),subQ4,subQ3])]})])],"derivedFrom":subQ11})])]})]});}
            var Q16;
            {var subQ0=sQuery(id+"F22.wireOp",EDGE,"E28.9.3");var subQ1=sQuery(id+"F22.wireOp",EDGE,"E28.9.2");var subQ2=sQuery(id+"F22.wireOp",EDGE,"E28.9.1");var subQ3=sQuery(id+"F3.wireOp",EDGE,"E20.1.3");var subQ4=sQuery(id+"F3.wireOp",EDGE,"E20.1.1");var subQ5=sQuery(id+"F22.wireOp",EDGE,"E28.9.0");var subQ6=makeQuery(id+"F32.opLoft","SWEPT_FACE",FACE,{"disambiguationData":[OSD([subQ4,sQuery(id+"F3.wireOp",EDGE,"E20.1.2"),subQ3,subQ5,subQ1,subQ0])]});var subQ7=sQuery(id+"F41.wireOp",EDGE,"E34");var subQ8=sQuery(id+"F41.wireOp",EDGE,"E32");Q16=makeQuery(id+"F44.opFillet","BLEND_EDGE",EDGE,{"blendedFrom":[makeQuery(id+"F40.boolean.opBoolean","INTERSECT",EDGE,{"derivedFrom":[subQ6,makeQuery(id+"F40.opExtrude","CAP_FACE",FACE,{"disambiguationData":[OSD([sQuery(id+"F39.wireOp",EDGE,"E29"),sQuery(id+"F39.wireOp",EDGE,"E30")])],"isStart":true})]}),makeQuery(id+"F42.boolean.opBoolean","COPY",FACE,{"disambiguationData":[TD([makeQuery(id+"F32.opLoft","SWEPT_FACE",FACE,{"disambiguationData":[OSD([sQuery(id+"F3.wireOp",EDGE,"E20.1.0"),subQ4,subQ3,subQ2,subQ1,subQ0])]})])],"derivedFrom":makeQuery(id+"F42.opRevolve","SWEPT_FACE",FACE,{"disambiguationData":[OSD([subQ8]),TDD([makeQuery(id+"F41.imprint","IMPRINT",EDGE,{"disambiguationData":[TD([[makeQuery(id+"F41.imprint","INTERSECT",VERTEX,{"disambiguationData":[OD(0.0)],"derivedFrom":[subQ8,subQ7]}),-1.0]])],"derivedFrom":subQ8})])]})})],"blendedInto":[makeQuery(id+"F42.boolean.opBoolean","COPY",FACE,{"disambiguationData":[TD([makeQuery(id+"F32.opLoft","SWEPT_FACE",FACE,{"disambiguationData":[OSD([sQuery(id+"F3.wireOp",EDGE,"E20.1.0"),subQ4,subQ3,subQ2,subQ1,subQ0])]})])],"derivedFrom":makeQuery(id+"F42.opRevolve","SWEPT_FACE",FACE,{"disambiguationData":[OSD([subQ8]),TDD([makeQuery(id+"F41.imprint","IMPRINT",EDGE,{"disambiguationData":[TD([[makeQuery(id+"F41.imprint","INTERSECT",VERTEX,{"disambiguationData":[OD(0.0)],"derivedFrom":[subQ8,subQ7]}),-1.0]])],"derivedFrom":subQ8})])]})})]});}
            var Q17;
            {var subQ0=sQuery(id+"F41.wireOp",EDGE,"E34");var subQ1=sQuery(id+"F41.wireOp",EDGE,"E32");Q17=makeQuery(id+"F42.boolean.opBoolean","INTERSECT",EDGE,{"derivedFrom":[makeQuery(id+"F31.opLoft","SWEPT_FACE",FACE,{"disambiguationData":[OSD([sQuery(id+"F3.wireOp",EDGE,"E18.bottom"),sQuery(id+"F3.wireOp",EDGE,"E18.top"),sQuery(id+"F3.wireOp",EDGE,"E18.left"),sQuery(id+"F22.wireOp",EDGE,"E28.8.1"),sQuery(id+"F22.wireOp",EDGE,"E28.8.2"),sQuery(id+"F22.wireOp",EDGE,"E28.8.3")])]}),makeQuery(id+"F42.opRevolve","SWEPT_FACE",FACE,{"disambiguationData":[OSD([subQ1]),TDD([makeQuery(id+"F41.imprint","IMPRINT",EDGE,{"disambiguationData":[TD([[makeQuery(id+"F41.imprint","INTERSECT",VERTEX,{"disambiguationData":[OD(0.0)],"derivedFrom":[subQ1,subQ0]}),-1.0]])],"derivedFrom":subQ1})])]})]});}
            var Q18;
            {var subQ0=sQuery(id+"F22.wireOp",EDGE,"E28.8.3");var subQ1=sQuery(id+"F22.wireOp",EDGE,"E28.8.2");var subQ2=sQuery(id+"F22.wireOp",EDGE,"E28.8.1");var subQ3=sQuery(id+"F3.wireOp",EDGE,"E18.top");var subQ4=sQuery(id+"F3.wireOp",EDGE,"E18.bottom");var subQ5=sQuery(id+"F22.wireOp",EDGE,"E28.8.0");var subQ6=makeQuery(id+"F31.opLoft","SWEPT_FACE",FACE,{"disambiguationData":[OSD([subQ4,subQ3,sQuery(id+"F3.wireOp",EDGE,"E18.right"),subQ5,subQ1,subQ0])]});var subQ7=sQuery(id+"F41.wireOp",EDGE,"E34");var subQ8=sQuery(id+"F41.wireOp",EDGE,"E32");Q18=makeQuery(id+"F44.opFillet","BLEND_EDGE",EDGE,{"blendedFrom":[makeQuery(id+"F40.boolean.opBoolean","INTERSECT",EDGE,{"derivedFrom":[subQ6,makeQuery(id+"F40.opExtrude","CAP_FACE",FACE,{"disambiguationData":[OSD([sQuery(id+"F39.wireOp",EDGE,"E29"),sQuery(id+"F39.wireOp",EDGE,"E30")])],"isStart":true})]}),makeQuery(id+"F42.boolean.opBoolean","COPY",FACE,{"disambiguationData":[TD([makeQuery(id+"F31.opLoft","SWEPT_FACE",FACE,{"disambiguationData":[OSD([subQ4,subQ3,sQuery(id+"F3.wireOp",EDGE,"E18.left"),subQ2,subQ1,subQ0])]})])],"derivedFrom":makeQuery(id+"F42.opRevolve","SWEPT_FACE",FACE,{"disambiguationData":[OSD([subQ8]),TDD([makeQuery(id+"F41.imprint","IMPRINT",EDGE,{"disambiguationData":[TD([[makeQuery(id+"F41.imprint","INTERSECT",VERTEX,{"disambiguationData":[OD(0.0)],"derivedFrom":[subQ8,subQ7]}),-1.0]])],"derivedFrom":subQ8})])]})})],"blendedInto":[makeQuery(id+"F42.boolean.opBoolean","COPY",FACE,{"disambiguationData":[TD([makeQuery(id+"F31.opLoft","SWEPT_FACE",FACE,{"disambiguationData":[OSD([subQ4,subQ3,sQuery(id+"F3.wireOp",EDGE,"E18.left"),subQ2,subQ1,subQ0])]})])],"derivedFrom":makeQuery(id+"F42.opRevolve","SWEPT_FACE",FACE,{"disambiguationData":[OSD([subQ8]),TDD([makeQuery(id+"F41.imprint","IMPRINT",EDGE,{"disambiguationData":[TD([[makeQuery(id+"F41.imprint","INTERSECT",VERTEX,{"disambiguationData":[OD(0.0)],"derivedFrom":[subQ8,subQ7]}),-1.0]])],"derivedFrom":subQ8})])]})})]});}
            var Q19;
            {var subQ0=sQuery(id+"F41.wireOp",EDGE,"E37");var subQ1=makeQuery(id+"F42.opRevolve","SWEPT_FACE",FACE,{"disambiguationData":[OSD([subQ0])]});var subQ2=makeQuery(id+"F40.opExtrude","CAP_FACE",FACE,{"disambiguationData":[OSD([sQuery(id+"F39.wireOp",EDGE,"E29"),sQuery(id+"F39.wireOp",EDGE,"E30")])],"isStart":true});var subQ3=sQuery(id+"F22.wireOp",EDGE,"E28.15.3");var subQ4=sQuery(id+"F22.wireOp",EDGE,"E28.15.2");var subQ5=sQuery(id+"F3.wireOp",EDGE,"E20.7.3");var subQ7=sQuery(id+"F3.wireOp",EDGE,"E20.7.1");var subQ8=sQuery(id+"F3.wireOp",EDGE,"E20.7.0");var subQ9=sQuery(id+"F41.wireOp",EDGE,"E38");var subQ10=makeQuery(id+"F42.opRevolve","SWEPT_FACE",FACE,{"disambiguationData":[OSD([subQ9])]});var subQ11=makeQuery(id+"F42.opRevolve","SWEPT_EDGE",EDGE,{"disambiguationData":[OSD([subQ0,subQ9])]});var subQ12=sQuery(id+"F22.wireOp",EDGE,"E28.14.3");var subQ13=sQuery(id+"F22.wireOp",EDGE,"E28.14.2");var subQ14=sQuery(id+"F3.wireOp",EDGE,"E20.6.3");var subQ15=sQuery(id+"F3.wireOp",EDGE,"E20.6.1");var subQ16=sQuery(id+"F3.wireOp",EDGE,"E20.6.0");var subQ18=sQuery(id+"F22.wireOp",EDGE,"E28.13.3");var subQ19=sQuery(id+"F22.wireOp",EDGE,"E28.13.2");var subQ20=sQuery(id+"F3.wireOp",EDGE,"E20.5.3");var subQ22=sQuery(id+"F3.wireOp",EDGE,"E20.5.1");var subQ23=sQuery(id+"F3.wireOp",EDGE,"E20.5.0");var subQ24=sQuery(id+"F22.wireOp",EDGE,"E28.12.3");var subQ25=sQuery(id+"F22.wireOp",EDGE,"E28.12.2");var subQ26=sQuery(id+"F3.wireOp",EDGE,"E20.4.3");var subQ28=sQuery(id+"F3.wireOp",EDGE,"E20.4.1");var subQ29=sQuery(id+"F3.wireOp",EDGE,"E20.4.0");var subQ30=sQuery(id+"F22.wireOp",EDGE,"E28.11.3");var subQ31=sQuery(id+"F22.wireOp",EDGE,"E28.11.2");var subQ32=sQuery(id+"F3.wireOp",EDGE,"E20.3.3");var subQ34=sQuery(id+"F3.wireOp",EDGE,"E20.3.1");var subQ35=sQuery(id+"F3.wireOp",EDGE,"E20.3.0");var subQ36=sQuery(id+"F22.wireOp",EDGE,"E28.10.3");var subQ37=sQuery(id+"F22.wireOp",EDGE,"E28.10.2");var subQ38=sQuery(id+"F3.wireOp",EDGE,"E20.2.3");var subQ40=sQuery(id+"F3.wireOp",EDGE,"E20.2.1");var subQ41=sQuery(id+"F3.wireOp",EDGE,"E20.2.0");var subQ42=sQuery(id+"F22.wireOp",EDGE,"E28.9.3");var subQ43=sQuery(id+"F22.wireOp",EDGE,"E28.9.2");var subQ44=sQuery(id+"F3.wireOp",EDGE,"E20.1.3");var subQ46=sQuery(id+"F3.wireOp",EDGE,"E20.1.1");var subQ47=sQuery(id+"F3.wireOp",EDGE,"E20.1.0");var subQ48=sQuery(id+"F22.wireOp",EDGE,"E28.8.3");var subQ49=sQuery(id+"F22.wireOp",EDGE,"E28.8.2");var subQ51=sQuery(id+"F3.wireOp",EDGE,"E18.top");var subQ52=sQuery(id+"F3.wireOp",EDGE,"E18.bottom");var subQ53=sQuery(id+"F3.wireOp",EDGE,"E18.left");var subQ54=sQuery(id+"F22.wireOp",EDGE,"E28.7.3");var subQ55=sQuery(id+"F22.wireOp",EDGE,"E28.7.2");var subQ56=sQuery(id+"F3.wireOp",EDGE,"E20.15.3");var subQ57=sQuery(id+"F3.wireOp",EDGE,"E20.15.1");var subQ58=sQuery(id+"F3.wireOp",EDGE,"E20.15.0");var subQ59=makeQuery(id+"F30.opLoft","SWEPT_FACE",FACE,{"disambiguationData":[OSD([subQ58,subQ57,subQ56,sQuery(id+"F22.wireOp",EDGE,"E28.7.1"),subQ55,subQ54])]});var subQ62=sQuery(id+"F22.wireOp",EDGE,"E28.6.3");var subQ63=sQuery(id+"F22.wireOp",EDGE,"E28.6.2");var subQ64=sQuery(id+"F3.wireOp",EDGE,"E20.14.3");var subQ66=sQuery(id+"F3.wireOp",EDGE,"E20.14.1");var subQ67=sQuery(id+"F3.wireOp",EDGE,"E20.14.0");var subQ68=makeQuery(id+"F29.opLoft","SWEPT_FACE",FACE,{"disambiguationData":[OSD([subQ67,subQ66,subQ64,sQuery(id+"F22.wireOp",EDGE,"E28.6.1"),subQ63,subQ62])]});var subQ69=sQuery(id+"F22.wireOp",EDGE,"E28.5.3");var subQ70=sQuery(id+"F22.wireOp",EDGE,"E28.5.2");var subQ71=sQuery(id+"F3.wireOp",EDGE,"E20.13.3");var subQ73=sQuery(id+"F3.wireOp",EDGE,"E20.13.1");var subQ74=sQuery(id+"F3.wireOp",EDGE,"E20.13.0");var subQ75=makeQuery(id+"F28.opLoft","SWEPT_FACE",FACE,{"disambiguationData":[OSD([subQ74,subQ73,subQ71,sQuery(id+"F22.wireOp",EDGE,"E28.5.1"),subQ70,subQ69])]});var subQ76=sQuery(id+"F22.wireOp",EDGE,"E28.4.3");var subQ77=sQuery(id+"F22.wireOp",EDGE,"E28.4.2");var subQ78=sQuery(id+"F3.wireOp",EDGE,"E20.12.3");var subQ80=sQuery(id+"F3.wireOp",EDGE,"E20.12.1");var subQ81=sQuery(id+"F3.wireOp",EDGE,"E20.12.0");var subQ82=makeQuery(id+"F27.opLoft","SWEPT_FACE",FACE,{"disambiguationData":[OSD([subQ81,subQ80,subQ78,sQuery(id+"F22.wireOp",EDGE,"E28.4.1"),subQ77,subQ76])]});var subQ83=sQuery(id+"F22.wireOp",EDGE,"E28.3.3");var subQ84=sQuery(id+"F22.wireOp",EDGE,"E28.3.2");var subQ85=sQuery(id+"F3.wireOp",EDGE,"E20.11.3");var subQ87=sQuery(id+"F3.wireOp",EDGE,"E20.11.1");var subQ88=sQuery(id+"F3.wireOp",EDGE,"E20.11.0");var subQ89=makeQuery(id+"F26.opLoft","SWEPT_FACE",FACE,{"disambiguationData":[OSD([subQ88,subQ87,subQ85,sQuery(id+"F22.wireOp",EDGE,"E28.3.1"),subQ84,subQ83])]});var subQ90=sQuery(id+"F22.wireOp",EDGE,"E28.2.3");var subQ91=sQuery(id+"F22.wireOp",EDGE,"E28.2.2");var subQ92=sQuery(id+"F3.wireOp",EDGE,"E20.10.3");var subQ93=sQuery(id+"F3.wireOp",EDGE,"E20.10.1");var subQ94=sQuery(id+"F3.wireOp",EDGE,"E20.10.0");var subQ95=makeQuery(id+"F25.opLoft","SWEPT_FACE",FACE,{"disambiguationData":[OSD([subQ94,subQ93,subQ92,sQuery(id+"F22.wireOp",EDGE,"E28.2.1"),subQ91,subQ90])]});var subQ97=sQuery(id+"F22.wireOp",EDGE,"E28.1.3");var subQ98=sQuery(id+"F22.wireOp",EDGE,"E28.1.2");var subQ99=sQuery(id+"F3.wireOp",EDGE,"E20.9.3");var subQ100=sQuery(id+"F3.wireOp",EDGE,"E20.9.1");var subQ101=sQuery(id+"F3.wireOp",EDGE,"E20.9.0");var subQ102=makeQuery(id+"F24.opLoft","SWEPT_FACE",FACE,{"disambiguationData":[OSD([subQ101,subQ100,subQ99,sQuery(id+"F22.wireOp",EDGE,"E28.1.1"),subQ98,subQ97])]});var subQ103=sQuery(id+"F22.wireOp",EDGE,"E27.top");var subQ104=sQuery(id+"F22.wireOp",EDGE,"E27.bottom");var subQ105=sQuery(id+"F3.wireOp",EDGE,"E20.8.3");var subQ107=sQuery(id+"F3.wireOp",EDGE,"E20.8.1");var subQ111=makeQuery(id+"F42.boolean.opBoolean","COPY",FACE,{"disambiguationData":[TD([subQ59])],"derivedFrom":subQ10});var subQ127=makeQuery(id+"F5.opLoft","CAP_FACE",FACE,{"disambiguationData":[OSD([makeQuery(id+"F3.imprint","IMPRINT",FACE,{"disambiguationData":[TD([[makeQuery(id+"F3.imprint","IMPRINT",EDGE,{"derivedFrom":subQ52}),1.0]])]})])],"isStart":true});var subQ183=makeQuery(id+"F30.boolean.opBoolean","INTERSECT",EDGE,{"derivedFrom":[makeQuery(id+"F29.boolean.opBoolean","SPLIT",FACE,{"disambiguationData":[TD([subQ127])],"derivedFrom":makeQuery(id+"F28.boolean.opBoolean","SPLIT",FACE,{"disambiguationData":[TD([subQ127])],"derivedFrom":makeQuery(id+"F27.boolean.opBoolean","SPLIT",FACE,{"disambiguationData":[TD([subQ127])],"derivedFrom":makeQuery(id+"F26.boolean.opBoolean","SPLIT",FACE,{"disambiguationData":[TD([subQ127])],"derivedFrom":makeQuery(id+"F25.boolean.opBoolean","SPLIT",FACE,{"disambiguationData":[TD([subQ127])],"derivedFrom":makeQuery(id+"F24.boolean.opBoolean","SPLIT",FACE,{"disambiguationData":[TD([subQ127])],"derivedFrom":makeQuery(id+"F1.opRevolve","SWEPT_FACE",FACE,{"disambiguationData":[OSD([sQuery(id+"F0.wireOp",EDGE,"E4")])]})})})})})})}),subQ59]});Q19=makeQuery(id+"F48.opFillet","BLEND_EDGE",EDGE,{"blendedFrom":[makeQuery(id+"F47.opFillet","TWEAK_EDGE",EDGE,{"derivedFrom":[makeQuery(id+"F45.opFillet","BLEND_VERTEX",VERTEX,{"blendedFrom":[subQ183,subQ59,subQ111],"blendedInto":[subQ59,subQ111]}),makeQuery(id+"F45.opFillet","BLEND_VERTEX",VERTEX,{"blendedFrom":[subQ183,makeQuery(id+"F42.boolean.opBoolean","MERGE",FACE,{"derivedFrom":[subQ2,subQ1]}),subQ111],"blendedInto":[makeQuery(id+"F42.boolean.opBoolean","MERGE",FACE,{"derivedFrom":[subQ2,subQ1]}),subQ111]})]}),makeQuery(id+"F47.opFillet","BLEND_FACE",FACE,{"disambiguationData":[OSD([subQ0,subQ9]),TDD([makeQuery(id+"F42.boolean.opBoolean","COPY",EDGE,{"disambiguationData":[TD([makeQuery(id+"F23.opLoft","SWEPT_FACE",FACE,{"disambiguationData":[OSD([sQuery(id+"F3.wireOp",EDGE,"E20.8.0"),subQ107,subQ105,subQ104,subQ103,sQuery(id+"F22.wireOp",EDGE,"E27.right")])]})])],"derivedFrom":subQ11})])]}),makeQuery(id+"F47.opFillet","BLEND_FACE",FACE,{"disambiguationData":[OSD([subQ0,subQ9]),TDD([makeQuery(id+"F42.boolean.opBoolean","COPY",EDGE,{"disambiguationData":[TD([subQ102])],"derivedFrom":subQ11})])]}),makeQuery(id+"F47.opFillet","BLEND_FACE",FACE,{"disambiguationData":[OSD([subQ0,subQ9]),TDD([makeQuery(id+"F42.boolean.opBoolean","COPY",EDGE,{"disambiguationData":[TD([subQ95])],"derivedFrom":subQ11})])]}),makeQuery(id+"F47.opFillet","BLEND_FACE",FACE,{"disambiguationData":[OSD([subQ0,subQ9]),TDD([makeQuery(id+"F42.boolean.opBoolean","COPY",EDGE,{"disambiguationData":[TD([subQ89])],"derivedFrom":subQ11})])]}),makeQuery(id+"F47.opFillet","BLEND_FACE",FACE,{"disambiguationData":[OSD([subQ0,subQ9]),TDD([makeQuery(id+"F42.boolean.opBoolean","COPY",EDGE,{"disambiguationData":[TD([subQ82])],"derivedFrom":subQ11})])]}),makeQuery(id+"F47.opFillet","BLEND_FACE",FACE,{"disambiguationData":[OSD([subQ0,subQ9]),TDD([makeQuery(id+"F42.boolean.opBoolean","COPY",EDGE,{"disambiguationData":[TD([subQ75])],"derivedFrom":subQ11})])]}),makeQuery(id+"F47.opFillet","BLEND_FACE",FACE,{"disambiguationData":[OSD([subQ0,subQ9]),TDD([makeQuery(id+"F42.boolean.opBoolean","COPY",EDGE,{"disambiguationData":[TD([subQ68])],"derivedFrom":subQ11})])]}),makeQuery(id+"F47.opFillet","BLEND_FACE",FACE,{"disambiguationData":[OSD([subQ0,subQ9]),TDD([makeQuery(id+"F42.boolean.opBoolean","COPY",EDGE,{"disambiguationData":[TD([subQ59])],"derivedFrom":subQ11})])]}),makeQuery(id+"F47.opFillet","BLEND_FACE",FACE,{"disambiguationData":[OSD([subQ0,subQ9]),TDD([makeQuery(id+"F42.boolean.opBoolean","COPY",EDGE,{"disambiguationData":[TD([makeQuery(id+"F31.opLoft","SWEPT_FACE",FACE,{"disambiguationData":[OSD([subQ52,subQ51,subQ53,sQuery(id+"F22.wireOp",EDGE,"E28.8.1"),subQ49,subQ48])]})])],"derivedFrom":subQ11})])]}),makeQuery(id+"F47.opFillet","BLEND_FACE",FACE,{"disambiguationData":[OSD([subQ0,subQ9]),TDD([makeQuery(id+"F42.boolean.opBoolean","COPY",EDGE,{"disambiguationData":[TD([makeQuery(id+"F32.opLoft","SWEPT_FACE",FACE,{"disambiguationData":[OSD([subQ47,subQ46,subQ44,sQuery(id+"F22.wireOp",EDGE,"E28.9.1"),subQ43,subQ42])]})])],"derivedFrom":subQ11})])]}),makeQuery(id+"F47.opFillet","BLEND_FACE",FACE,{"disambiguationData":[OSD([subQ0,subQ9]),TDD([makeQuery(id+"F42.boolean.opBoolean","COPY",EDGE,{"disambiguationData":[TD([makeQuery(id+"F33.opLoft","SWEPT_FACE",FACE,{"disambiguationData":[OSD([subQ41,subQ40,subQ38,sQuery(id+"F22.wireOp",EDGE,"E28.10.1"),subQ37,subQ36])]})])],"derivedFrom":subQ11})])]}),makeQuery(id+"F47.opFillet","BLEND_FACE",FACE,{"disambiguationData":[OSD([subQ0,subQ9]),TDD([makeQuery(id+"F42.boolean.opBoolean","COPY",EDGE,{"disambiguationData":[TD([makeQuery(id+"F34.opLoft","SWEPT_FACE",FACE,{"disambiguationData":[OSD([subQ35,subQ34,subQ32,sQuery(id+"F22.wireOp",EDGE,"E28.11.1"),subQ31,subQ30])]})])],"derivedFrom":subQ11})])]}),makeQuery(id+"F47.opFillet","BLEND_FACE",FACE,{"disambiguationData":[OSD([subQ0,subQ9]),TDD([makeQuery(id+"F42.boolean.opBoolean","COPY",EDGE,{"disambiguationData":[TD([makeQuery(id+"F35.opLoft","SWEPT_FACE",FACE,{"disambiguationData":[OSD([subQ29,subQ28,subQ26,sQuery(id+"F22.wireOp",EDGE,"E28.12.1"),subQ25,subQ24])]})])],"derivedFrom":subQ11})])]}),makeQuery(id+"F47.opFillet","BLEND_FACE",FACE,{"disambiguationData":[OSD([subQ0,subQ9]),TDD([makeQuery(id+"F42.boolean.opBoolean","COPY",EDGE,{"disambiguationData":[TD([makeQuery(id+"F36.opLoft","SWEPT_FACE",FACE,{"disambiguationData":[OSD([subQ23,subQ22,subQ20,sQuery(id+"F22.wireOp",EDGE,"E28.13.1"),subQ19,subQ18])]})])],"derivedFrom":subQ11})])]}),makeQuery(id+"F47.opFillet","BLEND_FACE",FACE,{"disambiguationData":[OSD([subQ0,subQ9]),TDD([makeQuery(id+"F42.boolean.opBoolean","COPY",EDGE,{"disambiguationData":[TD([makeQuery(id+"F37.opLoft","SWEPT_FACE",FACE,{"disambiguationData":[OSD([subQ16,subQ15,subQ14,sQuery(id+"F22.wireOp",EDGE,"E28.14.1"),subQ13,subQ12])]})])],"derivedFrom":subQ11})])]}),makeQuery(id+"F47.opFillet","BLEND_FACE",FACE,{"disambiguationData":[OSD([subQ0,subQ9]),TDD([makeQuery(id+"F42.boolean.opBoolean","COPY",EDGE,{"disambiguationData":[TD([makeQuery(id+"F38.opLoft","SWEPT_FACE",FACE,{"disambiguationData":[OSD([subQ8,subQ7,subQ5,sQuery(id+"F22.wireOp",EDGE,"E28.15.1"),subQ4,subQ3])]})])],"derivedFrom":subQ11})])]})],"blendedInto":[makeQuery(id+"F47.opFillet","BLEND_FACE",FACE,{"disambiguationData":[OSD([subQ0,subQ9]),TDD([makeQuery(id+"F42.boolean.opBoolean","COPY",EDGE,{"disambiguationData":[TD([makeQuery(id+"F23.opLoft","SWEPT_FACE",FACE,{"disambiguationData":[OSD([sQuery(id+"F3.wireOp",EDGE,"E20.8.0"),subQ107,subQ105,subQ104,subQ103,sQuery(id+"F22.wireOp",EDGE,"E27.right")])]})])],"derivedFrom":subQ11})])]}),makeQuery(id+"F47.opFillet","BLEND_FACE",FACE,{"disambiguationData":[OSD([subQ0,subQ9]),TDD([makeQuery(id+"F42.boolean.opBoolean","COPY",EDGE,{"disambiguationData":[TD([subQ102])],"derivedFrom":subQ11})])]}),makeQuery(id+"F47.opFillet","BLEND_FACE",FACE,{"disambiguationData":[OSD([subQ0,subQ9]),TDD([makeQuery(id+"F42.boolean.opBoolean","COPY",EDGE,{"disambiguationData":[TD([subQ95])],"derivedFrom":subQ11})])]}),makeQuery(id+"F47.opFillet","BLEND_FACE",FACE,{"disambiguationData":[OSD([subQ0,subQ9]),TDD([makeQuery(id+"F42.boolean.opBoolean","COPY",EDGE,{"disambiguationData":[TD([subQ89])],"derivedFrom":subQ11})])]}),makeQuery(id+"F47.opFillet","BLEND_FACE",FACE,{"disambiguationData":[OSD([subQ0,subQ9]),TDD([makeQuery(id+"F42.boolean.opBoolean","COPY",EDGE,{"disambiguationData":[TD([subQ82])],"derivedFrom":subQ11})])]}),makeQuery(id+"F47.opFillet","BLEND_FACE",FACE,{"disambiguationData":[OSD([subQ0,subQ9]),TDD([makeQuery(id+"F42.boolean.opBoolean","COPY",EDGE,{"disambiguationData":[TD([subQ75])],"derivedFrom":subQ11})])]}),makeQuery(id+"F47.opFillet","BLEND_FACE",FACE,{"disambiguationData":[OSD([subQ0,subQ9]),TDD([makeQuery(id+"F42.boolean.opBoolean","COPY",EDGE,{"disambiguationData":[TD([subQ68])],"derivedFrom":subQ11})])]}),makeQuery(id+"F47.opFillet","BLEND_FACE",FACE,{"disambiguationData":[OSD([subQ0,subQ9]),TDD([makeQuery(id+"F42.boolean.opBoolean","COPY",EDGE,{"disambiguationData":[TD([subQ59])],"derivedFrom":subQ11})])]}),makeQuery(id+"F47.opFillet","BLEND_FACE",FACE,{"disambiguationData":[OSD([subQ0,subQ9]),TDD([makeQuery(id+"F42.boolean.opBoolean","COPY",EDGE,{"disambiguationData":[TD([makeQuery(id+"F31.opLoft","SWEPT_FACE",FACE,{"disambiguationData":[OSD([subQ52,subQ51,subQ53,sQuery(id+"F22.wireOp",EDGE,"E28.8.1"),subQ49,subQ48])]})])],"derivedFrom":subQ11})])]}),makeQuery(id+"F47.opFillet","BLEND_FACE",FACE,{"disambiguationData":[OSD([subQ0,subQ9]),TDD([makeQuery(id+"F42.boolean.opBoolean","COPY",EDGE,{"disambiguationData":[TD([makeQuery(id+"F32.opLoft","SWEPT_FACE",FACE,{"disambiguationData":[OSD([subQ47,subQ46,subQ44,sQuery(id+"F22.wireOp",EDGE,"E28.9.1"),subQ43,subQ42])]})])],"derivedFrom":subQ11})])]}),makeQuery(id+"F47.opFillet","BLEND_FACE",FACE,{"disambiguationData":[OSD([subQ0,subQ9]),TDD([makeQuery(id+"F42.boolean.opBoolean","COPY",EDGE,{"disambiguationData":[TD([makeQuery(id+"F33.opLoft","SWEPT_FACE",FACE,{"disambiguationData":[OSD([subQ41,subQ40,subQ38,sQuery(id+"F22.wireOp",EDGE,"E28.10.1"),subQ37,subQ36])]})])],"derivedFrom":subQ11})])]}),makeQuery(id+"F47.opFillet","BLEND_FACE",FACE,{"disambiguationData":[OSD([subQ0,subQ9]),TDD([makeQuery(id+"F42.boolean.opBoolean","COPY",EDGE,{"disambiguationData":[TD([makeQuery(id+"F34.opLoft","SWEPT_FACE",FACE,{"disambiguationData":[OSD([subQ35,subQ34,subQ32,sQuery(id+"F22.wireOp",EDGE,"E28.11.1"),subQ31,subQ30])]})])],"derivedFrom":subQ11})])]}),makeQuery(id+"F47.opFillet","BLEND_FACE",FACE,{"disambiguationData":[OSD([subQ0,subQ9]),TDD([makeQuery(id+"F42.boolean.opBoolean","COPY",EDGE,{"disambiguationData":[TD([makeQuery(id+"F35.opLoft","SWEPT_FACE",FACE,{"disambiguationData":[OSD([subQ29,subQ28,subQ26,sQuery(id+"F22.wireOp",EDGE,"E28.12.1"),subQ25,subQ24])]})])],"derivedFrom":subQ11})])]}),makeQuery(id+"F47.opFillet","BLEND_FACE",FACE,{"disambiguationData":[OSD([subQ0,subQ9]),TDD([makeQuery(id+"F42.boolean.opBoolean","COPY",EDGE,{"disambiguationData":[TD([makeQuery(id+"F36.opLoft","SWEPT_FACE",FACE,{"disambiguationData":[OSD([subQ23,subQ22,subQ20,sQuery(id+"F22.wireOp",EDGE,"E28.13.1"),subQ19,subQ18])]})])],"derivedFrom":subQ11})])]}),makeQuery(id+"F47.opFillet","BLEND_FACE",FACE,{"disambiguationData":[OSD([subQ0,subQ9]),TDD([makeQuery(id+"F42.boolean.opBoolean","COPY",EDGE,{"disambiguationData":[TD([makeQuery(id+"F37.opLoft","SWEPT_FACE",FACE,{"disambiguationData":[OSD([subQ16,subQ15,subQ14,sQuery(id+"F22.wireOp",EDGE,"E28.14.1"),subQ13,subQ12])]})])],"derivedFrom":subQ11})])]}),makeQuery(id+"F47.opFillet","BLEND_FACE",FACE,{"disambiguationData":[OSD([subQ0,subQ9]),TDD([makeQuery(id+"F42.boolean.opBoolean","COPY",EDGE,{"disambiguationData":[TD([makeQuery(id+"F38.opLoft","SWEPT_FACE",FACE,{"disambiguationData":[OSD([subQ8,subQ7,subQ5,sQuery(id+"F22.wireOp",EDGE,"E28.15.1"),subQ4,subQ3])]})])],"derivedFrom":subQ11})])]})]});}
            var Q20;
            {var subQ0=sQuery(id+"F41.wireOp",EDGE,"E34");var subQ1=sQuery(id+"F41.wireOp",EDGE,"E32");Q20=makeQuery(id+"F42.boolean.opBoolean","INTERSECT",EDGE,{"derivedFrom":[makeQuery(id+"F30.opLoft","SWEPT_FACE",FACE,{"disambiguationData":[OSD([sQuery(id+"F3.wireOp",EDGE,"E20.15.0"),sQuery(id+"F3.wireOp",EDGE,"E20.15.1"),sQuery(id+"F3.wireOp",EDGE,"E20.15.3"),sQuery(id+"F22.wireOp",EDGE,"E28.7.1"),sQuery(id+"F22.wireOp",EDGE,"E28.7.2"),sQuery(id+"F22.wireOp",EDGE,"E28.7.3")])]}),makeQuery(id+"F42.opRevolve","SWEPT_FACE",FACE,{"disambiguationData":[OSD([subQ1]),TDD([makeQuery(id+"F41.imprint","IMPRINT",EDGE,{"disambiguationData":[TD([[makeQuery(id+"F41.imprint","INTERSECT",VERTEX,{"disambiguationData":[OD(0.0)],"derivedFrom":[subQ1,subQ0]}),-1.0]])],"derivedFrom":subQ1})])]})]});}
            var Q21;
            {var subQ0=sQuery(id+"F22.wireOp",EDGE,"E28.7.3");var subQ1=sQuery(id+"F22.wireOp",EDGE,"E28.7.2");var subQ2=sQuery(id+"F22.wireOp",EDGE,"E28.7.0");var subQ3=sQuery(id+"F3.wireOp",EDGE,"E20.15.3");var subQ4=sQuery(id+"F3.wireOp",EDGE,"E20.15.1");var subQ5=makeQuery(id+"F30.opLoft","SWEPT_FACE",FACE,{"disambiguationData":[OSD([subQ4,sQuery(id+"F3.wireOp",EDGE,"E20.15.2"),subQ3,subQ2,subQ1,subQ0])]});var subQ6=sQuery(id+"F22.wireOp",EDGE,"E28.7.1");var subQ7=sQuery(id+"F41.wireOp",EDGE,"E34");var subQ8=sQuery(id+"F41.wireOp",EDGE,"E32");Q21=makeQuery(id+"F44.opFillet","BLEND_EDGE",EDGE,{"blendedFrom":[makeQuery(id+"F40.boolean.opBoolean","INTERSECT",EDGE,{"derivedFrom":[subQ5,makeQuery(id+"F40.opExtrude","CAP_FACE",FACE,{"disambiguationData":[OSD([sQuery(id+"F39.wireOp",EDGE,"E29"),sQuery(id+"F39.wireOp",EDGE,"E30")])],"isStart":true})]}),makeQuery(id+"F42.boolean.opBoolean","COPY",FACE,{"disambiguationData":[TD([makeQuery(id+"F30.opLoft","SWEPT_FACE",FACE,{"disambiguationData":[OSD([sQuery(id+"F3.wireOp",EDGE,"E20.15.0"),subQ4,subQ3,subQ6,subQ1,subQ0])]})])],"derivedFrom":makeQuery(id+"F42.opRevolve","SWEPT_FACE",FACE,{"disambiguationData":[OSD([subQ8]),TDD([makeQuery(id+"F41.imprint","IMPRINT",EDGE,{"disambiguationData":[TD([[makeQuery(id+"F41.imprint","INTERSECT",VERTEX,{"disambiguationData":[OD(0.0)],"derivedFrom":[subQ8,subQ7]}),-1.0]])],"derivedFrom":subQ8})])]})})],"blendedInto":[makeQuery(id+"F42.boolean.opBoolean","COPY",FACE,{"disambiguationData":[TD([makeQuery(id+"F30.opLoft","SWEPT_FACE",FACE,{"disambiguationData":[OSD([sQuery(id+"F3.wireOp",EDGE,"E20.15.0"),subQ4,subQ3,subQ6,subQ1,subQ0])]})])],"derivedFrom":makeQuery(id+"F42.opRevolve","SWEPT_FACE",FACE,{"disambiguationData":[OSD([subQ8]),TDD([makeQuery(id+"F41.imprint","IMPRINT",EDGE,{"disambiguationData":[TD([[makeQuery(id+"F41.imprint","INTERSECT",VERTEX,{"disambiguationData":[OD(0.0)],"derivedFrom":[subQ8,subQ7]}),-1.0]])],"derivedFrom":subQ8})])]})})]});}
            var Q22;
            {var subQ0=sQuery(id+"F41.wireOp",EDGE,"E34");var subQ1=sQuery(id+"F41.wireOp",EDGE,"E32");Q22=makeQuery(id+"F42.boolean.opBoolean","INTERSECT",EDGE,{"derivedFrom":[makeQuery(id+"F29.opLoft","SWEPT_FACE",FACE,{"disambiguationData":[OSD([sQuery(id+"F3.wireOp",EDGE,"E20.14.0"),sQuery(id+"F3.wireOp",EDGE,"E20.14.1"),sQuery(id+"F3.wireOp",EDGE,"E20.14.3"),sQuery(id+"F22.wireOp",EDGE,"E28.6.1"),sQuery(id+"F22.wireOp",EDGE,"E28.6.2"),sQuery(id+"F22.wireOp",EDGE,"E28.6.3")])]}),makeQuery(id+"F42.opRevolve","SWEPT_FACE",FACE,{"disambiguationData":[OSD([subQ1]),TDD([makeQuery(id+"F41.imprint","IMPRINT",EDGE,{"disambiguationData":[TD([[makeQuery(id+"F41.imprint","INTERSECT",VERTEX,{"disambiguationData":[OD(0.0)],"derivedFrom":[subQ1,subQ0]}),-1.0]])],"derivedFrom":subQ1})])]})]});}
            var Q23;
            {var subQ0=sQuery(id+"F41.wireOp",EDGE,"E37");var subQ1=makeQuery(id+"F42.opRevolve","SWEPT_FACE",FACE,{"disambiguationData":[OSD([subQ0])]});var subQ2=makeQuery(id+"F40.opExtrude","CAP_FACE",FACE,{"disambiguationData":[OSD([sQuery(id+"F39.wireOp",EDGE,"E29"),sQuery(id+"F39.wireOp",EDGE,"E30")])],"isStart":true});var subQ3=sQuery(id+"F22.wireOp",EDGE,"E28.15.3");var subQ4=sQuery(id+"F22.wireOp",EDGE,"E28.15.2");var subQ5=sQuery(id+"F3.wireOp",EDGE,"E20.7.3");var subQ7=sQuery(id+"F3.wireOp",EDGE,"E20.7.1");var subQ8=sQuery(id+"F3.wireOp",EDGE,"E20.7.0");var subQ9=sQuery(id+"F41.wireOp",EDGE,"E38");var subQ10=makeQuery(id+"F42.opRevolve","SWEPT_FACE",FACE,{"disambiguationData":[OSD([subQ9])]});var subQ11=makeQuery(id+"F42.opRevolve","SWEPT_EDGE",EDGE,{"disambiguationData":[OSD([subQ0,subQ9])]});var subQ12=sQuery(id+"F22.wireOp",EDGE,"E28.14.3");var subQ13=sQuery(id+"F22.wireOp",EDGE,"E28.14.2");var subQ14=sQuery(id+"F3.wireOp",EDGE,"E20.6.3");var subQ15=sQuery(id+"F3.wireOp",EDGE,"E20.6.1");var subQ16=sQuery(id+"F3.wireOp",EDGE,"E20.6.0");var subQ18=sQuery(id+"F22.wireOp",EDGE,"E28.13.3");var subQ19=sQuery(id+"F22.wireOp",EDGE,"E28.13.2");var subQ20=sQuery(id+"F3.wireOp",EDGE,"E20.5.3");var subQ22=sQuery(id+"F3.wireOp",EDGE,"E20.5.1");var subQ23=sQuery(id+"F3.wireOp",EDGE,"E20.5.0");var subQ24=sQuery(id+"F22.wireOp",EDGE,"E28.12.3");var subQ25=sQuery(id+"F22.wireOp",EDGE,"E28.12.2");var subQ26=sQuery(id+"F3.wireOp",EDGE,"E20.4.3");var subQ28=sQuery(id+"F3.wireOp",EDGE,"E20.4.1");var subQ29=sQuery(id+"F3.wireOp",EDGE,"E20.4.0");var subQ30=sQuery(id+"F22.wireOp",EDGE,"E28.11.3");var subQ31=sQuery(id+"F22.wireOp",EDGE,"E28.11.2");var subQ32=sQuery(id+"F3.wireOp",EDGE,"E20.3.3");var subQ34=sQuery(id+"F3.wireOp",EDGE,"E20.3.1");var subQ35=sQuery(id+"F3.wireOp",EDGE,"E20.3.0");var subQ36=sQuery(id+"F22.wireOp",EDGE,"E28.10.3");var subQ37=sQuery(id+"F22.wireOp",EDGE,"E28.10.2");var subQ38=sQuery(id+"F3.wireOp",EDGE,"E20.2.3");var subQ40=sQuery(id+"F3.wireOp",EDGE,"E20.2.1");var subQ41=sQuery(id+"F3.wireOp",EDGE,"E20.2.0");var subQ42=sQuery(id+"F22.wireOp",EDGE,"E28.9.3");var subQ43=sQuery(id+"F22.wireOp",EDGE,"E28.9.2");var subQ44=sQuery(id+"F3.wireOp",EDGE,"E20.1.3");var subQ46=sQuery(id+"F3.wireOp",EDGE,"E20.1.1");var subQ47=sQuery(id+"F3.wireOp",EDGE,"E20.1.0");var subQ48=sQuery(id+"F22.wireOp",EDGE,"E28.8.3");var subQ49=sQuery(id+"F22.wireOp",EDGE,"E28.8.2");var subQ51=sQuery(id+"F3.wireOp",EDGE,"E18.top");var subQ52=sQuery(id+"F3.wireOp",EDGE,"E18.bottom");var subQ53=sQuery(id+"F3.wireOp",EDGE,"E18.left");var subQ54=sQuery(id+"F22.wireOp",EDGE,"E28.7.3");var subQ55=sQuery(id+"F22.wireOp",EDGE,"E28.7.2");var subQ56=sQuery(id+"F3.wireOp",EDGE,"E20.15.3");var subQ57=sQuery(id+"F3.wireOp",EDGE,"E20.15.1");var subQ58=sQuery(id+"F3.wireOp",EDGE,"E20.15.0");var subQ60=sQuery(id+"F22.wireOp",EDGE,"E28.6.3");var subQ61=sQuery(id+"F22.wireOp",EDGE,"E28.6.2");var subQ62=sQuery(id+"F3.wireOp",EDGE,"E20.14.3");var subQ64=sQuery(id+"F3.wireOp",EDGE,"E20.14.1");var subQ66=sQuery(id+"F3.wireOp",EDGE,"E20.14.0");var subQ67=makeQuery(id+"F29.opLoft","SWEPT_FACE",FACE,{"disambiguationData":[OSD([subQ66,subQ64,subQ62,sQuery(id+"F22.wireOp",EDGE,"E28.6.1"),subQ61,subQ60])]});var subQ68=sQuery(id+"F22.wireOp",EDGE,"E28.5.3");var subQ69=sQuery(id+"F22.wireOp",EDGE,"E28.5.2");var subQ70=sQuery(id+"F3.wireOp",EDGE,"E20.13.3");var subQ72=sQuery(id+"F3.wireOp",EDGE,"E20.13.1");var subQ73=sQuery(id+"F3.wireOp",EDGE,"E20.13.0");var subQ74=makeQuery(id+"F28.opLoft","SWEPT_FACE",FACE,{"disambiguationData":[OSD([subQ73,subQ72,subQ70,sQuery(id+"F22.wireOp",EDGE,"E28.5.1"),subQ69,subQ68])]});var subQ75=sQuery(id+"F22.wireOp",EDGE,"E28.4.3");var subQ76=sQuery(id+"F22.wireOp",EDGE,"E28.4.2");var subQ77=sQuery(id+"F3.wireOp",EDGE,"E20.12.3");var subQ79=sQuery(id+"F3.wireOp",EDGE,"E20.12.1");var subQ80=sQuery(id+"F3.wireOp",EDGE,"E20.12.0");var subQ81=makeQuery(id+"F27.opLoft","SWEPT_FACE",FACE,{"disambiguationData":[OSD([subQ80,subQ79,subQ77,sQuery(id+"F22.wireOp",EDGE,"E28.4.1"),subQ76,subQ75])]});var subQ82=sQuery(id+"F22.wireOp",EDGE,"E28.3.3");var subQ83=sQuery(id+"F22.wireOp",EDGE,"E28.3.2");var subQ84=sQuery(id+"F3.wireOp",EDGE,"E20.11.3");var subQ86=sQuery(id+"F3.wireOp",EDGE,"E20.11.1");var subQ87=sQuery(id+"F3.wireOp",EDGE,"E20.11.0");var subQ88=makeQuery(id+"F26.opLoft","SWEPT_FACE",FACE,{"disambiguationData":[OSD([subQ87,subQ86,subQ84,sQuery(id+"F22.wireOp",EDGE,"E28.3.1"),subQ83,subQ82])]});var subQ89=sQuery(id+"F22.wireOp",EDGE,"E28.2.3");var subQ90=sQuery(id+"F22.wireOp",EDGE,"E28.2.2");var subQ91=sQuery(id+"F3.wireOp",EDGE,"E20.10.3");var subQ92=sQuery(id+"F3.wireOp",EDGE,"E20.10.1");var subQ93=sQuery(id+"F3.wireOp",EDGE,"E20.10.0");var subQ94=makeQuery(id+"F25.opLoft","SWEPT_FACE",FACE,{"disambiguationData":[OSD([subQ93,subQ92,subQ91,sQuery(id+"F22.wireOp",EDGE,"E28.2.1"),subQ90,subQ89])]});var subQ96=sQuery(id+"F22.wireOp",EDGE,"E28.1.3");var subQ97=sQuery(id+"F22.wireOp",EDGE,"E28.1.2");var subQ98=sQuery(id+"F3.wireOp",EDGE,"E20.9.3");var subQ99=sQuery(id+"F3.wireOp",EDGE,"E20.9.1");var subQ100=sQuery(id+"F3.wireOp",EDGE,"E20.9.0");var subQ101=makeQuery(id+"F24.opLoft","SWEPT_FACE",FACE,{"disambiguationData":[OSD([subQ100,subQ99,subQ98,sQuery(id+"F22.wireOp",EDGE,"E28.1.1"),subQ97,subQ96])]});var subQ102=sQuery(id+"F22.wireOp",EDGE,"E27.top");var subQ103=sQuery(id+"F22.wireOp",EDGE,"E27.bottom");var subQ104=sQuery(id+"F3.wireOp",EDGE,"E20.8.3");var subQ106=sQuery(id+"F3.wireOp",EDGE,"E20.8.1");var subQ110=makeQuery(id+"F42.boolean.opBoolean","COPY",FACE,{"disambiguationData":[TD([subQ67])],"derivedFrom":subQ10});var subQ130=makeQuery(id+"F5.opLoft","CAP_FACE",FACE,{"disambiguationData":[OSD([makeQuery(id+"F3.imprint","IMPRINT",FACE,{"disambiguationData":[TD([[makeQuery(id+"F3.imprint","IMPRINT",EDGE,{"derivedFrom":subQ52}),1.0]])]})])],"isStart":true});var subQ182=makeQuery(id+"F29.boolean.opBoolean","INTERSECT",EDGE,{"derivedFrom":[makeQuery(id+"F28.boolean.opBoolean","SPLIT",FACE,{"disambiguationData":[TD([subQ130])],"derivedFrom":makeQuery(id+"F27.boolean.opBoolean","SPLIT",FACE,{"disambiguationData":[TD([subQ130])],"derivedFrom":makeQuery(id+"F26.boolean.opBoolean","SPLIT",FACE,{"disambiguationData":[TD([subQ130])],"derivedFrom":makeQuery(id+"F25.boolean.opBoolean","SPLIT",FACE,{"disambiguationData":[TD([subQ130])],"derivedFrom":makeQuery(id+"F24.boolean.opBoolean","SPLIT",FACE,{"disambiguationData":[TD([subQ130])],"derivedFrom":makeQuery(id+"F1.opRevolve","SWEPT_FACE",FACE,{"disambiguationData":[OSD([sQuery(id+"F0.wireOp",EDGE,"E4")])]})})})})})}),subQ67]});Q23=makeQuery(id+"F48.opFillet","BLEND_EDGE",EDGE,{"blendedFrom":[makeQuery(id+"F47.opFillet","TWEAK_EDGE",EDGE,{"derivedFrom":[makeQuery(id+"F45.opFillet","BLEND_VERTEX",VERTEX,{"blendedFrom":[subQ182,subQ67,subQ110],"blendedInto":[subQ67,subQ110]}),makeQuery(id+"F45.opFillet","BLEND_VERTEX",VERTEX,{"blendedFrom":[subQ182,makeQuery(id+"F42.boolean.opBoolean","MERGE",FACE,{"derivedFrom":[subQ2,subQ1]}),subQ110],"blendedInto":[makeQuery(id+"F42.boolean.opBoolean","MERGE",FACE,{"derivedFrom":[subQ2,subQ1]}),subQ110]})]}),makeQuery(id+"F47.opFillet","BLEND_FACE",FACE,{"disambiguationData":[OSD([subQ0,subQ9]),TDD([makeQuery(id+"F42.boolean.opBoolean","COPY",EDGE,{"disambiguationData":[TD([makeQuery(id+"F23.opLoft","SWEPT_FACE",FACE,{"disambiguationData":[OSD([sQuery(id+"F3.wireOp",EDGE,"E20.8.0"),subQ106,subQ104,subQ103,subQ102,sQuery(id+"F22.wireOp",EDGE,"E27.right")])]})])],"derivedFrom":subQ11})])]}),makeQuery(id+"F47.opFillet","BLEND_FACE",FACE,{"disambiguationData":[OSD([subQ0,subQ9]),TDD([makeQuery(id+"F42.boolean.opBoolean","COPY",EDGE,{"disambiguationData":[TD([subQ101])],"derivedFrom":subQ11})])]}),makeQuery(id+"F47.opFillet","BLEND_FACE",FACE,{"disambiguationData":[OSD([subQ0,subQ9]),TDD([makeQuery(id+"F42.boolean.opBoolean","COPY",EDGE,{"disambiguationData":[TD([subQ94])],"derivedFrom":subQ11})])]}),makeQuery(id+"F47.opFillet","BLEND_FACE",FACE,{"disambiguationData":[OSD([subQ0,subQ9]),TDD([makeQuery(id+"F42.boolean.opBoolean","COPY",EDGE,{"disambiguationData":[TD([subQ88])],"derivedFrom":subQ11})])]}),makeQuery(id+"F47.opFillet","BLEND_FACE",FACE,{"disambiguationData":[OSD([subQ0,subQ9]),TDD([makeQuery(id+"F42.boolean.opBoolean","COPY",EDGE,{"disambiguationData":[TD([subQ81])],"derivedFrom":subQ11})])]}),makeQuery(id+"F47.opFillet","BLEND_FACE",FACE,{"disambiguationData":[OSD([subQ0,subQ9]),TDD([makeQuery(id+"F42.boolean.opBoolean","COPY",EDGE,{"disambiguationData":[TD([subQ74])],"derivedFrom":subQ11})])]}),makeQuery(id+"F47.opFillet","BLEND_FACE",FACE,{"disambiguationData":[OSD([subQ0,subQ9]),TDD([makeQuery(id+"F42.boolean.opBoolean","COPY",EDGE,{"disambiguationData":[TD([subQ67])],"derivedFrom":subQ11})])]}),makeQuery(id+"F47.opFillet","BLEND_FACE",FACE,{"disambiguationData":[OSD([subQ0,subQ9]),TDD([makeQuery(id+"F42.boolean.opBoolean","COPY",EDGE,{"disambiguationData":[TD([makeQuery(id+"F30.opLoft","SWEPT_FACE",FACE,{"disambiguationData":[OSD([subQ58,subQ57,subQ56,sQuery(id+"F22.wireOp",EDGE,"E28.7.1"),subQ55,subQ54])]})])],"derivedFrom":subQ11})])]}),makeQuery(id+"F47.opFillet","BLEND_FACE",FACE,{"disambiguationData":[OSD([subQ0,subQ9]),TDD([makeQuery(id+"F42.boolean.opBoolean","COPY",EDGE,{"disambiguationData":[TD([makeQuery(id+"F31.opLoft","SWEPT_FACE",FACE,{"disambiguationData":[OSD([subQ52,subQ51,subQ53,sQuery(id+"F22.wireOp",EDGE,"E28.8.1"),subQ49,subQ48])]})])],"derivedFrom":subQ11})])]}),makeQuery(id+"F47.opFillet","BLEND_FACE",FACE,{"disambiguationData":[OSD([subQ0,subQ9]),TDD([makeQuery(id+"F42.boolean.opBoolean","COPY",EDGE,{"disambiguationData":[TD([makeQuery(id+"F32.opLoft","SWEPT_FACE",FACE,{"disambiguationData":[OSD([subQ47,subQ46,subQ44,sQuery(id+"F22.wireOp",EDGE,"E28.9.1"),subQ43,subQ42])]})])],"derivedFrom":subQ11})])]}),makeQuery(id+"F47.opFillet","BLEND_FACE",FACE,{"disambiguationData":[OSD([subQ0,subQ9]),TDD([makeQuery(id+"F42.boolean.opBoolean","COPY",EDGE,{"disambiguationData":[TD([makeQuery(id+"F33.opLoft","SWEPT_FACE",FACE,{"disambiguationData":[OSD([subQ41,subQ40,subQ38,sQuery(id+"F22.wireOp",EDGE,"E28.10.1"),subQ37,subQ36])]})])],"derivedFrom":subQ11})])]}),makeQuery(id+"F47.opFillet","BLEND_FACE",FACE,{"disambiguationData":[OSD([subQ0,subQ9]),TDD([makeQuery(id+"F42.boolean.opBoolean","COPY",EDGE,{"disambiguationData":[TD([makeQuery(id+"F34.opLoft","SWEPT_FACE",FACE,{"disambiguationData":[OSD([subQ35,subQ34,subQ32,sQuery(id+"F22.wireOp",EDGE,"E28.11.1"),subQ31,subQ30])]})])],"derivedFrom":subQ11})])]}),makeQuery(id+"F47.opFillet","BLEND_FACE",FACE,{"disambiguationData":[OSD([subQ0,subQ9]),TDD([makeQuery(id+"F42.boolean.opBoolean","COPY",EDGE,{"disambiguationData":[TD([makeQuery(id+"F35.opLoft","SWEPT_FACE",FACE,{"disambiguationData":[OSD([subQ29,subQ28,subQ26,sQuery(id+"F22.wireOp",EDGE,"E28.12.1"),subQ25,subQ24])]})])],"derivedFrom":subQ11})])]}),makeQuery(id+"F47.opFillet","BLEND_FACE",FACE,{"disambiguationData":[OSD([subQ0,subQ9]),TDD([makeQuery(id+"F42.boolean.opBoolean","COPY",EDGE,{"disambiguationData":[TD([makeQuery(id+"F36.opLoft","SWEPT_FACE",FACE,{"disambiguationData":[OSD([subQ23,subQ22,subQ20,sQuery(id+"F22.wireOp",EDGE,"E28.13.1"),subQ19,subQ18])]})])],"derivedFrom":subQ11})])]}),makeQuery(id+"F47.opFillet","BLEND_FACE",FACE,{"disambiguationData":[OSD([subQ0,subQ9]),TDD([makeQuery(id+"F42.boolean.opBoolean","COPY",EDGE,{"disambiguationData":[TD([makeQuery(id+"F37.opLoft","SWEPT_FACE",FACE,{"disambiguationData":[OSD([subQ16,subQ15,subQ14,sQuery(id+"F22.wireOp",EDGE,"E28.14.1"),subQ13,subQ12])]})])],"derivedFrom":subQ11})])]}),makeQuery(id+"F47.opFillet","BLEND_FACE",FACE,{"disambiguationData":[OSD([subQ0,subQ9]),TDD([makeQuery(id+"F42.boolean.opBoolean","COPY",EDGE,{"disambiguationData":[TD([makeQuery(id+"F38.opLoft","SWEPT_FACE",FACE,{"disambiguationData":[OSD([subQ8,subQ7,subQ5,sQuery(id+"F22.wireOp",EDGE,"E28.15.1"),subQ4,subQ3])]})])],"derivedFrom":subQ11})])]})],"blendedInto":[makeQuery(id+"F47.opFillet","BLEND_FACE",FACE,{"disambiguationData":[OSD([subQ0,subQ9]),TDD([makeQuery(id+"F42.boolean.opBoolean","COPY",EDGE,{"disambiguationData":[TD([makeQuery(id+"F23.opLoft","SWEPT_FACE",FACE,{"disambiguationData":[OSD([sQuery(id+"F3.wireOp",EDGE,"E20.8.0"),subQ106,subQ104,subQ103,subQ102,sQuery(id+"F22.wireOp",EDGE,"E27.right")])]})])],"derivedFrom":subQ11})])]}),makeQuery(id+"F47.opFillet","BLEND_FACE",FACE,{"disambiguationData":[OSD([subQ0,subQ9]),TDD([makeQuery(id+"F42.boolean.opBoolean","COPY",EDGE,{"disambiguationData":[TD([subQ101])],"derivedFrom":subQ11})])]}),makeQuery(id+"F47.opFillet","BLEND_FACE",FACE,{"disambiguationData":[OSD([subQ0,subQ9]),TDD([makeQuery(id+"F42.boolean.opBoolean","COPY",EDGE,{"disambiguationData":[TD([subQ94])],"derivedFrom":subQ11})])]}),makeQuery(id+"F47.opFillet","BLEND_FACE",FACE,{"disambiguationData":[OSD([subQ0,subQ9]),TDD([makeQuery(id+"F42.boolean.opBoolean","COPY",EDGE,{"disambiguationData":[TD([subQ88])],"derivedFrom":subQ11})])]}),makeQuery(id+"F47.opFillet","BLEND_FACE",FACE,{"disambiguationData":[OSD([subQ0,subQ9]),TDD([makeQuery(id+"F42.boolean.opBoolean","COPY",EDGE,{"disambiguationData":[TD([subQ81])],"derivedFrom":subQ11})])]}),makeQuery(id+"F47.opFillet","BLEND_FACE",FACE,{"disambiguationData":[OSD([subQ0,subQ9]),TDD([makeQuery(id+"F42.boolean.opBoolean","COPY",EDGE,{"disambiguationData":[TD([subQ74])],"derivedFrom":subQ11})])]}),makeQuery(id+"F47.opFillet","BLEND_FACE",FACE,{"disambiguationData":[OSD([subQ0,subQ9]),TDD([makeQuery(id+"F42.boolean.opBoolean","COPY",EDGE,{"disambiguationData":[TD([subQ67])],"derivedFrom":subQ11})])]}),makeQuery(id+"F47.opFillet","BLEND_FACE",FACE,{"disambiguationData":[OSD([subQ0,subQ9]),TDD([makeQuery(id+"F42.boolean.opBoolean","COPY",EDGE,{"disambiguationData":[TD([makeQuery(id+"F30.opLoft","SWEPT_FACE",FACE,{"disambiguationData":[OSD([subQ58,subQ57,subQ56,sQuery(id+"F22.wireOp",EDGE,"E28.7.1"),subQ55,subQ54])]})])],"derivedFrom":subQ11})])]}),makeQuery(id+"F47.opFillet","BLEND_FACE",FACE,{"disambiguationData":[OSD([subQ0,subQ9]),TDD([makeQuery(id+"F42.boolean.opBoolean","COPY",EDGE,{"disambiguationData":[TD([makeQuery(id+"F31.opLoft","SWEPT_FACE",FACE,{"disambiguationData":[OSD([subQ52,subQ51,subQ53,sQuery(id+"F22.wireOp",EDGE,"E28.8.1"),subQ49,subQ48])]})])],"derivedFrom":subQ11})])]}),makeQuery(id+"F47.opFillet","BLEND_FACE",FACE,{"disambiguationData":[OSD([subQ0,subQ9]),TDD([makeQuery(id+"F42.boolean.opBoolean","COPY",EDGE,{"disambiguationData":[TD([makeQuery(id+"F32.opLoft","SWEPT_FACE",FACE,{"disambiguationData":[OSD([subQ47,subQ46,subQ44,sQuery(id+"F22.wireOp",EDGE,"E28.9.1"),subQ43,subQ42])]})])],"derivedFrom":subQ11})])]}),makeQuery(id+"F47.opFillet","BLEND_FACE",FACE,{"disambiguationData":[OSD([subQ0,subQ9]),TDD([makeQuery(id+"F42.boolean.opBoolean","COPY",EDGE,{"disambiguationData":[TD([makeQuery(id+"F33.opLoft","SWEPT_FACE",FACE,{"disambiguationData":[OSD([subQ41,subQ40,subQ38,sQuery(id+"F22.wireOp",EDGE,"E28.10.1"),subQ37,subQ36])]})])],"derivedFrom":subQ11})])]}),makeQuery(id+"F47.opFillet","BLEND_FACE",FACE,{"disambiguationData":[OSD([subQ0,subQ9]),TDD([makeQuery(id+"F42.boolean.opBoolean","COPY",EDGE,{"disambiguationData":[TD([makeQuery(id+"F34.opLoft","SWEPT_FACE",FACE,{"disambiguationData":[OSD([subQ35,subQ34,subQ32,sQuery(id+"F22.wireOp",EDGE,"E28.11.1"),subQ31,subQ30])]})])],"derivedFrom":subQ11})])]}),makeQuery(id+"F47.opFillet","BLEND_FACE",FACE,{"disambiguationData":[OSD([subQ0,subQ9]),TDD([makeQuery(id+"F42.boolean.opBoolean","COPY",EDGE,{"disambiguationData":[TD([makeQuery(id+"F35.opLoft","SWEPT_FACE",FACE,{"disambiguationData":[OSD([subQ29,subQ28,subQ26,sQuery(id+"F22.wireOp",EDGE,"E28.12.1"),subQ25,subQ24])]})])],"derivedFrom":subQ11})])]}),makeQuery(id+"F47.opFillet","BLEND_FACE",FACE,{"disambiguationData":[OSD([subQ0,subQ9]),TDD([makeQuery(id+"F42.boolean.opBoolean","COPY",EDGE,{"disambiguationData":[TD([makeQuery(id+"F36.opLoft","SWEPT_FACE",FACE,{"disambiguationData":[OSD([subQ23,subQ22,subQ20,sQuery(id+"F22.wireOp",EDGE,"E28.13.1"),subQ19,subQ18])]})])],"derivedFrom":subQ11})])]}),makeQuery(id+"F47.opFillet","BLEND_FACE",FACE,{"disambiguationData":[OSD([subQ0,subQ9]),TDD([makeQuery(id+"F42.boolean.opBoolean","COPY",EDGE,{"disambiguationData":[TD([makeQuery(id+"F37.opLoft","SWEPT_FACE",FACE,{"disambiguationData":[OSD([subQ16,subQ15,subQ14,sQuery(id+"F22.wireOp",EDGE,"E28.14.1"),subQ13,subQ12])]})])],"derivedFrom":subQ11})])]}),makeQuery(id+"F47.opFillet","BLEND_FACE",FACE,{"disambiguationData":[OSD([subQ0,subQ9]),TDD([makeQuery(id+"F42.boolean.opBoolean","COPY",EDGE,{"disambiguationData":[TD([makeQuery(id+"F38.opLoft","SWEPT_FACE",FACE,{"disambiguationData":[OSD([subQ8,subQ7,subQ5,sQuery(id+"F22.wireOp",EDGE,"E28.15.1"),subQ4,subQ3])]})])],"derivedFrom":subQ11})])]})]});}
            var Q24;
            {var subQ0=sQuery(id+"F41.wireOp",EDGE,"E34");var subQ1=sQuery(id+"F41.wireOp",EDGE,"E32");Q24=makeQuery(id+"F42.boolean.opBoolean","INTERSECT",EDGE,{"derivedFrom":[makeQuery(id+"F28.opLoft","SWEPT_FACE",FACE,{"disambiguationData":[OSD([sQuery(id+"F3.wireOp",EDGE,"E20.13.0"),sQuery(id+"F3.wireOp",EDGE,"E20.13.1"),sQuery(id+"F3.wireOp",EDGE,"E20.13.3"),sQuery(id+"F22.wireOp",EDGE,"E28.5.1"),sQuery(id+"F22.wireOp",EDGE,"E28.5.2"),sQuery(id+"F22.wireOp",EDGE,"E28.5.3")])]}),makeQuery(id+"F42.opRevolve","SWEPT_FACE",FACE,{"disambiguationData":[OSD([subQ1]),TDD([makeQuery(id+"F41.imprint","IMPRINT",EDGE,{"disambiguationData":[TD([[makeQuery(id+"F41.imprint","INTERSECT",VERTEX,{"disambiguationData":[OD(0.0)],"derivedFrom":[subQ1,subQ0]}),-1.0]])],"derivedFrom":subQ1})])]})]});}
            var Q25;
            {var subQ0=sQuery(id+"F22.wireOp",EDGE,"E28.6.3");var subQ1=sQuery(id+"F22.wireOp",EDGE,"E28.6.2");var subQ2=sQuery(id+"F22.wireOp",EDGE,"E28.6.0");var subQ3=sQuery(id+"F3.wireOp",EDGE,"E20.14.3");var subQ4=sQuery(id+"F3.wireOp",EDGE,"E20.14.1");var subQ5=makeQuery(id+"F29.opLoft","SWEPT_FACE",FACE,{"disambiguationData":[OSD([subQ4,sQuery(id+"F3.wireOp",EDGE,"E20.14.2"),subQ3,subQ2,subQ1,subQ0])]});var subQ6=sQuery(id+"F22.wireOp",EDGE,"E28.6.1");var subQ7=sQuery(id+"F41.wireOp",EDGE,"E34");var subQ8=sQuery(id+"F41.wireOp",EDGE,"E32");Q25=makeQuery(id+"F44.opFillet","BLEND_EDGE",EDGE,{"blendedFrom":[makeQuery(id+"F40.boolean.opBoolean","INTERSECT",EDGE,{"derivedFrom":[subQ5,makeQuery(id+"F40.opExtrude","CAP_FACE",FACE,{"disambiguationData":[OSD([sQuery(id+"F39.wireOp",EDGE,"E29"),sQuery(id+"F39.wireOp",EDGE,"E30")])],"isStart":true})]}),makeQuery(id+"F42.boolean.opBoolean","COPY",FACE,{"disambiguationData":[TD([makeQuery(id+"F29.opLoft","SWEPT_FACE",FACE,{"disambiguationData":[OSD([sQuery(id+"F3.wireOp",EDGE,"E20.14.0"),subQ4,subQ3,subQ6,subQ1,subQ0])]})])],"derivedFrom":makeQuery(id+"F42.opRevolve","SWEPT_FACE",FACE,{"disambiguationData":[OSD([subQ8]),TDD([makeQuery(id+"F41.imprint","IMPRINT",EDGE,{"disambiguationData":[TD([[makeQuery(id+"F41.imprint","INTERSECT",VERTEX,{"disambiguationData":[OD(0.0)],"derivedFrom":[subQ8,subQ7]}),-1.0]])],"derivedFrom":subQ8})])]})})],"blendedInto":[makeQuery(id+"F42.boolean.opBoolean","COPY",FACE,{"disambiguationData":[TD([makeQuery(id+"F29.opLoft","SWEPT_FACE",FACE,{"disambiguationData":[OSD([sQuery(id+"F3.wireOp",EDGE,"E20.14.0"),subQ4,subQ3,subQ6,subQ1,subQ0])]})])],"derivedFrom":makeQuery(id+"F42.opRevolve","SWEPT_FACE",FACE,{"disambiguationData":[OSD([subQ8]),TDD([makeQuery(id+"F41.imprint","IMPRINT",EDGE,{"disambiguationData":[TD([[makeQuery(id+"F41.imprint","INTERSECT",VERTEX,{"disambiguationData":[OD(0.0)],"derivedFrom":[subQ8,subQ7]}),-1.0]])],"derivedFrom":subQ8})])]})})]});}
            var Q26;
            {var subQ0=sQuery(id+"F41.wireOp",EDGE,"E37");var subQ1=makeQuery(id+"F42.opRevolve","SWEPT_FACE",FACE,{"disambiguationData":[OSD([subQ0])]});var subQ2=makeQuery(id+"F40.opExtrude","CAP_FACE",FACE,{"disambiguationData":[OSD([sQuery(id+"F39.wireOp",EDGE,"E29"),sQuery(id+"F39.wireOp",EDGE,"E30")])],"isStart":true});var subQ3=sQuery(id+"F22.wireOp",EDGE,"E28.15.3");var subQ4=sQuery(id+"F22.wireOp",EDGE,"E28.15.2");var subQ5=sQuery(id+"F3.wireOp",EDGE,"E20.7.3");var subQ7=sQuery(id+"F3.wireOp",EDGE,"E20.7.1");var subQ8=sQuery(id+"F3.wireOp",EDGE,"E20.7.0");var subQ9=sQuery(id+"F41.wireOp",EDGE,"E38");var subQ10=makeQuery(id+"F42.opRevolve","SWEPT_FACE",FACE,{"disambiguationData":[OSD([subQ9])]});var subQ11=makeQuery(id+"F42.opRevolve","SWEPT_EDGE",EDGE,{"disambiguationData":[OSD([subQ0,subQ9])]});var subQ12=sQuery(id+"F22.wireOp",EDGE,"E28.14.3");var subQ13=sQuery(id+"F22.wireOp",EDGE,"E28.14.2");var subQ14=sQuery(id+"F3.wireOp",EDGE,"E20.6.3");var subQ15=sQuery(id+"F3.wireOp",EDGE,"E20.6.1");var subQ16=sQuery(id+"F3.wireOp",EDGE,"E20.6.0");var subQ18=sQuery(id+"F22.wireOp",EDGE,"E28.13.3");var subQ19=sQuery(id+"F22.wireOp",EDGE,"E28.13.2");var subQ20=sQuery(id+"F3.wireOp",EDGE,"E20.5.3");var subQ22=sQuery(id+"F3.wireOp",EDGE,"E20.5.1");var subQ23=sQuery(id+"F3.wireOp",EDGE,"E20.5.0");var subQ24=sQuery(id+"F22.wireOp",EDGE,"E28.12.3");var subQ25=sQuery(id+"F22.wireOp",EDGE,"E28.12.2");var subQ26=sQuery(id+"F3.wireOp",EDGE,"E20.4.3");var subQ28=sQuery(id+"F3.wireOp",EDGE,"E20.4.1");var subQ29=sQuery(id+"F3.wireOp",EDGE,"E20.4.0");var subQ30=sQuery(id+"F22.wireOp",EDGE,"E28.11.3");var subQ31=sQuery(id+"F22.wireOp",EDGE,"E28.11.2");var subQ32=sQuery(id+"F3.wireOp",EDGE,"E20.3.3");var subQ34=sQuery(id+"F3.wireOp",EDGE,"E20.3.1");var subQ35=sQuery(id+"F3.wireOp",EDGE,"E20.3.0");var subQ36=sQuery(id+"F22.wireOp",EDGE,"E28.10.3");var subQ37=sQuery(id+"F22.wireOp",EDGE,"E28.10.2");var subQ38=sQuery(id+"F3.wireOp",EDGE,"E20.2.3");var subQ40=sQuery(id+"F3.wireOp",EDGE,"E20.2.1");var subQ41=sQuery(id+"F3.wireOp",EDGE,"E20.2.0");var subQ42=sQuery(id+"F22.wireOp",EDGE,"E28.9.3");var subQ43=sQuery(id+"F22.wireOp",EDGE,"E28.9.2");var subQ44=sQuery(id+"F3.wireOp",EDGE,"E20.1.3");var subQ46=sQuery(id+"F3.wireOp",EDGE,"E20.1.1");var subQ47=sQuery(id+"F3.wireOp",EDGE,"E20.1.0");var subQ48=sQuery(id+"F22.wireOp",EDGE,"E28.8.3");var subQ49=sQuery(id+"F22.wireOp",EDGE,"E28.8.2");var subQ51=sQuery(id+"F3.wireOp",EDGE,"E18.top");var subQ52=sQuery(id+"F3.wireOp",EDGE,"E18.bottom");var subQ53=sQuery(id+"F3.wireOp",EDGE,"E18.left");var subQ54=sQuery(id+"F22.wireOp",EDGE,"E28.7.3");var subQ55=sQuery(id+"F22.wireOp",EDGE,"E28.7.2");var subQ56=sQuery(id+"F3.wireOp",EDGE,"E20.15.3");var subQ57=sQuery(id+"F3.wireOp",EDGE,"E20.15.1");var subQ58=sQuery(id+"F3.wireOp",EDGE,"E20.15.0");var subQ60=sQuery(id+"F22.wireOp",EDGE,"E28.6.3");var subQ61=sQuery(id+"F22.wireOp",EDGE,"E28.6.2");var subQ62=sQuery(id+"F3.wireOp",EDGE,"E20.14.3");var subQ64=sQuery(id+"F3.wireOp",EDGE,"E20.14.1");var subQ65=sQuery(id+"F3.wireOp",EDGE,"E20.14.0");var subQ66=sQuery(id+"F22.wireOp",EDGE,"E28.5.3");var subQ67=sQuery(id+"F22.wireOp",EDGE,"E28.5.2");var subQ68=sQuery(id+"F3.wireOp",EDGE,"E20.13.3");var subQ70=sQuery(id+"F3.wireOp",EDGE,"E20.13.1");var subQ72=sQuery(id+"F3.wireOp",EDGE,"E20.13.0");var subQ73=makeQuery(id+"F28.opLoft","SWEPT_FACE",FACE,{"disambiguationData":[OSD([subQ72,subQ70,subQ68,sQuery(id+"F22.wireOp",EDGE,"E28.5.1"),subQ67,subQ66])]});var subQ74=sQuery(id+"F22.wireOp",EDGE,"E28.4.3");var subQ75=sQuery(id+"F22.wireOp",EDGE,"E28.4.2");var subQ76=sQuery(id+"F3.wireOp",EDGE,"E20.12.3");var subQ78=sQuery(id+"F3.wireOp",EDGE,"E20.12.1");var subQ79=sQuery(id+"F3.wireOp",EDGE,"E20.12.0");var subQ80=makeQuery(id+"F27.opLoft","SWEPT_FACE",FACE,{"disambiguationData":[OSD([subQ79,subQ78,subQ76,sQuery(id+"F22.wireOp",EDGE,"E28.4.1"),subQ75,subQ74])]});var subQ81=sQuery(id+"F22.wireOp",EDGE,"E28.3.3");var subQ82=sQuery(id+"F22.wireOp",EDGE,"E28.3.2");var subQ83=sQuery(id+"F3.wireOp",EDGE,"E20.11.3");var subQ85=sQuery(id+"F3.wireOp",EDGE,"E20.11.1");var subQ86=sQuery(id+"F3.wireOp",EDGE,"E20.11.0");var subQ87=makeQuery(id+"F26.opLoft","SWEPT_FACE",FACE,{"disambiguationData":[OSD([subQ86,subQ85,subQ83,sQuery(id+"F22.wireOp",EDGE,"E28.3.1"),subQ82,subQ81])]});var subQ88=sQuery(id+"F22.wireOp",EDGE,"E28.2.3");var subQ89=sQuery(id+"F22.wireOp",EDGE,"E28.2.2");var subQ90=sQuery(id+"F3.wireOp",EDGE,"E20.10.3");var subQ91=sQuery(id+"F3.wireOp",EDGE,"E20.10.1");var subQ92=sQuery(id+"F3.wireOp",EDGE,"E20.10.0");var subQ93=makeQuery(id+"F25.opLoft","SWEPT_FACE",FACE,{"disambiguationData":[OSD([subQ92,subQ91,subQ90,sQuery(id+"F22.wireOp",EDGE,"E28.2.1"),subQ89,subQ88])]});var subQ95=sQuery(id+"F22.wireOp",EDGE,"E28.1.3");var subQ96=sQuery(id+"F22.wireOp",EDGE,"E28.1.2");var subQ97=sQuery(id+"F3.wireOp",EDGE,"E20.9.3");var subQ98=sQuery(id+"F3.wireOp",EDGE,"E20.9.1");var subQ99=sQuery(id+"F3.wireOp",EDGE,"E20.9.0");var subQ100=makeQuery(id+"F24.opLoft","SWEPT_FACE",FACE,{"disambiguationData":[OSD([subQ99,subQ98,subQ97,sQuery(id+"F22.wireOp",EDGE,"E28.1.1"),subQ96,subQ95])]});var subQ101=sQuery(id+"F22.wireOp",EDGE,"E27.top");var subQ102=sQuery(id+"F22.wireOp",EDGE,"E27.bottom");var subQ103=sQuery(id+"F3.wireOp",EDGE,"E20.8.3");var subQ105=sQuery(id+"F3.wireOp",EDGE,"E20.8.1");var subQ109=makeQuery(id+"F42.boolean.opBoolean","COPY",FACE,{"disambiguationData":[TD([subQ73])],"derivedFrom":subQ10});var subQ135=makeQuery(id+"F5.opLoft","CAP_FACE",FACE,{"disambiguationData":[OSD([makeQuery(id+"F3.imprint","IMPRINT",FACE,{"disambiguationData":[TD([[makeQuery(id+"F3.imprint","IMPRINT",EDGE,{"derivedFrom":subQ52}),1.0]])]})])],"isStart":true});var subQ181=makeQuery(id+"F28.boolean.opBoolean","INTERSECT",EDGE,{"derivedFrom":[makeQuery(id+"F27.boolean.opBoolean","SPLIT",FACE,{"disambiguationData":[TD([subQ135])],"derivedFrom":makeQuery(id+"F26.boolean.opBoolean","SPLIT",FACE,{"disambiguationData":[TD([subQ135])],"derivedFrom":makeQuery(id+"F25.boolean.opBoolean","SPLIT",FACE,{"disambiguationData":[TD([subQ135])],"derivedFrom":makeQuery(id+"F24.boolean.opBoolean","SPLIT",FACE,{"disambiguationData":[TD([subQ135])],"derivedFrom":makeQuery(id+"F1.opRevolve","SWEPT_FACE",FACE,{"disambiguationData":[OSD([sQuery(id+"F0.wireOp",EDGE,"E4")])]})})})})}),subQ73]});Q26=makeQuery(id+"F48.opFillet","BLEND_EDGE",EDGE,{"blendedFrom":[makeQuery(id+"F47.opFillet","TWEAK_EDGE",EDGE,{"derivedFrom":[makeQuery(id+"F45.opFillet","BLEND_VERTEX",VERTEX,{"blendedFrom":[subQ181,subQ73,subQ109],"blendedInto":[subQ73,subQ109]}),makeQuery(id+"F45.opFillet","BLEND_VERTEX",VERTEX,{"blendedFrom":[subQ181,makeQuery(id+"F42.boolean.opBoolean","MERGE",FACE,{"derivedFrom":[subQ2,subQ1]}),subQ109],"blendedInto":[makeQuery(id+"F42.boolean.opBoolean","MERGE",FACE,{"derivedFrom":[subQ2,subQ1]}),subQ109]})]}),makeQuery(id+"F47.opFillet","BLEND_FACE",FACE,{"disambiguationData":[OSD([subQ0,subQ9]),TDD([makeQuery(id+"F42.boolean.opBoolean","COPY",EDGE,{"disambiguationData":[TD([makeQuery(id+"F23.opLoft","SWEPT_FACE",FACE,{"disambiguationData":[OSD([sQuery(id+"F3.wireOp",EDGE,"E20.8.0"),subQ105,subQ103,subQ102,subQ101,sQuery(id+"F22.wireOp",EDGE,"E27.right")])]})])],"derivedFrom":subQ11})])]}),makeQuery(id+"F47.opFillet","BLEND_FACE",FACE,{"disambiguationData":[OSD([subQ0,subQ9]),TDD([makeQuery(id+"F42.boolean.opBoolean","COPY",EDGE,{"disambiguationData":[TD([subQ100])],"derivedFrom":subQ11})])]}),makeQuery(id+"F47.opFillet","BLEND_FACE",FACE,{"disambiguationData":[OSD([subQ0,subQ9]),TDD([makeQuery(id+"F42.boolean.opBoolean","COPY",EDGE,{"disambiguationData":[TD([subQ93])],"derivedFrom":subQ11})])]}),makeQuery(id+"F47.opFillet","BLEND_FACE",FACE,{"disambiguationData":[OSD([subQ0,subQ9]),TDD([makeQuery(id+"F42.boolean.opBoolean","COPY",EDGE,{"disambiguationData":[TD([subQ87])],"derivedFrom":subQ11})])]}),makeQuery(id+"F47.opFillet","BLEND_FACE",FACE,{"disambiguationData":[OSD([subQ0,subQ9]),TDD([makeQuery(id+"F42.boolean.opBoolean","COPY",EDGE,{"disambiguationData":[TD([subQ80])],"derivedFrom":subQ11})])]}),makeQuery(id+"F47.opFillet","BLEND_FACE",FACE,{"disambiguationData":[OSD([subQ0,subQ9]),TDD([makeQuery(id+"F42.boolean.opBoolean","COPY",EDGE,{"disambiguationData":[TD([subQ73])],"derivedFrom":subQ11})])]}),makeQuery(id+"F47.opFillet","BLEND_FACE",FACE,{"disambiguationData":[OSD([subQ0,subQ9]),TDD([makeQuery(id+"F42.boolean.opBoolean","COPY",EDGE,{"disambiguationData":[TD([makeQuery(id+"F29.opLoft","SWEPT_FACE",FACE,{"disambiguationData":[OSD([subQ65,subQ64,subQ62,sQuery(id+"F22.wireOp",EDGE,"E28.6.1"),subQ61,subQ60])]})])],"derivedFrom":subQ11})])]}),makeQuery(id+"F47.opFillet","BLEND_FACE",FACE,{"disambiguationData":[OSD([subQ0,subQ9]),TDD([makeQuery(id+"F42.boolean.opBoolean","COPY",EDGE,{"disambiguationData":[TD([makeQuery(id+"F30.opLoft","SWEPT_FACE",FACE,{"disambiguationData":[OSD([subQ58,subQ57,subQ56,sQuery(id+"F22.wireOp",EDGE,"E28.7.1"),subQ55,subQ54])]})])],"derivedFrom":subQ11})])]}),makeQuery(id+"F47.opFillet","BLEND_FACE",FACE,{"disambiguationData":[OSD([subQ0,subQ9]),TDD([makeQuery(id+"F42.boolean.opBoolean","COPY",EDGE,{"disambiguationData":[TD([makeQuery(id+"F31.opLoft","SWEPT_FACE",FACE,{"disambiguationData":[OSD([subQ52,subQ51,subQ53,sQuery(id+"F22.wireOp",EDGE,"E28.8.1"),subQ49,subQ48])]})])],"derivedFrom":subQ11})])]}),makeQuery(id+"F47.opFillet","BLEND_FACE",FACE,{"disambiguationData":[OSD([subQ0,subQ9]),TDD([makeQuery(id+"F42.boolean.opBoolean","COPY",EDGE,{"disambiguationData":[TD([makeQuery(id+"F32.opLoft","SWEPT_FACE",FACE,{"disambiguationData":[OSD([subQ47,subQ46,subQ44,sQuery(id+"F22.wireOp",EDGE,"E28.9.1"),subQ43,subQ42])]})])],"derivedFrom":subQ11})])]}),makeQuery(id+"F47.opFillet","BLEND_FACE",FACE,{"disambiguationData":[OSD([subQ0,subQ9]),TDD([makeQuery(id+"F42.boolean.opBoolean","COPY",EDGE,{"disambiguationData":[TD([makeQuery(id+"F33.opLoft","SWEPT_FACE",FACE,{"disambiguationData":[OSD([subQ41,subQ40,subQ38,sQuery(id+"F22.wireOp",EDGE,"E28.10.1"),subQ37,subQ36])]})])],"derivedFrom":subQ11})])]}),makeQuery(id+"F47.opFillet","BLEND_FACE",FACE,{"disambiguationData":[OSD([subQ0,subQ9]),TDD([makeQuery(id+"F42.boolean.opBoolean","COPY",EDGE,{"disambiguationData":[TD([makeQuery(id+"F34.opLoft","SWEPT_FACE",FACE,{"disambiguationData":[OSD([subQ35,subQ34,subQ32,sQuery(id+"F22.wireOp",EDGE,"E28.11.1"),subQ31,subQ30])]})])],"derivedFrom":subQ11})])]}),makeQuery(id+"F47.opFillet","BLEND_FACE",FACE,{"disambiguationData":[OSD([subQ0,subQ9]),TDD([makeQuery(id+"F42.boolean.opBoolean","COPY",EDGE,{"disambiguationData":[TD([makeQuery(id+"F35.opLoft","SWEPT_FACE",FACE,{"disambiguationData":[OSD([subQ29,subQ28,subQ26,sQuery(id+"F22.wireOp",EDGE,"E28.12.1"),subQ25,subQ24])]})])],"derivedFrom":subQ11})])]}),makeQuery(id+"F47.opFillet","BLEND_FACE",FACE,{"disambiguationData":[OSD([subQ0,subQ9]),TDD([makeQuery(id+"F42.boolean.opBoolean","COPY",EDGE,{"disambiguationData":[TD([makeQuery(id+"F36.opLoft","SWEPT_FACE",FACE,{"disambiguationData":[OSD([subQ23,subQ22,subQ20,sQuery(id+"F22.wireOp",EDGE,"E28.13.1"),subQ19,subQ18])]})])],"derivedFrom":subQ11})])]}),makeQuery(id+"F47.opFillet","BLEND_FACE",FACE,{"disambiguationData":[OSD([subQ0,subQ9]),TDD([makeQuery(id+"F42.boolean.opBoolean","COPY",EDGE,{"disambiguationData":[TD([makeQuery(id+"F37.opLoft","SWEPT_FACE",FACE,{"disambiguationData":[OSD([subQ16,subQ15,subQ14,sQuery(id+"F22.wireOp",EDGE,"E28.14.1"),subQ13,subQ12])]})])],"derivedFrom":subQ11})])]}),makeQuery(id+"F47.opFillet","BLEND_FACE",FACE,{"disambiguationData":[OSD([subQ0,subQ9]),TDD([makeQuery(id+"F42.boolean.opBoolean","COPY",EDGE,{"disambiguationData":[TD([makeQuery(id+"F38.opLoft","SWEPT_FACE",FACE,{"disambiguationData":[OSD([subQ8,subQ7,subQ5,sQuery(id+"F22.wireOp",EDGE,"E28.15.1"),subQ4,subQ3])]})])],"derivedFrom":subQ11})])]})],"blendedInto":[makeQuery(id+"F47.opFillet","BLEND_FACE",FACE,{"disambiguationData":[OSD([subQ0,subQ9]),TDD([makeQuery(id+"F42.boolean.opBoolean","COPY",EDGE,{"disambiguationData":[TD([makeQuery(id+"F23.opLoft","SWEPT_FACE",FACE,{"disambiguationData":[OSD([sQuery(id+"F3.wireOp",EDGE,"E20.8.0"),subQ105,subQ103,subQ102,subQ101,sQuery(id+"F22.wireOp",EDGE,"E27.right")])]})])],"derivedFrom":subQ11})])]}),makeQuery(id+"F47.opFillet","BLEND_FACE",FACE,{"disambiguationData":[OSD([subQ0,subQ9]),TDD([makeQuery(id+"F42.boolean.opBoolean","COPY",EDGE,{"disambiguationData":[TD([subQ100])],"derivedFrom":subQ11})])]}),makeQuery(id+"F47.opFillet","BLEND_FACE",FACE,{"disambiguationData":[OSD([subQ0,subQ9]),TDD([makeQuery(id+"F42.boolean.opBoolean","COPY",EDGE,{"disambiguationData":[TD([subQ93])],"derivedFrom":subQ11})])]}),makeQuery(id+"F47.opFillet","BLEND_FACE",FACE,{"disambiguationData":[OSD([subQ0,subQ9]),TDD([makeQuery(id+"F42.boolean.opBoolean","COPY",EDGE,{"disambiguationData":[TD([subQ87])],"derivedFrom":subQ11})])]}),makeQuery(id+"F47.opFillet","BLEND_FACE",FACE,{"disambiguationData":[OSD([subQ0,subQ9]),TDD([makeQuery(id+"F42.boolean.opBoolean","COPY",EDGE,{"disambiguationData":[TD([subQ80])],"derivedFrom":subQ11})])]}),makeQuery(id+"F47.opFillet","BLEND_FACE",FACE,{"disambiguationData":[OSD([subQ0,subQ9]),TDD([makeQuery(id+"F42.boolean.opBoolean","COPY",EDGE,{"disambiguationData":[TD([subQ73])],"derivedFrom":subQ11})])]}),makeQuery(id+"F47.opFillet","BLEND_FACE",FACE,{"disambiguationData":[OSD([subQ0,subQ9]),TDD([makeQuery(id+"F42.boolean.opBoolean","COPY",EDGE,{"disambiguationData":[TD([makeQuery(id+"F29.opLoft","SWEPT_FACE",FACE,{"disambiguationData":[OSD([subQ65,subQ64,subQ62,sQuery(id+"F22.wireOp",EDGE,"E28.6.1"),subQ61,subQ60])]})])],"derivedFrom":subQ11})])]}),makeQuery(id+"F47.opFillet","BLEND_FACE",FACE,{"disambiguationData":[OSD([subQ0,subQ9]),TDD([makeQuery(id+"F42.boolean.opBoolean","COPY",EDGE,{"disambiguationData":[TD([makeQuery(id+"F30.opLoft","SWEPT_FACE",FACE,{"disambiguationData":[OSD([subQ58,subQ57,subQ56,sQuery(id+"F22.wireOp",EDGE,"E28.7.1"),subQ55,subQ54])]})])],"derivedFrom":subQ11})])]}),makeQuery(id+"F47.opFillet","BLEND_FACE",FACE,{"disambiguationData":[OSD([subQ0,subQ9]),TDD([makeQuery(id+"F42.boolean.opBoolean","COPY",EDGE,{"disambiguationData":[TD([makeQuery(id+"F31.opLoft","SWEPT_FACE",FACE,{"disambiguationData":[OSD([subQ52,subQ51,subQ53,sQuery(id+"F22.wireOp",EDGE,"E28.8.1"),subQ49,subQ48])]})])],"derivedFrom":subQ11})])]}),makeQuery(id+"F47.opFillet","BLEND_FACE",FACE,{"disambiguationData":[OSD([subQ0,subQ9]),TDD([makeQuery(id+"F42.boolean.opBoolean","COPY",EDGE,{"disambiguationData":[TD([makeQuery(id+"F32.opLoft","SWEPT_FACE",FACE,{"disambiguationData":[OSD([subQ47,subQ46,subQ44,sQuery(id+"F22.wireOp",EDGE,"E28.9.1"),subQ43,subQ42])]})])],"derivedFrom":subQ11})])]}),makeQuery(id+"F47.opFillet","BLEND_FACE",FACE,{"disambiguationData":[OSD([subQ0,subQ9]),TDD([makeQuery(id+"F42.boolean.opBoolean","COPY",EDGE,{"disambiguationData":[TD([makeQuery(id+"F33.opLoft","SWEPT_FACE",FACE,{"disambiguationData":[OSD([subQ41,subQ40,subQ38,sQuery(id+"F22.wireOp",EDGE,"E28.10.1"),subQ37,subQ36])]})])],"derivedFrom":subQ11})])]}),makeQuery(id+"F47.opFillet","BLEND_FACE",FACE,{"disambiguationData":[OSD([subQ0,subQ9]),TDD([makeQuery(id+"F42.boolean.opBoolean","COPY",EDGE,{"disambiguationData":[TD([makeQuery(id+"F34.opLoft","SWEPT_FACE",FACE,{"disambiguationData":[OSD([subQ35,subQ34,subQ32,sQuery(id+"F22.wireOp",EDGE,"E28.11.1"),subQ31,subQ30])]})])],"derivedFrom":subQ11})])]}),makeQuery(id+"F47.opFillet","BLEND_FACE",FACE,{"disambiguationData":[OSD([subQ0,subQ9]),TDD([makeQuery(id+"F42.boolean.opBoolean","COPY",EDGE,{"disambiguationData":[TD([makeQuery(id+"F35.opLoft","SWEPT_FACE",FACE,{"disambiguationData":[OSD([subQ29,subQ28,subQ26,sQuery(id+"F22.wireOp",EDGE,"E28.12.1"),subQ25,subQ24])]})])],"derivedFrom":subQ11})])]}),makeQuery(id+"F47.opFillet","BLEND_FACE",FACE,{"disambiguationData":[OSD([subQ0,subQ9]),TDD([makeQuery(id+"F42.boolean.opBoolean","COPY",EDGE,{"disambiguationData":[TD([makeQuery(id+"F36.opLoft","SWEPT_FACE",FACE,{"disambiguationData":[OSD([subQ23,subQ22,subQ20,sQuery(id+"F22.wireOp",EDGE,"E28.13.1"),subQ19,subQ18])]})])],"derivedFrom":subQ11})])]}),makeQuery(id+"F47.opFillet","BLEND_FACE",FACE,{"disambiguationData":[OSD([subQ0,subQ9]),TDD([makeQuery(id+"F42.boolean.opBoolean","COPY",EDGE,{"disambiguationData":[TD([makeQuery(id+"F37.opLoft","SWEPT_FACE",FACE,{"disambiguationData":[OSD([subQ16,subQ15,subQ14,sQuery(id+"F22.wireOp",EDGE,"E28.14.1"),subQ13,subQ12])]})])],"derivedFrom":subQ11})])]}),makeQuery(id+"F47.opFillet","BLEND_FACE",FACE,{"disambiguationData":[OSD([subQ0,subQ9]),TDD([makeQuery(id+"F42.boolean.opBoolean","COPY",EDGE,{"disambiguationData":[TD([makeQuery(id+"F38.opLoft","SWEPT_FACE",FACE,{"disambiguationData":[OSD([subQ8,subQ7,subQ5,sQuery(id+"F22.wireOp",EDGE,"E28.15.1"),subQ4,subQ3])]})])],"derivedFrom":subQ11})])]})]});}
            var Q27;
            {var subQ0=sQuery(id+"F22.wireOp",EDGE,"E28.5.3");var subQ1=sQuery(id+"F22.wireOp",EDGE,"E28.5.2");var subQ2=sQuery(id+"F22.wireOp",EDGE,"E28.5.0");var subQ3=sQuery(id+"F3.wireOp",EDGE,"E20.13.3");var subQ4=sQuery(id+"F3.wireOp",EDGE,"E20.13.1");var subQ5=makeQuery(id+"F28.opLoft","SWEPT_FACE",FACE,{"disambiguationData":[OSD([subQ4,sQuery(id+"F3.wireOp",EDGE,"E20.13.2"),subQ3,subQ2,subQ1,subQ0])]});var subQ6=sQuery(id+"F22.wireOp",EDGE,"E28.5.1");var subQ7=sQuery(id+"F41.wireOp",EDGE,"E34");var subQ8=sQuery(id+"F41.wireOp",EDGE,"E32");Q27=makeQuery(id+"F44.opFillet","BLEND_EDGE",EDGE,{"blendedFrom":[makeQuery(id+"F40.boolean.opBoolean","INTERSECT",EDGE,{"derivedFrom":[subQ5,makeQuery(id+"F40.opExtrude","CAP_FACE",FACE,{"disambiguationData":[OSD([sQuery(id+"F39.wireOp",EDGE,"E29"),sQuery(id+"F39.wireOp",EDGE,"E30")])],"isStart":true})]}),makeQuery(id+"F42.boolean.opBoolean","COPY",FACE,{"disambiguationData":[TD([makeQuery(id+"F28.opLoft","SWEPT_FACE",FACE,{"disambiguationData":[OSD([sQuery(id+"F3.wireOp",EDGE,"E20.13.0"),subQ4,subQ3,subQ6,subQ1,subQ0])]})])],"derivedFrom":makeQuery(id+"F42.opRevolve","SWEPT_FACE",FACE,{"disambiguationData":[OSD([subQ8]),TDD([makeQuery(id+"F41.imprint","IMPRINT",EDGE,{"disambiguationData":[TD([[makeQuery(id+"F41.imprint","INTERSECT",VERTEX,{"disambiguationData":[OD(0.0)],"derivedFrom":[subQ8,subQ7]}),-1.0]])],"derivedFrom":subQ8})])]})})],"blendedInto":[makeQuery(id+"F42.boolean.opBoolean","COPY",FACE,{"disambiguationData":[TD([makeQuery(id+"F28.opLoft","SWEPT_FACE",FACE,{"disambiguationData":[OSD([sQuery(id+"F3.wireOp",EDGE,"E20.13.0"),subQ4,subQ3,subQ6,subQ1,subQ0])]})])],"derivedFrom":makeQuery(id+"F42.opRevolve","SWEPT_FACE",FACE,{"disambiguationData":[OSD([subQ8]),TDD([makeQuery(id+"F41.imprint","IMPRINT",EDGE,{"disambiguationData":[TD([[makeQuery(id+"F41.imprint","INTERSECT",VERTEX,{"disambiguationData":[OD(0.0)],"derivedFrom":[subQ8,subQ7]}),-1.0]])],"derivedFrom":subQ8})])]})})]});}
            var Q28;
            {var subQ0=sQuery(id+"F41.wireOp",EDGE,"E34");var subQ1=sQuery(id+"F41.wireOp",EDGE,"E32");Q28=makeQuery(id+"F42.boolean.opBoolean","INTERSECT",EDGE,{"derivedFrom":[makeQuery(id+"F27.opLoft","SWEPT_FACE",FACE,{"disambiguationData":[OSD([sQuery(id+"F3.wireOp",EDGE,"E20.12.0"),sQuery(id+"F3.wireOp",EDGE,"E20.12.1"),sQuery(id+"F3.wireOp",EDGE,"E20.12.3"),sQuery(id+"F22.wireOp",EDGE,"E28.4.1"),sQuery(id+"F22.wireOp",EDGE,"E28.4.2"),sQuery(id+"F22.wireOp",EDGE,"E28.4.3")])]}),makeQuery(id+"F42.opRevolve","SWEPT_FACE",FACE,{"disambiguationData":[OSD([subQ1]),TDD([makeQuery(id+"F41.imprint","IMPRINT",EDGE,{"disambiguationData":[TD([[makeQuery(id+"F41.imprint","INTERSECT",VERTEX,{"disambiguationData":[OD(0.0)],"derivedFrom":[subQ1,subQ0]}),-1.0]])],"derivedFrom":subQ1})])]})]});}
            var Q29;
            {var subQ0=sQuery(id+"F41.wireOp",EDGE,"E37");var subQ1=makeQuery(id+"F42.opRevolve","SWEPT_FACE",FACE,{"disambiguationData":[OSD([subQ0])]});var subQ2=makeQuery(id+"F40.opExtrude","CAP_FACE",FACE,{"disambiguationData":[OSD([sQuery(id+"F39.wireOp",EDGE,"E29"),sQuery(id+"F39.wireOp",EDGE,"E30")])],"isStart":true});var subQ3=sQuery(id+"F22.wireOp",EDGE,"E28.15.3");var subQ4=sQuery(id+"F22.wireOp",EDGE,"E28.15.2");var subQ5=sQuery(id+"F3.wireOp",EDGE,"E20.7.3");var subQ7=sQuery(id+"F3.wireOp",EDGE,"E20.7.1");var subQ8=sQuery(id+"F3.wireOp",EDGE,"E20.7.0");var subQ9=sQuery(id+"F41.wireOp",EDGE,"E38");var subQ10=makeQuery(id+"F42.opRevolve","SWEPT_FACE",FACE,{"disambiguationData":[OSD([subQ9])]});var subQ11=makeQuery(id+"F42.opRevolve","SWEPT_EDGE",EDGE,{"disambiguationData":[OSD([subQ0,subQ9])]});var subQ12=sQuery(id+"F22.wireOp",EDGE,"E28.14.3");var subQ13=sQuery(id+"F22.wireOp",EDGE,"E28.14.2");var subQ14=sQuery(id+"F3.wireOp",EDGE,"E20.6.3");var subQ15=sQuery(id+"F3.wireOp",EDGE,"E20.6.1");var subQ16=sQuery(id+"F3.wireOp",EDGE,"E20.6.0");var subQ18=sQuery(id+"F22.wireOp",EDGE,"E28.13.3");var subQ19=sQuery(id+"F22.wireOp",EDGE,"E28.13.2");var subQ20=sQuery(id+"F3.wireOp",EDGE,"E20.5.3");var subQ22=sQuery(id+"F3.wireOp",EDGE,"E20.5.1");var subQ23=sQuery(id+"F3.wireOp",EDGE,"E20.5.0");var subQ24=sQuery(id+"F22.wireOp",EDGE,"E28.12.3");var subQ25=sQuery(id+"F22.wireOp",EDGE,"E28.12.2");var subQ26=sQuery(id+"F3.wireOp",EDGE,"E20.4.3");var subQ28=sQuery(id+"F3.wireOp",EDGE,"E20.4.1");var subQ29=sQuery(id+"F3.wireOp",EDGE,"E20.4.0");var subQ30=sQuery(id+"F22.wireOp",EDGE,"E28.11.3");var subQ31=sQuery(id+"F22.wireOp",EDGE,"E28.11.2");var subQ32=sQuery(id+"F3.wireOp",EDGE,"E20.3.3");var subQ34=sQuery(id+"F3.wireOp",EDGE,"E20.3.1");var subQ35=sQuery(id+"F3.wireOp",EDGE,"E20.3.0");var subQ36=sQuery(id+"F22.wireOp",EDGE,"E28.10.3");var subQ37=sQuery(id+"F22.wireOp",EDGE,"E28.10.2");var subQ38=sQuery(id+"F3.wireOp",EDGE,"E20.2.3");var subQ40=sQuery(id+"F3.wireOp",EDGE,"E20.2.1");var subQ41=sQuery(id+"F3.wireOp",EDGE,"E20.2.0");var subQ42=sQuery(id+"F22.wireOp",EDGE,"E28.9.3");var subQ43=sQuery(id+"F22.wireOp",EDGE,"E28.9.2");var subQ44=sQuery(id+"F3.wireOp",EDGE,"E20.1.3");var subQ46=sQuery(id+"F3.wireOp",EDGE,"E20.1.1");var subQ47=sQuery(id+"F3.wireOp",EDGE,"E20.1.0");var subQ48=sQuery(id+"F22.wireOp",EDGE,"E28.8.3");var subQ49=sQuery(id+"F22.wireOp",EDGE,"E28.8.2");var subQ51=sQuery(id+"F3.wireOp",EDGE,"E18.top");var subQ52=sQuery(id+"F3.wireOp",EDGE,"E18.bottom");var subQ53=sQuery(id+"F3.wireOp",EDGE,"E18.left");var subQ54=sQuery(id+"F22.wireOp",EDGE,"E28.7.3");var subQ55=sQuery(id+"F22.wireOp",EDGE,"E28.7.2");var subQ56=sQuery(id+"F3.wireOp",EDGE,"E20.15.3");var subQ57=sQuery(id+"F3.wireOp",EDGE,"E20.15.1");var subQ58=sQuery(id+"F3.wireOp",EDGE,"E20.15.0");var subQ60=sQuery(id+"F22.wireOp",EDGE,"E28.6.3");var subQ61=sQuery(id+"F22.wireOp",EDGE,"E28.6.2");var subQ62=sQuery(id+"F3.wireOp",EDGE,"E20.14.3");var subQ64=sQuery(id+"F3.wireOp",EDGE,"E20.14.1");var subQ65=sQuery(id+"F3.wireOp",EDGE,"E20.14.0");var subQ66=sQuery(id+"F22.wireOp",EDGE,"E28.5.3");var subQ67=sQuery(id+"F22.wireOp",EDGE,"E28.5.2");var subQ68=sQuery(id+"F3.wireOp",EDGE,"E20.13.3");var subQ70=sQuery(id+"F3.wireOp",EDGE,"E20.13.1");var subQ71=sQuery(id+"F3.wireOp",EDGE,"E20.13.0");var subQ72=sQuery(id+"F22.wireOp",EDGE,"E28.4.3");var subQ73=sQuery(id+"F22.wireOp",EDGE,"E28.4.2");var subQ74=sQuery(id+"F3.wireOp",EDGE,"E20.12.3");var subQ76=sQuery(id+"F3.wireOp",EDGE,"E20.12.1");var subQ78=sQuery(id+"F3.wireOp",EDGE,"E20.12.0");var subQ79=makeQuery(id+"F27.opLoft","SWEPT_FACE",FACE,{"disambiguationData":[OSD([subQ78,subQ76,subQ74,sQuery(id+"F22.wireOp",EDGE,"E28.4.1"),subQ73,subQ72])]});var subQ80=sQuery(id+"F22.wireOp",EDGE,"E28.3.3");var subQ81=sQuery(id+"F22.wireOp",EDGE,"E28.3.2");var subQ82=sQuery(id+"F3.wireOp",EDGE,"E20.11.3");var subQ84=sQuery(id+"F3.wireOp",EDGE,"E20.11.1");var subQ85=sQuery(id+"F3.wireOp",EDGE,"E20.11.0");var subQ86=makeQuery(id+"F26.opLoft","SWEPT_FACE",FACE,{"disambiguationData":[OSD([subQ85,subQ84,subQ82,sQuery(id+"F22.wireOp",EDGE,"E28.3.1"),subQ81,subQ80])]});var subQ87=sQuery(id+"F22.wireOp",EDGE,"E28.2.3");var subQ88=sQuery(id+"F22.wireOp",EDGE,"E28.2.2");var subQ89=sQuery(id+"F3.wireOp",EDGE,"E20.10.3");var subQ90=sQuery(id+"F3.wireOp",EDGE,"E20.10.1");var subQ91=sQuery(id+"F3.wireOp",EDGE,"E20.10.0");var subQ92=makeQuery(id+"F25.opLoft","SWEPT_FACE",FACE,{"disambiguationData":[OSD([subQ91,subQ90,subQ89,sQuery(id+"F22.wireOp",EDGE,"E28.2.1"),subQ88,subQ87])]});var subQ94=sQuery(id+"F22.wireOp",EDGE,"E28.1.3");var subQ95=sQuery(id+"F22.wireOp",EDGE,"E28.1.2");var subQ96=sQuery(id+"F3.wireOp",EDGE,"E20.9.3");var subQ97=sQuery(id+"F3.wireOp",EDGE,"E20.9.1");var subQ98=sQuery(id+"F3.wireOp",EDGE,"E20.9.0");var subQ99=makeQuery(id+"F24.opLoft","SWEPT_FACE",FACE,{"disambiguationData":[OSD([subQ98,subQ97,subQ96,sQuery(id+"F22.wireOp",EDGE,"E28.1.1"),subQ95,subQ94])]});var subQ100=sQuery(id+"F22.wireOp",EDGE,"E27.top");var subQ101=sQuery(id+"F22.wireOp",EDGE,"E27.bottom");var subQ102=sQuery(id+"F3.wireOp",EDGE,"E20.8.3");var subQ104=sQuery(id+"F3.wireOp",EDGE,"E20.8.1");var subQ108=makeQuery(id+"F42.boolean.opBoolean","COPY",FACE,{"disambiguationData":[TD([subQ79])],"derivedFrom":subQ10});var subQ142=makeQuery(id+"F5.opLoft","CAP_FACE",FACE,{"disambiguationData":[OSD([makeQuery(id+"F3.imprint","IMPRINT",FACE,{"disambiguationData":[TD([[makeQuery(id+"F3.imprint","IMPRINT",EDGE,{"derivedFrom":subQ52}),1.0]])]})])],"isStart":true});var subQ180=makeQuery(id+"F27.boolean.opBoolean","INTERSECT",EDGE,{"derivedFrom":[makeQuery(id+"F26.boolean.opBoolean","SPLIT",FACE,{"disambiguationData":[TD([subQ142])],"derivedFrom":makeQuery(id+"F25.boolean.opBoolean","SPLIT",FACE,{"disambiguationData":[TD([subQ142])],"derivedFrom":makeQuery(id+"F24.boolean.opBoolean","SPLIT",FACE,{"disambiguationData":[TD([subQ142])],"derivedFrom":makeQuery(id+"F1.opRevolve","SWEPT_FACE",FACE,{"disambiguationData":[OSD([sQuery(id+"F0.wireOp",EDGE,"E4")])]})})})}),subQ79]});Q29=makeQuery(id+"F48.opFillet","BLEND_EDGE",EDGE,{"blendedFrom":[makeQuery(id+"F47.opFillet","TWEAK_EDGE",EDGE,{"derivedFrom":[makeQuery(id+"F45.opFillet","BLEND_VERTEX",VERTEX,{"blendedFrom":[subQ180,subQ79,subQ108],"blendedInto":[subQ79,subQ108]}),makeQuery(id+"F45.opFillet","BLEND_VERTEX",VERTEX,{"blendedFrom":[subQ180,makeQuery(id+"F42.boolean.opBoolean","MERGE",FACE,{"derivedFrom":[subQ2,subQ1]}),subQ108],"blendedInto":[makeQuery(id+"F42.boolean.opBoolean","MERGE",FACE,{"derivedFrom":[subQ2,subQ1]}),subQ108]})]}),makeQuery(id+"F47.opFillet","BLEND_FACE",FACE,{"disambiguationData":[OSD([subQ0,subQ9]),TDD([makeQuery(id+"F42.boolean.opBoolean","COPY",EDGE,{"disambiguationData":[TD([makeQuery(id+"F23.opLoft","SWEPT_FACE",FACE,{"disambiguationData":[OSD([sQuery(id+"F3.wireOp",EDGE,"E20.8.0"),subQ104,subQ102,subQ101,subQ100,sQuery(id+"F22.wireOp",EDGE,"E27.right")])]})])],"derivedFrom":subQ11})])]}),makeQuery(id+"F47.opFillet","BLEND_FACE",FACE,{"disambiguationData":[OSD([subQ0,subQ9]),TDD([makeQuery(id+"F42.boolean.opBoolean","COPY",EDGE,{"disambiguationData":[TD([subQ99])],"derivedFrom":subQ11})])]}),makeQuery(id+"F47.opFillet","BLEND_FACE",FACE,{"disambiguationData":[OSD([subQ0,subQ9]),TDD([makeQuery(id+"F42.boolean.opBoolean","COPY",EDGE,{"disambiguationData":[TD([subQ92])],"derivedFrom":subQ11})])]}),makeQuery(id+"F47.opFillet","BLEND_FACE",FACE,{"disambiguationData":[OSD([subQ0,subQ9]),TDD([makeQuery(id+"F42.boolean.opBoolean","COPY",EDGE,{"disambiguationData":[TD([subQ86])],"derivedFrom":subQ11})])]}),makeQuery(id+"F47.opFillet","BLEND_FACE",FACE,{"disambiguationData":[OSD([subQ0,subQ9]),TDD([makeQuery(id+"F42.boolean.opBoolean","COPY",EDGE,{"disambiguationData":[TD([subQ79])],"derivedFrom":subQ11})])]}),makeQuery(id+"F47.opFillet","BLEND_FACE",FACE,{"disambiguationData":[OSD([subQ0,subQ9]),TDD([makeQuery(id+"F42.boolean.opBoolean","COPY",EDGE,{"disambiguationData":[TD([makeQuery(id+"F28.opLoft","SWEPT_FACE",FACE,{"disambiguationData":[OSD([subQ71,subQ70,subQ68,sQuery(id+"F22.wireOp",EDGE,"E28.5.1"),subQ67,subQ66])]})])],"derivedFrom":subQ11})])]}),makeQuery(id+"F47.opFillet","BLEND_FACE",FACE,{"disambiguationData":[OSD([subQ0,subQ9]),TDD([makeQuery(id+"F42.boolean.opBoolean","COPY",EDGE,{"disambiguationData":[TD([makeQuery(id+"F29.opLoft","SWEPT_FACE",FACE,{"disambiguationData":[OSD([subQ65,subQ64,subQ62,sQuery(id+"F22.wireOp",EDGE,"E28.6.1"),subQ61,subQ60])]})])],"derivedFrom":subQ11})])]}),makeQuery(id+"F47.opFillet","BLEND_FACE",FACE,{"disambiguationData":[OSD([subQ0,subQ9]),TDD([makeQuery(id+"F42.boolean.opBoolean","COPY",EDGE,{"disambiguationData":[TD([makeQuery(id+"F30.opLoft","SWEPT_FACE",FACE,{"disambiguationData":[OSD([subQ58,subQ57,subQ56,sQuery(id+"F22.wireOp",EDGE,"E28.7.1"),subQ55,subQ54])]})])],"derivedFrom":subQ11})])]}),makeQuery(id+"F47.opFillet","BLEND_FACE",FACE,{"disambiguationData":[OSD([subQ0,subQ9]),TDD([makeQuery(id+"F42.boolean.opBoolean","COPY",EDGE,{"disambiguationData":[TD([makeQuery(id+"F31.opLoft","SWEPT_FACE",FACE,{"disambiguationData":[OSD([subQ52,subQ51,subQ53,sQuery(id+"F22.wireOp",EDGE,"E28.8.1"),subQ49,subQ48])]})])],"derivedFrom":subQ11})])]}),makeQuery(id+"F47.opFillet","BLEND_FACE",FACE,{"disambiguationData":[OSD([subQ0,subQ9]),TDD([makeQuery(id+"F42.boolean.opBoolean","COPY",EDGE,{"disambiguationData":[TD([makeQuery(id+"F32.opLoft","SWEPT_FACE",FACE,{"disambiguationData":[OSD([subQ47,subQ46,subQ44,sQuery(id+"F22.wireOp",EDGE,"E28.9.1"),subQ43,subQ42])]})])],"derivedFrom":subQ11})])]}),makeQuery(id+"F47.opFillet","BLEND_FACE",FACE,{"disambiguationData":[OSD([subQ0,subQ9]),TDD([makeQuery(id+"F42.boolean.opBoolean","COPY",EDGE,{"disambiguationData":[TD([makeQuery(id+"F33.opLoft","SWEPT_FACE",FACE,{"disambiguationData":[OSD([subQ41,subQ40,subQ38,sQuery(id+"F22.wireOp",EDGE,"E28.10.1"),subQ37,subQ36])]})])],"derivedFrom":subQ11})])]}),makeQuery(id+"F47.opFillet","BLEND_FACE",FACE,{"disambiguationData":[OSD([subQ0,subQ9]),TDD([makeQuery(id+"F42.boolean.opBoolean","COPY",EDGE,{"disambiguationData":[TD([makeQuery(id+"F34.opLoft","SWEPT_FACE",FACE,{"disambiguationData":[OSD([subQ35,subQ34,subQ32,sQuery(id+"F22.wireOp",EDGE,"E28.11.1"),subQ31,subQ30])]})])],"derivedFrom":subQ11})])]}),makeQuery(id+"F47.opFillet","BLEND_FACE",FACE,{"disambiguationData":[OSD([subQ0,subQ9]),TDD([makeQuery(id+"F42.boolean.opBoolean","COPY",EDGE,{"disambiguationData":[TD([makeQuery(id+"F35.opLoft","SWEPT_FACE",FACE,{"disambiguationData":[OSD([subQ29,subQ28,subQ26,sQuery(id+"F22.wireOp",EDGE,"E28.12.1"),subQ25,subQ24])]})])],"derivedFrom":subQ11})])]}),makeQuery(id+"F47.opFillet","BLEND_FACE",FACE,{"disambiguationData":[OSD([subQ0,subQ9]),TDD([makeQuery(id+"F42.boolean.opBoolean","COPY",EDGE,{"disambiguationData":[TD([makeQuery(id+"F36.opLoft","SWEPT_FACE",FACE,{"disambiguationData":[OSD([subQ23,subQ22,subQ20,sQuery(id+"F22.wireOp",EDGE,"E28.13.1"),subQ19,subQ18])]})])],"derivedFrom":subQ11})])]}),makeQuery(id+"F47.opFillet","BLEND_FACE",FACE,{"disambiguationData":[OSD([subQ0,subQ9]),TDD([makeQuery(id+"F42.boolean.opBoolean","COPY",EDGE,{"disambiguationData":[TD([makeQuery(id+"F37.opLoft","SWEPT_FACE",FACE,{"disambiguationData":[OSD([subQ16,subQ15,subQ14,sQuery(id+"F22.wireOp",EDGE,"E28.14.1"),subQ13,subQ12])]})])],"derivedFrom":subQ11})])]}),makeQuery(id+"F47.opFillet","BLEND_FACE",FACE,{"disambiguationData":[OSD([subQ0,subQ9]),TDD([makeQuery(id+"F42.boolean.opBoolean","COPY",EDGE,{"disambiguationData":[TD([makeQuery(id+"F38.opLoft","SWEPT_FACE",FACE,{"disambiguationData":[OSD([subQ8,subQ7,subQ5,sQuery(id+"F22.wireOp",EDGE,"E28.15.1"),subQ4,subQ3])]})])],"derivedFrom":subQ11})])]})],"blendedInto":[makeQuery(id+"F47.opFillet","BLEND_FACE",FACE,{"disambiguationData":[OSD([subQ0,subQ9]),TDD([makeQuery(id+"F42.boolean.opBoolean","COPY",EDGE,{"disambiguationData":[TD([makeQuery(id+"F23.opLoft","SWEPT_FACE",FACE,{"disambiguationData":[OSD([sQuery(id+"F3.wireOp",EDGE,"E20.8.0"),subQ104,subQ102,subQ101,subQ100,sQuery(id+"F22.wireOp",EDGE,"E27.right")])]})])],"derivedFrom":subQ11})])]}),makeQuery(id+"F47.opFillet","BLEND_FACE",FACE,{"disambiguationData":[OSD([subQ0,subQ9]),TDD([makeQuery(id+"F42.boolean.opBoolean","COPY",EDGE,{"disambiguationData":[TD([subQ99])],"derivedFrom":subQ11})])]}),makeQuery(id+"F47.opFillet","BLEND_FACE",FACE,{"disambiguationData":[OSD([subQ0,subQ9]),TDD([makeQuery(id+"F42.boolean.opBoolean","COPY",EDGE,{"disambiguationData":[TD([subQ92])],"derivedFrom":subQ11})])]}),makeQuery(id+"F47.opFillet","BLEND_FACE",FACE,{"disambiguationData":[OSD([subQ0,subQ9]),TDD([makeQuery(id+"F42.boolean.opBoolean","COPY",EDGE,{"disambiguationData":[TD([subQ86])],"derivedFrom":subQ11})])]}),makeQuery(id+"F47.opFillet","BLEND_FACE",FACE,{"disambiguationData":[OSD([subQ0,subQ9]),TDD([makeQuery(id+"F42.boolean.opBoolean","COPY",EDGE,{"disambiguationData":[TD([subQ79])],"derivedFrom":subQ11})])]}),makeQuery(id+"F47.opFillet","BLEND_FACE",FACE,{"disambiguationData":[OSD([subQ0,subQ9]),TDD([makeQuery(id+"F42.boolean.opBoolean","COPY",EDGE,{"disambiguationData":[TD([makeQuery(id+"F28.opLoft","SWEPT_FACE",FACE,{"disambiguationData":[OSD([subQ71,subQ70,subQ68,sQuery(id+"F22.wireOp",EDGE,"E28.5.1"),subQ67,subQ66])]})])],"derivedFrom":subQ11})])]}),makeQuery(id+"F47.opFillet","BLEND_FACE",FACE,{"disambiguationData":[OSD([subQ0,subQ9]),TDD([makeQuery(id+"F42.boolean.opBoolean","COPY",EDGE,{"disambiguationData":[TD([makeQuery(id+"F29.opLoft","SWEPT_FACE",FACE,{"disambiguationData":[OSD([subQ65,subQ64,subQ62,sQuery(id+"F22.wireOp",EDGE,"E28.6.1"),subQ61,subQ60])]})])],"derivedFrom":subQ11})])]}),makeQuery(id+"F47.opFillet","BLEND_FACE",FACE,{"disambiguationData":[OSD([subQ0,subQ9]),TDD([makeQuery(id+"F42.boolean.opBoolean","COPY",EDGE,{"disambiguationData":[TD([makeQuery(id+"F30.opLoft","SWEPT_FACE",FACE,{"disambiguationData":[OSD([subQ58,subQ57,subQ56,sQuery(id+"F22.wireOp",EDGE,"E28.7.1"),subQ55,subQ54])]})])],"derivedFrom":subQ11})])]}),makeQuery(id+"F47.opFillet","BLEND_FACE",FACE,{"disambiguationData":[OSD([subQ0,subQ9]),TDD([makeQuery(id+"F42.boolean.opBoolean","COPY",EDGE,{"disambiguationData":[TD([makeQuery(id+"F31.opLoft","SWEPT_FACE",FACE,{"disambiguationData":[OSD([subQ52,subQ51,subQ53,sQuery(id+"F22.wireOp",EDGE,"E28.8.1"),subQ49,subQ48])]})])],"derivedFrom":subQ11})])]}),makeQuery(id+"F47.opFillet","BLEND_FACE",FACE,{"disambiguationData":[OSD([subQ0,subQ9]),TDD([makeQuery(id+"F42.boolean.opBoolean","COPY",EDGE,{"disambiguationData":[TD([makeQuery(id+"F32.opLoft","SWEPT_FACE",FACE,{"disambiguationData":[OSD([subQ47,subQ46,subQ44,sQuery(id+"F22.wireOp",EDGE,"E28.9.1"),subQ43,subQ42])]})])],"derivedFrom":subQ11})])]}),makeQuery(id+"F47.opFillet","BLEND_FACE",FACE,{"disambiguationData":[OSD([subQ0,subQ9]),TDD([makeQuery(id+"F42.boolean.opBoolean","COPY",EDGE,{"disambiguationData":[TD([makeQuery(id+"F33.opLoft","SWEPT_FACE",FACE,{"disambiguationData":[OSD([subQ41,subQ40,subQ38,sQuery(id+"F22.wireOp",EDGE,"E28.10.1"),subQ37,subQ36])]})])],"derivedFrom":subQ11})])]}),makeQuery(id+"F47.opFillet","BLEND_FACE",FACE,{"disambiguationData":[OSD([subQ0,subQ9]),TDD([makeQuery(id+"F42.boolean.opBoolean","COPY",EDGE,{"disambiguationData":[TD([makeQuery(id+"F34.opLoft","SWEPT_FACE",FACE,{"disambiguationData":[OSD([subQ35,subQ34,subQ32,sQuery(id+"F22.wireOp",EDGE,"E28.11.1"),subQ31,subQ30])]})])],"derivedFrom":subQ11})])]}),makeQuery(id+"F47.opFillet","BLEND_FACE",FACE,{"disambiguationData":[OSD([subQ0,subQ9]),TDD([makeQuery(id+"F42.boolean.opBoolean","COPY",EDGE,{"disambiguationData":[TD([makeQuery(id+"F35.opLoft","SWEPT_FACE",FACE,{"disambiguationData":[OSD([subQ29,subQ28,subQ26,sQuery(id+"F22.wireOp",EDGE,"E28.12.1"),subQ25,subQ24])]})])],"derivedFrom":subQ11})])]}),makeQuery(id+"F47.opFillet","BLEND_FACE",FACE,{"disambiguationData":[OSD([subQ0,subQ9]),TDD([makeQuery(id+"F42.boolean.opBoolean","COPY",EDGE,{"disambiguationData":[TD([makeQuery(id+"F36.opLoft","SWEPT_FACE",FACE,{"disambiguationData":[OSD([subQ23,subQ22,subQ20,sQuery(id+"F22.wireOp",EDGE,"E28.13.1"),subQ19,subQ18])]})])],"derivedFrom":subQ11})])]}),makeQuery(id+"F47.opFillet","BLEND_FACE",FACE,{"disambiguationData":[OSD([subQ0,subQ9]),TDD([makeQuery(id+"F42.boolean.opBoolean","COPY",EDGE,{"disambiguationData":[TD([makeQuery(id+"F37.opLoft","SWEPT_FACE",FACE,{"disambiguationData":[OSD([subQ16,subQ15,subQ14,sQuery(id+"F22.wireOp",EDGE,"E28.14.1"),subQ13,subQ12])]})])],"derivedFrom":subQ11})])]}),makeQuery(id+"F47.opFillet","BLEND_FACE",FACE,{"disambiguationData":[OSD([subQ0,subQ9]),TDD([makeQuery(id+"F42.boolean.opBoolean","COPY",EDGE,{"disambiguationData":[TD([makeQuery(id+"F38.opLoft","SWEPT_FACE",FACE,{"disambiguationData":[OSD([subQ8,subQ7,subQ5,sQuery(id+"F22.wireOp",EDGE,"E28.15.1"),subQ4,subQ3])]})])],"derivedFrom":subQ11})])]})]});}
            var Q30;
            {var subQ0=sQuery(id+"F22.wireOp",EDGE,"E28.4.3");var subQ1=sQuery(id+"F22.wireOp",EDGE,"E28.4.2");var subQ2=sQuery(id+"F22.wireOp",EDGE,"E28.4.0");var subQ3=sQuery(id+"F3.wireOp",EDGE,"E20.12.3");var subQ4=sQuery(id+"F3.wireOp",EDGE,"E20.12.1");var subQ5=makeQuery(id+"F27.opLoft","SWEPT_FACE",FACE,{"disambiguationData":[OSD([subQ4,sQuery(id+"F3.wireOp",EDGE,"E20.12.2"),subQ3,subQ2,subQ1,subQ0])]});var subQ6=sQuery(id+"F22.wireOp",EDGE,"E28.4.1");var subQ7=sQuery(id+"F41.wireOp",EDGE,"E34");var subQ8=sQuery(id+"F41.wireOp",EDGE,"E32");Q30=makeQuery(id+"F44.opFillet","BLEND_EDGE",EDGE,{"blendedFrom":[makeQuery(id+"F40.boolean.opBoolean","INTERSECT",EDGE,{"derivedFrom":[subQ5,makeQuery(id+"F40.opExtrude","CAP_FACE",FACE,{"disambiguationData":[OSD([sQuery(id+"F39.wireOp",EDGE,"E29"),sQuery(id+"F39.wireOp",EDGE,"E30")])],"isStart":true})]}),makeQuery(id+"F42.boolean.opBoolean","COPY",FACE,{"disambiguationData":[TD([makeQuery(id+"F27.opLoft","SWEPT_FACE",FACE,{"disambiguationData":[OSD([sQuery(id+"F3.wireOp",EDGE,"E20.12.0"),subQ4,subQ3,subQ6,subQ1,subQ0])]})])],"derivedFrom":makeQuery(id+"F42.opRevolve","SWEPT_FACE",FACE,{"disambiguationData":[OSD([subQ8]),TDD([makeQuery(id+"F41.imprint","IMPRINT",EDGE,{"disambiguationData":[TD([[makeQuery(id+"F41.imprint","INTERSECT",VERTEX,{"disambiguationData":[OD(0.0)],"derivedFrom":[subQ8,subQ7]}),-1.0]])],"derivedFrom":subQ8})])]})})],"blendedInto":[makeQuery(id+"F42.boolean.opBoolean","COPY",FACE,{"disambiguationData":[TD([makeQuery(id+"F27.opLoft","SWEPT_FACE",FACE,{"disambiguationData":[OSD([sQuery(id+"F3.wireOp",EDGE,"E20.12.0"),subQ4,subQ3,subQ6,subQ1,subQ0])]})])],"derivedFrom":makeQuery(id+"F42.opRevolve","SWEPT_FACE",FACE,{"disambiguationData":[OSD([subQ8]),TDD([makeQuery(id+"F41.imprint","IMPRINT",EDGE,{"disambiguationData":[TD([[makeQuery(id+"F41.imprint","INTERSECT",VERTEX,{"disambiguationData":[OD(0.0)],"derivedFrom":[subQ8,subQ7]}),-1.0]])],"derivedFrom":subQ8})])]})})]});}
            var Q31;
            {var subQ0=sQuery(id+"F41.wireOp",EDGE,"E34");var subQ1=sQuery(id+"F41.wireOp",EDGE,"E32");Q31=makeQuery(id+"F42.boolean.opBoolean","INTERSECT",EDGE,{"derivedFrom":[makeQuery(id+"F26.opLoft","SWEPT_FACE",FACE,{"disambiguationData":[OSD([sQuery(id+"F3.wireOp",EDGE,"E20.11.0"),sQuery(id+"F3.wireOp",EDGE,"E20.11.1"),sQuery(id+"F3.wireOp",EDGE,"E20.11.3"),sQuery(id+"F22.wireOp",EDGE,"E28.3.1"),sQuery(id+"F22.wireOp",EDGE,"E28.3.2"),sQuery(id+"F22.wireOp",EDGE,"E28.3.3")])]}),makeQuery(id+"F42.opRevolve","SWEPT_FACE",FACE,{"disambiguationData":[OSD([subQ1]),TDD([makeQuery(id+"F41.imprint","IMPRINT",EDGE,{"disambiguationData":[TD([[makeQuery(id+"F41.imprint","INTERSECT",VERTEX,{"disambiguationData":[OD(0.0)],"derivedFrom":[subQ1,subQ0]}),-1.0]])],"derivedFrom":subQ1})])]})]});}
            var Q32;
            {var subQ0=sQuery(id+"F41.wireOp",EDGE,"E37");var subQ1=makeQuery(id+"F42.opRevolve","SWEPT_FACE",FACE,{"disambiguationData":[OSD([subQ0])]});var subQ2=makeQuery(id+"F40.opExtrude","CAP_FACE",FACE,{"disambiguationData":[OSD([sQuery(id+"F39.wireOp",EDGE,"E29"),sQuery(id+"F39.wireOp",EDGE,"E30")])],"isStart":true});var subQ3=sQuery(id+"F22.wireOp",EDGE,"E28.15.3");var subQ4=sQuery(id+"F22.wireOp",EDGE,"E28.15.2");var subQ5=sQuery(id+"F3.wireOp",EDGE,"E20.7.3");var subQ7=sQuery(id+"F3.wireOp",EDGE,"E20.7.1");var subQ8=sQuery(id+"F3.wireOp",EDGE,"E20.7.0");var subQ9=sQuery(id+"F41.wireOp",EDGE,"E38");var subQ10=makeQuery(id+"F42.opRevolve","SWEPT_FACE",FACE,{"disambiguationData":[OSD([subQ9])]});var subQ11=makeQuery(id+"F42.opRevolve","SWEPT_EDGE",EDGE,{"disambiguationData":[OSD([subQ0,subQ9])]});var subQ12=sQuery(id+"F22.wireOp",EDGE,"E28.14.3");var subQ13=sQuery(id+"F22.wireOp",EDGE,"E28.14.2");var subQ14=sQuery(id+"F3.wireOp",EDGE,"E20.6.3");var subQ15=sQuery(id+"F3.wireOp",EDGE,"E20.6.1");var subQ16=sQuery(id+"F3.wireOp",EDGE,"E20.6.0");var subQ18=sQuery(id+"F22.wireOp",EDGE,"E28.13.3");var subQ19=sQuery(id+"F22.wireOp",EDGE,"E28.13.2");var subQ20=sQuery(id+"F3.wireOp",EDGE,"E20.5.3");var subQ22=sQuery(id+"F3.wireOp",EDGE,"E20.5.1");var subQ23=sQuery(id+"F3.wireOp",EDGE,"E20.5.0");var subQ24=sQuery(id+"F22.wireOp",EDGE,"E28.12.3");var subQ25=sQuery(id+"F22.wireOp",EDGE,"E28.12.2");var subQ26=sQuery(id+"F3.wireOp",EDGE,"E20.4.3");var subQ28=sQuery(id+"F3.wireOp",EDGE,"E20.4.1");var subQ29=sQuery(id+"F3.wireOp",EDGE,"E20.4.0");var subQ30=sQuery(id+"F22.wireOp",EDGE,"E28.11.3");var subQ31=sQuery(id+"F22.wireOp",EDGE,"E28.11.2");var subQ32=sQuery(id+"F3.wireOp",EDGE,"E20.3.3");var subQ34=sQuery(id+"F3.wireOp",EDGE,"E20.3.1");var subQ35=sQuery(id+"F3.wireOp",EDGE,"E20.3.0");var subQ36=sQuery(id+"F22.wireOp",EDGE,"E28.10.3");var subQ37=sQuery(id+"F22.wireOp",EDGE,"E28.10.2");var subQ38=sQuery(id+"F3.wireOp",EDGE,"E20.2.3");var subQ40=sQuery(id+"F3.wireOp",EDGE,"E20.2.1");var subQ41=sQuery(id+"F3.wireOp",EDGE,"E20.2.0");var subQ42=sQuery(id+"F22.wireOp",EDGE,"E28.9.3");var subQ43=sQuery(id+"F22.wireOp",EDGE,"E28.9.2");var subQ44=sQuery(id+"F3.wireOp",EDGE,"E20.1.3");var subQ46=sQuery(id+"F3.wireOp",EDGE,"E20.1.1");var subQ47=sQuery(id+"F3.wireOp",EDGE,"E20.1.0");var subQ48=sQuery(id+"F22.wireOp",EDGE,"E28.8.3");var subQ49=sQuery(id+"F22.wireOp",EDGE,"E28.8.2");var subQ51=sQuery(id+"F3.wireOp",EDGE,"E18.top");var subQ52=sQuery(id+"F3.wireOp",EDGE,"E18.bottom");var subQ53=sQuery(id+"F3.wireOp",EDGE,"E18.left");var subQ54=sQuery(id+"F22.wireOp",EDGE,"E28.7.3");var subQ55=sQuery(id+"F22.wireOp",EDGE,"E28.7.2");var subQ56=sQuery(id+"F3.wireOp",EDGE,"E20.15.3");var subQ57=sQuery(id+"F3.wireOp",EDGE,"E20.15.1");var subQ58=sQuery(id+"F3.wireOp",EDGE,"E20.15.0");var subQ60=sQuery(id+"F22.wireOp",EDGE,"E28.6.3");var subQ61=sQuery(id+"F22.wireOp",EDGE,"E28.6.2");var subQ62=sQuery(id+"F3.wireOp",EDGE,"E20.14.3");var subQ64=sQuery(id+"F3.wireOp",EDGE,"E20.14.1");var subQ65=sQuery(id+"F3.wireOp",EDGE,"E20.14.0");var subQ66=sQuery(id+"F22.wireOp",EDGE,"E28.5.3");var subQ67=sQuery(id+"F22.wireOp",EDGE,"E28.5.2");var subQ68=sQuery(id+"F3.wireOp",EDGE,"E20.13.3");var subQ70=sQuery(id+"F3.wireOp",EDGE,"E20.13.1");var subQ71=sQuery(id+"F3.wireOp",EDGE,"E20.13.0");var subQ72=sQuery(id+"F22.wireOp",EDGE,"E28.4.3");var subQ73=sQuery(id+"F22.wireOp",EDGE,"E28.4.2");var subQ74=sQuery(id+"F3.wireOp",EDGE,"E20.12.3");var subQ76=sQuery(id+"F3.wireOp",EDGE,"E20.12.1");var subQ77=sQuery(id+"F3.wireOp",EDGE,"E20.12.0");var subQ78=sQuery(id+"F22.wireOp",EDGE,"E28.3.3");var subQ79=sQuery(id+"F22.wireOp",EDGE,"E28.3.2");var subQ80=sQuery(id+"F3.wireOp",EDGE,"E20.11.3");var subQ82=sQuery(id+"F3.wireOp",EDGE,"E20.11.1");var subQ84=sQuery(id+"F3.wireOp",EDGE,"E20.11.0");var subQ85=makeQuery(id+"F26.opLoft","SWEPT_FACE",FACE,{"disambiguationData":[OSD([subQ84,subQ82,subQ80,sQuery(id+"F22.wireOp",EDGE,"E28.3.1"),subQ79,subQ78])]});var subQ86=sQuery(id+"F22.wireOp",EDGE,"E28.2.3");var subQ87=sQuery(id+"F22.wireOp",EDGE,"E28.2.2");var subQ88=sQuery(id+"F3.wireOp",EDGE,"E20.10.3");var subQ89=sQuery(id+"F3.wireOp",EDGE,"E20.10.1");var subQ90=sQuery(id+"F3.wireOp",EDGE,"E20.10.0");var subQ91=makeQuery(id+"F25.opLoft","SWEPT_FACE",FACE,{"disambiguationData":[OSD([subQ90,subQ89,subQ88,sQuery(id+"F22.wireOp",EDGE,"E28.2.1"),subQ87,subQ86])]});var subQ93=sQuery(id+"F22.wireOp",EDGE,"E28.1.3");var subQ94=sQuery(id+"F22.wireOp",EDGE,"E28.1.2");var subQ95=sQuery(id+"F3.wireOp",EDGE,"E20.9.3");var subQ96=sQuery(id+"F3.wireOp",EDGE,"E20.9.1");var subQ97=sQuery(id+"F3.wireOp",EDGE,"E20.9.0");var subQ98=makeQuery(id+"F24.opLoft","SWEPT_FACE",FACE,{"disambiguationData":[OSD([subQ97,subQ96,subQ95,sQuery(id+"F22.wireOp",EDGE,"E28.1.1"),subQ94,subQ93])]});var subQ99=sQuery(id+"F22.wireOp",EDGE,"E27.top");var subQ100=sQuery(id+"F22.wireOp",EDGE,"E27.bottom");var subQ101=sQuery(id+"F3.wireOp",EDGE,"E20.8.3");var subQ103=sQuery(id+"F3.wireOp",EDGE,"E20.8.1");var subQ107=makeQuery(id+"F42.boolean.opBoolean","COPY",FACE,{"disambiguationData":[TD([subQ85])],"derivedFrom":subQ10});var subQ141=makeQuery(id+"F5.opLoft","CAP_FACE",FACE,{"disambiguationData":[OSD([makeQuery(id+"F3.imprint","IMPRINT",FACE,{"disambiguationData":[TD([[makeQuery(id+"F3.imprint","IMPRINT",EDGE,{"derivedFrom":subQ52}),1.0]])]})])],"isStart":true});var subQ179=makeQuery(id+"F26.boolean.opBoolean","INTERSECT",EDGE,{"derivedFrom":[makeQuery(id+"F25.boolean.opBoolean","SPLIT",FACE,{"disambiguationData":[TD([subQ141])],"derivedFrom":makeQuery(id+"F24.boolean.opBoolean","SPLIT",FACE,{"disambiguationData":[TD([subQ141])],"derivedFrom":makeQuery(id+"F1.opRevolve","SWEPT_FACE",FACE,{"disambiguationData":[OSD([sQuery(id+"F0.wireOp",EDGE,"E4")])]})})}),subQ85]});Q32=makeQuery(id+"F48.opFillet","BLEND_EDGE",EDGE,{"blendedFrom":[makeQuery(id+"F47.opFillet","TWEAK_EDGE",EDGE,{"derivedFrom":[makeQuery(id+"F45.opFillet","BLEND_VERTEX",VERTEX,{"blendedFrom":[subQ179,subQ85,subQ107],"blendedInto":[subQ85,subQ107]}),makeQuery(id+"F45.opFillet","BLEND_VERTEX",VERTEX,{"blendedFrom":[subQ179,makeQuery(id+"F42.boolean.opBoolean","MERGE",FACE,{"derivedFrom":[subQ2,subQ1]}),subQ107],"blendedInto":[makeQuery(id+"F42.boolean.opBoolean","MERGE",FACE,{"derivedFrom":[subQ2,subQ1]}),subQ107]})]}),makeQuery(id+"F47.opFillet","BLEND_FACE",FACE,{"disambiguationData":[OSD([subQ0,subQ9]),TDD([makeQuery(id+"F42.boolean.opBoolean","COPY",EDGE,{"disambiguationData":[TD([makeQuery(id+"F23.opLoft","SWEPT_FACE",FACE,{"disambiguationData":[OSD([sQuery(id+"F3.wireOp",EDGE,"E20.8.0"),subQ103,subQ101,subQ100,subQ99,sQuery(id+"F22.wireOp",EDGE,"E27.right")])]})])],"derivedFrom":subQ11})])]}),makeQuery(id+"F47.opFillet","BLEND_FACE",FACE,{"disambiguationData":[OSD([subQ0,subQ9]),TDD([makeQuery(id+"F42.boolean.opBoolean","COPY",EDGE,{"disambiguationData":[TD([subQ98])],"derivedFrom":subQ11})])]}),makeQuery(id+"F47.opFillet","BLEND_FACE",FACE,{"disambiguationData":[OSD([subQ0,subQ9]),TDD([makeQuery(id+"F42.boolean.opBoolean","COPY",EDGE,{"disambiguationData":[TD([subQ91])],"derivedFrom":subQ11})])]}),makeQuery(id+"F47.opFillet","BLEND_FACE",FACE,{"disambiguationData":[OSD([subQ0,subQ9]),TDD([makeQuery(id+"F42.boolean.opBoolean","COPY",EDGE,{"disambiguationData":[TD([subQ85])],"derivedFrom":subQ11})])]}),makeQuery(id+"F47.opFillet","BLEND_FACE",FACE,{"disambiguationData":[OSD([subQ0,subQ9]),TDD([makeQuery(id+"F42.boolean.opBoolean","COPY",EDGE,{"disambiguationData":[TD([makeQuery(id+"F27.opLoft","SWEPT_FACE",FACE,{"disambiguationData":[OSD([subQ77,subQ76,subQ74,sQuery(id+"F22.wireOp",EDGE,"E28.4.1"),subQ73,subQ72])]})])],"derivedFrom":subQ11})])]}),makeQuery(id+"F47.opFillet","BLEND_FACE",FACE,{"disambiguationData":[OSD([subQ0,subQ9]),TDD([makeQuery(id+"F42.boolean.opBoolean","COPY",EDGE,{"disambiguationData":[TD([makeQuery(id+"F28.opLoft","SWEPT_FACE",FACE,{"disambiguationData":[OSD([subQ71,subQ70,subQ68,sQuery(id+"F22.wireOp",EDGE,"E28.5.1"),subQ67,subQ66])]})])],"derivedFrom":subQ11})])]}),makeQuery(id+"F47.opFillet","BLEND_FACE",FACE,{"disambiguationData":[OSD([subQ0,subQ9]),TDD([makeQuery(id+"F42.boolean.opBoolean","COPY",EDGE,{"disambiguationData":[TD([makeQuery(id+"F29.opLoft","SWEPT_FACE",FACE,{"disambiguationData":[OSD([subQ65,subQ64,subQ62,sQuery(id+"F22.wireOp",EDGE,"E28.6.1"),subQ61,subQ60])]})])],"derivedFrom":subQ11})])]}),makeQuery(id+"F47.opFillet","BLEND_FACE",FACE,{"disambiguationData":[OSD([subQ0,subQ9]),TDD([makeQuery(id+"F42.boolean.opBoolean","COPY",EDGE,{"disambiguationData":[TD([makeQuery(id+"F30.opLoft","SWEPT_FACE",FACE,{"disambiguationData":[OSD([subQ58,subQ57,subQ56,sQuery(id+"F22.wireOp",EDGE,"E28.7.1"),subQ55,subQ54])]})])],"derivedFrom":subQ11})])]}),makeQuery(id+"F47.opFillet","BLEND_FACE",FACE,{"disambiguationData":[OSD([subQ0,subQ9]),TDD([makeQuery(id+"F42.boolean.opBoolean","COPY",EDGE,{"disambiguationData":[TD([makeQuery(id+"F31.opLoft","SWEPT_FACE",FACE,{"disambiguationData":[OSD([subQ52,subQ51,subQ53,sQuery(id+"F22.wireOp",EDGE,"E28.8.1"),subQ49,subQ48])]})])],"derivedFrom":subQ11})])]}),makeQuery(id+"F47.opFillet","BLEND_FACE",FACE,{"disambiguationData":[OSD([subQ0,subQ9]),TDD([makeQuery(id+"F42.boolean.opBoolean","COPY",EDGE,{"disambiguationData":[TD([makeQuery(id+"F32.opLoft","SWEPT_FACE",FACE,{"disambiguationData":[OSD([subQ47,subQ46,subQ44,sQuery(id+"F22.wireOp",EDGE,"E28.9.1"),subQ43,subQ42])]})])],"derivedFrom":subQ11})])]}),makeQuery(id+"F47.opFillet","BLEND_FACE",FACE,{"disambiguationData":[OSD([subQ0,subQ9]),TDD([makeQuery(id+"F42.boolean.opBoolean","COPY",EDGE,{"disambiguationData":[TD([makeQuery(id+"F33.opLoft","SWEPT_FACE",FACE,{"disambiguationData":[OSD([subQ41,subQ40,subQ38,sQuery(id+"F22.wireOp",EDGE,"E28.10.1"),subQ37,subQ36])]})])],"derivedFrom":subQ11})])]}),makeQuery(id+"F47.opFillet","BLEND_FACE",FACE,{"disambiguationData":[OSD([subQ0,subQ9]),TDD([makeQuery(id+"F42.boolean.opBoolean","COPY",EDGE,{"disambiguationData":[TD([makeQuery(id+"F34.opLoft","SWEPT_FACE",FACE,{"disambiguationData":[OSD([subQ35,subQ34,subQ32,sQuery(id+"F22.wireOp",EDGE,"E28.11.1"),subQ31,subQ30])]})])],"derivedFrom":subQ11})])]}),makeQuery(id+"F47.opFillet","BLEND_FACE",FACE,{"disambiguationData":[OSD([subQ0,subQ9]),TDD([makeQuery(id+"F42.boolean.opBoolean","COPY",EDGE,{"disambiguationData":[TD([makeQuery(id+"F35.opLoft","SWEPT_FACE",FACE,{"disambiguationData":[OSD([subQ29,subQ28,subQ26,sQuery(id+"F22.wireOp",EDGE,"E28.12.1"),subQ25,subQ24])]})])],"derivedFrom":subQ11})])]}),makeQuery(id+"F47.opFillet","BLEND_FACE",FACE,{"disambiguationData":[OSD([subQ0,subQ9]),TDD([makeQuery(id+"F42.boolean.opBoolean","COPY",EDGE,{"disambiguationData":[TD([makeQuery(id+"F36.opLoft","SWEPT_FACE",FACE,{"disambiguationData":[OSD([subQ23,subQ22,subQ20,sQuery(id+"F22.wireOp",EDGE,"E28.13.1"),subQ19,subQ18])]})])],"derivedFrom":subQ11})])]}),makeQuery(id+"F47.opFillet","BLEND_FACE",FACE,{"disambiguationData":[OSD([subQ0,subQ9]),TDD([makeQuery(id+"F42.boolean.opBoolean","COPY",EDGE,{"disambiguationData":[TD([makeQuery(id+"F37.opLoft","SWEPT_FACE",FACE,{"disambiguationData":[OSD([subQ16,subQ15,subQ14,sQuery(id+"F22.wireOp",EDGE,"E28.14.1"),subQ13,subQ12])]})])],"derivedFrom":subQ11})])]}),makeQuery(id+"F47.opFillet","BLEND_FACE",FACE,{"disambiguationData":[OSD([subQ0,subQ9]),TDD([makeQuery(id+"F42.boolean.opBoolean","COPY",EDGE,{"disambiguationData":[TD([makeQuery(id+"F38.opLoft","SWEPT_FACE",FACE,{"disambiguationData":[OSD([subQ8,subQ7,subQ5,sQuery(id+"F22.wireOp",EDGE,"E28.15.1"),subQ4,subQ3])]})])],"derivedFrom":subQ11})])]})],"blendedInto":[makeQuery(id+"F47.opFillet","BLEND_FACE",FACE,{"disambiguationData":[OSD([subQ0,subQ9]),TDD([makeQuery(id+"F42.boolean.opBoolean","COPY",EDGE,{"disambiguationData":[TD([makeQuery(id+"F23.opLoft","SWEPT_FACE",FACE,{"disambiguationData":[OSD([sQuery(id+"F3.wireOp",EDGE,"E20.8.0"),subQ103,subQ101,subQ100,subQ99,sQuery(id+"F22.wireOp",EDGE,"E27.right")])]})])],"derivedFrom":subQ11})])]}),makeQuery(id+"F47.opFillet","BLEND_FACE",FACE,{"disambiguationData":[OSD([subQ0,subQ9]),TDD([makeQuery(id+"F42.boolean.opBoolean","COPY",EDGE,{"disambiguationData":[TD([subQ98])],"derivedFrom":subQ11})])]}),makeQuery(id+"F47.opFillet","BLEND_FACE",FACE,{"disambiguationData":[OSD([subQ0,subQ9]),TDD([makeQuery(id+"F42.boolean.opBoolean","COPY",EDGE,{"disambiguationData":[TD([subQ91])],"derivedFrom":subQ11})])]}),makeQuery(id+"F47.opFillet","BLEND_FACE",FACE,{"disambiguationData":[OSD([subQ0,subQ9]),TDD([makeQuery(id+"F42.boolean.opBoolean","COPY",EDGE,{"disambiguationData":[TD([subQ85])],"derivedFrom":subQ11})])]}),makeQuery(id+"F47.opFillet","BLEND_FACE",FACE,{"disambiguationData":[OSD([subQ0,subQ9]),TDD([makeQuery(id+"F42.boolean.opBoolean","COPY",EDGE,{"disambiguationData":[TD([makeQuery(id+"F27.opLoft","SWEPT_FACE",FACE,{"disambiguationData":[OSD([subQ77,subQ76,subQ74,sQuery(id+"F22.wireOp",EDGE,"E28.4.1"),subQ73,subQ72])]})])],"derivedFrom":subQ11})])]}),makeQuery(id+"F47.opFillet","BLEND_FACE",FACE,{"disambiguationData":[OSD([subQ0,subQ9]),TDD([makeQuery(id+"F42.boolean.opBoolean","COPY",EDGE,{"disambiguationData":[TD([makeQuery(id+"F28.opLoft","SWEPT_FACE",FACE,{"disambiguationData":[OSD([subQ71,subQ70,subQ68,sQuery(id+"F22.wireOp",EDGE,"E28.5.1"),subQ67,subQ66])]})])],"derivedFrom":subQ11})])]}),makeQuery(id+"F47.opFillet","BLEND_FACE",FACE,{"disambiguationData":[OSD([subQ0,subQ9]),TDD([makeQuery(id+"F42.boolean.opBoolean","COPY",EDGE,{"disambiguationData":[TD([makeQuery(id+"F29.opLoft","SWEPT_FACE",FACE,{"disambiguationData":[OSD([subQ65,subQ64,subQ62,sQuery(id+"F22.wireOp",EDGE,"E28.6.1"),subQ61,subQ60])]})])],"derivedFrom":subQ11})])]}),makeQuery(id+"F47.opFillet","BLEND_FACE",FACE,{"disambiguationData":[OSD([subQ0,subQ9]),TDD([makeQuery(id+"F42.boolean.opBoolean","COPY",EDGE,{"disambiguationData":[TD([makeQuery(id+"F30.opLoft","SWEPT_FACE",FACE,{"disambiguationData":[OSD([subQ58,subQ57,subQ56,sQuery(id+"F22.wireOp",EDGE,"E28.7.1"),subQ55,subQ54])]})])],"derivedFrom":subQ11})])]}),makeQuery(id+"F47.opFillet","BLEND_FACE",FACE,{"disambiguationData":[OSD([subQ0,subQ9]),TDD([makeQuery(id+"F42.boolean.opBoolean","COPY",EDGE,{"disambiguationData":[TD([makeQuery(id+"F31.opLoft","SWEPT_FACE",FACE,{"disambiguationData":[OSD([subQ52,subQ51,subQ53,sQuery(id+"F22.wireOp",EDGE,"E28.8.1"),subQ49,subQ48])]})])],"derivedFrom":subQ11})])]}),makeQuery(id+"F47.opFillet","BLEND_FACE",FACE,{"disambiguationData":[OSD([subQ0,subQ9]),TDD([makeQuery(id+"F42.boolean.opBoolean","COPY",EDGE,{"disambiguationData":[TD([makeQuery(id+"F32.opLoft","SWEPT_FACE",FACE,{"disambiguationData":[OSD([subQ47,subQ46,subQ44,sQuery(id+"F22.wireOp",EDGE,"E28.9.1"),subQ43,subQ42])]})])],"derivedFrom":subQ11})])]}),makeQuery(id+"F47.opFillet","BLEND_FACE",FACE,{"disambiguationData":[OSD([subQ0,subQ9]),TDD([makeQuery(id+"F42.boolean.opBoolean","COPY",EDGE,{"disambiguationData":[TD([makeQuery(id+"F33.opLoft","SWEPT_FACE",FACE,{"disambiguationData":[OSD([subQ41,subQ40,subQ38,sQuery(id+"F22.wireOp",EDGE,"E28.10.1"),subQ37,subQ36])]})])],"derivedFrom":subQ11})])]}),makeQuery(id+"F47.opFillet","BLEND_FACE",FACE,{"disambiguationData":[OSD([subQ0,subQ9]),TDD([makeQuery(id+"F42.boolean.opBoolean","COPY",EDGE,{"disambiguationData":[TD([makeQuery(id+"F34.opLoft","SWEPT_FACE",FACE,{"disambiguationData":[OSD([subQ35,subQ34,subQ32,sQuery(id+"F22.wireOp",EDGE,"E28.11.1"),subQ31,subQ30])]})])],"derivedFrom":subQ11})])]}),makeQuery(id+"F47.opFillet","BLEND_FACE",FACE,{"disambiguationData":[OSD([subQ0,subQ9]),TDD([makeQuery(id+"F42.boolean.opBoolean","COPY",EDGE,{"disambiguationData":[TD([makeQuery(id+"F35.opLoft","SWEPT_FACE",FACE,{"disambiguationData":[OSD([subQ29,subQ28,subQ26,sQuery(id+"F22.wireOp",EDGE,"E28.12.1"),subQ25,subQ24])]})])],"derivedFrom":subQ11})])]}),makeQuery(id+"F47.opFillet","BLEND_FACE",FACE,{"disambiguationData":[OSD([subQ0,subQ9]),TDD([makeQuery(id+"F42.boolean.opBoolean","COPY",EDGE,{"disambiguationData":[TD([makeQuery(id+"F36.opLoft","SWEPT_FACE",FACE,{"disambiguationData":[OSD([subQ23,subQ22,subQ20,sQuery(id+"F22.wireOp",EDGE,"E28.13.1"),subQ19,subQ18])]})])],"derivedFrom":subQ11})])]}),makeQuery(id+"F47.opFillet","BLEND_FACE",FACE,{"disambiguationData":[OSD([subQ0,subQ9]),TDD([makeQuery(id+"F42.boolean.opBoolean","COPY",EDGE,{"disambiguationData":[TD([makeQuery(id+"F37.opLoft","SWEPT_FACE",FACE,{"disambiguationData":[OSD([subQ16,subQ15,subQ14,sQuery(id+"F22.wireOp",EDGE,"E28.14.1"),subQ13,subQ12])]})])],"derivedFrom":subQ11})])]}),makeQuery(id+"F47.opFillet","BLEND_FACE",FACE,{"disambiguationData":[OSD([subQ0,subQ9]),TDD([makeQuery(id+"F42.boolean.opBoolean","COPY",EDGE,{"disambiguationData":[TD([makeQuery(id+"F38.opLoft","SWEPT_FACE",FACE,{"disambiguationData":[OSD([subQ8,subQ7,subQ5,sQuery(id+"F22.wireOp",EDGE,"E28.15.1"),subQ4,subQ3])]})])],"derivedFrom":subQ11})])]})]});}
            var Q33;
            {var subQ0=sQuery(id+"F41.wireOp",EDGE,"E34");var subQ1=sQuery(id+"F41.wireOp",EDGE,"E32");Q33=makeQuery(id+"F42.boolean.opBoolean","INTERSECT",EDGE,{"derivedFrom":[makeQuery(id+"F25.opLoft","SWEPT_FACE",FACE,{"disambiguationData":[OSD([sQuery(id+"F3.wireOp",EDGE,"E20.10.0"),sQuery(id+"F3.wireOp",EDGE,"E20.10.1"),sQuery(id+"F3.wireOp",EDGE,"E20.10.3"),sQuery(id+"F22.wireOp",EDGE,"E28.2.1"),sQuery(id+"F22.wireOp",EDGE,"E28.2.2"),sQuery(id+"F22.wireOp",EDGE,"E28.2.3")])]}),makeQuery(id+"F42.opRevolve","SWEPT_FACE",FACE,{"disambiguationData":[OSD([subQ1]),TDD([makeQuery(id+"F41.imprint","IMPRINT",EDGE,{"disambiguationData":[TD([[makeQuery(id+"F41.imprint","INTERSECT",VERTEX,{"disambiguationData":[OD(0.0)],"derivedFrom":[subQ1,subQ0]}),-1.0]])],"derivedFrom":subQ1})])]})]});}
            var Q34;
            {var subQ0=sQuery(id+"F22.wireOp",EDGE,"E28.3.0");var subQ1=sQuery(id+"F22.wireOp",EDGE,"E28.3.1");var subQ2=sQuery(id+"F22.wireOp",EDGE,"E28.3.2");var subQ3=sQuery(id+"F22.wireOp",EDGE,"E28.3.3");var subQ4=sQuery(id+"F3.wireOp",EDGE,"E20.11.3");var subQ5=sQuery(id+"F3.wireOp",EDGE,"E20.11.1");var subQ6=makeQuery(id+"F26.opLoft","SWEPT_FACE",FACE,{"disambiguationData":[OSD([subQ5,sQuery(id+"F3.wireOp",EDGE,"E20.11.2"),subQ4,subQ0,subQ2,subQ3])]});var subQ7=sQuery(id+"F41.wireOp",EDGE,"E34");var subQ8=sQuery(id+"F41.wireOp",EDGE,"E32");Q34=makeQuery(id+"F44.opFillet","BLEND_EDGE",EDGE,{"blendedFrom":[makeQuery(id+"F40.boolean.opBoolean","INTERSECT",EDGE,{"derivedFrom":[subQ6,makeQuery(id+"F40.opExtrude","CAP_FACE",FACE,{"disambiguationData":[OSD([sQuery(id+"F39.wireOp",EDGE,"E29"),sQuery(id+"F39.wireOp",EDGE,"E30")])],"isStart":true})]}),makeQuery(id+"F42.boolean.opBoolean","COPY",FACE,{"disambiguationData":[TD([makeQuery(id+"F26.opLoft","SWEPT_FACE",FACE,{"disambiguationData":[OSD([sQuery(id+"F3.wireOp",EDGE,"E20.11.0"),subQ5,subQ4,subQ1,subQ2,subQ3])]})])],"derivedFrom":makeQuery(id+"F42.opRevolve","SWEPT_FACE",FACE,{"disambiguationData":[OSD([subQ8]),TDD([makeQuery(id+"F41.imprint","IMPRINT",EDGE,{"disambiguationData":[TD([[makeQuery(id+"F41.imprint","INTERSECT",VERTEX,{"disambiguationData":[OD(0.0)],"derivedFrom":[subQ8,subQ7]}),-1.0]])],"derivedFrom":subQ8})])]})})],"blendedInto":[makeQuery(id+"F42.boolean.opBoolean","COPY",FACE,{"disambiguationData":[TD([makeQuery(id+"F26.opLoft","SWEPT_FACE",FACE,{"disambiguationData":[OSD([sQuery(id+"F3.wireOp",EDGE,"E20.11.0"),subQ5,subQ4,subQ1,subQ2,subQ3])]})])],"derivedFrom":makeQuery(id+"F42.opRevolve","SWEPT_FACE",FACE,{"disambiguationData":[OSD([subQ8]),TDD([makeQuery(id+"F41.imprint","IMPRINT",EDGE,{"disambiguationData":[TD([[makeQuery(id+"F41.imprint","INTERSECT",VERTEX,{"disambiguationData":[OD(0.0)],"derivedFrom":[subQ8,subQ7]}),-1.0]])],"derivedFrom":subQ8})])]})})]});}
            var Q35;
            {var subQ0=sQuery(id+"F41.wireOp",EDGE,"E37");var subQ1=makeQuery(id+"F42.opRevolve","SWEPT_FACE",FACE,{"disambiguationData":[OSD([subQ0])]});var subQ2=makeQuery(id+"F40.opExtrude","CAP_FACE",FACE,{"disambiguationData":[OSD([sQuery(id+"F39.wireOp",EDGE,"E29"),sQuery(id+"F39.wireOp",EDGE,"E30")])],"isStart":true});var subQ3=sQuery(id+"F22.wireOp",EDGE,"E28.15.3");var subQ4=sQuery(id+"F22.wireOp",EDGE,"E28.15.2");var subQ5=sQuery(id+"F3.wireOp",EDGE,"E20.7.3");var subQ7=sQuery(id+"F3.wireOp",EDGE,"E20.7.1");var subQ8=sQuery(id+"F3.wireOp",EDGE,"E20.7.0");var subQ9=sQuery(id+"F41.wireOp",EDGE,"E38");var subQ10=makeQuery(id+"F42.opRevolve","SWEPT_FACE",FACE,{"disambiguationData":[OSD([subQ9])]});var subQ11=makeQuery(id+"F42.opRevolve","SWEPT_EDGE",EDGE,{"disambiguationData":[OSD([subQ0,subQ9])]});var subQ12=sQuery(id+"F22.wireOp",EDGE,"E28.14.3");var subQ13=sQuery(id+"F22.wireOp",EDGE,"E28.14.2");var subQ14=sQuery(id+"F3.wireOp",EDGE,"E20.6.3");var subQ15=sQuery(id+"F3.wireOp",EDGE,"E20.6.1");var subQ16=sQuery(id+"F3.wireOp",EDGE,"E20.6.0");var subQ18=sQuery(id+"F22.wireOp",EDGE,"E28.13.3");var subQ19=sQuery(id+"F22.wireOp",EDGE,"E28.13.2");var subQ20=sQuery(id+"F3.wireOp",EDGE,"E20.5.3");var subQ22=sQuery(id+"F3.wireOp",EDGE,"E20.5.1");var subQ23=sQuery(id+"F3.wireOp",EDGE,"E20.5.0");var subQ24=sQuery(id+"F22.wireOp",EDGE,"E28.12.3");var subQ25=sQuery(id+"F22.wireOp",EDGE,"E28.12.2");var subQ26=sQuery(id+"F3.wireOp",EDGE,"E20.4.3");var subQ28=sQuery(id+"F3.wireOp",EDGE,"E20.4.1");var subQ29=sQuery(id+"F3.wireOp",EDGE,"E20.4.0");var subQ30=sQuery(id+"F22.wireOp",EDGE,"E28.11.3");var subQ31=sQuery(id+"F22.wireOp",EDGE,"E28.11.2");var subQ32=sQuery(id+"F3.wireOp",EDGE,"E20.3.3");var subQ34=sQuery(id+"F3.wireOp",EDGE,"E20.3.1");var subQ35=sQuery(id+"F3.wireOp",EDGE,"E20.3.0");var subQ36=sQuery(id+"F22.wireOp",EDGE,"E28.10.3");var subQ37=sQuery(id+"F22.wireOp",EDGE,"E28.10.2");var subQ38=sQuery(id+"F3.wireOp",EDGE,"E20.2.3");var subQ40=sQuery(id+"F3.wireOp",EDGE,"E20.2.1");var subQ41=sQuery(id+"F3.wireOp",EDGE,"E20.2.0");var subQ42=sQuery(id+"F22.wireOp",EDGE,"E28.9.3");var subQ43=sQuery(id+"F22.wireOp",EDGE,"E28.9.2");var subQ44=sQuery(id+"F3.wireOp",EDGE,"E20.1.3");var subQ46=sQuery(id+"F3.wireOp",EDGE,"E20.1.1");var subQ47=sQuery(id+"F3.wireOp",EDGE,"E20.1.0");var subQ48=sQuery(id+"F22.wireOp",EDGE,"E28.8.3");var subQ49=sQuery(id+"F22.wireOp",EDGE,"E28.8.2");var subQ51=sQuery(id+"F3.wireOp",EDGE,"E18.top");var subQ52=sQuery(id+"F3.wireOp",EDGE,"E18.bottom");var subQ53=sQuery(id+"F3.wireOp",EDGE,"E18.left");var subQ54=sQuery(id+"F22.wireOp",EDGE,"E28.7.3");var subQ55=sQuery(id+"F22.wireOp",EDGE,"E28.7.2");var subQ56=sQuery(id+"F3.wireOp",EDGE,"E20.15.3");var subQ57=sQuery(id+"F3.wireOp",EDGE,"E20.15.1");var subQ58=sQuery(id+"F3.wireOp",EDGE,"E20.15.0");var subQ60=sQuery(id+"F22.wireOp",EDGE,"E28.6.3");var subQ61=sQuery(id+"F22.wireOp",EDGE,"E28.6.2");var subQ62=sQuery(id+"F3.wireOp",EDGE,"E20.14.3");var subQ64=sQuery(id+"F3.wireOp",EDGE,"E20.14.1");var subQ65=sQuery(id+"F3.wireOp",EDGE,"E20.14.0");var subQ66=sQuery(id+"F22.wireOp",EDGE,"E28.5.3");var subQ67=sQuery(id+"F22.wireOp",EDGE,"E28.5.2");var subQ68=sQuery(id+"F3.wireOp",EDGE,"E20.13.3");var subQ70=sQuery(id+"F3.wireOp",EDGE,"E20.13.1");var subQ71=sQuery(id+"F3.wireOp",EDGE,"E20.13.0");var subQ72=sQuery(id+"F22.wireOp",EDGE,"E28.4.3");var subQ73=sQuery(id+"F22.wireOp",EDGE,"E28.4.2");var subQ74=sQuery(id+"F3.wireOp",EDGE,"E20.12.3");var subQ76=sQuery(id+"F3.wireOp",EDGE,"E20.12.1");var subQ77=sQuery(id+"F3.wireOp",EDGE,"E20.12.0");var subQ78=sQuery(id+"F22.wireOp",EDGE,"E28.3.3");var subQ79=sQuery(id+"F22.wireOp",EDGE,"E28.3.2");var subQ80=sQuery(id+"F3.wireOp",EDGE,"E20.11.3");var subQ82=sQuery(id+"F3.wireOp",EDGE,"E20.11.1");var subQ83=sQuery(id+"F3.wireOp",EDGE,"E20.11.0");var subQ84=sQuery(id+"F22.wireOp",EDGE,"E28.2.3");var subQ85=sQuery(id+"F22.wireOp",EDGE,"E28.2.2");var subQ86=sQuery(id+"F3.wireOp",EDGE,"E20.10.3");var subQ87=sQuery(id+"F3.wireOp",EDGE,"E20.10.1");var subQ88=sQuery(id+"F3.wireOp",EDGE,"E20.10.0");var subQ89=makeQuery(id+"F25.opLoft","SWEPT_FACE",FACE,{"disambiguationData":[OSD([subQ88,subQ87,subQ86,sQuery(id+"F22.wireOp",EDGE,"E28.2.1"),subQ85,subQ84])]});var subQ92=sQuery(id+"F22.wireOp",EDGE,"E28.1.3");var subQ93=sQuery(id+"F22.wireOp",EDGE,"E28.1.2");var subQ94=sQuery(id+"F3.wireOp",EDGE,"E20.9.3");var subQ95=sQuery(id+"F3.wireOp",EDGE,"E20.9.1");var subQ96=sQuery(id+"F3.wireOp",EDGE,"E20.9.0");var subQ97=makeQuery(id+"F24.opLoft","SWEPT_FACE",FACE,{"disambiguationData":[OSD([subQ96,subQ95,subQ94,sQuery(id+"F22.wireOp",EDGE,"E28.1.1"),subQ93,subQ92])]});var subQ98=sQuery(id+"F22.wireOp",EDGE,"E27.top");var subQ99=sQuery(id+"F22.wireOp",EDGE,"E27.bottom");var subQ100=sQuery(id+"F3.wireOp",EDGE,"E20.8.3");var subQ102=sQuery(id+"F3.wireOp",EDGE,"E20.8.1");var subQ106=makeQuery(id+"F42.boolean.opBoolean","COPY",FACE,{"disambiguationData":[TD([subQ89])],"derivedFrom":subQ10});var subQ135=makeQuery(id+"F25.boolean.opBoolean","INTERSECT",EDGE,{"derivedFrom":[makeQuery(id+"F24.boolean.opBoolean","SPLIT",FACE,{"disambiguationData":[TD([makeQuery(id+"F5.opLoft","CAP_FACE",FACE,{"disambiguationData":[OSD([makeQuery(id+"F3.imprint","IMPRINT",FACE,{"disambiguationData":[TD([[makeQuery(id+"F3.imprint","IMPRINT",EDGE,{"derivedFrom":subQ52}),1.0]])]})])],"isStart":true})])],"derivedFrom":makeQuery(id+"F1.opRevolve","SWEPT_FACE",FACE,{"disambiguationData":[OSD([sQuery(id+"F0.wireOp",EDGE,"E4")])]})}),subQ89]});Q35=makeQuery(id+"F48.opFillet","BLEND_EDGE",EDGE,{"blendedFrom":[makeQuery(id+"F47.opFillet","TWEAK_EDGE",EDGE,{"derivedFrom":[makeQuery(id+"F45.opFillet","BLEND_VERTEX",VERTEX,{"blendedFrom":[subQ135,subQ89,subQ106],"blendedInto":[subQ89,subQ106]}),makeQuery(id+"F45.opFillet","BLEND_VERTEX",VERTEX,{"blendedFrom":[subQ135,makeQuery(id+"F42.boolean.opBoolean","MERGE",FACE,{"derivedFrom":[subQ2,subQ1]}),subQ106],"blendedInto":[makeQuery(id+"F42.boolean.opBoolean","MERGE",FACE,{"derivedFrom":[subQ2,subQ1]}),subQ106]})]}),makeQuery(id+"F47.opFillet","BLEND_FACE",FACE,{"disambiguationData":[OSD([subQ0,subQ9]),TDD([makeQuery(id+"F42.boolean.opBoolean","COPY",EDGE,{"disambiguationData":[TD([makeQuery(id+"F23.opLoft","SWEPT_FACE",FACE,{"disambiguationData":[OSD([sQuery(id+"F3.wireOp",EDGE,"E20.8.0"),subQ102,subQ100,subQ99,subQ98,sQuery(id+"F22.wireOp",EDGE,"E27.right")])]})])],"derivedFrom":subQ11})])]}),makeQuery(id+"F47.opFillet","BLEND_FACE",FACE,{"disambiguationData":[OSD([subQ0,subQ9]),TDD([makeQuery(id+"F42.boolean.opBoolean","COPY",EDGE,{"disambiguationData":[TD([subQ97])],"derivedFrom":subQ11})])]}),makeQuery(id+"F47.opFillet","BLEND_FACE",FACE,{"disambiguationData":[OSD([subQ0,subQ9]),TDD([makeQuery(id+"F42.boolean.opBoolean","COPY",EDGE,{"disambiguationData":[TD([subQ89])],"derivedFrom":subQ11})])]}),makeQuery(id+"F47.opFillet","BLEND_FACE",FACE,{"disambiguationData":[OSD([subQ0,subQ9]),TDD([makeQuery(id+"F42.boolean.opBoolean","COPY",EDGE,{"disambiguationData":[TD([makeQuery(id+"F26.opLoft","SWEPT_FACE",FACE,{"disambiguationData":[OSD([subQ83,subQ82,subQ80,sQuery(id+"F22.wireOp",EDGE,"E28.3.1"),subQ79,subQ78])]})])],"derivedFrom":subQ11})])]}),makeQuery(id+"F47.opFillet","BLEND_FACE",FACE,{"disambiguationData":[OSD([subQ0,subQ9]),TDD([makeQuery(id+"F42.boolean.opBoolean","COPY",EDGE,{"disambiguationData":[TD([makeQuery(id+"F27.opLoft","SWEPT_FACE",FACE,{"disambiguationData":[OSD([subQ77,subQ76,subQ74,sQuery(id+"F22.wireOp",EDGE,"E28.4.1"),subQ73,subQ72])]})])],"derivedFrom":subQ11})])]}),makeQuery(id+"F47.opFillet","BLEND_FACE",FACE,{"disambiguationData":[OSD([subQ0,subQ9]),TDD([makeQuery(id+"F42.boolean.opBoolean","COPY",EDGE,{"disambiguationData":[TD([makeQuery(id+"F28.opLoft","SWEPT_FACE",FACE,{"disambiguationData":[OSD([subQ71,subQ70,subQ68,sQuery(id+"F22.wireOp",EDGE,"E28.5.1"),subQ67,subQ66])]})])],"derivedFrom":subQ11})])]}),makeQuery(id+"F47.opFillet","BLEND_FACE",FACE,{"disambiguationData":[OSD([subQ0,subQ9]),TDD([makeQuery(id+"F42.boolean.opBoolean","COPY",EDGE,{"disambiguationData":[TD([makeQuery(id+"F29.opLoft","SWEPT_FACE",FACE,{"disambiguationData":[OSD([subQ65,subQ64,subQ62,sQuery(id+"F22.wireOp",EDGE,"E28.6.1"),subQ61,subQ60])]})])],"derivedFrom":subQ11})])]}),makeQuery(id+"F47.opFillet","BLEND_FACE",FACE,{"disambiguationData":[OSD([subQ0,subQ9]),TDD([makeQuery(id+"F42.boolean.opBoolean","COPY",EDGE,{"disambiguationData":[TD([makeQuery(id+"F30.opLoft","SWEPT_FACE",FACE,{"disambiguationData":[OSD([subQ58,subQ57,subQ56,sQuery(id+"F22.wireOp",EDGE,"E28.7.1"),subQ55,subQ54])]})])],"derivedFrom":subQ11})])]}),makeQuery(id+"F47.opFillet","BLEND_FACE",FACE,{"disambiguationData":[OSD([subQ0,subQ9]),TDD([makeQuery(id+"F42.boolean.opBoolean","COPY",EDGE,{"disambiguationData":[TD([makeQuery(id+"F31.opLoft","SWEPT_FACE",FACE,{"disambiguationData":[OSD([subQ52,subQ51,subQ53,sQuery(id+"F22.wireOp",EDGE,"E28.8.1"),subQ49,subQ48])]})])],"derivedFrom":subQ11})])]}),makeQuery(id+"F47.opFillet","BLEND_FACE",FACE,{"disambiguationData":[OSD([subQ0,subQ9]),TDD([makeQuery(id+"F42.boolean.opBoolean","COPY",EDGE,{"disambiguationData":[TD([makeQuery(id+"F32.opLoft","SWEPT_FACE",FACE,{"disambiguationData":[OSD([subQ47,subQ46,subQ44,sQuery(id+"F22.wireOp",EDGE,"E28.9.1"),subQ43,subQ42])]})])],"derivedFrom":subQ11})])]}),makeQuery(id+"F47.opFillet","BLEND_FACE",FACE,{"disambiguationData":[OSD([subQ0,subQ9]),TDD([makeQuery(id+"F42.boolean.opBoolean","COPY",EDGE,{"disambiguationData":[TD([makeQuery(id+"F33.opLoft","SWEPT_FACE",FACE,{"disambiguationData":[OSD([subQ41,subQ40,subQ38,sQuery(id+"F22.wireOp",EDGE,"E28.10.1"),subQ37,subQ36])]})])],"derivedFrom":subQ11})])]}),makeQuery(id+"F47.opFillet","BLEND_FACE",FACE,{"disambiguationData":[OSD([subQ0,subQ9]),TDD([makeQuery(id+"F42.boolean.opBoolean","COPY",EDGE,{"disambiguationData":[TD([makeQuery(id+"F34.opLoft","SWEPT_FACE",FACE,{"disambiguationData":[OSD([subQ35,subQ34,subQ32,sQuery(id+"F22.wireOp",EDGE,"E28.11.1"),subQ31,subQ30])]})])],"derivedFrom":subQ11})])]}),makeQuery(id+"F47.opFillet","BLEND_FACE",FACE,{"disambiguationData":[OSD([subQ0,subQ9]),TDD([makeQuery(id+"F42.boolean.opBoolean","COPY",EDGE,{"disambiguationData":[TD([makeQuery(id+"F35.opLoft","SWEPT_FACE",FACE,{"disambiguationData":[OSD([subQ29,subQ28,subQ26,sQuery(id+"F22.wireOp",EDGE,"E28.12.1"),subQ25,subQ24])]})])],"derivedFrom":subQ11})])]}),makeQuery(id+"F47.opFillet","BLEND_FACE",FACE,{"disambiguationData":[OSD([subQ0,subQ9]),TDD([makeQuery(id+"F42.boolean.opBoolean","COPY",EDGE,{"disambiguationData":[TD([makeQuery(id+"F36.opLoft","SWEPT_FACE",FACE,{"disambiguationData":[OSD([subQ23,subQ22,subQ20,sQuery(id+"F22.wireOp",EDGE,"E28.13.1"),subQ19,subQ18])]})])],"derivedFrom":subQ11})])]}),makeQuery(id+"F47.opFillet","BLEND_FACE",FACE,{"disambiguationData":[OSD([subQ0,subQ9]),TDD([makeQuery(id+"F42.boolean.opBoolean","COPY",EDGE,{"disambiguationData":[TD([makeQuery(id+"F37.opLoft","SWEPT_FACE",FACE,{"disambiguationData":[OSD([subQ16,subQ15,subQ14,sQuery(id+"F22.wireOp",EDGE,"E28.14.1"),subQ13,subQ12])]})])],"derivedFrom":subQ11})])]}),makeQuery(id+"F47.opFillet","BLEND_FACE",FACE,{"disambiguationData":[OSD([subQ0,subQ9]),TDD([makeQuery(id+"F42.boolean.opBoolean","COPY",EDGE,{"disambiguationData":[TD([makeQuery(id+"F38.opLoft","SWEPT_FACE",FACE,{"disambiguationData":[OSD([subQ8,subQ7,subQ5,sQuery(id+"F22.wireOp",EDGE,"E28.15.1"),subQ4,subQ3])]})])],"derivedFrom":subQ11})])]})],"blendedInto":[makeQuery(id+"F47.opFillet","BLEND_FACE",FACE,{"disambiguationData":[OSD([subQ0,subQ9]),TDD([makeQuery(id+"F42.boolean.opBoolean","COPY",EDGE,{"disambiguationData":[TD([makeQuery(id+"F23.opLoft","SWEPT_FACE",FACE,{"disambiguationData":[OSD([sQuery(id+"F3.wireOp",EDGE,"E20.8.0"),subQ102,subQ100,subQ99,subQ98,sQuery(id+"F22.wireOp",EDGE,"E27.right")])]})])],"derivedFrom":subQ11})])]}),makeQuery(id+"F47.opFillet","BLEND_FACE",FACE,{"disambiguationData":[OSD([subQ0,subQ9]),TDD([makeQuery(id+"F42.boolean.opBoolean","COPY",EDGE,{"disambiguationData":[TD([subQ97])],"derivedFrom":subQ11})])]}),makeQuery(id+"F47.opFillet","BLEND_FACE",FACE,{"disambiguationData":[OSD([subQ0,subQ9]),TDD([makeQuery(id+"F42.boolean.opBoolean","COPY",EDGE,{"disambiguationData":[TD([subQ89])],"derivedFrom":subQ11})])]}),makeQuery(id+"F47.opFillet","BLEND_FACE",FACE,{"disambiguationData":[OSD([subQ0,subQ9]),TDD([makeQuery(id+"F42.boolean.opBoolean","COPY",EDGE,{"disambiguationData":[TD([makeQuery(id+"F26.opLoft","SWEPT_FACE",FACE,{"disambiguationData":[OSD([subQ83,subQ82,subQ80,sQuery(id+"F22.wireOp",EDGE,"E28.3.1"),subQ79,subQ78])]})])],"derivedFrom":subQ11})])]}),makeQuery(id+"F47.opFillet","BLEND_FACE",FACE,{"disambiguationData":[OSD([subQ0,subQ9]),TDD([makeQuery(id+"F42.boolean.opBoolean","COPY",EDGE,{"disambiguationData":[TD([makeQuery(id+"F27.opLoft","SWEPT_FACE",FACE,{"disambiguationData":[OSD([subQ77,subQ76,subQ74,sQuery(id+"F22.wireOp",EDGE,"E28.4.1"),subQ73,subQ72])]})])],"derivedFrom":subQ11})])]}),makeQuery(id+"F47.opFillet","BLEND_FACE",FACE,{"disambiguationData":[OSD([subQ0,subQ9]),TDD([makeQuery(id+"F42.boolean.opBoolean","COPY",EDGE,{"disambiguationData":[TD([makeQuery(id+"F28.opLoft","SWEPT_FACE",FACE,{"disambiguationData":[OSD([subQ71,subQ70,subQ68,sQuery(id+"F22.wireOp",EDGE,"E28.5.1"),subQ67,subQ66])]})])],"derivedFrom":subQ11})])]}),makeQuery(id+"F47.opFillet","BLEND_FACE",FACE,{"disambiguationData":[OSD([subQ0,subQ9]),TDD([makeQuery(id+"F42.boolean.opBoolean","COPY",EDGE,{"disambiguationData":[TD([makeQuery(id+"F29.opLoft","SWEPT_FACE",FACE,{"disambiguationData":[OSD([subQ65,subQ64,subQ62,sQuery(id+"F22.wireOp",EDGE,"E28.6.1"),subQ61,subQ60])]})])],"derivedFrom":subQ11})])]}),makeQuery(id+"F47.opFillet","BLEND_FACE",FACE,{"disambiguationData":[OSD([subQ0,subQ9]),TDD([makeQuery(id+"F42.boolean.opBoolean","COPY",EDGE,{"disambiguationData":[TD([makeQuery(id+"F30.opLoft","SWEPT_FACE",FACE,{"disambiguationData":[OSD([subQ58,subQ57,subQ56,sQuery(id+"F22.wireOp",EDGE,"E28.7.1"),subQ55,subQ54])]})])],"derivedFrom":subQ11})])]}),makeQuery(id+"F47.opFillet","BLEND_FACE",FACE,{"disambiguationData":[OSD([subQ0,subQ9]),TDD([makeQuery(id+"F42.boolean.opBoolean","COPY",EDGE,{"disambiguationData":[TD([makeQuery(id+"F31.opLoft","SWEPT_FACE",FACE,{"disambiguationData":[OSD([subQ52,subQ51,subQ53,sQuery(id+"F22.wireOp",EDGE,"E28.8.1"),subQ49,subQ48])]})])],"derivedFrom":subQ11})])]}),makeQuery(id+"F47.opFillet","BLEND_FACE",FACE,{"disambiguationData":[OSD([subQ0,subQ9]),TDD([makeQuery(id+"F42.boolean.opBoolean","COPY",EDGE,{"disambiguationData":[TD([makeQuery(id+"F32.opLoft","SWEPT_FACE",FACE,{"disambiguationData":[OSD([subQ47,subQ46,subQ44,sQuery(id+"F22.wireOp",EDGE,"E28.9.1"),subQ43,subQ42])]})])],"derivedFrom":subQ11})])]}),makeQuery(id+"F47.opFillet","BLEND_FACE",FACE,{"disambiguationData":[OSD([subQ0,subQ9]),TDD([makeQuery(id+"F42.boolean.opBoolean","COPY",EDGE,{"disambiguationData":[TD([makeQuery(id+"F33.opLoft","SWEPT_FACE",FACE,{"disambiguationData":[OSD([subQ41,subQ40,subQ38,sQuery(id+"F22.wireOp",EDGE,"E28.10.1"),subQ37,subQ36])]})])],"derivedFrom":subQ11})])]}),makeQuery(id+"F47.opFillet","BLEND_FACE",FACE,{"disambiguationData":[OSD([subQ0,subQ9]),TDD([makeQuery(id+"F42.boolean.opBoolean","COPY",EDGE,{"disambiguationData":[TD([makeQuery(id+"F34.opLoft","SWEPT_FACE",FACE,{"disambiguationData":[OSD([subQ35,subQ34,subQ32,sQuery(id+"F22.wireOp",EDGE,"E28.11.1"),subQ31,subQ30])]})])],"derivedFrom":subQ11})])]}),makeQuery(id+"F47.opFillet","BLEND_FACE",FACE,{"disambiguationData":[OSD([subQ0,subQ9]),TDD([makeQuery(id+"F42.boolean.opBoolean","COPY",EDGE,{"disambiguationData":[TD([makeQuery(id+"F35.opLoft","SWEPT_FACE",FACE,{"disambiguationData":[OSD([subQ29,subQ28,subQ26,sQuery(id+"F22.wireOp",EDGE,"E28.12.1"),subQ25,subQ24])]})])],"derivedFrom":subQ11})])]}),makeQuery(id+"F47.opFillet","BLEND_FACE",FACE,{"disambiguationData":[OSD([subQ0,subQ9]),TDD([makeQuery(id+"F42.boolean.opBoolean","COPY",EDGE,{"disambiguationData":[TD([makeQuery(id+"F36.opLoft","SWEPT_FACE",FACE,{"disambiguationData":[OSD([subQ23,subQ22,subQ20,sQuery(id+"F22.wireOp",EDGE,"E28.13.1"),subQ19,subQ18])]})])],"derivedFrom":subQ11})])]}),makeQuery(id+"F47.opFillet","BLEND_FACE",FACE,{"disambiguationData":[OSD([subQ0,subQ9]),TDD([makeQuery(id+"F42.boolean.opBoolean","COPY",EDGE,{"disambiguationData":[TD([makeQuery(id+"F37.opLoft","SWEPT_FACE",FACE,{"disambiguationData":[OSD([subQ16,subQ15,subQ14,sQuery(id+"F22.wireOp",EDGE,"E28.14.1"),subQ13,subQ12])]})])],"derivedFrom":subQ11})])]}),makeQuery(id+"F47.opFillet","BLEND_FACE",FACE,{"disambiguationData":[OSD([subQ0,subQ9]),TDD([makeQuery(id+"F42.boolean.opBoolean","COPY",EDGE,{"disambiguationData":[TD([makeQuery(id+"F38.opLoft","SWEPT_FACE",FACE,{"disambiguationData":[OSD([subQ8,subQ7,subQ5,sQuery(id+"F22.wireOp",EDGE,"E28.15.1"),subQ4,subQ3])]})])],"derivedFrom":subQ11})])]})]});}
            var Q36;
            {var subQ0=sQuery(id+"F22.wireOp",EDGE,"E28.2.3");var subQ1=sQuery(id+"F22.wireOp",EDGE,"E28.2.2");var subQ2=sQuery(id+"F22.wireOp",EDGE,"E28.2.1");var subQ3=sQuery(id+"F3.wireOp",EDGE,"E20.10.3");var subQ4=sQuery(id+"F3.wireOp",EDGE,"E20.10.1");var subQ5=sQuery(id+"F22.wireOp",EDGE,"E28.2.0");var subQ6=makeQuery(id+"F25.opLoft","SWEPT_FACE",FACE,{"disambiguationData":[OSD([subQ4,sQuery(id+"F3.wireOp",EDGE,"E20.10.2"),subQ3,subQ5,subQ1,subQ0])]});var subQ7=sQuery(id+"F41.wireOp",EDGE,"E34");var subQ8=sQuery(id+"F41.wireOp",EDGE,"E32");Q36=makeQuery(id+"F44.opFillet","BLEND_EDGE",EDGE,{"blendedFrom":[makeQuery(id+"F40.boolean.opBoolean","INTERSECT",EDGE,{"derivedFrom":[subQ6,makeQuery(id+"F40.opExtrude","CAP_FACE",FACE,{"disambiguationData":[OSD([sQuery(id+"F39.wireOp",EDGE,"E29"),sQuery(id+"F39.wireOp",EDGE,"E30")])],"isStart":true})]}),makeQuery(id+"F42.boolean.opBoolean","COPY",FACE,{"disambiguationData":[TD([makeQuery(id+"F25.opLoft","SWEPT_FACE",FACE,{"disambiguationData":[OSD([sQuery(id+"F3.wireOp",EDGE,"E20.10.0"),subQ4,subQ3,subQ2,subQ1,subQ0])]})])],"derivedFrom":makeQuery(id+"F42.opRevolve","SWEPT_FACE",FACE,{"disambiguationData":[OSD([subQ8]),TDD([makeQuery(id+"F41.imprint","IMPRINT",EDGE,{"disambiguationData":[TD([[makeQuery(id+"F41.imprint","INTERSECT",VERTEX,{"disambiguationData":[OD(0.0)],"derivedFrom":[subQ8,subQ7]}),-1.0]])],"derivedFrom":subQ8})])]})})],"blendedInto":[makeQuery(id+"F42.boolean.opBoolean","COPY",FACE,{"disambiguationData":[TD([makeQuery(id+"F25.opLoft","SWEPT_FACE",FACE,{"disambiguationData":[OSD([sQuery(id+"F3.wireOp",EDGE,"E20.10.0"),subQ4,subQ3,subQ2,subQ1,subQ0])]})])],"derivedFrom":makeQuery(id+"F42.opRevolve","SWEPT_FACE",FACE,{"disambiguationData":[OSD([subQ8]),TDD([makeQuery(id+"F41.imprint","IMPRINT",EDGE,{"disambiguationData":[TD([[makeQuery(id+"F41.imprint","INTERSECT",VERTEX,{"disambiguationData":[OD(0.0)],"derivedFrom":[subQ8,subQ7]}),-1.0]])],"derivedFrom":subQ8})])]})})]});}
            var Q37;
            {var subQ0=sQuery(id+"F41.wireOp",EDGE,"E34");var subQ1=sQuery(id+"F41.wireOp",EDGE,"E32");Q37=makeQuery(id+"F42.boolean.opBoolean","INTERSECT",EDGE,{"derivedFrom":[makeQuery(id+"F24.opLoft","SWEPT_FACE",FACE,{"disambiguationData":[OSD([sQuery(id+"F3.wireOp",EDGE,"E20.9.0"),sQuery(id+"F3.wireOp",EDGE,"E20.9.1"),sQuery(id+"F3.wireOp",EDGE,"E20.9.3"),sQuery(id+"F22.wireOp",EDGE,"E28.1.1"),sQuery(id+"F22.wireOp",EDGE,"E28.1.2"),sQuery(id+"F22.wireOp",EDGE,"E28.1.3")])]}),makeQuery(id+"F42.opRevolve","SWEPT_FACE",FACE,{"disambiguationData":[OSD([subQ1]),TDD([makeQuery(id+"F41.imprint","IMPRINT",EDGE,{"disambiguationData":[TD([[makeQuery(id+"F41.imprint","INTERSECT",VERTEX,{"disambiguationData":[OD(0.0)],"derivedFrom":[subQ1,subQ0]}),-1.0]])],"derivedFrom":subQ1})])]})]});}
            var Q38;
            {var subQ0=sQuery(id+"F41.wireOp",EDGE,"E37");var subQ1=makeQuery(id+"F42.opRevolve","SWEPT_FACE",FACE,{"disambiguationData":[OSD([subQ0])]});var subQ2=makeQuery(id+"F40.opExtrude","CAP_FACE",FACE,{"disambiguationData":[OSD([sQuery(id+"F39.wireOp",EDGE,"E29"),sQuery(id+"F39.wireOp",EDGE,"E30")])],"isStart":true});var subQ3=sQuery(id+"F22.wireOp",EDGE,"E28.15.3");var subQ4=sQuery(id+"F22.wireOp",EDGE,"E28.15.2");var subQ5=sQuery(id+"F3.wireOp",EDGE,"E20.7.3");var subQ6=sQuery(id+"F3.wireOp",EDGE,"E20.7.1");var subQ7=sQuery(id+"F41.wireOp",EDGE,"E38");var subQ8=makeQuery(id+"F42.opRevolve","SWEPT_FACE",FACE,{"disambiguationData":[OSD([subQ7])]});var subQ9=makeQuery(id+"F42.opRevolve","SWEPT_EDGE",EDGE,{"disambiguationData":[OSD([subQ0,subQ7])]});var subQ10=sQuery(id+"F22.wireOp",EDGE,"E28.14.3");var subQ11=sQuery(id+"F22.wireOp",EDGE,"E28.14.2");var subQ12=sQuery(id+"F3.wireOp",EDGE,"E20.6.3");var subQ13=sQuery(id+"F3.wireOp",EDGE,"E20.6.1");var subQ14=sQuery(id+"F22.wireOp",EDGE,"E28.13.3");var subQ15=sQuery(id+"F22.wireOp",EDGE,"E28.13.2");var subQ16=sQuery(id+"F3.wireOp",EDGE,"E20.5.3");var subQ17=sQuery(id+"F3.wireOp",EDGE,"E20.5.1");var subQ18=sQuery(id+"F22.wireOp",EDGE,"E28.12.3");var subQ19=sQuery(id+"F22.wireOp",EDGE,"E28.12.2");var subQ20=sQuery(id+"F3.wireOp",EDGE,"E20.4.3");var subQ21=sQuery(id+"F3.wireOp",EDGE,"E20.4.1");var subQ22=sQuery(id+"F22.wireOp",EDGE,"E28.11.3");var subQ23=sQuery(id+"F22.wireOp",EDGE,"E28.11.2");var subQ24=sQuery(id+"F3.wireOp",EDGE,"E20.3.3");var subQ25=sQuery(id+"F3.wireOp",EDGE,"E20.3.1");var subQ26=sQuery(id+"F22.wireOp",EDGE,"E28.10.3");var subQ27=sQuery(id+"F22.wireOp",EDGE,"E28.10.2");var subQ28=sQuery(id+"F3.wireOp",EDGE,"E20.2.3");var subQ29=sQuery(id+"F3.wireOp",EDGE,"E20.2.1");var subQ30=sQuery(id+"F22.wireOp",EDGE,"E28.9.3");var subQ31=sQuery(id+"F22.wireOp",EDGE,"E28.9.2");var subQ32=sQuery(id+"F3.wireOp",EDGE,"E20.1.3");var subQ33=sQuery(id+"F3.wireOp",EDGE,"E20.1.1");var subQ34=sQuery(id+"F22.wireOp",EDGE,"E28.8.3");var subQ35=sQuery(id+"F22.wireOp",EDGE,"E28.8.2");var subQ36=sQuery(id+"F3.wireOp",EDGE,"E18.top");var subQ37=sQuery(id+"F3.wireOp",EDGE,"E18.bottom");var subQ38=sQuery(id+"F22.wireOp",EDGE,"E28.7.3");var subQ39=sQuery(id+"F22.wireOp",EDGE,"E28.7.2");var subQ40=sQuery(id+"F3.wireOp",EDGE,"E20.15.3");var subQ41=sQuery(id+"F3.wireOp",EDGE,"E20.15.1");var subQ42=sQuery(id+"F22.wireOp",EDGE,"E28.6.3");var subQ43=sQuery(id+"F22.wireOp",EDGE,"E28.6.2");var subQ44=sQuery(id+"F3.wireOp",EDGE,"E20.14.3");var subQ45=sQuery(id+"F3.wireOp",EDGE,"E20.14.1");var subQ46=sQuery(id+"F22.wireOp",EDGE,"E28.5.3");var subQ47=sQuery(id+"F22.wireOp",EDGE,"E28.5.2");var subQ48=sQuery(id+"F3.wireOp",EDGE,"E20.13.3");var subQ49=sQuery(id+"F3.wireOp",EDGE,"E20.13.1");var subQ50=sQuery(id+"F22.wireOp",EDGE,"E28.4.3");var subQ51=sQuery(id+"F22.wireOp",EDGE,"E28.4.2");var subQ52=sQuery(id+"F3.wireOp",EDGE,"E20.12.3");var subQ53=sQuery(id+"F3.wireOp",EDGE,"E20.12.1");var subQ54=sQuery(id+"F22.wireOp",EDGE,"E28.3.3");var subQ55=sQuery(id+"F22.wireOp",EDGE,"E28.3.2");var subQ56=sQuery(id+"F3.wireOp",EDGE,"E20.11.3");var subQ57=sQuery(id+"F3.wireOp",EDGE,"E20.11.1");var subQ58=sQuery(id+"F22.wireOp",EDGE,"E28.2.3");var subQ59=sQuery(id+"F22.wireOp",EDGE,"E28.2.2");var subQ60=sQuery(id+"F3.wireOp",EDGE,"E20.10.3");var subQ61=sQuery(id+"F3.wireOp",EDGE,"E20.10.1");var subQ62=sQuery(id+"F22.wireOp",EDGE,"E28.1.3");var subQ63=sQuery(id+"F22.wireOp",EDGE,"E28.1.2");var subQ64=sQuery(id+"F3.wireOp",EDGE,"E20.9.3");var subQ65=sQuery(id+"F3.wireOp",EDGE,"E20.9.1");var subQ67=makeQuery(id+"F24.opLoft","SWEPT_FACE",FACE,{"disambiguationData":[OSD([sQuery(id+"F3.wireOp",EDGE,"E20.9.0"),subQ65,subQ64,sQuery(id+"F22.wireOp",EDGE,"E28.1.1"),subQ63,subQ62])]});var subQ68=sQuery(id+"F22.wireOp",EDGE,"E27.top");var subQ69=sQuery(id+"F22.wireOp",EDGE,"E27.bottom");var subQ70=sQuery(id+"F3.wireOp",EDGE,"E20.8.3");var subQ71=sQuery(id+"F3.wireOp",EDGE,"E20.8.1");var subQ74=makeQuery(id+"F42.boolean.opBoolean","COPY",FACE,{"disambiguationData":[TD([subQ67])],"derivedFrom":subQ8});var subQ75=makeQuery(id+"F24.boolean.opBoolean","INTERSECT",EDGE,{"derivedFrom":[makeQuery(id+"F1.opRevolve","SWEPT_FACE",FACE,{"disambiguationData":[OSD([sQuery(id+"F0.wireOp",EDGE,"E4")])]}),subQ67]});Q38=makeQuery(id+"F48.opFillet","BLEND_EDGE",EDGE,{"blendedFrom":[makeQuery(id+"F47.opFillet","TWEAK_EDGE",EDGE,{"derivedFrom":[makeQuery(id+"F45.opFillet","BLEND_VERTEX",VERTEX,{"blendedFrom":[subQ75,subQ67,subQ74],"blendedInto":[subQ67,subQ74]}),makeQuery(id+"F45.opFillet","BLEND_VERTEX",VERTEX,{"blendedFrom":[subQ75,makeQuery(id+"F42.boolean.opBoolean","MERGE",FACE,{"derivedFrom":[subQ2,subQ1]}),subQ74],"blendedInto":[makeQuery(id+"F42.boolean.opBoolean","MERGE",FACE,{"derivedFrom":[subQ2,subQ1]}),subQ74]})]}),makeQuery(id+"F47.opFillet","BLEND_FACE",FACE,{"disambiguationData":[OSD([subQ0,subQ7]),TDD([makeQuery(id+"F42.boolean.opBoolean","COPY",EDGE,{"disambiguationData":[TD([makeQuery(id+"F23.opLoft","SWEPT_FACE",FACE,{"disambiguationData":[OSD([sQuery(id+"F3.wireOp",EDGE,"E20.8.0"),subQ71,subQ70,subQ69,subQ68,sQuery(id+"F22.wireOp",EDGE,"E27.right")])]})])],"derivedFrom":subQ9})])]}),makeQuery(id+"F47.opFillet","BLEND_FACE",FACE,{"disambiguationData":[OSD([subQ0,subQ7]),TDD([makeQuery(id+"F42.boolean.opBoolean","COPY",EDGE,{"disambiguationData":[TD([subQ67])],"derivedFrom":subQ9})])]}),makeQuery(id+"F47.opFillet","BLEND_FACE",FACE,{"disambiguationData":[OSD([subQ0,subQ7]),TDD([makeQuery(id+"F42.boolean.opBoolean","COPY",EDGE,{"disambiguationData":[TD([makeQuery(id+"F25.opLoft","SWEPT_FACE",FACE,{"disambiguationData":[OSD([sQuery(id+"F3.wireOp",EDGE,"E20.10.0"),subQ61,subQ60,sQuery(id+"F22.wireOp",EDGE,"E28.2.1"),subQ59,subQ58])]})])],"derivedFrom":subQ9})])]}),makeQuery(id+"F47.opFillet","BLEND_FACE",FACE,{"disambiguationData":[OSD([subQ0,subQ7]),TDD([makeQuery(id+"F42.boolean.opBoolean","COPY",EDGE,{"disambiguationData":[TD([makeQuery(id+"F26.opLoft","SWEPT_FACE",FACE,{"disambiguationData":[OSD([sQuery(id+"F3.wireOp",EDGE,"E20.11.0"),subQ57,subQ56,sQuery(id+"F22.wireOp",EDGE,"E28.3.1"),subQ55,subQ54])]})])],"derivedFrom":subQ9})])]}),makeQuery(id+"F47.opFillet","BLEND_FACE",FACE,{"disambiguationData":[OSD([subQ0,subQ7]),TDD([makeQuery(id+"F42.boolean.opBoolean","COPY",EDGE,{"disambiguationData":[TD([makeQuery(id+"F27.opLoft","SWEPT_FACE",FACE,{"disambiguationData":[OSD([sQuery(id+"F3.wireOp",EDGE,"E20.12.0"),subQ53,subQ52,sQuery(id+"F22.wireOp",EDGE,"E28.4.1"),subQ51,subQ50])]})])],"derivedFrom":subQ9})])]}),makeQuery(id+"F47.opFillet","BLEND_FACE",FACE,{"disambiguationData":[OSD([subQ0,subQ7]),TDD([makeQuery(id+"F42.boolean.opBoolean","COPY",EDGE,{"disambiguationData":[TD([makeQuery(id+"F28.opLoft","SWEPT_FACE",FACE,{"disambiguationData":[OSD([sQuery(id+"F3.wireOp",EDGE,"E20.13.0"),subQ49,subQ48,sQuery(id+"F22.wireOp",EDGE,"E28.5.1"),subQ47,subQ46])]})])],"derivedFrom":subQ9})])]}),makeQuery(id+"F47.opFillet","BLEND_FACE",FACE,{"disambiguationData":[OSD([subQ0,subQ7]),TDD([makeQuery(id+"F42.boolean.opBoolean","COPY",EDGE,{"disambiguationData":[TD([makeQuery(id+"F29.opLoft","SWEPT_FACE",FACE,{"disambiguationData":[OSD([sQuery(id+"F3.wireOp",EDGE,"E20.14.0"),subQ45,subQ44,sQuery(id+"F22.wireOp",EDGE,"E28.6.1"),subQ43,subQ42])]})])],"derivedFrom":subQ9})])]}),makeQuery(id+"F47.opFillet","BLEND_FACE",FACE,{"disambiguationData":[OSD([subQ0,subQ7]),TDD([makeQuery(id+"F42.boolean.opBoolean","COPY",EDGE,{"disambiguationData":[TD([makeQuery(id+"F30.opLoft","SWEPT_FACE",FACE,{"disambiguationData":[OSD([sQuery(id+"F3.wireOp",EDGE,"E20.15.0"),subQ41,subQ40,sQuery(id+"F22.wireOp",EDGE,"E28.7.1"),subQ39,subQ38])]})])],"derivedFrom":subQ9})])]}),makeQuery(id+"F47.opFillet","BLEND_FACE",FACE,{"disambiguationData":[OSD([subQ0,subQ7]),TDD([makeQuery(id+"F42.boolean.opBoolean","COPY",EDGE,{"disambiguationData":[TD([makeQuery(id+"F31.opLoft","SWEPT_FACE",FACE,{"disambiguationData":[OSD([subQ37,subQ36,sQuery(id+"F3.wireOp",EDGE,"E18.left"),sQuery(id+"F22.wireOp",EDGE,"E28.8.1"),subQ35,subQ34])]})])],"derivedFrom":subQ9})])]}),makeQuery(id+"F47.opFillet","BLEND_FACE",FACE,{"disambiguationData":[OSD([subQ0,subQ7]),TDD([makeQuery(id+"F42.boolean.opBoolean","COPY",EDGE,{"disambiguationData":[TD([makeQuery(id+"F32.opLoft","SWEPT_FACE",FACE,{"disambiguationData":[OSD([sQuery(id+"F3.wireOp",EDGE,"E20.1.0"),subQ33,subQ32,sQuery(id+"F22.wireOp",EDGE,"E28.9.1"),subQ31,subQ30])]})])],"derivedFrom":subQ9})])]}),makeQuery(id+"F47.opFillet","BLEND_FACE",FACE,{"disambiguationData":[OSD([subQ0,subQ7]),TDD([makeQuery(id+"F42.boolean.opBoolean","COPY",EDGE,{"disambiguationData":[TD([makeQuery(id+"F33.opLoft","SWEPT_FACE",FACE,{"disambiguationData":[OSD([sQuery(id+"F3.wireOp",EDGE,"E20.2.0"),subQ29,subQ28,sQuery(id+"F22.wireOp",EDGE,"E28.10.1"),subQ27,subQ26])]})])],"derivedFrom":subQ9})])]}),makeQuery(id+"F47.opFillet","BLEND_FACE",FACE,{"disambiguationData":[OSD([subQ0,subQ7]),TDD([makeQuery(id+"F42.boolean.opBoolean","COPY",EDGE,{"disambiguationData":[TD([makeQuery(id+"F34.opLoft","SWEPT_FACE",FACE,{"disambiguationData":[OSD([sQuery(id+"F3.wireOp",EDGE,"E20.3.0"),subQ25,subQ24,sQuery(id+"F22.wireOp",EDGE,"E28.11.1"),subQ23,subQ22])]})])],"derivedFrom":subQ9})])]}),makeQuery(id+"F47.opFillet","BLEND_FACE",FACE,{"disambiguationData":[OSD([subQ0,subQ7]),TDD([makeQuery(id+"F42.boolean.opBoolean","COPY",EDGE,{"disambiguationData":[TD([makeQuery(id+"F35.opLoft","SWEPT_FACE",FACE,{"disambiguationData":[OSD([sQuery(id+"F3.wireOp",EDGE,"E20.4.0"),subQ21,subQ20,sQuery(id+"F22.wireOp",EDGE,"E28.12.1"),subQ19,subQ18])]})])],"derivedFrom":subQ9})])]}),makeQuery(id+"F47.opFillet","BLEND_FACE",FACE,{"disambiguationData":[OSD([subQ0,subQ7]),TDD([makeQuery(id+"F42.boolean.opBoolean","COPY",EDGE,{"disambiguationData":[TD([makeQuery(id+"F36.opLoft","SWEPT_FACE",FACE,{"disambiguationData":[OSD([sQuery(id+"F3.wireOp",EDGE,"E20.5.0"),subQ17,subQ16,sQuery(id+"F22.wireOp",EDGE,"E28.13.1"),subQ15,subQ14])]})])],"derivedFrom":subQ9})])]}),makeQuery(id+"F47.opFillet","BLEND_FACE",FACE,{"disambiguationData":[OSD([subQ0,subQ7]),TDD([makeQuery(id+"F42.boolean.opBoolean","COPY",EDGE,{"disambiguationData":[TD([makeQuery(id+"F37.opLoft","SWEPT_FACE",FACE,{"disambiguationData":[OSD([sQuery(id+"F3.wireOp",EDGE,"E20.6.0"),subQ13,subQ12,sQuery(id+"F22.wireOp",EDGE,"E28.14.1"),subQ11,subQ10])]})])],"derivedFrom":subQ9})])]}),makeQuery(id+"F47.opFillet","BLEND_FACE",FACE,{"disambiguationData":[OSD([subQ0,subQ7]),TDD([makeQuery(id+"F42.boolean.opBoolean","COPY",EDGE,{"disambiguationData":[TD([makeQuery(id+"F38.opLoft","SWEPT_FACE",FACE,{"disambiguationData":[OSD([sQuery(id+"F3.wireOp",EDGE,"E20.7.0"),subQ6,subQ5,sQuery(id+"F22.wireOp",EDGE,"E28.15.1"),subQ4,subQ3])]})])],"derivedFrom":subQ9})])]})],"blendedInto":[makeQuery(id+"F47.opFillet","BLEND_FACE",FACE,{"disambiguationData":[OSD([subQ0,subQ7]),TDD([makeQuery(id+"F42.boolean.opBoolean","COPY",EDGE,{"disambiguationData":[TD([makeQuery(id+"F23.opLoft","SWEPT_FACE",FACE,{"disambiguationData":[OSD([sQuery(id+"F3.wireOp",EDGE,"E20.8.0"),subQ71,subQ70,subQ69,subQ68,sQuery(id+"F22.wireOp",EDGE,"E27.right")])]})])],"derivedFrom":subQ9})])]}),makeQuery(id+"F47.opFillet","BLEND_FACE",FACE,{"disambiguationData":[OSD([subQ0,subQ7]),TDD([makeQuery(id+"F42.boolean.opBoolean","COPY",EDGE,{"disambiguationData":[TD([subQ67])],"derivedFrom":subQ9})])]}),makeQuery(id+"F47.opFillet","BLEND_FACE",FACE,{"disambiguationData":[OSD([subQ0,subQ7]),TDD([makeQuery(id+"F42.boolean.opBoolean","COPY",EDGE,{"disambiguationData":[TD([makeQuery(id+"F25.opLoft","SWEPT_FACE",FACE,{"disambiguationData":[OSD([sQuery(id+"F3.wireOp",EDGE,"E20.10.0"),subQ61,subQ60,sQuery(id+"F22.wireOp",EDGE,"E28.2.1"),subQ59,subQ58])]})])],"derivedFrom":subQ9})])]}),makeQuery(id+"F47.opFillet","BLEND_FACE",FACE,{"disambiguationData":[OSD([subQ0,subQ7]),TDD([makeQuery(id+"F42.boolean.opBoolean","COPY",EDGE,{"disambiguationData":[TD([makeQuery(id+"F26.opLoft","SWEPT_FACE",FACE,{"disambiguationData":[OSD([sQuery(id+"F3.wireOp",EDGE,"E20.11.0"),subQ57,subQ56,sQuery(id+"F22.wireOp",EDGE,"E28.3.1"),subQ55,subQ54])]})])],"derivedFrom":subQ9})])]}),makeQuery(id+"F47.opFillet","BLEND_FACE",FACE,{"disambiguationData":[OSD([subQ0,subQ7]),TDD([makeQuery(id+"F42.boolean.opBoolean","COPY",EDGE,{"disambiguationData":[TD([makeQuery(id+"F27.opLoft","SWEPT_FACE",FACE,{"disambiguationData":[OSD([sQuery(id+"F3.wireOp",EDGE,"E20.12.0"),subQ53,subQ52,sQuery(id+"F22.wireOp",EDGE,"E28.4.1"),subQ51,subQ50])]})])],"derivedFrom":subQ9})])]}),makeQuery(id+"F47.opFillet","BLEND_FACE",FACE,{"disambiguationData":[OSD([subQ0,subQ7]),TDD([makeQuery(id+"F42.boolean.opBoolean","COPY",EDGE,{"disambiguationData":[TD([makeQuery(id+"F28.opLoft","SWEPT_FACE",FACE,{"disambiguationData":[OSD([sQuery(id+"F3.wireOp",EDGE,"E20.13.0"),subQ49,subQ48,sQuery(id+"F22.wireOp",EDGE,"E28.5.1"),subQ47,subQ46])]})])],"derivedFrom":subQ9})])]}),makeQuery(id+"F47.opFillet","BLEND_FACE",FACE,{"disambiguationData":[OSD([subQ0,subQ7]),TDD([makeQuery(id+"F42.boolean.opBoolean","COPY",EDGE,{"disambiguationData":[TD([makeQuery(id+"F29.opLoft","SWEPT_FACE",FACE,{"disambiguationData":[OSD([sQuery(id+"F3.wireOp",EDGE,"E20.14.0"),subQ45,subQ44,sQuery(id+"F22.wireOp",EDGE,"E28.6.1"),subQ43,subQ42])]})])],"derivedFrom":subQ9})])]}),makeQuery(id+"F47.opFillet","BLEND_FACE",FACE,{"disambiguationData":[OSD([subQ0,subQ7]),TDD([makeQuery(id+"F42.boolean.opBoolean","COPY",EDGE,{"disambiguationData":[TD([makeQuery(id+"F30.opLoft","SWEPT_FACE",FACE,{"disambiguationData":[OSD([sQuery(id+"F3.wireOp",EDGE,"E20.15.0"),subQ41,subQ40,sQuery(id+"F22.wireOp",EDGE,"E28.7.1"),subQ39,subQ38])]})])],"derivedFrom":subQ9})])]}),makeQuery(id+"F47.opFillet","BLEND_FACE",FACE,{"disambiguationData":[OSD([subQ0,subQ7]),TDD([makeQuery(id+"F42.boolean.opBoolean","COPY",EDGE,{"disambiguationData":[TD([makeQuery(id+"F31.opLoft","SWEPT_FACE",FACE,{"disambiguationData":[OSD([subQ37,subQ36,sQuery(id+"F3.wireOp",EDGE,"E18.left"),sQuery(id+"F22.wireOp",EDGE,"E28.8.1"),subQ35,subQ34])]})])],"derivedFrom":subQ9})])]}),makeQuery(id+"F47.opFillet","BLEND_FACE",FACE,{"disambiguationData":[OSD([subQ0,subQ7]),TDD([makeQuery(id+"F42.boolean.opBoolean","COPY",EDGE,{"disambiguationData":[TD([makeQuery(id+"F32.opLoft","SWEPT_FACE",FACE,{"disambiguationData":[OSD([sQuery(id+"F3.wireOp",EDGE,"E20.1.0"),subQ33,subQ32,sQuery(id+"F22.wireOp",EDGE,"E28.9.1"),subQ31,subQ30])]})])],"derivedFrom":subQ9})])]}),makeQuery(id+"F47.opFillet","BLEND_FACE",FACE,{"disambiguationData":[OSD([subQ0,subQ7]),TDD([makeQuery(id+"F42.boolean.opBoolean","COPY",EDGE,{"disambiguationData":[TD([makeQuery(id+"F33.opLoft","SWEPT_FACE",FACE,{"disambiguationData":[OSD([sQuery(id+"F3.wireOp",EDGE,"E20.2.0"),subQ29,subQ28,sQuery(id+"F22.wireOp",EDGE,"E28.10.1"),subQ27,subQ26])]})])],"derivedFrom":subQ9})])]}),makeQuery(id+"F47.opFillet","BLEND_FACE",FACE,{"disambiguationData":[OSD([subQ0,subQ7]),TDD([makeQuery(id+"F42.boolean.opBoolean","COPY",EDGE,{"disambiguationData":[TD([makeQuery(id+"F34.opLoft","SWEPT_FACE",FACE,{"disambiguationData":[OSD([sQuery(id+"F3.wireOp",EDGE,"E20.3.0"),subQ25,subQ24,sQuery(id+"F22.wireOp",EDGE,"E28.11.1"),subQ23,subQ22])]})])],"derivedFrom":subQ9})])]}),makeQuery(id+"F47.opFillet","BLEND_FACE",FACE,{"disambiguationData":[OSD([subQ0,subQ7]),TDD([makeQuery(id+"F42.boolean.opBoolean","COPY",EDGE,{"disambiguationData":[TD([makeQuery(id+"F35.opLoft","SWEPT_FACE",FACE,{"disambiguationData":[OSD([sQuery(id+"F3.wireOp",EDGE,"E20.4.0"),subQ21,subQ20,sQuery(id+"F22.wireOp",EDGE,"E28.12.1"),subQ19,subQ18])]})])],"derivedFrom":subQ9})])]}),makeQuery(id+"F47.opFillet","BLEND_FACE",FACE,{"disambiguationData":[OSD([subQ0,subQ7]),TDD([makeQuery(id+"F42.boolean.opBoolean","COPY",EDGE,{"disambiguationData":[TD([makeQuery(id+"F36.opLoft","SWEPT_FACE",FACE,{"disambiguationData":[OSD([sQuery(id+"F3.wireOp",EDGE,"E20.5.0"),subQ17,subQ16,sQuery(id+"F22.wireOp",EDGE,"E28.13.1"),subQ15,subQ14])]})])],"derivedFrom":subQ9})])]}),makeQuery(id+"F47.opFillet","BLEND_FACE",FACE,{"disambiguationData":[OSD([subQ0,subQ7]),TDD([makeQuery(id+"F42.boolean.opBoolean","COPY",EDGE,{"disambiguationData":[TD([makeQuery(id+"F37.opLoft","SWEPT_FACE",FACE,{"disambiguationData":[OSD([sQuery(id+"F3.wireOp",EDGE,"E20.6.0"),subQ13,subQ12,sQuery(id+"F22.wireOp",EDGE,"E28.14.1"),subQ11,subQ10])]})])],"derivedFrom":subQ9})])]}),makeQuery(id+"F47.opFillet","BLEND_FACE",FACE,{"disambiguationData":[OSD([subQ0,subQ7]),TDD([makeQuery(id+"F42.boolean.opBoolean","COPY",EDGE,{"disambiguationData":[TD([makeQuery(id+"F38.opLoft","SWEPT_FACE",FACE,{"disambiguationData":[OSD([sQuery(id+"F3.wireOp",EDGE,"E20.7.0"),subQ6,subQ5,sQuery(id+"F22.wireOp",EDGE,"E28.15.1"),subQ4,subQ3])]})])],"derivedFrom":subQ9})])]})]});}
            var Q39;
            {var subQ0=sQuery(id+"F22.wireOp",EDGE,"E28.1.0");var subQ1=sQuery(id+"F22.wireOp",EDGE,"E28.1.1");var subQ2=sQuery(id+"F22.wireOp",EDGE,"E28.1.2");var subQ3=sQuery(id+"F22.wireOp",EDGE,"E28.1.3");var subQ4=sQuery(id+"F3.wireOp",EDGE,"E20.9.3");var subQ5=sQuery(id+"F3.wireOp",EDGE,"E20.9.1");var subQ6=makeQuery(id+"F24.opLoft","SWEPT_FACE",FACE,{"disambiguationData":[OSD([subQ5,sQuery(id+"F3.wireOp",EDGE,"E20.9.2"),subQ4,subQ0,subQ2,subQ3])]});var subQ7=sQuery(id+"F41.wireOp",EDGE,"E34");var subQ8=sQuery(id+"F41.wireOp",EDGE,"E32");Q39=makeQuery(id+"F44.opFillet","BLEND_EDGE",EDGE,{"blendedFrom":[makeQuery(id+"F40.boolean.opBoolean","INTERSECT",EDGE,{"derivedFrom":[subQ6,makeQuery(id+"F40.opExtrude","CAP_FACE",FACE,{"disambiguationData":[OSD([sQuery(id+"F39.wireOp",EDGE,"E29"),sQuery(id+"F39.wireOp",EDGE,"E30")])],"isStart":true})]}),makeQuery(id+"F42.boolean.opBoolean","COPY",FACE,{"disambiguationData":[TD([makeQuery(id+"F24.opLoft","SWEPT_FACE",FACE,{"disambiguationData":[OSD([sQuery(id+"F3.wireOp",EDGE,"E20.9.0"),subQ5,subQ4,subQ1,subQ2,subQ3])]})])],"derivedFrom":makeQuery(id+"F42.opRevolve","SWEPT_FACE",FACE,{"disambiguationData":[OSD([subQ8]),TDD([makeQuery(id+"F41.imprint","IMPRINT",EDGE,{"disambiguationData":[TD([[makeQuery(id+"F41.imprint","INTERSECT",VERTEX,{"disambiguationData":[OD(0.0)],"derivedFrom":[subQ8,subQ7]}),-1.0]])],"derivedFrom":subQ8})])]})})],"blendedInto":[makeQuery(id+"F42.boolean.opBoolean","COPY",FACE,{"disambiguationData":[TD([makeQuery(id+"F24.opLoft","SWEPT_FACE",FACE,{"disambiguationData":[OSD([sQuery(id+"F3.wireOp",EDGE,"E20.9.0"),subQ5,subQ4,subQ1,subQ2,subQ3])]})])],"derivedFrom":makeQuery(id+"F42.opRevolve","SWEPT_FACE",FACE,{"disambiguationData":[OSD([subQ8]),TDD([makeQuery(id+"F41.imprint","IMPRINT",EDGE,{"disambiguationData":[TD([[makeQuery(id+"F41.imprint","INTERSECT",VERTEX,{"disambiguationData":[OD(0.0)],"derivedFrom":[subQ8,subQ7]}),-1.0]])],"derivedFrom":subQ8})])]})})]});}
            var Q40;
            {var subQ0=sQuery(id+"F41.wireOp",EDGE,"E34");var subQ1=sQuery(id+"F41.wireOp",EDGE,"E32");Q40=makeQuery(id+"F42.boolean.opBoolean","INTERSECT",EDGE,{"derivedFrom":[makeQuery(id+"F23.opLoft","SWEPT_FACE",FACE,{"disambiguationData":[OSD([sQuery(id+"F3.wireOp",EDGE,"E20.8.0"),sQuery(id+"F3.wireOp",EDGE,"E20.8.1"),sQuery(id+"F3.wireOp",EDGE,"E20.8.3"),sQuery(id+"F22.wireOp",EDGE,"E27.bottom"),sQuery(id+"F22.wireOp",EDGE,"E27.top"),sQuery(id+"F22.wireOp",EDGE,"E27.right")])]}),makeQuery(id+"F42.opRevolve","SWEPT_FACE",FACE,{"disambiguationData":[OSD([subQ1]),TDD([makeQuery(id+"F41.imprint","IMPRINT",EDGE,{"disambiguationData":[TD([[makeQuery(id+"F41.imprint","INTERSECT",VERTEX,{"disambiguationData":[OD(0.0)],"derivedFrom":[subQ1,subQ0]}),-1.0]])],"derivedFrom":subQ1})])]})]});}
            var Q41;
            {var subQ0=sQuery(id+"F41.wireOp",EDGE,"E37");var subQ1=makeQuery(id+"F42.opRevolve","SWEPT_FACE",FACE,{"disambiguationData":[OSD([subQ0])]});var subQ2=makeQuery(id+"F40.opExtrude","CAP_FACE",FACE,{"disambiguationData":[OSD([sQuery(id+"F39.wireOp",EDGE,"E29"),sQuery(id+"F39.wireOp",EDGE,"E30")])],"isStart":true});var subQ3=sQuery(id+"F22.wireOp",EDGE,"E28.15.3");var subQ4=sQuery(id+"F22.wireOp",EDGE,"E28.15.2");var subQ5=sQuery(id+"F3.wireOp",EDGE,"E20.7.3");var subQ6=sQuery(id+"F3.wireOp",EDGE,"E20.7.1");var subQ7=sQuery(id+"F41.wireOp",EDGE,"E38");var subQ8=makeQuery(id+"F42.opRevolve","SWEPT_FACE",FACE,{"disambiguationData":[OSD([subQ7])]});var subQ9=makeQuery(id+"F42.opRevolve","SWEPT_EDGE",EDGE,{"disambiguationData":[OSD([subQ0,subQ7])]});var subQ10=sQuery(id+"F22.wireOp",EDGE,"E28.14.3");var subQ11=sQuery(id+"F22.wireOp",EDGE,"E28.14.2");var subQ12=sQuery(id+"F3.wireOp",EDGE,"E20.6.3");var subQ13=sQuery(id+"F3.wireOp",EDGE,"E20.6.1");var subQ14=sQuery(id+"F22.wireOp",EDGE,"E28.13.3");var subQ15=sQuery(id+"F22.wireOp",EDGE,"E28.13.2");var subQ16=sQuery(id+"F3.wireOp",EDGE,"E20.5.3");var subQ17=sQuery(id+"F3.wireOp",EDGE,"E20.5.1");var subQ18=sQuery(id+"F22.wireOp",EDGE,"E28.12.3");var subQ19=sQuery(id+"F22.wireOp",EDGE,"E28.12.2");var subQ20=sQuery(id+"F3.wireOp",EDGE,"E20.4.3");var subQ21=sQuery(id+"F3.wireOp",EDGE,"E20.4.1");var subQ22=sQuery(id+"F22.wireOp",EDGE,"E28.11.3");var subQ23=sQuery(id+"F22.wireOp",EDGE,"E28.11.2");var subQ24=sQuery(id+"F3.wireOp",EDGE,"E20.3.3");var subQ25=sQuery(id+"F3.wireOp",EDGE,"E20.3.1");var subQ26=sQuery(id+"F22.wireOp",EDGE,"E28.10.3");var subQ27=sQuery(id+"F22.wireOp",EDGE,"E28.10.2");var subQ28=sQuery(id+"F3.wireOp",EDGE,"E20.2.3");var subQ29=sQuery(id+"F3.wireOp",EDGE,"E20.2.1");var subQ30=sQuery(id+"F22.wireOp",EDGE,"E28.9.3");var subQ31=sQuery(id+"F22.wireOp",EDGE,"E28.9.2");var subQ32=sQuery(id+"F3.wireOp",EDGE,"E20.1.3");var subQ33=sQuery(id+"F3.wireOp",EDGE,"E20.1.1");var subQ34=sQuery(id+"F22.wireOp",EDGE,"E28.8.3");var subQ35=sQuery(id+"F22.wireOp",EDGE,"E28.8.2");var subQ36=sQuery(id+"F3.wireOp",EDGE,"E18.top");var subQ37=sQuery(id+"F3.wireOp",EDGE,"E18.bottom");var subQ38=sQuery(id+"F22.wireOp",EDGE,"E28.7.3");var subQ39=sQuery(id+"F22.wireOp",EDGE,"E28.7.2");var subQ40=sQuery(id+"F3.wireOp",EDGE,"E20.15.3");var subQ41=sQuery(id+"F3.wireOp",EDGE,"E20.15.1");var subQ42=sQuery(id+"F22.wireOp",EDGE,"E28.6.3");var subQ43=sQuery(id+"F22.wireOp",EDGE,"E28.6.2");var subQ44=sQuery(id+"F3.wireOp",EDGE,"E20.14.3");var subQ45=sQuery(id+"F3.wireOp",EDGE,"E20.14.1");var subQ46=sQuery(id+"F22.wireOp",EDGE,"E28.5.3");var subQ47=sQuery(id+"F22.wireOp",EDGE,"E28.5.2");var subQ48=sQuery(id+"F3.wireOp",EDGE,"E20.13.3");var subQ49=sQuery(id+"F3.wireOp",EDGE,"E20.13.1");var subQ50=sQuery(id+"F22.wireOp",EDGE,"E28.4.3");var subQ51=sQuery(id+"F22.wireOp",EDGE,"E28.4.2");var subQ52=sQuery(id+"F3.wireOp",EDGE,"E20.12.3");var subQ53=sQuery(id+"F3.wireOp",EDGE,"E20.12.1");var subQ54=sQuery(id+"F22.wireOp",EDGE,"E28.3.3");var subQ55=sQuery(id+"F22.wireOp",EDGE,"E28.3.2");var subQ56=sQuery(id+"F3.wireOp",EDGE,"E20.11.3");var subQ57=sQuery(id+"F3.wireOp",EDGE,"E20.11.1");var subQ58=sQuery(id+"F22.wireOp",EDGE,"E28.2.3");var subQ59=sQuery(id+"F22.wireOp",EDGE,"E28.2.2");var subQ60=sQuery(id+"F3.wireOp",EDGE,"E20.10.3");var subQ61=sQuery(id+"F3.wireOp",EDGE,"E20.10.1");var subQ62=sQuery(id+"F22.wireOp",EDGE,"E28.1.3");var subQ63=sQuery(id+"F22.wireOp",EDGE,"E28.1.2");var subQ64=sQuery(id+"F3.wireOp",EDGE,"E20.9.3");var subQ65=sQuery(id+"F3.wireOp",EDGE,"E20.9.1");var subQ66=sQuery(id+"F22.wireOp",EDGE,"E27.top");var subQ67=sQuery(id+"F22.wireOp",EDGE,"E27.bottom");var subQ68=sQuery(id+"F3.wireOp",EDGE,"E20.8.3");var subQ69=sQuery(id+"F3.wireOp",EDGE,"E20.8.1");var subQ71=makeQuery(id+"F23.opLoft","SWEPT_FACE",FACE,{"disambiguationData":[OSD([sQuery(id+"F3.wireOp",EDGE,"E20.8.0"),subQ69,subQ68,subQ67,subQ66,sQuery(id+"F22.wireOp",EDGE,"E27.right")])]});var subQ74=makeQuery(id+"F42.boolean.opBoolean","COPY",FACE,{"disambiguationData":[TD([subQ71])],"derivedFrom":subQ8});var subQ75=makeQuery(id+"F23.boolean.opBoolean","INTERSECT",EDGE,{"derivedFrom":[makeQuery(id+"F1.opRevolve","SWEPT_FACE",FACE,{"disambiguationData":[OSD([sQuery(id+"F0.wireOp",EDGE,"E4")])]}),subQ71]});Q41=makeQuery(id+"F48.opFillet","BLEND_EDGE",EDGE,{"blendedFrom":[makeQuery(id+"F47.opFillet","TWEAK_EDGE",EDGE,{"derivedFrom":[makeQuery(id+"F45.opFillet","BLEND_VERTEX",VERTEX,{"blendedFrom":[subQ75,subQ71,subQ74],"blendedInto":[subQ71,subQ74]}),makeQuery(id+"F45.opFillet","BLEND_VERTEX",VERTEX,{"blendedFrom":[subQ75,makeQuery(id+"F42.boolean.opBoolean","MERGE",FACE,{"derivedFrom":[subQ2,subQ1]}),subQ74],"blendedInto":[makeQuery(id+"F42.boolean.opBoolean","MERGE",FACE,{"derivedFrom":[subQ2,subQ1]}),subQ74]})]}),makeQuery(id+"F47.opFillet","BLEND_FACE",FACE,{"disambiguationData":[OSD([subQ0,subQ7]),TDD([makeQuery(id+"F42.boolean.opBoolean","COPY",EDGE,{"disambiguationData":[TD([subQ71])],"derivedFrom":subQ9})])]}),makeQuery(id+"F47.opFillet","BLEND_FACE",FACE,{"disambiguationData":[OSD([subQ0,subQ7]),TDD([makeQuery(id+"F42.boolean.opBoolean","COPY",EDGE,{"disambiguationData":[TD([makeQuery(id+"F24.opLoft","SWEPT_FACE",FACE,{"disambiguationData":[OSD([sQuery(id+"F3.wireOp",EDGE,"E20.9.0"),subQ65,subQ64,sQuery(id+"F22.wireOp",EDGE,"E28.1.1"),subQ63,subQ62])]})])],"derivedFrom":subQ9})])]}),makeQuery(id+"F47.opFillet","BLEND_FACE",FACE,{"disambiguationData":[OSD([subQ0,subQ7]),TDD([makeQuery(id+"F42.boolean.opBoolean","COPY",EDGE,{"disambiguationData":[TD([makeQuery(id+"F25.opLoft","SWEPT_FACE",FACE,{"disambiguationData":[OSD([sQuery(id+"F3.wireOp",EDGE,"E20.10.0"),subQ61,subQ60,sQuery(id+"F22.wireOp",EDGE,"E28.2.1"),subQ59,subQ58])]})])],"derivedFrom":subQ9})])]}),makeQuery(id+"F47.opFillet","BLEND_FACE",FACE,{"disambiguationData":[OSD([subQ0,subQ7]),TDD([makeQuery(id+"F42.boolean.opBoolean","COPY",EDGE,{"disambiguationData":[TD([makeQuery(id+"F26.opLoft","SWEPT_FACE",FACE,{"disambiguationData":[OSD([sQuery(id+"F3.wireOp",EDGE,"E20.11.0"),subQ57,subQ56,sQuery(id+"F22.wireOp",EDGE,"E28.3.1"),subQ55,subQ54])]})])],"derivedFrom":subQ9})])]}),makeQuery(id+"F47.opFillet","BLEND_FACE",FACE,{"disambiguationData":[OSD([subQ0,subQ7]),TDD([makeQuery(id+"F42.boolean.opBoolean","COPY",EDGE,{"disambiguationData":[TD([makeQuery(id+"F27.opLoft","SWEPT_FACE",FACE,{"disambiguationData":[OSD([sQuery(id+"F3.wireOp",EDGE,"E20.12.0"),subQ53,subQ52,sQuery(id+"F22.wireOp",EDGE,"E28.4.1"),subQ51,subQ50])]})])],"derivedFrom":subQ9})])]}),makeQuery(id+"F47.opFillet","BLEND_FACE",FACE,{"disambiguationData":[OSD([subQ0,subQ7]),TDD([makeQuery(id+"F42.boolean.opBoolean","COPY",EDGE,{"disambiguationData":[TD([makeQuery(id+"F28.opLoft","SWEPT_FACE",FACE,{"disambiguationData":[OSD([sQuery(id+"F3.wireOp",EDGE,"E20.13.0"),subQ49,subQ48,sQuery(id+"F22.wireOp",EDGE,"E28.5.1"),subQ47,subQ46])]})])],"derivedFrom":subQ9})])]}),makeQuery(id+"F47.opFillet","BLEND_FACE",FACE,{"disambiguationData":[OSD([subQ0,subQ7]),TDD([makeQuery(id+"F42.boolean.opBoolean","COPY",EDGE,{"disambiguationData":[TD([makeQuery(id+"F29.opLoft","SWEPT_FACE",FACE,{"disambiguationData":[OSD([sQuery(id+"F3.wireOp",EDGE,"E20.14.0"),subQ45,subQ44,sQuery(id+"F22.wireOp",EDGE,"E28.6.1"),subQ43,subQ42])]})])],"derivedFrom":subQ9})])]}),makeQuery(id+"F47.opFillet","BLEND_FACE",FACE,{"disambiguationData":[OSD([subQ0,subQ7]),TDD([makeQuery(id+"F42.boolean.opBoolean","COPY",EDGE,{"disambiguationData":[TD([makeQuery(id+"F30.opLoft","SWEPT_FACE",FACE,{"disambiguationData":[OSD([sQuery(id+"F3.wireOp",EDGE,"E20.15.0"),subQ41,subQ40,sQuery(id+"F22.wireOp",EDGE,"E28.7.1"),subQ39,subQ38])]})])],"derivedFrom":subQ9})])]}),makeQuery(id+"F47.opFillet","BLEND_FACE",FACE,{"disambiguationData":[OSD([subQ0,subQ7]),TDD([makeQuery(id+"F42.boolean.opBoolean","COPY",EDGE,{"disambiguationData":[TD([makeQuery(id+"F31.opLoft","SWEPT_FACE",FACE,{"disambiguationData":[OSD([subQ37,subQ36,sQuery(id+"F3.wireOp",EDGE,"E18.left"),sQuery(id+"F22.wireOp",EDGE,"E28.8.1"),subQ35,subQ34])]})])],"derivedFrom":subQ9})])]}),makeQuery(id+"F47.opFillet","BLEND_FACE",FACE,{"disambiguationData":[OSD([subQ0,subQ7]),TDD([makeQuery(id+"F42.boolean.opBoolean","COPY",EDGE,{"disambiguationData":[TD([makeQuery(id+"F32.opLoft","SWEPT_FACE",FACE,{"disambiguationData":[OSD([sQuery(id+"F3.wireOp",EDGE,"E20.1.0"),subQ33,subQ32,sQuery(id+"F22.wireOp",EDGE,"E28.9.1"),subQ31,subQ30])]})])],"derivedFrom":subQ9})])]}),makeQuery(id+"F47.opFillet","BLEND_FACE",FACE,{"disambiguationData":[OSD([subQ0,subQ7]),TDD([makeQuery(id+"F42.boolean.opBoolean","COPY",EDGE,{"disambiguationData":[TD([makeQuery(id+"F33.opLoft","SWEPT_FACE",FACE,{"disambiguationData":[OSD([sQuery(id+"F3.wireOp",EDGE,"E20.2.0"),subQ29,subQ28,sQuery(id+"F22.wireOp",EDGE,"E28.10.1"),subQ27,subQ26])]})])],"derivedFrom":subQ9})])]}),makeQuery(id+"F47.opFillet","BLEND_FACE",FACE,{"disambiguationData":[OSD([subQ0,subQ7]),TDD([makeQuery(id+"F42.boolean.opBoolean","COPY",EDGE,{"disambiguationData":[TD([makeQuery(id+"F34.opLoft","SWEPT_FACE",FACE,{"disambiguationData":[OSD([sQuery(id+"F3.wireOp",EDGE,"E20.3.0"),subQ25,subQ24,sQuery(id+"F22.wireOp",EDGE,"E28.11.1"),subQ23,subQ22])]})])],"derivedFrom":subQ9})])]}),makeQuery(id+"F47.opFillet","BLEND_FACE",FACE,{"disambiguationData":[OSD([subQ0,subQ7]),TDD([makeQuery(id+"F42.boolean.opBoolean","COPY",EDGE,{"disambiguationData":[TD([makeQuery(id+"F35.opLoft","SWEPT_FACE",FACE,{"disambiguationData":[OSD([sQuery(id+"F3.wireOp",EDGE,"E20.4.0"),subQ21,subQ20,sQuery(id+"F22.wireOp",EDGE,"E28.12.1"),subQ19,subQ18])]})])],"derivedFrom":subQ9})])]}),makeQuery(id+"F47.opFillet","BLEND_FACE",FACE,{"disambiguationData":[OSD([subQ0,subQ7]),TDD([makeQuery(id+"F42.boolean.opBoolean","COPY",EDGE,{"disambiguationData":[TD([makeQuery(id+"F36.opLoft","SWEPT_FACE",FACE,{"disambiguationData":[OSD([sQuery(id+"F3.wireOp",EDGE,"E20.5.0"),subQ17,subQ16,sQuery(id+"F22.wireOp",EDGE,"E28.13.1"),subQ15,subQ14])]})])],"derivedFrom":subQ9})])]}),makeQuery(id+"F47.opFillet","BLEND_FACE",FACE,{"disambiguationData":[OSD([subQ0,subQ7]),TDD([makeQuery(id+"F42.boolean.opBoolean","COPY",EDGE,{"disambiguationData":[TD([makeQuery(id+"F37.opLoft","SWEPT_FACE",FACE,{"disambiguationData":[OSD([sQuery(id+"F3.wireOp",EDGE,"E20.6.0"),subQ13,subQ12,sQuery(id+"F22.wireOp",EDGE,"E28.14.1"),subQ11,subQ10])]})])],"derivedFrom":subQ9})])]}),makeQuery(id+"F47.opFillet","BLEND_FACE",FACE,{"disambiguationData":[OSD([subQ0,subQ7]),TDD([makeQuery(id+"F42.boolean.opBoolean","COPY",EDGE,{"disambiguationData":[TD([makeQuery(id+"F38.opLoft","SWEPT_FACE",FACE,{"disambiguationData":[OSD([sQuery(id+"F3.wireOp",EDGE,"E20.7.0"),subQ6,subQ5,sQuery(id+"F22.wireOp",EDGE,"E28.15.1"),subQ4,subQ3])]})])],"derivedFrom":subQ9})])]})],"blendedInto":[makeQuery(id+"F47.opFillet","BLEND_FACE",FACE,{"disambiguationData":[OSD([subQ0,subQ7]),TDD([makeQuery(id+"F42.boolean.opBoolean","COPY",EDGE,{"disambiguationData":[TD([subQ71])],"derivedFrom":subQ9})])]}),makeQuery(id+"F47.opFillet","BLEND_FACE",FACE,{"disambiguationData":[OSD([subQ0,subQ7]),TDD([makeQuery(id+"F42.boolean.opBoolean","COPY",EDGE,{"disambiguationData":[TD([makeQuery(id+"F24.opLoft","SWEPT_FACE",FACE,{"disambiguationData":[OSD([sQuery(id+"F3.wireOp",EDGE,"E20.9.0"),subQ65,subQ64,sQuery(id+"F22.wireOp",EDGE,"E28.1.1"),subQ63,subQ62])]})])],"derivedFrom":subQ9})])]}),makeQuery(id+"F47.opFillet","BLEND_FACE",FACE,{"disambiguationData":[OSD([subQ0,subQ7]),TDD([makeQuery(id+"F42.boolean.opBoolean","COPY",EDGE,{"disambiguationData":[TD([makeQuery(id+"F25.opLoft","SWEPT_FACE",FACE,{"disambiguationData":[OSD([sQuery(id+"F3.wireOp",EDGE,"E20.10.0"),subQ61,subQ60,sQuery(id+"F22.wireOp",EDGE,"E28.2.1"),subQ59,subQ58])]})])],"derivedFrom":subQ9})])]}),makeQuery(id+"F47.opFillet","BLEND_FACE",FACE,{"disambiguationData":[OSD([subQ0,subQ7]),TDD([makeQuery(id+"F42.boolean.opBoolean","COPY",EDGE,{"disambiguationData":[TD([makeQuery(id+"F26.opLoft","SWEPT_FACE",FACE,{"disambiguationData":[OSD([sQuery(id+"F3.wireOp",EDGE,"E20.11.0"),subQ57,subQ56,sQuery(id+"F22.wireOp",EDGE,"E28.3.1"),subQ55,subQ54])]})])],"derivedFrom":subQ9})])]}),makeQuery(id+"F47.opFillet","BLEND_FACE",FACE,{"disambiguationData":[OSD([subQ0,subQ7]),TDD([makeQuery(id+"F42.boolean.opBoolean","COPY",EDGE,{"disambiguationData":[TD([makeQuery(id+"F27.opLoft","SWEPT_FACE",FACE,{"disambiguationData":[OSD([sQuery(id+"F3.wireOp",EDGE,"E20.12.0"),subQ53,subQ52,sQuery(id+"F22.wireOp",EDGE,"E28.4.1"),subQ51,subQ50])]})])],"derivedFrom":subQ9})])]}),makeQuery(id+"F47.opFillet","BLEND_FACE",FACE,{"disambiguationData":[OSD([subQ0,subQ7]),TDD([makeQuery(id+"F42.boolean.opBoolean","COPY",EDGE,{"disambiguationData":[TD([makeQuery(id+"F28.opLoft","SWEPT_FACE",FACE,{"disambiguationData":[OSD([sQuery(id+"F3.wireOp",EDGE,"E20.13.0"),subQ49,subQ48,sQuery(id+"F22.wireOp",EDGE,"E28.5.1"),subQ47,subQ46])]})])],"derivedFrom":subQ9})])]}),makeQuery(id+"F47.opFillet","BLEND_FACE",FACE,{"disambiguationData":[OSD([subQ0,subQ7]),TDD([makeQuery(id+"F42.boolean.opBoolean","COPY",EDGE,{"disambiguationData":[TD([makeQuery(id+"F29.opLoft","SWEPT_FACE",FACE,{"disambiguationData":[OSD([sQuery(id+"F3.wireOp",EDGE,"E20.14.0"),subQ45,subQ44,sQuery(id+"F22.wireOp",EDGE,"E28.6.1"),subQ43,subQ42])]})])],"derivedFrom":subQ9})])]}),makeQuery(id+"F47.opFillet","BLEND_FACE",FACE,{"disambiguationData":[OSD([subQ0,subQ7]),TDD([makeQuery(id+"F42.boolean.opBoolean","COPY",EDGE,{"disambiguationData":[TD([makeQuery(id+"F30.opLoft","SWEPT_FACE",FACE,{"disambiguationData":[OSD([sQuery(id+"F3.wireOp",EDGE,"E20.15.0"),subQ41,subQ40,sQuery(id+"F22.wireOp",EDGE,"E28.7.1"),subQ39,subQ38])]})])],"derivedFrom":subQ9})])]}),makeQuery(id+"F47.opFillet","BLEND_FACE",FACE,{"disambiguationData":[OSD([subQ0,subQ7]),TDD([makeQuery(id+"F42.boolean.opBoolean","COPY",EDGE,{"disambiguationData":[TD([makeQuery(id+"F31.opLoft","SWEPT_FACE",FACE,{"disambiguationData":[OSD([subQ37,subQ36,sQuery(id+"F3.wireOp",EDGE,"E18.left"),sQuery(id+"F22.wireOp",EDGE,"E28.8.1"),subQ35,subQ34])]})])],"derivedFrom":subQ9})])]}),makeQuery(id+"F47.opFillet","BLEND_FACE",FACE,{"disambiguationData":[OSD([subQ0,subQ7]),TDD([makeQuery(id+"F42.boolean.opBoolean","COPY",EDGE,{"disambiguationData":[TD([makeQuery(id+"F32.opLoft","SWEPT_FACE",FACE,{"disambiguationData":[OSD([sQuery(id+"F3.wireOp",EDGE,"E20.1.0"),subQ33,subQ32,sQuery(id+"F22.wireOp",EDGE,"E28.9.1"),subQ31,subQ30])]})])],"derivedFrom":subQ9})])]}),makeQuery(id+"F47.opFillet","BLEND_FACE",FACE,{"disambiguationData":[OSD([subQ0,subQ7]),TDD([makeQuery(id+"F42.boolean.opBoolean","COPY",EDGE,{"disambiguationData":[TD([makeQuery(id+"F33.opLoft","SWEPT_FACE",FACE,{"disambiguationData":[OSD([sQuery(id+"F3.wireOp",EDGE,"E20.2.0"),subQ29,subQ28,sQuery(id+"F22.wireOp",EDGE,"E28.10.1"),subQ27,subQ26])]})])],"derivedFrom":subQ9})])]}),makeQuery(id+"F47.opFillet","BLEND_FACE",FACE,{"disambiguationData":[OSD([subQ0,subQ7]),TDD([makeQuery(id+"F42.boolean.opBoolean","COPY",EDGE,{"disambiguationData":[TD([makeQuery(id+"F34.opLoft","SWEPT_FACE",FACE,{"disambiguationData":[OSD([sQuery(id+"F3.wireOp",EDGE,"E20.3.0"),subQ25,subQ24,sQuery(id+"F22.wireOp",EDGE,"E28.11.1"),subQ23,subQ22])]})])],"derivedFrom":subQ9})])]}),makeQuery(id+"F47.opFillet","BLEND_FACE",FACE,{"disambiguationData":[OSD([subQ0,subQ7]),TDD([makeQuery(id+"F42.boolean.opBoolean","COPY",EDGE,{"disambiguationData":[TD([makeQuery(id+"F35.opLoft","SWEPT_FACE",FACE,{"disambiguationData":[OSD([sQuery(id+"F3.wireOp",EDGE,"E20.4.0"),subQ21,subQ20,sQuery(id+"F22.wireOp",EDGE,"E28.12.1"),subQ19,subQ18])]})])],"derivedFrom":subQ9})])]}),makeQuery(id+"F47.opFillet","BLEND_FACE",FACE,{"disambiguationData":[OSD([subQ0,subQ7]),TDD([makeQuery(id+"F42.boolean.opBoolean","COPY",EDGE,{"disambiguationData":[TD([makeQuery(id+"F36.opLoft","SWEPT_FACE",FACE,{"disambiguationData":[OSD([sQuery(id+"F3.wireOp",EDGE,"E20.5.0"),subQ17,subQ16,sQuery(id+"F22.wireOp",EDGE,"E28.13.1"),subQ15,subQ14])]})])],"derivedFrom":subQ9})])]}),makeQuery(id+"F47.opFillet","BLEND_FACE",FACE,{"disambiguationData":[OSD([subQ0,subQ7]),TDD([makeQuery(id+"F42.boolean.opBoolean","COPY",EDGE,{"disambiguationData":[TD([makeQuery(id+"F37.opLoft","SWEPT_FACE",FACE,{"disambiguationData":[OSD([sQuery(id+"F3.wireOp",EDGE,"E20.6.0"),subQ13,subQ12,sQuery(id+"F22.wireOp",EDGE,"E28.14.1"),subQ11,subQ10])]})])],"derivedFrom":subQ9})])]}),makeQuery(id+"F47.opFillet","BLEND_FACE",FACE,{"disambiguationData":[OSD([subQ0,subQ7]),TDD([makeQuery(id+"F42.boolean.opBoolean","COPY",EDGE,{"disambiguationData":[TD([makeQuery(id+"F38.opLoft","SWEPT_FACE",FACE,{"disambiguationData":[OSD([sQuery(id+"F3.wireOp",EDGE,"E20.7.0"),subQ6,subQ5,sQuery(id+"F22.wireOp",EDGE,"E28.15.1"),subQ4,subQ3])]})])],"derivedFrom":subQ9})])]})]});}
            var Q42;
            {var subQ0=sQuery(id+"F22.wireOp",EDGE,"E27.left");var subQ1=sQuery(id+"F22.wireOp",EDGE,"E27.top");var subQ2=sQuery(id+"F22.wireOp",EDGE,"E27.bottom");var subQ3=sQuery(id+"F3.wireOp",EDGE,"E20.8.3");var subQ4=sQuery(id+"F3.wireOp",EDGE,"E20.8.1");var subQ5=makeQuery(id+"F23.opLoft","SWEPT_FACE",FACE,{"disambiguationData":[OSD([subQ4,sQuery(id+"F3.wireOp",EDGE,"E20.8.2"),subQ3,subQ2,subQ1,subQ0])]});var subQ6=sQuery(id+"F22.wireOp",EDGE,"E27.right");var subQ7=sQuery(id+"F41.wireOp",EDGE,"E34");var subQ8=sQuery(id+"F41.wireOp",EDGE,"E32");Q42=makeQuery(id+"F44.opFillet","BLEND_EDGE",EDGE,{"blendedFrom":[makeQuery(id+"F40.boolean.opBoolean","INTERSECT",EDGE,{"derivedFrom":[subQ5,makeQuery(id+"F40.opExtrude","CAP_FACE",FACE,{"disambiguationData":[OSD([sQuery(id+"F39.wireOp",EDGE,"E29"),sQuery(id+"F39.wireOp",EDGE,"E30")])],"isStart":true})]}),makeQuery(id+"F42.boolean.opBoolean","COPY",FACE,{"disambiguationData":[TD([makeQuery(id+"F23.opLoft","SWEPT_FACE",FACE,{"disambiguationData":[OSD([sQuery(id+"F3.wireOp",EDGE,"E20.8.0"),subQ4,subQ3,subQ2,subQ1,subQ6])]})])],"derivedFrom":makeQuery(id+"F42.opRevolve","SWEPT_FACE",FACE,{"disambiguationData":[OSD([subQ8]),TDD([makeQuery(id+"F41.imprint","IMPRINT",EDGE,{"disambiguationData":[TD([[makeQuery(id+"F41.imprint","INTERSECT",VERTEX,{"disambiguationData":[OD(0.0)],"derivedFrom":[subQ8,subQ7]}),-1.0]])],"derivedFrom":subQ8})])]})})],"blendedInto":[makeQuery(id+"F42.boolean.opBoolean","COPY",FACE,{"disambiguationData":[TD([makeQuery(id+"F23.opLoft","SWEPT_FACE",FACE,{"disambiguationData":[OSD([sQuery(id+"F3.wireOp",EDGE,"E20.8.0"),subQ4,subQ3,subQ2,subQ1,subQ6])]})])],"derivedFrom":makeQuery(id+"F42.opRevolve","SWEPT_FACE",FACE,{"disambiguationData":[OSD([subQ8]),TDD([makeQuery(id+"F41.imprint","IMPRINT",EDGE,{"disambiguationData":[TD([[makeQuery(id+"F41.imprint","INTERSECT",VERTEX,{"disambiguationData":[OD(0.0)],"derivedFrom":[subQ8,subQ7]}),-1.0]])],"derivedFrom":subQ8})])]})})]});}
            var Q43;
            {var subQ0=sQuery(id+"F41.wireOp",EDGE,"E34");var subQ1=sQuery(id+"F41.wireOp",EDGE,"E32");Q43=makeQuery(id+"F42.boolean.opBoolean","INTERSECT",EDGE,{"derivedFrom":[makeQuery(id+"F38.opLoft","SWEPT_FACE",FACE,{"disambiguationData":[OSD([sQuery(id+"F3.wireOp",EDGE,"E20.7.0"),sQuery(id+"F3.wireOp",EDGE,"E20.7.1"),sQuery(id+"F3.wireOp",EDGE,"E20.7.3"),sQuery(id+"F22.wireOp",EDGE,"E28.15.1"),sQuery(id+"F22.wireOp",EDGE,"E28.15.2"),sQuery(id+"F22.wireOp",EDGE,"E28.15.3")])]}),makeQuery(id+"F42.opRevolve","SWEPT_FACE",FACE,{"disambiguationData":[OSD([subQ1]),TDD([makeQuery(id+"F41.imprint","IMPRINT",EDGE,{"disambiguationData":[TD([[makeQuery(id+"F41.imprint","INTERSECT",VERTEX,{"disambiguationData":[OD(0.0)],"derivedFrom":[subQ1,subQ0]}),-1.0]])],"derivedFrom":subQ1})])]})]});}
            var Q44;
            {var subQ0=sQuery(id+"F41.wireOp",EDGE,"E37");var subQ1=makeQuery(id+"F42.opRevolve","SWEPT_FACE",FACE,{"disambiguationData":[OSD([subQ0])]});var subQ2=makeQuery(id+"F40.opExtrude","CAP_FACE",FACE,{"disambiguationData":[OSD([sQuery(id+"F39.wireOp",EDGE,"E29"),sQuery(id+"F39.wireOp",EDGE,"E30")])],"isStart":true});var subQ3=sQuery(id+"F22.wireOp",EDGE,"E28.15.3");var subQ4=sQuery(id+"F22.wireOp",EDGE,"E28.15.2");var subQ5=sQuery(id+"F3.wireOp",EDGE,"E20.7.3");var subQ7=sQuery(id+"F3.wireOp",EDGE,"E20.7.1");var subQ9=sQuery(id+"F3.wireOp",EDGE,"E20.7.0");var subQ10=makeQuery(id+"F38.opLoft","SWEPT_FACE",FACE,{"disambiguationData":[OSD([subQ9,subQ7,subQ5,sQuery(id+"F22.wireOp",EDGE,"E28.15.1"),subQ4,subQ3])]});var subQ11=sQuery(id+"F41.wireOp",EDGE,"E38");var subQ12=makeQuery(id+"F42.opRevolve","SWEPT_FACE",FACE,{"disambiguationData":[OSD([subQ11])]});var subQ13=makeQuery(id+"F42.opRevolve","SWEPT_EDGE",EDGE,{"disambiguationData":[OSD([subQ0,subQ11])]});var subQ14=sQuery(id+"F22.wireOp",EDGE,"E28.14.3");var subQ15=sQuery(id+"F22.wireOp",EDGE,"E28.14.2");var subQ16=sQuery(id+"F3.wireOp",EDGE,"E20.6.3");var subQ17=sQuery(id+"F3.wireOp",EDGE,"E20.6.1");var subQ18=sQuery(id+"F3.wireOp",EDGE,"E20.6.0");var subQ19=makeQuery(id+"F37.opLoft","SWEPT_FACE",FACE,{"disambiguationData":[OSD([subQ18,subQ17,subQ16,sQuery(id+"F22.wireOp",EDGE,"E28.14.1"),subQ15,subQ14])]});var subQ21=sQuery(id+"F22.wireOp",EDGE,"E28.13.3");var subQ22=sQuery(id+"F22.wireOp",EDGE,"E28.13.2");var subQ23=sQuery(id+"F3.wireOp",EDGE,"E20.5.3");var subQ25=sQuery(id+"F3.wireOp",EDGE,"E20.5.1");var subQ26=sQuery(id+"F3.wireOp",EDGE,"E20.5.0");var subQ27=makeQuery(id+"F36.opLoft","SWEPT_FACE",FACE,{"disambiguationData":[OSD([subQ26,subQ25,subQ23,sQuery(id+"F22.wireOp",EDGE,"E28.13.1"),subQ22,subQ21])]});var subQ28=sQuery(id+"F22.wireOp",EDGE,"E28.12.3");var subQ29=sQuery(id+"F22.wireOp",EDGE,"E28.12.2");var subQ30=sQuery(id+"F3.wireOp",EDGE,"E20.4.3");var subQ32=sQuery(id+"F3.wireOp",EDGE,"E20.4.1");var subQ33=sQuery(id+"F3.wireOp",EDGE,"E20.4.0");var subQ34=makeQuery(id+"F35.opLoft","SWEPT_FACE",FACE,{"disambiguationData":[OSD([subQ33,subQ32,subQ30,sQuery(id+"F22.wireOp",EDGE,"E28.12.1"),subQ29,subQ28])]});var subQ35=sQuery(id+"F22.wireOp",EDGE,"E28.11.3");var subQ36=sQuery(id+"F22.wireOp",EDGE,"E28.11.2");var subQ37=sQuery(id+"F3.wireOp",EDGE,"E20.3.3");var subQ39=sQuery(id+"F3.wireOp",EDGE,"E20.3.1");var subQ40=sQuery(id+"F3.wireOp",EDGE,"E20.3.0");var subQ41=makeQuery(id+"F34.opLoft","SWEPT_FACE",FACE,{"disambiguationData":[OSD([subQ40,subQ39,subQ37,sQuery(id+"F22.wireOp",EDGE,"E28.11.1"),subQ36,subQ35])]});var subQ42=sQuery(id+"F22.wireOp",EDGE,"E28.10.3");var subQ43=sQuery(id+"F22.wireOp",EDGE,"E28.10.2");var subQ44=sQuery(id+"F3.wireOp",EDGE,"E20.2.3");var subQ46=sQuery(id+"F3.wireOp",EDGE,"E20.2.1");var subQ47=sQuery(id+"F3.wireOp",EDGE,"E20.2.0");var subQ48=makeQuery(id+"F33.opLoft","SWEPT_FACE",FACE,{"disambiguationData":[OSD([subQ47,subQ46,subQ44,sQuery(id+"F22.wireOp",EDGE,"E28.10.1"),subQ43,subQ42])]});var subQ49=sQuery(id+"F22.wireOp",EDGE,"E28.9.3");var subQ50=sQuery(id+"F22.wireOp",EDGE,"E28.9.2");var subQ51=sQuery(id+"F3.wireOp",EDGE,"E20.1.3");var subQ53=sQuery(id+"F3.wireOp",EDGE,"E20.1.1");var subQ54=sQuery(id+"F3.wireOp",EDGE,"E20.1.0");var subQ55=makeQuery(id+"F32.opLoft","SWEPT_FACE",FACE,{"disambiguationData":[OSD([subQ54,subQ53,subQ51,sQuery(id+"F22.wireOp",EDGE,"E28.9.1"),subQ50,subQ49])]});var subQ56=sQuery(id+"F22.wireOp",EDGE,"E28.8.3");var subQ57=sQuery(id+"F22.wireOp",EDGE,"E28.8.2");var subQ59=sQuery(id+"F3.wireOp",EDGE,"E18.top");var subQ60=sQuery(id+"F3.wireOp",EDGE,"E18.bottom");var subQ61=sQuery(id+"F3.wireOp",EDGE,"E18.left");var subQ62=makeQuery(id+"F31.opLoft","SWEPT_FACE",FACE,{"disambiguationData":[OSD([subQ60,subQ59,subQ61,sQuery(id+"F22.wireOp",EDGE,"E28.8.1"),subQ57,subQ56])]});var subQ63=sQuery(id+"F22.wireOp",EDGE,"E28.7.3");var subQ64=sQuery(id+"F22.wireOp",EDGE,"E28.7.2");var subQ65=sQuery(id+"F3.wireOp",EDGE,"E20.15.3");var subQ66=sQuery(id+"F3.wireOp",EDGE,"E20.15.1");var subQ67=sQuery(id+"F3.wireOp",EDGE,"E20.15.0");var subQ68=makeQuery(id+"F30.opLoft","SWEPT_FACE",FACE,{"disambiguationData":[OSD([subQ67,subQ66,subQ65,sQuery(id+"F22.wireOp",EDGE,"E28.7.1"),subQ64,subQ63])]});var subQ70=sQuery(id+"F22.wireOp",EDGE,"E28.6.3");var subQ71=sQuery(id+"F22.wireOp",EDGE,"E28.6.2");var subQ72=sQuery(id+"F3.wireOp",EDGE,"E20.14.3");var subQ74=sQuery(id+"F3.wireOp",EDGE,"E20.14.1");var subQ75=sQuery(id+"F3.wireOp",EDGE,"E20.14.0");var subQ76=makeQuery(id+"F29.opLoft","SWEPT_FACE",FACE,{"disambiguationData":[OSD([subQ75,subQ74,subQ72,sQuery(id+"F22.wireOp",EDGE,"E28.6.1"),subQ71,subQ70])]});var subQ77=sQuery(id+"F22.wireOp",EDGE,"E28.5.3");var subQ78=sQuery(id+"F22.wireOp",EDGE,"E28.5.2");var subQ79=sQuery(id+"F3.wireOp",EDGE,"E20.13.3");var subQ81=sQuery(id+"F3.wireOp",EDGE,"E20.13.1");var subQ82=sQuery(id+"F3.wireOp",EDGE,"E20.13.0");var subQ83=makeQuery(id+"F28.opLoft","SWEPT_FACE",FACE,{"disambiguationData":[OSD([subQ82,subQ81,subQ79,sQuery(id+"F22.wireOp",EDGE,"E28.5.1"),subQ78,subQ77])]});var subQ84=sQuery(id+"F22.wireOp",EDGE,"E28.4.3");var subQ85=sQuery(id+"F22.wireOp",EDGE,"E28.4.2");var subQ86=sQuery(id+"F3.wireOp",EDGE,"E20.12.3");var subQ88=sQuery(id+"F3.wireOp",EDGE,"E20.12.1");var subQ89=sQuery(id+"F3.wireOp",EDGE,"E20.12.0");var subQ90=makeQuery(id+"F27.opLoft","SWEPT_FACE",FACE,{"disambiguationData":[OSD([subQ89,subQ88,subQ86,sQuery(id+"F22.wireOp",EDGE,"E28.4.1"),subQ85,subQ84])]});var subQ91=sQuery(id+"F22.wireOp",EDGE,"E28.3.3");var subQ92=sQuery(id+"F22.wireOp",EDGE,"E28.3.2");var subQ93=sQuery(id+"F3.wireOp",EDGE,"E20.11.3");var subQ95=sQuery(id+"F3.wireOp",EDGE,"E20.11.1");var subQ96=sQuery(id+"F3.wireOp",EDGE,"E20.11.0");var subQ97=makeQuery(id+"F26.opLoft","SWEPT_FACE",FACE,{"disambiguationData":[OSD([subQ96,subQ95,subQ93,sQuery(id+"F22.wireOp",EDGE,"E28.3.1"),subQ92,subQ91])]});var subQ98=sQuery(id+"F22.wireOp",EDGE,"E28.2.3");var subQ99=sQuery(id+"F22.wireOp",EDGE,"E28.2.2");var subQ100=sQuery(id+"F3.wireOp",EDGE,"E20.10.3");var subQ101=sQuery(id+"F3.wireOp",EDGE,"E20.10.1");var subQ102=sQuery(id+"F3.wireOp",EDGE,"E20.10.0");var subQ103=makeQuery(id+"F25.opLoft","SWEPT_FACE",FACE,{"disambiguationData":[OSD([subQ102,subQ101,subQ100,sQuery(id+"F22.wireOp",EDGE,"E28.2.1"),subQ99,subQ98])]});var subQ105=sQuery(id+"F22.wireOp",EDGE,"E28.1.3");var subQ106=sQuery(id+"F22.wireOp",EDGE,"E28.1.2");var subQ107=sQuery(id+"F3.wireOp",EDGE,"E20.9.3");var subQ108=sQuery(id+"F3.wireOp",EDGE,"E20.9.1");var subQ109=sQuery(id+"F3.wireOp",EDGE,"E20.9.0");var subQ110=makeQuery(id+"F24.opLoft","SWEPT_FACE",FACE,{"disambiguationData":[OSD([subQ109,subQ108,subQ107,sQuery(id+"F22.wireOp",EDGE,"E28.1.1"),subQ106,subQ105])]});var subQ111=sQuery(id+"F22.wireOp",EDGE,"E27.top");var subQ112=sQuery(id+"F22.wireOp",EDGE,"E27.bottom");var subQ113=sQuery(id+"F3.wireOp",EDGE,"E20.8.3");var subQ115=sQuery(id+"F3.wireOp",EDGE,"E20.8.1");var subQ119=makeQuery(id+"F42.boolean.opBoolean","COPY",FACE,{"disambiguationData":[TD([subQ10])],"derivedFrom":subQ12});var subQ127=makeQuery(id+"F14.opLoft","CAP_FACE",FACE,{"disambiguationData":[OSD([makeQuery(id+"F3.imprint","IMPRINT",FACE,{"disambiguationData":[TD([[makeQuery(id+"F3.imprint","IMPRINT",EDGE,{"derivedFrom":subQ9}),-1.0]])]})])],"isStart":true});var subQ162=makeQuery(id+"F5.opLoft","CAP_FACE",FACE,{"disambiguationData":[OSD([makeQuery(id+"F3.imprint","IMPRINT",FACE,{"disambiguationData":[TD([[makeQuery(id+"F3.imprint","IMPRINT",EDGE,{"derivedFrom":subQ60}),1.0]])]})])],"isStart":true});var subQ191=makeQuery(id+"F38.boolean.opBoolean","INTERSECT",EDGE,{"derivedFrom":[makeQuery(id+"F37.boolean.opBoolean","SPLIT",FACE,{"disambiguationData":[TD([subQ127])],"derivedFrom":makeQuery(id+"F36.boolean.opBoolean","SPLIT",FACE,{"disambiguationData":[TD([subQ127])],"derivedFrom":makeQuery(id+"F35.boolean.opBoolean","SPLIT",FACE,{"disambiguationData":[TD([subQ127])],"derivedFrom":makeQuery(id+"F34.boolean.opBoolean","SPLIT",FACE,{"disambiguationData":[TD([subQ127])],"derivedFrom":makeQuery(id+"F33.boolean.opBoolean","SPLIT",FACE,{"disambiguationData":[TD([subQ127])],"derivedFrom":makeQuery(id+"F32.boolean.opBoolean","SPLIT",FACE,{"disambiguationData":[TD([subQ127])],"derivedFrom":makeQuery(id+"F31.boolean.opBoolean","SPLIT",FACE,{"disambiguationData":[TD([subQ127])],"derivedFrom":makeQuery(id+"F30.boolean.opBoolean","SPLIT",FACE,{"disambiguationData":[TD([subQ162])],"derivedFrom":makeQuery(id+"F29.boolean.opBoolean","SPLIT",FACE,{"disambiguationData":[TD([subQ162])],"derivedFrom":makeQuery(id+"F28.boolean.opBoolean","SPLIT",FACE,{"disambiguationData":[TD([subQ162])],"derivedFrom":makeQuery(id+"F27.boolean.opBoolean","SPLIT",FACE,{"disambiguationData":[TD([subQ162])],"derivedFrom":makeQuery(id+"F26.boolean.opBoolean","SPLIT",FACE,{"disambiguationData":[TD([subQ162])],"derivedFrom":makeQuery(id+"F25.boolean.opBoolean","SPLIT",FACE,{"disambiguationData":[TD([subQ162])],"derivedFrom":makeQuery(id+"F24.boolean.opBoolean","SPLIT",FACE,{"disambiguationData":[TD([subQ162])],"derivedFrom":makeQuery(id+"F1.opRevolve","SWEPT_FACE",FACE,{"disambiguationData":[OSD([sQuery(id+"F0.wireOp",EDGE,"E4")])]})})})})})})})})})})})})})})}),subQ10]});Q44=makeQuery(id+"F48.opFillet","BLEND_EDGE",EDGE,{"blendedFrom":[makeQuery(id+"F47.opFillet","TWEAK_EDGE",EDGE,{"derivedFrom":[makeQuery(id+"F45.opFillet","BLEND_VERTEX",VERTEX,{"blendedFrom":[subQ191,subQ10,subQ119],"blendedInto":[subQ10,subQ119]}),makeQuery(id+"F45.opFillet","BLEND_VERTEX",VERTEX,{"blendedFrom":[subQ191,makeQuery(id+"F42.boolean.opBoolean","MERGE",FACE,{"derivedFrom":[subQ2,subQ1]}),subQ119],"blendedInto":[makeQuery(id+"F42.boolean.opBoolean","MERGE",FACE,{"derivedFrom":[subQ2,subQ1]}),subQ119]})]}),makeQuery(id+"F47.opFillet","BLEND_FACE",FACE,{"disambiguationData":[OSD([subQ0,subQ11]),TDD([makeQuery(id+"F42.boolean.opBoolean","COPY",EDGE,{"disambiguationData":[TD([makeQuery(id+"F23.opLoft","SWEPT_FACE",FACE,{"disambiguationData":[OSD([sQuery(id+"F3.wireOp",EDGE,"E20.8.0"),subQ115,subQ113,subQ112,subQ111,sQuery(id+"F22.wireOp",EDGE,"E27.right")])]})])],"derivedFrom":subQ13})])]}),makeQuery(id+"F47.opFillet","BLEND_FACE",FACE,{"disambiguationData":[OSD([subQ0,subQ11]),TDD([makeQuery(id+"F42.boolean.opBoolean","COPY",EDGE,{"disambiguationData":[TD([subQ110])],"derivedFrom":subQ13})])]}),makeQuery(id+"F47.opFillet","BLEND_FACE",FACE,{"disambiguationData":[OSD([subQ0,subQ11]),TDD([makeQuery(id+"F42.boolean.opBoolean","COPY",EDGE,{"disambiguationData":[TD([subQ103])],"derivedFrom":subQ13})])]}),makeQuery(id+"F47.opFillet","BLEND_FACE",FACE,{"disambiguationData":[OSD([subQ0,subQ11]),TDD([makeQuery(id+"F42.boolean.opBoolean","COPY",EDGE,{"disambiguationData":[TD([subQ97])],"derivedFrom":subQ13})])]}),makeQuery(id+"F47.opFillet","BLEND_FACE",FACE,{"disambiguationData":[OSD([subQ0,subQ11]),TDD([makeQuery(id+"F42.boolean.opBoolean","COPY",EDGE,{"disambiguationData":[TD([subQ90])],"derivedFrom":subQ13})])]}),makeQuery(id+"F47.opFillet","BLEND_FACE",FACE,{"disambiguationData":[OSD([subQ0,subQ11]),TDD([makeQuery(id+"F42.boolean.opBoolean","COPY",EDGE,{"disambiguationData":[TD([subQ83])],"derivedFrom":subQ13})])]}),makeQuery(id+"F47.opFillet","BLEND_FACE",FACE,{"disambiguationData":[OSD([subQ0,subQ11]),TDD([makeQuery(id+"F42.boolean.opBoolean","COPY",EDGE,{"disambiguationData":[TD([subQ76])],"derivedFrom":subQ13})])]}),makeQuery(id+"F47.opFillet","BLEND_FACE",FACE,{"disambiguationData":[OSD([subQ0,subQ11]),TDD([makeQuery(id+"F42.boolean.opBoolean","COPY",EDGE,{"disambiguationData":[TD([subQ68])],"derivedFrom":subQ13})])]}),makeQuery(id+"F47.opFillet","BLEND_FACE",FACE,{"disambiguationData":[OSD([subQ0,subQ11]),TDD([makeQuery(id+"F42.boolean.opBoolean","COPY",EDGE,{"disambiguationData":[TD([subQ62])],"derivedFrom":subQ13})])]}),makeQuery(id+"F47.opFillet","BLEND_FACE",FACE,{"disambiguationData":[OSD([subQ0,subQ11]),TDD([makeQuery(id+"F42.boolean.opBoolean","COPY",EDGE,{"disambiguationData":[TD([subQ55])],"derivedFrom":subQ13})])]}),makeQuery(id+"F47.opFillet","BLEND_FACE",FACE,{"disambiguationData":[OSD([subQ0,subQ11]),TDD([makeQuery(id+"F42.boolean.opBoolean","COPY",EDGE,{"disambiguationData":[TD([subQ48])],"derivedFrom":subQ13})])]}),makeQuery(id+"F47.opFillet","BLEND_FACE",FACE,{"disambiguationData":[OSD([subQ0,subQ11]),TDD([makeQuery(id+"F42.boolean.opBoolean","COPY",EDGE,{"disambiguationData":[TD([subQ41])],"derivedFrom":subQ13})])]}),makeQuery(id+"F47.opFillet","BLEND_FACE",FACE,{"disambiguationData":[OSD([subQ0,subQ11]),TDD([makeQuery(id+"F42.boolean.opBoolean","COPY",EDGE,{"disambiguationData":[TD([subQ34])],"derivedFrom":subQ13})])]}),makeQuery(id+"F47.opFillet","BLEND_FACE",FACE,{"disambiguationData":[OSD([subQ0,subQ11]),TDD([makeQuery(id+"F42.boolean.opBoolean","COPY",EDGE,{"disambiguationData":[TD([subQ27])],"derivedFrom":subQ13})])]}),makeQuery(id+"F47.opFillet","BLEND_FACE",FACE,{"disambiguationData":[OSD([subQ0,subQ11]),TDD([makeQuery(id+"F42.boolean.opBoolean","COPY",EDGE,{"disambiguationData":[TD([subQ19])],"derivedFrom":subQ13})])]}),makeQuery(id+"F47.opFillet","BLEND_FACE",FACE,{"disambiguationData":[OSD([subQ0,subQ11]),TDD([makeQuery(id+"F42.boolean.opBoolean","COPY",EDGE,{"disambiguationData":[TD([subQ10])],"derivedFrom":subQ13})])]})],"blendedInto":[makeQuery(id+"F47.opFillet","BLEND_FACE",FACE,{"disambiguationData":[OSD([subQ0,subQ11]),TDD([makeQuery(id+"F42.boolean.opBoolean","COPY",EDGE,{"disambiguationData":[TD([makeQuery(id+"F23.opLoft","SWEPT_FACE",FACE,{"disambiguationData":[OSD([sQuery(id+"F3.wireOp",EDGE,"E20.8.0"),subQ115,subQ113,subQ112,subQ111,sQuery(id+"F22.wireOp",EDGE,"E27.right")])]})])],"derivedFrom":subQ13})])]}),makeQuery(id+"F47.opFillet","BLEND_FACE",FACE,{"disambiguationData":[OSD([subQ0,subQ11]),TDD([makeQuery(id+"F42.boolean.opBoolean","COPY",EDGE,{"disambiguationData":[TD([subQ110])],"derivedFrom":subQ13})])]}),makeQuery(id+"F47.opFillet","BLEND_FACE",FACE,{"disambiguationData":[OSD([subQ0,subQ11]),TDD([makeQuery(id+"F42.boolean.opBoolean","COPY",EDGE,{"disambiguationData":[TD([subQ103])],"derivedFrom":subQ13})])]}),makeQuery(id+"F47.opFillet","BLEND_FACE",FACE,{"disambiguationData":[OSD([subQ0,subQ11]),TDD([makeQuery(id+"F42.boolean.opBoolean","COPY",EDGE,{"disambiguationData":[TD([subQ97])],"derivedFrom":subQ13})])]}),makeQuery(id+"F47.opFillet","BLEND_FACE",FACE,{"disambiguationData":[OSD([subQ0,subQ11]),TDD([makeQuery(id+"F42.boolean.opBoolean","COPY",EDGE,{"disambiguationData":[TD([subQ90])],"derivedFrom":subQ13})])]}),makeQuery(id+"F47.opFillet","BLEND_FACE",FACE,{"disambiguationData":[OSD([subQ0,subQ11]),TDD([makeQuery(id+"F42.boolean.opBoolean","COPY",EDGE,{"disambiguationData":[TD([subQ83])],"derivedFrom":subQ13})])]}),makeQuery(id+"F47.opFillet","BLEND_FACE",FACE,{"disambiguationData":[OSD([subQ0,subQ11]),TDD([makeQuery(id+"F42.boolean.opBoolean","COPY",EDGE,{"disambiguationData":[TD([subQ76])],"derivedFrom":subQ13})])]}),makeQuery(id+"F47.opFillet","BLEND_FACE",FACE,{"disambiguationData":[OSD([subQ0,subQ11]),TDD([makeQuery(id+"F42.boolean.opBoolean","COPY",EDGE,{"disambiguationData":[TD([subQ68])],"derivedFrom":subQ13})])]}),makeQuery(id+"F47.opFillet","BLEND_FACE",FACE,{"disambiguationData":[OSD([subQ0,subQ11]),TDD([makeQuery(id+"F42.boolean.opBoolean","COPY",EDGE,{"disambiguationData":[TD([subQ62])],"derivedFrom":subQ13})])]}),makeQuery(id+"F47.opFillet","BLEND_FACE",FACE,{"disambiguationData":[OSD([subQ0,subQ11]),TDD([makeQuery(id+"F42.boolean.opBoolean","COPY",EDGE,{"disambiguationData":[TD([subQ55])],"derivedFrom":subQ13})])]}),makeQuery(id+"F47.opFillet","BLEND_FACE",FACE,{"disambiguationData":[OSD([subQ0,subQ11]),TDD([makeQuery(id+"F42.boolean.opBoolean","COPY",EDGE,{"disambiguationData":[TD([subQ48])],"derivedFrom":subQ13})])]}),makeQuery(id+"F47.opFillet","BLEND_FACE",FACE,{"disambiguationData":[OSD([subQ0,subQ11]),TDD([makeQuery(id+"F42.boolean.opBoolean","COPY",EDGE,{"disambiguationData":[TD([subQ41])],"derivedFrom":subQ13})])]}),makeQuery(id+"F47.opFillet","BLEND_FACE",FACE,{"disambiguationData":[OSD([subQ0,subQ11]),TDD([makeQuery(id+"F42.boolean.opBoolean","COPY",EDGE,{"disambiguationData":[TD([subQ34])],"derivedFrom":subQ13})])]}),makeQuery(id+"F47.opFillet","BLEND_FACE",FACE,{"disambiguationData":[OSD([subQ0,subQ11]),TDD([makeQuery(id+"F42.boolean.opBoolean","COPY",EDGE,{"disambiguationData":[TD([subQ27])],"derivedFrom":subQ13})])]}),makeQuery(id+"F47.opFillet","BLEND_FACE",FACE,{"disambiguationData":[OSD([subQ0,subQ11]),TDD([makeQuery(id+"F42.boolean.opBoolean","COPY",EDGE,{"disambiguationData":[TD([subQ19])],"derivedFrom":subQ13})])]}),makeQuery(id+"F47.opFillet","BLEND_FACE",FACE,{"disambiguationData":[OSD([subQ0,subQ11]),TDD([makeQuery(id+"F42.boolean.opBoolean","COPY",EDGE,{"disambiguationData":[TD([subQ10])],"derivedFrom":subQ13})])]})]});}
            var Q45;
            {var subQ0=sQuery(id+"F41.wireOp",EDGE,"E34");var subQ1=sQuery(id+"F41.wireOp",EDGE,"E32");Q45=makeQuery(id+"F42.boolean.opBoolean","INTERSECT",EDGE,{"derivedFrom":[makeQuery(id+"F37.opLoft","SWEPT_FACE",FACE,{"disambiguationData":[OSD([sQuery(id+"F3.wireOp",EDGE,"E20.6.0"),sQuery(id+"F3.wireOp",EDGE,"E20.6.1"),sQuery(id+"F3.wireOp",EDGE,"E20.6.3"),sQuery(id+"F22.wireOp",EDGE,"E28.14.1"),sQuery(id+"F22.wireOp",EDGE,"E28.14.2"),sQuery(id+"F22.wireOp",EDGE,"E28.14.3")])]}),makeQuery(id+"F42.opRevolve","SWEPT_FACE",FACE,{"disambiguationData":[OSD([subQ1]),TDD([makeQuery(id+"F41.imprint","IMPRINT",EDGE,{"disambiguationData":[TD([[makeQuery(id+"F41.imprint","INTERSECT",VERTEX,{"disambiguationData":[OD(0.0)],"derivedFrom":[subQ1,subQ0]}),-1.0]])],"derivedFrom":subQ1})])]})]});}
            var Q46;
            {var subQ0=sQuery(id+"F22.wireOp",EDGE,"E28.15.3");var subQ1=sQuery(id+"F22.wireOp",EDGE,"E28.15.2");var subQ2=sQuery(id+"F22.wireOp",EDGE,"E28.15.1");var subQ3=sQuery(id+"F3.wireOp",EDGE,"E20.7.3");var subQ4=sQuery(id+"F3.wireOp",EDGE,"E20.7.1");var subQ5=sQuery(id+"F22.wireOp",EDGE,"E28.15.0");var subQ6=makeQuery(id+"F38.opLoft","SWEPT_FACE",FACE,{"disambiguationData":[OSD([subQ4,sQuery(id+"F3.wireOp",EDGE,"E20.7.2"),subQ3,subQ5,subQ1,subQ0])]});var subQ7=sQuery(id+"F41.wireOp",EDGE,"E34");var subQ8=sQuery(id+"F41.wireOp",EDGE,"E32");Q46=makeQuery(id+"F44.opFillet","BLEND_EDGE",EDGE,{"blendedFrom":[makeQuery(id+"F40.boolean.opBoolean","INTERSECT",EDGE,{"derivedFrom":[subQ6,makeQuery(id+"F40.opExtrude","CAP_FACE",FACE,{"disambiguationData":[OSD([sQuery(id+"F39.wireOp",EDGE,"E29"),sQuery(id+"F39.wireOp",EDGE,"E30")])],"isStart":true})]}),makeQuery(id+"F42.boolean.opBoolean","COPY",FACE,{"disambiguationData":[TD([makeQuery(id+"F38.opLoft","SWEPT_FACE",FACE,{"disambiguationData":[OSD([sQuery(id+"F3.wireOp",EDGE,"E20.7.0"),subQ4,subQ3,subQ2,subQ1,subQ0])]})])],"derivedFrom":makeQuery(id+"F42.opRevolve","SWEPT_FACE",FACE,{"disambiguationData":[OSD([subQ8]),TDD([makeQuery(id+"F41.imprint","IMPRINT",EDGE,{"disambiguationData":[TD([[makeQuery(id+"F41.imprint","INTERSECT",VERTEX,{"disambiguationData":[OD(0.0)],"derivedFrom":[subQ8,subQ7]}),-1.0]])],"derivedFrom":subQ8})])]})})],"blendedInto":[makeQuery(id+"F42.boolean.opBoolean","COPY",FACE,{"disambiguationData":[TD([makeQuery(id+"F38.opLoft","SWEPT_FACE",FACE,{"disambiguationData":[OSD([sQuery(id+"F3.wireOp",EDGE,"E20.7.0"),subQ4,subQ3,subQ2,subQ1,subQ0])]})])],"derivedFrom":makeQuery(id+"F42.opRevolve","SWEPT_FACE",FACE,{"disambiguationData":[OSD([subQ8]),TDD([makeQuery(id+"F41.imprint","IMPRINT",EDGE,{"disambiguationData":[TD([[makeQuery(id+"F41.imprint","INTERSECT",VERTEX,{"disambiguationData":[OD(0.0)],"derivedFrom":[subQ8,subQ7]}),-1.0]])],"derivedFrom":subQ8})])]})})]});}
            var Q47;
            {var subQ0=sQuery(id+"F41.wireOp",EDGE,"E37");var subQ1=makeQuery(id+"F42.opRevolve","SWEPT_FACE",FACE,{"disambiguationData":[OSD([subQ0])]});var subQ2=makeQuery(id+"F40.opExtrude","CAP_FACE",FACE,{"disambiguationData":[OSD([sQuery(id+"F39.wireOp",EDGE,"E29"),sQuery(id+"F39.wireOp",EDGE,"E30")])],"isStart":true});var subQ3=sQuery(id+"F22.wireOp",EDGE,"E28.15.3");var subQ4=sQuery(id+"F22.wireOp",EDGE,"E28.15.2");var subQ5=sQuery(id+"F3.wireOp",EDGE,"E20.7.3");var subQ7=sQuery(id+"F3.wireOp",EDGE,"E20.7.1");var subQ8=sQuery(id+"F3.wireOp",EDGE,"E20.7.0");var subQ9=sQuery(id+"F41.wireOp",EDGE,"E38");var subQ10=makeQuery(id+"F42.opRevolve","SWEPT_FACE",FACE,{"disambiguationData":[OSD([subQ9])]});var subQ11=makeQuery(id+"F42.opRevolve","SWEPT_EDGE",EDGE,{"disambiguationData":[OSD([subQ0,subQ9])]});var subQ12=sQuery(id+"F22.wireOp",EDGE,"E28.14.3");var subQ13=sQuery(id+"F22.wireOp",EDGE,"E28.14.2");var subQ14=sQuery(id+"F3.wireOp",EDGE,"E20.6.3");var subQ15=sQuery(id+"F3.wireOp",EDGE,"E20.6.1");var subQ16=sQuery(id+"F3.wireOp",EDGE,"E20.6.0");var subQ17=makeQuery(id+"F37.opLoft","SWEPT_FACE",FACE,{"disambiguationData":[OSD([subQ16,subQ15,subQ14,sQuery(id+"F22.wireOp",EDGE,"E28.14.1"),subQ13,subQ12])]});var subQ20=sQuery(id+"F22.wireOp",EDGE,"E28.13.3");var subQ21=sQuery(id+"F22.wireOp",EDGE,"E28.13.2");var subQ22=sQuery(id+"F3.wireOp",EDGE,"E20.5.3");var subQ24=sQuery(id+"F3.wireOp",EDGE,"E20.5.1");var subQ25=sQuery(id+"F3.wireOp",EDGE,"E20.5.0");var subQ26=makeQuery(id+"F36.opLoft","SWEPT_FACE",FACE,{"disambiguationData":[OSD([subQ25,subQ24,subQ22,sQuery(id+"F22.wireOp",EDGE,"E28.13.1"),subQ21,subQ20])]});var subQ27=sQuery(id+"F22.wireOp",EDGE,"E28.12.3");var subQ28=sQuery(id+"F22.wireOp",EDGE,"E28.12.2");var subQ29=sQuery(id+"F3.wireOp",EDGE,"E20.4.3");var subQ31=sQuery(id+"F3.wireOp",EDGE,"E20.4.1");var subQ32=sQuery(id+"F3.wireOp",EDGE,"E20.4.0");var subQ33=makeQuery(id+"F35.opLoft","SWEPT_FACE",FACE,{"disambiguationData":[OSD([subQ32,subQ31,subQ29,sQuery(id+"F22.wireOp",EDGE,"E28.12.1"),subQ28,subQ27])]});var subQ34=sQuery(id+"F22.wireOp",EDGE,"E28.11.3");var subQ35=sQuery(id+"F22.wireOp",EDGE,"E28.11.2");var subQ36=sQuery(id+"F3.wireOp",EDGE,"E20.3.3");var subQ38=sQuery(id+"F3.wireOp",EDGE,"E20.3.1");var subQ39=sQuery(id+"F3.wireOp",EDGE,"E20.3.0");var subQ40=makeQuery(id+"F34.opLoft","SWEPT_FACE",FACE,{"disambiguationData":[OSD([subQ39,subQ38,subQ36,sQuery(id+"F22.wireOp",EDGE,"E28.11.1"),subQ35,subQ34])]});var subQ41=sQuery(id+"F22.wireOp",EDGE,"E28.10.3");var subQ42=sQuery(id+"F22.wireOp",EDGE,"E28.10.2");var subQ43=sQuery(id+"F3.wireOp",EDGE,"E20.2.3");var subQ45=sQuery(id+"F3.wireOp",EDGE,"E20.2.1");var subQ46=sQuery(id+"F3.wireOp",EDGE,"E20.2.0");var subQ47=makeQuery(id+"F33.opLoft","SWEPT_FACE",FACE,{"disambiguationData":[OSD([subQ46,subQ45,subQ43,sQuery(id+"F22.wireOp",EDGE,"E28.10.1"),subQ42,subQ41])]});var subQ48=sQuery(id+"F22.wireOp",EDGE,"E28.9.3");var subQ49=sQuery(id+"F22.wireOp",EDGE,"E28.9.2");var subQ50=sQuery(id+"F3.wireOp",EDGE,"E20.1.3");var subQ52=sQuery(id+"F3.wireOp",EDGE,"E20.1.1");var subQ53=sQuery(id+"F3.wireOp",EDGE,"E20.1.0");var subQ54=makeQuery(id+"F32.opLoft","SWEPT_FACE",FACE,{"disambiguationData":[OSD([subQ53,subQ52,subQ50,sQuery(id+"F22.wireOp",EDGE,"E28.9.1"),subQ49,subQ48])]});var subQ55=sQuery(id+"F22.wireOp",EDGE,"E28.8.3");var subQ56=sQuery(id+"F22.wireOp",EDGE,"E28.8.2");var subQ58=sQuery(id+"F3.wireOp",EDGE,"E18.top");var subQ59=sQuery(id+"F3.wireOp",EDGE,"E18.bottom");var subQ60=sQuery(id+"F3.wireOp",EDGE,"E18.left");var subQ61=makeQuery(id+"F31.opLoft","SWEPT_FACE",FACE,{"disambiguationData":[OSD([subQ59,subQ58,subQ60,sQuery(id+"F22.wireOp",EDGE,"E28.8.1"),subQ56,subQ55])]});var subQ62=sQuery(id+"F22.wireOp",EDGE,"E28.7.3");var subQ63=sQuery(id+"F22.wireOp",EDGE,"E28.7.2");var subQ64=sQuery(id+"F3.wireOp",EDGE,"E20.15.3");var subQ65=sQuery(id+"F3.wireOp",EDGE,"E20.15.1");var subQ66=sQuery(id+"F3.wireOp",EDGE,"E20.15.0");var subQ67=makeQuery(id+"F30.opLoft","SWEPT_FACE",FACE,{"disambiguationData":[OSD([subQ66,subQ65,subQ64,sQuery(id+"F22.wireOp",EDGE,"E28.7.1"),subQ63,subQ62])]});var subQ69=sQuery(id+"F22.wireOp",EDGE,"E28.6.3");var subQ70=sQuery(id+"F22.wireOp",EDGE,"E28.6.2");var subQ71=sQuery(id+"F3.wireOp",EDGE,"E20.14.3");var subQ73=sQuery(id+"F3.wireOp",EDGE,"E20.14.1");var subQ74=sQuery(id+"F3.wireOp",EDGE,"E20.14.0");var subQ75=makeQuery(id+"F29.opLoft","SWEPT_FACE",FACE,{"disambiguationData":[OSD([subQ74,subQ73,subQ71,sQuery(id+"F22.wireOp",EDGE,"E28.6.1"),subQ70,subQ69])]});var subQ76=sQuery(id+"F22.wireOp",EDGE,"E28.5.3");var subQ77=sQuery(id+"F22.wireOp",EDGE,"E28.5.2");var subQ78=sQuery(id+"F3.wireOp",EDGE,"E20.13.3");var subQ80=sQuery(id+"F3.wireOp",EDGE,"E20.13.1");var subQ81=sQuery(id+"F3.wireOp",EDGE,"E20.13.0");var subQ82=makeQuery(id+"F28.opLoft","SWEPT_FACE",FACE,{"disambiguationData":[OSD([subQ81,subQ80,subQ78,sQuery(id+"F22.wireOp",EDGE,"E28.5.1"),subQ77,subQ76])]});var subQ83=sQuery(id+"F22.wireOp",EDGE,"E28.4.3");var subQ84=sQuery(id+"F22.wireOp",EDGE,"E28.4.2");var subQ85=sQuery(id+"F3.wireOp",EDGE,"E20.12.3");var subQ87=sQuery(id+"F3.wireOp",EDGE,"E20.12.1");var subQ88=sQuery(id+"F3.wireOp",EDGE,"E20.12.0");var subQ89=makeQuery(id+"F27.opLoft","SWEPT_FACE",FACE,{"disambiguationData":[OSD([subQ88,subQ87,subQ85,sQuery(id+"F22.wireOp",EDGE,"E28.4.1"),subQ84,subQ83])]});var subQ90=sQuery(id+"F22.wireOp",EDGE,"E28.3.3");var subQ91=sQuery(id+"F22.wireOp",EDGE,"E28.3.2");var subQ92=sQuery(id+"F3.wireOp",EDGE,"E20.11.3");var subQ94=sQuery(id+"F3.wireOp",EDGE,"E20.11.1");var subQ95=sQuery(id+"F3.wireOp",EDGE,"E20.11.0");var subQ96=makeQuery(id+"F26.opLoft","SWEPT_FACE",FACE,{"disambiguationData":[OSD([subQ95,subQ94,subQ92,sQuery(id+"F22.wireOp",EDGE,"E28.3.1"),subQ91,subQ90])]});var subQ97=sQuery(id+"F22.wireOp",EDGE,"E28.2.3");var subQ98=sQuery(id+"F22.wireOp",EDGE,"E28.2.2");var subQ99=sQuery(id+"F3.wireOp",EDGE,"E20.10.3");var subQ100=sQuery(id+"F3.wireOp",EDGE,"E20.10.1");var subQ101=sQuery(id+"F3.wireOp",EDGE,"E20.10.0");var subQ102=makeQuery(id+"F25.opLoft","SWEPT_FACE",FACE,{"disambiguationData":[OSD([subQ101,subQ100,subQ99,sQuery(id+"F22.wireOp",EDGE,"E28.2.1"),subQ98,subQ97])]});var subQ104=sQuery(id+"F22.wireOp",EDGE,"E28.1.3");var subQ105=sQuery(id+"F22.wireOp",EDGE,"E28.1.2");var subQ106=sQuery(id+"F3.wireOp",EDGE,"E20.9.3");var subQ107=sQuery(id+"F3.wireOp",EDGE,"E20.9.1");var subQ108=sQuery(id+"F3.wireOp",EDGE,"E20.9.0");var subQ109=makeQuery(id+"F24.opLoft","SWEPT_FACE",FACE,{"disambiguationData":[OSD([subQ108,subQ107,subQ106,sQuery(id+"F22.wireOp",EDGE,"E28.1.1"),subQ105,subQ104])]});var subQ110=sQuery(id+"F22.wireOp",EDGE,"E27.top");var subQ111=sQuery(id+"F22.wireOp",EDGE,"E27.bottom");var subQ112=sQuery(id+"F3.wireOp",EDGE,"E20.8.3");var subQ114=sQuery(id+"F3.wireOp",EDGE,"E20.8.1");var subQ118=makeQuery(id+"F42.boolean.opBoolean","COPY",FACE,{"disambiguationData":[TD([subQ17])],"derivedFrom":subQ10});var subQ126=makeQuery(id+"F14.opLoft","CAP_FACE",FACE,{"disambiguationData":[OSD([makeQuery(id+"F3.imprint","IMPRINT",FACE,{"disambiguationData":[TD([[makeQuery(id+"F3.imprint","IMPRINT",EDGE,{"derivedFrom":subQ8}),-1.0]])]})])],"isStart":true});var subQ161=makeQuery(id+"F5.opLoft","CAP_FACE",FACE,{"disambiguationData":[OSD([makeQuery(id+"F3.imprint","IMPRINT",FACE,{"disambiguationData":[TD([[makeQuery(id+"F3.imprint","IMPRINT",EDGE,{"derivedFrom":subQ59}),1.0]])]})])],"isStart":true});var subQ190=makeQuery(id+"F37.boolean.opBoolean","INTERSECT",EDGE,{"derivedFrom":[makeQuery(id+"F36.boolean.opBoolean","SPLIT",FACE,{"disambiguationData":[TD([subQ126])],"derivedFrom":makeQuery(id+"F35.boolean.opBoolean","SPLIT",FACE,{"disambiguationData":[TD([subQ126])],"derivedFrom":makeQuery(id+"F34.boolean.opBoolean","SPLIT",FACE,{"disambiguationData":[TD([subQ126])],"derivedFrom":makeQuery(id+"F33.boolean.opBoolean","SPLIT",FACE,{"disambiguationData":[TD([subQ126])],"derivedFrom":makeQuery(id+"F32.boolean.opBoolean","SPLIT",FACE,{"disambiguationData":[TD([subQ126])],"derivedFrom":makeQuery(id+"F31.boolean.opBoolean","SPLIT",FACE,{"disambiguationData":[TD([subQ126])],"derivedFrom":makeQuery(id+"F30.boolean.opBoolean","SPLIT",FACE,{"disambiguationData":[TD([subQ161])],"derivedFrom":makeQuery(id+"F29.boolean.opBoolean","SPLIT",FACE,{"disambiguationData":[TD([subQ161])],"derivedFrom":makeQuery(id+"F28.boolean.opBoolean","SPLIT",FACE,{"disambiguationData":[TD([subQ161])],"derivedFrom":makeQuery(id+"F27.boolean.opBoolean","SPLIT",FACE,{"disambiguationData":[TD([subQ161])],"derivedFrom":makeQuery(id+"F26.boolean.opBoolean","SPLIT",FACE,{"disambiguationData":[TD([subQ161])],"derivedFrom":makeQuery(id+"F25.boolean.opBoolean","SPLIT",FACE,{"disambiguationData":[TD([subQ161])],"derivedFrom":makeQuery(id+"F24.boolean.opBoolean","SPLIT",FACE,{"disambiguationData":[TD([subQ161])],"derivedFrom":makeQuery(id+"F1.opRevolve","SWEPT_FACE",FACE,{"disambiguationData":[OSD([sQuery(id+"F0.wireOp",EDGE,"E4")])]})})})})})})})})})})})})})}),subQ17]});Q47=makeQuery(id+"F48.opFillet","BLEND_EDGE",EDGE,{"blendedFrom":[makeQuery(id+"F47.opFillet","TWEAK_EDGE",EDGE,{"derivedFrom":[makeQuery(id+"F45.opFillet","BLEND_VERTEX",VERTEX,{"blendedFrom":[subQ190,subQ17,subQ118],"blendedInto":[subQ17,subQ118]}),makeQuery(id+"F45.opFillet","BLEND_VERTEX",VERTEX,{"blendedFrom":[subQ190,makeQuery(id+"F42.boolean.opBoolean","MERGE",FACE,{"derivedFrom":[subQ2,subQ1]}),subQ118],"blendedInto":[makeQuery(id+"F42.boolean.opBoolean","MERGE",FACE,{"derivedFrom":[subQ2,subQ1]}),subQ118]})]}),makeQuery(id+"F47.opFillet","BLEND_FACE",FACE,{"disambiguationData":[OSD([subQ0,subQ9]),TDD([makeQuery(id+"F42.boolean.opBoolean","COPY",EDGE,{"disambiguationData":[TD([makeQuery(id+"F23.opLoft","SWEPT_FACE",FACE,{"disambiguationData":[OSD([sQuery(id+"F3.wireOp",EDGE,"E20.8.0"),subQ114,subQ112,subQ111,subQ110,sQuery(id+"F22.wireOp",EDGE,"E27.right")])]})])],"derivedFrom":subQ11})])]}),makeQuery(id+"F47.opFillet","BLEND_FACE",FACE,{"disambiguationData":[OSD([subQ0,subQ9]),TDD([makeQuery(id+"F42.boolean.opBoolean","COPY",EDGE,{"disambiguationData":[TD([subQ109])],"derivedFrom":subQ11})])]}),makeQuery(id+"F47.opFillet","BLEND_FACE",FACE,{"disambiguationData":[OSD([subQ0,subQ9]),TDD([makeQuery(id+"F42.boolean.opBoolean","COPY",EDGE,{"disambiguationData":[TD([subQ102])],"derivedFrom":subQ11})])]}),makeQuery(id+"F47.opFillet","BLEND_FACE",FACE,{"disambiguationData":[OSD([subQ0,subQ9]),TDD([makeQuery(id+"F42.boolean.opBoolean","COPY",EDGE,{"disambiguationData":[TD([subQ96])],"derivedFrom":subQ11})])]}),makeQuery(id+"F47.opFillet","BLEND_FACE",FACE,{"disambiguationData":[OSD([subQ0,subQ9]),TDD([makeQuery(id+"F42.boolean.opBoolean","COPY",EDGE,{"disambiguationData":[TD([subQ89])],"derivedFrom":subQ11})])]}),makeQuery(id+"F47.opFillet","BLEND_FACE",FACE,{"disambiguationData":[OSD([subQ0,subQ9]),TDD([makeQuery(id+"F42.boolean.opBoolean","COPY",EDGE,{"disambiguationData":[TD([subQ82])],"derivedFrom":subQ11})])]}),makeQuery(id+"F47.opFillet","BLEND_FACE",FACE,{"disambiguationData":[OSD([subQ0,subQ9]),TDD([makeQuery(id+"F42.boolean.opBoolean","COPY",EDGE,{"disambiguationData":[TD([subQ75])],"derivedFrom":subQ11})])]}),makeQuery(id+"F47.opFillet","BLEND_FACE",FACE,{"disambiguationData":[OSD([subQ0,subQ9]),TDD([makeQuery(id+"F42.boolean.opBoolean","COPY",EDGE,{"disambiguationData":[TD([subQ67])],"derivedFrom":subQ11})])]}),makeQuery(id+"F47.opFillet","BLEND_FACE",FACE,{"disambiguationData":[OSD([subQ0,subQ9]),TDD([makeQuery(id+"F42.boolean.opBoolean","COPY",EDGE,{"disambiguationData":[TD([subQ61])],"derivedFrom":subQ11})])]}),makeQuery(id+"F47.opFillet","BLEND_FACE",FACE,{"disambiguationData":[OSD([subQ0,subQ9]),TDD([makeQuery(id+"F42.boolean.opBoolean","COPY",EDGE,{"disambiguationData":[TD([subQ54])],"derivedFrom":subQ11})])]}),makeQuery(id+"F47.opFillet","BLEND_FACE",FACE,{"disambiguationData":[OSD([subQ0,subQ9]),TDD([makeQuery(id+"F42.boolean.opBoolean","COPY",EDGE,{"disambiguationData":[TD([subQ47])],"derivedFrom":subQ11})])]}),makeQuery(id+"F47.opFillet","BLEND_FACE",FACE,{"disambiguationData":[OSD([subQ0,subQ9]),TDD([makeQuery(id+"F42.boolean.opBoolean","COPY",EDGE,{"disambiguationData":[TD([subQ40])],"derivedFrom":subQ11})])]}),makeQuery(id+"F47.opFillet","BLEND_FACE",FACE,{"disambiguationData":[OSD([subQ0,subQ9]),TDD([makeQuery(id+"F42.boolean.opBoolean","COPY",EDGE,{"disambiguationData":[TD([subQ33])],"derivedFrom":subQ11})])]}),makeQuery(id+"F47.opFillet","BLEND_FACE",FACE,{"disambiguationData":[OSD([subQ0,subQ9]),TDD([makeQuery(id+"F42.boolean.opBoolean","COPY",EDGE,{"disambiguationData":[TD([subQ26])],"derivedFrom":subQ11})])]}),makeQuery(id+"F47.opFillet","BLEND_FACE",FACE,{"disambiguationData":[OSD([subQ0,subQ9]),TDD([makeQuery(id+"F42.boolean.opBoolean","COPY",EDGE,{"disambiguationData":[TD([subQ17])],"derivedFrom":subQ11})])]}),makeQuery(id+"F47.opFillet","BLEND_FACE",FACE,{"disambiguationData":[OSD([subQ0,subQ9]),TDD([makeQuery(id+"F42.boolean.opBoolean","COPY",EDGE,{"disambiguationData":[TD([makeQuery(id+"F38.opLoft","SWEPT_FACE",FACE,{"disambiguationData":[OSD([subQ8,subQ7,subQ5,sQuery(id+"F22.wireOp",EDGE,"E28.15.1"),subQ4,subQ3])]})])],"derivedFrom":subQ11})])]})],"blendedInto":[makeQuery(id+"F47.opFillet","BLEND_FACE",FACE,{"disambiguationData":[OSD([subQ0,subQ9]),TDD([makeQuery(id+"F42.boolean.opBoolean","COPY",EDGE,{"disambiguationData":[TD([makeQuery(id+"F23.opLoft","SWEPT_FACE",FACE,{"disambiguationData":[OSD([sQuery(id+"F3.wireOp",EDGE,"E20.8.0"),subQ114,subQ112,subQ111,subQ110,sQuery(id+"F22.wireOp",EDGE,"E27.right")])]})])],"derivedFrom":subQ11})])]}),makeQuery(id+"F47.opFillet","BLEND_FACE",FACE,{"disambiguationData":[OSD([subQ0,subQ9]),TDD([makeQuery(id+"F42.boolean.opBoolean","COPY",EDGE,{"disambiguationData":[TD([subQ109])],"derivedFrom":subQ11})])]}),makeQuery(id+"F47.opFillet","BLEND_FACE",FACE,{"disambiguationData":[OSD([subQ0,subQ9]),TDD([makeQuery(id+"F42.boolean.opBoolean","COPY",EDGE,{"disambiguationData":[TD([subQ102])],"derivedFrom":subQ11})])]}),makeQuery(id+"F47.opFillet","BLEND_FACE",FACE,{"disambiguationData":[OSD([subQ0,subQ9]),TDD([makeQuery(id+"F42.boolean.opBoolean","COPY",EDGE,{"disambiguationData":[TD([subQ96])],"derivedFrom":subQ11})])]}),makeQuery(id+"F47.opFillet","BLEND_FACE",FACE,{"disambiguationData":[OSD([subQ0,subQ9]),TDD([makeQuery(id+"F42.boolean.opBoolean","COPY",EDGE,{"disambiguationData":[TD([subQ89])],"derivedFrom":subQ11})])]}),makeQuery(id+"F47.opFillet","BLEND_FACE",FACE,{"disambiguationData":[OSD([subQ0,subQ9]),TDD([makeQuery(id+"F42.boolean.opBoolean","COPY",EDGE,{"disambiguationData":[TD([subQ82])],"derivedFrom":subQ11})])]}),makeQuery(id+"F47.opFillet","BLEND_FACE",FACE,{"disambiguationData":[OSD([subQ0,subQ9]),TDD([makeQuery(id+"F42.boolean.opBoolean","COPY",EDGE,{"disambiguationData":[TD([subQ75])],"derivedFrom":subQ11})])]}),makeQuery(id+"F47.opFillet","BLEND_FACE",FACE,{"disambiguationData":[OSD([subQ0,subQ9]),TDD([makeQuery(id+"F42.boolean.opBoolean","COPY",EDGE,{"disambiguationData":[TD([subQ67])],"derivedFrom":subQ11})])]}),makeQuery(id+"F47.opFillet","BLEND_FACE",FACE,{"disambiguationData":[OSD([subQ0,subQ9]),TDD([makeQuery(id+"F42.boolean.opBoolean","COPY",EDGE,{"disambiguationData":[TD([subQ61])],"derivedFrom":subQ11})])]}),makeQuery(id+"F47.opFillet","BLEND_FACE",FACE,{"disambiguationData":[OSD([subQ0,subQ9]),TDD([makeQuery(id+"F42.boolean.opBoolean","COPY",EDGE,{"disambiguationData":[TD([subQ54])],"derivedFrom":subQ11})])]}),makeQuery(id+"F47.opFillet","BLEND_FACE",FACE,{"disambiguationData":[OSD([subQ0,subQ9]),TDD([makeQuery(id+"F42.boolean.opBoolean","COPY",EDGE,{"disambiguationData":[TD([subQ47])],"derivedFrom":subQ11})])]}),makeQuery(id+"F47.opFillet","BLEND_FACE",FACE,{"disambiguationData":[OSD([subQ0,subQ9]),TDD([makeQuery(id+"F42.boolean.opBoolean","COPY",EDGE,{"disambiguationData":[TD([subQ40])],"derivedFrom":subQ11})])]}),makeQuery(id+"F47.opFillet","BLEND_FACE",FACE,{"disambiguationData":[OSD([subQ0,subQ9]),TDD([makeQuery(id+"F42.boolean.opBoolean","COPY",EDGE,{"disambiguationData":[TD([subQ33])],"derivedFrom":subQ11})])]}),makeQuery(id+"F47.opFillet","BLEND_FACE",FACE,{"disambiguationData":[OSD([subQ0,subQ9]),TDD([makeQuery(id+"F42.boolean.opBoolean","COPY",EDGE,{"disambiguationData":[TD([subQ26])],"derivedFrom":subQ11})])]}),makeQuery(id+"F47.opFillet","BLEND_FACE",FACE,{"disambiguationData":[OSD([subQ0,subQ9]),TDD([makeQuery(id+"F42.boolean.opBoolean","COPY",EDGE,{"disambiguationData":[TD([subQ17])],"derivedFrom":subQ11})])]}),makeQuery(id+"F47.opFillet","BLEND_FACE",FACE,{"disambiguationData":[OSD([subQ0,subQ9]),TDD([makeQuery(id+"F42.boolean.opBoolean","COPY",EDGE,{"disambiguationData":[TD([makeQuery(id+"F38.opLoft","SWEPT_FACE",FACE,{"disambiguationData":[OSD([subQ8,subQ7,subQ5,sQuery(id+"F22.wireOp",EDGE,"E28.15.1"),subQ4,subQ3])]})])],"derivedFrom":subQ11})])]})]});}
            var Q48;
            {var subQ0=makeQuery(id+"F40.opExtrude","CAP_FACE",FACE,{"disambiguationData":[OSD([sQuery(id+"F39.wireOp",EDGE,"E29"),sQuery(id+"F39.wireOp",EDGE,"E30")])],"isStart":false});var subQ1=sQuery(id+"F4.wireOp",EDGE,"E26.1.3");var subQ2=sQuery(id+"F4.wireOp",EDGE,"E26.1.2");var subQ3=sQuery(id+"F3.wireOp",EDGE,"E20.1.3");var subQ4=sQuery(id+"F3.wireOp",EDGE,"E20.1.1");var subQ5=sQuery(id+"F41.wireOp",EDGE,"E35");var subQ6=makeQuery(id+"F42.opRevolve","SWEPT_FACE",FACE,{"disambiguationData":[OSD([subQ5])]});var subQ7=sQuery(id+"F41.wireOp",EDGE,"E36");var subQ8=makeQuery(id+"F42.opRevolve","SWEPT_FACE",FACE,{"disambiguationData":[OSD([subQ7])]});var subQ9=makeQuery(id+"F42.opRevolve","SWEPT_EDGE",EDGE,{"disambiguationData":[OSD([subQ5,subQ7])]});var subQ10=sQuery(id+"F4.wireOp",EDGE,"E26.2.3");var subQ11=sQuery(id+"F4.wireOp",EDGE,"E26.2.2");var subQ12=sQuery(id+"F3.wireOp",EDGE,"E20.2.3");var subQ13=sQuery(id+"F3.wireOp",EDGE,"E20.2.1");var subQ14=sQuery(id+"F4.wireOp",EDGE,"E26.3.3");var subQ15=sQuery(id+"F4.wireOp",EDGE,"E26.3.2");var subQ16=sQuery(id+"F3.wireOp",EDGE,"E20.3.3");var subQ17=sQuery(id+"F3.wireOp",EDGE,"E20.3.1");var subQ18=sQuery(id+"F4.wireOp",EDGE,"E26.4.3");var subQ19=sQuery(id+"F4.wireOp",EDGE,"E26.4.2");var subQ20=sQuery(id+"F3.wireOp",EDGE,"E20.4.3");var subQ21=sQuery(id+"F3.wireOp",EDGE,"E20.4.1");var subQ22=sQuery(id+"F4.wireOp",EDGE,"E26.5.3");var subQ23=sQuery(id+"F4.wireOp",EDGE,"E26.5.2");var subQ24=sQuery(id+"F3.wireOp",EDGE,"E20.5.3");var subQ25=sQuery(id+"F3.wireOp",EDGE,"E20.5.1");var subQ26=sQuery(id+"F4.wireOp",EDGE,"E26.6.3");var subQ27=sQuery(id+"F4.wireOp",EDGE,"E26.6.2");var subQ28=sQuery(id+"F3.wireOp",EDGE,"E20.6.3");var subQ29=sQuery(id+"F3.wireOp",EDGE,"E20.6.1");var subQ31=makeQuery(id+"F15.opLoft","SWEPT_FACE",FACE,{"disambiguationData":[OSD([sQuery(id+"F3.wireOp",EDGE,"E20.6.0"),subQ29,subQ28,sQuery(id+"F4.wireOp",EDGE,"E26.6.0"),subQ27,subQ26])]});var subQ32=sQuery(id+"F4.wireOp",EDGE,"E26.7.3");var subQ33=sQuery(id+"F4.wireOp",EDGE,"E26.7.2");var subQ34=sQuery(id+"F3.wireOp",EDGE,"E20.7.3");var subQ35=sQuery(id+"F3.wireOp",EDGE,"E20.7.1");var subQ36=sQuery(id+"F4.wireOp",EDGE,"E26.8.3");var subQ37=sQuery(id+"F4.wireOp",EDGE,"E26.8.2");var subQ38=sQuery(id+"F3.wireOp",EDGE,"E20.8.3");var subQ39=sQuery(id+"F3.wireOp",EDGE,"E20.8.1");var subQ40=sQuery(id+"F4.wireOp",EDGE,"E26.9.3");var subQ41=sQuery(id+"F4.wireOp",EDGE,"E26.9.2");var subQ42=sQuery(id+"F3.wireOp",EDGE,"E20.9.3");var subQ43=sQuery(id+"F3.wireOp",EDGE,"E20.9.1");var subQ44=sQuery(id+"F4.wireOp",EDGE,"E26.10.3");var subQ45=sQuery(id+"F4.wireOp",EDGE,"E26.10.2");var subQ46=sQuery(id+"F3.wireOp",EDGE,"E20.10.3");var subQ47=sQuery(id+"F3.wireOp",EDGE,"E20.10.1");var subQ48=sQuery(id+"F4.wireOp",EDGE,"E26.11.3");var subQ49=sQuery(id+"F4.wireOp",EDGE,"E26.11.2");var subQ50=sQuery(id+"F3.wireOp",EDGE,"E20.11.3");var subQ51=sQuery(id+"F3.wireOp",EDGE,"E20.11.1");var subQ52=sQuery(id+"F4.wireOp",EDGE,"E26.12.3");var subQ53=sQuery(id+"F4.wireOp",EDGE,"E26.12.2");var subQ54=sQuery(id+"F3.wireOp",EDGE,"E20.12.3");var subQ55=sQuery(id+"F3.wireOp",EDGE,"E20.12.1");var subQ56=sQuery(id+"F4.wireOp",EDGE,"E26.13.3");var subQ57=sQuery(id+"F4.wireOp",EDGE,"E26.13.2");var subQ58=sQuery(id+"F3.wireOp",EDGE,"E20.13.3");var subQ59=sQuery(id+"F3.wireOp",EDGE,"E20.13.1");var subQ60=sQuery(id+"F4.wireOp",EDGE,"E26.14.3");var subQ61=sQuery(id+"F4.wireOp",EDGE,"E26.14.2");var subQ62=sQuery(id+"F3.wireOp",EDGE,"E20.14.3");var subQ63=sQuery(id+"F3.wireOp",EDGE,"E20.14.1");var subQ64=sQuery(id+"F4.wireOp",EDGE,"E26.15.3");var subQ65=sQuery(id+"F4.wireOp",EDGE,"E26.15.2");var subQ66=sQuery(id+"F3.wireOp",EDGE,"E20.15.3");var subQ67=sQuery(id+"F3.wireOp",EDGE,"E20.15.1");var subQ68=sQuery(id+"F4.wireOp",EDGE,"E23");var subQ69=sQuery(id+"F4.wireOp",EDGE,"E22");var subQ70=sQuery(id+"F3.wireOp",EDGE,"E18.top");var subQ71=sQuery(id+"F3.wireOp",EDGE,"E18.bottom");var subQ74=makeQuery(id+"F42.boolean.opBoolean","COPY",FACE,{"disambiguationData":[TD([subQ31])],"derivedFrom":subQ6});var subQ75=makeQuery(id+"F15.boolean.opBoolean","INTERSECT",EDGE,{"derivedFrom":[makeQuery(id+"F1.opRevolve","SWEPT_FACE",FACE,{"disambiguationData":[OSD([sQuery(id+"F0.wireOp",EDGE,"E4")])]}),subQ31]});Q48=makeQuery(id+"F48.opFillet","BLEND_EDGE",EDGE,{"blendedFrom":[makeQuery(id+"F47.opFillet","TWEAK_EDGE",EDGE,{"derivedFrom":[makeQuery(id+"F45.opFillet","BLEND_VERTEX",VERTEX,{"blendedFrom":[subQ75,subQ31,subQ74],"blendedInto":[subQ31,subQ74]}),makeQuery(id+"F45.opFillet","BLEND_VERTEX",VERTEX,{"blendedFrom":[subQ75,makeQuery(id+"F42.boolean.opBoolean","MERGE",FACE,{"derivedFrom":[subQ0,subQ8]}),subQ74],"blendedInto":[makeQuery(id+"F42.boolean.opBoolean","MERGE",FACE,{"derivedFrom":[subQ0,subQ8]}),subQ74]})]}),makeQuery(id+"F47.opFillet","BLEND_FACE",FACE,{"disambiguationData":[OSD([subQ5,subQ7]),TDD([makeQuery(id+"F42.boolean.opBoolean","COPY",EDGE,{"disambiguationData":[TD([makeQuery(id+"F5.opLoft","SWEPT_FACE",FACE,{"disambiguationData":[OSD([subQ71,subQ70,sQuery(id+"F3.wireOp",EDGE,"E18.left"),sQuery(id+"F4.wireOp",EDGE,"E21"),subQ69,subQ68])]})])],"derivedFrom":subQ9})])]}),makeQuery(id+"F47.opFillet","BLEND_FACE",FACE,{"disambiguationData":[OSD([subQ5,subQ7]),TDD([makeQuery(id+"F42.boolean.opBoolean","COPY",EDGE,{"disambiguationData":[TD([makeQuery(id+"F6.opLoft","SWEPT_FACE",FACE,{"disambiguationData":[OSD([sQuery(id+"F3.wireOp",EDGE,"E20.15.0"),subQ67,subQ66,sQuery(id+"F4.wireOp",EDGE,"E26.15.0"),subQ65,subQ64])]})])],"derivedFrom":subQ9})])]}),makeQuery(id+"F47.opFillet","BLEND_FACE",FACE,{"disambiguationData":[OSD([subQ5,subQ7]),TDD([makeQuery(id+"F42.boolean.opBoolean","COPY",EDGE,{"disambiguationData":[TD([makeQuery(id+"F7.opLoft","SWEPT_FACE",FACE,{"disambiguationData":[OSD([sQuery(id+"F3.wireOp",EDGE,"E20.14.0"),subQ63,subQ62,sQuery(id+"F4.wireOp",EDGE,"E26.14.0"),subQ61,subQ60])]})])],"derivedFrom":subQ9})])]}),makeQuery(id+"F47.opFillet","BLEND_FACE",FACE,{"disambiguationData":[OSD([subQ5,subQ7]),TDD([makeQuery(id+"F42.boolean.opBoolean","COPY",EDGE,{"disambiguationData":[TD([makeQuery(id+"F8.opLoft","SWEPT_FACE",FACE,{"disambiguationData":[OSD([sQuery(id+"F3.wireOp",EDGE,"E20.13.0"),subQ59,subQ58,sQuery(id+"F4.wireOp",EDGE,"E26.13.0"),subQ57,subQ56])]})])],"derivedFrom":subQ9})])]}),makeQuery(id+"F47.opFillet","BLEND_FACE",FACE,{"disambiguationData":[OSD([subQ5,subQ7]),TDD([makeQuery(id+"F42.boolean.opBoolean","COPY",EDGE,{"disambiguationData":[TD([makeQuery(id+"F9.opLoft","SWEPT_FACE",FACE,{"disambiguationData":[OSD([sQuery(id+"F3.wireOp",EDGE,"E20.12.0"),subQ55,subQ54,sQuery(id+"F4.wireOp",EDGE,"E26.12.0"),subQ53,subQ52])]})])],"derivedFrom":subQ9})])]}),makeQuery(id+"F47.opFillet","BLEND_FACE",FACE,{"disambiguationData":[OSD([subQ5,subQ7]),TDD([makeQuery(id+"F42.boolean.opBoolean","COPY",EDGE,{"disambiguationData":[TD([makeQuery(id+"F10.opLoft","SWEPT_FACE",FACE,{"disambiguationData":[OSD([sQuery(id+"F3.wireOp",EDGE,"E20.11.0"),subQ51,subQ50,sQuery(id+"F4.wireOp",EDGE,"E26.11.0"),subQ49,subQ48])]})])],"derivedFrom":subQ9})])]}),makeQuery(id+"F47.opFillet","BLEND_FACE",FACE,{"disambiguationData":[OSD([subQ5,subQ7]),TDD([makeQuery(id+"F42.boolean.opBoolean","COPY",EDGE,{"disambiguationData":[TD([makeQuery(id+"F11.opLoft","SWEPT_FACE",FACE,{"disambiguationData":[OSD([sQuery(id+"F3.wireOp",EDGE,"E20.10.0"),subQ47,subQ46,sQuery(id+"F4.wireOp",EDGE,"E26.10.0"),subQ45,subQ44])]})])],"derivedFrom":subQ9})])]}),makeQuery(id+"F47.opFillet","BLEND_FACE",FACE,{"disambiguationData":[OSD([subQ5,subQ7]),TDD([makeQuery(id+"F42.boolean.opBoolean","COPY",EDGE,{"disambiguationData":[TD([makeQuery(id+"F12.opLoft","SWEPT_FACE",FACE,{"disambiguationData":[OSD([sQuery(id+"F3.wireOp",EDGE,"E20.9.0"),subQ43,subQ42,sQuery(id+"F4.wireOp",EDGE,"E26.9.0"),subQ41,subQ40])]})])],"derivedFrom":subQ9})])]}),makeQuery(id+"F47.opFillet","BLEND_FACE",FACE,{"disambiguationData":[OSD([subQ5,subQ7]),TDD([makeQuery(id+"F42.boolean.opBoolean","COPY",EDGE,{"disambiguationData":[TD([makeQuery(id+"F13.opLoft","SWEPT_FACE",FACE,{"disambiguationData":[OSD([sQuery(id+"F3.wireOp",EDGE,"E20.8.0"),subQ39,subQ38,sQuery(id+"F4.wireOp",EDGE,"E26.8.0"),subQ37,subQ36])]})])],"derivedFrom":subQ9})])]}),makeQuery(id+"F47.opFillet","BLEND_FACE",FACE,{"disambiguationData":[OSD([subQ5,subQ7]),TDD([makeQuery(id+"F42.boolean.opBoolean","COPY",EDGE,{"disambiguationData":[TD([makeQuery(id+"F14.opLoft","SWEPT_FACE",FACE,{"disambiguationData":[OSD([sQuery(id+"F3.wireOp",EDGE,"E20.7.0"),subQ35,subQ34,sQuery(id+"F4.wireOp",EDGE,"E26.7.0"),subQ33,subQ32])]})])],"derivedFrom":subQ9})])]}),makeQuery(id+"F47.opFillet","BLEND_FACE",FACE,{"disambiguationData":[OSD([subQ5,subQ7]),TDD([makeQuery(id+"F42.boolean.opBoolean","COPY",EDGE,{"disambiguationData":[TD([subQ31])],"derivedFrom":subQ9})])]}),makeQuery(id+"F47.opFillet","BLEND_FACE",FACE,{"disambiguationData":[OSD([subQ5,subQ7]),TDD([makeQuery(id+"F42.boolean.opBoolean","COPY",EDGE,{"disambiguationData":[TD([makeQuery(id+"F16.opLoft","SWEPT_FACE",FACE,{"disambiguationData":[OSD([sQuery(id+"F3.wireOp",EDGE,"E20.5.0"),subQ25,subQ24,sQuery(id+"F4.wireOp",EDGE,"E26.5.0"),subQ23,subQ22])]})])],"derivedFrom":subQ9})])]}),makeQuery(id+"F47.opFillet","BLEND_FACE",FACE,{"disambiguationData":[OSD([subQ5,subQ7]),TDD([makeQuery(id+"F42.boolean.opBoolean","COPY",EDGE,{"disambiguationData":[TD([makeQuery(id+"F17.opLoft","SWEPT_FACE",FACE,{"disambiguationData":[OSD([sQuery(id+"F3.wireOp",EDGE,"E20.4.0"),subQ21,subQ20,sQuery(id+"F4.wireOp",EDGE,"E26.4.0"),subQ19,subQ18])]})])],"derivedFrom":subQ9})])]}),makeQuery(id+"F47.opFillet","BLEND_FACE",FACE,{"disambiguationData":[OSD([subQ5,subQ7]),TDD([makeQuery(id+"F42.boolean.opBoolean","COPY",EDGE,{"disambiguationData":[TD([makeQuery(id+"F18.opLoft","SWEPT_FACE",FACE,{"disambiguationData":[OSD([sQuery(id+"F3.wireOp",EDGE,"E20.3.0"),subQ17,subQ16,sQuery(id+"F4.wireOp",EDGE,"E26.3.0"),subQ15,subQ14])]})])],"derivedFrom":subQ9})])]}),makeQuery(id+"F47.opFillet","BLEND_FACE",FACE,{"disambiguationData":[OSD([subQ5,subQ7]),TDD([makeQuery(id+"F42.boolean.opBoolean","COPY",EDGE,{"disambiguationData":[TD([makeQuery(id+"F19.opLoft","SWEPT_FACE",FACE,{"disambiguationData":[OSD([sQuery(id+"F3.wireOp",EDGE,"E20.2.0"),subQ13,subQ12,sQuery(id+"F4.wireOp",EDGE,"E26.2.0"),subQ11,subQ10])]})])],"derivedFrom":subQ9})])]}),makeQuery(id+"F47.opFillet","BLEND_FACE",FACE,{"disambiguationData":[OSD([subQ5,subQ7]),TDD([makeQuery(id+"F42.boolean.opBoolean","COPY",EDGE,{"disambiguationData":[TD([makeQuery(id+"F20.opLoft","SWEPT_FACE",FACE,{"disambiguationData":[OSD([sQuery(id+"F3.wireOp",EDGE,"E20.1.0"),subQ4,subQ3,sQuery(id+"F4.wireOp",EDGE,"E26.1.0"),subQ2,subQ1])]})])],"derivedFrom":subQ9})])]})],"blendedInto":[makeQuery(id+"F47.opFillet","BLEND_FACE",FACE,{"disambiguationData":[OSD([subQ5,subQ7]),TDD([makeQuery(id+"F42.boolean.opBoolean","COPY",EDGE,{"disambiguationData":[TD([makeQuery(id+"F5.opLoft","SWEPT_FACE",FACE,{"disambiguationData":[OSD([subQ71,subQ70,sQuery(id+"F3.wireOp",EDGE,"E18.left"),sQuery(id+"F4.wireOp",EDGE,"E21"),subQ69,subQ68])]})])],"derivedFrom":subQ9})])]}),makeQuery(id+"F47.opFillet","BLEND_FACE",FACE,{"disambiguationData":[OSD([subQ5,subQ7]),TDD([makeQuery(id+"F42.boolean.opBoolean","COPY",EDGE,{"disambiguationData":[TD([makeQuery(id+"F6.opLoft","SWEPT_FACE",FACE,{"disambiguationData":[OSD([sQuery(id+"F3.wireOp",EDGE,"E20.15.0"),subQ67,subQ66,sQuery(id+"F4.wireOp",EDGE,"E26.15.0"),subQ65,subQ64])]})])],"derivedFrom":subQ9})])]}),makeQuery(id+"F47.opFillet","BLEND_FACE",FACE,{"disambiguationData":[OSD([subQ5,subQ7]),TDD([makeQuery(id+"F42.boolean.opBoolean","COPY",EDGE,{"disambiguationData":[TD([makeQuery(id+"F7.opLoft","SWEPT_FACE",FACE,{"disambiguationData":[OSD([sQuery(id+"F3.wireOp",EDGE,"E20.14.0"),subQ63,subQ62,sQuery(id+"F4.wireOp",EDGE,"E26.14.0"),subQ61,subQ60])]})])],"derivedFrom":subQ9})])]}),makeQuery(id+"F47.opFillet","BLEND_FACE",FACE,{"disambiguationData":[OSD([subQ5,subQ7]),TDD([makeQuery(id+"F42.boolean.opBoolean","COPY",EDGE,{"disambiguationData":[TD([makeQuery(id+"F8.opLoft","SWEPT_FACE",FACE,{"disambiguationData":[OSD([sQuery(id+"F3.wireOp",EDGE,"E20.13.0"),subQ59,subQ58,sQuery(id+"F4.wireOp",EDGE,"E26.13.0"),subQ57,subQ56])]})])],"derivedFrom":subQ9})])]}),makeQuery(id+"F47.opFillet","BLEND_FACE",FACE,{"disambiguationData":[OSD([subQ5,subQ7]),TDD([makeQuery(id+"F42.boolean.opBoolean","COPY",EDGE,{"disambiguationData":[TD([makeQuery(id+"F9.opLoft","SWEPT_FACE",FACE,{"disambiguationData":[OSD([sQuery(id+"F3.wireOp",EDGE,"E20.12.0"),subQ55,subQ54,sQuery(id+"F4.wireOp",EDGE,"E26.12.0"),subQ53,subQ52])]})])],"derivedFrom":subQ9})])]}),makeQuery(id+"F47.opFillet","BLEND_FACE",FACE,{"disambiguationData":[OSD([subQ5,subQ7]),TDD([makeQuery(id+"F42.boolean.opBoolean","COPY",EDGE,{"disambiguationData":[TD([makeQuery(id+"F10.opLoft","SWEPT_FACE",FACE,{"disambiguationData":[OSD([sQuery(id+"F3.wireOp",EDGE,"E20.11.0"),subQ51,subQ50,sQuery(id+"F4.wireOp",EDGE,"E26.11.0"),subQ49,subQ48])]})])],"derivedFrom":subQ9})])]}),makeQuery(id+"F47.opFillet","BLEND_FACE",FACE,{"disambiguationData":[OSD([subQ5,subQ7]),TDD([makeQuery(id+"F42.boolean.opBoolean","COPY",EDGE,{"disambiguationData":[TD([makeQuery(id+"F11.opLoft","SWEPT_FACE",FACE,{"disambiguationData":[OSD([sQuery(id+"F3.wireOp",EDGE,"E20.10.0"),subQ47,subQ46,sQuery(id+"F4.wireOp",EDGE,"E26.10.0"),subQ45,subQ44])]})])],"derivedFrom":subQ9})])]}),makeQuery(id+"F47.opFillet","BLEND_FACE",FACE,{"disambiguationData":[OSD([subQ5,subQ7]),TDD([makeQuery(id+"F42.boolean.opBoolean","COPY",EDGE,{"disambiguationData":[TD([makeQuery(id+"F12.opLoft","SWEPT_FACE",FACE,{"disambiguationData":[OSD([sQuery(id+"F3.wireOp",EDGE,"E20.9.0"),subQ43,subQ42,sQuery(id+"F4.wireOp",EDGE,"E26.9.0"),subQ41,subQ40])]})])],"derivedFrom":subQ9})])]}),makeQuery(id+"F47.opFillet","BLEND_FACE",FACE,{"disambiguationData":[OSD([subQ5,subQ7]),TDD([makeQuery(id+"F42.boolean.opBoolean","COPY",EDGE,{"disambiguationData":[TD([makeQuery(id+"F13.opLoft","SWEPT_FACE",FACE,{"disambiguationData":[OSD([sQuery(id+"F3.wireOp",EDGE,"E20.8.0"),subQ39,subQ38,sQuery(id+"F4.wireOp",EDGE,"E26.8.0"),subQ37,subQ36])]})])],"derivedFrom":subQ9})])]}),makeQuery(id+"F47.opFillet","BLEND_FACE",FACE,{"disambiguationData":[OSD([subQ5,subQ7]),TDD([makeQuery(id+"F42.boolean.opBoolean","COPY",EDGE,{"disambiguationData":[TD([makeQuery(id+"F14.opLoft","SWEPT_FACE",FACE,{"disambiguationData":[OSD([sQuery(id+"F3.wireOp",EDGE,"E20.7.0"),subQ35,subQ34,sQuery(id+"F4.wireOp",EDGE,"E26.7.0"),subQ33,subQ32])]})])],"derivedFrom":subQ9})])]}),makeQuery(id+"F47.opFillet","BLEND_FACE",FACE,{"disambiguationData":[OSD([subQ5,subQ7]),TDD([makeQuery(id+"F42.boolean.opBoolean","COPY",EDGE,{"disambiguationData":[TD([subQ31])],"derivedFrom":subQ9})])]}),makeQuery(id+"F47.opFillet","BLEND_FACE",FACE,{"disambiguationData":[OSD([subQ5,subQ7]),TDD([makeQuery(id+"F42.boolean.opBoolean","COPY",EDGE,{"disambiguationData":[TD([makeQuery(id+"F16.opLoft","SWEPT_FACE",FACE,{"disambiguationData":[OSD([sQuery(id+"F3.wireOp",EDGE,"E20.5.0"),subQ25,subQ24,sQuery(id+"F4.wireOp",EDGE,"E26.5.0"),subQ23,subQ22])]})])],"derivedFrom":subQ9})])]}),makeQuery(id+"F47.opFillet","BLEND_FACE",FACE,{"disambiguationData":[OSD([subQ5,subQ7]),TDD([makeQuery(id+"F42.boolean.opBoolean","COPY",EDGE,{"disambiguationData":[TD([makeQuery(id+"F17.opLoft","SWEPT_FACE",FACE,{"disambiguationData":[OSD([sQuery(id+"F3.wireOp",EDGE,"E20.4.0"),subQ21,subQ20,sQuery(id+"F4.wireOp",EDGE,"E26.4.0"),subQ19,subQ18])]})])],"derivedFrom":subQ9})])]}),makeQuery(id+"F47.opFillet","BLEND_FACE",FACE,{"disambiguationData":[OSD([subQ5,subQ7]),TDD([makeQuery(id+"F42.boolean.opBoolean","COPY",EDGE,{"disambiguationData":[TD([makeQuery(id+"F18.opLoft","SWEPT_FACE",FACE,{"disambiguationData":[OSD([sQuery(id+"F3.wireOp",EDGE,"E20.3.0"),subQ17,subQ16,sQuery(id+"F4.wireOp",EDGE,"E26.3.0"),subQ15,subQ14])]})])],"derivedFrom":subQ9})])]}),makeQuery(id+"F47.opFillet","BLEND_FACE",FACE,{"disambiguationData":[OSD([subQ5,subQ7]),TDD([makeQuery(id+"F42.boolean.opBoolean","COPY",EDGE,{"disambiguationData":[TD([makeQuery(id+"F19.opLoft","SWEPT_FACE",FACE,{"disambiguationData":[OSD([sQuery(id+"F3.wireOp",EDGE,"E20.2.0"),subQ13,subQ12,sQuery(id+"F4.wireOp",EDGE,"E26.2.0"),subQ11,subQ10])]})])],"derivedFrom":subQ9})])]}),makeQuery(id+"F47.opFillet","BLEND_FACE",FACE,{"disambiguationData":[OSD([subQ5,subQ7]),TDD([makeQuery(id+"F42.boolean.opBoolean","COPY",EDGE,{"disambiguationData":[TD([makeQuery(id+"F20.opLoft","SWEPT_FACE",FACE,{"disambiguationData":[OSD([sQuery(id+"F3.wireOp",EDGE,"E20.1.0"),subQ4,subQ3,sQuery(id+"F4.wireOp",EDGE,"E26.1.0"),subQ2,subQ1])]})])],"derivedFrom":subQ9})])]})]});}
            var Q49;
            {var subQ0=makeQuery(id+"F40.opExtrude","CAP_FACE",FACE,{"disambiguationData":[OSD([sQuery(id+"F39.wireOp",EDGE,"E29"),sQuery(id+"F39.wireOp",EDGE,"E30")])],"isStart":false});var subQ1=sQuery(id+"F4.wireOp",EDGE,"E26.1.3");var subQ2=sQuery(id+"F4.wireOp",EDGE,"E26.1.2");var subQ3=sQuery(id+"F3.wireOp",EDGE,"E20.1.3");var subQ4=sQuery(id+"F3.wireOp",EDGE,"E20.1.1");var subQ5=sQuery(id+"F41.wireOp",EDGE,"E35");var subQ6=makeQuery(id+"F42.opRevolve","SWEPT_FACE",FACE,{"disambiguationData":[OSD([subQ5])]});var subQ7=sQuery(id+"F41.wireOp",EDGE,"E36");var subQ8=makeQuery(id+"F42.opRevolve","SWEPT_FACE",FACE,{"disambiguationData":[OSD([subQ7])]});var subQ9=makeQuery(id+"F42.opRevolve","SWEPT_EDGE",EDGE,{"disambiguationData":[OSD([subQ5,subQ7])]});var subQ10=sQuery(id+"F4.wireOp",EDGE,"E26.2.3");var subQ11=sQuery(id+"F4.wireOp",EDGE,"E26.2.2");var subQ12=sQuery(id+"F3.wireOp",EDGE,"E20.2.3");var subQ13=sQuery(id+"F3.wireOp",EDGE,"E20.2.1");var subQ14=sQuery(id+"F4.wireOp",EDGE,"E26.3.3");var subQ15=sQuery(id+"F4.wireOp",EDGE,"E26.3.2");var subQ16=sQuery(id+"F3.wireOp",EDGE,"E20.3.3");var subQ17=sQuery(id+"F3.wireOp",EDGE,"E20.3.1");var subQ18=sQuery(id+"F4.wireOp",EDGE,"E26.4.3");var subQ19=sQuery(id+"F4.wireOp",EDGE,"E26.4.2");var subQ20=sQuery(id+"F3.wireOp",EDGE,"E20.4.3");var subQ21=sQuery(id+"F3.wireOp",EDGE,"E20.4.1");var subQ22=sQuery(id+"F4.wireOp",EDGE,"E26.5.3");var subQ23=sQuery(id+"F4.wireOp",EDGE,"E26.5.2");var subQ24=sQuery(id+"F3.wireOp",EDGE,"E20.5.3");var subQ25=sQuery(id+"F3.wireOp",EDGE,"E20.5.1");var subQ27=makeQuery(id+"F16.opLoft","SWEPT_FACE",FACE,{"disambiguationData":[OSD([sQuery(id+"F3.wireOp",EDGE,"E20.5.0"),subQ25,subQ24,sQuery(id+"F4.wireOp",EDGE,"E26.5.0"),subQ23,subQ22])]});var subQ28=sQuery(id+"F4.wireOp",EDGE,"E26.6.3");var subQ29=sQuery(id+"F4.wireOp",EDGE,"E26.6.2");var subQ30=sQuery(id+"F3.wireOp",EDGE,"E20.6.3");var subQ31=sQuery(id+"F3.wireOp",EDGE,"E20.6.1");var subQ32=sQuery(id+"F4.wireOp",EDGE,"E26.7.3");var subQ33=sQuery(id+"F4.wireOp",EDGE,"E26.7.2");var subQ34=sQuery(id+"F3.wireOp",EDGE,"E20.7.3");var subQ35=sQuery(id+"F3.wireOp",EDGE,"E20.7.1");var subQ36=sQuery(id+"F4.wireOp",EDGE,"E26.8.3");var subQ37=sQuery(id+"F4.wireOp",EDGE,"E26.8.2");var subQ38=sQuery(id+"F3.wireOp",EDGE,"E20.8.3");var subQ39=sQuery(id+"F3.wireOp",EDGE,"E20.8.1");var subQ40=sQuery(id+"F4.wireOp",EDGE,"E26.9.3");var subQ41=sQuery(id+"F4.wireOp",EDGE,"E26.9.2");var subQ42=sQuery(id+"F3.wireOp",EDGE,"E20.9.3");var subQ43=sQuery(id+"F3.wireOp",EDGE,"E20.9.1");var subQ44=sQuery(id+"F4.wireOp",EDGE,"E26.10.3");var subQ45=sQuery(id+"F4.wireOp",EDGE,"E26.10.2");var subQ46=sQuery(id+"F3.wireOp",EDGE,"E20.10.3");var subQ47=sQuery(id+"F3.wireOp",EDGE,"E20.10.1");var subQ48=sQuery(id+"F4.wireOp",EDGE,"E26.11.3");var subQ49=sQuery(id+"F4.wireOp",EDGE,"E26.11.2");var subQ50=sQuery(id+"F3.wireOp",EDGE,"E20.11.3");var subQ51=sQuery(id+"F3.wireOp",EDGE,"E20.11.1");var subQ52=sQuery(id+"F4.wireOp",EDGE,"E26.12.3");var subQ53=sQuery(id+"F4.wireOp",EDGE,"E26.12.2");var subQ54=sQuery(id+"F3.wireOp",EDGE,"E20.12.3");var subQ55=sQuery(id+"F3.wireOp",EDGE,"E20.12.1");var subQ56=sQuery(id+"F4.wireOp",EDGE,"E26.13.3");var subQ57=sQuery(id+"F4.wireOp",EDGE,"E26.13.2");var subQ58=sQuery(id+"F3.wireOp",EDGE,"E20.13.3");var subQ59=sQuery(id+"F3.wireOp",EDGE,"E20.13.1");var subQ60=sQuery(id+"F4.wireOp",EDGE,"E26.14.3");var subQ61=sQuery(id+"F4.wireOp",EDGE,"E26.14.2");var subQ62=sQuery(id+"F3.wireOp",EDGE,"E20.14.3");var subQ63=sQuery(id+"F3.wireOp",EDGE,"E20.14.1");var subQ64=sQuery(id+"F4.wireOp",EDGE,"E26.15.3");var subQ65=sQuery(id+"F4.wireOp",EDGE,"E26.15.2");var subQ66=sQuery(id+"F3.wireOp",EDGE,"E20.15.3");var subQ67=sQuery(id+"F3.wireOp",EDGE,"E20.15.1");var subQ68=sQuery(id+"F4.wireOp",EDGE,"E23");var subQ69=sQuery(id+"F4.wireOp",EDGE,"E22");var subQ70=sQuery(id+"F3.wireOp",EDGE,"E18.top");var subQ71=sQuery(id+"F3.wireOp",EDGE,"E18.bottom");var subQ74=makeQuery(id+"F42.boolean.opBoolean","COPY",FACE,{"disambiguationData":[TD([subQ27])],"derivedFrom":subQ6});var subQ75=makeQuery(id+"F16.boolean.opBoolean","INTERSECT",EDGE,{"derivedFrom":[makeQuery(id+"F1.opRevolve","SWEPT_FACE",FACE,{"disambiguationData":[OSD([sQuery(id+"F0.wireOp",EDGE,"E4")])]}),subQ27]});Q49=makeQuery(id+"F48.opFillet","BLEND_EDGE",EDGE,{"blendedFrom":[makeQuery(id+"F47.opFillet","TWEAK_EDGE",EDGE,{"derivedFrom":[makeQuery(id+"F45.opFillet","BLEND_VERTEX",VERTEX,{"blendedFrom":[subQ75,subQ27,subQ74],"blendedInto":[subQ27,subQ74]}),makeQuery(id+"F45.opFillet","BLEND_VERTEX",VERTEX,{"blendedFrom":[subQ75,makeQuery(id+"F42.boolean.opBoolean","MERGE",FACE,{"derivedFrom":[subQ0,subQ8]}),subQ74],"blendedInto":[makeQuery(id+"F42.boolean.opBoolean","MERGE",FACE,{"derivedFrom":[subQ0,subQ8]}),subQ74]})]}),makeQuery(id+"F47.opFillet","BLEND_FACE",FACE,{"disambiguationData":[OSD([subQ5,subQ7]),TDD([makeQuery(id+"F42.boolean.opBoolean","COPY",EDGE,{"disambiguationData":[TD([makeQuery(id+"F5.opLoft","SWEPT_FACE",FACE,{"disambiguationData":[OSD([subQ71,subQ70,sQuery(id+"F3.wireOp",EDGE,"E18.left"),sQuery(id+"F4.wireOp",EDGE,"E21"),subQ69,subQ68])]})])],"derivedFrom":subQ9})])]}),makeQuery(id+"F47.opFillet","BLEND_FACE",FACE,{"disambiguationData":[OSD([subQ5,subQ7]),TDD([makeQuery(id+"F42.boolean.opBoolean","COPY",EDGE,{"disambiguationData":[TD([makeQuery(id+"F6.opLoft","SWEPT_FACE",FACE,{"disambiguationData":[OSD([sQuery(id+"F3.wireOp",EDGE,"E20.15.0"),subQ67,subQ66,sQuery(id+"F4.wireOp",EDGE,"E26.15.0"),subQ65,subQ64])]})])],"derivedFrom":subQ9})])]}),makeQuery(id+"F47.opFillet","BLEND_FACE",FACE,{"disambiguationData":[OSD([subQ5,subQ7]),TDD([makeQuery(id+"F42.boolean.opBoolean","COPY",EDGE,{"disambiguationData":[TD([makeQuery(id+"F7.opLoft","SWEPT_FACE",FACE,{"disambiguationData":[OSD([sQuery(id+"F3.wireOp",EDGE,"E20.14.0"),subQ63,subQ62,sQuery(id+"F4.wireOp",EDGE,"E26.14.0"),subQ61,subQ60])]})])],"derivedFrom":subQ9})])]}),makeQuery(id+"F47.opFillet","BLEND_FACE",FACE,{"disambiguationData":[OSD([subQ5,subQ7]),TDD([makeQuery(id+"F42.boolean.opBoolean","COPY",EDGE,{"disambiguationData":[TD([makeQuery(id+"F8.opLoft","SWEPT_FACE",FACE,{"disambiguationData":[OSD([sQuery(id+"F3.wireOp",EDGE,"E20.13.0"),subQ59,subQ58,sQuery(id+"F4.wireOp",EDGE,"E26.13.0"),subQ57,subQ56])]})])],"derivedFrom":subQ9})])]}),makeQuery(id+"F47.opFillet","BLEND_FACE",FACE,{"disambiguationData":[OSD([subQ5,subQ7]),TDD([makeQuery(id+"F42.boolean.opBoolean","COPY",EDGE,{"disambiguationData":[TD([makeQuery(id+"F9.opLoft","SWEPT_FACE",FACE,{"disambiguationData":[OSD([sQuery(id+"F3.wireOp",EDGE,"E20.12.0"),subQ55,subQ54,sQuery(id+"F4.wireOp",EDGE,"E26.12.0"),subQ53,subQ52])]})])],"derivedFrom":subQ9})])]}),makeQuery(id+"F47.opFillet","BLEND_FACE",FACE,{"disambiguationData":[OSD([subQ5,subQ7]),TDD([makeQuery(id+"F42.boolean.opBoolean","COPY",EDGE,{"disambiguationData":[TD([makeQuery(id+"F10.opLoft","SWEPT_FACE",FACE,{"disambiguationData":[OSD([sQuery(id+"F3.wireOp",EDGE,"E20.11.0"),subQ51,subQ50,sQuery(id+"F4.wireOp",EDGE,"E26.11.0"),subQ49,subQ48])]})])],"derivedFrom":subQ9})])]}),makeQuery(id+"F47.opFillet","BLEND_FACE",FACE,{"disambiguationData":[OSD([subQ5,subQ7]),TDD([makeQuery(id+"F42.boolean.opBoolean","COPY",EDGE,{"disambiguationData":[TD([makeQuery(id+"F11.opLoft","SWEPT_FACE",FACE,{"disambiguationData":[OSD([sQuery(id+"F3.wireOp",EDGE,"E20.10.0"),subQ47,subQ46,sQuery(id+"F4.wireOp",EDGE,"E26.10.0"),subQ45,subQ44])]})])],"derivedFrom":subQ9})])]}),makeQuery(id+"F47.opFillet","BLEND_FACE",FACE,{"disambiguationData":[OSD([subQ5,subQ7]),TDD([makeQuery(id+"F42.boolean.opBoolean","COPY",EDGE,{"disambiguationData":[TD([makeQuery(id+"F12.opLoft","SWEPT_FACE",FACE,{"disambiguationData":[OSD([sQuery(id+"F3.wireOp",EDGE,"E20.9.0"),subQ43,subQ42,sQuery(id+"F4.wireOp",EDGE,"E26.9.0"),subQ41,subQ40])]})])],"derivedFrom":subQ9})])]}),makeQuery(id+"F47.opFillet","BLEND_FACE",FACE,{"disambiguationData":[OSD([subQ5,subQ7]),TDD([makeQuery(id+"F42.boolean.opBoolean","COPY",EDGE,{"disambiguationData":[TD([makeQuery(id+"F13.opLoft","SWEPT_FACE",FACE,{"disambiguationData":[OSD([sQuery(id+"F3.wireOp",EDGE,"E20.8.0"),subQ39,subQ38,sQuery(id+"F4.wireOp",EDGE,"E26.8.0"),subQ37,subQ36])]})])],"derivedFrom":subQ9})])]}),makeQuery(id+"F47.opFillet","BLEND_FACE",FACE,{"disambiguationData":[OSD([subQ5,subQ7]),TDD([makeQuery(id+"F42.boolean.opBoolean","COPY",EDGE,{"disambiguationData":[TD([makeQuery(id+"F14.opLoft","SWEPT_FACE",FACE,{"disambiguationData":[OSD([sQuery(id+"F3.wireOp",EDGE,"E20.7.0"),subQ35,subQ34,sQuery(id+"F4.wireOp",EDGE,"E26.7.0"),subQ33,subQ32])]})])],"derivedFrom":subQ9})])]}),makeQuery(id+"F47.opFillet","BLEND_FACE",FACE,{"disambiguationData":[OSD([subQ5,subQ7]),TDD([makeQuery(id+"F42.boolean.opBoolean","COPY",EDGE,{"disambiguationData":[TD([makeQuery(id+"F15.opLoft","SWEPT_FACE",FACE,{"disambiguationData":[OSD([sQuery(id+"F3.wireOp",EDGE,"E20.6.0"),subQ31,subQ30,sQuery(id+"F4.wireOp",EDGE,"E26.6.0"),subQ29,subQ28])]})])],"derivedFrom":subQ9})])]}),makeQuery(id+"F47.opFillet","BLEND_FACE",FACE,{"disambiguationData":[OSD([subQ5,subQ7]),TDD([makeQuery(id+"F42.boolean.opBoolean","COPY",EDGE,{"disambiguationData":[TD([subQ27])],"derivedFrom":subQ9})])]}),makeQuery(id+"F47.opFillet","BLEND_FACE",FACE,{"disambiguationData":[OSD([subQ5,subQ7]),TDD([makeQuery(id+"F42.boolean.opBoolean","COPY",EDGE,{"disambiguationData":[TD([makeQuery(id+"F17.opLoft","SWEPT_FACE",FACE,{"disambiguationData":[OSD([sQuery(id+"F3.wireOp",EDGE,"E20.4.0"),subQ21,subQ20,sQuery(id+"F4.wireOp",EDGE,"E26.4.0"),subQ19,subQ18])]})])],"derivedFrom":subQ9})])]}),makeQuery(id+"F47.opFillet","BLEND_FACE",FACE,{"disambiguationData":[OSD([subQ5,subQ7]),TDD([makeQuery(id+"F42.boolean.opBoolean","COPY",EDGE,{"disambiguationData":[TD([makeQuery(id+"F18.opLoft","SWEPT_FACE",FACE,{"disambiguationData":[OSD([sQuery(id+"F3.wireOp",EDGE,"E20.3.0"),subQ17,subQ16,sQuery(id+"F4.wireOp",EDGE,"E26.3.0"),subQ15,subQ14])]})])],"derivedFrom":subQ9})])]}),makeQuery(id+"F47.opFillet","BLEND_FACE",FACE,{"disambiguationData":[OSD([subQ5,subQ7]),TDD([makeQuery(id+"F42.boolean.opBoolean","COPY",EDGE,{"disambiguationData":[TD([makeQuery(id+"F19.opLoft","SWEPT_FACE",FACE,{"disambiguationData":[OSD([sQuery(id+"F3.wireOp",EDGE,"E20.2.0"),subQ13,subQ12,sQuery(id+"F4.wireOp",EDGE,"E26.2.0"),subQ11,subQ10])]})])],"derivedFrom":subQ9})])]}),makeQuery(id+"F47.opFillet","BLEND_FACE",FACE,{"disambiguationData":[OSD([subQ5,subQ7]),TDD([makeQuery(id+"F42.boolean.opBoolean","COPY",EDGE,{"disambiguationData":[TD([makeQuery(id+"F20.opLoft","SWEPT_FACE",FACE,{"disambiguationData":[OSD([sQuery(id+"F3.wireOp",EDGE,"E20.1.0"),subQ4,subQ3,sQuery(id+"F4.wireOp",EDGE,"E26.1.0"),subQ2,subQ1])]})])],"derivedFrom":subQ9})])]})],"blendedInto":[makeQuery(id+"F47.opFillet","BLEND_FACE",FACE,{"disambiguationData":[OSD([subQ5,subQ7]),TDD([makeQuery(id+"F42.boolean.opBoolean","COPY",EDGE,{"disambiguationData":[TD([makeQuery(id+"F5.opLoft","SWEPT_FACE",FACE,{"disambiguationData":[OSD([subQ71,subQ70,sQuery(id+"F3.wireOp",EDGE,"E18.left"),sQuery(id+"F4.wireOp",EDGE,"E21"),subQ69,subQ68])]})])],"derivedFrom":subQ9})])]}),makeQuery(id+"F47.opFillet","BLEND_FACE",FACE,{"disambiguationData":[OSD([subQ5,subQ7]),TDD([makeQuery(id+"F42.boolean.opBoolean","COPY",EDGE,{"disambiguationData":[TD([makeQuery(id+"F6.opLoft","SWEPT_FACE",FACE,{"disambiguationData":[OSD([sQuery(id+"F3.wireOp",EDGE,"E20.15.0"),subQ67,subQ66,sQuery(id+"F4.wireOp",EDGE,"E26.15.0"),subQ65,subQ64])]})])],"derivedFrom":subQ9})])]}),makeQuery(id+"F47.opFillet","BLEND_FACE",FACE,{"disambiguationData":[OSD([subQ5,subQ7]),TDD([makeQuery(id+"F42.boolean.opBoolean","COPY",EDGE,{"disambiguationData":[TD([makeQuery(id+"F7.opLoft","SWEPT_FACE",FACE,{"disambiguationData":[OSD([sQuery(id+"F3.wireOp",EDGE,"E20.14.0"),subQ63,subQ62,sQuery(id+"F4.wireOp",EDGE,"E26.14.0"),subQ61,subQ60])]})])],"derivedFrom":subQ9})])]}),makeQuery(id+"F47.opFillet","BLEND_FACE",FACE,{"disambiguationData":[OSD([subQ5,subQ7]),TDD([makeQuery(id+"F42.boolean.opBoolean","COPY",EDGE,{"disambiguationData":[TD([makeQuery(id+"F8.opLoft","SWEPT_FACE",FACE,{"disambiguationData":[OSD([sQuery(id+"F3.wireOp",EDGE,"E20.13.0"),subQ59,subQ58,sQuery(id+"F4.wireOp",EDGE,"E26.13.0"),subQ57,subQ56])]})])],"derivedFrom":subQ9})])]}),makeQuery(id+"F47.opFillet","BLEND_FACE",FACE,{"disambiguationData":[OSD([subQ5,subQ7]),TDD([makeQuery(id+"F42.boolean.opBoolean","COPY",EDGE,{"disambiguationData":[TD([makeQuery(id+"F9.opLoft","SWEPT_FACE",FACE,{"disambiguationData":[OSD([sQuery(id+"F3.wireOp",EDGE,"E20.12.0"),subQ55,subQ54,sQuery(id+"F4.wireOp",EDGE,"E26.12.0"),subQ53,subQ52])]})])],"derivedFrom":subQ9})])]}),makeQuery(id+"F47.opFillet","BLEND_FACE",FACE,{"disambiguationData":[OSD([subQ5,subQ7]),TDD([makeQuery(id+"F42.boolean.opBoolean","COPY",EDGE,{"disambiguationData":[TD([makeQuery(id+"F10.opLoft","SWEPT_FACE",FACE,{"disambiguationData":[OSD([sQuery(id+"F3.wireOp",EDGE,"E20.11.0"),subQ51,subQ50,sQuery(id+"F4.wireOp",EDGE,"E26.11.0"),subQ49,subQ48])]})])],"derivedFrom":subQ9})])]}),makeQuery(id+"F47.opFillet","BLEND_FACE",FACE,{"disambiguationData":[OSD([subQ5,subQ7]),TDD([makeQuery(id+"F42.boolean.opBoolean","COPY",EDGE,{"disambiguationData":[TD([makeQuery(id+"F11.opLoft","SWEPT_FACE",FACE,{"disambiguationData":[OSD([sQuery(id+"F3.wireOp",EDGE,"E20.10.0"),subQ47,subQ46,sQuery(id+"F4.wireOp",EDGE,"E26.10.0"),subQ45,subQ44])]})])],"derivedFrom":subQ9})])]}),makeQuery(id+"F47.opFillet","BLEND_FACE",FACE,{"disambiguationData":[OSD([subQ5,subQ7]),TDD([makeQuery(id+"F42.boolean.opBoolean","COPY",EDGE,{"disambiguationData":[TD([makeQuery(id+"F12.opLoft","SWEPT_FACE",FACE,{"disambiguationData":[OSD([sQuery(id+"F3.wireOp",EDGE,"E20.9.0"),subQ43,subQ42,sQuery(id+"F4.wireOp",EDGE,"E26.9.0"),subQ41,subQ40])]})])],"derivedFrom":subQ9})])]}),makeQuery(id+"F47.opFillet","BLEND_FACE",FACE,{"disambiguationData":[OSD([subQ5,subQ7]),TDD([makeQuery(id+"F42.boolean.opBoolean","COPY",EDGE,{"disambiguationData":[TD([makeQuery(id+"F13.opLoft","SWEPT_FACE",FACE,{"disambiguationData":[OSD([sQuery(id+"F3.wireOp",EDGE,"E20.8.0"),subQ39,subQ38,sQuery(id+"F4.wireOp",EDGE,"E26.8.0"),subQ37,subQ36])]})])],"derivedFrom":subQ9})])]}),makeQuery(id+"F47.opFillet","BLEND_FACE",FACE,{"disambiguationData":[OSD([subQ5,subQ7]),TDD([makeQuery(id+"F42.boolean.opBoolean","COPY",EDGE,{"disambiguationData":[TD([makeQuery(id+"F14.opLoft","SWEPT_FACE",FACE,{"disambiguationData":[OSD([sQuery(id+"F3.wireOp",EDGE,"E20.7.0"),subQ35,subQ34,sQuery(id+"F4.wireOp",EDGE,"E26.7.0"),subQ33,subQ32])]})])],"derivedFrom":subQ9})])]}),makeQuery(id+"F47.opFillet","BLEND_FACE",FACE,{"disambiguationData":[OSD([subQ5,subQ7]),TDD([makeQuery(id+"F42.boolean.opBoolean","COPY",EDGE,{"disambiguationData":[TD([makeQuery(id+"F15.opLoft","SWEPT_FACE",FACE,{"disambiguationData":[OSD([sQuery(id+"F3.wireOp",EDGE,"E20.6.0"),subQ31,subQ30,sQuery(id+"F4.wireOp",EDGE,"E26.6.0"),subQ29,subQ28])]})])],"derivedFrom":subQ9})])]}),makeQuery(id+"F47.opFillet","BLEND_FACE",FACE,{"disambiguationData":[OSD([subQ5,subQ7]),TDD([makeQuery(id+"F42.boolean.opBoolean","COPY",EDGE,{"disambiguationData":[TD([subQ27])],"derivedFrom":subQ9})])]}),makeQuery(id+"F47.opFillet","BLEND_FACE",FACE,{"disambiguationData":[OSD([subQ5,subQ7]),TDD([makeQuery(id+"F42.boolean.opBoolean","COPY",EDGE,{"disambiguationData":[TD([makeQuery(id+"F17.opLoft","SWEPT_FACE",FACE,{"disambiguationData":[OSD([sQuery(id+"F3.wireOp",EDGE,"E20.4.0"),subQ21,subQ20,sQuery(id+"F4.wireOp",EDGE,"E26.4.0"),subQ19,subQ18])]})])],"derivedFrom":subQ9})])]}),makeQuery(id+"F47.opFillet","BLEND_FACE",FACE,{"disambiguationData":[OSD([subQ5,subQ7]),TDD([makeQuery(id+"F42.boolean.opBoolean","COPY",EDGE,{"disambiguationData":[TD([makeQuery(id+"F18.opLoft","SWEPT_FACE",FACE,{"disambiguationData":[OSD([sQuery(id+"F3.wireOp",EDGE,"E20.3.0"),subQ17,subQ16,sQuery(id+"F4.wireOp",EDGE,"E26.3.0"),subQ15,subQ14])]})])],"derivedFrom":subQ9})])]}),makeQuery(id+"F47.opFillet","BLEND_FACE",FACE,{"disambiguationData":[OSD([subQ5,subQ7]),TDD([makeQuery(id+"F42.boolean.opBoolean","COPY",EDGE,{"disambiguationData":[TD([makeQuery(id+"F19.opLoft","SWEPT_FACE",FACE,{"disambiguationData":[OSD([sQuery(id+"F3.wireOp",EDGE,"E20.2.0"),subQ13,subQ12,sQuery(id+"F4.wireOp",EDGE,"E26.2.0"),subQ11,subQ10])]})])],"derivedFrom":subQ9})])]}),makeQuery(id+"F47.opFillet","BLEND_FACE",FACE,{"disambiguationData":[OSD([subQ5,subQ7]),TDD([makeQuery(id+"F42.boolean.opBoolean","COPY",EDGE,{"disambiguationData":[TD([makeQuery(id+"F20.opLoft","SWEPT_FACE",FACE,{"disambiguationData":[OSD([sQuery(id+"F3.wireOp",EDGE,"E20.1.0"),subQ4,subQ3,sQuery(id+"F4.wireOp",EDGE,"E26.1.0"),subQ2,subQ1])]})])],"derivedFrom":subQ9})])]})]});}
            var Q50;
            {var subQ0=makeQuery(id+"F40.opExtrude","CAP_FACE",FACE,{"disambiguationData":[OSD([sQuery(id+"F39.wireOp",EDGE,"E29"),sQuery(id+"F39.wireOp",EDGE,"E30")])],"isStart":false});var subQ1=sQuery(id+"F4.wireOp",EDGE,"E26.1.3");var subQ2=sQuery(id+"F4.wireOp",EDGE,"E26.1.2");var subQ3=sQuery(id+"F3.wireOp",EDGE,"E20.1.3");var subQ4=sQuery(id+"F3.wireOp",EDGE,"E20.1.1");var subQ5=sQuery(id+"F41.wireOp",EDGE,"E35");var subQ6=makeQuery(id+"F42.opRevolve","SWEPT_FACE",FACE,{"disambiguationData":[OSD([subQ5])]});var subQ7=sQuery(id+"F41.wireOp",EDGE,"E36");var subQ8=makeQuery(id+"F42.opRevolve","SWEPT_FACE",FACE,{"disambiguationData":[OSD([subQ7])]});var subQ9=makeQuery(id+"F42.opRevolve","SWEPT_EDGE",EDGE,{"disambiguationData":[OSD([subQ5,subQ7])]});var subQ10=sQuery(id+"F4.wireOp",EDGE,"E26.2.3");var subQ11=sQuery(id+"F4.wireOp",EDGE,"E26.2.2");var subQ12=sQuery(id+"F3.wireOp",EDGE,"E20.2.3");var subQ13=sQuery(id+"F3.wireOp",EDGE,"E20.2.1");var subQ14=sQuery(id+"F4.wireOp",EDGE,"E26.3.3");var subQ15=sQuery(id+"F4.wireOp",EDGE,"E26.3.2");var subQ16=sQuery(id+"F3.wireOp",EDGE,"E20.3.3");var subQ17=sQuery(id+"F3.wireOp",EDGE,"E20.3.1");var subQ18=sQuery(id+"F4.wireOp",EDGE,"E26.4.3");var subQ19=sQuery(id+"F4.wireOp",EDGE,"E26.4.2");var subQ20=sQuery(id+"F3.wireOp",EDGE,"E20.4.3");var subQ21=sQuery(id+"F3.wireOp",EDGE,"E20.4.1");var subQ23=makeQuery(id+"F17.opLoft","SWEPT_FACE",FACE,{"disambiguationData":[OSD([sQuery(id+"F3.wireOp",EDGE,"E20.4.0"),subQ21,subQ20,sQuery(id+"F4.wireOp",EDGE,"E26.4.0"),subQ19,subQ18])]});var subQ24=sQuery(id+"F4.wireOp",EDGE,"E26.5.3");var subQ25=sQuery(id+"F4.wireOp",EDGE,"E26.5.2");var subQ26=sQuery(id+"F3.wireOp",EDGE,"E20.5.3");var subQ27=sQuery(id+"F3.wireOp",EDGE,"E20.5.1");var subQ28=sQuery(id+"F4.wireOp",EDGE,"E26.6.3");var subQ29=sQuery(id+"F4.wireOp",EDGE,"E26.6.2");var subQ30=sQuery(id+"F3.wireOp",EDGE,"E20.6.3");var subQ31=sQuery(id+"F3.wireOp",EDGE,"E20.6.1");var subQ32=sQuery(id+"F4.wireOp",EDGE,"E26.7.3");var subQ33=sQuery(id+"F4.wireOp",EDGE,"E26.7.2");var subQ34=sQuery(id+"F3.wireOp",EDGE,"E20.7.3");var subQ35=sQuery(id+"F3.wireOp",EDGE,"E20.7.1");var subQ36=sQuery(id+"F4.wireOp",EDGE,"E26.8.3");var subQ37=sQuery(id+"F4.wireOp",EDGE,"E26.8.2");var subQ38=sQuery(id+"F3.wireOp",EDGE,"E20.8.3");var subQ39=sQuery(id+"F3.wireOp",EDGE,"E20.8.1");var subQ40=sQuery(id+"F4.wireOp",EDGE,"E26.9.3");var subQ41=sQuery(id+"F4.wireOp",EDGE,"E26.9.2");var subQ42=sQuery(id+"F3.wireOp",EDGE,"E20.9.3");var subQ43=sQuery(id+"F3.wireOp",EDGE,"E20.9.1");var subQ44=sQuery(id+"F4.wireOp",EDGE,"E26.10.3");var subQ45=sQuery(id+"F4.wireOp",EDGE,"E26.10.2");var subQ46=sQuery(id+"F3.wireOp",EDGE,"E20.10.3");var subQ47=sQuery(id+"F3.wireOp",EDGE,"E20.10.1");var subQ48=sQuery(id+"F4.wireOp",EDGE,"E26.11.3");var subQ49=sQuery(id+"F4.wireOp",EDGE,"E26.11.2");var subQ50=sQuery(id+"F3.wireOp",EDGE,"E20.11.3");var subQ51=sQuery(id+"F3.wireOp",EDGE,"E20.11.1");var subQ52=sQuery(id+"F4.wireOp",EDGE,"E26.12.3");var subQ53=sQuery(id+"F4.wireOp",EDGE,"E26.12.2");var subQ54=sQuery(id+"F3.wireOp",EDGE,"E20.12.3");var subQ55=sQuery(id+"F3.wireOp",EDGE,"E20.12.1");var subQ56=sQuery(id+"F4.wireOp",EDGE,"E26.13.3");var subQ57=sQuery(id+"F4.wireOp",EDGE,"E26.13.2");var subQ58=sQuery(id+"F3.wireOp",EDGE,"E20.13.3");var subQ59=sQuery(id+"F3.wireOp",EDGE,"E20.13.1");var subQ60=sQuery(id+"F4.wireOp",EDGE,"E26.14.3");var subQ61=sQuery(id+"F4.wireOp",EDGE,"E26.14.2");var subQ62=sQuery(id+"F3.wireOp",EDGE,"E20.14.3");var subQ63=sQuery(id+"F3.wireOp",EDGE,"E20.14.1");var subQ64=sQuery(id+"F4.wireOp",EDGE,"E26.15.3");var subQ65=sQuery(id+"F4.wireOp",EDGE,"E26.15.2");var subQ66=sQuery(id+"F3.wireOp",EDGE,"E20.15.3");var subQ67=sQuery(id+"F3.wireOp",EDGE,"E20.15.1");var subQ68=sQuery(id+"F4.wireOp",EDGE,"E23");var subQ69=sQuery(id+"F4.wireOp",EDGE,"E22");var subQ70=sQuery(id+"F3.wireOp",EDGE,"E18.top");var subQ71=sQuery(id+"F3.wireOp",EDGE,"E18.bottom");var subQ74=makeQuery(id+"F42.boolean.opBoolean","COPY",FACE,{"disambiguationData":[TD([subQ23])],"derivedFrom":subQ6});var subQ75=makeQuery(id+"F17.boolean.opBoolean","INTERSECT",EDGE,{"derivedFrom":[makeQuery(id+"F1.opRevolve","SWEPT_FACE",FACE,{"disambiguationData":[OSD([sQuery(id+"F0.wireOp",EDGE,"E4")])]}),subQ23]});Q50=makeQuery(id+"F48.opFillet","BLEND_EDGE",EDGE,{"blendedFrom":[makeQuery(id+"F47.opFillet","TWEAK_EDGE",EDGE,{"derivedFrom":[makeQuery(id+"F45.opFillet","BLEND_VERTEX",VERTEX,{"blendedFrom":[subQ75,subQ23,subQ74],"blendedInto":[subQ23,subQ74]}),makeQuery(id+"F45.opFillet","BLEND_VERTEX",VERTEX,{"blendedFrom":[subQ75,makeQuery(id+"F42.boolean.opBoolean","MERGE",FACE,{"derivedFrom":[subQ0,subQ8]}),subQ74],"blendedInto":[makeQuery(id+"F42.boolean.opBoolean","MERGE",FACE,{"derivedFrom":[subQ0,subQ8]}),subQ74]})]}),makeQuery(id+"F47.opFillet","BLEND_FACE",FACE,{"disambiguationData":[OSD([subQ5,subQ7]),TDD([makeQuery(id+"F42.boolean.opBoolean","COPY",EDGE,{"disambiguationData":[TD([makeQuery(id+"F5.opLoft","SWEPT_FACE",FACE,{"disambiguationData":[OSD([subQ71,subQ70,sQuery(id+"F3.wireOp",EDGE,"E18.left"),sQuery(id+"F4.wireOp",EDGE,"E21"),subQ69,subQ68])]})])],"derivedFrom":subQ9})])]}),makeQuery(id+"F47.opFillet","BLEND_FACE",FACE,{"disambiguationData":[OSD([subQ5,subQ7]),TDD([makeQuery(id+"F42.boolean.opBoolean","COPY",EDGE,{"disambiguationData":[TD([makeQuery(id+"F6.opLoft","SWEPT_FACE",FACE,{"disambiguationData":[OSD([sQuery(id+"F3.wireOp",EDGE,"E20.15.0"),subQ67,subQ66,sQuery(id+"F4.wireOp",EDGE,"E26.15.0"),subQ65,subQ64])]})])],"derivedFrom":subQ9})])]}),makeQuery(id+"F47.opFillet","BLEND_FACE",FACE,{"disambiguationData":[OSD([subQ5,subQ7]),TDD([makeQuery(id+"F42.boolean.opBoolean","COPY",EDGE,{"disambiguationData":[TD([makeQuery(id+"F7.opLoft","SWEPT_FACE",FACE,{"disambiguationData":[OSD([sQuery(id+"F3.wireOp",EDGE,"E20.14.0"),subQ63,subQ62,sQuery(id+"F4.wireOp",EDGE,"E26.14.0"),subQ61,subQ60])]})])],"derivedFrom":subQ9})])]}),makeQuery(id+"F47.opFillet","BLEND_FACE",FACE,{"disambiguationData":[OSD([subQ5,subQ7]),TDD([makeQuery(id+"F42.boolean.opBoolean","COPY",EDGE,{"disambiguationData":[TD([makeQuery(id+"F8.opLoft","SWEPT_FACE",FACE,{"disambiguationData":[OSD([sQuery(id+"F3.wireOp",EDGE,"E20.13.0"),subQ59,subQ58,sQuery(id+"F4.wireOp",EDGE,"E26.13.0"),subQ57,subQ56])]})])],"derivedFrom":subQ9})])]}),makeQuery(id+"F47.opFillet","BLEND_FACE",FACE,{"disambiguationData":[OSD([subQ5,subQ7]),TDD([makeQuery(id+"F42.boolean.opBoolean","COPY",EDGE,{"disambiguationData":[TD([makeQuery(id+"F9.opLoft","SWEPT_FACE",FACE,{"disambiguationData":[OSD([sQuery(id+"F3.wireOp",EDGE,"E20.12.0"),subQ55,subQ54,sQuery(id+"F4.wireOp",EDGE,"E26.12.0"),subQ53,subQ52])]})])],"derivedFrom":subQ9})])]}),makeQuery(id+"F47.opFillet","BLEND_FACE",FACE,{"disambiguationData":[OSD([subQ5,subQ7]),TDD([makeQuery(id+"F42.boolean.opBoolean","COPY",EDGE,{"disambiguationData":[TD([makeQuery(id+"F10.opLoft","SWEPT_FACE",FACE,{"disambiguationData":[OSD([sQuery(id+"F3.wireOp",EDGE,"E20.11.0"),subQ51,subQ50,sQuery(id+"F4.wireOp",EDGE,"E26.11.0"),subQ49,subQ48])]})])],"derivedFrom":subQ9})])]}),makeQuery(id+"F47.opFillet","BLEND_FACE",FACE,{"disambiguationData":[OSD([subQ5,subQ7]),TDD([makeQuery(id+"F42.boolean.opBoolean","COPY",EDGE,{"disambiguationData":[TD([makeQuery(id+"F11.opLoft","SWEPT_FACE",FACE,{"disambiguationData":[OSD([sQuery(id+"F3.wireOp",EDGE,"E20.10.0"),subQ47,subQ46,sQuery(id+"F4.wireOp",EDGE,"E26.10.0"),subQ45,subQ44])]})])],"derivedFrom":subQ9})])]}),makeQuery(id+"F47.opFillet","BLEND_FACE",FACE,{"disambiguationData":[OSD([subQ5,subQ7]),TDD([makeQuery(id+"F42.boolean.opBoolean","COPY",EDGE,{"disambiguationData":[TD([makeQuery(id+"F12.opLoft","SWEPT_FACE",FACE,{"disambiguationData":[OSD([sQuery(id+"F3.wireOp",EDGE,"E20.9.0"),subQ43,subQ42,sQuery(id+"F4.wireOp",EDGE,"E26.9.0"),subQ41,subQ40])]})])],"derivedFrom":subQ9})])]}),makeQuery(id+"F47.opFillet","BLEND_FACE",FACE,{"disambiguationData":[OSD([subQ5,subQ7]),TDD([makeQuery(id+"F42.boolean.opBoolean","COPY",EDGE,{"disambiguationData":[TD([makeQuery(id+"F13.opLoft","SWEPT_FACE",FACE,{"disambiguationData":[OSD([sQuery(id+"F3.wireOp",EDGE,"E20.8.0"),subQ39,subQ38,sQuery(id+"F4.wireOp",EDGE,"E26.8.0"),subQ37,subQ36])]})])],"derivedFrom":subQ9})])]}),makeQuery(id+"F47.opFillet","BLEND_FACE",FACE,{"disambiguationData":[OSD([subQ5,subQ7]),TDD([makeQuery(id+"F42.boolean.opBoolean","COPY",EDGE,{"disambiguationData":[TD([makeQuery(id+"F14.opLoft","SWEPT_FACE",FACE,{"disambiguationData":[OSD([sQuery(id+"F3.wireOp",EDGE,"E20.7.0"),subQ35,subQ34,sQuery(id+"F4.wireOp",EDGE,"E26.7.0"),subQ33,subQ32])]})])],"derivedFrom":subQ9})])]}),makeQuery(id+"F47.opFillet","BLEND_FACE",FACE,{"disambiguationData":[OSD([subQ5,subQ7]),TDD([makeQuery(id+"F42.boolean.opBoolean","COPY",EDGE,{"disambiguationData":[TD([makeQuery(id+"F15.opLoft","SWEPT_FACE",FACE,{"disambiguationData":[OSD([sQuery(id+"F3.wireOp",EDGE,"E20.6.0"),subQ31,subQ30,sQuery(id+"F4.wireOp",EDGE,"E26.6.0"),subQ29,subQ28])]})])],"derivedFrom":subQ9})])]}),makeQuery(id+"F47.opFillet","BLEND_FACE",FACE,{"disambiguationData":[OSD([subQ5,subQ7]),TDD([makeQuery(id+"F42.boolean.opBoolean","COPY",EDGE,{"disambiguationData":[TD([makeQuery(id+"F16.opLoft","SWEPT_FACE",FACE,{"disambiguationData":[OSD([sQuery(id+"F3.wireOp",EDGE,"E20.5.0"),subQ27,subQ26,sQuery(id+"F4.wireOp",EDGE,"E26.5.0"),subQ25,subQ24])]})])],"derivedFrom":subQ9})])]}),makeQuery(id+"F47.opFillet","BLEND_FACE",FACE,{"disambiguationData":[OSD([subQ5,subQ7]),TDD([makeQuery(id+"F42.boolean.opBoolean","COPY",EDGE,{"disambiguationData":[TD([subQ23])],"derivedFrom":subQ9})])]}),makeQuery(id+"F47.opFillet","BLEND_FACE",FACE,{"disambiguationData":[OSD([subQ5,subQ7]),TDD([makeQuery(id+"F42.boolean.opBoolean","COPY",EDGE,{"disambiguationData":[TD([makeQuery(id+"F18.opLoft","SWEPT_FACE",FACE,{"disambiguationData":[OSD([sQuery(id+"F3.wireOp",EDGE,"E20.3.0"),subQ17,subQ16,sQuery(id+"F4.wireOp",EDGE,"E26.3.0"),subQ15,subQ14])]})])],"derivedFrom":subQ9})])]}),makeQuery(id+"F47.opFillet","BLEND_FACE",FACE,{"disambiguationData":[OSD([subQ5,subQ7]),TDD([makeQuery(id+"F42.boolean.opBoolean","COPY",EDGE,{"disambiguationData":[TD([makeQuery(id+"F19.opLoft","SWEPT_FACE",FACE,{"disambiguationData":[OSD([sQuery(id+"F3.wireOp",EDGE,"E20.2.0"),subQ13,subQ12,sQuery(id+"F4.wireOp",EDGE,"E26.2.0"),subQ11,subQ10])]})])],"derivedFrom":subQ9})])]}),makeQuery(id+"F47.opFillet","BLEND_FACE",FACE,{"disambiguationData":[OSD([subQ5,subQ7]),TDD([makeQuery(id+"F42.boolean.opBoolean","COPY",EDGE,{"disambiguationData":[TD([makeQuery(id+"F20.opLoft","SWEPT_FACE",FACE,{"disambiguationData":[OSD([sQuery(id+"F3.wireOp",EDGE,"E20.1.0"),subQ4,subQ3,sQuery(id+"F4.wireOp",EDGE,"E26.1.0"),subQ2,subQ1])]})])],"derivedFrom":subQ9})])]})],"blendedInto":[makeQuery(id+"F47.opFillet","BLEND_FACE",FACE,{"disambiguationData":[OSD([subQ5,subQ7]),TDD([makeQuery(id+"F42.boolean.opBoolean","COPY",EDGE,{"disambiguationData":[TD([makeQuery(id+"F5.opLoft","SWEPT_FACE",FACE,{"disambiguationData":[OSD([subQ71,subQ70,sQuery(id+"F3.wireOp",EDGE,"E18.left"),sQuery(id+"F4.wireOp",EDGE,"E21"),subQ69,subQ68])]})])],"derivedFrom":subQ9})])]}),makeQuery(id+"F47.opFillet","BLEND_FACE",FACE,{"disambiguationData":[OSD([subQ5,subQ7]),TDD([makeQuery(id+"F42.boolean.opBoolean","COPY",EDGE,{"disambiguationData":[TD([makeQuery(id+"F6.opLoft","SWEPT_FACE",FACE,{"disambiguationData":[OSD([sQuery(id+"F3.wireOp",EDGE,"E20.15.0"),subQ67,subQ66,sQuery(id+"F4.wireOp",EDGE,"E26.15.0"),subQ65,subQ64])]})])],"derivedFrom":subQ9})])]}),makeQuery(id+"F47.opFillet","BLEND_FACE",FACE,{"disambiguationData":[OSD([subQ5,subQ7]),TDD([makeQuery(id+"F42.boolean.opBoolean","COPY",EDGE,{"disambiguationData":[TD([makeQuery(id+"F7.opLoft","SWEPT_FACE",FACE,{"disambiguationData":[OSD([sQuery(id+"F3.wireOp",EDGE,"E20.14.0"),subQ63,subQ62,sQuery(id+"F4.wireOp",EDGE,"E26.14.0"),subQ61,subQ60])]})])],"derivedFrom":subQ9})])]}),makeQuery(id+"F47.opFillet","BLEND_FACE",FACE,{"disambiguationData":[OSD([subQ5,subQ7]),TDD([makeQuery(id+"F42.boolean.opBoolean","COPY",EDGE,{"disambiguationData":[TD([makeQuery(id+"F8.opLoft","SWEPT_FACE",FACE,{"disambiguationData":[OSD([sQuery(id+"F3.wireOp",EDGE,"E20.13.0"),subQ59,subQ58,sQuery(id+"F4.wireOp",EDGE,"E26.13.0"),subQ57,subQ56])]})])],"derivedFrom":subQ9})])]}),makeQuery(id+"F47.opFillet","BLEND_FACE",FACE,{"disambiguationData":[OSD([subQ5,subQ7]),TDD([makeQuery(id+"F42.boolean.opBoolean","COPY",EDGE,{"disambiguationData":[TD([makeQuery(id+"F9.opLoft","SWEPT_FACE",FACE,{"disambiguationData":[OSD([sQuery(id+"F3.wireOp",EDGE,"E20.12.0"),subQ55,subQ54,sQuery(id+"F4.wireOp",EDGE,"E26.12.0"),subQ53,subQ52])]})])],"derivedFrom":subQ9})])]}),makeQuery(id+"F47.opFillet","BLEND_FACE",FACE,{"disambiguationData":[OSD([subQ5,subQ7]),TDD([makeQuery(id+"F42.boolean.opBoolean","COPY",EDGE,{"disambiguationData":[TD([makeQuery(id+"F10.opLoft","SWEPT_FACE",FACE,{"disambiguationData":[OSD([sQuery(id+"F3.wireOp",EDGE,"E20.11.0"),subQ51,subQ50,sQuery(id+"F4.wireOp",EDGE,"E26.11.0"),subQ49,subQ48])]})])],"derivedFrom":subQ9})])]}),makeQuery(id+"F47.opFillet","BLEND_FACE",FACE,{"disambiguationData":[OSD([subQ5,subQ7]),TDD([makeQuery(id+"F42.boolean.opBoolean","COPY",EDGE,{"disambiguationData":[TD([makeQuery(id+"F11.opLoft","SWEPT_FACE",FACE,{"disambiguationData":[OSD([sQuery(id+"F3.wireOp",EDGE,"E20.10.0"),subQ47,subQ46,sQuery(id+"F4.wireOp",EDGE,"E26.10.0"),subQ45,subQ44])]})])],"derivedFrom":subQ9})])]}),makeQuery(id+"F47.opFillet","BLEND_FACE",FACE,{"disambiguationData":[OSD([subQ5,subQ7]),TDD([makeQuery(id+"F42.boolean.opBoolean","COPY",EDGE,{"disambiguationData":[TD([makeQuery(id+"F12.opLoft","SWEPT_FACE",FACE,{"disambiguationData":[OSD([sQuery(id+"F3.wireOp",EDGE,"E20.9.0"),subQ43,subQ42,sQuery(id+"F4.wireOp",EDGE,"E26.9.0"),subQ41,subQ40])]})])],"derivedFrom":subQ9})])]}),makeQuery(id+"F47.opFillet","BLEND_FACE",FACE,{"disambiguationData":[OSD([subQ5,subQ7]),TDD([makeQuery(id+"F42.boolean.opBoolean","COPY",EDGE,{"disambiguationData":[TD([makeQuery(id+"F13.opLoft","SWEPT_FACE",FACE,{"disambiguationData":[OSD([sQuery(id+"F3.wireOp",EDGE,"E20.8.0"),subQ39,subQ38,sQuery(id+"F4.wireOp",EDGE,"E26.8.0"),subQ37,subQ36])]})])],"derivedFrom":subQ9})])]}),makeQuery(id+"F47.opFillet","BLEND_FACE",FACE,{"disambiguationData":[OSD([subQ5,subQ7]),TDD([makeQuery(id+"F42.boolean.opBoolean","COPY",EDGE,{"disambiguationData":[TD([makeQuery(id+"F14.opLoft","SWEPT_FACE",FACE,{"disambiguationData":[OSD([sQuery(id+"F3.wireOp",EDGE,"E20.7.0"),subQ35,subQ34,sQuery(id+"F4.wireOp",EDGE,"E26.7.0"),subQ33,subQ32])]})])],"derivedFrom":subQ9})])]}),makeQuery(id+"F47.opFillet","BLEND_FACE",FACE,{"disambiguationData":[OSD([subQ5,subQ7]),TDD([makeQuery(id+"F42.boolean.opBoolean","COPY",EDGE,{"disambiguationData":[TD([makeQuery(id+"F15.opLoft","SWEPT_FACE",FACE,{"disambiguationData":[OSD([sQuery(id+"F3.wireOp",EDGE,"E20.6.0"),subQ31,subQ30,sQuery(id+"F4.wireOp",EDGE,"E26.6.0"),subQ29,subQ28])]})])],"derivedFrom":subQ9})])]}),makeQuery(id+"F47.opFillet","BLEND_FACE",FACE,{"disambiguationData":[OSD([subQ5,subQ7]),TDD([makeQuery(id+"F42.boolean.opBoolean","COPY",EDGE,{"disambiguationData":[TD([makeQuery(id+"F16.opLoft","SWEPT_FACE",FACE,{"disambiguationData":[OSD([sQuery(id+"F3.wireOp",EDGE,"E20.5.0"),subQ27,subQ26,sQuery(id+"F4.wireOp",EDGE,"E26.5.0"),subQ25,subQ24])]})])],"derivedFrom":subQ9})])]}),makeQuery(id+"F47.opFillet","BLEND_FACE",FACE,{"disambiguationData":[OSD([subQ5,subQ7]),TDD([makeQuery(id+"F42.boolean.opBoolean","COPY",EDGE,{"disambiguationData":[TD([subQ23])],"derivedFrom":subQ9})])]}),makeQuery(id+"F47.opFillet","BLEND_FACE",FACE,{"disambiguationData":[OSD([subQ5,subQ7]),TDD([makeQuery(id+"F42.boolean.opBoolean","COPY",EDGE,{"disambiguationData":[TD([makeQuery(id+"F18.opLoft","SWEPT_FACE",FACE,{"disambiguationData":[OSD([sQuery(id+"F3.wireOp",EDGE,"E20.3.0"),subQ17,subQ16,sQuery(id+"F4.wireOp",EDGE,"E26.3.0"),subQ15,subQ14])]})])],"derivedFrom":subQ9})])]}),makeQuery(id+"F47.opFillet","BLEND_FACE",FACE,{"disambiguationData":[OSD([subQ5,subQ7]),TDD([makeQuery(id+"F42.boolean.opBoolean","COPY",EDGE,{"disambiguationData":[TD([makeQuery(id+"F19.opLoft","SWEPT_FACE",FACE,{"disambiguationData":[OSD([sQuery(id+"F3.wireOp",EDGE,"E20.2.0"),subQ13,subQ12,sQuery(id+"F4.wireOp",EDGE,"E26.2.0"),subQ11,subQ10])]})])],"derivedFrom":subQ9})])]}),makeQuery(id+"F47.opFillet","BLEND_FACE",FACE,{"disambiguationData":[OSD([subQ5,subQ7]),TDD([makeQuery(id+"F42.boolean.opBoolean","COPY",EDGE,{"disambiguationData":[TD([makeQuery(id+"F20.opLoft","SWEPT_FACE",FACE,{"disambiguationData":[OSD([sQuery(id+"F3.wireOp",EDGE,"E20.1.0"),subQ4,subQ3,sQuery(id+"F4.wireOp",EDGE,"E26.1.0"),subQ2,subQ1])]})])],"derivedFrom":subQ9})])]})]});}
            var Q51;
            {var subQ0=makeQuery(id+"F40.opExtrude","CAP_FACE",FACE,{"disambiguationData":[OSD([sQuery(id+"F39.wireOp",EDGE,"E29"),sQuery(id+"F39.wireOp",EDGE,"E30")])],"isStart":false});var subQ1=sQuery(id+"F4.wireOp",EDGE,"E26.1.3");var subQ2=sQuery(id+"F4.wireOp",EDGE,"E26.1.2");var subQ3=sQuery(id+"F3.wireOp",EDGE,"E20.1.3");var subQ4=sQuery(id+"F3.wireOp",EDGE,"E20.1.1");var subQ5=sQuery(id+"F41.wireOp",EDGE,"E35");var subQ6=makeQuery(id+"F42.opRevolve","SWEPT_FACE",FACE,{"disambiguationData":[OSD([subQ5])]});var subQ7=sQuery(id+"F41.wireOp",EDGE,"E36");var subQ8=makeQuery(id+"F42.opRevolve","SWEPT_FACE",FACE,{"disambiguationData":[OSD([subQ7])]});var subQ9=makeQuery(id+"F42.opRevolve","SWEPT_EDGE",EDGE,{"disambiguationData":[OSD([subQ5,subQ7])]});var subQ10=sQuery(id+"F4.wireOp",EDGE,"E26.2.3");var subQ11=sQuery(id+"F4.wireOp",EDGE,"E26.2.2");var subQ12=sQuery(id+"F3.wireOp",EDGE,"E20.2.3");var subQ13=sQuery(id+"F3.wireOp",EDGE,"E20.2.1");var subQ14=sQuery(id+"F4.wireOp",EDGE,"E26.3.3");var subQ15=sQuery(id+"F4.wireOp",EDGE,"E26.3.2");var subQ16=sQuery(id+"F3.wireOp",EDGE,"E20.3.3");var subQ17=sQuery(id+"F3.wireOp",EDGE,"E20.3.1");var subQ18=makeQuery(id+"F18.opLoft","SWEPT_FACE",FACE,{"disambiguationData":[OSD([sQuery(id+"F3.wireOp",EDGE,"E20.3.0"),subQ17,subQ16,sQuery(id+"F4.wireOp",EDGE,"E26.3.0"),subQ15,subQ14])]});var subQ20=sQuery(id+"F4.wireOp",EDGE,"E26.4.3");var subQ21=sQuery(id+"F4.wireOp",EDGE,"E26.4.2");var subQ22=sQuery(id+"F3.wireOp",EDGE,"E20.4.3");var subQ23=sQuery(id+"F3.wireOp",EDGE,"E20.4.1");var subQ24=sQuery(id+"F4.wireOp",EDGE,"E26.5.3");var subQ25=sQuery(id+"F4.wireOp",EDGE,"E26.5.2");var subQ26=sQuery(id+"F3.wireOp",EDGE,"E20.5.3");var subQ27=sQuery(id+"F3.wireOp",EDGE,"E20.5.1");var subQ28=sQuery(id+"F4.wireOp",EDGE,"E26.6.3");var subQ29=sQuery(id+"F4.wireOp",EDGE,"E26.6.2");var subQ30=sQuery(id+"F3.wireOp",EDGE,"E20.6.3");var subQ31=sQuery(id+"F3.wireOp",EDGE,"E20.6.1");var subQ32=sQuery(id+"F4.wireOp",EDGE,"E26.7.3");var subQ33=sQuery(id+"F4.wireOp",EDGE,"E26.7.2");var subQ34=sQuery(id+"F3.wireOp",EDGE,"E20.7.3");var subQ35=sQuery(id+"F3.wireOp",EDGE,"E20.7.1");var subQ36=sQuery(id+"F4.wireOp",EDGE,"E26.8.3");var subQ37=sQuery(id+"F4.wireOp",EDGE,"E26.8.2");var subQ38=sQuery(id+"F3.wireOp",EDGE,"E20.8.3");var subQ39=sQuery(id+"F3.wireOp",EDGE,"E20.8.1");var subQ40=sQuery(id+"F4.wireOp",EDGE,"E26.9.3");var subQ41=sQuery(id+"F4.wireOp",EDGE,"E26.9.2");var subQ42=sQuery(id+"F3.wireOp",EDGE,"E20.9.3");var subQ43=sQuery(id+"F3.wireOp",EDGE,"E20.9.1");var subQ44=sQuery(id+"F4.wireOp",EDGE,"E26.10.3");var subQ45=sQuery(id+"F4.wireOp",EDGE,"E26.10.2");var subQ46=sQuery(id+"F3.wireOp",EDGE,"E20.10.3");var subQ47=sQuery(id+"F3.wireOp",EDGE,"E20.10.1");var subQ48=sQuery(id+"F4.wireOp",EDGE,"E26.11.3");var subQ49=sQuery(id+"F4.wireOp",EDGE,"E26.11.2");var subQ50=sQuery(id+"F3.wireOp",EDGE,"E20.11.3");var subQ51=sQuery(id+"F3.wireOp",EDGE,"E20.11.1");var subQ52=sQuery(id+"F4.wireOp",EDGE,"E26.12.3");var subQ53=sQuery(id+"F4.wireOp",EDGE,"E26.12.2");var subQ54=sQuery(id+"F3.wireOp",EDGE,"E20.12.3");var subQ55=sQuery(id+"F3.wireOp",EDGE,"E20.12.1");var subQ56=sQuery(id+"F4.wireOp",EDGE,"E26.13.3");var subQ57=sQuery(id+"F4.wireOp",EDGE,"E26.13.2");var subQ58=sQuery(id+"F3.wireOp",EDGE,"E20.13.3");var subQ59=sQuery(id+"F3.wireOp",EDGE,"E20.13.1");var subQ60=sQuery(id+"F4.wireOp",EDGE,"E26.14.3");var subQ61=sQuery(id+"F4.wireOp",EDGE,"E26.14.2");var subQ62=sQuery(id+"F3.wireOp",EDGE,"E20.14.3");var subQ63=sQuery(id+"F3.wireOp",EDGE,"E20.14.1");var subQ64=sQuery(id+"F4.wireOp",EDGE,"E26.15.3");var subQ65=sQuery(id+"F4.wireOp",EDGE,"E26.15.2");var subQ66=sQuery(id+"F3.wireOp",EDGE,"E20.15.3");var subQ67=sQuery(id+"F3.wireOp",EDGE,"E20.15.1");var subQ68=sQuery(id+"F4.wireOp",EDGE,"E23");var subQ69=sQuery(id+"F4.wireOp",EDGE,"E22");var subQ70=sQuery(id+"F3.wireOp",EDGE,"E18.top");var subQ71=sQuery(id+"F3.wireOp",EDGE,"E18.bottom");var subQ74=makeQuery(id+"F42.boolean.opBoolean","COPY",FACE,{"disambiguationData":[TD([subQ18])],"derivedFrom":subQ6});var subQ75=makeQuery(id+"F18.boolean.opBoolean","INTERSECT",EDGE,{"derivedFrom":[makeQuery(id+"F1.opRevolve","SWEPT_FACE",FACE,{"disambiguationData":[OSD([sQuery(id+"F0.wireOp",EDGE,"E4")])]}),subQ18]});Q51=makeQuery(id+"F48.opFillet","BLEND_EDGE",EDGE,{"blendedFrom":[makeQuery(id+"F47.opFillet","TWEAK_EDGE",EDGE,{"derivedFrom":[makeQuery(id+"F45.opFillet","BLEND_VERTEX",VERTEX,{"blendedFrom":[subQ75,subQ18,subQ74],"blendedInto":[subQ18,subQ74]}),makeQuery(id+"F45.opFillet","BLEND_VERTEX",VERTEX,{"blendedFrom":[subQ75,makeQuery(id+"F42.boolean.opBoolean","MERGE",FACE,{"derivedFrom":[subQ0,subQ8]}),subQ74],"blendedInto":[makeQuery(id+"F42.boolean.opBoolean","MERGE",FACE,{"derivedFrom":[subQ0,subQ8]}),subQ74]})]}),makeQuery(id+"F47.opFillet","BLEND_FACE",FACE,{"disambiguationData":[OSD([subQ5,subQ7]),TDD([makeQuery(id+"F42.boolean.opBoolean","COPY",EDGE,{"disambiguationData":[TD([makeQuery(id+"F5.opLoft","SWEPT_FACE",FACE,{"disambiguationData":[OSD([subQ71,subQ70,sQuery(id+"F3.wireOp",EDGE,"E18.left"),sQuery(id+"F4.wireOp",EDGE,"E21"),subQ69,subQ68])]})])],"derivedFrom":subQ9})])]}),makeQuery(id+"F47.opFillet","BLEND_FACE",FACE,{"disambiguationData":[OSD([subQ5,subQ7]),TDD([makeQuery(id+"F42.boolean.opBoolean","COPY",EDGE,{"disambiguationData":[TD([makeQuery(id+"F6.opLoft","SWEPT_FACE",FACE,{"disambiguationData":[OSD([sQuery(id+"F3.wireOp",EDGE,"E20.15.0"),subQ67,subQ66,sQuery(id+"F4.wireOp",EDGE,"E26.15.0"),subQ65,subQ64])]})])],"derivedFrom":subQ9})])]}),makeQuery(id+"F47.opFillet","BLEND_FACE",FACE,{"disambiguationData":[OSD([subQ5,subQ7]),TDD([makeQuery(id+"F42.boolean.opBoolean","COPY",EDGE,{"disambiguationData":[TD([makeQuery(id+"F7.opLoft","SWEPT_FACE",FACE,{"disambiguationData":[OSD([sQuery(id+"F3.wireOp",EDGE,"E20.14.0"),subQ63,subQ62,sQuery(id+"F4.wireOp",EDGE,"E26.14.0"),subQ61,subQ60])]})])],"derivedFrom":subQ9})])]}),makeQuery(id+"F47.opFillet","BLEND_FACE",FACE,{"disambiguationData":[OSD([subQ5,subQ7]),TDD([makeQuery(id+"F42.boolean.opBoolean","COPY",EDGE,{"disambiguationData":[TD([makeQuery(id+"F8.opLoft","SWEPT_FACE",FACE,{"disambiguationData":[OSD([sQuery(id+"F3.wireOp",EDGE,"E20.13.0"),subQ59,subQ58,sQuery(id+"F4.wireOp",EDGE,"E26.13.0"),subQ57,subQ56])]})])],"derivedFrom":subQ9})])]}),makeQuery(id+"F47.opFillet","BLEND_FACE",FACE,{"disambiguationData":[OSD([subQ5,subQ7]),TDD([makeQuery(id+"F42.boolean.opBoolean","COPY",EDGE,{"disambiguationData":[TD([makeQuery(id+"F9.opLoft","SWEPT_FACE",FACE,{"disambiguationData":[OSD([sQuery(id+"F3.wireOp",EDGE,"E20.12.0"),subQ55,subQ54,sQuery(id+"F4.wireOp",EDGE,"E26.12.0"),subQ53,subQ52])]})])],"derivedFrom":subQ9})])]}),makeQuery(id+"F47.opFillet","BLEND_FACE",FACE,{"disambiguationData":[OSD([subQ5,subQ7]),TDD([makeQuery(id+"F42.boolean.opBoolean","COPY",EDGE,{"disambiguationData":[TD([makeQuery(id+"F10.opLoft","SWEPT_FACE",FACE,{"disambiguationData":[OSD([sQuery(id+"F3.wireOp",EDGE,"E20.11.0"),subQ51,subQ50,sQuery(id+"F4.wireOp",EDGE,"E26.11.0"),subQ49,subQ48])]})])],"derivedFrom":subQ9})])]}),makeQuery(id+"F47.opFillet","BLEND_FACE",FACE,{"disambiguationData":[OSD([subQ5,subQ7]),TDD([makeQuery(id+"F42.boolean.opBoolean","COPY",EDGE,{"disambiguationData":[TD([makeQuery(id+"F11.opLoft","SWEPT_FACE",FACE,{"disambiguationData":[OSD([sQuery(id+"F3.wireOp",EDGE,"E20.10.0"),subQ47,subQ46,sQuery(id+"F4.wireOp",EDGE,"E26.10.0"),subQ45,subQ44])]})])],"derivedFrom":subQ9})])]}),makeQuery(id+"F47.opFillet","BLEND_FACE",FACE,{"disambiguationData":[OSD([subQ5,subQ7]),TDD([makeQuery(id+"F42.boolean.opBoolean","COPY",EDGE,{"disambiguationData":[TD([makeQuery(id+"F12.opLoft","SWEPT_FACE",FACE,{"disambiguationData":[OSD([sQuery(id+"F3.wireOp",EDGE,"E20.9.0"),subQ43,subQ42,sQuery(id+"F4.wireOp",EDGE,"E26.9.0"),subQ41,subQ40])]})])],"derivedFrom":subQ9})])]}),makeQuery(id+"F47.opFillet","BLEND_FACE",FACE,{"disambiguationData":[OSD([subQ5,subQ7]),TDD([makeQuery(id+"F42.boolean.opBoolean","COPY",EDGE,{"disambiguationData":[TD([makeQuery(id+"F13.opLoft","SWEPT_FACE",FACE,{"disambiguationData":[OSD([sQuery(id+"F3.wireOp",EDGE,"E20.8.0"),subQ39,subQ38,sQuery(id+"F4.wireOp",EDGE,"E26.8.0"),subQ37,subQ36])]})])],"derivedFrom":subQ9})])]}),makeQuery(id+"F47.opFillet","BLEND_FACE",FACE,{"disambiguationData":[OSD([subQ5,subQ7]),TDD([makeQuery(id+"F42.boolean.opBoolean","COPY",EDGE,{"disambiguationData":[TD([makeQuery(id+"F14.opLoft","SWEPT_FACE",FACE,{"disambiguationData":[OSD([sQuery(id+"F3.wireOp",EDGE,"E20.7.0"),subQ35,subQ34,sQuery(id+"F4.wireOp",EDGE,"E26.7.0"),subQ33,subQ32])]})])],"derivedFrom":subQ9})])]}),makeQuery(id+"F47.opFillet","BLEND_FACE",FACE,{"disambiguationData":[OSD([subQ5,subQ7]),TDD([makeQuery(id+"F42.boolean.opBoolean","COPY",EDGE,{"disambiguationData":[TD([makeQuery(id+"F15.opLoft","SWEPT_FACE",FACE,{"disambiguationData":[OSD([sQuery(id+"F3.wireOp",EDGE,"E20.6.0"),subQ31,subQ30,sQuery(id+"F4.wireOp",EDGE,"E26.6.0"),subQ29,subQ28])]})])],"derivedFrom":subQ9})])]}),makeQuery(id+"F47.opFillet","BLEND_FACE",FACE,{"disambiguationData":[OSD([subQ5,subQ7]),TDD([makeQuery(id+"F42.boolean.opBoolean","COPY",EDGE,{"disambiguationData":[TD([makeQuery(id+"F16.opLoft","SWEPT_FACE",FACE,{"disambiguationData":[OSD([sQuery(id+"F3.wireOp",EDGE,"E20.5.0"),subQ27,subQ26,sQuery(id+"F4.wireOp",EDGE,"E26.5.0"),subQ25,subQ24])]})])],"derivedFrom":subQ9})])]}),makeQuery(id+"F47.opFillet","BLEND_FACE",FACE,{"disambiguationData":[OSD([subQ5,subQ7]),TDD([makeQuery(id+"F42.boolean.opBoolean","COPY",EDGE,{"disambiguationData":[TD([makeQuery(id+"F17.opLoft","SWEPT_FACE",FACE,{"disambiguationData":[OSD([sQuery(id+"F3.wireOp",EDGE,"E20.4.0"),subQ23,subQ22,sQuery(id+"F4.wireOp",EDGE,"E26.4.0"),subQ21,subQ20])]})])],"derivedFrom":subQ9})])]}),makeQuery(id+"F47.opFillet","BLEND_FACE",FACE,{"disambiguationData":[OSD([subQ5,subQ7]),TDD([makeQuery(id+"F42.boolean.opBoolean","COPY",EDGE,{"disambiguationData":[TD([subQ18])],"derivedFrom":subQ9})])]}),makeQuery(id+"F47.opFillet","BLEND_FACE",FACE,{"disambiguationData":[OSD([subQ5,subQ7]),TDD([makeQuery(id+"F42.boolean.opBoolean","COPY",EDGE,{"disambiguationData":[TD([makeQuery(id+"F19.opLoft","SWEPT_FACE",FACE,{"disambiguationData":[OSD([sQuery(id+"F3.wireOp",EDGE,"E20.2.0"),subQ13,subQ12,sQuery(id+"F4.wireOp",EDGE,"E26.2.0"),subQ11,subQ10])]})])],"derivedFrom":subQ9})])]}),makeQuery(id+"F47.opFillet","BLEND_FACE",FACE,{"disambiguationData":[OSD([subQ5,subQ7]),TDD([makeQuery(id+"F42.boolean.opBoolean","COPY",EDGE,{"disambiguationData":[TD([makeQuery(id+"F20.opLoft","SWEPT_FACE",FACE,{"disambiguationData":[OSD([sQuery(id+"F3.wireOp",EDGE,"E20.1.0"),subQ4,subQ3,sQuery(id+"F4.wireOp",EDGE,"E26.1.0"),subQ2,subQ1])]})])],"derivedFrom":subQ9})])]})],"blendedInto":[makeQuery(id+"F47.opFillet","BLEND_FACE",FACE,{"disambiguationData":[OSD([subQ5,subQ7]),TDD([makeQuery(id+"F42.boolean.opBoolean","COPY",EDGE,{"disambiguationData":[TD([makeQuery(id+"F5.opLoft","SWEPT_FACE",FACE,{"disambiguationData":[OSD([subQ71,subQ70,sQuery(id+"F3.wireOp",EDGE,"E18.left"),sQuery(id+"F4.wireOp",EDGE,"E21"),subQ69,subQ68])]})])],"derivedFrom":subQ9})])]}),makeQuery(id+"F47.opFillet","BLEND_FACE",FACE,{"disambiguationData":[OSD([subQ5,subQ7]),TDD([makeQuery(id+"F42.boolean.opBoolean","COPY",EDGE,{"disambiguationData":[TD([makeQuery(id+"F6.opLoft","SWEPT_FACE",FACE,{"disambiguationData":[OSD([sQuery(id+"F3.wireOp",EDGE,"E20.15.0"),subQ67,subQ66,sQuery(id+"F4.wireOp",EDGE,"E26.15.0"),subQ65,subQ64])]})])],"derivedFrom":subQ9})])]}),makeQuery(id+"F47.opFillet","BLEND_FACE",FACE,{"disambiguationData":[OSD([subQ5,subQ7]),TDD([makeQuery(id+"F42.boolean.opBoolean","COPY",EDGE,{"disambiguationData":[TD([makeQuery(id+"F7.opLoft","SWEPT_FACE",FACE,{"disambiguationData":[OSD([sQuery(id+"F3.wireOp",EDGE,"E20.14.0"),subQ63,subQ62,sQuery(id+"F4.wireOp",EDGE,"E26.14.0"),subQ61,subQ60])]})])],"derivedFrom":subQ9})])]}),makeQuery(id+"F47.opFillet","BLEND_FACE",FACE,{"disambiguationData":[OSD([subQ5,subQ7]),TDD([makeQuery(id+"F42.boolean.opBoolean","COPY",EDGE,{"disambiguationData":[TD([makeQuery(id+"F8.opLoft","SWEPT_FACE",FACE,{"disambiguationData":[OSD([sQuery(id+"F3.wireOp",EDGE,"E20.13.0"),subQ59,subQ58,sQuery(id+"F4.wireOp",EDGE,"E26.13.0"),subQ57,subQ56])]})])],"derivedFrom":subQ9})])]}),makeQuery(id+"F47.opFillet","BLEND_FACE",FACE,{"disambiguationData":[OSD([subQ5,subQ7]),TDD([makeQuery(id+"F42.boolean.opBoolean","COPY",EDGE,{"disambiguationData":[TD([makeQuery(id+"F9.opLoft","SWEPT_FACE",FACE,{"disambiguationData":[OSD([sQuery(id+"F3.wireOp",EDGE,"E20.12.0"),subQ55,subQ54,sQuery(id+"F4.wireOp",EDGE,"E26.12.0"),subQ53,subQ52])]})])],"derivedFrom":subQ9})])]}),makeQuery(id+"F47.opFillet","BLEND_FACE",FACE,{"disambiguationData":[OSD([subQ5,subQ7]),TDD([makeQuery(id+"F42.boolean.opBoolean","COPY",EDGE,{"disambiguationData":[TD([makeQuery(id+"F10.opLoft","SWEPT_FACE",FACE,{"disambiguationData":[OSD([sQuery(id+"F3.wireOp",EDGE,"E20.11.0"),subQ51,subQ50,sQuery(id+"F4.wireOp",EDGE,"E26.11.0"),subQ49,subQ48])]})])],"derivedFrom":subQ9})])]}),makeQuery(id+"F47.opFillet","BLEND_FACE",FACE,{"disambiguationData":[OSD([subQ5,subQ7]),TDD([makeQuery(id+"F42.boolean.opBoolean","COPY",EDGE,{"disambiguationData":[TD([makeQuery(id+"F11.opLoft","SWEPT_FACE",FACE,{"disambiguationData":[OSD([sQuery(id+"F3.wireOp",EDGE,"E20.10.0"),subQ47,subQ46,sQuery(id+"F4.wireOp",EDGE,"E26.10.0"),subQ45,subQ44])]})])],"derivedFrom":subQ9})])]}),makeQuery(id+"F47.opFillet","BLEND_FACE",FACE,{"disambiguationData":[OSD([subQ5,subQ7]),TDD([makeQuery(id+"F42.boolean.opBoolean","COPY",EDGE,{"disambiguationData":[TD([makeQuery(id+"F12.opLoft","SWEPT_FACE",FACE,{"disambiguationData":[OSD([sQuery(id+"F3.wireOp",EDGE,"E20.9.0"),subQ43,subQ42,sQuery(id+"F4.wireOp",EDGE,"E26.9.0"),subQ41,subQ40])]})])],"derivedFrom":subQ9})])]}),makeQuery(id+"F47.opFillet","BLEND_FACE",FACE,{"disambiguationData":[OSD([subQ5,subQ7]),TDD([makeQuery(id+"F42.boolean.opBoolean","COPY",EDGE,{"disambiguationData":[TD([makeQuery(id+"F13.opLoft","SWEPT_FACE",FACE,{"disambiguationData":[OSD([sQuery(id+"F3.wireOp",EDGE,"E20.8.0"),subQ39,subQ38,sQuery(id+"F4.wireOp",EDGE,"E26.8.0"),subQ37,subQ36])]})])],"derivedFrom":subQ9})])]}),makeQuery(id+"F47.opFillet","BLEND_FACE",FACE,{"disambiguationData":[OSD([subQ5,subQ7]),TDD([makeQuery(id+"F42.boolean.opBoolean","COPY",EDGE,{"disambiguationData":[TD([makeQuery(id+"F14.opLoft","SWEPT_FACE",FACE,{"disambiguationData":[OSD([sQuery(id+"F3.wireOp",EDGE,"E20.7.0"),subQ35,subQ34,sQuery(id+"F4.wireOp",EDGE,"E26.7.0"),subQ33,subQ32])]})])],"derivedFrom":subQ9})])]}),makeQuery(id+"F47.opFillet","BLEND_FACE",FACE,{"disambiguationData":[OSD([subQ5,subQ7]),TDD([makeQuery(id+"F42.boolean.opBoolean","COPY",EDGE,{"disambiguationData":[TD([makeQuery(id+"F15.opLoft","SWEPT_FACE",FACE,{"disambiguationData":[OSD([sQuery(id+"F3.wireOp",EDGE,"E20.6.0"),subQ31,subQ30,sQuery(id+"F4.wireOp",EDGE,"E26.6.0"),subQ29,subQ28])]})])],"derivedFrom":subQ9})])]}),makeQuery(id+"F47.opFillet","BLEND_FACE",FACE,{"disambiguationData":[OSD([subQ5,subQ7]),TDD([makeQuery(id+"F42.boolean.opBoolean","COPY",EDGE,{"disambiguationData":[TD([makeQuery(id+"F16.opLoft","SWEPT_FACE",FACE,{"disambiguationData":[OSD([sQuery(id+"F3.wireOp",EDGE,"E20.5.0"),subQ27,subQ26,sQuery(id+"F4.wireOp",EDGE,"E26.5.0"),subQ25,subQ24])]})])],"derivedFrom":subQ9})])]}),makeQuery(id+"F47.opFillet","BLEND_FACE",FACE,{"disambiguationData":[OSD([subQ5,subQ7]),TDD([makeQuery(id+"F42.boolean.opBoolean","COPY",EDGE,{"disambiguationData":[TD([makeQuery(id+"F17.opLoft","SWEPT_FACE",FACE,{"disambiguationData":[OSD([sQuery(id+"F3.wireOp",EDGE,"E20.4.0"),subQ23,subQ22,sQuery(id+"F4.wireOp",EDGE,"E26.4.0"),subQ21,subQ20])]})])],"derivedFrom":subQ9})])]}),makeQuery(id+"F47.opFillet","BLEND_FACE",FACE,{"disambiguationData":[OSD([subQ5,subQ7]),TDD([makeQuery(id+"F42.boolean.opBoolean","COPY",EDGE,{"disambiguationData":[TD([subQ18])],"derivedFrom":subQ9})])]}),makeQuery(id+"F47.opFillet","BLEND_FACE",FACE,{"disambiguationData":[OSD([subQ5,subQ7]),TDD([makeQuery(id+"F42.boolean.opBoolean","COPY",EDGE,{"disambiguationData":[TD([makeQuery(id+"F19.opLoft","SWEPT_FACE",FACE,{"disambiguationData":[OSD([sQuery(id+"F3.wireOp",EDGE,"E20.2.0"),subQ13,subQ12,sQuery(id+"F4.wireOp",EDGE,"E26.2.0"),subQ11,subQ10])]})])],"derivedFrom":subQ9})])]}),makeQuery(id+"F47.opFillet","BLEND_FACE",FACE,{"disambiguationData":[OSD([subQ5,subQ7]),TDD([makeQuery(id+"F42.boolean.opBoolean","COPY",EDGE,{"disambiguationData":[TD([makeQuery(id+"F20.opLoft","SWEPT_FACE",FACE,{"disambiguationData":[OSD([sQuery(id+"F3.wireOp",EDGE,"E20.1.0"),subQ4,subQ3,sQuery(id+"F4.wireOp",EDGE,"E26.1.0"),subQ2,subQ1])]})])],"derivedFrom":subQ9})])]})]});}
            var Q52;
            {var subQ0=makeQuery(id+"F40.opExtrude","CAP_FACE",FACE,{"disambiguationData":[OSD([sQuery(id+"F39.wireOp",EDGE,"E29"),sQuery(id+"F39.wireOp",EDGE,"E30")])],"isStart":false});var subQ1=sQuery(id+"F4.wireOp",EDGE,"E26.1.3");var subQ2=sQuery(id+"F4.wireOp",EDGE,"E26.1.2");var subQ3=sQuery(id+"F3.wireOp",EDGE,"E20.1.3");var subQ4=sQuery(id+"F3.wireOp",EDGE,"E20.1.1");var subQ5=sQuery(id+"F41.wireOp",EDGE,"E35");var subQ6=makeQuery(id+"F42.opRevolve","SWEPT_FACE",FACE,{"disambiguationData":[OSD([subQ5])]});var subQ7=sQuery(id+"F41.wireOp",EDGE,"E36");var subQ8=makeQuery(id+"F42.opRevolve","SWEPT_FACE",FACE,{"disambiguationData":[OSD([subQ7])]});var subQ9=makeQuery(id+"F42.opRevolve","SWEPT_EDGE",EDGE,{"disambiguationData":[OSD([subQ5,subQ7])]});var subQ10=sQuery(id+"F4.wireOp",EDGE,"E26.2.3");var subQ11=sQuery(id+"F4.wireOp",EDGE,"E26.2.2");var subQ12=sQuery(id+"F3.wireOp",EDGE,"E20.2.3");var subQ13=sQuery(id+"F3.wireOp",EDGE,"E20.2.1");var subQ15=makeQuery(id+"F19.opLoft","SWEPT_FACE",FACE,{"disambiguationData":[OSD([sQuery(id+"F3.wireOp",EDGE,"E20.2.0"),subQ13,subQ12,sQuery(id+"F4.wireOp",EDGE,"E26.2.0"),subQ11,subQ10])]});var subQ16=sQuery(id+"F4.wireOp",EDGE,"E26.3.3");var subQ17=sQuery(id+"F4.wireOp",EDGE,"E26.3.2");var subQ18=sQuery(id+"F3.wireOp",EDGE,"E20.3.3");var subQ19=sQuery(id+"F3.wireOp",EDGE,"E20.3.1");var subQ20=sQuery(id+"F4.wireOp",EDGE,"E26.4.3");var subQ21=sQuery(id+"F4.wireOp",EDGE,"E26.4.2");var subQ22=sQuery(id+"F3.wireOp",EDGE,"E20.4.3");var subQ23=sQuery(id+"F3.wireOp",EDGE,"E20.4.1");var subQ24=sQuery(id+"F4.wireOp",EDGE,"E26.5.3");var subQ25=sQuery(id+"F4.wireOp",EDGE,"E26.5.2");var subQ26=sQuery(id+"F3.wireOp",EDGE,"E20.5.3");var subQ27=sQuery(id+"F3.wireOp",EDGE,"E20.5.1");var subQ28=sQuery(id+"F4.wireOp",EDGE,"E26.6.3");var subQ29=sQuery(id+"F4.wireOp",EDGE,"E26.6.2");var subQ30=sQuery(id+"F3.wireOp",EDGE,"E20.6.3");var subQ31=sQuery(id+"F3.wireOp",EDGE,"E20.6.1");var subQ32=sQuery(id+"F4.wireOp",EDGE,"E26.7.3");var subQ33=sQuery(id+"F4.wireOp",EDGE,"E26.7.2");var subQ34=sQuery(id+"F3.wireOp",EDGE,"E20.7.3");var subQ35=sQuery(id+"F3.wireOp",EDGE,"E20.7.1");var subQ36=sQuery(id+"F4.wireOp",EDGE,"E26.8.3");var subQ37=sQuery(id+"F4.wireOp",EDGE,"E26.8.2");var subQ38=sQuery(id+"F3.wireOp",EDGE,"E20.8.3");var subQ39=sQuery(id+"F3.wireOp",EDGE,"E20.8.1");var subQ40=sQuery(id+"F4.wireOp",EDGE,"E26.9.3");var subQ41=sQuery(id+"F4.wireOp",EDGE,"E26.9.2");var subQ42=sQuery(id+"F3.wireOp",EDGE,"E20.9.3");var subQ43=sQuery(id+"F3.wireOp",EDGE,"E20.9.1");var subQ44=sQuery(id+"F4.wireOp",EDGE,"E26.10.3");var subQ45=sQuery(id+"F4.wireOp",EDGE,"E26.10.2");var subQ46=sQuery(id+"F3.wireOp",EDGE,"E20.10.3");var subQ47=sQuery(id+"F3.wireOp",EDGE,"E20.10.1");var subQ48=sQuery(id+"F4.wireOp",EDGE,"E26.11.3");var subQ49=sQuery(id+"F4.wireOp",EDGE,"E26.11.2");var subQ50=sQuery(id+"F3.wireOp",EDGE,"E20.11.3");var subQ51=sQuery(id+"F3.wireOp",EDGE,"E20.11.1");var subQ52=sQuery(id+"F4.wireOp",EDGE,"E26.12.3");var subQ53=sQuery(id+"F4.wireOp",EDGE,"E26.12.2");var subQ54=sQuery(id+"F3.wireOp",EDGE,"E20.12.3");var subQ55=sQuery(id+"F3.wireOp",EDGE,"E20.12.1");var subQ56=sQuery(id+"F4.wireOp",EDGE,"E26.13.3");var subQ57=sQuery(id+"F4.wireOp",EDGE,"E26.13.2");var subQ58=sQuery(id+"F3.wireOp",EDGE,"E20.13.3");var subQ59=sQuery(id+"F3.wireOp",EDGE,"E20.13.1");var subQ60=sQuery(id+"F4.wireOp",EDGE,"E26.14.3");var subQ61=sQuery(id+"F4.wireOp",EDGE,"E26.14.2");var subQ62=sQuery(id+"F3.wireOp",EDGE,"E20.14.3");var subQ63=sQuery(id+"F3.wireOp",EDGE,"E20.14.1");var subQ64=sQuery(id+"F4.wireOp",EDGE,"E26.15.3");var subQ65=sQuery(id+"F4.wireOp",EDGE,"E26.15.2");var subQ66=sQuery(id+"F3.wireOp",EDGE,"E20.15.3");var subQ67=sQuery(id+"F3.wireOp",EDGE,"E20.15.1");var subQ68=sQuery(id+"F4.wireOp",EDGE,"E23");var subQ69=sQuery(id+"F4.wireOp",EDGE,"E22");var subQ70=sQuery(id+"F3.wireOp",EDGE,"E18.top");var subQ71=sQuery(id+"F3.wireOp",EDGE,"E18.bottom");var subQ74=makeQuery(id+"F42.boolean.opBoolean","COPY",FACE,{"disambiguationData":[TD([subQ15])],"derivedFrom":subQ6});var subQ75=makeQuery(id+"F19.boolean.opBoolean","INTERSECT",EDGE,{"derivedFrom":[makeQuery(id+"F1.opRevolve","SWEPT_FACE",FACE,{"disambiguationData":[OSD([sQuery(id+"F0.wireOp",EDGE,"E4")])]}),subQ15]});Q52=makeQuery(id+"F48.opFillet","BLEND_EDGE",EDGE,{"blendedFrom":[makeQuery(id+"F47.opFillet","TWEAK_EDGE",EDGE,{"derivedFrom":[makeQuery(id+"F45.opFillet","BLEND_VERTEX",VERTEX,{"blendedFrom":[subQ75,subQ15,subQ74],"blendedInto":[subQ15,subQ74]}),makeQuery(id+"F45.opFillet","BLEND_VERTEX",VERTEX,{"blendedFrom":[subQ75,makeQuery(id+"F42.boolean.opBoolean","MERGE",FACE,{"derivedFrom":[subQ0,subQ8]}),subQ74],"blendedInto":[makeQuery(id+"F42.boolean.opBoolean","MERGE",FACE,{"derivedFrom":[subQ0,subQ8]}),subQ74]})]}),makeQuery(id+"F47.opFillet","BLEND_FACE",FACE,{"disambiguationData":[OSD([subQ5,subQ7]),TDD([makeQuery(id+"F42.boolean.opBoolean","COPY",EDGE,{"disambiguationData":[TD([makeQuery(id+"F5.opLoft","SWEPT_FACE",FACE,{"disambiguationData":[OSD([subQ71,subQ70,sQuery(id+"F3.wireOp",EDGE,"E18.left"),sQuery(id+"F4.wireOp",EDGE,"E21"),subQ69,subQ68])]})])],"derivedFrom":subQ9})])]}),makeQuery(id+"F47.opFillet","BLEND_FACE",FACE,{"disambiguationData":[OSD([subQ5,subQ7]),TDD([makeQuery(id+"F42.boolean.opBoolean","COPY",EDGE,{"disambiguationData":[TD([makeQuery(id+"F6.opLoft","SWEPT_FACE",FACE,{"disambiguationData":[OSD([sQuery(id+"F3.wireOp",EDGE,"E20.15.0"),subQ67,subQ66,sQuery(id+"F4.wireOp",EDGE,"E26.15.0"),subQ65,subQ64])]})])],"derivedFrom":subQ9})])]}),makeQuery(id+"F47.opFillet","BLEND_FACE",FACE,{"disambiguationData":[OSD([subQ5,subQ7]),TDD([makeQuery(id+"F42.boolean.opBoolean","COPY",EDGE,{"disambiguationData":[TD([makeQuery(id+"F7.opLoft","SWEPT_FACE",FACE,{"disambiguationData":[OSD([sQuery(id+"F3.wireOp",EDGE,"E20.14.0"),subQ63,subQ62,sQuery(id+"F4.wireOp",EDGE,"E26.14.0"),subQ61,subQ60])]})])],"derivedFrom":subQ9})])]}),makeQuery(id+"F47.opFillet","BLEND_FACE",FACE,{"disambiguationData":[OSD([subQ5,subQ7]),TDD([makeQuery(id+"F42.boolean.opBoolean","COPY",EDGE,{"disambiguationData":[TD([makeQuery(id+"F8.opLoft","SWEPT_FACE",FACE,{"disambiguationData":[OSD([sQuery(id+"F3.wireOp",EDGE,"E20.13.0"),subQ59,subQ58,sQuery(id+"F4.wireOp",EDGE,"E26.13.0"),subQ57,subQ56])]})])],"derivedFrom":subQ9})])]}),makeQuery(id+"F47.opFillet","BLEND_FACE",FACE,{"disambiguationData":[OSD([subQ5,subQ7]),TDD([makeQuery(id+"F42.boolean.opBoolean","COPY",EDGE,{"disambiguationData":[TD([makeQuery(id+"F9.opLoft","SWEPT_FACE",FACE,{"disambiguationData":[OSD([sQuery(id+"F3.wireOp",EDGE,"E20.12.0"),subQ55,subQ54,sQuery(id+"F4.wireOp",EDGE,"E26.12.0"),subQ53,subQ52])]})])],"derivedFrom":subQ9})])]}),makeQuery(id+"F47.opFillet","BLEND_FACE",FACE,{"disambiguationData":[OSD([subQ5,subQ7]),TDD([makeQuery(id+"F42.boolean.opBoolean","COPY",EDGE,{"disambiguationData":[TD([makeQuery(id+"F10.opLoft","SWEPT_FACE",FACE,{"disambiguationData":[OSD([sQuery(id+"F3.wireOp",EDGE,"E20.11.0"),subQ51,subQ50,sQuery(id+"F4.wireOp",EDGE,"E26.11.0"),subQ49,subQ48])]})])],"derivedFrom":subQ9})])]}),makeQuery(id+"F47.opFillet","BLEND_FACE",FACE,{"disambiguationData":[OSD([subQ5,subQ7]),TDD([makeQuery(id+"F42.boolean.opBoolean","COPY",EDGE,{"disambiguationData":[TD([makeQuery(id+"F11.opLoft","SWEPT_FACE",FACE,{"disambiguationData":[OSD([sQuery(id+"F3.wireOp",EDGE,"E20.10.0"),subQ47,subQ46,sQuery(id+"F4.wireOp",EDGE,"E26.10.0"),subQ45,subQ44])]})])],"derivedFrom":subQ9})])]}),makeQuery(id+"F47.opFillet","BLEND_FACE",FACE,{"disambiguationData":[OSD([subQ5,subQ7]),TDD([makeQuery(id+"F42.boolean.opBoolean","COPY",EDGE,{"disambiguationData":[TD([makeQuery(id+"F12.opLoft","SWEPT_FACE",FACE,{"disambiguationData":[OSD([sQuery(id+"F3.wireOp",EDGE,"E20.9.0"),subQ43,subQ42,sQuery(id+"F4.wireOp",EDGE,"E26.9.0"),subQ41,subQ40])]})])],"derivedFrom":subQ9})])]}),makeQuery(id+"F47.opFillet","BLEND_FACE",FACE,{"disambiguationData":[OSD([subQ5,subQ7]),TDD([makeQuery(id+"F42.boolean.opBoolean","COPY",EDGE,{"disambiguationData":[TD([makeQuery(id+"F13.opLoft","SWEPT_FACE",FACE,{"disambiguationData":[OSD([sQuery(id+"F3.wireOp",EDGE,"E20.8.0"),subQ39,subQ38,sQuery(id+"F4.wireOp",EDGE,"E26.8.0"),subQ37,subQ36])]})])],"derivedFrom":subQ9})])]}),makeQuery(id+"F47.opFillet","BLEND_FACE",FACE,{"disambiguationData":[OSD([subQ5,subQ7]),TDD([makeQuery(id+"F42.boolean.opBoolean","COPY",EDGE,{"disambiguationData":[TD([makeQuery(id+"F14.opLoft","SWEPT_FACE",FACE,{"disambiguationData":[OSD([sQuery(id+"F3.wireOp",EDGE,"E20.7.0"),subQ35,subQ34,sQuery(id+"F4.wireOp",EDGE,"E26.7.0"),subQ33,subQ32])]})])],"derivedFrom":subQ9})])]}),makeQuery(id+"F47.opFillet","BLEND_FACE",FACE,{"disambiguationData":[OSD([subQ5,subQ7]),TDD([makeQuery(id+"F42.boolean.opBoolean","COPY",EDGE,{"disambiguationData":[TD([makeQuery(id+"F15.opLoft","SWEPT_FACE",FACE,{"disambiguationData":[OSD([sQuery(id+"F3.wireOp",EDGE,"E20.6.0"),subQ31,subQ30,sQuery(id+"F4.wireOp",EDGE,"E26.6.0"),subQ29,subQ28])]})])],"derivedFrom":subQ9})])]}),makeQuery(id+"F47.opFillet","BLEND_FACE",FACE,{"disambiguationData":[OSD([subQ5,subQ7]),TDD([makeQuery(id+"F42.boolean.opBoolean","COPY",EDGE,{"disambiguationData":[TD([makeQuery(id+"F16.opLoft","SWEPT_FACE",FACE,{"disambiguationData":[OSD([sQuery(id+"F3.wireOp",EDGE,"E20.5.0"),subQ27,subQ26,sQuery(id+"F4.wireOp",EDGE,"E26.5.0"),subQ25,subQ24])]})])],"derivedFrom":subQ9})])]}),makeQuery(id+"F47.opFillet","BLEND_FACE",FACE,{"disambiguationData":[OSD([subQ5,subQ7]),TDD([makeQuery(id+"F42.boolean.opBoolean","COPY",EDGE,{"disambiguationData":[TD([makeQuery(id+"F17.opLoft","SWEPT_FACE",FACE,{"disambiguationData":[OSD([sQuery(id+"F3.wireOp",EDGE,"E20.4.0"),subQ23,subQ22,sQuery(id+"F4.wireOp",EDGE,"E26.4.0"),subQ21,subQ20])]})])],"derivedFrom":subQ9})])]}),makeQuery(id+"F47.opFillet","BLEND_FACE",FACE,{"disambiguationData":[OSD([subQ5,subQ7]),TDD([makeQuery(id+"F42.boolean.opBoolean","COPY",EDGE,{"disambiguationData":[TD([makeQuery(id+"F18.opLoft","SWEPT_FACE",FACE,{"disambiguationData":[OSD([sQuery(id+"F3.wireOp",EDGE,"E20.3.0"),subQ19,subQ18,sQuery(id+"F4.wireOp",EDGE,"E26.3.0"),subQ17,subQ16])]})])],"derivedFrom":subQ9})])]}),makeQuery(id+"F47.opFillet","BLEND_FACE",FACE,{"disambiguationData":[OSD([subQ5,subQ7]),TDD([makeQuery(id+"F42.boolean.opBoolean","COPY",EDGE,{"disambiguationData":[TD([subQ15])],"derivedFrom":subQ9})])]}),makeQuery(id+"F47.opFillet","BLEND_FACE",FACE,{"disambiguationData":[OSD([subQ5,subQ7]),TDD([makeQuery(id+"F42.boolean.opBoolean","COPY",EDGE,{"disambiguationData":[TD([makeQuery(id+"F20.opLoft","SWEPT_FACE",FACE,{"disambiguationData":[OSD([sQuery(id+"F3.wireOp",EDGE,"E20.1.0"),subQ4,subQ3,sQuery(id+"F4.wireOp",EDGE,"E26.1.0"),subQ2,subQ1])]})])],"derivedFrom":subQ9})])]})],"blendedInto":[makeQuery(id+"F47.opFillet","BLEND_FACE",FACE,{"disambiguationData":[OSD([subQ5,subQ7]),TDD([makeQuery(id+"F42.boolean.opBoolean","COPY",EDGE,{"disambiguationData":[TD([makeQuery(id+"F5.opLoft","SWEPT_FACE",FACE,{"disambiguationData":[OSD([subQ71,subQ70,sQuery(id+"F3.wireOp",EDGE,"E18.left"),sQuery(id+"F4.wireOp",EDGE,"E21"),subQ69,subQ68])]})])],"derivedFrom":subQ9})])]}),makeQuery(id+"F47.opFillet","BLEND_FACE",FACE,{"disambiguationData":[OSD([subQ5,subQ7]),TDD([makeQuery(id+"F42.boolean.opBoolean","COPY",EDGE,{"disambiguationData":[TD([makeQuery(id+"F6.opLoft","SWEPT_FACE",FACE,{"disambiguationData":[OSD([sQuery(id+"F3.wireOp",EDGE,"E20.15.0"),subQ67,subQ66,sQuery(id+"F4.wireOp",EDGE,"E26.15.0"),subQ65,subQ64])]})])],"derivedFrom":subQ9})])]}),makeQuery(id+"F47.opFillet","BLEND_FACE",FACE,{"disambiguationData":[OSD([subQ5,subQ7]),TDD([makeQuery(id+"F42.boolean.opBoolean","COPY",EDGE,{"disambiguationData":[TD([makeQuery(id+"F7.opLoft","SWEPT_FACE",FACE,{"disambiguationData":[OSD([sQuery(id+"F3.wireOp",EDGE,"E20.14.0"),subQ63,subQ62,sQuery(id+"F4.wireOp",EDGE,"E26.14.0"),subQ61,subQ60])]})])],"derivedFrom":subQ9})])]}),makeQuery(id+"F47.opFillet","BLEND_FACE",FACE,{"disambiguationData":[OSD([subQ5,subQ7]),TDD([makeQuery(id+"F42.boolean.opBoolean","COPY",EDGE,{"disambiguationData":[TD([makeQuery(id+"F8.opLoft","SWEPT_FACE",FACE,{"disambiguationData":[OSD([sQuery(id+"F3.wireOp",EDGE,"E20.13.0"),subQ59,subQ58,sQuery(id+"F4.wireOp",EDGE,"E26.13.0"),subQ57,subQ56])]})])],"derivedFrom":subQ9})])]}),makeQuery(id+"F47.opFillet","BLEND_FACE",FACE,{"disambiguationData":[OSD([subQ5,subQ7]),TDD([makeQuery(id+"F42.boolean.opBoolean","COPY",EDGE,{"disambiguationData":[TD([makeQuery(id+"F9.opLoft","SWEPT_FACE",FACE,{"disambiguationData":[OSD([sQuery(id+"F3.wireOp",EDGE,"E20.12.0"),subQ55,subQ54,sQuery(id+"F4.wireOp",EDGE,"E26.12.0"),subQ53,subQ52])]})])],"derivedFrom":subQ9})])]}),makeQuery(id+"F47.opFillet","BLEND_FACE",FACE,{"disambiguationData":[OSD([subQ5,subQ7]),TDD([makeQuery(id+"F42.boolean.opBoolean","COPY",EDGE,{"disambiguationData":[TD([makeQuery(id+"F10.opLoft","SWEPT_FACE",FACE,{"disambiguationData":[OSD([sQuery(id+"F3.wireOp",EDGE,"E20.11.0"),subQ51,subQ50,sQuery(id+"F4.wireOp",EDGE,"E26.11.0"),subQ49,subQ48])]})])],"derivedFrom":subQ9})])]}),makeQuery(id+"F47.opFillet","BLEND_FACE",FACE,{"disambiguationData":[OSD([subQ5,subQ7]),TDD([makeQuery(id+"F42.boolean.opBoolean","COPY",EDGE,{"disambiguationData":[TD([makeQuery(id+"F11.opLoft","SWEPT_FACE",FACE,{"disambiguationData":[OSD([sQuery(id+"F3.wireOp",EDGE,"E20.10.0"),subQ47,subQ46,sQuery(id+"F4.wireOp",EDGE,"E26.10.0"),subQ45,subQ44])]})])],"derivedFrom":subQ9})])]}),makeQuery(id+"F47.opFillet","BLEND_FACE",FACE,{"disambiguationData":[OSD([subQ5,subQ7]),TDD([makeQuery(id+"F42.boolean.opBoolean","COPY",EDGE,{"disambiguationData":[TD([makeQuery(id+"F12.opLoft","SWEPT_FACE",FACE,{"disambiguationData":[OSD([sQuery(id+"F3.wireOp",EDGE,"E20.9.0"),subQ43,subQ42,sQuery(id+"F4.wireOp",EDGE,"E26.9.0"),subQ41,subQ40])]})])],"derivedFrom":subQ9})])]}),makeQuery(id+"F47.opFillet","BLEND_FACE",FACE,{"disambiguationData":[OSD([subQ5,subQ7]),TDD([makeQuery(id+"F42.boolean.opBoolean","COPY",EDGE,{"disambiguationData":[TD([makeQuery(id+"F13.opLoft","SWEPT_FACE",FACE,{"disambiguationData":[OSD([sQuery(id+"F3.wireOp",EDGE,"E20.8.0"),subQ39,subQ38,sQuery(id+"F4.wireOp",EDGE,"E26.8.0"),subQ37,subQ36])]})])],"derivedFrom":subQ9})])]}),makeQuery(id+"F47.opFillet","BLEND_FACE",FACE,{"disambiguationData":[OSD([subQ5,subQ7]),TDD([makeQuery(id+"F42.boolean.opBoolean","COPY",EDGE,{"disambiguationData":[TD([makeQuery(id+"F14.opLoft","SWEPT_FACE",FACE,{"disambiguationData":[OSD([sQuery(id+"F3.wireOp",EDGE,"E20.7.0"),subQ35,subQ34,sQuery(id+"F4.wireOp",EDGE,"E26.7.0"),subQ33,subQ32])]})])],"derivedFrom":subQ9})])]}),makeQuery(id+"F47.opFillet","BLEND_FACE",FACE,{"disambiguationData":[OSD([subQ5,subQ7]),TDD([makeQuery(id+"F42.boolean.opBoolean","COPY",EDGE,{"disambiguationData":[TD([makeQuery(id+"F15.opLoft","SWEPT_FACE",FACE,{"disambiguationData":[OSD([sQuery(id+"F3.wireOp",EDGE,"E20.6.0"),subQ31,subQ30,sQuery(id+"F4.wireOp",EDGE,"E26.6.0"),subQ29,subQ28])]})])],"derivedFrom":subQ9})])]}),makeQuery(id+"F47.opFillet","BLEND_FACE",FACE,{"disambiguationData":[OSD([subQ5,subQ7]),TDD([makeQuery(id+"F42.boolean.opBoolean","COPY",EDGE,{"disambiguationData":[TD([makeQuery(id+"F16.opLoft","SWEPT_FACE",FACE,{"disambiguationData":[OSD([sQuery(id+"F3.wireOp",EDGE,"E20.5.0"),subQ27,subQ26,sQuery(id+"F4.wireOp",EDGE,"E26.5.0"),subQ25,subQ24])]})])],"derivedFrom":subQ9})])]}),makeQuery(id+"F47.opFillet","BLEND_FACE",FACE,{"disambiguationData":[OSD([subQ5,subQ7]),TDD([makeQuery(id+"F42.boolean.opBoolean","COPY",EDGE,{"disambiguationData":[TD([makeQuery(id+"F17.opLoft","SWEPT_FACE",FACE,{"disambiguationData":[OSD([sQuery(id+"F3.wireOp",EDGE,"E20.4.0"),subQ23,subQ22,sQuery(id+"F4.wireOp",EDGE,"E26.4.0"),subQ21,subQ20])]})])],"derivedFrom":subQ9})])]}),makeQuery(id+"F47.opFillet","BLEND_FACE",FACE,{"disambiguationData":[OSD([subQ5,subQ7]),TDD([makeQuery(id+"F42.boolean.opBoolean","COPY",EDGE,{"disambiguationData":[TD([makeQuery(id+"F18.opLoft","SWEPT_FACE",FACE,{"disambiguationData":[OSD([sQuery(id+"F3.wireOp",EDGE,"E20.3.0"),subQ19,subQ18,sQuery(id+"F4.wireOp",EDGE,"E26.3.0"),subQ17,subQ16])]})])],"derivedFrom":subQ9})])]}),makeQuery(id+"F47.opFillet","BLEND_FACE",FACE,{"disambiguationData":[OSD([subQ5,subQ7]),TDD([makeQuery(id+"F42.boolean.opBoolean","COPY",EDGE,{"disambiguationData":[TD([subQ15])],"derivedFrom":subQ9})])]}),makeQuery(id+"F47.opFillet","BLEND_FACE",FACE,{"disambiguationData":[OSD([subQ5,subQ7]),TDD([makeQuery(id+"F42.boolean.opBoolean","COPY",EDGE,{"disambiguationData":[TD([makeQuery(id+"F20.opLoft","SWEPT_FACE",FACE,{"disambiguationData":[OSD([sQuery(id+"F3.wireOp",EDGE,"E20.1.0"),subQ4,subQ3,sQuery(id+"F4.wireOp",EDGE,"E26.1.0"),subQ2,subQ1])]})])],"derivedFrom":subQ9})])]})]});}
            var Q53;
            {var subQ0=makeQuery(id+"F40.opExtrude","CAP_FACE",FACE,{"disambiguationData":[OSD([sQuery(id+"F39.wireOp",EDGE,"E29"),sQuery(id+"F39.wireOp",EDGE,"E30")])],"isStart":false});var subQ1=sQuery(id+"F4.wireOp",EDGE,"E26.1.3");var subQ2=sQuery(id+"F4.wireOp",EDGE,"E26.1.2");var subQ3=sQuery(id+"F3.wireOp",EDGE,"E20.1.3");var subQ4=sQuery(id+"F3.wireOp",EDGE,"E20.1.1");var subQ6=sQuery(id+"F41.wireOp",EDGE,"E35");var subQ7=makeQuery(id+"F42.opRevolve","SWEPT_FACE",FACE,{"disambiguationData":[OSD([subQ6])]});var subQ8=makeQuery(id+"F20.opLoft","SWEPT_FACE",FACE,{"disambiguationData":[OSD([sQuery(id+"F3.wireOp",EDGE,"E20.1.0"),subQ4,subQ3,sQuery(id+"F4.wireOp",EDGE,"E26.1.0"),subQ2,subQ1])]});var subQ9=sQuery(id+"F41.wireOp",EDGE,"E36");var subQ10=makeQuery(id+"F42.opRevolve","SWEPT_FACE",FACE,{"disambiguationData":[OSD([subQ9])]});var subQ11=makeQuery(id+"F42.opRevolve","SWEPT_EDGE",EDGE,{"disambiguationData":[OSD([subQ6,subQ9])]});var subQ12=sQuery(id+"F4.wireOp",EDGE,"E26.2.3");var subQ13=sQuery(id+"F4.wireOp",EDGE,"E26.2.2");var subQ14=sQuery(id+"F3.wireOp",EDGE,"E20.2.3");var subQ15=sQuery(id+"F3.wireOp",EDGE,"E20.2.1");var subQ16=sQuery(id+"F4.wireOp",EDGE,"E26.3.3");var subQ17=sQuery(id+"F4.wireOp",EDGE,"E26.3.2");var subQ18=sQuery(id+"F3.wireOp",EDGE,"E20.3.3");var subQ19=sQuery(id+"F3.wireOp",EDGE,"E20.3.1");var subQ20=sQuery(id+"F4.wireOp",EDGE,"E26.4.3");var subQ21=sQuery(id+"F4.wireOp",EDGE,"E26.4.2");var subQ22=sQuery(id+"F3.wireOp",EDGE,"E20.4.3");var subQ23=sQuery(id+"F3.wireOp",EDGE,"E20.4.1");var subQ24=sQuery(id+"F4.wireOp",EDGE,"E26.5.3");var subQ25=sQuery(id+"F4.wireOp",EDGE,"E26.5.2");var subQ26=sQuery(id+"F3.wireOp",EDGE,"E20.5.3");var subQ27=sQuery(id+"F3.wireOp",EDGE,"E20.5.1");var subQ28=sQuery(id+"F4.wireOp",EDGE,"E26.6.3");var subQ29=sQuery(id+"F4.wireOp",EDGE,"E26.6.2");var subQ30=sQuery(id+"F3.wireOp",EDGE,"E20.6.3");var subQ31=sQuery(id+"F3.wireOp",EDGE,"E20.6.1");var subQ32=sQuery(id+"F4.wireOp",EDGE,"E26.7.3");var subQ33=sQuery(id+"F4.wireOp",EDGE,"E26.7.2");var subQ34=sQuery(id+"F3.wireOp",EDGE,"E20.7.3");var subQ35=sQuery(id+"F3.wireOp",EDGE,"E20.7.1");var subQ36=sQuery(id+"F4.wireOp",EDGE,"E26.8.3");var subQ37=sQuery(id+"F4.wireOp",EDGE,"E26.8.2");var subQ38=sQuery(id+"F3.wireOp",EDGE,"E20.8.3");var subQ39=sQuery(id+"F3.wireOp",EDGE,"E20.8.1");var subQ40=sQuery(id+"F4.wireOp",EDGE,"E26.9.3");var subQ41=sQuery(id+"F4.wireOp",EDGE,"E26.9.2");var subQ42=sQuery(id+"F3.wireOp",EDGE,"E20.9.3");var subQ43=sQuery(id+"F3.wireOp",EDGE,"E20.9.1");var subQ44=sQuery(id+"F4.wireOp",EDGE,"E26.10.3");var subQ45=sQuery(id+"F4.wireOp",EDGE,"E26.10.2");var subQ46=sQuery(id+"F3.wireOp",EDGE,"E20.10.3");var subQ47=sQuery(id+"F3.wireOp",EDGE,"E20.10.1");var subQ48=sQuery(id+"F4.wireOp",EDGE,"E26.11.3");var subQ49=sQuery(id+"F4.wireOp",EDGE,"E26.11.2");var subQ50=sQuery(id+"F3.wireOp",EDGE,"E20.11.3");var subQ51=sQuery(id+"F3.wireOp",EDGE,"E20.11.1");var subQ52=sQuery(id+"F4.wireOp",EDGE,"E26.12.3");var subQ53=sQuery(id+"F4.wireOp",EDGE,"E26.12.2");var subQ54=sQuery(id+"F3.wireOp",EDGE,"E20.12.3");var subQ55=sQuery(id+"F3.wireOp",EDGE,"E20.12.1");var subQ56=sQuery(id+"F4.wireOp",EDGE,"E26.13.3");var subQ57=sQuery(id+"F4.wireOp",EDGE,"E26.13.2");var subQ58=sQuery(id+"F3.wireOp",EDGE,"E20.13.3");var subQ59=sQuery(id+"F3.wireOp",EDGE,"E20.13.1");var subQ60=sQuery(id+"F4.wireOp",EDGE,"E26.14.3");var subQ61=sQuery(id+"F4.wireOp",EDGE,"E26.14.2");var subQ62=sQuery(id+"F3.wireOp",EDGE,"E20.14.3");var subQ63=sQuery(id+"F3.wireOp",EDGE,"E20.14.1");var subQ64=sQuery(id+"F4.wireOp",EDGE,"E26.15.3");var subQ65=sQuery(id+"F4.wireOp",EDGE,"E26.15.2");var subQ66=sQuery(id+"F3.wireOp",EDGE,"E20.15.3");var subQ67=sQuery(id+"F3.wireOp",EDGE,"E20.15.1");var subQ68=sQuery(id+"F4.wireOp",EDGE,"E23");var subQ69=sQuery(id+"F4.wireOp",EDGE,"E22");var subQ70=sQuery(id+"F3.wireOp",EDGE,"E18.top");var subQ71=sQuery(id+"F3.wireOp",EDGE,"E18.bottom");var subQ74=makeQuery(id+"F42.boolean.opBoolean","COPY",FACE,{"disambiguationData":[TD([subQ8])],"derivedFrom":subQ7});var subQ75=makeQuery(id+"F20.boolean.opBoolean","INTERSECT",EDGE,{"derivedFrom":[makeQuery(id+"F1.opRevolve","SWEPT_FACE",FACE,{"disambiguationData":[OSD([sQuery(id+"F0.wireOp",EDGE,"E4")])]}),subQ8]});Q53=makeQuery(id+"F48.opFillet","BLEND_EDGE",EDGE,{"blendedFrom":[makeQuery(id+"F47.opFillet","TWEAK_EDGE",EDGE,{"derivedFrom":[makeQuery(id+"F45.opFillet","BLEND_VERTEX",VERTEX,{"blendedFrom":[subQ75,subQ8,subQ74],"blendedInto":[subQ8,subQ74]}),makeQuery(id+"F45.opFillet","BLEND_VERTEX",VERTEX,{"blendedFrom":[subQ75,makeQuery(id+"F42.boolean.opBoolean","MERGE",FACE,{"derivedFrom":[subQ0,subQ10]}),subQ74],"blendedInto":[makeQuery(id+"F42.boolean.opBoolean","MERGE",FACE,{"derivedFrom":[subQ0,subQ10]}),subQ74]})]}),makeQuery(id+"F47.opFillet","BLEND_FACE",FACE,{"disambiguationData":[OSD([subQ6,subQ9]),TDD([makeQuery(id+"F42.boolean.opBoolean","COPY",EDGE,{"disambiguationData":[TD([makeQuery(id+"F5.opLoft","SWEPT_FACE",FACE,{"disambiguationData":[OSD([subQ71,subQ70,sQuery(id+"F3.wireOp",EDGE,"E18.left"),sQuery(id+"F4.wireOp",EDGE,"E21"),subQ69,subQ68])]})])],"derivedFrom":subQ11})])]}),makeQuery(id+"F47.opFillet","BLEND_FACE",FACE,{"disambiguationData":[OSD([subQ6,subQ9]),TDD([makeQuery(id+"F42.boolean.opBoolean","COPY",EDGE,{"disambiguationData":[TD([makeQuery(id+"F6.opLoft","SWEPT_FACE",FACE,{"disambiguationData":[OSD([sQuery(id+"F3.wireOp",EDGE,"E20.15.0"),subQ67,subQ66,sQuery(id+"F4.wireOp",EDGE,"E26.15.0"),subQ65,subQ64])]})])],"derivedFrom":subQ11})])]}),makeQuery(id+"F47.opFillet","BLEND_FACE",FACE,{"disambiguationData":[OSD([subQ6,subQ9]),TDD([makeQuery(id+"F42.boolean.opBoolean","COPY",EDGE,{"disambiguationData":[TD([makeQuery(id+"F7.opLoft","SWEPT_FACE",FACE,{"disambiguationData":[OSD([sQuery(id+"F3.wireOp",EDGE,"E20.14.0"),subQ63,subQ62,sQuery(id+"F4.wireOp",EDGE,"E26.14.0"),subQ61,subQ60])]})])],"derivedFrom":subQ11})])]}),makeQuery(id+"F47.opFillet","BLEND_FACE",FACE,{"disambiguationData":[OSD([subQ6,subQ9]),TDD([makeQuery(id+"F42.boolean.opBoolean","COPY",EDGE,{"disambiguationData":[TD([makeQuery(id+"F8.opLoft","SWEPT_FACE",FACE,{"disambiguationData":[OSD([sQuery(id+"F3.wireOp",EDGE,"E20.13.0"),subQ59,subQ58,sQuery(id+"F4.wireOp",EDGE,"E26.13.0"),subQ57,subQ56])]})])],"derivedFrom":subQ11})])]}),makeQuery(id+"F47.opFillet","BLEND_FACE",FACE,{"disambiguationData":[OSD([subQ6,subQ9]),TDD([makeQuery(id+"F42.boolean.opBoolean","COPY",EDGE,{"disambiguationData":[TD([makeQuery(id+"F9.opLoft","SWEPT_FACE",FACE,{"disambiguationData":[OSD([sQuery(id+"F3.wireOp",EDGE,"E20.12.0"),subQ55,subQ54,sQuery(id+"F4.wireOp",EDGE,"E26.12.0"),subQ53,subQ52])]})])],"derivedFrom":subQ11})])]}),makeQuery(id+"F47.opFillet","BLEND_FACE",FACE,{"disambiguationData":[OSD([subQ6,subQ9]),TDD([makeQuery(id+"F42.boolean.opBoolean","COPY",EDGE,{"disambiguationData":[TD([makeQuery(id+"F10.opLoft","SWEPT_FACE",FACE,{"disambiguationData":[OSD([sQuery(id+"F3.wireOp",EDGE,"E20.11.0"),subQ51,subQ50,sQuery(id+"F4.wireOp",EDGE,"E26.11.0"),subQ49,subQ48])]})])],"derivedFrom":subQ11})])]}),makeQuery(id+"F47.opFillet","BLEND_FACE",FACE,{"disambiguationData":[OSD([subQ6,subQ9]),TDD([makeQuery(id+"F42.boolean.opBoolean","COPY",EDGE,{"disambiguationData":[TD([makeQuery(id+"F11.opLoft","SWEPT_FACE",FACE,{"disambiguationData":[OSD([sQuery(id+"F3.wireOp",EDGE,"E20.10.0"),subQ47,subQ46,sQuery(id+"F4.wireOp",EDGE,"E26.10.0"),subQ45,subQ44])]})])],"derivedFrom":subQ11})])]}),makeQuery(id+"F47.opFillet","BLEND_FACE",FACE,{"disambiguationData":[OSD([subQ6,subQ9]),TDD([makeQuery(id+"F42.boolean.opBoolean","COPY",EDGE,{"disambiguationData":[TD([makeQuery(id+"F12.opLoft","SWEPT_FACE",FACE,{"disambiguationData":[OSD([sQuery(id+"F3.wireOp",EDGE,"E20.9.0"),subQ43,subQ42,sQuery(id+"F4.wireOp",EDGE,"E26.9.0"),subQ41,subQ40])]})])],"derivedFrom":subQ11})])]}),makeQuery(id+"F47.opFillet","BLEND_FACE",FACE,{"disambiguationData":[OSD([subQ6,subQ9]),TDD([makeQuery(id+"F42.boolean.opBoolean","COPY",EDGE,{"disambiguationData":[TD([makeQuery(id+"F13.opLoft","SWEPT_FACE",FACE,{"disambiguationData":[OSD([sQuery(id+"F3.wireOp",EDGE,"E20.8.0"),subQ39,subQ38,sQuery(id+"F4.wireOp",EDGE,"E26.8.0"),subQ37,subQ36])]})])],"derivedFrom":subQ11})])]}),makeQuery(id+"F47.opFillet","BLEND_FACE",FACE,{"disambiguationData":[OSD([subQ6,subQ9]),TDD([makeQuery(id+"F42.boolean.opBoolean","COPY",EDGE,{"disambiguationData":[TD([makeQuery(id+"F14.opLoft","SWEPT_FACE",FACE,{"disambiguationData":[OSD([sQuery(id+"F3.wireOp",EDGE,"E20.7.0"),subQ35,subQ34,sQuery(id+"F4.wireOp",EDGE,"E26.7.0"),subQ33,subQ32])]})])],"derivedFrom":subQ11})])]}),makeQuery(id+"F47.opFillet","BLEND_FACE",FACE,{"disambiguationData":[OSD([subQ6,subQ9]),TDD([makeQuery(id+"F42.boolean.opBoolean","COPY",EDGE,{"disambiguationData":[TD([makeQuery(id+"F15.opLoft","SWEPT_FACE",FACE,{"disambiguationData":[OSD([sQuery(id+"F3.wireOp",EDGE,"E20.6.0"),subQ31,subQ30,sQuery(id+"F4.wireOp",EDGE,"E26.6.0"),subQ29,subQ28])]})])],"derivedFrom":subQ11})])]}),makeQuery(id+"F47.opFillet","BLEND_FACE",FACE,{"disambiguationData":[OSD([subQ6,subQ9]),TDD([makeQuery(id+"F42.boolean.opBoolean","COPY",EDGE,{"disambiguationData":[TD([makeQuery(id+"F16.opLoft","SWEPT_FACE",FACE,{"disambiguationData":[OSD([sQuery(id+"F3.wireOp",EDGE,"E20.5.0"),subQ27,subQ26,sQuery(id+"F4.wireOp",EDGE,"E26.5.0"),subQ25,subQ24])]})])],"derivedFrom":subQ11})])]}),makeQuery(id+"F47.opFillet","BLEND_FACE",FACE,{"disambiguationData":[OSD([subQ6,subQ9]),TDD([makeQuery(id+"F42.boolean.opBoolean","COPY",EDGE,{"disambiguationData":[TD([makeQuery(id+"F17.opLoft","SWEPT_FACE",FACE,{"disambiguationData":[OSD([sQuery(id+"F3.wireOp",EDGE,"E20.4.0"),subQ23,subQ22,sQuery(id+"F4.wireOp",EDGE,"E26.4.0"),subQ21,subQ20])]})])],"derivedFrom":subQ11})])]}),makeQuery(id+"F47.opFillet","BLEND_FACE",FACE,{"disambiguationData":[OSD([subQ6,subQ9]),TDD([makeQuery(id+"F42.boolean.opBoolean","COPY",EDGE,{"disambiguationData":[TD([makeQuery(id+"F18.opLoft","SWEPT_FACE",FACE,{"disambiguationData":[OSD([sQuery(id+"F3.wireOp",EDGE,"E20.3.0"),subQ19,subQ18,sQuery(id+"F4.wireOp",EDGE,"E26.3.0"),subQ17,subQ16])]})])],"derivedFrom":subQ11})])]}),makeQuery(id+"F47.opFillet","BLEND_FACE",FACE,{"disambiguationData":[OSD([subQ6,subQ9]),TDD([makeQuery(id+"F42.boolean.opBoolean","COPY",EDGE,{"disambiguationData":[TD([makeQuery(id+"F19.opLoft","SWEPT_FACE",FACE,{"disambiguationData":[OSD([sQuery(id+"F3.wireOp",EDGE,"E20.2.0"),subQ15,subQ14,sQuery(id+"F4.wireOp",EDGE,"E26.2.0"),subQ13,subQ12])]})])],"derivedFrom":subQ11})])]}),makeQuery(id+"F47.opFillet","BLEND_FACE",FACE,{"disambiguationData":[OSD([subQ6,subQ9]),TDD([makeQuery(id+"F42.boolean.opBoolean","COPY",EDGE,{"disambiguationData":[TD([subQ8])],"derivedFrom":subQ11})])]})],"blendedInto":[makeQuery(id+"F47.opFillet","BLEND_FACE",FACE,{"disambiguationData":[OSD([subQ6,subQ9]),TDD([makeQuery(id+"F42.boolean.opBoolean","COPY",EDGE,{"disambiguationData":[TD([makeQuery(id+"F5.opLoft","SWEPT_FACE",FACE,{"disambiguationData":[OSD([subQ71,subQ70,sQuery(id+"F3.wireOp",EDGE,"E18.left"),sQuery(id+"F4.wireOp",EDGE,"E21"),subQ69,subQ68])]})])],"derivedFrom":subQ11})])]}),makeQuery(id+"F47.opFillet","BLEND_FACE",FACE,{"disambiguationData":[OSD([subQ6,subQ9]),TDD([makeQuery(id+"F42.boolean.opBoolean","COPY",EDGE,{"disambiguationData":[TD([makeQuery(id+"F6.opLoft","SWEPT_FACE",FACE,{"disambiguationData":[OSD([sQuery(id+"F3.wireOp",EDGE,"E20.15.0"),subQ67,subQ66,sQuery(id+"F4.wireOp",EDGE,"E26.15.0"),subQ65,subQ64])]})])],"derivedFrom":subQ11})])]}),makeQuery(id+"F47.opFillet","BLEND_FACE",FACE,{"disambiguationData":[OSD([subQ6,subQ9]),TDD([makeQuery(id+"F42.boolean.opBoolean","COPY",EDGE,{"disambiguationData":[TD([makeQuery(id+"F7.opLoft","SWEPT_FACE",FACE,{"disambiguationData":[OSD([sQuery(id+"F3.wireOp",EDGE,"E20.14.0"),subQ63,subQ62,sQuery(id+"F4.wireOp",EDGE,"E26.14.0"),subQ61,subQ60])]})])],"derivedFrom":subQ11})])]}),makeQuery(id+"F47.opFillet","BLEND_FACE",FACE,{"disambiguationData":[OSD([subQ6,subQ9]),TDD([makeQuery(id+"F42.boolean.opBoolean","COPY",EDGE,{"disambiguationData":[TD([makeQuery(id+"F8.opLoft","SWEPT_FACE",FACE,{"disambiguationData":[OSD([sQuery(id+"F3.wireOp",EDGE,"E20.13.0"),subQ59,subQ58,sQuery(id+"F4.wireOp",EDGE,"E26.13.0"),subQ57,subQ56])]})])],"derivedFrom":subQ11})])]}),makeQuery(id+"F47.opFillet","BLEND_FACE",FACE,{"disambiguationData":[OSD([subQ6,subQ9]),TDD([makeQuery(id+"F42.boolean.opBoolean","COPY",EDGE,{"disambiguationData":[TD([makeQuery(id+"F9.opLoft","SWEPT_FACE",FACE,{"disambiguationData":[OSD([sQuery(id+"F3.wireOp",EDGE,"E20.12.0"),subQ55,subQ54,sQuery(id+"F4.wireOp",EDGE,"E26.12.0"),subQ53,subQ52])]})])],"derivedFrom":subQ11})])]}),makeQuery(id+"F47.opFillet","BLEND_FACE",FACE,{"disambiguationData":[OSD([subQ6,subQ9]),TDD([makeQuery(id+"F42.boolean.opBoolean","COPY",EDGE,{"disambiguationData":[TD([makeQuery(id+"F10.opLoft","SWEPT_FACE",FACE,{"disambiguationData":[OSD([sQuery(id+"F3.wireOp",EDGE,"E20.11.0"),subQ51,subQ50,sQuery(id+"F4.wireOp",EDGE,"E26.11.0"),subQ49,subQ48])]})])],"derivedFrom":subQ11})])]}),makeQuery(id+"F47.opFillet","BLEND_FACE",FACE,{"disambiguationData":[OSD([subQ6,subQ9]),TDD([makeQuery(id+"F42.boolean.opBoolean","COPY",EDGE,{"disambiguationData":[TD([makeQuery(id+"F11.opLoft","SWEPT_FACE",FACE,{"disambiguationData":[OSD([sQuery(id+"F3.wireOp",EDGE,"E20.10.0"),subQ47,subQ46,sQuery(id+"F4.wireOp",EDGE,"E26.10.0"),subQ45,subQ44])]})])],"derivedFrom":subQ11})])]}),makeQuery(id+"F47.opFillet","BLEND_FACE",FACE,{"disambiguationData":[OSD([subQ6,subQ9]),TDD([makeQuery(id+"F42.boolean.opBoolean","COPY",EDGE,{"disambiguationData":[TD([makeQuery(id+"F12.opLoft","SWEPT_FACE",FACE,{"disambiguationData":[OSD([sQuery(id+"F3.wireOp",EDGE,"E20.9.0"),subQ43,subQ42,sQuery(id+"F4.wireOp",EDGE,"E26.9.0"),subQ41,subQ40])]})])],"derivedFrom":subQ11})])]}),makeQuery(id+"F47.opFillet","BLEND_FACE",FACE,{"disambiguationData":[OSD([subQ6,subQ9]),TDD([makeQuery(id+"F42.boolean.opBoolean","COPY",EDGE,{"disambiguationData":[TD([makeQuery(id+"F13.opLoft","SWEPT_FACE",FACE,{"disambiguationData":[OSD([sQuery(id+"F3.wireOp",EDGE,"E20.8.0"),subQ39,subQ38,sQuery(id+"F4.wireOp",EDGE,"E26.8.0"),subQ37,subQ36])]})])],"derivedFrom":subQ11})])]}),makeQuery(id+"F47.opFillet","BLEND_FACE",FACE,{"disambiguationData":[OSD([subQ6,subQ9]),TDD([makeQuery(id+"F42.boolean.opBoolean","COPY",EDGE,{"disambiguationData":[TD([makeQuery(id+"F14.opLoft","SWEPT_FACE",FACE,{"disambiguationData":[OSD([sQuery(id+"F3.wireOp",EDGE,"E20.7.0"),subQ35,subQ34,sQuery(id+"F4.wireOp",EDGE,"E26.7.0"),subQ33,subQ32])]})])],"derivedFrom":subQ11})])]}),makeQuery(id+"F47.opFillet","BLEND_FACE",FACE,{"disambiguationData":[OSD([subQ6,subQ9]),TDD([makeQuery(id+"F42.boolean.opBoolean","COPY",EDGE,{"disambiguationData":[TD([makeQuery(id+"F15.opLoft","SWEPT_FACE",FACE,{"disambiguationData":[OSD([sQuery(id+"F3.wireOp",EDGE,"E20.6.0"),subQ31,subQ30,sQuery(id+"F4.wireOp",EDGE,"E26.6.0"),subQ29,subQ28])]})])],"derivedFrom":subQ11})])]}),makeQuery(id+"F47.opFillet","BLEND_FACE",FACE,{"disambiguationData":[OSD([subQ6,subQ9]),TDD([makeQuery(id+"F42.boolean.opBoolean","COPY",EDGE,{"disambiguationData":[TD([makeQuery(id+"F16.opLoft","SWEPT_FACE",FACE,{"disambiguationData":[OSD([sQuery(id+"F3.wireOp",EDGE,"E20.5.0"),subQ27,subQ26,sQuery(id+"F4.wireOp",EDGE,"E26.5.0"),subQ25,subQ24])]})])],"derivedFrom":subQ11})])]}),makeQuery(id+"F47.opFillet","BLEND_FACE",FACE,{"disambiguationData":[OSD([subQ6,subQ9]),TDD([makeQuery(id+"F42.boolean.opBoolean","COPY",EDGE,{"disambiguationData":[TD([makeQuery(id+"F17.opLoft","SWEPT_FACE",FACE,{"disambiguationData":[OSD([sQuery(id+"F3.wireOp",EDGE,"E20.4.0"),subQ23,subQ22,sQuery(id+"F4.wireOp",EDGE,"E26.4.0"),subQ21,subQ20])]})])],"derivedFrom":subQ11})])]}),makeQuery(id+"F47.opFillet","BLEND_FACE",FACE,{"disambiguationData":[OSD([subQ6,subQ9]),TDD([makeQuery(id+"F42.boolean.opBoolean","COPY",EDGE,{"disambiguationData":[TD([makeQuery(id+"F18.opLoft","SWEPT_FACE",FACE,{"disambiguationData":[OSD([sQuery(id+"F3.wireOp",EDGE,"E20.3.0"),subQ19,subQ18,sQuery(id+"F4.wireOp",EDGE,"E26.3.0"),subQ17,subQ16])]})])],"derivedFrom":subQ11})])]}),makeQuery(id+"F47.opFillet","BLEND_FACE",FACE,{"disambiguationData":[OSD([subQ6,subQ9]),TDD([makeQuery(id+"F42.boolean.opBoolean","COPY",EDGE,{"disambiguationData":[TD([makeQuery(id+"F19.opLoft","SWEPT_FACE",FACE,{"disambiguationData":[OSD([sQuery(id+"F3.wireOp",EDGE,"E20.2.0"),subQ15,subQ14,sQuery(id+"F4.wireOp",EDGE,"E26.2.0"),subQ13,subQ12])]})])],"derivedFrom":subQ11})])]}),makeQuery(id+"F47.opFillet","BLEND_FACE",FACE,{"disambiguationData":[OSD([subQ6,subQ9]),TDD([makeQuery(id+"F42.boolean.opBoolean","COPY",EDGE,{"disambiguationData":[TD([subQ8])],"derivedFrom":subQ11})])]})]});}
            var Q54;
            {var subQ0=makeQuery(id+"F40.opExtrude","CAP_FACE",FACE,{"disambiguationData":[OSD([sQuery(id+"F39.wireOp",EDGE,"E29"),sQuery(id+"F39.wireOp",EDGE,"E30")])],"isStart":false});var subQ1=sQuery(id+"F4.wireOp",EDGE,"E26.1.3");var subQ2=sQuery(id+"F4.wireOp",EDGE,"E26.1.2");var subQ3=sQuery(id+"F3.wireOp",EDGE,"E20.1.3");var subQ4=sQuery(id+"F3.wireOp",EDGE,"E20.1.1");var subQ5=sQuery(id+"F41.wireOp",EDGE,"E35");var subQ6=makeQuery(id+"F42.opRevolve","SWEPT_FACE",FACE,{"disambiguationData":[OSD([subQ5])]});var subQ7=sQuery(id+"F41.wireOp",EDGE,"E36");var subQ8=makeQuery(id+"F42.opRevolve","SWEPT_FACE",FACE,{"disambiguationData":[OSD([subQ7])]});var subQ9=makeQuery(id+"F42.opRevolve","SWEPT_EDGE",EDGE,{"disambiguationData":[OSD([subQ5,subQ7])]});var subQ10=sQuery(id+"F4.wireOp",EDGE,"E26.2.3");var subQ11=sQuery(id+"F4.wireOp",EDGE,"E26.2.2");var subQ12=sQuery(id+"F3.wireOp",EDGE,"E20.2.3");var subQ13=sQuery(id+"F3.wireOp",EDGE,"E20.2.1");var subQ14=sQuery(id+"F4.wireOp",EDGE,"E26.3.3");var subQ15=sQuery(id+"F4.wireOp",EDGE,"E26.3.2");var subQ16=sQuery(id+"F3.wireOp",EDGE,"E20.3.3");var subQ17=sQuery(id+"F3.wireOp",EDGE,"E20.3.1");var subQ18=sQuery(id+"F4.wireOp",EDGE,"E26.4.3");var subQ19=sQuery(id+"F4.wireOp",EDGE,"E26.4.2");var subQ20=sQuery(id+"F3.wireOp",EDGE,"E20.4.3");var subQ21=sQuery(id+"F3.wireOp",EDGE,"E20.4.1");var subQ22=sQuery(id+"F4.wireOp",EDGE,"E26.5.3");var subQ23=sQuery(id+"F4.wireOp",EDGE,"E26.5.2");var subQ24=sQuery(id+"F3.wireOp",EDGE,"E20.5.3");var subQ25=sQuery(id+"F3.wireOp",EDGE,"E20.5.1");var subQ26=sQuery(id+"F4.wireOp",EDGE,"E26.6.3");var subQ27=sQuery(id+"F4.wireOp",EDGE,"E26.6.2");var subQ28=sQuery(id+"F3.wireOp",EDGE,"E20.6.3");var subQ29=sQuery(id+"F3.wireOp",EDGE,"E20.6.1");var subQ30=sQuery(id+"F4.wireOp",EDGE,"E26.7.3");var subQ31=sQuery(id+"F4.wireOp",EDGE,"E26.7.2");var subQ32=sQuery(id+"F3.wireOp",EDGE,"E20.7.3");var subQ33=sQuery(id+"F3.wireOp",EDGE,"E20.7.1");var subQ34=sQuery(id+"F4.wireOp",EDGE,"E26.8.3");var subQ35=sQuery(id+"F4.wireOp",EDGE,"E26.8.2");var subQ36=sQuery(id+"F3.wireOp",EDGE,"E20.8.3");var subQ37=sQuery(id+"F3.wireOp",EDGE,"E20.8.1");var subQ38=sQuery(id+"F4.wireOp",EDGE,"E26.9.3");var subQ39=sQuery(id+"F4.wireOp",EDGE,"E26.9.2");var subQ40=sQuery(id+"F3.wireOp",EDGE,"E20.9.3");var subQ41=sQuery(id+"F3.wireOp",EDGE,"E20.9.1");var subQ42=sQuery(id+"F4.wireOp",EDGE,"E26.10.3");var subQ43=sQuery(id+"F4.wireOp",EDGE,"E26.10.2");var subQ44=sQuery(id+"F3.wireOp",EDGE,"E20.10.3");var subQ45=sQuery(id+"F3.wireOp",EDGE,"E20.10.1");var subQ46=sQuery(id+"F4.wireOp",EDGE,"E26.11.3");var subQ47=sQuery(id+"F4.wireOp",EDGE,"E26.11.2");var subQ48=sQuery(id+"F3.wireOp",EDGE,"E20.11.3");var subQ49=sQuery(id+"F3.wireOp",EDGE,"E20.11.1");var subQ50=sQuery(id+"F4.wireOp",EDGE,"E26.12.3");var subQ51=sQuery(id+"F4.wireOp",EDGE,"E26.12.2");var subQ52=sQuery(id+"F3.wireOp",EDGE,"E20.12.3");var subQ53=sQuery(id+"F3.wireOp",EDGE,"E20.12.1");var subQ54=sQuery(id+"F4.wireOp",EDGE,"E26.13.3");var subQ55=sQuery(id+"F4.wireOp",EDGE,"E26.13.2");var subQ56=sQuery(id+"F3.wireOp",EDGE,"E20.13.3");var subQ57=sQuery(id+"F3.wireOp",EDGE,"E20.13.1");var subQ58=sQuery(id+"F4.wireOp",EDGE,"E26.14.3");var subQ59=sQuery(id+"F4.wireOp",EDGE,"E26.14.2");var subQ60=sQuery(id+"F3.wireOp",EDGE,"E20.14.3");var subQ61=sQuery(id+"F3.wireOp",EDGE,"E20.14.1");var subQ62=sQuery(id+"F4.wireOp",EDGE,"E26.15.3");var subQ63=sQuery(id+"F4.wireOp",EDGE,"E26.15.2");var subQ64=sQuery(id+"F3.wireOp",EDGE,"E20.15.3");var subQ65=sQuery(id+"F3.wireOp",EDGE,"E20.15.1");var subQ66=sQuery(id+"F4.wireOp",EDGE,"E23");var subQ67=sQuery(id+"F4.wireOp",EDGE,"E22");var subQ68=sQuery(id+"F3.wireOp",EDGE,"E18.top");var subQ69=sQuery(id+"F3.wireOp",EDGE,"E18.bottom");var subQ71=makeQuery(id+"F5.opLoft","SWEPT_FACE",FACE,{"disambiguationData":[OSD([subQ69,subQ68,sQuery(id+"F3.wireOp",EDGE,"E18.left"),sQuery(id+"F4.wireOp",EDGE,"E21"),subQ67,subQ66])]});var subQ74=makeQuery(id+"F42.boolean.opBoolean","COPY",FACE,{"disambiguationData":[TD([subQ71])],"derivedFrom":subQ6});var subQ75=makeQuery(id+"F5.boolean.opBoolean","INTERSECT",EDGE,{"derivedFrom":[makeQuery(id+"F1.opRevolve","SWEPT_FACE",FACE,{"disambiguationData":[OSD([sQuery(id+"F0.wireOp",EDGE,"E4")])]}),subQ71]});Q54=makeQuery(id+"F48.opFillet","BLEND_EDGE",EDGE,{"blendedFrom":[makeQuery(id+"F47.opFillet","TWEAK_EDGE",EDGE,{"derivedFrom":[makeQuery(id+"F45.opFillet","BLEND_VERTEX",VERTEX,{"blendedFrom":[subQ75,subQ71,subQ74],"blendedInto":[subQ71,subQ74]}),makeQuery(id+"F45.opFillet","BLEND_VERTEX",VERTEX,{"blendedFrom":[subQ75,makeQuery(id+"F42.boolean.opBoolean","MERGE",FACE,{"derivedFrom":[subQ0,subQ8]}),subQ74],"blendedInto":[makeQuery(id+"F42.boolean.opBoolean","MERGE",FACE,{"derivedFrom":[subQ0,subQ8]}),subQ74]})]}),makeQuery(id+"F47.opFillet","BLEND_FACE",FACE,{"disambiguationData":[OSD([subQ5,subQ7]),TDD([makeQuery(id+"F42.boolean.opBoolean","COPY",EDGE,{"disambiguationData":[TD([subQ71])],"derivedFrom":subQ9})])]}),makeQuery(id+"F47.opFillet","BLEND_FACE",FACE,{"disambiguationData":[OSD([subQ5,subQ7]),TDD([makeQuery(id+"F42.boolean.opBoolean","COPY",EDGE,{"disambiguationData":[TD([makeQuery(id+"F6.opLoft","SWEPT_FACE",FACE,{"disambiguationData":[OSD([sQuery(id+"F3.wireOp",EDGE,"E20.15.0"),subQ65,subQ64,sQuery(id+"F4.wireOp",EDGE,"E26.15.0"),subQ63,subQ62])]})])],"derivedFrom":subQ9})])]}),makeQuery(id+"F47.opFillet","BLEND_FACE",FACE,{"disambiguationData":[OSD([subQ5,subQ7]),TDD([makeQuery(id+"F42.boolean.opBoolean","COPY",EDGE,{"disambiguationData":[TD([makeQuery(id+"F7.opLoft","SWEPT_FACE",FACE,{"disambiguationData":[OSD([sQuery(id+"F3.wireOp",EDGE,"E20.14.0"),subQ61,subQ60,sQuery(id+"F4.wireOp",EDGE,"E26.14.0"),subQ59,subQ58])]})])],"derivedFrom":subQ9})])]}),makeQuery(id+"F47.opFillet","BLEND_FACE",FACE,{"disambiguationData":[OSD([subQ5,subQ7]),TDD([makeQuery(id+"F42.boolean.opBoolean","COPY",EDGE,{"disambiguationData":[TD([makeQuery(id+"F8.opLoft","SWEPT_FACE",FACE,{"disambiguationData":[OSD([sQuery(id+"F3.wireOp",EDGE,"E20.13.0"),subQ57,subQ56,sQuery(id+"F4.wireOp",EDGE,"E26.13.0"),subQ55,subQ54])]})])],"derivedFrom":subQ9})])]}),makeQuery(id+"F47.opFillet","BLEND_FACE",FACE,{"disambiguationData":[OSD([subQ5,subQ7]),TDD([makeQuery(id+"F42.boolean.opBoolean","COPY",EDGE,{"disambiguationData":[TD([makeQuery(id+"F9.opLoft","SWEPT_FACE",FACE,{"disambiguationData":[OSD([sQuery(id+"F3.wireOp",EDGE,"E20.12.0"),subQ53,subQ52,sQuery(id+"F4.wireOp",EDGE,"E26.12.0"),subQ51,subQ50])]})])],"derivedFrom":subQ9})])]}),makeQuery(id+"F47.opFillet","BLEND_FACE",FACE,{"disambiguationData":[OSD([subQ5,subQ7]),TDD([makeQuery(id+"F42.boolean.opBoolean","COPY",EDGE,{"disambiguationData":[TD([makeQuery(id+"F10.opLoft","SWEPT_FACE",FACE,{"disambiguationData":[OSD([sQuery(id+"F3.wireOp",EDGE,"E20.11.0"),subQ49,subQ48,sQuery(id+"F4.wireOp",EDGE,"E26.11.0"),subQ47,subQ46])]})])],"derivedFrom":subQ9})])]}),makeQuery(id+"F47.opFillet","BLEND_FACE",FACE,{"disambiguationData":[OSD([subQ5,subQ7]),TDD([makeQuery(id+"F42.boolean.opBoolean","COPY",EDGE,{"disambiguationData":[TD([makeQuery(id+"F11.opLoft","SWEPT_FACE",FACE,{"disambiguationData":[OSD([sQuery(id+"F3.wireOp",EDGE,"E20.10.0"),subQ45,subQ44,sQuery(id+"F4.wireOp",EDGE,"E26.10.0"),subQ43,subQ42])]})])],"derivedFrom":subQ9})])]}),makeQuery(id+"F47.opFillet","BLEND_FACE",FACE,{"disambiguationData":[OSD([subQ5,subQ7]),TDD([makeQuery(id+"F42.boolean.opBoolean","COPY",EDGE,{"disambiguationData":[TD([makeQuery(id+"F12.opLoft","SWEPT_FACE",FACE,{"disambiguationData":[OSD([sQuery(id+"F3.wireOp",EDGE,"E20.9.0"),subQ41,subQ40,sQuery(id+"F4.wireOp",EDGE,"E26.9.0"),subQ39,subQ38])]})])],"derivedFrom":subQ9})])]}),makeQuery(id+"F47.opFillet","BLEND_FACE",FACE,{"disambiguationData":[OSD([subQ5,subQ7]),TDD([makeQuery(id+"F42.boolean.opBoolean","COPY",EDGE,{"disambiguationData":[TD([makeQuery(id+"F13.opLoft","SWEPT_FACE",FACE,{"disambiguationData":[OSD([sQuery(id+"F3.wireOp",EDGE,"E20.8.0"),subQ37,subQ36,sQuery(id+"F4.wireOp",EDGE,"E26.8.0"),subQ35,subQ34])]})])],"derivedFrom":subQ9})])]}),makeQuery(id+"F47.opFillet","BLEND_FACE",FACE,{"disambiguationData":[OSD([subQ5,subQ7]),TDD([makeQuery(id+"F42.boolean.opBoolean","COPY",EDGE,{"disambiguationData":[TD([makeQuery(id+"F14.opLoft","SWEPT_FACE",FACE,{"disambiguationData":[OSD([sQuery(id+"F3.wireOp",EDGE,"E20.7.0"),subQ33,subQ32,sQuery(id+"F4.wireOp",EDGE,"E26.7.0"),subQ31,subQ30])]})])],"derivedFrom":subQ9})])]}),makeQuery(id+"F47.opFillet","BLEND_FACE",FACE,{"disambiguationData":[OSD([subQ5,subQ7]),TDD([makeQuery(id+"F42.boolean.opBoolean","COPY",EDGE,{"disambiguationData":[TD([makeQuery(id+"F15.opLoft","SWEPT_FACE",FACE,{"disambiguationData":[OSD([sQuery(id+"F3.wireOp",EDGE,"E20.6.0"),subQ29,subQ28,sQuery(id+"F4.wireOp",EDGE,"E26.6.0"),subQ27,subQ26])]})])],"derivedFrom":subQ9})])]}),makeQuery(id+"F47.opFillet","BLEND_FACE",FACE,{"disambiguationData":[OSD([subQ5,subQ7]),TDD([makeQuery(id+"F42.boolean.opBoolean","COPY",EDGE,{"disambiguationData":[TD([makeQuery(id+"F16.opLoft","SWEPT_FACE",FACE,{"disambiguationData":[OSD([sQuery(id+"F3.wireOp",EDGE,"E20.5.0"),subQ25,subQ24,sQuery(id+"F4.wireOp",EDGE,"E26.5.0"),subQ23,subQ22])]})])],"derivedFrom":subQ9})])]}),makeQuery(id+"F47.opFillet","BLEND_FACE",FACE,{"disambiguationData":[OSD([subQ5,subQ7]),TDD([makeQuery(id+"F42.boolean.opBoolean","COPY",EDGE,{"disambiguationData":[TD([makeQuery(id+"F17.opLoft","SWEPT_FACE",FACE,{"disambiguationData":[OSD([sQuery(id+"F3.wireOp",EDGE,"E20.4.0"),subQ21,subQ20,sQuery(id+"F4.wireOp",EDGE,"E26.4.0"),subQ19,subQ18])]})])],"derivedFrom":subQ9})])]}),makeQuery(id+"F47.opFillet","BLEND_FACE",FACE,{"disambiguationData":[OSD([subQ5,subQ7]),TDD([makeQuery(id+"F42.boolean.opBoolean","COPY",EDGE,{"disambiguationData":[TD([makeQuery(id+"F18.opLoft","SWEPT_FACE",FACE,{"disambiguationData":[OSD([sQuery(id+"F3.wireOp",EDGE,"E20.3.0"),subQ17,subQ16,sQuery(id+"F4.wireOp",EDGE,"E26.3.0"),subQ15,subQ14])]})])],"derivedFrom":subQ9})])]}),makeQuery(id+"F47.opFillet","BLEND_FACE",FACE,{"disambiguationData":[OSD([subQ5,subQ7]),TDD([makeQuery(id+"F42.boolean.opBoolean","COPY",EDGE,{"disambiguationData":[TD([makeQuery(id+"F19.opLoft","SWEPT_FACE",FACE,{"disambiguationData":[OSD([sQuery(id+"F3.wireOp",EDGE,"E20.2.0"),subQ13,subQ12,sQuery(id+"F4.wireOp",EDGE,"E26.2.0"),subQ11,subQ10])]})])],"derivedFrom":subQ9})])]}),makeQuery(id+"F47.opFillet","BLEND_FACE",FACE,{"disambiguationData":[OSD([subQ5,subQ7]),TDD([makeQuery(id+"F42.boolean.opBoolean","COPY",EDGE,{"disambiguationData":[TD([makeQuery(id+"F20.opLoft","SWEPT_FACE",FACE,{"disambiguationData":[OSD([sQuery(id+"F3.wireOp",EDGE,"E20.1.0"),subQ4,subQ3,sQuery(id+"F4.wireOp",EDGE,"E26.1.0"),subQ2,subQ1])]})])],"derivedFrom":subQ9})])]})],"blendedInto":[makeQuery(id+"F47.opFillet","BLEND_FACE",FACE,{"disambiguationData":[OSD([subQ5,subQ7]),TDD([makeQuery(id+"F42.boolean.opBoolean","COPY",EDGE,{"disambiguationData":[TD([subQ71])],"derivedFrom":subQ9})])]}),makeQuery(id+"F47.opFillet","BLEND_FACE",FACE,{"disambiguationData":[OSD([subQ5,subQ7]),TDD([makeQuery(id+"F42.boolean.opBoolean","COPY",EDGE,{"disambiguationData":[TD([makeQuery(id+"F6.opLoft","SWEPT_FACE",FACE,{"disambiguationData":[OSD([sQuery(id+"F3.wireOp",EDGE,"E20.15.0"),subQ65,subQ64,sQuery(id+"F4.wireOp",EDGE,"E26.15.0"),subQ63,subQ62])]})])],"derivedFrom":subQ9})])]}),makeQuery(id+"F47.opFillet","BLEND_FACE",FACE,{"disambiguationData":[OSD([subQ5,subQ7]),TDD([makeQuery(id+"F42.boolean.opBoolean","COPY",EDGE,{"disambiguationData":[TD([makeQuery(id+"F7.opLoft","SWEPT_FACE",FACE,{"disambiguationData":[OSD([sQuery(id+"F3.wireOp",EDGE,"E20.14.0"),subQ61,subQ60,sQuery(id+"F4.wireOp",EDGE,"E26.14.0"),subQ59,subQ58])]})])],"derivedFrom":subQ9})])]}),makeQuery(id+"F47.opFillet","BLEND_FACE",FACE,{"disambiguationData":[OSD([subQ5,subQ7]),TDD([makeQuery(id+"F42.boolean.opBoolean","COPY",EDGE,{"disambiguationData":[TD([makeQuery(id+"F8.opLoft","SWEPT_FACE",FACE,{"disambiguationData":[OSD([sQuery(id+"F3.wireOp",EDGE,"E20.13.0"),subQ57,subQ56,sQuery(id+"F4.wireOp",EDGE,"E26.13.0"),subQ55,subQ54])]})])],"derivedFrom":subQ9})])]}),makeQuery(id+"F47.opFillet","BLEND_FACE",FACE,{"disambiguationData":[OSD([subQ5,subQ7]),TDD([makeQuery(id+"F42.boolean.opBoolean","COPY",EDGE,{"disambiguationData":[TD([makeQuery(id+"F9.opLoft","SWEPT_FACE",FACE,{"disambiguationData":[OSD([sQuery(id+"F3.wireOp",EDGE,"E20.12.0"),subQ53,subQ52,sQuery(id+"F4.wireOp",EDGE,"E26.12.0"),subQ51,subQ50])]})])],"derivedFrom":subQ9})])]}),makeQuery(id+"F47.opFillet","BLEND_FACE",FACE,{"disambiguationData":[OSD([subQ5,subQ7]),TDD([makeQuery(id+"F42.boolean.opBoolean","COPY",EDGE,{"disambiguationData":[TD([makeQuery(id+"F10.opLoft","SWEPT_FACE",FACE,{"disambiguationData":[OSD([sQuery(id+"F3.wireOp",EDGE,"E20.11.0"),subQ49,subQ48,sQuery(id+"F4.wireOp",EDGE,"E26.11.0"),subQ47,subQ46])]})])],"derivedFrom":subQ9})])]}),makeQuery(id+"F47.opFillet","BLEND_FACE",FACE,{"disambiguationData":[OSD([subQ5,subQ7]),TDD([makeQuery(id+"F42.boolean.opBoolean","COPY",EDGE,{"disambiguationData":[TD([makeQuery(id+"F11.opLoft","SWEPT_FACE",FACE,{"disambiguationData":[OSD([sQuery(id+"F3.wireOp",EDGE,"E20.10.0"),subQ45,subQ44,sQuery(id+"F4.wireOp",EDGE,"E26.10.0"),subQ43,subQ42])]})])],"derivedFrom":subQ9})])]}),makeQuery(id+"F47.opFillet","BLEND_FACE",FACE,{"disambiguationData":[OSD([subQ5,subQ7]),TDD([makeQuery(id+"F42.boolean.opBoolean","COPY",EDGE,{"disambiguationData":[TD([makeQuery(id+"F12.opLoft","SWEPT_FACE",FACE,{"disambiguationData":[OSD([sQuery(id+"F3.wireOp",EDGE,"E20.9.0"),subQ41,subQ40,sQuery(id+"F4.wireOp",EDGE,"E26.9.0"),subQ39,subQ38])]})])],"derivedFrom":subQ9})])]}),makeQuery(id+"F47.opFillet","BLEND_FACE",FACE,{"disambiguationData":[OSD([subQ5,subQ7]),TDD([makeQuery(id+"F42.boolean.opBoolean","COPY",EDGE,{"disambiguationData":[TD([makeQuery(id+"F13.opLoft","SWEPT_FACE",FACE,{"disambiguationData":[OSD([sQuery(id+"F3.wireOp",EDGE,"E20.8.0"),subQ37,subQ36,sQuery(id+"F4.wireOp",EDGE,"E26.8.0"),subQ35,subQ34])]})])],"derivedFrom":subQ9})])]}),makeQuery(id+"F47.opFillet","BLEND_FACE",FACE,{"disambiguationData":[OSD([subQ5,subQ7]),TDD([makeQuery(id+"F42.boolean.opBoolean","COPY",EDGE,{"disambiguationData":[TD([makeQuery(id+"F14.opLoft","SWEPT_FACE",FACE,{"disambiguationData":[OSD([sQuery(id+"F3.wireOp",EDGE,"E20.7.0"),subQ33,subQ32,sQuery(id+"F4.wireOp",EDGE,"E26.7.0"),subQ31,subQ30])]})])],"derivedFrom":subQ9})])]}),makeQuery(id+"F47.opFillet","BLEND_FACE",FACE,{"disambiguationData":[OSD([subQ5,subQ7]),TDD([makeQuery(id+"F42.boolean.opBoolean","COPY",EDGE,{"disambiguationData":[TD([makeQuery(id+"F15.opLoft","SWEPT_FACE",FACE,{"disambiguationData":[OSD([sQuery(id+"F3.wireOp",EDGE,"E20.6.0"),subQ29,subQ28,sQuery(id+"F4.wireOp",EDGE,"E26.6.0"),subQ27,subQ26])]})])],"derivedFrom":subQ9})])]}),makeQuery(id+"F47.opFillet","BLEND_FACE",FACE,{"disambiguationData":[OSD([subQ5,subQ7]),TDD([makeQuery(id+"F42.boolean.opBoolean","COPY",EDGE,{"disambiguationData":[TD([makeQuery(id+"F16.opLoft","SWEPT_FACE",FACE,{"disambiguationData":[OSD([sQuery(id+"F3.wireOp",EDGE,"E20.5.0"),subQ25,subQ24,sQuery(id+"F4.wireOp",EDGE,"E26.5.0"),subQ23,subQ22])]})])],"derivedFrom":subQ9})])]}),makeQuery(id+"F47.opFillet","BLEND_FACE",FACE,{"disambiguationData":[OSD([subQ5,subQ7]),TDD([makeQuery(id+"F42.boolean.opBoolean","COPY",EDGE,{"disambiguationData":[TD([makeQuery(id+"F17.opLoft","SWEPT_FACE",FACE,{"disambiguationData":[OSD([sQuery(id+"F3.wireOp",EDGE,"E20.4.0"),subQ21,subQ20,sQuery(id+"F4.wireOp",EDGE,"E26.4.0"),subQ19,subQ18])]})])],"derivedFrom":subQ9})])]}),makeQuery(id+"F47.opFillet","BLEND_FACE",FACE,{"disambiguationData":[OSD([subQ5,subQ7]),TDD([makeQuery(id+"F42.boolean.opBoolean","COPY",EDGE,{"disambiguationData":[TD([makeQuery(id+"F18.opLoft","SWEPT_FACE",FACE,{"disambiguationData":[OSD([sQuery(id+"F3.wireOp",EDGE,"E20.3.0"),subQ17,subQ16,sQuery(id+"F4.wireOp",EDGE,"E26.3.0"),subQ15,subQ14])]})])],"derivedFrom":subQ9})])]}),makeQuery(id+"F47.opFillet","BLEND_FACE",FACE,{"disambiguationData":[OSD([subQ5,subQ7]),TDD([makeQuery(id+"F42.boolean.opBoolean","COPY",EDGE,{"disambiguationData":[TD([makeQuery(id+"F19.opLoft","SWEPT_FACE",FACE,{"disambiguationData":[OSD([sQuery(id+"F3.wireOp",EDGE,"E20.2.0"),subQ13,subQ12,sQuery(id+"F4.wireOp",EDGE,"E26.2.0"),subQ11,subQ10])]})])],"derivedFrom":subQ9})])]}),makeQuery(id+"F47.opFillet","BLEND_FACE",FACE,{"disambiguationData":[OSD([subQ5,subQ7]),TDD([makeQuery(id+"F42.boolean.opBoolean","COPY",EDGE,{"disambiguationData":[TD([makeQuery(id+"F20.opLoft","SWEPT_FACE",FACE,{"disambiguationData":[OSD([sQuery(id+"F3.wireOp",EDGE,"E20.1.0"),subQ4,subQ3,sQuery(id+"F4.wireOp",EDGE,"E26.1.0"),subQ2,subQ1])]})])],"derivedFrom":subQ9})])]})]});}
            var Q55;
            {var subQ0=makeQuery(id+"F40.opExtrude","CAP_FACE",FACE,{"disambiguationData":[OSD([sQuery(id+"F39.wireOp",EDGE,"E29"),sQuery(id+"F39.wireOp",EDGE,"E30")])],"isStart":false});var subQ1=sQuery(id+"F4.wireOp",EDGE,"E26.1.3");var subQ2=sQuery(id+"F4.wireOp",EDGE,"E26.1.2");var subQ3=sQuery(id+"F3.wireOp",EDGE,"E20.1.3");var subQ4=sQuery(id+"F3.wireOp",EDGE,"E20.1.1");var subQ5=sQuery(id+"F41.wireOp",EDGE,"E35");var subQ6=makeQuery(id+"F42.opRevolve","SWEPT_FACE",FACE,{"disambiguationData":[OSD([subQ5])]});var subQ7=sQuery(id+"F41.wireOp",EDGE,"E36");var subQ8=makeQuery(id+"F42.opRevolve","SWEPT_FACE",FACE,{"disambiguationData":[OSD([subQ7])]});var subQ9=makeQuery(id+"F42.opRevolve","SWEPT_EDGE",EDGE,{"disambiguationData":[OSD([subQ5,subQ7])]});var subQ10=sQuery(id+"F4.wireOp",EDGE,"E26.2.3");var subQ11=sQuery(id+"F4.wireOp",EDGE,"E26.2.2");var subQ12=sQuery(id+"F3.wireOp",EDGE,"E20.2.3");var subQ13=sQuery(id+"F3.wireOp",EDGE,"E20.2.1");var subQ14=sQuery(id+"F4.wireOp",EDGE,"E26.3.3");var subQ15=sQuery(id+"F4.wireOp",EDGE,"E26.3.2");var subQ16=sQuery(id+"F3.wireOp",EDGE,"E20.3.3");var subQ17=sQuery(id+"F3.wireOp",EDGE,"E20.3.1");var subQ18=sQuery(id+"F4.wireOp",EDGE,"E26.4.3");var subQ19=sQuery(id+"F4.wireOp",EDGE,"E26.4.2");var subQ20=sQuery(id+"F3.wireOp",EDGE,"E20.4.3");var subQ21=sQuery(id+"F3.wireOp",EDGE,"E20.4.1");var subQ22=sQuery(id+"F4.wireOp",EDGE,"E26.5.3");var subQ23=sQuery(id+"F4.wireOp",EDGE,"E26.5.2");var subQ24=sQuery(id+"F3.wireOp",EDGE,"E20.5.3");var subQ25=sQuery(id+"F3.wireOp",EDGE,"E20.5.1");var subQ26=sQuery(id+"F4.wireOp",EDGE,"E26.6.3");var subQ27=sQuery(id+"F4.wireOp",EDGE,"E26.6.2");var subQ28=sQuery(id+"F3.wireOp",EDGE,"E20.6.3");var subQ29=sQuery(id+"F3.wireOp",EDGE,"E20.6.1");var subQ30=sQuery(id+"F4.wireOp",EDGE,"E26.7.3");var subQ31=sQuery(id+"F4.wireOp",EDGE,"E26.7.2");var subQ32=sQuery(id+"F3.wireOp",EDGE,"E20.7.3");var subQ33=sQuery(id+"F3.wireOp",EDGE,"E20.7.1");var subQ34=sQuery(id+"F4.wireOp",EDGE,"E26.8.3");var subQ35=sQuery(id+"F4.wireOp",EDGE,"E26.8.2");var subQ36=sQuery(id+"F3.wireOp",EDGE,"E20.8.3");var subQ37=sQuery(id+"F3.wireOp",EDGE,"E20.8.1");var subQ38=sQuery(id+"F4.wireOp",EDGE,"E26.9.3");var subQ39=sQuery(id+"F4.wireOp",EDGE,"E26.9.2");var subQ40=sQuery(id+"F3.wireOp",EDGE,"E20.9.3");var subQ41=sQuery(id+"F3.wireOp",EDGE,"E20.9.1");var subQ42=sQuery(id+"F4.wireOp",EDGE,"E26.10.3");var subQ43=sQuery(id+"F4.wireOp",EDGE,"E26.10.2");var subQ44=sQuery(id+"F3.wireOp",EDGE,"E20.10.3");var subQ45=sQuery(id+"F3.wireOp",EDGE,"E20.10.1");var subQ46=sQuery(id+"F4.wireOp",EDGE,"E26.11.3");var subQ47=sQuery(id+"F4.wireOp",EDGE,"E26.11.2");var subQ48=sQuery(id+"F3.wireOp",EDGE,"E20.11.3");var subQ49=sQuery(id+"F3.wireOp",EDGE,"E20.11.1");var subQ50=sQuery(id+"F4.wireOp",EDGE,"E26.12.3");var subQ51=sQuery(id+"F4.wireOp",EDGE,"E26.12.2");var subQ52=sQuery(id+"F3.wireOp",EDGE,"E20.12.3");var subQ53=sQuery(id+"F3.wireOp",EDGE,"E20.12.1");var subQ54=sQuery(id+"F4.wireOp",EDGE,"E26.13.3");var subQ55=sQuery(id+"F4.wireOp",EDGE,"E26.13.2");var subQ56=sQuery(id+"F3.wireOp",EDGE,"E20.13.3");var subQ57=sQuery(id+"F3.wireOp",EDGE,"E20.13.1");var subQ58=sQuery(id+"F4.wireOp",EDGE,"E26.14.3");var subQ59=sQuery(id+"F4.wireOp",EDGE,"E26.14.2");var subQ60=sQuery(id+"F3.wireOp",EDGE,"E20.14.3");var subQ61=sQuery(id+"F3.wireOp",EDGE,"E20.14.1");var subQ62=sQuery(id+"F4.wireOp",EDGE,"E26.15.3");var subQ63=sQuery(id+"F4.wireOp",EDGE,"E26.15.2");var subQ64=sQuery(id+"F3.wireOp",EDGE,"E20.15.3");var subQ65=sQuery(id+"F3.wireOp",EDGE,"E20.15.1");var subQ67=makeQuery(id+"F6.opLoft","SWEPT_FACE",FACE,{"disambiguationData":[OSD([sQuery(id+"F3.wireOp",EDGE,"E20.15.0"),subQ65,subQ64,sQuery(id+"F4.wireOp",EDGE,"E26.15.0"),subQ63,subQ62])]});var subQ68=sQuery(id+"F4.wireOp",EDGE,"E23");var subQ69=sQuery(id+"F4.wireOp",EDGE,"E22");var subQ70=sQuery(id+"F3.wireOp",EDGE,"E18.top");var subQ71=sQuery(id+"F3.wireOp",EDGE,"E18.bottom");var subQ74=makeQuery(id+"F42.boolean.opBoolean","COPY",FACE,{"disambiguationData":[TD([subQ67])],"derivedFrom":subQ6});var subQ75=makeQuery(id+"F6.boolean.opBoolean","INTERSECT",EDGE,{"derivedFrom":[makeQuery(id+"F1.opRevolve","SWEPT_FACE",FACE,{"disambiguationData":[OSD([sQuery(id+"F0.wireOp",EDGE,"E4")])]}),subQ67]});Q55=makeQuery(id+"F48.opFillet","BLEND_EDGE",EDGE,{"blendedFrom":[makeQuery(id+"F47.opFillet","TWEAK_EDGE",EDGE,{"derivedFrom":[makeQuery(id+"F45.opFillet","BLEND_VERTEX",VERTEX,{"blendedFrom":[subQ75,subQ67,subQ74],"blendedInto":[subQ67,subQ74]}),makeQuery(id+"F45.opFillet","BLEND_VERTEX",VERTEX,{"blendedFrom":[subQ75,makeQuery(id+"F42.boolean.opBoolean","MERGE",FACE,{"derivedFrom":[subQ0,subQ8]}),subQ74],"blendedInto":[makeQuery(id+"F42.boolean.opBoolean","MERGE",FACE,{"derivedFrom":[subQ0,subQ8]}),subQ74]})]}),makeQuery(id+"F47.opFillet","BLEND_FACE",FACE,{"disambiguationData":[OSD([subQ5,subQ7]),TDD([makeQuery(id+"F42.boolean.opBoolean","COPY",EDGE,{"disambiguationData":[TD([makeQuery(id+"F5.opLoft","SWEPT_FACE",FACE,{"disambiguationData":[OSD([subQ71,subQ70,sQuery(id+"F3.wireOp",EDGE,"E18.left"),sQuery(id+"F4.wireOp",EDGE,"E21"),subQ69,subQ68])]})])],"derivedFrom":subQ9})])]}),makeQuery(id+"F47.opFillet","BLEND_FACE",FACE,{"disambiguationData":[OSD([subQ5,subQ7]),TDD([makeQuery(id+"F42.boolean.opBoolean","COPY",EDGE,{"disambiguationData":[TD([subQ67])],"derivedFrom":subQ9})])]}),makeQuery(id+"F47.opFillet","BLEND_FACE",FACE,{"disambiguationData":[OSD([subQ5,subQ7]),TDD([makeQuery(id+"F42.boolean.opBoolean","COPY",EDGE,{"disambiguationData":[TD([makeQuery(id+"F7.opLoft","SWEPT_FACE",FACE,{"disambiguationData":[OSD([sQuery(id+"F3.wireOp",EDGE,"E20.14.0"),subQ61,subQ60,sQuery(id+"F4.wireOp",EDGE,"E26.14.0"),subQ59,subQ58])]})])],"derivedFrom":subQ9})])]}),makeQuery(id+"F47.opFillet","BLEND_FACE",FACE,{"disambiguationData":[OSD([subQ5,subQ7]),TDD([makeQuery(id+"F42.boolean.opBoolean","COPY",EDGE,{"disambiguationData":[TD([makeQuery(id+"F8.opLoft","SWEPT_FACE",FACE,{"disambiguationData":[OSD([sQuery(id+"F3.wireOp",EDGE,"E20.13.0"),subQ57,subQ56,sQuery(id+"F4.wireOp",EDGE,"E26.13.0"),subQ55,subQ54])]})])],"derivedFrom":subQ9})])]}),makeQuery(id+"F47.opFillet","BLEND_FACE",FACE,{"disambiguationData":[OSD([subQ5,subQ7]),TDD([makeQuery(id+"F42.boolean.opBoolean","COPY",EDGE,{"disambiguationData":[TD([makeQuery(id+"F9.opLoft","SWEPT_FACE",FACE,{"disambiguationData":[OSD([sQuery(id+"F3.wireOp",EDGE,"E20.12.0"),subQ53,subQ52,sQuery(id+"F4.wireOp",EDGE,"E26.12.0"),subQ51,subQ50])]})])],"derivedFrom":subQ9})])]}),makeQuery(id+"F47.opFillet","BLEND_FACE",FACE,{"disambiguationData":[OSD([subQ5,subQ7]),TDD([makeQuery(id+"F42.boolean.opBoolean","COPY",EDGE,{"disambiguationData":[TD([makeQuery(id+"F10.opLoft","SWEPT_FACE",FACE,{"disambiguationData":[OSD([sQuery(id+"F3.wireOp",EDGE,"E20.11.0"),subQ49,subQ48,sQuery(id+"F4.wireOp",EDGE,"E26.11.0"),subQ47,subQ46])]})])],"derivedFrom":subQ9})])]}),makeQuery(id+"F47.opFillet","BLEND_FACE",FACE,{"disambiguationData":[OSD([subQ5,subQ7]),TDD([makeQuery(id+"F42.boolean.opBoolean","COPY",EDGE,{"disambiguationData":[TD([makeQuery(id+"F11.opLoft","SWEPT_FACE",FACE,{"disambiguationData":[OSD([sQuery(id+"F3.wireOp",EDGE,"E20.10.0"),subQ45,subQ44,sQuery(id+"F4.wireOp",EDGE,"E26.10.0"),subQ43,subQ42])]})])],"derivedFrom":subQ9})])]}),makeQuery(id+"F47.opFillet","BLEND_FACE",FACE,{"disambiguationData":[OSD([subQ5,subQ7]),TDD([makeQuery(id+"F42.boolean.opBoolean","COPY",EDGE,{"disambiguationData":[TD([makeQuery(id+"F12.opLoft","SWEPT_FACE",FACE,{"disambiguationData":[OSD([sQuery(id+"F3.wireOp",EDGE,"E20.9.0"),subQ41,subQ40,sQuery(id+"F4.wireOp",EDGE,"E26.9.0"),subQ39,subQ38])]})])],"derivedFrom":subQ9})])]}),makeQuery(id+"F47.opFillet","BLEND_FACE",FACE,{"disambiguationData":[OSD([subQ5,subQ7]),TDD([makeQuery(id+"F42.boolean.opBoolean","COPY",EDGE,{"disambiguationData":[TD([makeQuery(id+"F13.opLoft","SWEPT_FACE",FACE,{"disambiguationData":[OSD([sQuery(id+"F3.wireOp",EDGE,"E20.8.0"),subQ37,subQ36,sQuery(id+"F4.wireOp",EDGE,"E26.8.0"),subQ35,subQ34])]})])],"derivedFrom":subQ9})])]}),makeQuery(id+"F47.opFillet","BLEND_FACE",FACE,{"disambiguationData":[OSD([subQ5,subQ7]),TDD([makeQuery(id+"F42.boolean.opBoolean","COPY",EDGE,{"disambiguationData":[TD([makeQuery(id+"F14.opLoft","SWEPT_FACE",FACE,{"disambiguationData":[OSD([sQuery(id+"F3.wireOp",EDGE,"E20.7.0"),subQ33,subQ32,sQuery(id+"F4.wireOp",EDGE,"E26.7.0"),subQ31,subQ30])]})])],"derivedFrom":subQ9})])]}),makeQuery(id+"F47.opFillet","BLEND_FACE",FACE,{"disambiguationData":[OSD([subQ5,subQ7]),TDD([makeQuery(id+"F42.boolean.opBoolean","COPY",EDGE,{"disambiguationData":[TD([makeQuery(id+"F15.opLoft","SWEPT_FACE",FACE,{"disambiguationData":[OSD([sQuery(id+"F3.wireOp",EDGE,"E20.6.0"),subQ29,subQ28,sQuery(id+"F4.wireOp",EDGE,"E26.6.0"),subQ27,subQ26])]})])],"derivedFrom":subQ9})])]}),makeQuery(id+"F47.opFillet","BLEND_FACE",FACE,{"disambiguationData":[OSD([subQ5,subQ7]),TDD([makeQuery(id+"F42.boolean.opBoolean","COPY",EDGE,{"disambiguationData":[TD([makeQuery(id+"F16.opLoft","SWEPT_FACE",FACE,{"disambiguationData":[OSD([sQuery(id+"F3.wireOp",EDGE,"E20.5.0"),subQ25,subQ24,sQuery(id+"F4.wireOp",EDGE,"E26.5.0"),subQ23,subQ22])]})])],"derivedFrom":subQ9})])]}),makeQuery(id+"F47.opFillet","BLEND_FACE",FACE,{"disambiguationData":[OSD([subQ5,subQ7]),TDD([makeQuery(id+"F42.boolean.opBoolean","COPY",EDGE,{"disambiguationData":[TD([makeQuery(id+"F17.opLoft","SWEPT_FACE",FACE,{"disambiguationData":[OSD([sQuery(id+"F3.wireOp",EDGE,"E20.4.0"),subQ21,subQ20,sQuery(id+"F4.wireOp",EDGE,"E26.4.0"),subQ19,subQ18])]})])],"derivedFrom":subQ9})])]}),makeQuery(id+"F47.opFillet","BLEND_FACE",FACE,{"disambiguationData":[OSD([subQ5,subQ7]),TDD([makeQuery(id+"F42.boolean.opBoolean","COPY",EDGE,{"disambiguationData":[TD([makeQuery(id+"F18.opLoft","SWEPT_FACE",FACE,{"disambiguationData":[OSD([sQuery(id+"F3.wireOp",EDGE,"E20.3.0"),subQ17,subQ16,sQuery(id+"F4.wireOp",EDGE,"E26.3.0"),subQ15,subQ14])]})])],"derivedFrom":subQ9})])]}),makeQuery(id+"F47.opFillet","BLEND_FACE",FACE,{"disambiguationData":[OSD([subQ5,subQ7]),TDD([makeQuery(id+"F42.boolean.opBoolean","COPY",EDGE,{"disambiguationData":[TD([makeQuery(id+"F19.opLoft","SWEPT_FACE",FACE,{"disambiguationData":[OSD([sQuery(id+"F3.wireOp",EDGE,"E20.2.0"),subQ13,subQ12,sQuery(id+"F4.wireOp",EDGE,"E26.2.0"),subQ11,subQ10])]})])],"derivedFrom":subQ9})])]}),makeQuery(id+"F47.opFillet","BLEND_FACE",FACE,{"disambiguationData":[OSD([subQ5,subQ7]),TDD([makeQuery(id+"F42.boolean.opBoolean","COPY",EDGE,{"disambiguationData":[TD([makeQuery(id+"F20.opLoft","SWEPT_FACE",FACE,{"disambiguationData":[OSD([sQuery(id+"F3.wireOp",EDGE,"E20.1.0"),subQ4,subQ3,sQuery(id+"F4.wireOp",EDGE,"E26.1.0"),subQ2,subQ1])]})])],"derivedFrom":subQ9})])]})],"blendedInto":[makeQuery(id+"F47.opFillet","BLEND_FACE",FACE,{"disambiguationData":[OSD([subQ5,subQ7]),TDD([makeQuery(id+"F42.boolean.opBoolean","COPY",EDGE,{"disambiguationData":[TD([makeQuery(id+"F5.opLoft","SWEPT_FACE",FACE,{"disambiguationData":[OSD([subQ71,subQ70,sQuery(id+"F3.wireOp",EDGE,"E18.left"),sQuery(id+"F4.wireOp",EDGE,"E21"),subQ69,subQ68])]})])],"derivedFrom":subQ9})])]}),makeQuery(id+"F47.opFillet","BLEND_FACE",FACE,{"disambiguationData":[OSD([subQ5,subQ7]),TDD([makeQuery(id+"F42.boolean.opBoolean","COPY",EDGE,{"disambiguationData":[TD([subQ67])],"derivedFrom":subQ9})])]}),makeQuery(id+"F47.opFillet","BLEND_FACE",FACE,{"disambiguationData":[OSD([subQ5,subQ7]),TDD([makeQuery(id+"F42.boolean.opBoolean","COPY",EDGE,{"disambiguationData":[TD([makeQuery(id+"F7.opLoft","SWEPT_FACE",FACE,{"disambiguationData":[OSD([sQuery(id+"F3.wireOp",EDGE,"E20.14.0"),subQ61,subQ60,sQuery(id+"F4.wireOp",EDGE,"E26.14.0"),subQ59,subQ58])]})])],"derivedFrom":subQ9})])]}),makeQuery(id+"F47.opFillet","BLEND_FACE",FACE,{"disambiguationData":[OSD([subQ5,subQ7]),TDD([makeQuery(id+"F42.boolean.opBoolean","COPY",EDGE,{"disambiguationData":[TD([makeQuery(id+"F8.opLoft","SWEPT_FACE",FACE,{"disambiguationData":[OSD([sQuery(id+"F3.wireOp",EDGE,"E20.13.0"),subQ57,subQ56,sQuery(id+"F4.wireOp",EDGE,"E26.13.0"),subQ55,subQ54])]})])],"derivedFrom":subQ9})])]}),makeQuery(id+"F47.opFillet","BLEND_FACE",FACE,{"disambiguationData":[OSD([subQ5,subQ7]),TDD([makeQuery(id+"F42.boolean.opBoolean","COPY",EDGE,{"disambiguationData":[TD([makeQuery(id+"F9.opLoft","SWEPT_FACE",FACE,{"disambiguationData":[OSD([sQuery(id+"F3.wireOp",EDGE,"E20.12.0"),subQ53,subQ52,sQuery(id+"F4.wireOp",EDGE,"E26.12.0"),subQ51,subQ50])]})])],"derivedFrom":subQ9})])]}),makeQuery(id+"F47.opFillet","BLEND_FACE",FACE,{"disambiguationData":[OSD([subQ5,subQ7]),TDD([makeQuery(id+"F42.boolean.opBoolean","COPY",EDGE,{"disambiguationData":[TD([makeQuery(id+"F10.opLoft","SWEPT_FACE",FACE,{"disambiguationData":[OSD([sQuery(id+"F3.wireOp",EDGE,"E20.11.0"),subQ49,subQ48,sQuery(id+"F4.wireOp",EDGE,"E26.11.0"),subQ47,subQ46])]})])],"derivedFrom":subQ9})])]}),makeQuery(id+"F47.opFillet","BLEND_FACE",FACE,{"disambiguationData":[OSD([subQ5,subQ7]),TDD([makeQuery(id+"F42.boolean.opBoolean","COPY",EDGE,{"disambiguationData":[TD([makeQuery(id+"F11.opLoft","SWEPT_FACE",FACE,{"disambiguationData":[OSD([sQuery(id+"F3.wireOp",EDGE,"E20.10.0"),subQ45,subQ44,sQuery(id+"F4.wireOp",EDGE,"E26.10.0"),subQ43,subQ42])]})])],"derivedFrom":subQ9})])]}),makeQuery(id+"F47.opFillet","BLEND_FACE",FACE,{"disambiguationData":[OSD([subQ5,subQ7]),TDD([makeQuery(id+"F42.boolean.opBoolean","COPY",EDGE,{"disambiguationData":[TD([makeQuery(id+"F12.opLoft","SWEPT_FACE",FACE,{"disambiguationData":[OSD([sQuery(id+"F3.wireOp",EDGE,"E20.9.0"),subQ41,subQ40,sQuery(id+"F4.wireOp",EDGE,"E26.9.0"),subQ39,subQ38])]})])],"derivedFrom":subQ9})])]}),makeQuery(id+"F47.opFillet","BLEND_FACE",FACE,{"disambiguationData":[OSD([subQ5,subQ7]),TDD([makeQuery(id+"F42.boolean.opBoolean","COPY",EDGE,{"disambiguationData":[TD([makeQuery(id+"F13.opLoft","SWEPT_FACE",FACE,{"disambiguationData":[OSD([sQuery(id+"F3.wireOp",EDGE,"E20.8.0"),subQ37,subQ36,sQuery(id+"F4.wireOp",EDGE,"E26.8.0"),subQ35,subQ34])]})])],"derivedFrom":subQ9})])]}),makeQuery(id+"F47.opFillet","BLEND_FACE",FACE,{"disambiguationData":[OSD([subQ5,subQ7]),TDD([makeQuery(id+"F42.boolean.opBoolean","COPY",EDGE,{"disambiguationData":[TD([makeQuery(id+"F14.opLoft","SWEPT_FACE",FACE,{"disambiguationData":[OSD([sQuery(id+"F3.wireOp",EDGE,"E20.7.0"),subQ33,subQ32,sQuery(id+"F4.wireOp",EDGE,"E26.7.0"),subQ31,subQ30])]})])],"derivedFrom":subQ9})])]}),makeQuery(id+"F47.opFillet","BLEND_FACE",FACE,{"disambiguationData":[OSD([subQ5,subQ7]),TDD([makeQuery(id+"F42.boolean.opBoolean","COPY",EDGE,{"disambiguationData":[TD([makeQuery(id+"F15.opLoft","SWEPT_FACE",FACE,{"disambiguationData":[OSD([sQuery(id+"F3.wireOp",EDGE,"E20.6.0"),subQ29,subQ28,sQuery(id+"F4.wireOp",EDGE,"E26.6.0"),subQ27,subQ26])]})])],"derivedFrom":subQ9})])]}),makeQuery(id+"F47.opFillet","BLEND_FACE",FACE,{"disambiguationData":[OSD([subQ5,subQ7]),TDD([makeQuery(id+"F42.boolean.opBoolean","COPY",EDGE,{"disambiguationData":[TD([makeQuery(id+"F16.opLoft","SWEPT_FACE",FACE,{"disambiguationData":[OSD([sQuery(id+"F3.wireOp",EDGE,"E20.5.0"),subQ25,subQ24,sQuery(id+"F4.wireOp",EDGE,"E26.5.0"),subQ23,subQ22])]})])],"derivedFrom":subQ9})])]}),makeQuery(id+"F47.opFillet","BLEND_FACE",FACE,{"disambiguationData":[OSD([subQ5,subQ7]),TDD([makeQuery(id+"F42.boolean.opBoolean","COPY",EDGE,{"disambiguationData":[TD([makeQuery(id+"F17.opLoft","SWEPT_FACE",FACE,{"disambiguationData":[OSD([sQuery(id+"F3.wireOp",EDGE,"E20.4.0"),subQ21,subQ20,sQuery(id+"F4.wireOp",EDGE,"E26.4.0"),subQ19,subQ18])]})])],"derivedFrom":subQ9})])]}),makeQuery(id+"F47.opFillet","BLEND_FACE",FACE,{"disambiguationData":[OSD([subQ5,subQ7]),TDD([makeQuery(id+"F42.boolean.opBoolean","COPY",EDGE,{"disambiguationData":[TD([makeQuery(id+"F18.opLoft","SWEPT_FACE",FACE,{"disambiguationData":[OSD([sQuery(id+"F3.wireOp",EDGE,"E20.3.0"),subQ17,subQ16,sQuery(id+"F4.wireOp",EDGE,"E26.3.0"),subQ15,subQ14])]})])],"derivedFrom":subQ9})])]}),makeQuery(id+"F47.opFillet","BLEND_FACE",FACE,{"disambiguationData":[OSD([subQ5,subQ7]),TDD([makeQuery(id+"F42.boolean.opBoolean","COPY",EDGE,{"disambiguationData":[TD([makeQuery(id+"F19.opLoft","SWEPT_FACE",FACE,{"disambiguationData":[OSD([sQuery(id+"F3.wireOp",EDGE,"E20.2.0"),subQ13,subQ12,sQuery(id+"F4.wireOp",EDGE,"E26.2.0"),subQ11,subQ10])]})])],"derivedFrom":subQ9})])]}),makeQuery(id+"F47.opFillet","BLEND_FACE",FACE,{"disambiguationData":[OSD([subQ5,subQ7]),TDD([makeQuery(id+"F42.boolean.opBoolean","COPY",EDGE,{"disambiguationData":[TD([makeQuery(id+"F20.opLoft","SWEPT_FACE",FACE,{"disambiguationData":[OSD([sQuery(id+"F3.wireOp",EDGE,"E20.1.0"),subQ4,subQ3,sQuery(id+"F4.wireOp",EDGE,"E26.1.0"),subQ2,subQ1])]})])],"derivedFrom":subQ9})])]})]});}
            var Q56;
            {var subQ0=makeQuery(id+"F40.opExtrude","CAP_FACE",FACE,{"disambiguationData":[OSD([sQuery(id+"F39.wireOp",EDGE,"E29"),sQuery(id+"F39.wireOp",EDGE,"E30")])],"isStart":false});var subQ1=sQuery(id+"F4.wireOp",EDGE,"E26.1.3");var subQ2=sQuery(id+"F4.wireOp",EDGE,"E26.1.2");var subQ3=sQuery(id+"F3.wireOp",EDGE,"E20.1.3");var subQ4=sQuery(id+"F3.wireOp",EDGE,"E20.1.1");var subQ5=sQuery(id+"F41.wireOp",EDGE,"E35");var subQ6=makeQuery(id+"F42.opRevolve","SWEPT_FACE",FACE,{"disambiguationData":[OSD([subQ5])]});var subQ7=sQuery(id+"F41.wireOp",EDGE,"E36");var subQ8=makeQuery(id+"F42.opRevolve","SWEPT_FACE",FACE,{"disambiguationData":[OSD([subQ7])]});var subQ9=makeQuery(id+"F42.opRevolve","SWEPT_EDGE",EDGE,{"disambiguationData":[OSD([subQ5,subQ7])]});var subQ10=sQuery(id+"F4.wireOp",EDGE,"E26.2.3");var subQ11=sQuery(id+"F4.wireOp",EDGE,"E26.2.2");var subQ12=sQuery(id+"F3.wireOp",EDGE,"E20.2.3");var subQ13=sQuery(id+"F3.wireOp",EDGE,"E20.2.1");var subQ14=sQuery(id+"F4.wireOp",EDGE,"E26.3.3");var subQ15=sQuery(id+"F4.wireOp",EDGE,"E26.3.2");var subQ16=sQuery(id+"F3.wireOp",EDGE,"E20.3.3");var subQ17=sQuery(id+"F3.wireOp",EDGE,"E20.3.1");var subQ18=sQuery(id+"F4.wireOp",EDGE,"E26.4.3");var subQ19=sQuery(id+"F4.wireOp",EDGE,"E26.4.2");var subQ20=sQuery(id+"F3.wireOp",EDGE,"E20.4.3");var subQ21=sQuery(id+"F3.wireOp",EDGE,"E20.4.1");var subQ22=sQuery(id+"F4.wireOp",EDGE,"E26.5.3");var subQ23=sQuery(id+"F4.wireOp",EDGE,"E26.5.2");var subQ24=sQuery(id+"F3.wireOp",EDGE,"E20.5.3");var subQ25=sQuery(id+"F3.wireOp",EDGE,"E20.5.1");var subQ26=sQuery(id+"F4.wireOp",EDGE,"E26.6.3");var subQ27=sQuery(id+"F4.wireOp",EDGE,"E26.6.2");var subQ28=sQuery(id+"F3.wireOp",EDGE,"E20.6.3");var subQ29=sQuery(id+"F3.wireOp",EDGE,"E20.6.1");var subQ30=sQuery(id+"F4.wireOp",EDGE,"E26.7.3");var subQ31=sQuery(id+"F4.wireOp",EDGE,"E26.7.2");var subQ32=sQuery(id+"F3.wireOp",EDGE,"E20.7.3");var subQ33=sQuery(id+"F3.wireOp",EDGE,"E20.7.1");var subQ34=sQuery(id+"F4.wireOp",EDGE,"E26.8.3");var subQ35=sQuery(id+"F4.wireOp",EDGE,"E26.8.2");var subQ36=sQuery(id+"F3.wireOp",EDGE,"E20.8.3");var subQ37=sQuery(id+"F3.wireOp",EDGE,"E20.8.1");var subQ38=sQuery(id+"F4.wireOp",EDGE,"E26.9.3");var subQ39=sQuery(id+"F4.wireOp",EDGE,"E26.9.2");var subQ40=sQuery(id+"F3.wireOp",EDGE,"E20.9.3");var subQ41=sQuery(id+"F3.wireOp",EDGE,"E20.9.1");var subQ42=sQuery(id+"F4.wireOp",EDGE,"E26.10.3");var subQ43=sQuery(id+"F4.wireOp",EDGE,"E26.10.2");var subQ44=sQuery(id+"F3.wireOp",EDGE,"E20.10.3");var subQ45=sQuery(id+"F3.wireOp",EDGE,"E20.10.1");var subQ46=sQuery(id+"F4.wireOp",EDGE,"E26.11.3");var subQ47=sQuery(id+"F4.wireOp",EDGE,"E26.11.2");var subQ48=sQuery(id+"F3.wireOp",EDGE,"E20.11.3");var subQ49=sQuery(id+"F3.wireOp",EDGE,"E20.11.1");var subQ50=sQuery(id+"F4.wireOp",EDGE,"E26.12.3");var subQ51=sQuery(id+"F4.wireOp",EDGE,"E26.12.2");var subQ52=sQuery(id+"F3.wireOp",EDGE,"E20.12.3");var subQ53=sQuery(id+"F3.wireOp",EDGE,"E20.12.1");var subQ54=sQuery(id+"F4.wireOp",EDGE,"E26.13.3");var subQ55=sQuery(id+"F4.wireOp",EDGE,"E26.13.2");var subQ56=sQuery(id+"F3.wireOp",EDGE,"E20.13.3");var subQ57=sQuery(id+"F3.wireOp",EDGE,"E20.13.1");var subQ58=sQuery(id+"F4.wireOp",EDGE,"E26.14.3");var subQ59=sQuery(id+"F4.wireOp",EDGE,"E26.14.2");var subQ60=sQuery(id+"F3.wireOp",EDGE,"E20.14.3");var subQ61=sQuery(id+"F3.wireOp",EDGE,"E20.14.1");var subQ63=makeQuery(id+"F7.opLoft","SWEPT_FACE",FACE,{"disambiguationData":[OSD([sQuery(id+"F3.wireOp",EDGE,"E20.14.0"),subQ61,subQ60,sQuery(id+"F4.wireOp",EDGE,"E26.14.0"),subQ59,subQ58])]});var subQ64=sQuery(id+"F4.wireOp",EDGE,"E26.15.3");var subQ65=sQuery(id+"F4.wireOp",EDGE,"E26.15.2");var subQ66=sQuery(id+"F3.wireOp",EDGE,"E20.15.3");var subQ67=sQuery(id+"F3.wireOp",EDGE,"E20.15.1");var subQ68=sQuery(id+"F4.wireOp",EDGE,"E23");var subQ69=sQuery(id+"F4.wireOp",EDGE,"E22");var subQ70=sQuery(id+"F3.wireOp",EDGE,"E18.top");var subQ71=sQuery(id+"F3.wireOp",EDGE,"E18.bottom");var subQ74=makeQuery(id+"F42.boolean.opBoolean","COPY",FACE,{"disambiguationData":[TD([subQ63])],"derivedFrom":subQ6});var subQ75=makeQuery(id+"F7.boolean.opBoolean","INTERSECT",EDGE,{"derivedFrom":[makeQuery(id+"F1.opRevolve","SWEPT_FACE",FACE,{"disambiguationData":[OSD([sQuery(id+"F0.wireOp",EDGE,"E4")])]}),subQ63]});Q56=makeQuery(id+"F48.opFillet","BLEND_EDGE",EDGE,{"blendedFrom":[makeQuery(id+"F47.opFillet","TWEAK_EDGE",EDGE,{"derivedFrom":[makeQuery(id+"F45.opFillet","BLEND_VERTEX",VERTEX,{"blendedFrom":[subQ75,subQ63,subQ74],"blendedInto":[subQ63,subQ74]}),makeQuery(id+"F45.opFillet","BLEND_VERTEX",VERTEX,{"blendedFrom":[subQ75,makeQuery(id+"F42.boolean.opBoolean","MERGE",FACE,{"derivedFrom":[subQ0,subQ8]}),subQ74],"blendedInto":[makeQuery(id+"F42.boolean.opBoolean","MERGE",FACE,{"derivedFrom":[subQ0,subQ8]}),subQ74]})]}),makeQuery(id+"F47.opFillet","BLEND_FACE",FACE,{"disambiguationData":[OSD([subQ5,subQ7]),TDD([makeQuery(id+"F42.boolean.opBoolean","COPY",EDGE,{"disambiguationData":[TD([makeQuery(id+"F5.opLoft","SWEPT_FACE",FACE,{"disambiguationData":[OSD([subQ71,subQ70,sQuery(id+"F3.wireOp",EDGE,"E18.left"),sQuery(id+"F4.wireOp",EDGE,"E21"),subQ69,subQ68])]})])],"derivedFrom":subQ9})])]}),makeQuery(id+"F47.opFillet","BLEND_FACE",FACE,{"disambiguationData":[OSD([subQ5,subQ7]),TDD([makeQuery(id+"F42.boolean.opBoolean","COPY",EDGE,{"disambiguationData":[TD([makeQuery(id+"F6.opLoft","SWEPT_FACE",FACE,{"disambiguationData":[OSD([sQuery(id+"F3.wireOp",EDGE,"E20.15.0"),subQ67,subQ66,sQuery(id+"F4.wireOp",EDGE,"E26.15.0"),subQ65,subQ64])]})])],"derivedFrom":subQ9})])]}),makeQuery(id+"F47.opFillet","BLEND_FACE",FACE,{"disambiguationData":[OSD([subQ5,subQ7]),TDD([makeQuery(id+"F42.boolean.opBoolean","COPY",EDGE,{"disambiguationData":[TD([subQ63])],"derivedFrom":subQ9})])]}),makeQuery(id+"F47.opFillet","BLEND_FACE",FACE,{"disambiguationData":[OSD([subQ5,subQ7]),TDD([makeQuery(id+"F42.boolean.opBoolean","COPY",EDGE,{"disambiguationData":[TD([makeQuery(id+"F8.opLoft","SWEPT_FACE",FACE,{"disambiguationData":[OSD([sQuery(id+"F3.wireOp",EDGE,"E20.13.0"),subQ57,subQ56,sQuery(id+"F4.wireOp",EDGE,"E26.13.0"),subQ55,subQ54])]})])],"derivedFrom":subQ9})])]}),makeQuery(id+"F47.opFillet","BLEND_FACE",FACE,{"disambiguationData":[OSD([subQ5,subQ7]),TDD([makeQuery(id+"F42.boolean.opBoolean","COPY",EDGE,{"disambiguationData":[TD([makeQuery(id+"F9.opLoft","SWEPT_FACE",FACE,{"disambiguationData":[OSD([sQuery(id+"F3.wireOp",EDGE,"E20.12.0"),subQ53,subQ52,sQuery(id+"F4.wireOp",EDGE,"E26.12.0"),subQ51,subQ50])]})])],"derivedFrom":subQ9})])]}),makeQuery(id+"F47.opFillet","BLEND_FACE",FACE,{"disambiguationData":[OSD([subQ5,subQ7]),TDD([makeQuery(id+"F42.boolean.opBoolean","COPY",EDGE,{"disambiguationData":[TD([makeQuery(id+"F10.opLoft","SWEPT_FACE",FACE,{"disambiguationData":[OSD([sQuery(id+"F3.wireOp",EDGE,"E20.11.0"),subQ49,subQ48,sQuery(id+"F4.wireOp",EDGE,"E26.11.0"),subQ47,subQ46])]})])],"derivedFrom":subQ9})])]}),makeQuery(id+"F47.opFillet","BLEND_FACE",FACE,{"disambiguationData":[OSD([subQ5,subQ7]),TDD([makeQuery(id+"F42.boolean.opBoolean","COPY",EDGE,{"disambiguationData":[TD([makeQuery(id+"F11.opLoft","SWEPT_FACE",FACE,{"disambiguationData":[OSD([sQuery(id+"F3.wireOp",EDGE,"E20.10.0"),subQ45,subQ44,sQuery(id+"F4.wireOp",EDGE,"E26.10.0"),subQ43,subQ42])]})])],"derivedFrom":subQ9})])]}),makeQuery(id+"F47.opFillet","BLEND_FACE",FACE,{"disambiguationData":[OSD([subQ5,subQ7]),TDD([makeQuery(id+"F42.boolean.opBoolean","COPY",EDGE,{"disambiguationData":[TD([makeQuery(id+"F12.opLoft","SWEPT_FACE",FACE,{"disambiguationData":[OSD([sQuery(id+"F3.wireOp",EDGE,"E20.9.0"),subQ41,subQ40,sQuery(id+"F4.wireOp",EDGE,"E26.9.0"),subQ39,subQ38])]})])],"derivedFrom":subQ9})])]}),makeQuery(id+"F47.opFillet","BLEND_FACE",FACE,{"disambiguationData":[OSD([subQ5,subQ7]),TDD([makeQuery(id+"F42.boolean.opBoolean","COPY",EDGE,{"disambiguationData":[TD([makeQuery(id+"F13.opLoft","SWEPT_FACE",FACE,{"disambiguationData":[OSD([sQuery(id+"F3.wireOp",EDGE,"E20.8.0"),subQ37,subQ36,sQuery(id+"F4.wireOp",EDGE,"E26.8.0"),subQ35,subQ34])]})])],"derivedFrom":subQ9})])]}),makeQuery(id+"F47.opFillet","BLEND_FACE",FACE,{"disambiguationData":[OSD([subQ5,subQ7]),TDD([makeQuery(id+"F42.boolean.opBoolean","COPY",EDGE,{"disambiguationData":[TD([makeQuery(id+"F14.opLoft","SWEPT_FACE",FACE,{"disambiguationData":[OSD([sQuery(id+"F3.wireOp",EDGE,"E20.7.0"),subQ33,subQ32,sQuery(id+"F4.wireOp",EDGE,"E26.7.0"),subQ31,subQ30])]})])],"derivedFrom":subQ9})])]}),makeQuery(id+"F47.opFillet","BLEND_FACE",FACE,{"disambiguationData":[OSD([subQ5,subQ7]),TDD([makeQuery(id+"F42.boolean.opBoolean","COPY",EDGE,{"disambiguationData":[TD([makeQuery(id+"F15.opLoft","SWEPT_FACE",FACE,{"disambiguationData":[OSD([sQuery(id+"F3.wireOp",EDGE,"E20.6.0"),subQ29,subQ28,sQuery(id+"F4.wireOp",EDGE,"E26.6.0"),subQ27,subQ26])]})])],"derivedFrom":subQ9})])]}),makeQuery(id+"F47.opFillet","BLEND_FACE",FACE,{"disambiguationData":[OSD([subQ5,subQ7]),TDD([makeQuery(id+"F42.boolean.opBoolean","COPY",EDGE,{"disambiguationData":[TD([makeQuery(id+"F16.opLoft","SWEPT_FACE",FACE,{"disambiguationData":[OSD([sQuery(id+"F3.wireOp",EDGE,"E20.5.0"),subQ25,subQ24,sQuery(id+"F4.wireOp",EDGE,"E26.5.0"),subQ23,subQ22])]})])],"derivedFrom":subQ9})])]}),makeQuery(id+"F47.opFillet","BLEND_FACE",FACE,{"disambiguationData":[OSD([subQ5,subQ7]),TDD([makeQuery(id+"F42.boolean.opBoolean","COPY",EDGE,{"disambiguationData":[TD([makeQuery(id+"F17.opLoft","SWEPT_FACE",FACE,{"disambiguationData":[OSD([sQuery(id+"F3.wireOp",EDGE,"E20.4.0"),subQ21,subQ20,sQuery(id+"F4.wireOp",EDGE,"E26.4.0"),subQ19,subQ18])]})])],"derivedFrom":subQ9})])]}),makeQuery(id+"F47.opFillet","BLEND_FACE",FACE,{"disambiguationData":[OSD([subQ5,subQ7]),TDD([makeQuery(id+"F42.boolean.opBoolean","COPY",EDGE,{"disambiguationData":[TD([makeQuery(id+"F18.opLoft","SWEPT_FACE",FACE,{"disambiguationData":[OSD([sQuery(id+"F3.wireOp",EDGE,"E20.3.0"),subQ17,subQ16,sQuery(id+"F4.wireOp",EDGE,"E26.3.0"),subQ15,subQ14])]})])],"derivedFrom":subQ9})])]}),makeQuery(id+"F47.opFillet","BLEND_FACE",FACE,{"disambiguationData":[OSD([subQ5,subQ7]),TDD([makeQuery(id+"F42.boolean.opBoolean","COPY",EDGE,{"disambiguationData":[TD([makeQuery(id+"F19.opLoft","SWEPT_FACE",FACE,{"disambiguationData":[OSD([sQuery(id+"F3.wireOp",EDGE,"E20.2.0"),subQ13,subQ12,sQuery(id+"F4.wireOp",EDGE,"E26.2.0"),subQ11,subQ10])]})])],"derivedFrom":subQ9})])]}),makeQuery(id+"F47.opFillet","BLEND_FACE",FACE,{"disambiguationData":[OSD([subQ5,subQ7]),TDD([makeQuery(id+"F42.boolean.opBoolean","COPY",EDGE,{"disambiguationData":[TD([makeQuery(id+"F20.opLoft","SWEPT_FACE",FACE,{"disambiguationData":[OSD([sQuery(id+"F3.wireOp",EDGE,"E20.1.0"),subQ4,subQ3,sQuery(id+"F4.wireOp",EDGE,"E26.1.0"),subQ2,subQ1])]})])],"derivedFrom":subQ9})])]})],"blendedInto":[makeQuery(id+"F47.opFillet","BLEND_FACE",FACE,{"disambiguationData":[OSD([subQ5,subQ7]),TDD([makeQuery(id+"F42.boolean.opBoolean","COPY",EDGE,{"disambiguationData":[TD([makeQuery(id+"F5.opLoft","SWEPT_FACE",FACE,{"disambiguationData":[OSD([subQ71,subQ70,sQuery(id+"F3.wireOp",EDGE,"E18.left"),sQuery(id+"F4.wireOp",EDGE,"E21"),subQ69,subQ68])]})])],"derivedFrom":subQ9})])]}),makeQuery(id+"F47.opFillet","BLEND_FACE",FACE,{"disambiguationData":[OSD([subQ5,subQ7]),TDD([makeQuery(id+"F42.boolean.opBoolean","COPY",EDGE,{"disambiguationData":[TD([makeQuery(id+"F6.opLoft","SWEPT_FACE",FACE,{"disambiguationData":[OSD([sQuery(id+"F3.wireOp",EDGE,"E20.15.0"),subQ67,subQ66,sQuery(id+"F4.wireOp",EDGE,"E26.15.0"),subQ65,subQ64])]})])],"derivedFrom":subQ9})])]}),makeQuery(id+"F47.opFillet","BLEND_FACE",FACE,{"disambiguationData":[OSD([subQ5,subQ7]),TDD([makeQuery(id+"F42.boolean.opBoolean","COPY",EDGE,{"disambiguationData":[TD([subQ63])],"derivedFrom":subQ9})])]}),makeQuery(id+"F47.opFillet","BLEND_FACE",FACE,{"disambiguationData":[OSD([subQ5,subQ7]),TDD([makeQuery(id+"F42.boolean.opBoolean","COPY",EDGE,{"disambiguationData":[TD([makeQuery(id+"F8.opLoft","SWEPT_FACE",FACE,{"disambiguationData":[OSD([sQuery(id+"F3.wireOp",EDGE,"E20.13.0"),subQ57,subQ56,sQuery(id+"F4.wireOp",EDGE,"E26.13.0"),subQ55,subQ54])]})])],"derivedFrom":subQ9})])]}),makeQuery(id+"F47.opFillet","BLEND_FACE",FACE,{"disambiguationData":[OSD([subQ5,subQ7]),TDD([makeQuery(id+"F42.boolean.opBoolean","COPY",EDGE,{"disambiguationData":[TD([makeQuery(id+"F9.opLoft","SWEPT_FACE",FACE,{"disambiguationData":[OSD([sQuery(id+"F3.wireOp",EDGE,"E20.12.0"),subQ53,subQ52,sQuery(id+"F4.wireOp",EDGE,"E26.12.0"),subQ51,subQ50])]})])],"derivedFrom":subQ9})])]}),makeQuery(id+"F47.opFillet","BLEND_FACE",FACE,{"disambiguationData":[OSD([subQ5,subQ7]),TDD([makeQuery(id+"F42.boolean.opBoolean","COPY",EDGE,{"disambiguationData":[TD([makeQuery(id+"F10.opLoft","SWEPT_FACE",FACE,{"disambiguationData":[OSD([sQuery(id+"F3.wireOp",EDGE,"E20.11.0"),subQ49,subQ48,sQuery(id+"F4.wireOp",EDGE,"E26.11.0"),subQ47,subQ46])]})])],"derivedFrom":subQ9})])]}),makeQuery(id+"F47.opFillet","BLEND_FACE",FACE,{"disambiguationData":[OSD([subQ5,subQ7]),TDD([makeQuery(id+"F42.boolean.opBoolean","COPY",EDGE,{"disambiguationData":[TD([makeQuery(id+"F11.opLoft","SWEPT_FACE",FACE,{"disambiguationData":[OSD([sQuery(id+"F3.wireOp",EDGE,"E20.10.0"),subQ45,subQ44,sQuery(id+"F4.wireOp",EDGE,"E26.10.0"),subQ43,subQ42])]})])],"derivedFrom":subQ9})])]}),makeQuery(id+"F47.opFillet","BLEND_FACE",FACE,{"disambiguationData":[OSD([subQ5,subQ7]),TDD([makeQuery(id+"F42.boolean.opBoolean","COPY",EDGE,{"disambiguationData":[TD([makeQuery(id+"F12.opLoft","SWEPT_FACE",FACE,{"disambiguationData":[OSD([sQuery(id+"F3.wireOp",EDGE,"E20.9.0"),subQ41,subQ40,sQuery(id+"F4.wireOp",EDGE,"E26.9.0"),subQ39,subQ38])]})])],"derivedFrom":subQ9})])]}),makeQuery(id+"F47.opFillet","BLEND_FACE",FACE,{"disambiguationData":[OSD([subQ5,subQ7]),TDD([makeQuery(id+"F42.boolean.opBoolean","COPY",EDGE,{"disambiguationData":[TD([makeQuery(id+"F13.opLoft","SWEPT_FACE",FACE,{"disambiguationData":[OSD([sQuery(id+"F3.wireOp",EDGE,"E20.8.0"),subQ37,subQ36,sQuery(id+"F4.wireOp",EDGE,"E26.8.0"),subQ35,subQ34])]})])],"derivedFrom":subQ9})])]}),makeQuery(id+"F47.opFillet","BLEND_FACE",FACE,{"disambiguationData":[OSD([subQ5,subQ7]),TDD([makeQuery(id+"F42.boolean.opBoolean","COPY",EDGE,{"disambiguationData":[TD([makeQuery(id+"F14.opLoft","SWEPT_FACE",FACE,{"disambiguationData":[OSD([sQuery(id+"F3.wireOp",EDGE,"E20.7.0"),subQ33,subQ32,sQuery(id+"F4.wireOp",EDGE,"E26.7.0"),subQ31,subQ30])]})])],"derivedFrom":subQ9})])]}),makeQuery(id+"F47.opFillet","BLEND_FACE",FACE,{"disambiguationData":[OSD([subQ5,subQ7]),TDD([makeQuery(id+"F42.boolean.opBoolean","COPY",EDGE,{"disambiguationData":[TD([makeQuery(id+"F15.opLoft","SWEPT_FACE",FACE,{"disambiguationData":[OSD([sQuery(id+"F3.wireOp",EDGE,"E20.6.0"),subQ29,subQ28,sQuery(id+"F4.wireOp",EDGE,"E26.6.0"),subQ27,subQ26])]})])],"derivedFrom":subQ9})])]}),makeQuery(id+"F47.opFillet","BLEND_FACE",FACE,{"disambiguationData":[OSD([subQ5,subQ7]),TDD([makeQuery(id+"F42.boolean.opBoolean","COPY",EDGE,{"disambiguationData":[TD([makeQuery(id+"F16.opLoft","SWEPT_FACE",FACE,{"disambiguationData":[OSD([sQuery(id+"F3.wireOp",EDGE,"E20.5.0"),subQ25,subQ24,sQuery(id+"F4.wireOp",EDGE,"E26.5.0"),subQ23,subQ22])]})])],"derivedFrom":subQ9})])]}),makeQuery(id+"F47.opFillet","BLEND_FACE",FACE,{"disambiguationData":[OSD([subQ5,subQ7]),TDD([makeQuery(id+"F42.boolean.opBoolean","COPY",EDGE,{"disambiguationData":[TD([makeQuery(id+"F17.opLoft","SWEPT_FACE",FACE,{"disambiguationData":[OSD([sQuery(id+"F3.wireOp",EDGE,"E20.4.0"),subQ21,subQ20,sQuery(id+"F4.wireOp",EDGE,"E26.4.0"),subQ19,subQ18])]})])],"derivedFrom":subQ9})])]}),makeQuery(id+"F47.opFillet","BLEND_FACE",FACE,{"disambiguationData":[OSD([subQ5,subQ7]),TDD([makeQuery(id+"F42.boolean.opBoolean","COPY",EDGE,{"disambiguationData":[TD([makeQuery(id+"F18.opLoft","SWEPT_FACE",FACE,{"disambiguationData":[OSD([sQuery(id+"F3.wireOp",EDGE,"E20.3.0"),subQ17,subQ16,sQuery(id+"F4.wireOp",EDGE,"E26.3.0"),subQ15,subQ14])]})])],"derivedFrom":subQ9})])]}),makeQuery(id+"F47.opFillet","BLEND_FACE",FACE,{"disambiguationData":[OSD([subQ5,subQ7]),TDD([makeQuery(id+"F42.boolean.opBoolean","COPY",EDGE,{"disambiguationData":[TD([makeQuery(id+"F19.opLoft","SWEPT_FACE",FACE,{"disambiguationData":[OSD([sQuery(id+"F3.wireOp",EDGE,"E20.2.0"),subQ13,subQ12,sQuery(id+"F4.wireOp",EDGE,"E26.2.0"),subQ11,subQ10])]})])],"derivedFrom":subQ9})])]}),makeQuery(id+"F47.opFillet","BLEND_FACE",FACE,{"disambiguationData":[OSD([subQ5,subQ7]),TDD([makeQuery(id+"F42.boolean.opBoolean","COPY",EDGE,{"disambiguationData":[TD([makeQuery(id+"F20.opLoft","SWEPT_FACE",FACE,{"disambiguationData":[OSD([sQuery(id+"F3.wireOp",EDGE,"E20.1.0"),subQ4,subQ3,sQuery(id+"F4.wireOp",EDGE,"E26.1.0"),subQ2,subQ1])]})])],"derivedFrom":subQ9})])]})]});}
            var Q57;
            {var subQ0=makeQuery(id+"F40.opExtrude","CAP_FACE",FACE,{"disambiguationData":[OSD([sQuery(id+"F39.wireOp",EDGE,"E29"),sQuery(id+"F39.wireOp",EDGE,"E30")])],"isStart":false});var subQ1=sQuery(id+"F4.wireOp",EDGE,"E26.1.3");var subQ2=sQuery(id+"F4.wireOp",EDGE,"E26.1.2");var subQ3=sQuery(id+"F3.wireOp",EDGE,"E20.1.3");var subQ4=sQuery(id+"F3.wireOp",EDGE,"E20.1.1");var subQ5=sQuery(id+"F41.wireOp",EDGE,"E35");var subQ6=makeQuery(id+"F42.opRevolve","SWEPT_FACE",FACE,{"disambiguationData":[OSD([subQ5])]});var subQ7=sQuery(id+"F41.wireOp",EDGE,"E36");var subQ8=makeQuery(id+"F42.opRevolve","SWEPT_FACE",FACE,{"disambiguationData":[OSD([subQ7])]});var subQ9=makeQuery(id+"F42.opRevolve","SWEPT_EDGE",EDGE,{"disambiguationData":[OSD([subQ5,subQ7])]});var subQ10=sQuery(id+"F4.wireOp",EDGE,"E26.2.3");var subQ11=sQuery(id+"F4.wireOp",EDGE,"E26.2.2");var subQ12=sQuery(id+"F3.wireOp",EDGE,"E20.2.3");var subQ13=sQuery(id+"F3.wireOp",EDGE,"E20.2.1");var subQ14=sQuery(id+"F4.wireOp",EDGE,"E26.3.3");var subQ15=sQuery(id+"F4.wireOp",EDGE,"E26.3.2");var subQ16=sQuery(id+"F3.wireOp",EDGE,"E20.3.3");var subQ17=sQuery(id+"F3.wireOp",EDGE,"E20.3.1");var subQ18=sQuery(id+"F4.wireOp",EDGE,"E26.4.3");var subQ19=sQuery(id+"F4.wireOp",EDGE,"E26.4.2");var subQ20=sQuery(id+"F3.wireOp",EDGE,"E20.4.3");var subQ21=sQuery(id+"F3.wireOp",EDGE,"E20.4.1");var subQ22=sQuery(id+"F4.wireOp",EDGE,"E26.5.3");var subQ23=sQuery(id+"F4.wireOp",EDGE,"E26.5.2");var subQ24=sQuery(id+"F3.wireOp",EDGE,"E20.5.3");var subQ25=sQuery(id+"F3.wireOp",EDGE,"E20.5.1");var subQ26=sQuery(id+"F4.wireOp",EDGE,"E26.6.3");var subQ27=sQuery(id+"F4.wireOp",EDGE,"E26.6.2");var subQ28=sQuery(id+"F3.wireOp",EDGE,"E20.6.3");var subQ29=sQuery(id+"F3.wireOp",EDGE,"E20.6.1");var subQ30=sQuery(id+"F4.wireOp",EDGE,"E26.7.3");var subQ31=sQuery(id+"F4.wireOp",EDGE,"E26.7.2");var subQ32=sQuery(id+"F3.wireOp",EDGE,"E20.7.3");var subQ33=sQuery(id+"F3.wireOp",EDGE,"E20.7.1");var subQ34=sQuery(id+"F4.wireOp",EDGE,"E26.8.3");var subQ35=sQuery(id+"F4.wireOp",EDGE,"E26.8.2");var subQ36=sQuery(id+"F3.wireOp",EDGE,"E20.8.3");var subQ37=sQuery(id+"F3.wireOp",EDGE,"E20.8.1");var subQ38=sQuery(id+"F4.wireOp",EDGE,"E26.9.3");var subQ39=sQuery(id+"F4.wireOp",EDGE,"E26.9.2");var subQ40=sQuery(id+"F3.wireOp",EDGE,"E20.9.3");var subQ41=sQuery(id+"F3.wireOp",EDGE,"E20.9.1");var subQ42=sQuery(id+"F4.wireOp",EDGE,"E26.10.3");var subQ43=sQuery(id+"F4.wireOp",EDGE,"E26.10.2");var subQ44=sQuery(id+"F3.wireOp",EDGE,"E20.10.3");var subQ45=sQuery(id+"F3.wireOp",EDGE,"E20.10.1");var subQ46=sQuery(id+"F4.wireOp",EDGE,"E26.11.3");var subQ47=sQuery(id+"F4.wireOp",EDGE,"E26.11.2");var subQ48=sQuery(id+"F3.wireOp",EDGE,"E20.11.3");var subQ49=sQuery(id+"F3.wireOp",EDGE,"E20.11.1");var subQ50=sQuery(id+"F4.wireOp",EDGE,"E26.12.3");var subQ51=sQuery(id+"F4.wireOp",EDGE,"E26.12.2");var subQ52=sQuery(id+"F3.wireOp",EDGE,"E20.12.3");var subQ53=sQuery(id+"F3.wireOp",EDGE,"E20.12.1");var subQ54=sQuery(id+"F4.wireOp",EDGE,"E26.13.3");var subQ55=sQuery(id+"F4.wireOp",EDGE,"E26.13.2");var subQ56=sQuery(id+"F3.wireOp",EDGE,"E20.13.3");var subQ57=sQuery(id+"F3.wireOp",EDGE,"E20.13.1");var subQ59=makeQuery(id+"F8.opLoft","SWEPT_FACE",FACE,{"disambiguationData":[OSD([sQuery(id+"F3.wireOp",EDGE,"E20.13.0"),subQ57,subQ56,sQuery(id+"F4.wireOp",EDGE,"E26.13.0"),subQ55,subQ54])]});var subQ60=sQuery(id+"F4.wireOp",EDGE,"E26.14.3");var subQ61=sQuery(id+"F4.wireOp",EDGE,"E26.14.2");var subQ62=sQuery(id+"F3.wireOp",EDGE,"E20.14.3");var subQ63=sQuery(id+"F3.wireOp",EDGE,"E20.14.1");var subQ64=sQuery(id+"F4.wireOp",EDGE,"E26.15.3");var subQ65=sQuery(id+"F4.wireOp",EDGE,"E26.15.2");var subQ66=sQuery(id+"F3.wireOp",EDGE,"E20.15.3");var subQ67=sQuery(id+"F3.wireOp",EDGE,"E20.15.1");var subQ68=sQuery(id+"F4.wireOp",EDGE,"E23");var subQ69=sQuery(id+"F4.wireOp",EDGE,"E22");var subQ70=sQuery(id+"F3.wireOp",EDGE,"E18.top");var subQ71=sQuery(id+"F3.wireOp",EDGE,"E18.bottom");var subQ74=makeQuery(id+"F42.boolean.opBoolean","COPY",FACE,{"disambiguationData":[TD([subQ59])],"derivedFrom":subQ6});var subQ75=makeQuery(id+"F8.boolean.opBoolean","INTERSECT",EDGE,{"derivedFrom":[makeQuery(id+"F1.opRevolve","SWEPT_FACE",FACE,{"disambiguationData":[OSD([sQuery(id+"F0.wireOp",EDGE,"E4")])]}),subQ59]});Q57=makeQuery(id+"F48.opFillet","BLEND_EDGE",EDGE,{"blendedFrom":[makeQuery(id+"F47.opFillet","TWEAK_EDGE",EDGE,{"derivedFrom":[makeQuery(id+"F45.opFillet","BLEND_VERTEX",VERTEX,{"blendedFrom":[subQ75,subQ59,subQ74],"blendedInto":[subQ59,subQ74]}),makeQuery(id+"F45.opFillet","BLEND_VERTEX",VERTEX,{"blendedFrom":[subQ75,makeQuery(id+"F42.boolean.opBoolean","MERGE",FACE,{"derivedFrom":[subQ0,subQ8]}),subQ74],"blendedInto":[makeQuery(id+"F42.boolean.opBoolean","MERGE",FACE,{"derivedFrom":[subQ0,subQ8]}),subQ74]})]}),makeQuery(id+"F47.opFillet","BLEND_FACE",FACE,{"disambiguationData":[OSD([subQ5,subQ7]),TDD([makeQuery(id+"F42.boolean.opBoolean","COPY",EDGE,{"disambiguationData":[TD([makeQuery(id+"F5.opLoft","SWEPT_FACE",FACE,{"disambiguationData":[OSD([subQ71,subQ70,sQuery(id+"F3.wireOp",EDGE,"E18.left"),sQuery(id+"F4.wireOp",EDGE,"E21"),subQ69,subQ68])]})])],"derivedFrom":subQ9})])]}),makeQuery(id+"F47.opFillet","BLEND_FACE",FACE,{"disambiguationData":[OSD([subQ5,subQ7]),TDD([makeQuery(id+"F42.boolean.opBoolean","COPY",EDGE,{"disambiguationData":[TD([makeQuery(id+"F6.opLoft","SWEPT_FACE",FACE,{"disambiguationData":[OSD([sQuery(id+"F3.wireOp",EDGE,"E20.15.0"),subQ67,subQ66,sQuery(id+"F4.wireOp",EDGE,"E26.15.0"),subQ65,subQ64])]})])],"derivedFrom":subQ9})])]}),makeQuery(id+"F47.opFillet","BLEND_FACE",FACE,{"disambiguationData":[OSD([subQ5,subQ7]),TDD([makeQuery(id+"F42.boolean.opBoolean","COPY",EDGE,{"disambiguationData":[TD([makeQuery(id+"F7.opLoft","SWEPT_FACE",FACE,{"disambiguationData":[OSD([sQuery(id+"F3.wireOp",EDGE,"E20.14.0"),subQ63,subQ62,sQuery(id+"F4.wireOp",EDGE,"E26.14.0"),subQ61,subQ60])]})])],"derivedFrom":subQ9})])]}),makeQuery(id+"F47.opFillet","BLEND_FACE",FACE,{"disambiguationData":[OSD([subQ5,subQ7]),TDD([makeQuery(id+"F42.boolean.opBoolean","COPY",EDGE,{"disambiguationData":[TD([subQ59])],"derivedFrom":subQ9})])]}),makeQuery(id+"F47.opFillet","BLEND_FACE",FACE,{"disambiguationData":[OSD([subQ5,subQ7]),TDD([makeQuery(id+"F42.boolean.opBoolean","COPY",EDGE,{"disambiguationData":[TD([makeQuery(id+"F9.opLoft","SWEPT_FACE",FACE,{"disambiguationData":[OSD([sQuery(id+"F3.wireOp",EDGE,"E20.12.0"),subQ53,subQ52,sQuery(id+"F4.wireOp",EDGE,"E26.12.0"),subQ51,subQ50])]})])],"derivedFrom":subQ9})])]}),makeQuery(id+"F47.opFillet","BLEND_FACE",FACE,{"disambiguationData":[OSD([subQ5,subQ7]),TDD([makeQuery(id+"F42.boolean.opBoolean","COPY",EDGE,{"disambiguationData":[TD([makeQuery(id+"F10.opLoft","SWEPT_FACE",FACE,{"disambiguationData":[OSD([sQuery(id+"F3.wireOp",EDGE,"E20.11.0"),subQ49,subQ48,sQuery(id+"F4.wireOp",EDGE,"E26.11.0"),subQ47,subQ46])]})])],"derivedFrom":subQ9})])]}),makeQuery(id+"F47.opFillet","BLEND_FACE",FACE,{"disambiguationData":[OSD([subQ5,subQ7]),TDD([makeQuery(id+"F42.boolean.opBoolean","COPY",EDGE,{"disambiguationData":[TD([makeQuery(id+"F11.opLoft","SWEPT_FACE",FACE,{"disambiguationData":[OSD([sQuery(id+"F3.wireOp",EDGE,"E20.10.0"),subQ45,subQ44,sQuery(id+"F4.wireOp",EDGE,"E26.10.0"),subQ43,subQ42])]})])],"derivedFrom":subQ9})])]}),makeQuery(id+"F47.opFillet","BLEND_FACE",FACE,{"disambiguationData":[OSD([subQ5,subQ7]),TDD([makeQuery(id+"F42.boolean.opBoolean","COPY",EDGE,{"disambiguationData":[TD([makeQuery(id+"F12.opLoft","SWEPT_FACE",FACE,{"disambiguationData":[OSD([sQuery(id+"F3.wireOp",EDGE,"E20.9.0"),subQ41,subQ40,sQuery(id+"F4.wireOp",EDGE,"E26.9.0"),subQ39,subQ38])]})])],"derivedFrom":subQ9})])]}),makeQuery(id+"F47.opFillet","BLEND_FACE",FACE,{"disambiguationData":[OSD([subQ5,subQ7]),TDD([makeQuery(id+"F42.boolean.opBoolean","COPY",EDGE,{"disambiguationData":[TD([makeQuery(id+"F13.opLoft","SWEPT_FACE",FACE,{"disambiguationData":[OSD([sQuery(id+"F3.wireOp",EDGE,"E20.8.0"),subQ37,subQ36,sQuery(id+"F4.wireOp",EDGE,"E26.8.0"),subQ35,subQ34])]})])],"derivedFrom":subQ9})])]}),makeQuery(id+"F47.opFillet","BLEND_FACE",FACE,{"disambiguationData":[OSD([subQ5,subQ7]),TDD([makeQuery(id+"F42.boolean.opBoolean","COPY",EDGE,{"disambiguationData":[TD([makeQuery(id+"F14.opLoft","SWEPT_FACE",FACE,{"disambiguationData":[OSD([sQuery(id+"F3.wireOp",EDGE,"E20.7.0"),subQ33,subQ32,sQuery(id+"F4.wireOp",EDGE,"E26.7.0"),subQ31,subQ30])]})])],"derivedFrom":subQ9})])]}),makeQuery(id+"F47.opFillet","BLEND_FACE",FACE,{"disambiguationData":[OSD([subQ5,subQ7]),TDD([makeQuery(id+"F42.boolean.opBoolean","COPY",EDGE,{"disambiguationData":[TD([makeQuery(id+"F15.opLoft","SWEPT_FACE",FACE,{"disambiguationData":[OSD([sQuery(id+"F3.wireOp",EDGE,"E20.6.0"),subQ29,subQ28,sQuery(id+"F4.wireOp",EDGE,"E26.6.0"),subQ27,subQ26])]})])],"derivedFrom":subQ9})])]}),makeQuery(id+"F47.opFillet","BLEND_FACE",FACE,{"disambiguationData":[OSD([subQ5,subQ7]),TDD([makeQuery(id+"F42.boolean.opBoolean","COPY",EDGE,{"disambiguationData":[TD([makeQuery(id+"F16.opLoft","SWEPT_FACE",FACE,{"disambiguationData":[OSD([sQuery(id+"F3.wireOp",EDGE,"E20.5.0"),subQ25,subQ24,sQuery(id+"F4.wireOp",EDGE,"E26.5.0"),subQ23,subQ22])]})])],"derivedFrom":subQ9})])]}),makeQuery(id+"F47.opFillet","BLEND_FACE",FACE,{"disambiguationData":[OSD([subQ5,subQ7]),TDD([makeQuery(id+"F42.boolean.opBoolean","COPY",EDGE,{"disambiguationData":[TD([makeQuery(id+"F17.opLoft","SWEPT_FACE",FACE,{"disambiguationData":[OSD([sQuery(id+"F3.wireOp",EDGE,"E20.4.0"),subQ21,subQ20,sQuery(id+"F4.wireOp",EDGE,"E26.4.0"),subQ19,subQ18])]})])],"derivedFrom":subQ9})])]}),makeQuery(id+"F47.opFillet","BLEND_FACE",FACE,{"disambiguationData":[OSD([subQ5,subQ7]),TDD([makeQuery(id+"F42.boolean.opBoolean","COPY",EDGE,{"disambiguationData":[TD([makeQuery(id+"F18.opLoft","SWEPT_FACE",FACE,{"disambiguationData":[OSD([sQuery(id+"F3.wireOp",EDGE,"E20.3.0"),subQ17,subQ16,sQuery(id+"F4.wireOp",EDGE,"E26.3.0"),subQ15,subQ14])]})])],"derivedFrom":subQ9})])]}),makeQuery(id+"F47.opFillet","BLEND_FACE",FACE,{"disambiguationData":[OSD([subQ5,subQ7]),TDD([makeQuery(id+"F42.boolean.opBoolean","COPY",EDGE,{"disambiguationData":[TD([makeQuery(id+"F19.opLoft","SWEPT_FACE",FACE,{"disambiguationData":[OSD([sQuery(id+"F3.wireOp",EDGE,"E20.2.0"),subQ13,subQ12,sQuery(id+"F4.wireOp",EDGE,"E26.2.0"),subQ11,subQ10])]})])],"derivedFrom":subQ9})])]}),makeQuery(id+"F47.opFillet","BLEND_FACE",FACE,{"disambiguationData":[OSD([subQ5,subQ7]),TDD([makeQuery(id+"F42.boolean.opBoolean","COPY",EDGE,{"disambiguationData":[TD([makeQuery(id+"F20.opLoft","SWEPT_FACE",FACE,{"disambiguationData":[OSD([sQuery(id+"F3.wireOp",EDGE,"E20.1.0"),subQ4,subQ3,sQuery(id+"F4.wireOp",EDGE,"E26.1.0"),subQ2,subQ1])]})])],"derivedFrom":subQ9})])]})],"blendedInto":[makeQuery(id+"F47.opFillet","BLEND_FACE",FACE,{"disambiguationData":[OSD([subQ5,subQ7]),TDD([makeQuery(id+"F42.boolean.opBoolean","COPY",EDGE,{"disambiguationData":[TD([makeQuery(id+"F5.opLoft","SWEPT_FACE",FACE,{"disambiguationData":[OSD([subQ71,subQ70,sQuery(id+"F3.wireOp",EDGE,"E18.left"),sQuery(id+"F4.wireOp",EDGE,"E21"),subQ69,subQ68])]})])],"derivedFrom":subQ9})])]}),makeQuery(id+"F47.opFillet","BLEND_FACE",FACE,{"disambiguationData":[OSD([subQ5,subQ7]),TDD([makeQuery(id+"F42.boolean.opBoolean","COPY",EDGE,{"disambiguationData":[TD([makeQuery(id+"F6.opLoft","SWEPT_FACE",FACE,{"disambiguationData":[OSD([sQuery(id+"F3.wireOp",EDGE,"E20.15.0"),subQ67,subQ66,sQuery(id+"F4.wireOp",EDGE,"E26.15.0"),subQ65,subQ64])]})])],"derivedFrom":subQ9})])]}),makeQuery(id+"F47.opFillet","BLEND_FACE",FACE,{"disambiguationData":[OSD([subQ5,subQ7]),TDD([makeQuery(id+"F42.boolean.opBoolean","COPY",EDGE,{"disambiguationData":[TD([makeQuery(id+"F7.opLoft","SWEPT_FACE",FACE,{"disambiguationData":[OSD([sQuery(id+"F3.wireOp",EDGE,"E20.14.0"),subQ63,subQ62,sQuery(id+"F4.wireOp",EDGE,"E26.14.0"),subQ61,subQ60])]})])],"derivedFrom":subQ9})])]}),makeQuery(id+"F47.opFillet","BLEND_FACE",FACE,{"disambiguationData":[OSD([subQ5,subQ7]),TDD([makeQuery(id+"F42.boolean.opBoolean","COPY",EDGE,{"disambiguationData":[TD([subQ59])],"derivedFrom":subQ9})])]}),makeQuery(id+"F47.opFillet","BLEND_FACE",FACE,{"disambiguationData":[OSD([subQ5,subQ7]),TDD([makeQuery(id+"F42.boolean.opBoolean","COPY",EDGE,{"disambiguationData":[TD([makeQuery(id+"F9.opLoft","SWEPT_FACE",FACE,{"disambiguationData":[OSD([sQuery(id+"F3.wireOp",EDGE,"E20.12.0"),subQ53,subQ52,sQuery(id+"F4.wireOp",EDGE,"E26.12.0"),subQ51,subQ50])]})])],"derivedFrom":subQ9})])]}),makeQuery(id+"F47.opFillet","BLEND_FACE",FACE,{"disambiguationData":[OSD([subQ5,subQ7]),TDD([makeQuery(id+"F42.boolean.opBoolean","COPY",EDGE,{"disambiguationData":[TD([makeQuery(id+"F10.opLoft","SWEPT_FACE",FACE,{"disambiguationData":[OSD([sQuery(id+"F3.wireOp",EDGE,"E20.11.0"),subQ49,subQ48,sQuery(id+"F4.wireOp",EDGE,"E26.11.0"),subQ47,subQ46])]})])],"derivedFrom":subQ9})])]}),makeQuery(id+"F47.opFillet","BLEND_FACE",FACE,{"disambiguationData":[OSD([subQ5,subQ7]),TDD([makeQuery(id+"F42.boolean.opBoolean","COPY",EDGE,{"disambiguationData":[TD([makeQuery(id+"F11.opLoft","SWEPT_FACE",FACE,{"disambiguationData":[OSD([sQuery(id+"F3.wireOp",EDGE,"E20.10.0"),subQ45,subQ44,sQuery(id+"F4.wireOp",EDGE,"E26.10.0"),subQ43,subQ42])]})])],"derivedFrom":subQ9})])]}),makeQuery(id+"F47.opFillet","BLEND_FACE",FACE,{"disambiguationData":[OSD([subQ5,subQ7]),TDD([makeQuery(id+"F42.boolean.opBoolean","COPY",EDGE,{"disambiguationData":[TD([makeQuery(id+"F12.opLoft","SWEPT_FACE",FACE,{"disambiguationData":[OSD([sQuery(id+"F3.wireOp",EDGE,"E20.9.0"),subQ41,subQ40,sQuery(id+"F4.wireOp",EDGE,"E26.9.0"),subQ39,subQ38])]})])],"derivedFrom":subQ9})])]}),makeQuery(id+"F47.opFillet","BLEND_FACE",FACE,{"disambiguationData":[OSD([subQ5,subQ7]),TDD([makeQuery(id+"F42.boolean.opBoolean","COPY",EDGE,{"disambiguationData":[TD([makeQuery(id+"F13.opLoft","SWEPT_FACE",FACE,{"disambiguationData":[OSD([sQuery(id+"F3.wireOp",EDGE,"E20.8.0"),subQ37,subQ36,sQuery(id+"F4.wireOp",EDGE,"E26.8.0"),subQ35,subQ34])]})])],"derivedFrom":subQ9})])]}),makeQuery(id+"F47.opFillet","BLEND_FACE",FACE,{"disambiguationData":[OSD([subQ5,subQ7]),TDD([makeQuery(id+"F42.boolean.opBoolean","COPY",EDGE,{"disambiguationData":[TD([makeQuery(id+"F14.opLoft","SWEPT_FACE",FACE,{"disambiguationData":[OSD([sQuery(id+"F3.wireOp",EDGE,"E20.7.0"),subQ33,subQ32,sQuery(id+"F4.wireOp",EDGE,"E26.7.0"),subQ31,subQ30])]})])],"derivedFrom":subQ9})])]}),makeQuery(id+"F47.opFillet","BLEND_FACE",FACE,{"disambiguationData":[OSD([subQ5,subQ7]),TDD([makeQuery(id+"F42.boolean.opBoolean","COPY",EDGE,{"disambiguationData":[TD([makeQuery(id+"F15.opLoft","SWEPT_FACE",FACE,{"disambiguationData":[OSD([sQuery(id+"F3.wireOp",EDGE,"E20.6.0"),subQ29,subQ28,sQuery(id+"F4.wireOp",EDGE,"E26.6.0"),subQ27,subQ26])]})])],"derivedFrom":subQ9})])]}),makeQuery(id+"F47.opFillet","BLEND_FACE",FACE,{"disambiguationData":[OSD([subQ5,subQ7]),TDD([makeQuery(id+"F42.boolean.opBoolean","COPY",EDGE,{"disambiguationData":[TD([makeQuery(id+"F16.opLoft","SWEPT_FACE",FACE,{"disambiguationData":[OSD([sQuery(id+"F3.wireOp",EDGE,"E20.5.0"),subQ25,subQ24,sQuery(id+"F4.wireOp",EDGE,"E26.5.0"),subQ23,subQ22])]})])],"derivedFrom":subQ9})])]}),makeQuery(id+"F47.opFillet","BLEND_FACE",FACE,{"disambiguationData":[OSD([subQ5,subQ7]),TDD([makeQuery(id+"F42.boolean.opBoolean","COPY",EDGE,{"disambiguationData":[TD([makeQuery(id+"F17.opLoft","SWEPT_FACE",FACE,{"disambiguationData":[OSD([sQuery(id+"F3.wireOp",EDGE,"E20.4.0"),subQ21,subQ20,sQuery(id+"F4.wireOp",EDGE,"E26.4.0"),subQ19,subQ18])]})])],"derivedFrom":subQ9})])]}),makeQuery(id+"F47.opFillet","BLEND_FACE",FACE,{"disambiguationData":[OSD([subQ5,subQ7]),TDD([makeQuery(id+"F42.boolean.opBoolean","COPY",EDGE,{"disambiguationData":[TD([makeQuery(id+"F18.opLoft","SWEPT_FACE",FACE,{"disambiguationData":[OSD([sQuery(id+"F3.wireOp",EDGE,"E20.3.0"),subQ17,subQ16,sQuery(id+"F4.wireOp",EDGE,"E26.3.0"),subQ15,subQ14])]})])],"derivedFrom":subQ9})])]}),makeQuery(id+"F47.opFillet","BLEND_FACE",FACE,{"disambiguationData":[OSD([subQ5,subQ7]),TDD([makeQuery(id+"F42.boolean.opBoolean","COPY",EDGE,{"disambiguationData":[TD([makeQuery(id+"F19.opLoft","SWEPT_FACE",FACE,{"disambiguationData":[OSD([sQuery(id+"F3.wireOp",EDGE,"E20.2.0"),subQ13,subQ12,sQuery(id+"F4.wireOp",EDGE,"E26.2.0"),subQ11,subQ10])]})])],"derivedFrom":subQ9})])]}),makeQuery(id+"F47.opFillet","BLEND_FACE",FACE,{"disambiguationData":[OSD([subQ5,subQ7]),TDD([makeQuery(id+"F42.boolean.opBoolean","COPY",EDGE,{"disambiguationData":[TD([makeQuery(id+"F20.opLoft","SWEPT_FACE",FACE,{"disambiguationData":[OSD([sQuery(id+"F3.wireOp",EDGE,"E20.1.0"),subQ4,subQ3,sQuery(id+"F4.wireOp",EDGE,"E26.1.0"),subQ2,subQ1])]})])],"derivedFrom":subQ9})])]})]});}
            var Q58;
            {var subQ0=makeQuery(id+"F40.opExtrude","CAP_FACE",FACE,{"disambiguationData":[OSD([sQuery(id+"F39.wireOp",EDGE,"E29"),sQuery(id+"F39.wireOp",EDGE,"E30")])],"isStart":false});var subQ1=sQuery(id+"F4.wireOp",EDGE,"E26.1.3");var subQ2=sQuery(id+"F4.wireOp",EDGE,"E26.1.2");var subQ3=sQuery(id+"F3.wireOp",EDGE,"E20.1.3");var subQ4=sQuery(id+"F3.wireOp",EDGE,"E20.1.1");var subQ5=sQuery(id+"F41.wireOp",EDGE,"E35");var subQ6=makeQuery(id+"F42.opRevolve","SWEPT_FACE",FACE,{"disambiguationData":[OSD([subQ5])]});var subQ7=sQuery(id+"F41.wireOp",EDGE,"E36");var subQ8=makeQuery(id+"F42.opRevolve","SWEPT_FACE",FACE,{"disambiguationData":[OSD([subQ7])]});var subQ9=makeQuery(id+"F42.opRevolve","SWEPT_EDGE",EDGE,{"disambiguationData":[OSD([subQ5,subQ7])]});var subQ10=sQuery(id+"F4.wireOp",EDGE,"E26.2.3");var subQ11=sQuery(id+"F4.wireOp",EDGE,"E26.2.2");var subQ12=sQuery(id+"F3.wireOp",EDGE,"E20.2.3");var subQ13=sQuery(id+"F3.wireOp",EDGE,"E20.2.1");var subQ14=sQuery(id+"F4.wireOp",EDGE,"E26.3.3");var subQ15=sQuery(id+"F4.wireOp",EDGE,"E26.3.2");var subQ16=sQuery(id+"F3.wireOp",EDGE,"E20.3.3");var subQ17=sQuery(id+"F3.wireOp",EDGE,"E20.3.1");var subQ18=sQuery(id+"F4.wireOp",EDGE,"E26.4.3");var subQ19=sQuery(id+"F4.wireOp",EDGE,"E26.4.2");var subQ20=sQuery(id+"F3.wireOp",EDGE,"E20.4.3");var subQ21=sQuery(id+"F3.wireOp",EDGE,"E20.4.1");var subQ22=sQuery(id+"F4.wireOp",EDGE,"E26.5.3");var subQ23=sQuery(id+"F4.wireOp",EDGE,"E26.5.2");var subQ24=sQuery(id+"F3.wireOp",EDGE,"E20.5.3");var subQ25=sQuery(id+"F3.wireOp",EDGE,"E20.5.1");var subQ26=sQuery(id+"F4.wireOp",EDGE,"E26.6.3");var subQ27=sQuery(id+"F4.wireOp",EDGE,"E26.6.2");var subQ28=sQuery(id+"F3.wireOp",EDGE,"E20.6.3");var subQ29=sQuery(id+"F3.wireOp",EDGE,"E20.6.1");var subQ30=sQuery(id+"F4.wireOp",EDGE,"E26.7.3");var subQ31=sQuery(id+"F4.wireOp",EDGE,"E26.7.2");var subQ32=sQuery(id+"F3.wireOp",EDGE,"E20.7.3");var subQ33=sQuery(id+"F3.wireOp",EDGE,"E20.7.1");var subQ34=sQuery(id+"F4.wireOp",EDGE,"E26.8.3");var subQ35=sQuery(id+"F4.wireOp",EDGE,"E26.8.2");var subQ36=sQuery(id+"F3.wireOp",EDGE,"E20.8.3");var subQ37=sQuery(id+"F3.wireOp",EDGE,"E20.8.1");var subQ38=sQuery(id+"F4.wireOp",EDGE,"E26.9.3");var subQ39=sQuery(id+"F4.wireOp",EDGE,"E26.9.2");var subQ40=sQuery(id+"F3.wireOp",EDGE,"E20.9.3");var subQ41=sQuery(id+"F3.wireOp",EDGE,"E20.9.1");var subQ42=sQuery(id+"F4.wireOp",EDGE,"E26.10.3");var subQ43=sQuery(id+"F4.wireOp",EDGE,"E26.10.2");var subQ44=sQuery(id+"F3.wireOp",EDGE,"E20.10.3");var subQ45=sQuery(id+"F3.wireOp",EDGE,"E20.10.1");var subQ46=sQuery(id+"F4.wireOp",EDGE,"E26.11.3");var subQ47=sQuery(id+"F4.wireOp",EDGE,"E26.11.2");var subQ48=sQuery(id+"F3.wireOp",EDGE,"E20.11.3");var subQ49=sQuery(id+"F3.wireOp",EDGE,"E20.11.1");var subQ50=sQuery(id+"F4.wireOp",EDGE,"E26.12.3");var subQ51=sQuery(id+"F4.wireOp",EDGE,"E26.12.2");var subQ52=sQuery(id+"F3.wireOp",EDGE,"E20.12.3");var subQ53=sQuery(id+"F3.wireOp",EDGE,"E20.12.1");var subQ55=makeQuery(id+"F9.opLoft","SWEPT_FACE",FACE,{"disambiguationData":[OSD([sQuery(id+"F3.wireOp",EDGE,"E20.12.0"),subQ53,subQ52,sQuery(id+"F4.wireOp",EDGE,"E26.12.0"),subQ51,subQ50])]});var subQ56=sQuery(id+"F4.wireOp",EDGE,"E26.13.3");var subQ57=sQuery(id+"F4.wireOp",EDGE,"E26.13.2");var subQ58=sQuery(id+"F3.wireOp",EDGE,"E20.13.3");var subQ59=sQuery(id+"F3.wireOp",EDGE,"E20.13.1");var subQ60=sQuery(id+"F4.wireOp",EDGE,"E26.14.3");var subQ61=sQuery(id+"F4.wireOp",EDGE,"E26.14.2");var subQ62=sQuery(id+"F3.wireOp",EDGE,"E20.14.3");var subQ63=sQuery(id+"F3.wireOp",EDGE,"E20.14.1");var subQ64=sQuery(id+"F4.wireOp",EDGE,"E26.15.3");var subQ65=sQuery(id+"F4.wireOp",EDGE,"E26.15.2");var subQ66=sQuery(id+"F3.wireOp",EDGE,"E20.15.3");var subQ67=sQuery(id+"F3.wireOp",EDGE,"E20.15.1");var subQ68=sQuery(id+"F4.wireOp",EDGE,"E23");var subQ69=sQuery(id+"F4.wireOp",EDGE,"E22");var subQ70=sQuery(id+"F3.wireOp",EDGE,"E18.top");var subQ71=sQuery(id+"F3.wireOp",EDGE,"E18.bottom");var subQ74=makeQuery(id+"F42.boolean.opBoolean","COPY",FACE,{"disambiguationData":[TD([subQ55])],"derivedFrom":subQ6});var subQ75=makeQuery(id+"F9.boolean.opBoolean","INTERSECT",EDGE,{"derivedFrom":[makeQuery(id+"F1.opRevolve","SWEPT_FACE",FACE,{"disambiguationData":[OSD([sQuery(id+"F0.wireOp",EDGE,"E4")])]}),subQ55]});Q58=makeQuery(id+"F48.opFillet","BLEND_EDGE",EDGE,{"blendedFrom":[makeQuery(id+"F47.opFillet","TWEAK_EDGE",EDGE,{"derivedFrom":[makeQuery(id+"F45.opFillet","BLEND_VERTEX",VERTEX,{"blendedFrom":[subQ75,subQ55,subQ74],"blendedInto":[subQ55,subQ74]}),makeQuery(id+"F45.opFillet","BLEND_VERTEX",VERTEX,{"blendedFrom":[subQ75,makeQuery(id+"F42.boolean.opBoolean","MERGE",FACE,{"derivedFrom":[subQ0,subQ8]}),subQ74],"blendedInto":[makeQuery(id+"F42.boolean.opBoolean","MERGE",FACE,{"derivedFrom":[subQ0,subQ8]}),subQ74]})]}),makeQuery(id+"F47.opFillet","BLEND_FACE",FACE,{"disambiguationData":[OSD([subQ5,subQ7]),TDD([makeQuery(id+"F42.boolean.opBoolean","COPY",EDGE,{"disambiguationData":[TD([makeQuery(id+"F5.opLoft","SWEPT_FACE",FACE,{"disambiguationData":[OSD([subQ71,subQ70,sQuery(id+"F3.wireOp",EDGE,"E18.left"),sQuery(id+"F4.wireOp",EDGE,"E21"),subQ69,subQ68])]})])],"derivedFrom":subQ9})])]}),makeQuery(id+"F47.opFillet","BLEND_FACE",FACE,{"disambiguationData":[OSD([subQ5,subQ7]),TDD([makeQuery(id+"F42.boolean.opBoolean","COPY",EDGE,{"disambiguationData":[TD([makeQuery(id+"F6.opLoft","SWEPT_FACE",FACE,{"disambiguationData":[OSD([sQuery(id+"F3.wireOp",EDGE,"E20.15.0"),subQ67,subQ66,sQuery(id+"F4.wireOp",EDGE,"E26.15.0"),subQ65,subQ64])]})])],"derivedFrom":subQ9})])]}),makeQuery(id+"F47.opFillet","BLEND_FACE",FACE,{"disambiguationData":[OSD([subQ5,subQ7]),TDD([makeQuery(id+"F42.boolean.opBoolean","COPY",EDGE,{"disambiguationData":[TD([makeQuery(id+"F7.opLoft","SWEPT_FACE",FACE,{"disambiguationData":[OSD([sQuery(id+"F3.wireOp",EDGE,"E20.14.0"),subQ63,subQ62,sQuery(id+"F4.wireOp",EDGE,"E26.14.0"),subQ61,subQ60])]})])],"derivedFrom":subQ9})])]}),makeQuery(id+"F47.opFillet","BLEND_FACE",FACE,{"disambiguationData":[OSD([subQ5,subQ7]),TDD([makeQuery(id+"F42.boolean.opBoolean","COPY",EDGE,{"disambiguationData":[TD([makeQuery(id+"F8.opLoft","SWEPT_FACE",FACE,{"disambiguationData":[OSD([sQuery(id+"F3.wireOp",EDGE,"E20.13.0"),subQ59,subQ58,sQuery(id+"F4.wireOp",EDGE,"E26.13.0"),subQ57,subQ56])]})])],"derivedFrom":subQ9})])]}),makeQuery(id+"F47.opFillet","BLEND_FACE",FACE,{"disambiguationData":[OSD([subQ5,subQ7]),TDD([makeQuery(id+"F42.boolean.opBoolean","COPY",EDGE,{"disambiguationData":[TD([subQ55])],"derivedFrom":subQ9})])]}),makeQuery(id+"F47.opFillet","BLEND_FACE",FACE,{"disambiguationData":[OSD([subQ5,subQ7]),TDD([makeQuery(id+"F42.boolean.opBoolean","COPY",EDGE,{"disambiguationData":[TD([makeQuery(id+"F10.opLoft","SWEPT_FACE",FACE,{"disambiguationData":[OSD([sQuery(id+"F3.wireOp",EDGE,"E20.11.0"),subQ49,subQ48,sQuery(id+"F4.wireOp",EDGE,"E26.11.0"),subQ47,subQ46])]})])],"derivedFrom":subQ9})])]}),makeQuery(id+"F47.opFillet","BLEND_FACE",FACE,{"disambiguationData":[OSD([subQ5,subQ7]),TDD([makeQuery(id+"F42.boolean.opBoolean","COPY",EDGE,{"disambiguationData":[TD([makeQuery(id+"F11.opLoft","SWEPT_FACE",FACE,{"disambiguationData":[OSD([sQuery(id+"F3.wireOp",EDGE,"E20.10.0"),subQ45,subQ44,sQuery(id+"F4.wireOp",EDGE,"E26.10.0"),subQ43,subQ42])]})])],"derivedFrom":subQ9})])]}),makeQuery(id+"F47.opFillet","BLEND_FACE",FACE,{"disambiguationData":[OSD([subQ5,subQ7]),TDD([makeQuery(id+"F42.boolean.opBoolean","COPY",EDGE,{"disambiguationData":[TD([makeQuery(id+"F12.opLoft","SWEPT_FACE",FACE,{"disambiguationData":[OSD([sQuery(id+"F3.wireOp",EDGE,"E20.9.0"),subQ41,subQ40,sQuery(id+"F4.wireOp",EDGE,"E26.9.0"),subQ39,subQ38])]})])],"derivedFrom":subQ9})])]}),makeQuery(id+"F47.opFillet","BLEND_FACE",FACE,{"disambiguationData":[OSD([subQ5,subQ7]),TDD([makeQuery(id+"F42.boolean.opBoolean","COPY",EDGE,{"disambiguationData":[TD([makeQuery(id+"F13.opLoft","SWEPT_FACE",FACE,{"disambiguationData":[OSD([sQuery(id+"F3.wireOp",EDGE,"E20.8.0"),subQ37,subQ36,sQuery(id+"F4.wireOp",EDGE,"E26.8.0"),subQ35,subQ34])]})])],"derivedFrom":subQ9})])]}),makeQuery(id+"F47.opFillet","BLEND_FACE",FACE,{"disambiguationData":[OSD([subQ5,subQ7]),TDD([makeQuery(id+"F42.boolean.opBoolean","COPY",EDGE,{"disambiguationData":[TD([makeQuery(id+"F14.opLoft","SWEPT_FACE",FACE,{"disambiguationData":[OSD([sQuery(id+"F3.wireOp",EDGE,"E20.7.0"),subQ33,subQ32,sQuery(id+"F4.wireOp",EDGE,"E26.7.0"),subQ31,subQ30])]})])],"derivedFrom":subQ9})])]}),makeQuery(id+"F47.opFillet","BLEND_FACE",FACE,{"disambiguationData":[OSD([subQ5,subQ7]),TDD([makeQuery(id+"F42.boolean.opBoolean","COPY",EDGE,{"disambiguationData":[TD([makeQuery(id+"F15.opLoft","SWEPT_FACE",FACE,{"disambiguationData":[OSD([sQuery(id+"F3.wireOp",EDGE,"E20.6.0"),subQ29,subQ28,sQuery(id+"F4.wireOp",EDGE,"E26.6.0"),subQ27,subQ26])]})])],"derivedFrom":subQ9})])]}),makeQuery(id+"F47.opFillet","BLEND_FACE",FACE,{"disambiguationData":[OSD([subQ5,subQ7]),TDD([makeQuery(id+"F42.boolean.opBoolean","COPY",EDGE,{"disambiguationData":[TD([makeQuery(id+"F16.opLoft","SWEPT_FACE",FACE,{"disambiguationData":[OSD([sQuery(id+"F3.wireOp",EDGE,"E20.5.0"),subQ25,subQ24,sQuery(id+"F4.wireOp",EDGE,"E26.5.0"),subQ23,subQ22])]})])],"derivedFrom":subQ9})])]}),makeQuery(id+"F47.opFillet","BLEND_FACE",FACE,{"disambiguationData":[OSD([subQ5,subQ7]),TDD([makeQuery(id+"F42.boolean.opBoolean","COPY",EDGE,{"disambiguationData":[TD([makeQuery(id+"F17.opLoft","SWEPT_FACE",FACE,{"disambiguationData":[OSD([sQuery(id+"F3.wireOp",EDGE,"E20.4.0"),subQ21,subQ20,sQuery(id+"F4.wireOp",EDGE,"E26.4.0"),subQ19,subQ18])]})])],"derivedFrom":subQ9})])]}),makeQuery(id+"F47.opFillet","BLEND_FACE",FACE,{"disambiguationData":[OSD([subQ5,subQ7]),TDD([makeQuery(id+"F42.boolean.opBoolean","COPY",EDGE,{"disambiguationData":[TD([makeQuery(id+"F18.opLoft","SWEPT_FACE",FACE,{"disambiguationData":[OSD([sQuery(id+"F3.wireOp",EDGE,"E20.3.0"),subQ17,subQ16,sQuery(id+"F4.wireOp",EDGE,"E26.3.0"),subQ15,subQ14])]})])],"derivedFrom":subQ9})])]}),makeQuery(id+"F47.opFillet","BLEND_FACE",FACE,{"disambiguationData":[OSD([subQ5,subQ7]),TDD([makeQuery(id+"F42.boolean.opBoolean","COPY",EDGE,{"disambiguationData":[TD([makeQuery(id+"F19.opLoft","SWEPT_FACE",FACE,{"disambiguationData":[OSD([sQuery(id+"F3.wireOp",EDGE,"E20.2.0"),subQ13,subQ12,sQuery(id+"F4.wireOp",EDGE,"E26.2.0"),subQ11,subQ10])]})])],"derivedFrom":subQ9})])]}),makeQuery(id+"F47.opFillet","BLEND_FACE",FACE,{"disambiguationData":[OSD([subQ5,subQ7]),TDD([makeQuery(id+"F42.boolean.opBoolean","COPY",EDGE,{"disambiguationData":[TD([makeQuery(id+"F20.opLoft","SWEPT_FACE",FACE,{"disambiguationData":[OSD([sQuery(id+"F3.wireOp",EDGE,"E20.1.0"),subQ4,subQ3,sQuery(id+"F4.wireOp",EDGE,"E26.1.0"),subQ2,subQ1])]})])],"derivedFrom":subQ9})])]})],"blendedInto":[makeQuery(id+"F47.opFillet","BLEND_FACE",FACE,{"disambiguationData":[OSD([subQ5,subQ7]),TDD([makeQuery(id+"F42.boolean.opBoolean","COPY",EDGE,{"disambiguationData":[TD([makeQuery(id+"F5.opLoft","SWEPT_FACE",FACE,{"disambiguationData":[OSD([subQ71,subQ70,sQuery(id+"F3.wireOp",EDGE,"E18.left"),sQuery(id+"F4.wireOp",EDGE,"E21"),subQ69,subQ68])]})])],"derivedFrom":subQ9})])]}),makeQuery(id+"F47.opFillet","BLEND_FACE",FACE,{"disambiguationData":[OSD([subQ5,subQ7]),TDD([makeQuery(id+"F42.boolean.opBoolean","COPY",EDGE,{"disambiguationData":[TD([makeQuery(id+"F6.opLoft","SWEPT_FACE",FACE,{"disambiguationData":[OSD([sQuery(id+"F3.wireOp",EDGE,"E20.15.0"),subQ67,subQ66,sQuery(id+"F4.wireOp",EDGE,"E26.15.0"),subQ65,subQ64])]})])],"derivedFrom":subQ9})])]}),makeQuery(id+"F47.opFillet","BLEND_FACE",FACE,{"disambiguationData":[OSD([subQ5,subQ7]),TDD([makeQuery(id+"F42.boolean.opBoolean","COPY",EDGE,{"disambiguationData":[TD([makeQuery(id+"F7.opLoft","SWEPT_FACE",FACE,{"disambiguationData":[OSD([sQuery(id+"F3.wireOp",EDGE,"E20.14.0"),subQ63,subQ62,sQuery(id+"F4.wireOp",EDGE,"E26.14.0"),subQ61,subQ60])]})])],"derivedFrom":subQ9})])]}),makeQuery(id+"F47.opFillet","BLEND_FACE",FACE,{"disambiguationData":[OSD([subQ5,subQ7]),TDD([makeQuery(id+"F42.boolean.opBoolean","COPY",EDGE,{"disambiguationData":[TD([makeQuery(id+"F8.opLoft","SWEPT_FACE",FACE,{"disambiguationData":[OSD([sQuery(id+"F3.wireOp",EDGE,"E20.13.0"),subQ59,subQ58,sQuery(id+"F4.wireOp",EDGE,"E26.13.0"),subQ57,subQ56])]})])],"derivedFrom":subQ9})])]}),makeQuery(id+"F47.opFillet","BLEND_FACE",FACE,{"disambiguationData":[OSD([subQ5,subQ7]),TDD([makeQuery(id+"F42.boolean.opBoolean","COPY",EDGE,{"disambiguationData":[TD([subQ55])],"derivedFrom":subQ9})])]}),makeQuery(id+"F47.opFillet","BLEND_FACE",FACE,{"disambiguationData":[OSD([subQ5,subQ7]),TDD([makeQuery(id+"F42.boolean.opBoolean","COPY",EDGE,{"disambiguationData":[TD([makeQuery(id+"F10.opLoft","SWEPT_FACE",FACE,{"disambiguationData":[OSD([sQuery(id+"F3.wireOp",EDGE,"E20.11.0"),subQ49,subQ48,sQuery(id+"F4.wireOp",EDGE,"E26.11.0"),subQ47,subQ46])]})])],"derivedFrom":subQ9})])]}),makeQuery(id+"F47.opFillet","BLEND_FACE",FACE,{"disambiguationData":[OSD([subQ5,subQ7]),TDD([makeQuery(id+"F42.boolean.opBoolean","COPY",EDGE,{"disambiguationData":[TD([makeQuery(id+"F11.opLoft","SWEPT_FACE",FACE,{"disambiguationData":[OSD([sQuery(id+"F3.wireOp",EDGE,"E20.10.0"),subQ45,subQ44,sQuery(id+"F4.wireOp",EDGE,"E26.10.0"),subQ43,subQ42])]})])],"derivedFrom":subQ9})])]}),makeQuery(id+"F47.opFillet","BLEND_FACE",FACE,{"disambiguationData":[OSD([subQ5,subQ7]),TDD([makeQuery(id+"F42.boolean.opBoolean","COPY",EDGE,{"disambiguationData":[TD([makeQuery(id+"F12.opLoft","SWEPT_FACE",FACE,{"disambiguationData":[OSD([sQuery(id+"F3.wireOp",EDGE,"E20.9.0"),subQ41,subQ40,sQuery(id+"F4.wireOp",EDGE,"E26.9.0"),subQ39,subQ38])]})])],"derivedFrom":subQ9})])]}),makeQuery(id+"F47.opFillet","BLEND_FACE",FACE,{"disambiguationData":[OSD([subQ5,subQ7]),TDD([makeQuery(id+"F42.boolean.opBoolean","COPY",EDGE,{"disambiguationData":[TD([makeQuery(id+"F13.opLoft","SWEPT_FACE",FACE,{"disambiguationData":[OSD([sQuery(id+"F3.wireOp",EDGE,"E20.8.0"),subQ37,subQ36,sQuery(id+"F4.wireOp",EDGE,"E26.8.0"),subQ35,subQ34])]})])],"derivedFrom":subQ9})])]}),makeQuery(id+"F47.opFillet","BLEND_FACE",FACE,{"disambiguationData":[OSD([subQ5,subQ7]),TDD([makeQuery(id+"F42.boolean.opBoolean","COPY",EDGE,{"disambiguationData":[TD([makeQuery(id+"F14.opLoft","SWEPT_FACE",FACE,{"disambiguationData":[OSD([sQuery(id+"F3.wireOp",EDGE,"E20.7.0"),subQ33,subQ32,sQuery(id+"F4.wireOp",EDGE,"E26.7.0"),subQ31,subQ30])]})])],"derivedFrom":subQ9})])]}),makeQuery(id+"F47.opFillet","BLEND_FACE",FACE,{"disambiguationData":[OSD([subQ5,subQ7]),TDD([makeQuery(id+"F42.boolean.opBoolean","COPY",EDGE,{"disambiguationData":[TD([makeQuery(id+"F15.opLoft","SWEPT_FACE",FACE,{"disambiguationData":[OSD([sQuery(id+"F3.wireOp",EDGE,"E20.6.0"),subQ29,subQ28,sQuery(id+"F4.wireOp",EDGE,"E26.6.0"),subQ27,subQ26])]})])],"derivedFrom":subQ9})])]}),makeQuery(id+"F47.opFillet","BLEND_FACE",FACE,{"disambiguationData":[OSD([subQ5,subQ7]),TDD([makeQuery(id+"F42.boolean.opBoolean","COPY",EDGE,{"disambiguationData":[TD([makeQuery(id+"F16.opLoft","SWEPT_FACE",FACE,{"disambiguationData":[OSD([sQuery(id+"F3.wireOp",EDGE,"E20.5.0"),subQ25,subQ24,sQuery(id+"F4.wireOp",EDGE,"E26.5.0"),subQ23,subQ22])]})])],"derivedFrom":subQ9})])]}),makeQuery(id+"F47.opFillet","BLEND_FACE",FACE,{"disambiguationData":[OSD([subQ5,subQ7]),TDD([makeQuery(id+"F42.boolean.opBoolean","COPY",EDGE,{"disambiguationData":[TD([makeQuery(id+"F17.opLoft","SWEPT_FACE",FACE,{"disambiguationData":[OSD([sQuery(id+"F3.wireOp",EDGE,"E20.4.0"),subQ21,subQ20,sQuery(id+"F4.wireOp",EDGE,"E26.4.0"),subQ19,subQ18])]})])],"derivedFrom":subQ9})])]}),makeQuery(id+"F47.opFillet","BLEND_FACE",FACE,{"disambiguationData":[OSD([subQ5,subQ7]),TDD([makeQuery(id+"F42.boolean.opBoolean","COPY",EDGE,{"disambiguationData":[TD([makeQuery(id+"F18.opLoft","SWEPT_FACE",FACE,{"disambiguationData":[OSD([sQuery(id+"F3.wireOp",EDGE,"E20.3.0"),subQ17,subQ16,sQuery(id+"F4.wireOp",EDGE,"E26.3.0"),subQ15,subQ14])]})])],"derivedFrom":subQ9})])]}),makeQuery(id+"F47.opFillet","BLEND_FACE",FACE,{"disambiguationData":[OSD([subQ5,subQ7]),TDD([makeQuery(id+"F42.boolean.opBoolean","COPY",EDGE,{"disambiguationData":[TD([makeQuery(id+"F19.opLoft","SWEPT_FACE",FACE,{"disambiguationData":[OSD([sQuery(id+"F3.wireOp",EDGE,"E20.2.0"),subQ13,subQ12,sQuery(id+"F4.wireOp",EDGE,"E26.2.0"),subQ11,subQ10])]})])],"derivedFrom":subQ9})])]}),makeQuery(id+"F47.opFillet","BLEND_FACE",FACE,{"disambiguationData":[OSD([subQ5,subQ7]),TDD([makeQuery(id+"F42.boolean.opBoolean","COPY",EDGE,{"disambiguationData":[TD([makeQuery(id+"F20.opLoft","SWEPT_FACE",FACE,{"disambiguationData":[OSD([sQuery(id+"F3.wireOp",EDGE,"E20.1.0"),subQ4,subQ3,sQuery(id+"F4.wireOp",EDGE,"E26.1.0"),subQ2,subQ1])]})])],"derivedFrom":subQ9})])]})]});}
            var Q59;
            {var subQ0=makeQuery(id+"F40.opExtrude","CAP_FACE",FACE,{"disambiguationData":[OSD([sQuery(id+"F39.wireOp",EDGE,"E29"),sQuery(id+"F39.wireOp",EDGE,"E30")])],"isStart":false});var subQ1=sQuery(id+"F4.wireOp",EDGE,"E26.1.3");var subQ2=sQuery(id+"F4.wireOp",EDGE,"E26.1.2");var subQ3=sQuery(id+"F3.wireOp",EDGE,"E20.1.3");var subQ4=sQuery(id+"F3.wireOp",EDGE,"E20.1.1");var subQ5=sQuery(id+"F41.wireOp",EDGE,"E35");var subQ6=makeQuery(id+"F42.opRevolve","SWEPT_FACE",FACE,{"disambiguationData":[OSD([subQ5])]});var subQ7=sQuery(id+"F41.wireOp",EDGE,"E36");var subQ8=makeQuery(id+"F42.opRevolve","SWEPT_FACE",FACE,{"disambiguationData":[OSD([subQ7])]});var subQ9=makeQuery(id+"F42.opRevolve","SWEPT_EDGE",EDGE,{"disambiguationData":[OSD([subQ5,subQ7])]});var subQ10=sQuery(id+"F4.wireOp",EDGE,"E26.2.3");var subQ11=sQuery(id+"F4.wireOp",EDGE,"E26.2.2");var subQ12=sQuery(id+"F3.wireOp",EDGE,"E20.2.3");var subQ13=sQuery(id+"F3.wireOp",EDGE,"E20.2.1");var subQ14=sQuery(id+"F4.wireOp",EDGE,"E26.3.3");var subQ15=sQuery(id+"F4.wireOp",EDGE,"E26.3.2");var subQ16=sQuery(id+"F3.wireOp",EDGE,"E20.3.3");var subQ17=sQuery(id+"F3.wireOp",EDGE,"E20.3.1");var subQ18=sQuery(id+"F4.wireOp",EDGE,"E26.4.3");var subQ19=sQuery(id+"F4.wireOp",EDGE,"E26.4.2");var subQ20=sQuery(id+"F3.wireOp",EDGE,"E20.4.3");var subQ21=sQuery(id+"F3.wireOp",EDGE,"E20.4.1");var subQ22=sQuery(id+"F4.wireOp",EDGE,"E26.5.3");var subQ23=sQuery(id+"F4.wireOp",EDGE,"E26.5.2");var subQ24=sQuery(id+"F3.wireOp",EDGE,"E20.5.3");var subQ25=sQuery(id+"F3.wireOp",EDGE,"E20.5.1");var subQ26=sQuery(id+"F4.wireOp",EDGE,"E26.6.3");var subQ27=sQuery(id+"F4.wireOp",EDGE,"E26.6.2");var subQ28=sQuery(id+"F3.wireOp",EDGE,"E20.6.3");var subQ29=sQuery(id+"F3.wireOp",EDGE,"E20.6.1");var subQ30=sQuery(id+"F4.wireOp",EDGE,"E26.7.3");var subQ31=sQuery(id+"F4.wireOp",EDGE,"E26.7.2");var subQ32=sQuery(id+"F3.wireOp",EDGE,"E20.7.3");var subQ33=sQuery(id+"F3.wireOp",EDGE,"E20.7.1");var subQ34=sQuery(id+"F4.wireOp",EDGE,"E26.8.3");var subQ35=sQuery(id+"F4.wireOp",EDGE,"E26.8.2");var subQ36=sQuery(id+"F3.wireOp",EDGE,"E20.8.3");var subQ37=sQuery(id+"F3.wireOp",EDGE,"E20.8.1");var subQ38=sQuery(id+"F4.wireOp",EDGE,"E26.9.3");var subQ39=sQuery(id+"F4.wireOp",EDGE,"E26.9.2");var subQ40=sQuery(id+"F3.wireOp",EDGE,"E20.9.3");var subQ41=sQuery(id+"F3.wireOp",EDGE,"E20.9.1");var subQ42=sQuery(id+"F4.wireOp",EDGE,"E26.10.3");var subQ43=sQuery(id+"F4.wireOp",EDGE,"E26.10.2");var subQ44=sQuery(id+"F3.wireOp",EDGE,"E20.10.3");var subQ45=sQuery(id+"F3.wireOp",EDGE,"E20.10.1");var subQ46=sQuery(id+"F4.wireOp",EDGE,"E26.11.3");var subQ47=sQuery(id+"F4.wireOp",EDGE,"E26.11.2");var subQ48=sQuery(id+"F3.wireOp",EDGE,"E20.11.3");var subQ49=sQuery(id+"F3.wireOp",EDGE,"E20.11.1");var subQ51=makeQuery(id+"F10.opLoft","SWEPT_FACE",FACE,{"disambiguationData":[OSD([sQuery(id+"F3.wireOp",EDGE,"E20.11.0"),subQ49,subQ48,sQuery(id+"F4.wireOp",EDGE,"E26.11.0"),subQ47,subQ46])]});var subQ52=sQuery(id+"F4.wireOp",EDGE,"E26.12.3");var subQ53=sQuery(id+"F4.wireOp",EDGE,"E26.12.2");var subQ54=sQuery(id+"F3.wireOp",EDGE,"E20.12.3");var subQ55=sQuery(id+"F3.wireOp",EDGE,"E20.12.1");var subQ56=sQuery(id+"F4.wireOp",EDGE,"E26.13.3");var subQ57=sQuery(id+"F4.wireOp",EDGE,"E26.13.2");var subQ58=sQuery(id+"F3.wireOp",EDGE,"E20.13.3");var subQ59=sQuery(id+"F3.wireOp",EDGE,"E20.13.1");var subQ60=sQuery(id+"F4.wireOp",EDGE,"E26.14.3");var subQ61=sQuery(id+"F4.wireOp",EDGE,"E26.14.2");var subQ62=sQuery(id+"F3.wireOp",EDGE,"E20.14.3");var subQ63=sQuery(id+"F3.wireOp",EDGE,"E20.14.1");var subQ64=sQuery(id+"F4.wireOp",EDGE,"E26.15.3");var subQ65=sQuery(id+"F4.wireOp",EDGE,"E26.15.2");var subQ66=sQuery(id+"F3.wireOp",EDGE,"E20.15.3");var subQ67=sQuery(id+"F3.wireOp",EDGE,"E20.15.1");var subQ68=sQuery(id+"F4.wireOp",EDGE,"E23");var subQ69=sQuery(id+"F4.wireOp",EDGE,"E22");var subQ70=sQuery(id+"F3.wireOp",EDGE,"E18.top");var subQ71=sQuery(id+"F3.wireOp",EDGE,"E18.bottom");var subQ74=makeQuery(id+"F42.boolean.opBoolean","COPY",FACE,{"disambiguationData":[TD([subQ51])],"derivedFrom":subQ6});var subQ75=makeQuery(id+"F10.boolean.opBoolean","INTERSECT",EDGE,{"derivedFrom":[makeQuery(id+"F1.opRevolve","SWEPT_FACE",FACE,{"disambiguationData":[OSD([sQuery(id+"F0.wireOp",EDGE,"E4")])]}),subQ51]});Q59=makeQuery(id+"F48.opFillet","BLEND_EDGE",EDGE,{"blendedFrom":[makeQuery(id+"F47.opFillet","TWEAK_EDGE",EDGE,{"derivedFrom":[makeQuery(id+"F45.opFillet","BLEND_VERTEX",VERTEX,{"blendedFrom":[subQ75,subQ51,subQ74],"blendedInto":[subQ51,subQ74]}),makeQuery(id+"F45.opFillet","BLEND_VERTEX",VERTEX,{"blendedFrom":[subQ75,makeQuery(id+"F42.boolean.opBoolean","MERGE",FACE,{"derivedFrom":[subQ0,subQ8]}),subQ74],"blendedInto":[makeQuery(id+"F42.boolean.opBoolean","MERGE",FACE,{"derivedFrom":[subQ0,subQ8]}),subQ74]})]}),makeQuery(id+"F47.opFillet","BLEND_FACE",FACE,{"disambiguationData":[OSD([subQ5,subQ7]),TDD([makeQuery(id+"F42.boolean.opBoolean","COPY",EDGE,{"disambiguationData":[TD([makeQuery(id+"F5.opLoft","SWEPT_FACE",FACE,{"disambiguationData":[OSD([subQ71,subQ70,sQuery(id+"F3.wireOp",EDGE,"E18.left"),sQuery(id+"F4.wireOp",EDGE,"E21"),subQ69,subQ68])]})])],"derivedFrom":subQ9})])]}),makeQuery(id+"F47.opFillet","BLEND_FACE",FACE,{"disambiguationData":[OSD([subQ5,subQ7]),TDD([makeQuery(id+"F42.boolean.opBoolean","COPY",EDGE,{"disambiguationData":[TD([makeQuery(id+"F6.opLoft","SWEPT_FACE",FACE,{"disambiguationData":[OSD([sQuery(id+"F3.wireOp",EDGE,"E20.15.0"),subQ67,subQ66,sQuery(id+"F4.wireOp",EDGE,"E26.15.0"),subQ65,subQ64])]})])],"derivedFrom":subQ9})])]}),makeQuery(id+"F47.opFillet","BLEND_FACE",FACE,{"disambiguationData":[OSD([subQ5,subQ7]),TDD([makeQuery(id+"F42.boolean.opBoolean","COPY",EDGE,{"disambiguationData":[TD([makeQuery(id+"F7.opLoft","SWEPT_FACE",FACE,{"disambiguationData":[OSD([sQuery(id+"F3.wireOp",EDGE,"E20.14.0"),subQ63,subQ62,sQuery(id+"F4.wireOp",EDGE,"E26.14.0"),subQ61,subQ60])]})])],"derivedFrom":subQ9})])]}),makeQuery(id+"F47.opFillet","BLEND_FACE",FACE,{"disambiguationData":[OSD([subQ5,subQ7]),TDD([makeQuery(id+"F42.boolean.opBoolean","COPY",EDGE,{"disambiguationData":[TD([makeQuery(id+"F8.opLoft","SWEPT_FACE",FACE,{"disambiguationData":[OSD([sQuery(id+"F3.wireOp",EDGE,"E20.13.0"),subQ59,subQ58,sQuery(id+"F4.wireOp",EDGE,"E26.13.0"),subQ57,subQ56])]})])],"derivedFrom":subQ9})])]}),makeQuery(id+"F47.opFillet","BLEND_FACE",FACE,{"disambiguationData":[OSD([subQ5,subQ7]),TDD([makeQuery(id+"F42.boolean.opBoolean","COPY",EDGE,{"disambiguationData":[TD([makeQuery(id+"F9.opLoft","SWEPT_FACE",FACE,{"disambiguationData":[OSD([sQuery(id+"F3.wireOp",EDGE,"E20.12.0"),subQ55,subQ54,sQuery(id+"F4.wireOp",EDGE,"E26.12.0"),subQ53,subQ52])]})])],"derivedFrom":subQ9})])]}),makeQuery(id+"F47.opFillet","BLEND_FACE",FACE,{"disambiguationData":[OSD([subQ5,subQ7]),TDD([makeQuery(id+"F42.boolean.opBoolean","COPY",EDGE,{"disambiguationData":[TD([subQ51])],"derivedFrom":subQ9})])]}),makeQuery(id+"F47.opFillet","BLEND_FACE",FACE,{"disambiguationData":[OSD([subQ5,subQ7]),TDD([makeQuery(id+"F42.boolean.opBoolean","COPY",EDGE,{"disambiguationData":[TD([makeQuery(id+"F11.opLoft","SWEPT_FACE",FACE,{"disambiguationData":[OSD([sQuery(id+"F3.wireOp",EDGE,"E20.10.0"),subQ45,subQ44,sQuery(id+"F4.wireOp",EDGE,"E26.10.0"),subQ43,subQ42])]})])],"derivedFrom":subQ9})])]}),makeQuery(id+"F47.opFillet","BLEND_FACE",FACE,{"disambiguationData":[OSD([subQ5,subQ7]),TDD([makeQuery(id+"F42.boolean.opBoolean","COPY",EDGE,{"disambiguationData":[TD([makeQuery(id+"F12.opLoft","SWEPT_FACE",FACE,{"disambiguationData":[OSD([sQuery(id+"F3.wireOp",EDGE,"E20.9.0"),subQ41,subQ40,sQuery(id+"F4.wireOp",EDGE,"E26.9.0"),subQ39,subQ38])]})])],"derivedFrom":subQ9})])]}),makeQuery(id+"F47.opFillet","BLEND_FACE",FACE,{"disambiguationData":[OSD([subQ5,subQ7]),TDD([makeQuery(id+"F42.boolean.opBoolean","COPY",EDGE,{"disambiguationData":[TD([makeQuery(id+"F13.opLoft","SWEPT_FACE",FACE,{"disambiguationData":[OSD([sQuery(id+"F3.wireOp",EDGE,"E20.8.0"),subQ37,subQ36,sQuery(id+"F4.wireOp",EDGE,"E26.8.0"),subQ35,subQ34])]})])],"derivedFrom":subQ9})])]}),makeQuery(id+"F47.opFillet","BLEND_FACE",FACE,{"disambiguationData":[OSD([subQ5,subQ7]),TDD([makeQuery(id+"F42.boolean.opBoolean","COPY",EDGE,{"disambiguationData":[TD([makeQuery(id+"F14.opLoft","SWEPT_FACE",FACE,{"disambiguationData":[OSD([sQuery(id+"F3.wireOp",EDGE,"E20.7.0"),subQ33,subQ32,sQuery(id+"F4.wireOp",EDGE,"E26.7.0"),subQ31,subQ30])]})])],"derivedFrom":subQ9})])]}),makeQuery(id+"F47.opFillet","BLEND_FACE",FACE,{"disambiguationData":[OSD([subQ5,subQ7]),TDD([makeQuery(id+"F42.boolean.opBoolean","COPY",EDGE,{"disambiguationData":[TD([makeQuery(id+"F15.opLoft","SWEPT_FACE",FACE,{"disambiguationData":[OSD([sQuery(id+"F3.wireOp",EDGE,"E20.6.0"),subQ29,subQ28,sQuery(id+"F4.wireOp",EDGE,"E26.6.0"),subQ27,subQ26])]})])],"derivedFrom":subQ9})])]}),makeQuery(id+"F47.opFillet","BLEND_FACE",FACE,{"disambiguationData":[OSD([subQ5,subQ7]),TDD([makeQuery(id+"F42.boolean.opBoolean","COPY",EDGE,{"disambiguationData":[TD([makeQuery(id+"F16.opLoft","SWEPT_FACE",FACE,{"disambiguationData":[OSD([sQuery(id+"F3.wireOp",EDGE,"E20.5.0"),subQ25,subQ24,sQuery(id+"F4.wireOp",EDGE,"E26.5.0"),subQ23,subQ22])]})])],"derivedFrom":subQ9})])]}),makeQuery(id+"F47.opFillet","BLEND_FACE",FACE,{"disambiguationData":[OSD([subQ5,subQ7]),TDD([makeQuery(id+"F42.boolean.opBoolean","COPY",EDGE,{"disambiguationData":[TD([makeQuery(id+"F17.opLoft","SWEPT_FACE",FACE,{"disambiguationData":[OSD([sQuery(id+"F3.wireOp",EDGE,"E20.4.0"),subQ21,subQ20,sQuery(id+"F4.wireOp",EDGE,"E26.4.0"),subQ19,subQ18])]})])],"derivedFrom":subQ9})])]}),makeQuery(id+"F47.opFillet","BLEND_FACE",FACE,{"disambiguationData":[OSD([subQ5,subQ7]),TDD([makeQuery(id+"F42.boolean.opBoolean","COPY",EDGE,{"disambiguationData":[TD([makeQuery(id+"F18.opLoft","SWEPT_FACE",FACE,{"disambiguationData":[OSD([sQuery(id+"F3.wireOp",EDGE,"E20.3.0"),subQ17,subQ16,sQuery(id+"F4.wireOp",EDGE,"E26.3.0"),subQ15,subQ14])]})])],"derivedFrom":subQ9})])]}),makeQuery(id+"F47.opFillet","BLEND_FACE",FACE,{"disambiguationData":[OSD([subQ5,subQ7]),TDD([makeQuery(id+"F42.boolean.opBoolean","COPY",EDGE,{"disambiguationData":[TD([makeQuery(id+"F19.opLoft","SWEPT_FACE",FACE,{"disambiguationData":[OSD([sQuery(id+"F3.wireOp",EDGE,"E20.2.0"),subQ13,subQ12,sQuery(id+"F4.wireOp",EDGE,"E26.2.0"),subQ11,subQ10])]})])],"derivedFrom":subQ9})])]}),makeQuery(id+"F47.opFillet","BLEND_FACE",FACE,{"disambiguationData":[OSD([subQ5,subQ7]),TDD([makeQuery(id+"F42.boolean.opBoolean","COPY",EDGE,{"disambiguationData":[TD([makeQuery(id+"F20.opLoft","SWEPT_FACE",FACE,{"disambiguationData":[OSD([sQuery(id+"F3.wireOp",EDGE,"E20.1.0"),subQ4,subQ3,sQuery(id+"F4.wireOp",EDGE,"E26.1.0"),subQ2,subQ1])]})])],"derivedFrom":subQ9})])]})],"blendedInto":[makeQuery(id+"F47.opFillet","BLEND_FACE",FACE,{"disambiguationData":[OSD([subQ5,subQ7]),TDD([makeQuery(id+"F42.boolean.opBoolean","COPY",EDGE,{"disambiguationData":[TD([makeQuery(id+"F5.opLoft","SWEPT_FACE",FACE,{"disambiguationData":[OSD([subQ71,subQ70,sQuery(id+"F3.wireOp",EDGE,"E18.left"),sQuery(id+"F4.wireOp",EDGE,"E21"),subQ69,subQ68])]})])],"derivedFrom":subQ9})])]}),makeQuery(id+"F47.opFillet","BLEND_FACE",FACE,{"disambiguationData":[OSD([subQ5,subQ7]),TDD([makeQuery(id+"F42.boolean.opBoolean","COPY",EDGE,{"disambiguationData":[TD([makeQuery(id+"F6.opLoft","SWEPT_FACE",FACE,{"disambiguationData":[OSD([sQuery(id+"F3.wireOp",EDGE,"E20.15.0"),subQ67,subQ66,sQuery(id+"F4.wireOp",EDGE,"E26.15.0"),subQ65,subQ64])]})])],"derivedFrom":subQ9})])]}),makeQuery(id+"F47.opFillet","BLEND_FACE",FACE,{"disambiguationData":[OSD([subQ5,subQ7]),TDD([makeQuery(id+"F42.boolean.opBoolean","COPY",EDGE,{"disambiguationData":[TD([makeQuery(id+"F7.opLoft","SWEPT_FACE",FACE,{"disambiguationData":[OSD([sQuery(id+"F3.wireOp",EDGE,"E20.14.0"),subQ63,subQ62,sQuery(id+"F4.wireOp",EDGE,"E26.14.0"),subQ61,subQ60])]})])],"derivedFrom":subQ9})])]}),makeQuery(id+"F47.opFillet","BLEND_FACE",FACE,{"disambiguationData":[OSD([subQ5,subQ7]),TDD([makeQuery(id+"F42.boolean.opBoolean","COPY",EDGE,{"disambiguationData":[TD([makeQuery(id+"F8.opLoft","SWEPT_FACE",FACE,{"disambiguationData":[OSD([sQuery(id+"F3.wireOp",EDGE,"E20.13.0"),subQ59,subQ58,sQuery(id+"F4.wireOp",EDGE,"E26.13.0"),subQ57,subQ56])]})])],"derivedFrom":subQ9})])]}),makeQuery(id+"F47.opFillet","BLEND_FACE",FACE,{"disambiguationData":[OSD([subQ5,subQ7]),TDD([makeQuery(id+"F42.boolean.opBoolean","COPY",EDGE,{"disambiguationData":[TD([makeQuery(id+"F9.opLoft","SWEPT_FACE",FACE,{"disambiguationData":[OSD([sQuery(id+"F3.wireOp",EDGE,"E20.12.0"),subQ55,subQ54,sQuery(id+"F4.wireOp",EDGE,"E26.12.0"),subQ53,subQ52])]})])],"derivedFrom":subQ9})])]}),makeQuery(id+"F47.opFillet","BLEND_FACE",FACE,{"disambiguationData":[OSD([subQ5,subQ7]),TDD([makeQuery(id+"F42.boolean.opBoolean","COPY",EDGE,{"disambiguationData":[TD([subQ51])],"derivedFrom":subQ9})])]}),makeQuery(id+"F47.opFillet","BLEND_FACE",FACE,{"disambiguationData":[OSD([subQ5,subQ7]),TDD([makeQuery(id+"F42.boolean.opBoolean","COPY",EDGE,{"disambiguationData":[TD([makeQuery(id+"F11.opLoft","SWEPT_FACE",FACE,{"disambiguationData":[OSD([sQuery(id+"F3.wireOp",EDGE,"E20.10.0"),subQ45,subQ44,sQuery(id+"F4.wireOp",EDGE,"E26.10.0"),subQ43,subQ42])]})])],"derivedFrom":subQ9})])]}),makeQuery(id+"F47.opFillet","BLEND_FACE",FACE,{"disambiguationData":[OSD([subQ5,subQ7]),TDD([makeQuery(id+"F42.boolean.opBoolean","COPY",EDGE,{"disambiguationData":[TD([makeQuery(id+"F12.opLoft","SWEPT_FACE",FACE,{"disambiguationData":[OSD([sQuery(id+"F3.wireOp",EDGE,"E20.9.0"),subQ41,subQ40,sQuery(id+"F4.wireOp",EDGE,"E26.9.0"),subQ39,subQ38])]})])],"derivedFrom":subQ9})])]}),makeQuery(id+"F47.opFillet","BLEND_FACE",FACE,{"disambiguationData":[OSD([subQ5,subQ7]),TDD([makeQuery(id+"F42.boolean.opBoolean","COPY",EDGE,{"disambiguationData":[TD([makeQuery(id+"F13.opLoft","SWEPT_FACE",FACE,{"disambiguationData":[OSD([sQuery(id+"F3.wireOp",EDGE,"E20.8.0"),subQ37,subQ36,sQuery(id+"F4.wireOp",EDGE,"E26.8.0"),subQ35,subQ34])]})])],"derivedFrom":subQ9})])]}),makeQuery(id+"F47.opFillet","BLEND_FACE",FACE,{"disambiguationData":[OSD([subQ5,subQ7]),TDD([makeQuery(id+"F42.boolean.opBoolean","COPY",EDGE,{"disambiguationData":[TD([makeQuery(id+"F14.opLoft","SWEPT_FACE",FACE,{"disambiguationData":[OSD([sQuery(id+"F3.wireOp",EDGE,"E20.7.0"),subQ33,subQ32,sQuery(id+"F4.wireOp",EDGE,"E26.7.0"),subQ31,subQ30])]})])],"derivedFrom":subQ9})])]}),makeQuery(id+"F47.opFillet","BLEND_FACE",FACE,{"disambiguationData":[OSD([subQ5,subQ7]),TDD([makeQuery(id+"F42.boolean.opBoolean","COPY",EDGE,{"disambiguationData":[TD([makeQuery(id+"F15.opLoft","SWEPT_FACE",FACE,{"disambiguationData":[OSD([sQuery(id+"F3.wireOp",EDGE,"E20.6.0"),subQ29,subQ28,sQuery(id+"F4.wireOp",EDGE,"E26.6.0"),subQ27,subQ26])]})])],"derivedFrom":subQ9})])]}),makeQuery(id+"F47.opFillet","BLEND_FACE",FACE,{"disambiguationData":[OSD([subQ5,subQ7]),TDD([makeQuery(id+"F42.boolean.opBoolean","COPY",EDGE,{"disambiguationData":[TD([makeQuery(id+"F16.opLoft","SWEPT_FACE",FACE,{"disambiguationData":[OSD([sQuery(id+"F3.wireOp",EDGE,"E20.5.0"),subQ25,subQ24,sQuery(id+"F4.wireOp",EDGE,"E26.5.0"),subQ23,subQ22])]})])],"derivedFrom":subQ9})])]}),makeQuery(id+"F47.opFillet","BLEND_FACE",FACE,{"disambiguationData":[OSD([subQ5,subQ7]),TDD([makeQuery(id+"F42.boolean.opBoolean","COPY",EDGE,{"disambiguationData":[TD([makeQuery(id+"F17.opLoft","SWEPT_FACE",FACE,{"disambiguationData":[OSD([sQuery(id+"F3.wireOp",EDGE,"E20.4.0"),subQ21,subQ20,sQuery(id+"F4.wireOp",EDGE,"E26.4.0"),subQ19,subQ18])]})])],"derivedFrom":subQ9})])]}),makeQuery(id+"F47.opFillet","BLEND_FACE",FACE,{"disambiguationData":[OSD([subQ5,subQ7]),TDD([makeQuery(id+"F42.boolean.opBoolean","COPY",EDGE,{"disambiguationData":[TD([makeQuery(id+"F18.opLoft","SWEPT_FACE",FACE,{"disambiguationData":[OSD([sQuery(id+"F3.wireOp",EDGE,"E20.3.0"),subQ17,subQ16,sQuery(id+"F4.wireOp",EDGE,"E26.3.0"),subQ15,subQ14])]})])],"derivedFrom":subQ9})])]}),makeQuery(id+"F47.opFillet","BLEND_FACE",FACE,{"disambiguationData":[OSD([subQ5,subQ7]),TDD([makeQuery(id+"F42.boolean.opBoolean","COPY",EDGE,{"disambiguationData":[TD([makeQuery(id+"F19.opLoft","SWEPT_FACE",FACE,{"disambiguationData":[OSD([sQuery(id+"F3.wireOp",EDGE,"E20.2.0"),subQ13,subQ12,sQuery(id+"F4.wireOp",EDGE,"E26.2.0"),subQ11,subQ10])]})])],"derivedFrom":subQ9})])]}),makeQuery(id+"F47.opFillet","BLEND_FACE",FACE,{"disambiguationData":[OSD([subQ5,subQ7]),TDD([makeQuery(id+"F42.boolean.opBoolean","COPY",EDGE,{"disambiguationData":[TD([makeQuery(id+"F20.opLoft","SWEPT_FACE",FACE,{"disambiguationData":[OSD([sQuery(id+"F3.wireOp",EDGE,"E20.1.0"),subQ4,subQ3,sQuery(id+"F4.wireOp",EDGE,"E26.1.0"),subQ2,subQ1])]})])],"derivedFrom":subQ9})])]})]});}
            var Q60;
            {var subQ0=makeQuery(id+"F40.opExtrude","CAP_FACE",FACE,{"disambiguationData":[OSD([sQuery(id+"F39.wireOp",EDGE,"E29"),sQuery(id+"F39.wireOp",EDGE,"E30")])],"isStart":false});var subQ1=sQuery(id+"F4.wireOp",EDGE,"E26.1.3");var subQ2=sQuery(id+"F4.wireOp",EDGE,"E26.1.2");var subQ3=sQuery(id+"F3.wireOp",EDGE,"E20.1.3");var subQ4=sQuery(id+"F3.wireOp",EDGE,"E20.1.1");var subQ5=sQuery(id+"F41.wireOp",EDGE,"E35");var subQ6=makeQuery(id+"F42.opRevolve","SWEPT_FACE",FACE,{"disambiguationData":[OSD([subQ5])]});var subQ7=sQuery(id+"F41.wireOp",EDGE,"E36");var subQ8=makeQuery(id+"F42.opRevolve","SWEPT_FACE",FACE,{"disambiguationData":[OSD([subQ7])]});var subQ9=makeQuery(id+"F42.opRevolve","SWEPT_EDGE",EDGE,{"disambiguationData":[OSD([subQ5,subQ7])]});var subQ10=sQuery(id+"F4.wireOp",EDGE,"E26.2.3");var subQ11=sQuery(id+"F4.wireOp",EDGE,"E26.2.2");var subQ12=sQuery(id+"F3.wireOp",EDGE,"E20.2.3");var subQ13=sQuery(id+"F3.wireOp",EDGE,"E20.2.1");var subQ14=sQuery(id+"F4.wireOp",EDGE,"E26.3.3");var subQ15=sQuery(id+"F4.wireOp",EDGE,"E26.3.2");var subQ16=sQuery(id+"F3.wireOp",EDGE,"E20.3.3");var subQ17=sQuery(id+"F3.wireOp",EDGE,"E20.3.1");var subQ18=sQuery(id+"F4.wireOp",EDGE,"E26.4.3");var subQ19=sQuery(id+"F4.wireOp",EDGE,"E26.4.2");var subQ20=sQuery(id+"F3.wireOp",EDGE,"E20.4.3");var subQ21=sQuery(id+"F3.wireOp",EDGE,"E20.4.1");var subQ22=sQuery(id+"F4.wireOp",EDGE,"E26.5.3");var subQ23=sQuery(id+"F4.wireOp",EDGE,"E26.5.2");var subQ24=sQuery(id+"F3.wireOp",EDGE,"E20.5.3");var subQ25=sQuery(id+"F3.wireOp",EDGE,"E20.5.1");var subQ26=sQuery(id+"F4.wireOp",EDGE,"E26.6.3");var subQ27=sQuery(id+"F4.wireOp",EDGE,"E26.6.2");var subQ28=sQuery(id+"F3.wireOp",EDGE,"E20.6.3");var subQ29=sQuery(id+"F3.wireOp",EDGE,"E20.6.1");var subQ30=sQuery(id+"F4.wireOp",EDGE,"E26.7.3");var subQ31=sQuery(id+"F4.wireOp",EDGE,"E26.7.2");var subQ32=sQuery(id+"F3.wireOp",EDGE,"E20.7.3");var subQ33=sQuery(id+"F3.wireOp",EDGE,"E20.7.1");var subQ34=sQuery(id+"F4.wireOp",EDGE,"E26.8.3");var subQ35=sQuery(id+"F4.wireOp",EDGE,"E26.8.2");var subQ36=sQuery(id+"F3.wireOp",EDGE,"E20.8.3");var subQ37=sQuery(id+"F3.wireOp",EDGE,"E20.8.1");var subQ38=sQuery(id+"F4.wireOp",EDGE,"E26.9.3");var subQ39=sQuery(id+"F4.wireOp",EDGE,"E26.9.2");var subQ40=sQuery(id+"F3.wireOp",EDGE,"E20.9.3");var subQ41=sQuery(id+"F3.wireOp",EDGE,"E20.9.1");var subQ42=sQuery(id+"F4.wireOp",EDGE,"E26.10.3");var subQ43=sQuery(id+"F4.wireOp",EDGE,"E26.10.2");var subQ44=sQuery(id+"F3.wireOp",EDGE,"E20.10.3");var subQ45=sQuery(id+"F3.wireOp",EDGE,"E20.10.1");var subQ47=makeQuery(id+"F11.opLoft","SWEPT_FACE",FACE,{"disambiguationData":[OSD([sQuery(id+"F3.wireOp",EDGE,"E20.10.0"),subQ45,subQ44,sQuery(id+"F4.wireOp",EDGE,"E26.10.0"),subQ43,subQ42])]});var subQ48=sQuery(id+"F4.wireOp",EDGE,"E26.11.3");var subQ49=sQuery(id+"F4.wireOp",EDGE,"E26.11.2");var subQ50=sQuery(id+"F3.wireOp",EDGE,"E20.11.3");var subQ51=sQuery(id+"F3.wireOp",EDGE,"E20.11.1");var subQ52=sQuery(id+"F4.wireOp",EDGE,"E26.12.3");var subQ53=sQuery(id+"F4.wireOp",EDGE,"E26.12.2");var subQ54=sQuery(id+"F3.wireOp",EDGE,"E20.12.3");var subQ55=sQuery(id+"F3.wireOp",EDGE,"E20.12.1");var subQ56=sQuery(id+"F4.wireOp",EDGE,"E26.13.3");var subQ57=sQuery(id+"F4.wireOp",EDGE,"E26.13.2");var subQ58=sQuery(id+"F3.wireOp",EDGE,"E20.13.3");var subQ59=sQuery(id+"F3.wireOp",EDGE,"E20.13.1");var subQ60=sQuery(id+"F4.wireOp",EDGE,"E26.14.3");var subQ61=sQuery(id+"F4.wireOp",EDGE,"E26.14.2");var subQ62=sQuery(id+"F3.wireOp",EDGE,"E20.14.3");var subQ63=sQuery(id+"F3.wireOp",EDGE,"E20.14.1");var subQ64=sQuery(id+"F4.wireOp",EDGE,"E26.15.3");var subQ65=sQuery(id+"F4.wireOp",EDGE,"E26.15.2");var subQ66=sQuery(id+"F3.wireOp",EDGE,"E20.15.3");var subQ67=sQuery(id+"F3.wireOp",EDGE,"E20.15.1");var subQ68=sQuery(id+"F4.wireOp",EDGE,"E23");var subQ69=sQuery(id+"F4.wireOp",EDGE,"E22");var subQ70=sQuery(id+"F3.wireOp",EDGE,"E18.top");var subQ71=sQuery(id+"F3.wireOp",EDGE,"E18.bottom");var subQ74=makeQuery(id+"F42.boolean.opBoolean","COPY",FACE,{"disambiguationData":[TD([subQ47])],"derivedFrom":subQ6});var subQ75=makeQuery(id+"F11.boolean.opBoolean","INTERSECT",EDGE,{"derivedFrom":[makeQuery(id+"F1.opRevolve","SWEPT_FACE",FACE,{"disambiguationData":[OSD([sQuery(id+"F0.wireOp",EDGE,"E4")])]}),subQ47]});Q60=makeQuery(id+"F48.opFillet","BLEND_EDGE",EDGE,{"blendedFrom":[makeQuery(id+"F47.opFillet","TWEAK_EDGE",EDGE,{"derivedFrom":[makeQuery(id+"F45.opFillet","BLEND_VERTEX",VERTEX,{"blendedFrom":[subQ75,subQ47,subQ74],"blendedInto":[subQ47,subQ74]}),makeQuery(id+"F45.opFillet","BLEND_VERTEX",VERTEX,{"blendedFrom":[subQ75,makeQuery(id+"F42.boolean.opBoolean","MERGE",FACE,{"derivedFrom":[subQ0,subQ8]}),subQ74],"blendedInto":[makeQuery(id+"F42.boolean.opBoolean","MERGE",FACE,{"derivedFrom":[subQ0,subQ8]}),subQ74]})]}),makeQuery(id+"F47.opFillet","BLEND_FACE",FACE,{"disambiguationData":[OSD([subQ5,subQ7]),TDD([makeQuery(id+"F42.boolean.opBoolean","COPY",EDGE,{"disambiguationData":[TD([makeQuery(id+"F5.opLoft","SWEPT_FACE",FACE,{"disambiguationData":[OSD([subQ71,subQ70,sQuery(id+"F3.wireOp",EDGE,"E18.left"),sQuery(id+"F4.wireOp",EDGE,"E21"),subQ69,subQ68])]})])],"derivedFrom":subQ9})])]}),makeQuery(id+"F47.opFillet","BLEND_FACE",FACE,{"disambiguationData":[OSD([subQ5,subQ7]),TDD([makeQuery(id+"F42.boolean.opBoolean","COPY",EDGE,{"disambiguationData":[TD([makeQuery(id+"F6.opLoft","SWEPT_FACE",FACE,{"disambiguationData":[OSD([sQuery(id+"F3.wireOp",EDGE,"E20.15.0"),subQ67,subQ66,sQuery(id+"F4.wireOp",EDGE,"E26.15.0"),subQ65,subQ64])]})])],"derivedFrom":subQ9})])]}),makeQuery(id+"F47.opFillet","BLEND_FACE",FACE,{"disambiguationData":[OSD([subQ5,subQ7]),TDD([makeQuery(id+"F42.boolean.opBoolean","COPY",EDGE,{"disambiguationData":[TD([makeQuery(id+"F7.opLoft","SWEPT_FACE",FACE,{"disambiguationData":[OSD([sQuery(id+"F3.wireOp",EDGE,"E20.14.0"),subQ63,subQ62,sQuery(id+"F4.wireOp",EDGE,"E26.14.0"),subQ61,subQ60])]})])],"derivedFrom":subQ9})])]}),makeQuery(id+"F47.opFillet","BLEND_FACE",FACE,{"disambiguationData":[OSD([subQ5,subQ7]),TDD([makeQuery(id+"F42.boolean.opBoolean","COPY",EDGE,{"disambiguationData":[TD([makeQuery(id+"F8.opLoft","SWEPT_FACE",FACE,{"disambiguationData":[OSD([sQuery(id+"F3.wireOp",EDGE,"E20.13.0"),subQ59,subQ58,sQuery(id+"F4.wireOp",EDGE,"E26.13.0"),subQ57,subQ56])]})])],"derivedFrom":subQ9})])]}),makeQuery(id+"F47.opFillet","BLEND_FACE",FACE,{"disambiguationData":[OSD([subQ5,subQ7]),TDD([makeQuery(id+"F42.boolean.opBoolean","COPY",EDGE,{"disambiguationData":[TD([makeQuery(id+"F9.opLoft","SWEPT_FACE",FACE,{"disambiguationData":[OSD([sQuery(id+"F3.wireOp",EDGE,"E20.12.0"),subQ55,subQ54,sQuery(id+"F4.wireOp",EDGE,"E26.12.0"),subQ53,subQ52])]})])],"derivedFrom":subQ9})])]}),makeQuery(id+"F47.opFillet","BLEND_FACE",FACE,{"disambiguationData":[OSD([subQ5,subQ7]),TDD([makeQuery(id+"F42.boolean.opBoolean","COPY",EDGE,{"disambiguationData":[TD([makeQuery(id+"F10.opLoft","SWEPT_FACE",FACE,{"disambiguationData":[OSD([sQuery(id+"F3.wireOp",EDGE,"E20.11.0"),subQ51,subQ50,sQuery(id+"F4.wireOp",EDGE,"E26.11.0"),subQ49,subQ48])]})])],"derivedFrom":subQ9})])]}),makeQuery(id+"F47.opFillet","BLEND_FACE",FACE,{"disambiguationData":[OSD([subQ5,subQ7]),TDD([makeQuery(id+"F42.boolean.opBoolean","COPY",EDGE,{"disambiguationData":[TD([subQ47])],"derivedFrom":subQ9})])]}),makeQuery(id+"F47.opFillet","BLEND_FACE",FACE,{"disambiguationData":[OSD([subQ5,subQ7]),TDD([makeQuery(id+"F42.boolean.opBoolean","COPY",EDGE,{"disambiguationData":[TD([makeQuery(id+"F12.opLoft","SWEPT_FACE",FACE,{"disambiguationData":[OSD([sQuery(id+"F3.wireOp",EDGE,"E20.9.0"),subQ41,subQ40,sQuery(id+"F4.wireOp",EDGE,"E26.9.0"),subQ39,subQ38])]})])],"derivedFrom":subQ9})])]}),makeQuery(id+"F47.opFillet","BLEND_FACE",FACE,{"disambiguationData":[OSD([subQ5,subQ7]),TDD([makeQuery(id+"F42.boolean.opBoolean","COPY",EDGE,{"disambiguationData":[TD([makeQuery(id+"F13.opLoft","SWEPT_FACE",FACE,{"disambiguationData":[OSD([sQuery(id+"F3.wireOp",EDGE,"E20.8.0"),subQ37,subQ36,sQuery(id+"F4.wireOp",EDGE,"E26.8.0"),subQ35,subQ34])]})])],"derivedFrom":subQ9})])]}),makeQuery(id+"F47.opFillet","BLEND_FACE",FACE,{"disambiguationData":[OSD([subQ5,subQ7]),TDD([makeQuery(id+"F42.boolean.opBoolean","COPY",EDGE,{"disambiguationData":[TD([makeQuery(id+"F14.opLoft","SWEPT_FACE",FACE,{"disambiguationData":[OSD([sQuery(id+"F3.wireOp",EDGE,"E20.7.0"),subQ33,subQ32,sQuery(id+"F4.wireOp",EDGE,"E26.7.0"),subQ31,subQ30])]})])],"derivedFrom":subQ9})])]}),makeQuery(id+"F47.opFillet","BLEND_FACE",FACE,{"disambiguationData":[OSD([subQ5,subQ7]),TDD([makeQuery(id+"F42.boolean.opBoolean","COPY",EDGE,{"disambiguationData":[TD([makeQuery(id+"F15.opLoft","SWEPT_FACE",FACE,{"disambiguationData":[OSD([sQuery(id+"F3.wireOp",EDGE,"E20.6.0"),subQ29,subQ28,sQuery(id+"F4.wireOp",EDGE,"E26.6.0"),subQ27,subQ26])]})])],"derivedFrom":subQ9})])]}),makeQuery(id+"F47.opFillet","BLEND_FACE",FACE,{"disambiguationData":[OSD([subQ5,subQ7]),TDD([makeQuery(id+"F42.boolean.opBoolean","COPY",EDGE,{"disambiguationData":[TD([makeQuery(id+"F16.opLoft","SWEPT_FACE",FACE,{"disambiguationData":[OSD([sQuery(id+"F3.wireOp",EDGE,"E20.5.0"),subQ25,subQ24,sQuery(id+"F4.wireOp",EDGE,"E26.5.0"),subQ23,subQ22])]})])],"derivedFrom":subQ9})])]}),makeQuery(id+"F47.opFillet","BLEND_FACE",FACE,{"disambiguationData":[OSD([subQ5,subQ7]),TDD([makeQuery(id+"F42.boolean.opBoolean","COPY",EDGE,{"disambiguationData":[TD([makeQuery(id+"F17.opLoft","SWEPT_FACE",FACE,{"disambiguationData":[OSD([sQuery(id+"F3.wireOp",EDGE,"E20.4.0"),subQ21,subQ20,sQuery(id+"F4.wireOp",EDGE,"E26.4.0"),subQ19,subQ18])]})])],"derivedFrom":subQ9})])]}),makeQuery(id+"F47.opFillet","BLEND_FACE",FACE,{"disambiguationData":[OSD([subQ5,subQ7]),TDD([makeQuery(id+"F42.boolean.opBoolean","COPY",EDGE,{"disambiguationData":[TD([makeQuery(id+"F18.opLoft","SWEPT_FACE",FACE,{"disambiguationData":[OSD([sQuery(id+"F3.wireOp",EDGE,"E20.3.0"),subQ17,subQ16,sQuery(id+"F4.wireOp",EDGE,"E26.3.0"),subQ15,subQ14])]})])],"derivedFrom":subQ9})])]}),makeQuery(id+"F47.opFillet","BLEND_FACE",FACE,{"disambiguationData":[OSD([subQ5,subQ7]),TDD([makeQuery(id+"F42.boolean.opBoolean","COPY",EDGE,{"disambiguationData":[TD([makeQuery(id+"F19.opLoft","SWEPT_FACE",FACE,{"disambiguationData":[OSD([sQuery(id+"F3.wireOp",EDGE,"E20.2.0"),subQ13,subQ12,sQuery(id+"F4.wireOp",EDGE,"E26.2.0"),subQ11,subQ10])]})])],"derivedFrom":subQ9})])]}),makeQuery(id+"F47.opFillet","BLEND_FACE",FACE,{"disambiguationData":[OSD([subQ5,subQ7]),TDD([makeQuery(id+"F42.boolean.opBoolean","COPY",EDGE,{"disambiguationData":[TD([makeQuery(id+"F20.opLoft","SWEPT_FACE",FACE,{"disambiguationData":[OSD([sQuery(id+"F3.wireOp",EDGE,"E20.1.0"),subQ4,subQ3,sQuery(id+"F4.wireOp",EDGE,"E26.1.0"),subQ2,subQ1])]})])],"derivedFrom":subQ9})])]})],"blendedInto":[makeQuery(id+"F47.opFillet","BLEND_FACE",FACE,{"disambiguationData":[OSD([subQ5,subQ7]),TDD([makeQuery(id+"F42.boolean.opBoolean","COPY",EDGE,{"disambiguationData":[TD([makeQuery(id+"F5.opLoft","SWEPT_FACE",FACE,{"disambiguationData":[OSD([subQ71,subQ70,sQuery(id+"F3.wireOp",EDGE,"E18.left"),sQuery(id+"F4.wireOp",EDGE,"E21"),subQ69,subQ68])]})])],"derivedFrom":subQ9})])]}),makeQuery(id+"F47.opFillet","BLEND_FACE",FACE,{"disambiguationData":[OSD([subQ5,subQ7]),TDD([makeQuery(id+"F42.boolean.opBoolean","COPY",EDGE,{"disambiguationData":[TD([makeQuery(id+"F6.opLoft","SWEPT_FACE",FACE,{"disambiguationData":[OSD([sQuery(id+"F3.wireOp",EDGE,"E20.15.0"),subQ67,subQ66,sQuery(id+"F4.wireOp",EDGE,"E26.15.0"),subQ65,subQ64])]})])],"derivedFrom":subQ9})])]}),makeQuery(id+"F47.opFillet","BLEND_FACE",FACE,{"disambiguationData":[OSD([subQ5,subQ7]),TDD([makeQuery(id+"F42.boolean.opBoolean","COPY",EDGE,{"disambiguationData":[TD([makeQuery(id+"F7.opLoft","SWEPT_FACE",FACE,{"disambiguationData":[OSD([sQuery(id+"F3.wireOp",EDGE,"E20.14.0"),subQ63,subQ62,sQuery(id+"F4.wireOp",EDGE,"E26.14.0"),subQ61,subQ60])]})])],"derivedFrom":subQ9})])]}),makeQuery(id+"F47.opFillet","BLEND_FACE",FACE,{"disambiguationData":[OSD([subQ5,subQ7]),TDD([makeQuery(id+"F42.boolean.opBoolean","COPY",EDGE,{"disambiguationData":[TD([makeQuery(id+"F8.opLoft","SWEPT_FACE",FACE,{"disambiguationData":[OSD([sQuery(id+"F3.wireOp",EDGE,"E20.13.0"),subQ59,subQ58,sQuery(id+"F4.wireOp",EDGE,"E26.13.0"),subQ57,subQ56])]})])],"derivedFrom":subQ9})])]}),makeQuery(id+"F47.opFillet","BLEND_FACE",FACE,{"disambiguationData":[OSD([subQ5,subQ7]),TDD([makeQuery(id+"F42.boolean.opBoolean","COPY",EDGE,{"disambiguationData":[TD([makeQuery(id+"F9.opLoft","SWEPT_FACE",FACE,{"disambiguationData":[OSD([sQuery(id+"F3.wireOp",EDGE,"E20.12.0"),subQ55,subQ54,sQuery(id+"F4.wireOp",EDGE,"E26.12.0"),subQ53,subQ52])]})])],"derivedFrom":subQ9})])]}),makeQuery(id+"F47.opFillet","BLEND_FACE",FACE,{"disambiguationData":[OSD([subQ5,subQ7]),TDD([makeQuery(id+"F42.boolean.opBoolean","COPY",EDGE,{"disambiguationData":[TD([makeQuery(id+"F10.opLoft","SWEPT_FACE",FACE,{"disambiguationData":[OSD([sQuery(id+"F3.wireOp",EDGE,"E20.11.0"),subQ51,subQ50,sQuery(id+"F4.wireOp",EDGE,"E26.11.0"),subQ49,subQ48])]})])],"derivedFrom":subQ9})])]}),makeQuery(id+"F47.opFillet","BLEND_FACE",FACE,{"disambiguationData":[OSD([subQ5,subQ7]),TDD([makeQuery(id+"F42.boolean.opBoolean","COPY",EDGE,{"disambiguationData":[TD([subQ47])],"derivedFrom":subQ9})])]}),makeQuery(id+"F47.opFillet","BLEND_FACE",FACE,{"disambiguationData":[OSD([subQ5,subQ7]),TDD([makeQuery(id+"F42.boolean.opBoolean","COPY",EDGE,{"disambiguationData":[TD([makeQuery(id+"F12.opLoft","SWEPT_FACE",FACE,{"disambiguationData":[OSD([sQuery(id+"F3.wireOp",EDGE,"E20.9.0"),subQ41,subQ40,sQuery(id+"F4.wireOp",EDGE,"E26.9.0"),subQ39,subQ38])]})])],"derivedFrom":subQ9})])]}),makeQuery(id+"F47.opFillet","BLEND_FACE",FACE,{"disambiguationData":[OSD([subQ5,subQ7]),TDD([makeQuery(id+"F42.boolean.opBoolean","COPY",EDGE,{"disambiguationData":[TD([makeQuery(id+"F13.opLoft","SWEPT_FACE",FACE,{"disambiguationData":[OSD([sQuery(id+"F3.wireOp",EDGE,"E20.8.0"),subQ37,subQ36,sQuery(id+"F4.wireOp",EDGE,"E26.8.0"),subQ35,subQ34])]})])],"derivedFrom":subQ9})])]}),makeQuery(id+"F47.opFillet","BLEND_FACE",FACE,{"disambiguationData":[OSD([subQ5,subQ7]),TDD([makeQuery(id+"F42.boolean.opBoolean","COPY",EDGE,{"disambiguationData":[TD([makeQuery(id+"F14.opLoft","SWEPT_FACE",FACE,{"disambiguationData":[OSD([sQuery(id+"F3.wireOp",EDGE,"E20.7.0"),subQ33,subQ32,sQuery(id+"F4.wireOp",EDGE,"E26.7.0"),subQ31,subQ30])]})])],"derivedFrom":subQ9})])]}),makeQuery(id+"F47.opFillet","BLEND_FACE",FACE,{"disambiguationData":[OSD([subQ5,subQ7]),TDD([makeQuery(id+"F42.boolean.opBoolean","COPY",EDGE,{"disambiguationData":[TD([makeQuery(id+"F15.opLoft","SWEPT_FACE",FACE,{"disambiguationData":[OSD([sQuery(id+"F3.wireOp",EDGE,"E20.6.0"),subQ29,subQ28,sQuery(id+"F4.wireOp",EDGE,"E26.6.0"),subQ27,subQ26])]})])],"derivedFrom":subQ9})])]}),makeQuery(id+"F47.opFillet","BLEND_FACE",FACE,{"disambiguationData":[OSD([subQ5,subQ7]),TDD([makeQuery(id+"F42.boolean.opBoolean","COPY",EDGE,{"disambiguationData":[TD([makeQuery(id+"F16.opLoft","SWEPT_FACE",FACE,{"disambiguationData":[OSD([sQuery(id+"F3.wireOp",EDGE,"E20.5.0"),subQ25,subQ24,sQuery(id+"F4.wireOp",EDGE,"E26.5.0"),subQ23,subQ22])]})])],"derivedFrom":subQ9})])]}),makeQuery(id+"F47.opFillet","BLEND_FACE",FACE,{"disambiguationData":[OSD([subQ5,subQ7]),TDD([makeQuery(id+"F42.boolean.opBoolean","COPY",EDGE,{"disambiguationData":[TD([makeQuery(id+"F17.opLoft","SWEPT_FACE",FACE,{"disambiguationData":[OSD([sQuery(id+"F3.wireOp",EDGE,"E20.4.0"),subQ21,subQ20,sQuery(id+"F4.wireOp",EDGE,"E26.4.0"),subQ19,subQ18])]})])],"derivedFrom":subQ9})])]}),makeQuery(id+"F47.opFillet","BLEND_FACE",FACE,{"disambiguationData":[OSD([subQ5,subQ7]),TDD([makeQuery(id+"F42.boolean.opBoolean","COPY",EDGE,{"disambiguationData":[TD([makeQuery(id+"F18.opLoft","SWEPT_FACE",FACE,{"disambiguationData":[OSD([sQuery(id+"F3.wireOp",EDGE,"E20.3.0"),subQ17,subQ16,sQuery(id+"F4.wireOp",EDGE,"E26.3.0"),subQ15,subQ14])]})])],"derivedFrom":subQ9})])]}),makeQuery(id+"F47.opFillet","BLEND_FACE",FACE,{"disambiguationData":[OSD([subQ5,subQ7]),TDD([makeQuery(id+"F42.boolean.opBoolean","COPY",EDGE,{"disambiguationData":[TD([makeQuery(id+"F19.opLoft","SWEPT_FACE",FACE,{"disambiguationData":[OSD([sQuery(id+"F3.wireOp",EDGE,"E20.2.0"),subQ13,subQ12,sQuery(id+"F4.wireOp",EDGE,"E26.2.0"),subQ11,subQ10])]})])],"derivedFrom":subQ9})])]}),makeQuery(id+"F47.opFillet","BLEND_FACE",FACE,{"disambiguationData":[OSD([subQ5,subQ7]),TDD([makeQuery(id+"F42.boolean.opBoolean","COPY",EDGE,{"disambiguationData":[TD([makeQuery(id+"F20.opLoft","SWEPT_FACE",FACE,{"disambiguationData":[OSD([sQuery(id+"F3.wireOp",EDGE,"E20.1.0"),subQ4,subQ3,sQuery(id+"F4.wireOp",EDGE,"E26.1.0"),subQ2,subQ1])]})])],"derivedFrom":subQ9})])]})]});}
            var Q61;
            {var subQ0=makeQuery(id+"F40.opExtrude","CAP_FACE",FACE,{"disambiguationData":[OSD([sQuery(id+"F39.wireOp",EDGE,"E29"),sQuery(id+"F39.wireOp",EDGE,"E30")])],"isStart":false});var subQ1=sQuery(id+"F4.wireOp",EDGE,"E26.1.3");var subQ2=sQuery(id+"F4.wireOp",EDGE,"E26.1.2");var subQ3=sQuery(id+"F3.wireOp",EDGE,"E20.1.3");var subQ4=sQuery(id+"F3.wireOp",EDGE,"E20.1.1");var subQ5=sQuery(id+"F41.wireOp",EDGE,"E35");var subQ6=makeQuery(id+"F42.opRevolve","SWEPT_FACE",FACE,{"disambiguationData":[OSD([subQ5])]});var subQ7=sQuery(id+"F41.wireOp",EDGE,"E36");var subQ8=makeQuery(id+"F42.opRevolve","SWEPT_FACE",FACE,{"disambiguationData":[OSD([subQ7])]});var subQ9=makeQuery(id+"F42.opRevolve","SWEPT_EDGE",EDGE,{"disambiguationData":[OSD([subQ5,subQ7])]});var subQ10=sQuery(id+"F4.wireOp",EDGE,"E26.2.3");var subQ11=sQuery(id+"F4.wireOp",EDGE,"E26.2.2");var subQ12=sQuery(id+"F3.wireOp",EDGE,"E20.2.3");var subQ13=sQuery(id+"F3.wireOp",EDGE,"E20.2.1");var subQ14=sQuery(id+"F4.wireOp",EDGE,"E26.3.3");var subQ15=sQuery(id+"F4.wireOp",EDGE,"E26.3.2");var subQ16=sQuery(id+"F3.wireOp",EDGE,"E20.3.3");var subQ17=sQuery(id+"F3.wireOp",EDGE,"E20.3.1");var subQ18=sQuery(id+"F4.wireOp",EDGE,"E26.4.3");var subQ19=sQuery(id+"F4.wireOp",EDGE,"E26.4.2");var subQ20=sQuery(id+"F3.wireOp",EDGE,"E20.4.3");var subQ21=sQuery(id+"F3.wireOp",EDGE,"E20.4.1");var subQ22=sQuery(id+"F4.wireOp",EDGE,"E26.5.3");var subQ23=sQuery(id+"F4.wireOp",EDGE,"E26.5.2");var subQ24=sQuery(id+"F3.wireOp",EDGE,"E20.5.3");var subQ25=sQuery(id+"F3.wireOp",EDGE,"E20.5.1");var subQ26=sQuery(id+"F4.wireOp",EDGE,"E26.6.3");var subQ27=sQuery(id+"F4.wireOp",EDGE,"E26.6.2");var subQ28=sQuery(id+"F3.wireOp",EDGE,"E20.6.3");var subQ29=sQuery(id+"F3.wireOp",EDGE,"E20.6.1");var subQ30=sQuery(id+"F4.wireOp",EDGE,"E26.7.3");var subQ31=sQuery(id+"F4.wireOp",EDGE,"E26.7.2");var subQ32=sQuery(id+"F3.wireOp",EDGE,"E20.7.3");var subQ33=sQuery(id+"F3.wireOp",EDGE,"E20.7.1");var subQ34=sQuery(id+"F4.wireOp",EDGE,"E26.8.3");var subQ35=sQuery(id+"F4.wireOp",EDGE,"E26.8.2");var subQ36=sQuery(id+"F3.wireOp",EDGE,"E20.8.3");var subQ37=sQuery(id+"F3.wireOp",EDGE,"E20.8.1");var subQ38=sQuery(id+"F4.wireOp",EDGE,"E26.9.3");var subQ39=sQuery(id+"F4.wireOp",EDGE,"E26.9.2");var subQ40=sQuery(id+"F3.wireOp",EDGE,"E20.9.3");var subQ41=sQuery(id+"F3.wireOp",EDGE,"E20.9.1");var subQ43=makeQuery(id+"F12.opLoft","SWEPT_FACE",FACE,{"disambiguationData":[OSD([sQuery(id+"F3.wireOp",EDGE,"E20.9.0"),subQ41,subQ40,sQuery(id+"F4.wireOp",EDGE,"E26.9.0"),subQ39,subQ38])]});var subQ44=sQuery(id+"F4.wireOp",EDGE,"E26.10.3");var subQ45=sQuery(id+"F4.wireOp",EDGE,"E26.10.2");var subQ46=sQuery(id+"F3.wireOp",EDGE,"E20.10.3");var subQ47=sQuery(id+"F3.wireOp",EDGE,"E20.10.1");var subQ48=sQuery(id+"F4.wireOp",EDGE,"E26.11.3");var subQ49=sQuery(id+"F4.wireOp",EDGE,"E26.11.2");var subQ50=sQuery(id+"F3.wireOp",EDGE,"E20.11.3");var subQ51=sQuery(id+"F3.wireOp",EDGE,"E20.11.1");var subQ52=sQuery(id+"F4.wireOp",EDGE,"E26.12.3");var subQ53=sQuery(id+"F4.wireOp",EDGE,"E26.12.2");var subQ54=sQuery(id+"F3.wireOp",EDGE,"E20.12.3");var subQ55=sQuery(id+"F3.wireOp",EDGE,"E20.12.1");var subQ56=sQuery(id+"F4.wireOp",EDGE,"E26.13.3");var subQ57=sQuery(id+"F4.wireOp",EDGE,"E26.13.2");var subQ58=sQuery(id+"F3.wireOp",EDGE,"E20.13.3");var subQ59=sQuery(id+"F3.wireOp",EDGE,"E20.13.1");var subQ60=sQuery(id+"F4.wireOp",EDGE,"E26.14.3");var subQ61=sQuery(id+"F4.wireOp",EDGE,"E26.14.2");var subQ62=sQuery(id+"F3.wireOp",EDGE,"E20.14.3");var subQ63=sQuery(id+"F3.wireOp",EDGE,"E20.14.1");var subQ64=sQuery(id+"F4.wireOp",EDGE,"E26.15.3");var subQ65=sQuery(id+"F4.wireOp",EDGE,"E26.15.2");var subQ66=sQuery(id+"F3.wireOp",EDGE,"E20.15.3");var subQ67=sQuery(id+"F3.wireOp",EDGE,"E20.15.1");var subQ68=sQuery(id+"F4.wireOp",EDGE,"E23");var subQ69=sQuery(id+"F4.wireOp",EDGE,"E22");var subQ70=sQuery(id+"F3.wireOp",EDGE,"E18.top");var subQ71=sQuery(id+"F3.wireOp",EDGE,"E18.bottom");var subQ74=makeQuery(id+"F42.boolean.opBoolean","COPY",FACE,{"disambiguationData":[TD([subQ43])],"derivedFrom":subQ6});var subQ75=makeQuery(id+"F12.boolean.opBoolean","INTERSECT",EDGE,{"derivedFrom":[makeQuery(id+"F1.opRevolve","SWEPT_FACE",FACE,{"disambiguationData":[OSD([sQuery(id+"F0.wireOp",EDGE,"E4")])]}),subQ43]});Q61=makeQuery(id+"F48.opFillet","BLEND_EDGE",EDGE,{"blendedFrom":[makeQuery(id+"F47.opFillet","TWEAK_EDGE",EDGE,{"derivedFrom":[makeQuery(id+"F45.opFillet","BLEND_VERTEX",VERTEX,{"blendedFrom":[subQ75,subQ43,subQ74],"blendedInto":[subQ43,subQ74]}),makeQuery(id+"F45.opFillet","BLEND_VERTEX",VERTEX,{"blendedFrom":[subQ75,makeQuery(id+"F42.boolean.opBoolean","MERGE",FACE,{"derivedFrom":[subQ0,subQ8]}),subQ74],"blendedInto":[makeQuery(id+"F42.boolean.opBoolean","MERGE",FACE,{"derivedFrom":[subQ0,subQ8]}),subQ74]})]}),makeQuery(id+"F47.opFillet","BLEND_FACE",FACE,{"disambiguationData":[OSD([subQ5,subQ7]),TDD([makeQuery(id+"F42.boolean.opBoolean","COPY",EDGE,{"disambiguationData":[TD([makeQuery(id+"F5.opLoft","SWEPT_FACE",FACE,{"disambiguationData":[OSD([subQ71,subQ70,sQuery(id+"F3.wireOp",EDGE,"E18.left"),sQuery(id+"F4.wireOp",EDGE,"E21"),subQ69,subQ68])]})])],"derivedFrom":subQ9})])]}),makeQuery(id+"F47.opFillet","BLEND_FACE",FACE,{"disambiguationData":[OSD([subQ5,subQ7]),TDD([makeQuery(id+"F42.boolean.opBoolean","COPY",EDGE,{"disambiguationData":[TD([makeQuery(id+"F6.opLoft","SWEPT_FACE",FACE,{"disambiguationData":[OSD([sQuery(id+"F3.wireOp",EDGE,"E20.15.0"),subQ67,subQ66,sQuery(id+"F4.wireOp",EDGE,"E26.15.0"),subQ65,subQ64])]})])],"derivedFrom":subQ9})])]}),makeQuery(id+"F47.opFillet","BLEND_FACE",FACE,{"disambiguationData":[OSD([subQ5,subQ7]),TDD([makeQuery(id+"F42.boolean.opBoolean","COPY",EDGE,{"disambiguationData":[TD([makeQuery(id+"F7.opLoft","SWEPT_FACE",FACE,{"disambiguationData":[OSD([sQuery(id+"F3.wireOp",EDGE,"E20.14.0"),subQ63,subQ62,sQuery(id+"F4.wireOp",EDGE,"E26.14.0"),subQ61,subQ60])]})])],"derivedFrom":subQ9})])]}),makeQuery(id+"F47.opFillet","BLEND_FACE",FACE,{"disambiguationData":[OSD([subQ5,subQ7]),TDD([makeQuery(id+"F42.boolean.opBoolean","COPY",EDGE,{"disambiguationData":[TD([makeQuery(id+"F8.opLoft","SWEPT_FACE",FACE,{"disambiguationData":[OSD([sQuery(id+"F3.wireOp",EDGE,"E20.13.0"),subQ59,subQ58,sQuery(id+"F4.wireOp",EDGE,"E26.13.0"),subQ57,subQ56])]})])],"derivedFrom":subQ9})])]}),makeQuery(id+"F47.opFillet","BLEND_FACE",FACE,{"disambiguationData":[OSD([subQ5,subQ7]),TDD([makeQuery(id+"F42.boolean.opBoolean","COPY",EDGE,{"disambiguationData":[TD([makeQuery(id+"F9.opLoft","SWEPT_FACE",FACE,{"disambiguationData":[OSD([sQuery(id+"F3.wireOp",EDGE,"E20.12.0"),subQ55,subQ54,sQuery(id+"F4.wireOp",EDGE,"E26.12.0"),subQ53,subQ52])]})])],"derivedFrom":subQ9})])]}),makeQuery(id+"F47.opFillet","BLEND_FACE",FACE,{"disambiguationData":[OSD([subQ5,subQ7]),TDD([makeQuery(id+"F42.boolean.opBoolean","COPY",EDGE,{"disambiguationData":[TD([makeQuery(id+"F10.opLoft","SWEPT_FACE",FACE,{"disambiguationData":[OSD([sQuery(id+"F3.wireOp",EDGE,"E20.11.0"),subQ51,subQ50,sQuery(id+"F4.wireOp",EDGE,"E26.11.0"),subQ49,subQ48])]})])],"derivedFrom":subQ9})])]}),makeQuery(id+"F47.opFillet","BLEND_FACE",FACE,{"disambiguationData":[OSD([subQ5,subQ7]),TDD([makeQuery(id+"F42.boolean.opBoolean","COPY",EDGE,{"disambiguationData":[TD([makeQuery(id+"F11.opLoft","SWEPT_FACE",FACE,{"disambiguationData":[OSD([sQuery(id+"F3.wireOp",EDGE,"E20.10.0"),subQ47,subQ46,sQuery(id+"F4.wireOp",EDGE,"E26.10.0"),subQ45,subQ44])]})])],"derivedFrom":subQ9})])]}),makeQuery(id+"F47.opFillet","BLEND_FACE",FACE,{"disambiguationData":[OSD([subQ5,subQ7]),TDD([makeQuery(id+"F42.boolean.opBoolean","COPY",EDGE,{"disambiguationData":[TD([subQ43])],"derivedFrom":subQ9})])]}),makeQuery(id+"F47.opFillet","BLEND_FACE",FACE,{"disambiguationData":[OSD([subQ5,subQ7]),TDD([makeQuery(id+"F42.boolean.opBoolean","COPY",EDGE,{"disambiguationData":[TD([makeQuery(id+"F13.opLoft","SWEPT_FACE",FACE,{"disambiguationData":[OSD([sQuery(id+"F3.wireOp",EDGE,"E20.8.0"),subQ37,subQ36,sQuery(id+"F4.wireOp",EDGE,"E26.8.0"),subQ35,subQ34])]})])],"derivedFrom":subQ9})])]}),makeQuery(id+"F47.opFillet","BLEND_FACE",FACE,{"disambiguationData":[OSD([subQ5,subQ7]),TDD([makeQuery(id+"F42.boolean.opBoolean","COPY",EDGE,{"disambiguationData":[TD([makeQuery(id+"F14.opLoft","SWEPT_FACE",FACE,{"disambiguationData":[OSD([sQuery(id+"F3.wireOp",EDGE,"E20.7.0"),subQ33,subQ32,sQuery(id+"F4.wireOp",EDGE,"E26.7.0"),subQ31,subQ30])]})])],"derivedFrom":subQ9})])]}),makeQuery(id+"F47.opFillet","BLEND_FACE",FACE,{"disambiguationData":[OSD([subQ5,subQ7]),TDD([makeQuery(id+"F42.boolean.opBoolean","COPY",EDGE,{"disambiguationData":[TD([makeQuery(id+"F15.opLoft","SWEPT_FACE",FACE,{"disambiguationData":[OSD([sQuery(id+"F3.wireOp",EDGE,"E20.6.0"),subQ29,subQ28,sQuery(id+"F4.wireOp",EDGE,"E26.6.0"),subQ27,subQ26])]})])],"derivedFrom":subQ9})])]}),makeQuery(id+"F47.opFillet","BLEND_FACE",FACE,{"disambiguationData":[OSD([subQ5,subQ7]),TDD([makeQuery(id+"F42.boolean.opBoolean","COPY",EDGE,{"disambiguationData":[TD([makeQuery(id+"F16.opLoft","SWEPT_FACE",FACE,{"disambiguationData":[OSD([sQuery(id+"F3.wireOp",EDGE,"E20.5.0"),subQ25,subQ24,sQuery(id+"F4.wireOp",EDGE,"E26.5.0"),subQ23,subQ22])]})])],"derivedFrom":subQ9})])]}),makeQuery(id+"F47.opFillet","BLEND_FACE",FACE,{"disambiguationData":[OSD([subQ5,subQ7]),TDD([makeQuery(id+"F42.boolean.opBoolean","COPY",EDGE,{"disambiguationData":[TD([makeQuery(id+"F17.opLoft","SWEPT_FACE",FACE,{"disambiguationData":[OSD([sQuery(id+"F3.wireOp",EDGE,"E20.4.0"),subQ21,subQ20,sQuery(id+"F4.wireOp",EDGE,"E26.4.0"),subQ19,subQ18])]})])],"derivedFrom":subQ9})])]}),makeQuery(id+"F47.opFillet","BLEND_FACE",FACE,{"disambiguationData":[OSD([subQ5,subQ7]),TDD([makeQuery(id+"F42.boolean.opBoolean","COPY",EDGE,{"disambiguationData":[TD([makeQuery(id+"F18.opLoft","SWEPT_FACE",FACE,{"disambiguationData":[OSD([sQuery(id+"F3.wireOp",EDGE,"E20.3.0"),subQ17,subQ16,sQuery(id+"F4.wireOp",EDGE,"E26.3.0"),subQ15,subQ14])]})])],"derivedFrom":subQ9})])]}),makeQuery(id+"F47.opFillet","BLEND_FACE",FACE,{"disambiguationData":[OSD([subQ5,subQ7]),TDD([makeQuery(id+"F42.boolean.opBoolean","COPY",EDGE,{"disambiguationData":[TD([makeQuery(id+"F19.opLoft","SWEPT_FACE",FACE,{"disambiguationData":[OSD([sQuery(id+"F3.wireOp",EDGE,"E20.2.0"),subQ13,subQ12,sQuery(id+"F4.wireOp",EDGE,"E26.2.0"),subQ11,subQ10])]})])],"derivedFrom":subQ9})])]}),makeQuery(id+"F47.opFillet","BLEND_FACE",FACE,{"disambiguationData":[OSD([subQ5,subQ7]),TDD([makeQuery(id+"F42.boolean.opBoolean","COPY",EDGE,{"disambiguationData":[TD([makeQuery(id+"F20.opLoft","SWEPT_FACE",FACE,{"disambiguationData":[OSD([sQuery(id+"F3.wireOp",EDGE,"E20.1.0"),subQ4,subQ3,sQuery(id+"F4.wireOp",EDGE,"E26.1.0"),subQ2,subQ1])]})])],"derivedFrom":subQ9})])]})],"blendedInto":[makeQuery(id+"F47.opFillet","BLEND_FACE",FACE,{"disambiguationData":[OSD([subQ5,subQ7]),TDD([makeQuery(id+"F42.boolean.opBoolean","COPY",EDGE,{"disambiguationData":[TD([makeQuery(id+"F5.opLoft","SWEPT_FACE",FACE,{"disambiguationData":[OSD([subQ71,subQ70,sQuery(id+"F3.wireOp",EDGE,"E18.left"),sQuery(id+"F4.wireOp",EDGE,"E21"),subQ69,subQ68])]})])],"derivedFrom":subQ9})])]}),makeQuery(id+"F47.opFillet","BLEND_FACE",FACE,{"disambiguationData":[OSD([subQ5,subQ7]),TDD([makeQuery(id+"F42.boolean.opBoolean","COPY",EDGE,{"disambiguationData":[TD([makeQuery(id+"F6.opLoft","SWEPT_FACE",FACE,{"disambiguationData":[OSD([sQuery(id+"F3.wireOp",EDGE,"E20.15.0"),subQ67,subQ66,sQuery(id+"F4.wireOp",EDGE,"E26.15.0"),subQ65,subQ64])]})])],"derivedFrom":subQ9})])]}),makeQuery(id+"F47.opFillet","BLEND_FACE",FACE,{"disambiguationData":[OSD([subQ5,subQ7]),TDD([makeQuery(id+"F42.boolean.opBoolean","COPY",EDGE,{"disambiguationData":[TD([makeQuery(id+"F7.opLoft","SWEPT_FACE",FACE,{"disambiguationData":[OSD([sQuery(id+"F3.wireOp",EDGE,"E20.14.0"),subQ63,subQ62,sQuery(id+"F4.wireOp",EDGE,"E26.14.0"),subQ61,subQ60])]})])],"derivedFrom":subQ9})])]}),makeQuery(id+"F47.opFillet","BLEND_FACE",FACE,{"disambiguationData":[OSD([subQ5,subQ7]),TDD([makeQuery(id+"F42.boolean.opBoolean","COPY",EDGE,{"disambiguationData":[TD([makeQuery(id+"F8.opLoft","SWEPT_FACE",FACE,{"disambiguationData":[OSD([sQuery(id+"F3.wireOp",EDGE,"E20.13.0"),subQ59,subQ58,sQuery(id+"F4.wireOp",EDGE,"E26.13.0"),subQ57,subQ56])]})])],"derivedFrom":subQ9})])]}),makeQuery(id+"F47.opFillet","BLEND_FACE",FACE,{"disambiguationData":[OSD([subQ5,subQ7]),TDD([makeQuery(id+"F42.boolean.opBoolean","COPY",EDGE,{"disambiguationData":[TD([makeQuery(id+"F9.opLoft","SWEPT_FACE",FACE,{"disambiguationData":[OSD([sQuery(id+"F3.wireOp",EDGE,"E20.12.0"),subQ55,subQ54,sQuery(id+"F4.wireOp",EDGE,"E26.12.0"),subQ53,subQ52])]})])],"derivedFrom":subQ9})])]}),makeQuery(id+"F47.opFillet","BLEND_FACE",FACE,{"disambiguationData":[OSD([subQ5,subQ7]),TDD([makeQuery(id+"F42.boolean.opBoolean","COPY",EDGE,{"disambiguationData":[TD([makeQuery(id+"F10.opLoft","SWEPT_FACE",FACE,{"disambiguationData":[OSD([sQuery(id+"F3.wireOp",EDGE,"E20.11.0"),subQ51,subQ50,sQuery(id+"F4.wireOp",EDGE,"E26.11.0"),subQ49,subQ48])]})])],"derivedFrom":subQ9})])]}),makeQuery(id+"F47.opFillet","BLEND_FACE",FACE,{"disambiguationData":[OSD([subQ5,subQ7]),TDD([makeQuery(id+"F42.boolean.opBoolean","COPY",EDGE,{"disambiguationData":[TD([makeQuery(id+"F11.opLoft","SWEPT_FACE",FACE,{"disambiguationData":[OSD([sQuery(id+"F3.wireOp",EDGE,"E20.10.0"),subQ47,subQ46,sQuery(id+"F4.wireOp",EDGE,"E26.10.0"),subQ45,subQ44])]})])],"derivedFrom":subQ9})])]}),makeQuery(id+"F47.opFillet","BLEND_FACE",FACE,{"disambiguationData":[OSD([subQ5,subQ7]),TDD([makeQuery(id+"F42.boolean.opBoolean","COPY",EDGE,{"disambiguationData":[TD([subQ43])],"derivedFrom":subQ9})])]}),makeQuery(id+"F47.opFillet","BLEND_FACE",FACE,{"disambiguationData":[OSD([subQ5,subQ7]),TDD([makeQuery(id+"F42.boolean.opBoolean","COPY",EDGE,{"disambiguationData":[TD([makeQuery(id+"F13.opLoft","SWEPT_FACE",FACE,{"disambiguationData":[OSD([sQuery(id+"F3.wireOp",EDGE,"E20.8.0"),subQ37,subQ36,sQuery(id+"F4.wireOp",EDGE,"E26.8.0"),subQ35,subQ34])]})])],"derivedFrom":subQ9})])]}),makeQuery(id+"F47.opFillet","BLEND_FACE",FACE,{"disambiguationData":[OSD([subQ5,subQ7]),TDD([makeQuery(id+"F42.boolean.opBoolean","COPY",EDGE,{"disambiguationData":[TD([makeQuery(id+"F14.opLoft","SWEPT_FACE",FACE,{"disambiguationData":[OSD([sQuery(id+"F3.wireOp",EDGE,"E20.7.0"),subQ33,subQ32,sQuery(id+"F4.wireOp",EDGE,"E26.7.0"),subQ31,subQ30])]})])],"derivedFrom":subQ9})])]}),makeQuery(id+"F47.opFillet","BLEND_FACE",FACE,{"disambiguationData":[OSD([subQ5,subQ7]),TDD([makeQuery(id+"F42.boolean.opBoolean","COPY",EDGE,{"disambiguationData":[TD([makeQuery(id+"F15.opLoft","SWEPT_FACE",FACE,{"disambiguationData":[OSD([sQuery(id+"F3.wireOp",EDGE,"E20.6.0"),subQ29,subQ28,sQuery(id+"F4.wireOp",EDGE,"E26.6.0"),subQ27,subQ26])]})])],"derivedFrom":subQ9})])]}),makeQuery(id+"F47.opFillet","BLEND_FACE",FACE,{"disambiguationData":[OSD([subQ5,subQ7]),TDD([makeQuery(id+"F42.boolean.opBoolean","COPY",EDGE,{"disambiguationData":[TD([makeQuery(id+"F16.opLoft","SWEPT_FACE",FACE,{"disambiguationData":[OSD([sQuery(id+"F3.wireOp",EDGE,"E20.5.0"),subQ25,subQ24,sQuery(id+"F4.wireOp",EDGE,"E26.5.0"),subQ23,subQ22])]})])],"derivedFrom":subQ9})])]}),makeQuery(id+"F47.opFillet","BLEND_FACE",FACE,{"disambiguationData":[OSD([subQ5,subQ7]),TDD([makeQuery(id+"F42.boolean.opBoolean","COPY",EDGE,{"disambiguationData":[TD([makeQuery(id+"F17.opLoft","SWEPT_FACE",FACE,{"disambiguationData":[OSD([sQuery(id+"F3.wireOp",EDGE,"E20.4.0"),subQ21,subQ20,sQuery(id+"F4.wireOp",EDGE,"E26.4.0"),subQ19,subQ18])]})])],"derivedFrom":subQ9})])]}),makeQuery(id+"F47.opFillet","BLEND_FACE",FACE,{"disambiguationData":[OSD([subQ5,subQ7]),TDD([makeQuery(id+"F42.boolean.opBoolean","COPY",EDGE,{"disambiguationData":[TD([makeQuery(id+"F18.opLoft","SWEPT_FACE",FACE,{"disambiguationData":[OSD([sQuery(id+"F3.wireOp",EDGE,"E20.3.0"),subQ17,subQ16,sQuery(id+"F4.wireOp",EDGE,"E26.3.0"),subQ15,subQ14])]})])],"derivedFrom":subQ9})])]}),makeQuery(id+"F47.opFillet","BLEND_FACE",FACE,{"disambiguationData":[OSD([subQ5,subQ7]),TDD([makeQuery(id+"F42.boolean.opBoolean","COPY",EDGE,{"disambiguationData":[TD([makeQuery(id+"F19.opLoft","SWEPT_FACE",FACE,{"disambiguationData":[OSD([sQuery(id+"F3.wireOp",EDGE,"E20.2.0"),subQ13,subQ12,sQuery(id+"F4.wireOp",EDGE,"E26.2.0"),subQ11,subQ10])]})])],"derivedFrom":subQ9})])]}),makeQuery(id+"F47.opFillet","BLEND_FACE",FACE,{"disambiguationData":[OSD([subQ5,subQ7]),TDD([makeQuery(id+"F42.boolean.opBoolean","COPY",EDGE,{"disambiguationData":[TD([makeQuery(id+"F20.opLoft","SWEPT_FACE",FACE,{"disambiguationData":[OSD([sQuery(id+"F3.wireOp",EDGE,"E20.1.0"),subQ4,subQ3,sQuery(id+"F4.wireOp",EDGE,"E26.1.0"),subQ2,subQ1])]})])],"derivedFrom":subQ9})])]})]});}
            var Q62;
            {var subQ0=makeQuery(id+"F40.opExtrude","CAP_FACE",FACE,{"disambiguationData":[OSD([sQuery(id+"F39.wireOp",EDGE,"E29"),sQuery(id+"F39.wireOp",EDGE,"E30")])],"isStart":false});var subQ1=sQuery(id+"F4.wireOp",EDGE,"E26.1.3");var subQ2=sQuery(id+"F4.wireOp",EDGE,"E26.1.2");var subQ3=sQuery(id+"F3.wireOp",EDGE,"E20.1.3");var subQ4=sQuery(id+"F3.wireOp",EDGE,"E20.1.1");var subQ5=sQuery(id+"F41.wireOp",EDGE,"E35");var subQ6=makeQuery(id+"F42.opRevolve","SWEPT_FACE",FACE,{"disambiguationData":[OSD([subQ5])]});var subQ7=sQuery(id+"F41.wireOp",EDGE,"E36");var subQ8=makeQuery(id+"F42.opRevolve","SWEPT_FACE",FACE,{"disambiguationData":[OSD([subQ7])]});var subQ9=makeQuery(id+"F42.opRevolve","SWEPT_EDGE",EDGE,{"disambiguationData":[OSD([subQ5,subQ7])]});var subQ10=sQuery(id+"F4.wireOp",EDGE,"E26.2.3");var subQ11=sQuery(id+"F4.wireOp",EDGE,"E26.2.2");var subQ12=sQuery(id+"F3.wireOp",EDGE,"E20.2.3");var subQ13=sQuery(id+"F3.wireOp",EDGE,"E20.2.1");var subQ14=sQuery(id+"F4.wireOp",EDGE,"E26.3.3");var subQ15=sQuery(id+"F4.wireOp",EDGE,"E26.3.2");var subQ16=sQuery(id+"F3.wireOp",EDGE,"E20.3.3");var subQ17=sQuery(id+"F3.wireOp",EDGE,"E20.3.1");var subQ18=sQuery(id+"F4.wireOp",EDGE,"E26.4.3");var subQ19=sQuery(id+"F4.wireOp",EDGE,"E26.4.2");var subQ20=sQuery(id+"F3.wireOp",EDGE,"E20.4.3");var subQ21=sQuery(id+"F3.wireOp",EDGE,"E20.4.1");var subQ22=sQuery(id+"F4.wireOp",EDGE,"E26.5.3");var subQ23=sQuery(id+"F4.wireOp",EDGE,"E26.5.2");var subQ24=sQuery(id+"F3.wireOp",EDGE,"E20.5.3");var subQ25=sQuery(id+"F3.wireOp",EDGE,"E20.5.1");var subQ26=sQuery(id+"F4.wireOp",EDGE,"E26.6.3");var subQ27=sQuery(id+"F4.wireOp",EDGE,"E26.6.2");var subQ28=sQuery(id+"F3.wireOp",EDGE,"E20.6.3");var subQ29=sQuery(id+"F3.wireOp",EDGE,"E20.6.1");var subQ30=sQuery(id+"F4.wireOp",EDGE,"E26.7.3");var subQ31=sQuery(id+"F4.wireOp",EDGE,"E26.7.2");var subQ32=sQuery(id+"F3.wireOp",EDGE,"E20.7.3");var subQ33=sQuery(id+"F3.wireOp",EDGE,"E20.7.1");var subQ35=makeQuery(id+"F14.opLoft","SWEPT_FACE",FACE,{"disambiguationData":[OSD([sQuery(id+"F3.wireOp",EDGE,"E20.7.0"),subQ33,subQ32,sQuery(id+"F4.wireOp",EDGE,"E26.7.0"),subQ31,subQ30])]});var subQ36=sQuery(id+"F4.wireOp",EDGE,"E26.8.3");var subQ37=sQuery(id+"F4.wireOp",EDGE,"E26.8.2");var subQ38=sQuery(id+"F3.wireOp",EDGE,"E20.8.3");var subQ39=sQuery(id+"F3.wireOp",EDGE,"E20.8.1");var subQ40=sQuery(id+"F4.wireOp",EDGE,"E26.9.3");var subQ41=sQuery(id+"F4.wireOp",EDGE,"E26.9.2");var subQ42=sQuery(id+"F3.wireOp",EDGE,"E20.9.3");var subQ43=sQuery(id+"F3.wireOp",EDGE,"E20.9.1");var subQ44=sQuery(id+"F4.wireOp",EDGE,"E26.10.3");var subQ45=sQuery(id+"F4.wireOp",EDGE,"E26.10.2");var subQ46=sQuery(id+"F3.wireOp",EDGE,"E20.10.3");var subQ47=sQuery(id+"F3.wireOp",EDGE,"E20.10.1");var subQ48=sQuery(id+"F4.wireOp",EDGE,"E26.11.3");var subQ49=sQuery(id+"F4.wireOp",EDGE,"E26.11.2");var subQ50=sQuery(id+"F3.wireOp",EDGE,"E20.11.3");var subQ51=sQuery(id+"F3.wireOp",EDGE,"E20.11.1");var subQ52=sQuery(id+"F4.wireOp",EDGE,"E26.12.3");var subQ53=sQuery(id+"F4.wireOp",EDGE,"E26.12.2");var subQ54=sQuery(id+"F3.wireOp",EDGE,"E20.12.3");var subQ55=sQuery(id+"F3.wireOp",EDGE,"E20.12.1");var subQ56=sQuery(id+"F4.wireOp",EDGE,"E26.13.3");var subQ57=sQuery(id+"F4.wireOp",EDGE,"E26.13.2");var subQ58=sQuery(id+"F3.wireOp",EDGE,"E20.13.3");var subQ59=sQuery(id+"F3.wireOp",EDGE,"E20.13.1");var subQ60=sQuery(id+"F4.wireOp",EDGE,"E26.14.3");var subQ61=sQuery(id+"F4.wireOp",EDGE,"E26.14.2");var subQ62=sQuery(id+"F3.wireOp",EDGE,"E20.14.3");var subQ63=sQuery(id+"F3.wireOp",EDGE,"E20.14.1");var subQ64=sQuery(id+"F4.wireOp",EDGE,"E26.15.3");var subQ65=sQuery(id+"F4.wireOp",EDGE,"E26.15.2");var subQ66=sQuery(id+"F3.wireOp",EDGE,"E20.15.3");var subQ67=sQuery(id+"F3.wireOp",EDGE,"E20.15.1");var subQ68=sQuery(id+"F4.wireOp",EDGE,"E23");var subQ69=sQuery(id+"F4.wireOp",EDGE,"E22");var subQ70=sQuery(id+"F3.wireOp",EDGE,"E18.top");var subQ71=sQuery(id+"F3.wireOp",EDGE,"E18.bottom");var subQ74=makeQuery(id+"F42.boolean.opBoolean","COPY",FACE,{"disambiguationData":[TD([subQ35])],"derivedFrom":subQ6});var subQ75=makeQuery(id+"F14.boolean.opBoolean","INTERSECT",EDGE,{"derivedFrom":[makeQuery(id+"F1.opRevolve","SWEPT_FACE",FACE,{"disambiguationData":[OSD([sQuery(id+"F0.wireOp",EDGE,"E4")])]}),subQ35]});Q62=makeQuery(id+"F48.opFillet","BLEND_EDGE",EDGE,{"blendedFrom":[makeQuery(id+"F47.opFillet","TWEAK_EDGE",EDGE,{"derivedFrom":[makeQuery(id+"F45.opFillet","BLEND_VERTEX",VERTEX,{"blendedFrom":[subQ75,subQ35,subQ74],"blendedInto":[subQ35,subQ74]}),makeQuery(id+"F45.opFillet","BLEND_VERTEX",VERTEX,{"blendedFrom":[subQ75,makeQuery(id+"F42.boolean.opBoolean","MERGE",FACE,{"derivedFrom":[subQ0,subQ8]}),subQ74],"blendedInto":[makeQuery(id+"F42.boolean.opBoolean","MERGE",FACE,{"derivedFrom":[subQ0,subQ8]}),subQ74]})]}),makeQuery(id+"F47.opFillet","BLEND_FACE",FACE,{"disambiguationData":[OSD([subQ5,subQ7]),TDD([makeQuery(id+"F42.boolean.opBoolean","COPY",EDGE,{"disambiguationData":[TD([makeQuery(id+"F5.opLoft","SWEPT_FACE",FACE,{"disambiguationData":[OSD([subQ71,subQ70,sQuery(id+"F3.wireOp",EDGE,"E18.left"),sQuery(id+"F4.wireOp",EDGE,"E21"),subQ69,subQ68])]})])],"derivedFrom":subQ9})])]}),makeQuery(id+"F47.opFillet","BLEND_FACE",FACE,{"disambiguationData":[OSD([subQ5,subQ7]),TDD([makeQuery(id+"F42.boolean.opBoolean","COPY",EDGE,{"disambiguationData":[TD([makeQuery(id+"F6.opLoft","SWEPT_FACE",FACE,{"disambiguationData":[OSD([sQuery(id+"F3.wireOp",EDGE,"E20.15.0"),subQ67,subQ66,sQuery(id+"F4.wireOp",EDGE,"E26.15.0"),subQ65,subQ64])]})])],"derivedFrom":subQ9})])]}),makeQuery(id+"F47.opFillet","BLEND_FACE",FACE,{"disambiguationData":[OSD([subQ5,subQ7]),TDD([makeQuery(id+"F42.boolean.opBoolean","COPY",EDGE,{"disambiguationData":[TD([makeQuery(id+"F7.opLoft","SWEPT_FACE",FACE,{"disambiguationData":[OSD([sQuery(id+"F3.wireOp",EDGE,"E20.14.0"),subQ63,subQ62,sQuery(id+"F4.wireOp",EDGE,"E26.14.0"),subQ61,subQ60])]})])],"derivedFrom":subQ9})])]}),makeQuery(id+"F47.opFillet","BLEND_FACE",FACE,{"disambiguationData":[OSD([subQ5,subQ7]),TDD([makeQuery(id+"F42.boolean.opBoolean","COPY",EDGE,{"disambiguationData":[TD([makeQuery(id+"F8.opLoft","SWEPT_FACE",FACE,{"disambiguationData":[OSD([sQuery(id+"F3.wireOp",EDGE,"E20.13.0"),subQ59,subQ58,sQuery(id+"F4.wireOp",EDGE,"E26.13.0"),subQ57,subQ56])]})])],"derivedFrom":subQ9})])]}),makeQuery(id+"F47.opFillet","BLEND_FACE",FACE,{"disambiguationData":[OSD([subQ5,subQ7]),TDD([makeQuery(id+"F42.boolean.opBoolean","COPY",EDGE,{"disambiguationData":[TD([makeQuery(id+"F9.opLoft","SWEPT_FACE",FACE,{"disambiguationData":[OSD([sQuery(id+"F3.wireOp",EDGE,"E20.12.0"),subQ55,subQ54,sQuery(id+"F4.wireOp",EDGE,"E26.12.0"),subQ53,subQ52])]})])],"derivedFrom":subQ9})])]}),makeQuery(id+"F47.opFillet","BLEND_FACE",FACE,{"disambiguationData":[OSD([subQ5,subQ7]),TDD([makeQuery(id+"F42.boolean.opBoolean","COPY",EDGE,{"disambiguationData":[TD([makeQuery(id+"F10.opLoft","SWEPT_FACE",FACE,{"disambiguationData":[OSD([sQuery(id+"F3.wireOp",EDGE,"E20.11.0"),subQ51,subQ50,sQuery(id+"F4.wireOp",EDGE,"E26.11.0"),subQ49,subQ48])]})])],"derivedFrom":subQ9})])]}),makeQuery(id+"F47.opFillet","BLEND_FACE",FACE,{"disambiguationData":[OSD([subQ5,subQ7]),TDD([makeQuery(id+"F42.boolean.opBoolean","COPY",EDGE,{"disambiguationData":[TD([makeQuery(id+"F11.opLoft","SWEPT_FACE",FACE,{"disambiguationData":[OSD([sQuery(id+"F3.wireOp",EDGE,"E20.10.0"),subQ47,subQ46,sQuery(id+"F4.wireOp",EDGE,"E26.10.0"),subQ45,subQ44])]})])],"derivedFrom":subQ9})])]}),makeQuery(id+"F47.opFillet","BLEND_FACE",FACE,{"disambiguationData":[OSD([subQ5,subQ7]),TDD([makeQuery(id+"F42.boolean.opBoolean","COPY",EDGE,{"disambiguationData":[TD([makeQuery(id+"F12.opLoft","SWEPT_FACE",FACE,{"disambiguationData":[OSD([sQuery(id+"F3.wireOp",EDGE,"E20.9.0"),subQ43,subQ42,sQuery(id+"F4.wireOp",EDGE,"E26.9.0"),subQ41,subQ40])]})])],"derivedFrom":subQ9})])]}),makeQuery(id+"F47.opFillet","BLEND_FACE",FACE,{"disambiguationData":[OSD([subQ5,subQ7]),TDD([makeQuery(id+"F42.boolean.opBoolean","COPY",EDGE,{"disambiguationData":[TD([makeQuery(id+"F13.opLoft","SWEPT_FACE",FACE,{"disambiguationData":[OSD([sQuery(id+"F3.wireOp",EDGE,"E20.8.0"),subQ39,subQ38,sQuery(id+"F4.wireOp",EDGE,"E26.8.0"),subQ37,subQ36])]})])],"derivedFrom":subQ9})])]}),makeQuery(id+"F47.opFillet","BLEND_FACE",FACE,{"disambiguationData":[OSD([subQ5,subQ7]),TDD([makeQuery(id+"F42.boolean.opBoolean","COPY",EDGE,{"disambiguationData":[TD([subQ35])],"derivedFrom":subQ9})])]}),makeQuery(id+"F47.opFillet","BLEND_FACE",FACE,{"disambiguationData":[OSD([subQ5,subQ7]),TDD([makeQuery(id+"F42.boolean.opBoolean","COPY",EDGE,{"disambiguationData":[TD([makeQuery(id+"F15.opLoft","SWEPT_FACE",FACE,{"disambiguationData":[OSD([sQuery(id+"F3.wireOp",EDGE,"E20.6.0"),subQ29,subQ28,sQuery(id+"F4.wireOp",EDGE,"E26.6.0"),subQ27,subQ26])]})])],"derivedFrom":subQ9})])]}),makeQuery(id+"F47.opFillet","BLEND_FACE",FACE,{"disambiguationData":[OSD([subQ5,subQ7]),TDD([makeQuery(id+"F42.boolean.opBoolean","COPY",EDGE,{"disambiguationData":[TD([makeQuery(id+"F16.opLoft","SWEPT_FACE",FACE,{"disambiguationData":[OSD([sQuery(id+"F3.wireOp",EDGE,"E20.5.0"),subQ25,subQ24,sQuery(id+"F4.wireOp",EDGE,"E26.5.0"),subQ23,subQ22])]})])],"derivedFrom":subQ9})])]}),makeQuery(id+"F47.opFillet","BLEND_FACE",FACE,{"disambiguationData":[OSD([subQ5,subQ7]),TDD([makeQuery(id+"F42.boolean.opBoolean","COPY",EDGE,{"disambiguationData":[TD([makeQuery(id+"F17.opLoft","SWEPT_FACE",FACE,{"disambiguationData":[OSD([sQuery(id+"F3.wireOp",EDGE,"E20.4.0"),subQ21,subQ20,sQuery(id+"F4.wireOp",EDGE,"E26.4.0"),subQ19,subQ18])]})])],"derivedFrom":subQ9})])]}),makeQuery(id+"F47.opFillet","BLEND_FACE",FACE,{"disambiguationData":[OSD([subQ5,subQ7]),TDD([makeQuery(id+"F42.boolean.opBoolean","COPY",EDGE,{"disambiguationData":[TD([makeQuery(id+"F18.opLoft","SWEPT_FACE",FACE,{"disambiguationData":[OSD([sQuery(id+"F3.wireOp",EDGE,"E20.3.0"),subQ17,subQ16,sQuery(id+"F4.wireOp",EDGE,"E26.3.0"),subQ15,subQ14])]})])],"derivedFrom":subQ9})])]}),makeQuery(id+"F47.opFillet","BLEND_FACE",FACE,{"disambiguationData":[OSD([subQ5,subQ7]),TDD([makeQuery(id+"F42.boolean.opBoolean","COPY",EDGE,{"disambiguationData":[TD([makeQuery(id+"F19.opLoft","SWEPT_FACE",FACE,{"disambiguationData":[OSD([sQuery(id+"F3.wireOp",EDGE,"E20.2.0"),subQ13,subQ12,sQuery(id+"F4.wireOp",EDGE,"E26.2.0"),subQ11,subQ10])]})])],"derivedFrom":subQ9})])]}),makeQuery(id+"F47.opFillet","BLEND_FACE",FACE,{"disambiguationData":[OSD([subQ5,subQ7]),TDD([makeQuery(id+"F42.boolean.opBoolean","COPY",EDGE,{"disambiguationData":[TD([makeQuery(id+"F20.opLoft","SWEPT_FACE",FACE,{"disambiguationData":[OSD([sQuery(id+"F3.wireOp",EDGE,"E20.1.0"),subQ4,subQ3,sQuery(id+"F4.wireOp",EDGE,"E26.1.0"),subQ2,subQ1])]})])],"derivedFrom":subQ9})])]})],"blendedInto":[makeQuery(id+"F47.opFillet","BLEND_FACE",FACE,{"disambiguationData":[OSD([subQ5,subQ7]),TDD([makeQuery(id+"F42.boolean.opBoolean","COPY",EDGE,{"disambiguationData":[TD([makeQuery(id+"F5.opLoft","SWEPT_FACE",FACE,{"disambiguationData":[OSD([subQ71,subQ70,sQuery(id+"F3.wireOp",EDGE,"E18.left"),sQuery(id+"F4.wireOp",EDGE,"E21"),subQ69,subQ68])]})])],"derivedFrom":subQ9})])]}),makeQuery(id+"F47.opFillet","BLEND_FACE",FACE,{"disambiguationData":[OSD([subQ5,subQ7]),TDD([makeQuery(id+"F42.boolean.opBoolean","COPY",EDGE,{"disambiguationData":[TD([makeQuery(id+"F6.opLoft","SWEPT_FACE",FACE,{"disambiguationData":[OSD([sQuery(id+"F3.wireOp",EDGE,"E20.15.0"),subQ67,subQ66,sQuery(id+"F4.wireOp",EDGE,"E26.15.0"),subQ65,subQ64])]})])],"derivedFrom":subQ9})])]}),makeQuery(id+"F47.opFillet","BLEND_FACE",FACE,{"disambiguationData":[OSD([subQ5,subQ7]),TDD([makeQuery(id+"F42.boolean.opBoolean","COPY",EDGE,{"disambiguationData":[TD([makeQuery(id+"F7.opLoft","SWEPT_FACE",FACE,{"disambiguationData":[OSD([sQuery(id+"F3.wireOp",EDGE,"E20.14.0"),subQ63,subQ62,sQuery(id+"F4.wireOp",EDGE,"E26.14.0"),subQ61,subQ60])]})])],"derivedFrom":subQ9})])]}),makeQuery(id+"F47.opFillet","BLEND_FACE",FACE,{"disambiguationData":[OSD([subQ5,subQ7]),TDD([makeQuery(id+"F42.boolean.opBoolean","COPY",EDGE,{"disambiguationData":[TD([makeQuery(id+"F8.opLoft","SWEPT_FACE",FACE,{"disambiguationData":[OSD([sQuery(id+"F3.wireOp",EDGE,"E20.13.0"),subQ59,subQ58,sQuery(id+"F4.wireOp",EDGE,"E26.13.0"),subQ57,subQ56])]})])],"derivedFrom":subQ9})])]}),makeQuery(id+"F47.opFillet","BLEND_FACE",FACE,{"disambiguationData":[OSD([subQ5,subQ7]),TDD([makeQuery(id+"F42.boolean.opBoolean","COPY",EDGE,{"disambiguationData":[TD([makeQuery(id+"F9.opLoft","SWEPT_FACE",FACE,{"disambiguationData":[OSD([sQuery(id+"F3.wireOp",EDGE,"E20.12.0"),subQ55,subQ54,sQuery(id+"F4.wireOp",EDGE,"E26.12.0"),subQ53,subQ52])]})])],"derivedFrom":subQ9})])]}),makeQuery(id+"F47.opFillet","BLEND_FACE",FACE,{"disambiguationData":[OSD([subQ5,subQ7]),TDD([makeQuery(id+"F42.boolean.opBoolean","COPY",EDGE,{"disambiguationData":[TD([makeQuery(id+"F10.opLoft","SWEPT_FACE",FACE,{"disambiguationData":[OSD([sQuery(id+"F3.wireOp",EDGE,"E20.11.0"),subQ51,subQ50,sQuery(id+"F4.wireOp",EDGE,"E26.11.0"),subQ49,subQ48])]})])],"derivedFrom":subQ9})])]}),makeQuery(id+"F47.opFillet","BLEND_FACE",FACE,{"disambiguationData":[OSD([subQ5,subQ7]),TDD([makeQuery(id+"F42.boolean.opBoolean","COPY",EDGE,{"disambiguationData":[TD([makeQuery(id+"F11.opLoft","SWEPT_FACE",FACE,{"disambiguationData":[OSD([sQuery(id+"F3.wireOp",EDGE,"E20.10.0"),subQ47,subQ46,sQuery(id+"F4.wireOp",EDGE,"E26.10.0"),subQ45,subQ44])]})])],"derivedFrom":subQ9})])]}),makeQuery(id+"F47.opFillet","BLEND_FACE",FACE,{"disambiguationData":[OSD([subQ5,subQ7]),TDD([makeQuery(id+"F42.boolean.opBoolean","COPY",EDGE,{"disambiguationData":[TD([makeQuery(id+"F12.opLoft","SWEPT_FACE",FACE,{"disambiguationData":[OSD([sQuery(id+"F3.wireOp",EDGE,"E20.9.0"),subQ43,subQ42,sQuery(id+"F4.wireOp",EDGE,"E26.9.0"),subQ41,subQ40])]})])],"derivedFrom":subQ9})])]}),makeQuery(id+"F47.opFillet","BLEND_FACE",FACE,{"disambiguationData":[OSD([subQ5,subQ7]),TDD([makeQuery(id+"F42.boolean.opBoolean","COPY",EDGE,{"disambiguationData":[TD([makeQuery(id+"F13.opLoft","SWEPT_FACE",FACE,{"disambiguationData":[OSD([sQuery(id+"F3.wireOp",EDGE,"E20.8.0"),subQ39,subQ38,sQuery(id+"F4.wireOp",EDGE,"E26.8.0"),subQ37,subQ36])]})])],"derivedFrom":subQ9})])]}),makeQuery(id+"F47.opFillet","BLEND_FACE",FACE,{"disambiguationData":[OSD([subQ5,subQ7]),TDD([makeQuery(id+"F42.boolean.opBoolean","COPY",EDGE,{"disambiguationData":[TD([subQ35])],"derivedFrom":subQ9})])]}),makeQuery(id+"F47.opFillet","BLEND_FACE",FACE,{"disambiguationData":[OSD([subQ5,subQ7]),TDD([makeQuery(id+"F42.boolean.opBoolean","COPY",EDGE,{"disambiguationData":[TD([makeQuery(id+"F15.opLoft","SWEPT_FACE",FACE,{"disambiguationData":[OSD([sQuery(id+"F3.wireOp",EDGE,"E20.6.0"),subQ29,subQ28,sQuery(id+"F4.wireOp",EDGE,"E26.6.0"),subQ27,subQ26])]})])],"derivedFrom":subQ9})])]}),makeQuery(id+"F47.opFillet","BLEND_FACE",FACE,{"disambiguationData":[OSD([subQ5,subQ7]),TDD([makeQuery(id+"F42.boolean.opBoolean","COPY",EDGE,{"disambiguationData":[TD([makeQuery(id+"F16.opLoft","SWEPT_FACE",FACE,{"disambiguationData":[OSD([sQuery(id+"F3.wireOp",EDGE,"E20.5.0"),subQ25,subQ24,sQuery(id+"F4.wireOp",EDGE,"E26.5.0"),subQ23,subQ22])]})])],"derivedFrom":subQ9})])]}),makeQuery(id+"F47.opFillet","BLEND_FACE",FACE,{"disambiguationData":[OSD([subQ5,subQ7]),TDD([makeQuery(id+"F42.boolean.opBoolean","COPY",EDGE,{"disambiguationData":[TD([makeQuery(id+"F17.opLoft","SWEPT_FACE",FACE,{"disambiguationData":[OSD([sQuery(id+"F3.wireOp",EDGE,"E20.4.0"),subQ21,subQ20,sQuery(id+"F4.wireOp",EDGE,"E26.4.0"),subQ19,subQ18])]})])],"derivedFrom":subQ9})])]}),makeQuery(id+"F47.opFillet","BLEND_FACE",FACE,{"disambiguationData":[OSD([subQ5,subQ7]),TDD([makeQuery(id+"F42.boolean.opBoolean","COPY",EDGE,{"disambiguationData":[TD([makeQuery(id+"F18.opLoft","SWEPT_FACE",FACE,{"disambiguationData":[OSD([sQuery(id+"F3.wireOp",EDGE,"E20.3.0"),subQ17,subQ16,sQuery(id+"F4.wireOp",EDGE,"E26.3.0"),subQ15,subQ14])]})])],"derivedFrom":subQ9})])]}),makeQuery(id+"F47.opFillet","BLEND_FACE",FACE,{"disambiguationData":[OSD([subQ5,subQ7]),TDD([makeQuery(id+"F42.boolean.opBoolean","COPY",EDGE,{"disambiguationData":[TD([makeQuery(id+"F19.opLoft","SWEPT_FACE",FACE,{"disambiguationData":[OSD([sQuery(id+"F3.wireOp",EDGE,"E20.2.0"),subQ13,subQ12,sQuery(id+"F4.wireOp",EDGE,"E26.2.0"),subQ11,subQ10])]})])],"derivedFrom":subQ9})])]}),makeQuery(id+"F47.opFillet","BLEND_FACE",FACE,{"disambiguationData":[OSD([subQ5,subQ7]),TDD([makeQuery(id+"F42.boolean.opBoolean","COPY",EDGE,{"disambiguationData":[TD([makeQuery(id+"F20.opLoft","SWEPT_FACE",FACE,{"disambiguationData":[OSD([sQuery(id+"F3.wireOp",EDGE,"E20.1.0"),subQ4,subQ3,sQuery(id+"F4.wireOp",EDGE,"E26.1.0"),subQ2,subQ1])]})])],"derivedFrom":subQ9})])]})]});}
            var Q63;
            {var subQ0=makeQuery(id+"F40.opExtrude","CAP_FACE",FACE,{"disambiguationData":[OSD([sQuery(id+"F39.wireOp",EDGE,"E29"),sQuery(id+"F39.wireOp",EDGE,"E30")])],"isStart":false});var subQ1=sQuery(id+"F4.wireOp",EDGE,"E26.1.3");var subQ2=sQuery(id+"F4.wireOp",EDGE,"E26.1.2");var subQ3=sQuery(id+"F3.wireOp",EDGE,"E20.1.3");var subQ4=sQuery(id+"F3.wireOp",EDGE,"E20.1.1");var subQ5=sQuery(id+"F41.wireOp",EDGE,"E35");var subQ6=makeQuery(id+"F42.opRevolve","SWEPT_FACE",FACE,{"disambiguationData":[OSD([subQ5])]});var subQ7=sQuery(id+"F41.wireOp",EDGE,"E36");var subQ8=makeQuery(id+"F42.opRevolve","SWEPT_FACE",FACE,{"disambiguationData":[OSD([subQ7])]});var subQ9=makeQuery(id+"F42.opRevolve","SWEPT_EDGE",EDGE,{"disambiguationData":[OSD([subQ5,subQ7])]});var subQ10=sQuery(id+"F4.wireOp",EDGE,"E26.2.3");var subQ11=sQuery(id+"F4.wireOp",EDGE,"E26.2.2");var subQ12=sQuery(id+"F3.wireOp",EDGE,"E20.2.3");var subQ13=sQuery(id+"F3.wireOp",EDGE,"E20.2.1");var subQ14=sQuery(id+"F4.wireOp",EDGE,"E26.3.3");var subQ15=sQuery(id+"F4.wireOp",EDGE,"E26.3.2");var subQ16=sQuery(id+"F3.wireOp",EDGE,"E20.3.3");var subQ17=sQuery(id+"F3.wireOp",EDGE,"E20.3.1");var subQ18=sQuery(id+"F4.wireOp",EDGE,"E26.4.3");var subQ19=sQuery(id+"F4.wireOp",EDGE,"E26.4.2");var subQ20=sQuery(id+"F3.wireOp",EDGE,"E20.4.3");var subQ21=sQuery(id+"F3.wireOp",EDGE,"E20.4.1");var subQ22=sQuery(id+"F4.wireOp",EDGE,"E26.5.3");var subQ23=sQuery(id+"F4.wireOp",EDGE,"E26.5.2");var subQ24=sQuery(id+"F3.wireOp",EDGE,"E20.5.3");var subQ25=sQuery(id+"F3.wireOp",EDGE,"E20.5.1");var subQ26=sQuery(id+"F4.wireOp",EDGE,"E26.6.3");var subQ27=sQuery(id+"F4.wireOp",EDGE,"E26.6.2");var subQ28=sQuery(id+"F3.wireOp",EDGE,"E20.6.3");var subQ29=sQuery(id+"F3.wireOp",EDGE,"E20.6.1");var subQ30=sQuery(id+"F4.wireOp",EDGE,"E26.7.3");var subQ31=sQuery(id+"F4.wireOp",EDGE,"E26.7.2");var subQ32=sQuery(id+"F3.wireOp",EDGE,"E20.7.3");var subQ33=sQuery(id+"F3.wireOp",EDGE,"E20.7.1");var subQ34=sQuery(id+"F4.wireOp",EDGE,"E26.8.3");var subQ35=sQuery(id+"F4.wireOp",EDGE,"E26.8.2");var subQ36=sQuery(id+"F3.wireOp",EDGE,"E20.8.3");var subQ37=sQuery(id+"F3.wireOp",EDGE,"E20.8.1");var subQ39=makeQuery(id+"F13.opLoft","SWEPT_FACE",FACE,{"disambiguationData":[OSD([sQuery(id+"F3.wireOp",EDGE,"E20.8.0"),subQ37,subQ36,sQuery(id+"F4.wireOp",EDGE,"E26.8.0"),subQ35,subQ34])]});var subQ40=sQuery(id+"F4.wireOp",EDGE,"E26.9.3");var subQ41=sQuery(id+"F4.wireOp",EDGE,"E26.9.2");var subQ42=sQuery(id+"F3.wireOp",EDGE,"E20.9.3");var subQ43=sQuery(id+"F3.wireOp",EDGE,"E20.9.1");var subQ44=sQuery(id+"F4.wireOp",EDGE,"E26.10.3");var subQ45=sQuery(id+"F4.wireOp",EDGE,"E26.10.2");var subQ46=sQuery(id+"F3.wireOp",EDGE,"E20.10.3");var subQ47=sQuery(id+"F3.wireOp",EDGE,"E20.10.1");var subQ48=sQuery(id+"F4.wireOp",EDGE,"E26.11.3");var subQ49=sQuery(id+"F4.wireOp",EDGE,"E26.11.2");var subQ50=sQuery(id+"F3.wireOp",EDGE,"E20.11.3");var subQ51=sQuery(id+"F3.wireOp",EDGE,"E20.11.1");var subQ52=sQuery(id+"F4.wireOp",EDGE,"E26.12.3");var subQ53=sQuery(id+"F4.wireOp",EDGE,"E26.12.2");var subQ54=sQuery(id+"F3.wireOp",EDGE,"E20.12.3");var subQ55=sQuery(id+"F3.wireOp",EDGE,"E20.12.1");var subQ56=sQuery(id+"F4.wireOp",EDGE,"E26.13.3");var subQ57=sQuery(id+"F4.wireOp",EDGE,"E26.13.2");var subQ58=sQuery(id+"F3.wireOp",EDGE,"E20.13.3");var subQ59=sQuery(id+"F3.wireOp",EDGE,"E20.13.1");var subQ60=sQuery(id+"F4.wireOp",EDGE,"E26.14.3");var subQ61=sQuery(id+"F4.wireOp",EDGE,"E26.14.2");var subQ62=sQuery(id+"F3.wireOp",EDGE,"E20.14.3");var subQ63=sQuery(id+"F3.wireOp",EDGE,"E20.14.1");var subQ64=sQuery(id+"F4.wireOp",EDGE,"E26.15.3");var subQ65=sQuery(id+"F4.wireOp",EDGE,"E26.15.2");var subQ66=sQuery(id+"F3.wireOp",EDGE,"E20.15.3");var subQ67=sQuery(id+"F3.wireOp",EDGE,"E20.15.1");var subQ68=sQuery(id+"F4.wireOp",EDGE,"E23");var subQ69=sQuery(id+"F4.wireOp",EDGE,"E22");var subQ70=sQuery(id+"F3.wireOp",EDGE,"E18.top");var subQ71=sQuery(id+"F3.wireOp",EDGE,"E18.bottom");var subQ74=makeQuery(id+"F42.boolean.opBoolean","COPY",FACE,{"disambiguationData":[TD([subQ39])],"derivedFrom":subQ6});var subQ75=makeQuery(id+"F13.boolean.opBoolean","INTERSECT",EDGE,{"derivedFrom":[makeQuery(id+"F1.opRevolve","SWEPT_FACE",FACE,{"disambiguationData":[OSD([sQuery(id+"F0.wireOp",EDGE,"E4")])]}),subQ39]});Q63=makeQuery(id+"F48.opFillet","BLEND_EDGE",EDGE,{"blendedFrom":[makeQuery(id+"F47.opFillet","TWEAK_EDGE",EDGE,{"derivedFrom":[makeQuery(id+"F45.opFillet","BLEND_VERTEX",VERTEX,{"blendedFrom":[subQ75,subQ39,subQ74],"blendedInto":[subQ39,subQ74]}),makeQuery(id+"F45.opFillet","BLEND_VERTEX",VERTEX,{"blendedFrom":[subQ75,makeQuery(id+"F42.boolean.opBoolean","MERGE",FACE,{"derivedFrom":[subQ0,subQ8]}),subQ74],"blendedInto":[makeQuery(id+"F42.boolean.opBoolean","MERGE",FACE,{"derivedFrom":[subQ0,subQ8]}),subQ74]})]}),makeQuery(id+"F47.opFillet","BLEND_FACE",FACE,{"disambiguationData":[OSD([subQ5,subQ7]),TDD([makeQuery(id+"F42.boolean.opBoolean","COPY",EDGE,{"disambiguationData":[TD([makeQuery(id+"F5.opLoft","SWEPT_FACE",FACE,{"disambiguationData":[OSD([subQ71,subQ70,sQuery(id+"F3.wireOp",EDGE,"E18.left"),sQuery(id+"F4.wireOp",EDGE,"E21"),subQ69,subQ68])]})])],"derivedFrom":subQ9})])]}),makeQuery(id+"F47.opFillet","BLEND_FACE",FACE,{"disambiguationData":[OSD([subQ5,subQ7]),TDD([makeQuery(id+"F42.boolean.opBoolean","COPY",EDGE,{"disambiguationData":[TD([makeQuery(id+"F6.opLoft","SWEPT_FACE",FACE,{"disambiguationData":[OSD([sQuery(id+"F3.wireOp",EDGE,"E20.15.0"),subQ67,subQ66,sQuery(id+"F4.wireOp",EDGE,"E26.15.0"),subQ65,subQ64])]})])],"derivedFrom":subQ9})])]}),makeQuery(id+"F47.opFillet","BLEND_FACE",FACE,{"disambiguationData":[OSD([subQ5,subQ7]),TDD([makeQuery(id+"F42.boolean.opBoolean","COPY",EDGE,{"disambiguationData":[TD([makeQuery(id+"F7.opLoft","SWEPT_FACE",FACE,{"disambiguationData":[OSD([sQuery(id+"F3.wireOp",EDGE,"E20.14.0"),subQ63,subQ62,sQuery(id+"F4.wireOp",EDGE,"E26.14.0"),subQ61,subQ60])]})])],"derivedFrom":subQ9})])]}),makeQuery(id+"F47.opFillet","BLEND_FACE",FACE,{"disambiguationData":[OSD([subQ5,subQ7]),TDD([makeQuery(id+"F42.boolean.opBoolean","COPY",EDGE,{"disambiguationData":[TD([makeQuery(id+"F8.opLoft","SWEPT_FACE",FACE,{"disambiguationData":[OSD([sQuery(id+"F3.wireOp",EDGE,"E20.13.0"),subQ59,subQ58,sQuery(id+"F4.wireOp",EDGE,"E26.13.0"),subQ57,subQ56])]})])],"derivedFrom":subQ9})])]}),makeQuery(id+"F47.opFillet","BLEND_FACE",FACE,{"disambiguationData":[OSD([subQ5,subQ7]),TDD([makeQuery(id+"F42.boolean.opBoolean","COPY",EDGE,{"disambiguationData":[TD([makeQuery(id+"F9.opLoft","SWEPT_FACE",FACE,{"disambiguationData":[OSD([sQuery(id+"F3.wireOp",EDGE,"E20.12.0"),subQ55,subQ54,sQuery(id+"F4.wireOp",EDGE,"E26.12.0"),subQ53,subQ52])]})])],"derivedFrom":subQ9})])]}),makeQuery(id+"F47.opFillet","BLEND_FACE",FACE,{"disambiguationData":[OSD([subQ5,subQ7]),TDD([makeQuery(id+"F42.boolean.opBoolean","COPY",EDGE,{"disambiguationData":[TD([makeQuery(id+"F10.opLoft","SWEPT_FACE",FACE,{"disambiguationData":[OSD([sQuery(id+"F3.wireOp",EDGE,"E20.11.0"),subQ51,subQ50,sQuery(id+"F4.wireOp",EDGE,"E26.11.0"),subQ49,subQ48])]})])],"derivedFrom":subQ9})])]}),makeQuery(id+"F47.opFillet","BLEND_FACE",FACE,{"disambiguationData":[OSD([subQ5,subQ7]),TDD([makeQuery(id+"F42.boolean.opBoolean","COPY",EDGE,{"disambiguationData":[TD([makeQuery(id+"F11.opLoft","SWEPT_FACE",FACE,{"disambiguationData":[OSD([sQuery(id+"F3.wireOp",EDGE,"E20.10.0"),subQ47,subQ46,sQuery(id+"F4.wireOp",EDGE,"E26.10.0"),subQ45,subQ44])]})])],"derivedFrom":subQ9})])]}),makeQuery(id+"F47.opFillet","BLEND_FACE",FACE,{"disambiguationData":[OSD([subQ5,subQ7]),TDD([makeQuery(id+"F42.boolean.opBoolean","COPY",EDGE,{"disambiguationData":[TD([makeQuery(id+"F12.opLoft","SWEPT_FACE",FACE,{"disambiguationData":[OSD([sQuery(id+"F3.wireOp",EDGE,"E20.9.0"),subQ43,subQ42,sQuery(id+"F4.wireOp",EDGE,"E26.9.0"),subQ41,subQ40])]})])],"derivedFrom":subQ9})])]}),makeQuery(id+"F47.opFillet","BLEND_FACE",FACE,{"disambiguationData":[OSD([subQ5,subQ7]),TDD([makeQuery(id+"F42.boolean.opBoolean","COPY",EDGE,{"disambiguationData":[TD([subQ39])],"derivedFrom":subQ9})])]}),makeQuery(id+"F47.opFillet","BLEND_FACE",FACE,{"disambiguationData":[OSD([subQ5,subQ7]),TDD([makeQuery(id+"F42.boolean.opBoolean","COPY",EDGE,{"disambiguationData":[TD([makeQuery(id+"F14.opLoft","SWEPT_FACE",FACE,{"disambiguationData":[OSD([sQuery(id+"F3.wireOp",EDGE,"E20.7.0"),subQ33,subQ32,sQuery(id+"F4.wireOp",EDGE,"E26.7.0"),subQ31,subQ30])]})])],"derivedFrom":subQ9})])]}),makeQuery(id+"F47.opFillet","BLEND_FACE",FACE,{"disambiguationData":[OSD([subQ5,subQ7]),TDD([makeQuery(id+"F42.boolean.opBoolean","COPY",EDGE,{"disambiguationData":[TD([makeQuery(id+"F15.opLoft","SWEPT_FACE",FACE,{"disambiguationData":[OSD([sQuery(id+"F3.wireOp",EDGE,"E20.6.0"),subQ29,subQ28,sQuery(id+"F4.wireOp",EDGE,"E26.6.0"),subQ27,subQ26])]})])],"derivedFrom":subQ9})])]}),makeQuery(id+"F47.opFillet","BLEND_FACE",FACE,{"disambiguationData":[OSD([subQ5,subQ7]),TDD([makeQuery(id+"F42.boolean.opBoolean","COPY",EDGE,{"disambiguationData":[TD([makeQuery(id+"F16.opLoft","SWEPT_FACE",FACE,{"disambiguationData":[OSD([sQuery(id+"F3.wireOp",EDGE,"E20.5.0"),subQ25,subQ24,sQuery(id+"F4.wireOp",EDGE,"E26.5.0"),subQ23,subQ22])]})])],"derivedFrom":subQ9})])]}),makeQuery(id+"F47.opFillet","BLEND_FACE",FACE,{"disambiguationData":[OSD([subQ5,subQ7]),TDD([makeQuery(id+"F42.boolean.opBoolean","COPY",EDGE,{"disambiguationData":[TD([makeQuery(id+"F17.opLoft","SWEPT_FACE",FACE,{"disambiguationData":[OSD([sQuery(id+"F3.wireOp",EDGE,"E20.4.0"),subQ21,subQ20,sQuery(id+"F4.wireOp",EDGE,"E26.4.0"),subQ19,subQ18])]})])],"derivedFrom":subQ9})])]}),makeQuery(id+"F47.opFillet","BLEND_FACE",FACE,{"disambiguationData":[OSD([subQ5,subQ7]),TDD([makeQuery(id+"F42.boolean.opBoolean","COPY",EDGE,{"disambiguationData":[TD([makeQuery(id+"F18.opLoft","SWEPT_FACE",FACE,{"disambiguationData":[OSD([sQuery(id+"F3.wireOp",EDGE,"E20.3.0"),subQ17,subQ16,sQuery(id+"F4.wireOp",EDGE,"E26.3.0"),subQ15,subQ14])]})])],"derivedFrom":subQ9})])]}),makeQuery(id+"F47.opFillet","BLEND_FACE",FACE,{"disambiguationData":[OSD([subQ5,subQ7]),TDD([makeQuery(id+"F42.boolean.opBoolean","COPY",EDGE,{"disambiguationData":[TD([makeQuery(id+"F19.opLoft","SWEPT_FACE",FACE,{"disambiguationData":[OSD([sQuery(id+"F3.wireOp",EDGE,"E20.2.0"),subQ13,subQ12,sQuery(id+"F4.wireOp",EDGE,"E26.2.0"),subQ11,subQ10])]})])],"derivedFrom":subQ9})])]}),makeQuery(id+"F47.opFillet","BLEND_FACE",FACE,{"disambiguationData":[OSD([subQ5,subQ7]),TDD([makeQuery(id+"F42.boolean.opBoolean","COPY",EDGE,{"disambiguationData":[TD([makeQuery(id+"F20.opLoft","SWEPT_FACE",FACE,{"disambiguationData":[OSD([sQuery(id+"F3.wireOp",EDGE,"E20.1.0"),subQ4,subQ3,sQuery(id+"F4.wireOp",EDGE,"E26.1.0"),subQ2,subQ1])]})])],"derivedFrom":subQ9})])]})],"blendedInto":[makeQuery(id+"F47.opFillet","BLEND_FACE",FACE,{"disambiguationData":[OSD([subQ5,subQ7]),TDD([makeQuery(id+"F42.boolean.opBoolean","COPY",EDGE,{"disambiguationData":[TD([makeQuery(id+"F5.opLoft","SWEPT_FACE",FACE,{"disambiguationData":[OSD([subQ71,subQ70,sQuery(id+"F3.wireOp",EDGE,"E18.left"),sQuery(id+"F4.wireOp",EDGE,"E21"),subQ69,subQ68])]})])],"derivedFrom":subQ9})])]}),makeQuery(id+"F47.opFillet","BLEND_FACE",FACE,{"disambiguationData":[OSD([subQ5,subQ7]),TDD([makeQuery(id+"F42.boolean.opBoolean","COPY",EDGE,{"disambiguationData":[TD([makeQuery(id+"F6.opLoft","SWEPT_FACE",FACE,{"disambiguationData":[OSD([sQuery(id+"F3.wireOp",EDGE,"E20.15.0"),subQ67,subQ66,sQuery(id+"F4.wireOp",EDGE,"E26.15.0"),subQ65,subQ64])]})])],"derivedFrom":subQ9})])]}),makeQuery(id+"F47.opFillet","BLEND_FACE",FACE,{"disambiguationData":[OSD([subQ5,subQ7]),TDD([makeQuery(id+"F42.boolean.opBoolean","COPY",EDGE,{"disambiguationData":[TD([makeQuery(id+"F7.opLoft","SWEPT_FACE",FACE,{"disambiguationData":[OSD([sQuery(id+"F3.wireOp",EDGE,"E20.14.0"),subQ63,subQ62,sQuery(id+"F4.wireOp",EDGE,"E26.14.0"),subQ61,subQ60])]})])],"derivedFrom":subQ9})])]}),makeQuery(id+"F47.opFillet","BLEND_FACE",FACE,{"disambiguationData":[OSD([subQ5,subQ7]),TDD([makeQuery(id+"F42.boolean.opBoolean","COPY",EDGE,{"disambiguationData":[TD([makeQuery(id+"F8.opLoft","SWEPT_FACE",FACE,{"disambiguationData":[OSD([sQuery(id+"F3.wireOp",EDGE,"E20.13.0"),subQ59,subQ58,sQuery(id+"F4.wireOp",EDGE,"E26.13.0"),subQ57,subQ56])]})])],"derivedFrom":subQ9})])]}),makeQuery(id+"F47.opFillet","BLEND_FACE",FACE,{"disambiguationData":[OSD([subQ5,subQ7]),TDD([makeQuery(id+"F42.boolean.opBoolean","COPY",EDGE,{"disambiguationData":[TD([makeQuery(id+"F9.opLoft","SWEPT_FACE",FACE,{"disambiguationData":[OSD([sQuery(id+"F3.wireOp",EDGE,"E20.12.0"),subQ55,subQ54,sQuery(id+"F4.wireOp",EDGE,"E26.12.0"),subQ53,subQ52])]})])],"derivedFrom":subQ9})])]}),makeQuery(id+"F47.opFillet","BLEND_FACE",FACE,{"disambiguationData":[OSD([subQ5,subQ7]),TDD([makeQuery(id+"F42.boolean.opBoolean","COPY",EDGE,{"disambiguationData":[TD([makeQuery(id+"F10.opLoft","SWEPT_FACE",FACE,{"disambiguationData":[OSD([sQuery(id+"F3.wireOp",EDGE,"E20.11.0"),subQ51,subQ50,sQuery(id+"F4.wireOp",EDGE,"E26.11.0"),subQ49,subQ48])]})])],"derivedFrom":subQ9})])]}),makeQuery(id+"F47.opFillet","BLEND_FACE",FACE,{"disambiguationData":[OSD([subQ5,subQ7]),TDD([makeQuery(id+"F42.boolean.opBoolean","COPY",EDGE,{"disambiguationData":[TD([makeQuery(id+"F11.opLoft","SWEPT_FACE",FACE,{"disambiguationData":[OSD([sQuery(id+"F3.wireOp",EDGE,"E20.10.0"),subQ47,subQ46,sQuery(id+"F4.wireOp",EDGE,"E26.10.0"),subQ45,subQ44])]})])],"derivedFrom":subQ9})])]}),makeQuery(id+"F47.opFillet","BLEND_FACE",FACE,{"disambiguationData":[OSD([subQ5,subQ7]),TDD([makeQuery(id+"F42.boolean.opBoolean","COPY",EDGE,{"disambiguationData":[TD([makeQuery(id+"F12.opLoft","SWEPT_FACE",FACE,{"disambiguationData":[OSD([sQuery(id+"F3.wireOp",EDGE,"E20.9.0"),subQ43,subQ42,sQuery(id+"F4.wireOp",EDGE,"E26.9.0"),subQ41,subQ40])]})])],"derivedFrom":subQ9})])]}),makeQuery(id+"F47.opFillet","BLEND_FACE",FACE,{"disambiguationData":[OSD([subQ5,subQ7]),TDD([makeQuery(id+"F42.boolean.opBoolean","COPY",EDGE,{"disambiguationData":[TD([subQ39])],"derivedFrom":subQ9})])]}),makeQuery(id+"F47.opFillet","BLEND_FACE",FACE,{"disambiguationData":[OSD([subQ5,subQ7]),TDD([makeQuery(id+"F42.boolean.opBoolean","COPY",EDGE,{"disambiguationData":[TD([makeQuery(id+"F14.opLoft","SWEPT_FACE",FACE,{"disambiguationData":[OSD([sQuery(id+"F3.wireOp",EDGE,"E20.7.0"),subQ33,subQ32,sQuery(id+"F4.wireOp",EDGE,"E26.7.0"),subQ31,subQ30])]})])],"derivedFrom":subQ9})])]}),makeQuery(id+"F47.opFillet","BLEND_FACE",FACE,{"disambiguationData":[OSD([subQ5,subQ7]),TDD([makeQuery(id+"F42.boolean.opBoolean","COPY",EDGE,{"disambiguationData":[TD([makeQuery(id+"F15.opLoft","SWEPT_FACE",FACE,{"disambiguationData":[OSD([sQuery(id+"F3.wireOp",EDGE,"E20.6.0"),subQ29,subQ28,sQuery(id+"F4.wireOp",EDGE,"E26.6.0"),subQ27,subQ26])]})])],"derivedFrom":subQ9})])]}),makeQuery(id+"F47.opFillet","BLEND_FACE",FACE,{"disambiguationData":[OSD([subQ5,subQ7]),TDD([makeQuery(id+"F42.boolean.opBoolean","COPY",EDGE,{"disambiguationData":[TD([makeQuery(id+"F16.opLoft","SWEPT_FACE",FACE,{"disambiguationData":[OSD([sQuery(id+"F3.wireOp",EDGE,"E20.5.0"),subQ25,subQ24,sQuery(id+"F4.wireOp",EDGE,"E26.5.0"),subQ23,subQ22])]})])],"derivedFrom":subQ9})])]}),makeQuery(id+"F47.opFillet","BLEND_FACE",FACE,{"disambiguationData":[OSD([subQ5,subQ7]),TDD([makeQuery(id+"F42.boolean.opBoolean","COPY",EDGE,{"disambiguationData":[TD([makeQuery(id+"F17.opLoft","SWEPT_FACE",FACE,{"disambiguationData":[OSD([sQuery(id+"F3.wireOp",EDGE,"E20.4.0"),subQ21,subQ20,sQuery(id+"F4.wireOp",EDGE,"E26.4.0"),subQ19,subQ18])]})])],"derivedFrom":subQ9})])]}),makeQuery(id+"F47.opFillet","BLEND_FACE",FACE,{"disambiguationData":[OSD([subQ5,subQ7]),TDD([makeQuery(id+"F42.boolean.opBoolean","COPY",EDGE,{"disambiguationData":[TD([makeQuery(id+"F18.opLoft","SWEPT_FACE",FACE,{"disambiguationData":[OSD([sQuery(id+"F3.wireOp",EDGE,"E20.3.0"),subQ17,subQ16,sQuery(id+"F4.wireOp",EDGE,"E26.3.0"),subQ15,subQ14])]})])],"derivedFrom":subQ9})])]}),makeQuery(id+"F47.opFillet","BLEND_FACE",FACE,{"disambiguationData":[OSD([subQ5,subQ7]),TDD([makeQuery(id+"F42.boolean.opBoolean","COPY",EDGE,{"disambiguationData":[TD([makeQuery(id+"F19.opLoft","SWEPT_FACE",FACE,{"disambiguationData":[OSD([sQuery(id+"F3.wireOp",EDGE,"E20.2.0"),subQ13,subQ12,sQuery(id+"F4.wireOp",EDGE,"E26.2.0"),subQ11,subQ10])]})])],"derivedFrom":subQ9})])]}),makeQuery(id+"F47.opFillet","BLEND_FACE",FACE,{"disambiguationData":[OSD([subQ5,subQ7]),TDD([makeQuery(id+"F42.boolean.opBoolean","COPY",EDGE,{"disambiguationData":[TD([makeQuery(id+"F20.opLoft","SWEPT_FACE",FACE,{"disambiguationData":[OSD([sQuery(id+"F3.wireOp",EDGE,"E20.1.0"),subQ4,subQ3,sQuery(id+"F4.wireOp",EDGE,"E26.1.0"),subQ2,subQ1])]})])],"derivedFrom":subQ9})])]})]});}
            var Q64;
            {var subQ0=sQuery(id+"F4.wireOp",EDGE,"E26.7.3");var subQ1=sQuery(id+"F4.wireOp",EDGE,"E26.7.2");var subQ2=sQuery(id+"F4.wireOp",EDGE,"E26.7.0");var subQ3=sQuery(id+"F3.wireOp",EDGE,"E20.7.3");var subQ4=sQuery(id+"F3.wireOp",EDGE,"E20.7.1");var subQ5=sQuery(id+"F4.wireOp",EDGE,"E26.7.1");var subQ6=makeQuery(id+"F14.opLoft","SWEPT_FACE",FACE,{"disambiguationData":[OSD([subQ4,sQuery(id+"F3.wireOp",EDGE,"E20.7.2"),subQ3,subQ5,subQ1,subQ0])]});var subQ7=sQuery(id+"F41.wireOp",EDGE,"E34");var subQ8=sQuery(id+"F41.wireOp",EDGE,"E32");Q64=makeQuery(id+"F44.opFillet","BLEND_EDGE",EDGE,{"blendedFrom":[makeQuery(id+"F40.boolean.opBoolean","INTERSECT",EDGE,{"derivedFrom":[subQ6,makeQuery(id+"F40.opExtrude","CAP_FACE",FACE,{"disambiguationData":[OSD([sQuery(id+"F39.wireOp",EDGE,"E29"),sQuery(id+"F39.wireOp",EDGE,"E30")])],"isStart":false})]}),makeQuery(id+"F42.boolean.opBoolean","COPY",FACE,{"disambiguationData":[TD([makeQuery(id+"F14.opLoft","SWEPT_FACE",FACE,{"disambiguationData":[OSD([sQuery(id+"F3.wireOp",EDGE,"E20.7.0"),subQ4,subQ3,subQ2,subQ1,subQ0])]})])],"derivedFrom":makeQuery(id+"F42.opRevolve","SWEPT_FACE",FACE,{"disambiguationData":[OSD([subQ8]),TDD([makeQuery(id+"F41.imprint","IMPRINT",EDGE,{"disambiguationData":[TD([[makeQuery(id+"F41.imprint","INTERSECT",VERTEX,{"disambiguationData":[OD(0.0)],"derivedFrom":[subQ8,subQ7]}),-1.0]])],"derivedFrom":subQ8})])]})})],"blendedInto":[makeQuery(id+"F42.boolean.opBoolean","COPY",FACE,{"disambiguationData":[TD([makeQuery(id+"F14.opLoft","SWEPT_FACE",FACE,{"disambiguationData":[OSD([sQuery(id+"F3.wireOp",EDGE,"E20.7.0"),subQ4,subQ3,subQ2,subQ1,subQ0])]})])],"derivedFrom":makeQuery(id+"F42.opRevolve","SWEPT_FACE",FACE,{"disambiguationData":[OSD([subQ8]),TDD([makeQuery(id+"F41.imprint","IMPRINT",EDGE,{"disambiguationData":[TD([[makeQuery(id+"F41.imprint","INTERSECT",VERTEX,{"disambiguationData":[OD(0.0)],"derivedFrom":[subQ8,subQ7]}),-1.0]])],"derivedFrom":subQ8})])]})})]});}
            var Q65;
            {var subQ0=sQuery(id+"F41.wireOp",EDGE,"E34");var subQ1=sQuery(id+"F41.wireOp",EDGE,"E32");Q65=makeQuery(id+"F42.boolean.opBoolean","INTERSECT",EDGE,{"derivedFrom":[makeQuery(id+"F14.opLoft","SWEPT_FACE",FACE,{"disambiguationData":[OSD([sQuery(id+"F3.wireOp",EDGE,"E20.7.0"),sQuery(id+"F3.wireOp",EDGE,"E20.7.1"),sQuery(id+"F3.wireOp",EDGE,"E20.7.3"),sQuery(id+"F4.wireOp",EDGE,"E26.7.0"),sQuery(id+"F4.wireOp",EDGE,"E26.7.2"),sQuery(id+"F4.wireOp",EDGE,"E26.7.3")])]}),makeQuery(id+"F42.opRevolve","SWEPT_FACE",FACE,{"disambiguationData":[OSD([subQ1]),TDD([makeQuery(id+"F41.imprint","IMPRINT",EDGE,{"disambiguationData":[TD([[makeQuery(id+"F41.imprint","INTERSECT",VERTEX,{"disambiguationData":[OD(0.0)],"derivedFrom":[subQ1,subQ0]}),-1.0]])],"derivedFrom":subQ1})])]})]});}
            var Q66;
            {var subQ0=sQuery(id+"F4.wireOp",EDGE,"E26.8.3");var subQ1=sQuery(id+"F4.wireOp",EDGE,"E26.8.2");var subQ2=sQuery(id+"F4.wireOp",EDGE,"E26.8.0");var subQ3=sQuery(id+"F3.wireOp",EDGE,"E20.8.3");var subQ4=sQuery(id+"F3.wireOp",EDGE,"E20.8.1");var subQ5=sQuery(id+"F4.wireOp",EDGE,"E26.8.1");var subQ6=makeQuery(id+"F13.opLoft","SWEPT_FACE",FACE,{"disambiguationData":[OSD([subQ4,sQuery(id+"F3.wireOp",EDGE,"E20.8.2"),subQ3,subQ5,subQ1,subQ0])]});var subQ7=sQuery(id+"F41.wireOp",EDGE,"E34");var subQ8=sQuery(id+"F41.wireOp",EDGE,"E32");Q66=makeQuery(id+"F44.opFillet","BLEND_EDGE",EDGE,{"blendedFrom":[makeQuery(id+"F40.boolean.opBoolean","INTERSECT",EDGE,{"derivedFrom":[subQ6,makeQuery(id+"F40.opExtrude","CAP_FACE",FACE,{"disambiguationData":[OSD([sQuery(id+"F39.wireOp",EDGE,"E29"),sQuery(id+"F39.wireOp",EDGE,"E30")])],"isStart":false})]}),makeQuery(id+"F42.boolean.opBoolean","COPY",FACE,{"disambiguationData":[TD([makeQuery(id+"F13.opLoft","SWEPT_FACE",FACE,{"disambiguationData":[OSD([sQuery(id+"F3.wireOp",EDGE,"E20.8.0"),subQ4,subQ3,subQ2,subQ1,subQ0])]})])],"derivedFrom":makeQuery(id+"F42.opRevolve","SWEPT_FACE",FACE,{"disambiguationData":[OSD([subQ8]),TDD([makeQuery(id+"F41.imprint","IMPRINT",EDGE,{"disambiguationData":[TD([[makeQuery(id+"F41.imprint","INTERSECT",VERTEX,{"disambiguationData":[OD(0.0)],"derivedFrom":[subQ8,subQ7]}),-1.0]])],"derivedFrom":subQ8})])]})})],"blendedInto":[makeQuery(id+"F42.boolean.opBoolean","COPY",FACE,{"disambiguationData":[TD([makeQuery(id+"F13.opLoft","SWEPT_FACE",FACE,{"disambiguationData":[OSD([sQuery(id+"F3.wireOp",EDGE,"E20.8.0"),subQ4,subQ3,subQ2,subQ1,subQ0])]})])],"derivedFrom":makeQuery(id+"F42.opRevolve","SWEPT_FACE",FACE,{"disambiguationData":[OSD([subQ8]),TDD([makeQuery(id+"F41.imprint","IMPRINT",EDGE,{"disambiguationData":[TD([[makeQuery(id+"F41.imprint","INTERSECT",VERTEX,{"disambiguationData":[OD(0.0)],"derivedFrom":[subQ8,subQ7]}),-1.0]])],"derivedFrom":subQ8})])]})})]});}
            var Q67;
            {var subQ0=sQuery(id+"F41.wireOp",EDGE,"E34");var subQ1=sQuery(id+"F41.wireOp",EDGE,"E32");Q67=makeQuery(id+"F42.boolean.opBoolean","INTERSECT",EDGE,{"derivedFrom":[makeQuery(id+"F13.opLoft","SWEPT_FACE",FACE,{"disambiguationData":[OSD([sQuery(id+"F3.wireOp",EDGE,"E20.8.0"),sQuery(id+"F3.wireOp",EDGE,"E20.8.1"),sQuery(id+"F3.wireOp",EDGE,"E20.8.3"),sQuery(id+"F4.wireOp",EDGE,"E26.8.0"),sQuery(id+"F4.wireOp",EDGE,"E26.8.2"),sQuery(id+"F4.wireOp",EDGE,"E26.8.3")])]}),makeQuery(id+"F42.opRevolve","SWEPT_FACE",FACE,{"disambiguationData":[OSD([subQ1]),TDD([makeQuery(id+"F41.imprint","IMPRINT",EDGE,{"disambiguationData":[TD([[makeQuery(id+"F41.imprint","INTERSECT",VERTEX,{"disambiguationData":[OD(0.0)],"derivedFrom":[subQ1,subQ0]}),-1.0]])],"derivedFrom":subQ1})])]})]});}
            var Q68;
            {var subQ0=sQuery(id+"F4.wireOp",EDGE,"E26.9.3");var subQ1=sQuery(id+"F4.wireOp",EDGE,"E26.9.2");var subQ2=sQuery(id+"F4.wireOp",EDGE,"E26.9.0");var subQ3=sQuery(id+"F3.wireOp",EDGE,"E20.9.3");var subQ4=sQuery(id+"F3.wireOp",EDGE,"E20.9.1");var subQ5=sQuery(id+"F4.wireOp",EDGE,"E26.9.1");var subQ6=makeQuery(id+"F12.opLoft","SWEPT_FACE",FACE,{"disambiguationData":[OSD([subQ4,sQuery(id+"F3.wireOp",EDGE,"E20.9.2"),subQ3,subQ5,subQ1,subQ0])]});var subQ7=sQuery(id+"F41.wireOp",EDGE,"E34");var subQ8=sQuery(id+"F41.wireOp",EDGE,"E32");Q68=makeQuery(id+"F44.opFillet","BLEND_EDGE",EDGE,{"blendedFrom":[makeQuery(id+"F40.boolean.opBoolean","INTERSECT",EDGE,{"derivedFrom":[subQ6,makeQuery(id+"F40.opExtrude","CAP_FACE",FACE,{"disambiguationData":[OSD([sQuery(id+"F39.wireOp",EDGE,"E29"),sQuery(id+"F39.wireOp",EDGE,"E30")])],"isStart":false})]}),makeQuery(id+"F42.boolean.opBoolean","COPY",FACE,{"disambiguationData":[TD([makeQuery(id+"F12.opLoft","SWEPT_FACE",FACE,{"disambiguationData":[OSD([sQuery(id+"F3.wireOp",EDGE,"E20.9.0"),subQ4,subQ3,subQ2,subQ1,subQ0])]})])],"derivedFrom":makeQuery(id+"F42.opRevolve","SWEPT_FACE",FACE,{"disambiguationData":[OSD([subQ8]),TDD([makeQuery(id+"F41.imprint","IMPRINT",EDGE,{"disambiguationData":[TD([[makeQuery(id+"F41.imprint","INTERSECT",VERTEX,{"disambiguationData":[OD(0.0)],"derivedFrom":[subQ8,subQ7]}),-1.0]])],"derivedFrom":subQ8})])]})})],"blendedInto":[makeQuery(id+"F42.boolean.opBoolean","COPY",FACE,{"disambiguationData":[TD([makeQuery(id+"F12.opLoft","SWEPT_FACE",FACE,{"disambiguationData":[OSD([sQuery(id+"F3.wireOp",EDGE,"E20.9.0"),subQ4,subQ3,subQ2,subQ1,subQ0])]})])],"derivedFrom":makeQuery(id+"F42.opRevolve","SWEPT_FACE",FACE,{"disambiguationData":[OSD([subQ8]),TDD([makeQuery(id+"F41.imprint","IMPRINT",EDGE,{"disambiguationData":[TD([[makeQuery(id+"F41.imprint","INTERSECT",VERTEX,{"disambiguationData":[OD(0.0)],"derivedFrom":[subQ8,subQ7]}),-1.0]])],"derivedFrom":subQ8})])]})})]});}
            var Q69;
            {var subQ0=sQuery(id+"F41.wireOp",EDGE,"E34");var subQ1=sQuery(id+"F41.wireOp",EDGE,"E32");Q69=makeQuery(id+"F42.boolean.opBoolean","INTERSECT",EDGE,{"derivedFrom":[makeQuery(id+"F12.opLoft","SWEPT_FACE",FACE,{"disambiguationData":[OSD([sQuery(id+"F3.wireOp",EDGE,"E20.9.0"),sQuery(id+"F3.wireOp",EDGE,"E20.9.1"),sQuery(id+"F3.wireOp",EDGE,"E20.9.3"),sQuery(id+"F4.wireOp",EDGE,"E26.9.0"),sQuery(id+"F4.wireOp",EDGE,"E26.9.2"),sQuery(id+"F4.wireOp",EDGE,"E26.9.3")])]}),makeQuery(id+"F42.opRevolve","SWEPT_FACE",FACE,{"disambiguationData":[OSD([subQ1]),TDD([makeQuery(id+"F41.imprint","IMPRINT",EDGE,{"disambiguationData":[TD([[makeQuery(id+"F41.imprint","INTERSECT",VERTEX,{"disambiguationData":[OD(0.0)],"derivedFrom":[subQ1,subQ0]}),-1.0]])],"derivedFrom":subQ1})])]})]});}
            var Q70;
            {var subQ0=sQuery(id+"F4.wireOp",EDGE,"E26.10.0");var subQ1=sQuery(id+"F4.wireOp",EDGE,"E26.10.1");var subQ2=sQuery(id+"F4.wireOp",EDGE,"E26.10.2");var subQ3=sQuery(id+"F4.wireOp",EDGE,"E26.10.3");var subQ4=sQuery(id+"F3.wireOp",EDGE,"E20.10.3");var subQ5=sQuery(id+"F3.wireOp",EDGE,"E20.10.1");var subQ6=makeQuery(id+"F11.opLoft","SWEPT_FACE",FACE,{"disambiguationData":[OSD([subQ5,sQuery(id+"F3.wireOp",EDGE,"E20.10.2"),subQ4,subQ1,subQ2,subQ3])]});var subQ7=sQuery(id+"F41.wireOp",EDGE,"E34");var subQ8=sQuery(id+"F41.wireOp",EDGE,"E32");Q70=makeQuery(id+"F44.opFillet","BLEND_EDGE",EDGE,{"blendedFrom":[makeQuery(id+"F40.boolean.opBoolean","INTERSECT",EDGE,{"derivedFrom":[subQ6,makeQuery(id+"F40.opExtrude","CAP_FACE",FACE,{"disambiguationData":[OSD([sQuery(id+"F39.wireOp",EDGE,"E29"),sQuery(id+"F39.wireOp",EDGE,"E30")])],"isStart":false})]}),makeQuery(id+"F42.boolean.opBoolean","COPY",FACE,{"disambiguationData":[TD([makeQuery(id+"F11.opLoft","SWEPT_FACE",FACE,{"disambiguationData":[OSD([sQuery(id+"F3.wireOp",EDGE,"E20.10.0"),subQ5,subQ4,subQ0,subQ2,subQ3])]})])],"derivedFrom":makeQuery(id+"F42.opRevolve","SWEPT_FACE",FACE,{"disambiguationData":[OSD([subQ8]),TDD([makeQuery(id+"F41.imprint","IMPRINT",EDGE,{"disambiguationData":[TD([[makeQuery(id+"F41.imprint","INTERSECT",VERTEX,{"disambiguationData":[OD(0.0)],"derivedFrom":[subQ8,subQ7]}),-1.0]])],"derivedFrom":subQ8})])]})})],"blendedInto":[makeQuery(id+"F42.boolean.opBoolean","COPY",FACE,{"disambiguationData":[TD([makeQuery(id+"F11.opLoft","SWEPT_FACE",FACE,{"disambiguationData":[OSD([sQuery(id+"F3.wireOp",EDGE,"E20.10.0"),subQ5,subQ4,subQ0,subQ2,subQ3])]})])],"derivedFrom":makeQuery(id+"F42.opRevolve","SWEPT_FACE",FACE,{"disambiguationData":[OSD([subQ8]),TDD([makeQuery(id+"F41.imprint","IMPRINT",EDGE,{"disambiguationData":[TD([[makeQuery(id+"F41.imprint","INTERSECT",VERTEX,{"disambiguationData":[OD(0.0)],"derivedFrom":[subQ8,subQ7]}),-1.0]])],"derivedFrom":subQ8})])]})})]});}
            var Q71;
            {var subQ0=sQuery(id+"F41.wireOp",EDGE,"E34");var subQ1=sQuery(id+"F41.wireOp",EDGE,"E32");Q71=makeQuery(id+"F42.boolean.opBoolean","INTERSECT",EDGE,{"derivedFrom":[makeQuery(id+"F11.opLoft","SWEPT_FACE",FACE,{"disambiguationData":[OSD([sQuery(id+"F3.wireOp",EDGE,"E20.10.0"),sQuery(id+"F3.wireOp",EDGE,"E20.10.1"),sQuery(id+"F3.wireOp",EDGE,"E20.10.3"),sQuery(id+"F4.wireOp",EDGE,"E26.10.0"),sQuery(id+"F4.wireOp",EDGE,"E26.10.2"),sQuery(id+"F4.wireOp",EDGE,"E26.10.3")])]}),makeQuery(id+"F42.opRevolve","SWEPT_FACE",FACE,{"disambiguationData":[OSD([subQ1]),TDD([makeQuery(id+"F41.imprint","IMPRINT",EDGE,{"disambiguationData":[TD([[makeQuery(id+"F41.imprint","INTERSECT",VERTEX,{"disambiguationData":[OD(0.0)],"derivedFrom":[subQ1,subQ0]}),-1.0]])],"derivedFrom":subQ1})])]})]});}
            var Q72;
            {var subQ0=sQuery(id+"F4.wireOp",EDGE,"E26.11.0");var subQ1=sQuery(id+"F4.wireOp",EDGE,"E26.11.1");var subQ2=sQuery(id+"F4.wireOp",EDGE,"E26.11.2");var subQ3=sQuery(id+"F4.wireOp",EDGE,"E26.11.3");var subQ4=sQuery(id+"F3.wireOp",EDGE,"E20.11.3");var subQ5=sQuery(id+"F3.wireOp",EDGE,"E20.11.1");var subQ6=makeQuery(id+"F10.opLoft","SWEPT_FACE",FACE,{"disambiguationData":[OSD([subQ5,sQuery(id+"F3.wireOp",EDGE,"E20.11.2"),subQ4,subQ1,subQ2,subQ3])]});var subQ7=sQuery(id+"F41.wireOp",EDGE,"E34");var subQ8=sQuery(id+"F41.wireOp",EDGE,"E32");Q72=makeQuery(id+"F44.opFillet","BLEND_EDGE",EDGE,{"blendedFrom":[makeQuery(id+"F40.boolean.opBoolean","INTERSECT",EDGE,{"derivedFrom":[subQ6,makeQuery(id+"F40.opExtrude","CAP_FACE",FACE,{"disambiguationData":[OSD([sQuery(id+"F39.wireOp",EDGE,"E29"),sQuery(id+"F39.wireOp",EDGE,"E30")])],"isStart":false})]}),makeQuery(id+"F42.boolean.opBoolean","COPY",FACE,{"disambiguationData":[TD([makeQuery(id+"F10.opLoft","SWEPT_FACE",FACE,{"disambiguationData":[OSD([sQuery(id+"F3.wireOp",EDGE,"E20.11.0"),subQ5,subQ4,subQ0,subQ2,subQ3])]})])],"derivedFrom":makeQuery(id+"F42.opRevolve","SWEPT_FACE",FACE,{"disambiguationData":[OSD([subQ8]),TDD([makeQuery(id+"F41.imprint","IMPRINT",EDGE,{"disambiguationData":[TD([[makeQuery(id+"F41.imprint","INTERSECT",VERTEX,{"disambiguationData":[OD(0.0)],"derivedFrom":[subQ8,subQ7]}),-1.0]])],"derivedFrom":subQ8})])]})})],"blendedInto":[makeQuery(id+"F42.boolean.opBoolean","COPY",FACE,{"disambiguationData":[TD([makeQuery(id+"F10.opLoft","SWEPT_FACE",FACE,{"disambiguationData":[OSD([sQuery(id+"F3.wireOp",EDGE,"E20.11.0"),subQ5,subQ4,subQ0,subQ2,subQ3])]})])],"derivedFrom":makeQuery(id+"F42.opRevolve","SWEPT_FACE",FACE,{"disambiguationData":[OSD([subQ8]),TDD([makeQuery(id+"F41.imprint","IMPRINT",EDGE,{"disambiguationData":[TD([[makeQuery(id+"F41.imprint","INTERSECT",VERTEX,{"disambiguationData":[OD(0.0)],"derivedFrom":[subQ8,subQ7]}),-1.0]])],"derivedFrom":subQ8})])]})})]});}
            var Q73;
            {var subQ0=sQuery(id+"F41.wireOp",EDGE,"E34");var subQ1=sQuery(id+"F41.wireOp",EDGE,"E32");Q73=makeQuery(id+"F42.boolean.opBoolean","INTERSECT",EDGE,{"derivedFrom":[makeQuery(id+"F10.opLoft","SWEPT_FACE",FACE,{"disambiguationData":[OSD([sQuery(id+"F3.wireOp",EDGE,"E20.11.0"),sQuery(id+"F3.wireOp",EDGE,"E20.11.1"),sQuery(id+"F3.wireOp",EDGE,"E20.11.3"),sQuery(id+"F4.wireOp",EDGE,"E26.11.0"),sQuery(id+"F4.wireOp",EDGE,"E26.11.2"),sQuery(id+"F4.wireOp",EDGE,"E26.11.3")])]}),makeQuery(id+"F42.opRevolve","SWEPT_FACE",FACE,{"disambiguationData":[OSD([subQ1]),TDD([makeQuery(id+"F41.imprint","IMPRINT",EDGE,{"disambiguationData":[TD([[makeQuery(id+"F41.imprint","INTERSECT",VERTEX,{"disambiguationData":[OD(0.0)],"derivedFrom":[subQ1,subQ0]}),-1.0]])],"derivedFrom":subQ1})])]})]});}
            var Q74;
            {var subQ0=sQuery(id+"F4.wireOp",EDGE,"E26.12.0");var subQ1=sQuery(id+"F4.wireOp",EDGE,"E26.12.2");var subQ2=sQuery(id+"F4.wireOp",EDGE,"E26.12.1");var subQ3=sQuery(id+"F4.wireOp",EDGE,"E26.12.3");var subQ4=sQuery(id+"F3.wireOp",EDGE,"E20.12.3");var subQ5=sQuery(id+"F3.wireOp",EDGE,"E20.12.1");var subQ6=makeQuery(id+"F9.opLoft","SWEPT_FACE",FACE,{"disambiguationData":[OSD([subQ5,sQuery(id+"F3.wireOp",EDGE,"E20.12.2"),subQ4,subQ2,subQ1,subQ3])]});var subQ7=sQuery(id+"F41.wireOp",EDGE,"E34");var subQ8=sQuery(id+"F41.wireOp",EDGE,"E32");Q74=makeQuery(id+"F44.opFillet","BLEND_EDGE",EDGE,{"blendedFrom":[makeQuery(id+"F40.boolean.opBoolean","INTERSECT",EDGE,{"derivedFrom":[subQ6,makeQuery(id+"F40.opExtrude","CAP_FACE",FACE,{"disambiguationData":[OSD([sQuery(id+"F39.wireOp",EDGE,"E29"),sQuery(id+"F39.wireOp",EDGE,"E30")])],"isStart":false})]}),makeQuery(id+"F42.boolean.opBoolean","COPY",FACE,{"disambiguationData":[TD([makeQuery(id+"F9.opLoft","SWEPT_FACE",FACE,{"disambiguationData":[OSD([sQuery(id+"F3.wireOp",EDGE,"E20.12.0"),subQ5,subQ4,subQ0,subQ1,subQ3])]})])],"derivedFrom":makeQuery(id+"F42.opRevolve","SWEPT_FACE",FACE,{"disambiguationData":[OSD([subQ8]),TDD([makeQuery(id+"F41.imprint","IMPRINT",EDGE,{"disambiguationData":[TD([[makeQuery(id+"F41.imprint","INTERSECT",VERTEX,{"disambiguationData":[OD(0.0)],"derivedFrom":[subQ8,subQ7]}),-1.0]])],"derivedFrom":subQ8})])]})})],"blendedInto":[makeQuery(id+"F42.boolean.opBoolean","COPY",FACE,{"disambiguationData":[TD([makeQuery(id+"F9.opLoft","SWEPT_FACE",FACE,{"disambiguationData":[OSD([sQuery(id+"F3.wireOp",EDGE,"E20.12.0"),subQ5,subQ4,subQ0,subQ1,subQ3])]})])],"derivedFrom":makeQuery(id+"F42.opRevolve","SWEPT_FACE",FACE,{"disambiguationData":[OSD([subQ8]),TDD([makeQuery(id+"F41.imprint","IMPRINT",EDGE,{"disambiguationData":[TD([[makeQuery(id+"F41.imprint","INTERSECT",VERTEX,{"disambiguationData":[OD(0.0)],"derivedFrom":[subQ8,subQ7]}),-1.0]])],"derivedFrom":subQ8})])]})})]});}
            var Q75;
            {var subQ0=sQuery(id+"F41.wireOp",EDGE,"E34");var subQ1=sQuery(id+"F41.wireOp",EDGE,"E32");Q75=makeQuery(id+"F42.boolean.opBoolean","INTERSECT",EDGE,{"derivedFrom":[makeQuery(id+"F9.opLoft","SWEPT_FACE",FACE,{"disambiguationData":[OSD([sQuery(id+"F3.wireOp",EDGE,"E20.12.0"),sQuery(id+"F3.wireOp",EDGE,"E20.12.1"),sQuery(id+"F3.wireOp",EDGE,"E20.12.3"),sQuery(id+"F4.wireOp",EDGE,"E26.12.0"),sQuery(id+"F4.wireOp",EDGE,"E26.12.2"),sQuery(id+"F4.wireOp",EDGE,"E26.12.3")])]}),makeQuery(id+"F42.opRevolve","SWEPT_FACE",FACE,{"disambiguationData":[OSD([subQ1]),TDD([makeQuery(id+"F41.imprint","IMPRINT",EDGE,{"disambiguationData":[TD([[makeQuery(id+"F41.imprint","INTERSECT",VERTEX,{"disambiguationData":[OD(0.0)],"derivedFrom":[subQ1,subQ0]}),-1.0]])],"derivedFrom":subQ1})])]})]});}
            var Q76;
            {var subQ0=sQuery(id+"F4.wireOp",EDGE,"E26.13.3");var subQ1=sQuery(id+"F4.wireOp",EDGE,"E26.13.2");var subQ2=sQuery(id+"F4.wireOp",EDGE,"E26.13.1");var subQ3=sQuery(id+"F3.wireOp",EDGE,"E20.13.3");var subQ4=sQuery(id+"F3.wireOp",EDGE,"E20.13.1");var subQ5=makeQuery(id+"F8.opLoft","SWEPT_FACE",FACE,{"disambiguationData":[OSD([subQ4,sQuery(id+"F3.wireOp",EDGE,"E20.13.2"),subQ3,subQ2,subQ1,subQ0])]});var subQ6=sQuery(id+"F4.wireOp",EDGE,"E26.13.0");var subQ7=sQuery(id+"F41.wireOp",EDGE,"E34");var subQ8=sQuery(id+"F41.wireOp",EDGE,"E32");Q76=makeQuery(id+"F44.opFillet","BLEND_EDGE",EDGE,{"blendedFrom":[makeQuery(id+"F40.boolean.opBoolean","INTERSECT",EDGE,{"derivedFrom":[subQ5,makeQuery(id+"F40.opExtrude","CAP_FACE",FACE,{"disambiguationData":[OSD([sQuery(id+"F39.wireOp",EDGE,"E29"),sQuery(id+"F39.wireOp",EDGE,"E30")])],"isStart":false})]}),makeQuery(id+"F42.boolean.opBoolean","COPY",FACE,{"disambiguationData":[TD([makeQuery(id+"F8.opLoft","SWEPT_FACE",FACE,{"disambiguationData":[OSD([sQuery(id+"F3.wireOp",EDGE,"E20.13.0"),subQ4,subQ3,subQ6,subQ1,subQ0])]})])],"derivedFrom":makeQuery(id+"F42.opRevolve","SWEPT_FACE",FACE,{"disambiguationData":[OSD([subQ8]),TDD([makeQuery(id+"F41.imprint","IMPRINT",EDGE,{"disambiguationData":[TD([[makeQuery(id+"F41.imprint","INTERSECT",VERTEX,{"disambiguationData":[OD(0.0)],"derivedFrom":[subQ8,subQ7]}),-1.0]])],"derivedFrom":subQ8})])]})})],"blendedInto":[makeQuery(id+"F42.boolean.opBoolean","COPY",FACE,{"disambiguationData":[TD([makeQuery(id+"F8.opLoft","SWEPT_FACE",FACE,{"disambiguationData":[OSD([sQuery(id+"F3.wireOp",EDGE,"E20.13.0"),subQ4,subQ3,subQ6,subQ1,subQ0])]})])],"derivedFrom":makeQuery(id+"F42.opRevolve","SWEPT_FACE",FACE,{"disambiguationData":[OSD([subQ8]),TDD([makeQuery(id+"F41.imprint","IMPRINT",EDGE,{"disambiguationData":[TD([[makeQuery(id+"F41.imprint","INTERSECT",VERTEX,{"disambiguationData":[OD(0.0)],"derivedFrom":[subQ8,subQ7]}),-1.0]])],"derivedFrom":subQ8})])]})})]});}
            var Q77;
            {var subQ0=sQuery(id+"F41.wireOp",EDGE,"E34");var subQ1=sQuery(id+"F41.wireOp",EDGE,"E32");Q77=makeQuery(id+"F42.boolean.opBoolean","INTERSECT",EDGE,{"derivedFrom":[makeQuery(id+"F8.opLoft","SWEPT_FACE",FACE,{"disambiguationData":[OSD([sQuery(id+"F3.wireOp",EDGE,"E20.13.0"),sQuery(id+"F3.wireOp",EDGE,"E20.13.1"),sQuery(id+"F3.wireOp",EDGE,"E20.13.3"),sQuery(id+"F4.wireOp",EDGE,"E26.13.0"),sQuery(id+"F4.wireOp",EDGE,"E26.13.2"),sQuery(id+"F4.wireOp",EDGE,"E26.13.3")])]}),makeQuery(id+"F42.opRevolve","SWEPT_FACE",FACE,{"disambiguationData":[OSD([subQ1]),TDD([makeQuery(id+"F41.imprint","IMPRINT",EDGE,{"disambiguationData":[TD([[makeQuery(id+"F41.imprint","INTERSECT",VERTEX,{"disambiguationData":[OD(0.0)],"derivedFrom":[subQ1,subQ0]}),-1.0]])],"derivedFrom":subQ1})])]})]});}
            var Q78;
            {var subQ0=sQuery(id+"F4.wireOp",EDGE,"E26.14.0");var subQ1=sQuery(id+"F4.wireOp",EDGE,"E26.14.2");var subQ2=sQuery(id+"F4.wireOp",EDGE,"E26.14.1");var subQ3=sQuery(id+"F4.wireOp",EDGE,"E26.14.3");var subQ4=sQuery(id+"F3.wireOp",EDGE,"E20.14.3");var subQ5=sQuery(id+"F3.wireOp",EDGE,"E20.14.1");var subQ6=makeQuery(id+"F7.opLoft","SWEPT_FACE",FACE,{"disambiguationData":[OSD([subQ5,sQuery(id+"F3.wireOp",EDGE,"E20.14.2"),subQ4,subQ2,subQ1,subQ3])]});var subQ7=sQuery(id+"F41.wireOp",EDGE,"E34");var subQ8=sQuery(id+"F41.wireOp",EDGE,"E32");Q78=makeQuery(id+"F44.opFillet","BLEND_EDGE",EDGE,{"blendedFrom":[makeQuery(id+"F40.boolean.opBoolean","INTERSECT",EDGE,{"derivedFrom":[subQ6,makeQuery(id+"F40.opExtrude","CAP_FACE",FACE,{"disambiguationData":[OSD([sQuery(id+"F39.wireOp",EDGE,"E29"),sQuery(id+"F39.wireOp",EDGE,"E30")])],"isStart":false})]}),makeQuery(id+"F42.boolean.opBoolean","COPY",FACE,{"disambiguationData":[TD([makeQuery(id+"F7.opLoft","SWEPT_FACE",FACE,{"disambiguationData":[OSD([sQuery(id+"F3.wireOp",EDGE,"E20.14.0"),subQ5,subQ4,subQ0,subQ1,subQ3])]})])],"derivedFrom":makeQuery(id+"F42.opRevolve","SWEPT_FACE",FACE,{"disambiguationData":[OSD([subQ8]),TDD([makeQuery(id+"F41.imprint","IMPRINT",EDGE,{"disambiguationData":[TD([[makeQuery(id+"F41.imprint","INTERSECT",VERTEX,{"disambiguationData":[OD(0.0)],"derivedFrom":[subQ8,subQ7]}),-1.0]])],"derivedFrom":subQ8})])]})})],"blendedInto":[makeQuery(id+"F42.boolean.opBoolean","COPY",FACE,{"disambiguationData":[TD([makeQuery(id+"F7.opLoft","SWEPT_FACE",FACE,{"disambiguationData":[OSD([sQuery(id+"F3.wireOp",EDGE,"E20.14.0"),subQ5,subQ4,subQ0,subQ1,subQ3])]})])],"derivedFrom":makeQuery(id+"F42.opRevolve","SWEPT_FACE",FACE,{"disambiguationData":[OSD([subQ8]),TDD([makeQuery(id+"F41.imprint","IMPRINT",EDGE,{"disambiguationData":[TD([[makeQuery(id+"F41.imprint","INTERSECT",VERTEX,{"disambiguationData":[OD(0.0)],"derivedFrom":[subQ8,subQ7]}),-1.0]])],"derivedFrom":subQ8})])]})})]});}
            var Q79;
            {var subQ0=sQuery(id+"F41.wireOp",EDGE,"E34");var subQ1=sQuery(id+"F41.wireOp",EDGE,"E32");Q79=makeQuery(id+"F42.boolean.opBoolean","INTERSECT",EDGE,{"derivedFrom":[makeQuery(id+"F7.opLoft","SWEPT_FACE",FACE,{"disambiguationData":[OSD([sQuery(id+"F3.wireOp",EDGE,"E20.14.0"),sQuery(id+"F3.wireOp",EDGE,"E20.14.1"),sQuery(id+"F3.wireOp",EDGE,"E20.14.3"),sQuery(id+"F4.wireOp",EDGE,"E26.14.0"),sQuery(id+"F4.wireOp",EDGE,"E26.14.2"),sQuery(id+"F4.wireOp",EDGE,"E26.14.3")])]}),makeQuery(id+"F42.opRevolve","SWEPT_FACE",FACE,{"disambiguationData":[OSD([subQ1]),TDD([makeQuery(id+"F41.imprint","IMPRINT",EDGE,{"disambiguationData":[TD([[makeQuery(id+"F41.imprint","INTERSECT",VERTEX,{"disambiguationData":[OD(0.0)],"derivedFrom":[subQ1,subQ0]}),-1.0]])],"derivedFrom":subQ1})])]})]});}
            var Q80;
            {var subQ0=sQuery(id+"F4.wireOp",EDGE,"E26.15.3");var subQ1=sQuery(id+"F4.wireOp",EDGE,"E26.15.2");var subQ2=sQuery(id+"F4.wireOp",EDGE,"E26.15.0");var subQ3=sQuery(id+"F3.wireOp",EDGE,"E20.15.3");var subQ4=sQuery(id+"F3.wireOp",EDGE,"E20.15.1");var subQ5=sQuery(id+"F4.wireOp",EDGE,"E26.15.1");var subQ6=makeQuery(id+"F6.opLoft","SWEPT_FACE",FACE,{"disambiguationData":[OSD([subQ4,sQuery(id+"F3.wireOp",EDGE,"E20.15.2"),subQ3,subQ5,subQ1,subQ0])]});var subQ7=sQuery(id+"F41.wireOp",EDGE,"E34");var subQ8=sQuery(id+"F41.wireOp",EDGE,"E32");Q80=makeQuery(id+"F44.opFillet","BLEND_EDGE",EDGE,{"blendedFrom":[makeQuery(id+"F40.boolean.opBoolean","INTERSECT",EDGE,{"derivedFrom":[subQ6,makeQuery(id+"F40.opExtrude","CAP_FACE",FACE,{"disambiguationData":[OSD([sQuery(id+"F39.wireOp",EDGE,"E29"),sQuery(id+"F39.wireOp",EDGE,"E30")])],"isStart":false})]}),makeQuery(id+"F42.boolean.opBoolean","COPY",FACE,{"disambiguationData":[TD([makeQuery(id+"F6.opLoft","SWEPT_FACE",FACE,{"disambiguationData":[OSD([sQuery(id+"F3.wireOp",EDGE,"E20.15.0"),subQ4,subQ3,subQ2,subQ1,subQ0])]})])],"derivedFrom":makeQuery(id+"F42.opRevolve","SWEPT_FACE",FACE,{"disambiguationData":[OSD([subQ8]),TDD([makeQuery(id+"F41.imprint","IMPRINT",EDGE,{"disambiguationData":[TD([[makeQuery(id+"F41.imprint","INTERSECT",VERTEX,{"disambiguationData":[OD(0.0)],"derivedFrom":[subQ8,subQ7]}),-1.0]])],"derivedFrom":subQ8})])]})})],"blendedInto":[makeQuery(id+"F42.boolean.opBoolean","COPY",FACE,{"disambiguationData":[TD([makeQuery(id+"F6.opLoft","SWEPT_FACE",FACE,{"disambiguationData":[OSD([sQuery(id+"F3.wireOp",EDGE,"E20.15.0"),subQ4,subQ3,subQ2,subQ1,subQ0])]})])],"derivedFrom":makeQuery(id+"F42.opRevolve","SWEPT_FACE",FACE,{"disambiguationData":[OSD([subQ8]),TDD([makeQuery(id+"F41.imprint","IMPRINT",EDGE,{"disambiguationData":[TD([[makeQuery(id+"F41.imprint","INTERSECT",VERTEX,{"disambiguationData":[OD(0.0)],"derivedFrom":[subQ8,subQ7]}),-1.0]])],"derivedFrom":subQ8})])]})})]});}
            var Q81;
            {var subQ0=sQuery(id+"F41.wireOp",EDGE,"E34");var subQ1=sQuery(id+"F41.wireOp",EDGE,"E32");Q81=makeQuery(id+"F42.boolean.opBoolean","INTERSECT",EDGE,{"derivedFrom":[makeQuery(id+"F6.opLoft","SWEPT_FACE",FACE,{"disambiguationData":[OSD([sQuery(id+"F3.wireOp",EDGE,"E20.15.0"),sQuery(id+"F3.wireOp",EDGE,"E20.15.1"),sQuery(id+"F3.wireOp",EDGE,"E20.15.3"),sQuery(id+"F4.wireOp",EDGE,"E26.15.0"),sQuery(id+"F4.wireOp",EDGE,"E26.15.2"),sQuery(id+"F4.wireOp",EDGE,"E26.15.3")])]}),makeQuery(id+"F42.opRevolve","SWEPT_FACE",FACE,{"disambiguationData":[OSD([subQ1]),TDD([makeQuery(id+"F41.imprint","IMPRINT",EDGE,{"disambiguationData":[TD([[makeQuery(id+"F41.imprint","INTERSECT",VERTEX,{"disambiguationData":[OD(0.0)],"derivedFrom":[subQ1,subQ0]}),-1.0]])],"derivedFrom":subQ1})])]})]});}
            var Q82;
            {var subQ0=sQuery(id+"F4.wireOp",EDGE,"E23");var subQ1=sQuery(id+"F4.wireOp",EDGE,"E22");var subQ2=sQuery(id+"F4.wireOp",EDGE,"E21");var subQ3=sQuery(id+"F3.wireOp",EDGE,"E18.top");var subQ4=sQuery(id+"F3.wireOp",EDGE,"E18.bottom");var subQ5=sQuery(id+"F4.wireOp",EDGE,"E24");var subQ6=makeQuery(id+"F5.opLoft","SWEPT_FACE",FACE,{"disambiguationData":[OSD([subQ4,subQ3,sQuery(id+"F3.wireOp",EDGE,"E18.right"),subQ1,subQ0,subQ5])]});var subQ7=sQuery(id+"F41.wireOp",EDGE,"E34");var subQ8=sQuery(id+"F41.wireOp",EDGE,"E32");Q82=makeQuery(id+"F44.opFillet","BLEND_EDGE",EDGE,{"blendedFrom":[makeQuery(id+"F40.boolean.opBoolean","INTERSECT",EDGE,{"derivedFrom":[subQ6,makeQuery(id+"F40.opExtrude","CAP_FACE",FACE,{"disambiguationData":[OSD([sQuery(id+"F39.wireOp",EDGE,"E29"),sQuery(id+"F39.wireOp",EDGE,"E30")])],"isStart":false})]}),makeQuery(id+"F42.boolean.opBoolean","COPY",FACE,{"disambiguationData":[TD([makeQuery(id+"F5.opLoft","SWEPT_FACE",FACE,{"disambiguationData":[OSD([subQ4,subQ3,sQuery(id+"F3.wireOp",EDGE,"E18.left"),subQ2,subQ1,subQ0])]})])],"derivedFrom":makeQuery(id+"F42.opRevolve","SWEPT_FACE",FACE,{"disambiguationData":[OSD([subQ8]),TDD([makeQuery(id+"F41.imprint","IMPRINT",EDGE,{"disambiguationData":[TD([[makeQuery(id+"F41.imprint","INTERSECT",VERTEX,{"disambiguationData":[OD(0.0)],"derivedFrom":[subQ8,subQ7]}),-1.0]])],"derivedFrom":subQ8})])]})})],"blendedInto":[makeQuery(id+"F42.boolean.opBoolean","COPY",FACE,{"disambiguationData":[TD([makeQuery(id+"F5.opLoft","SWEPT_FACE",FACE,{"disambiguationData":[OSD([subQ4,subQ3,sQuery(id+"F3.wireOp",EDGE,"E18.left"),subQ2,subQ1,subQ0])]})])],"derivedFrom":makeQuery(id+"F42.opRevolve","SWEPT_FACE",FACE,{"disambiguationData":[OSD([subQ8]),TDD([makeQuery(id+"F41.imprint","IMPRINT",EDGE,{"disambiguationData":[TD([[makeQuery(id+"F41.imprint","INTERSECT",VERTEX,{"disambiguationData":[OD(0.0)],"derivedFrom":[subQ8,subQ7]}),-1.0]])],"derivedFrom":subQ8})])]})})]});}
            var Q83;
            {var subQ0=sQuery(id+"F41.wireOp",EDGE,"E34");var subQ1=sQuery(id+"F41.wireOp",EDGE,"E32");Q83=makeQuery(id+"F42.boolean.opBoolean","INTERSECT",EDGE,{"derivedFrom":[makeQuery(id+"F5.opLoft","SWEPT_FACE",FACE,{"disambiguationData":[OSD([sQuery(id+"F3.wireOp",EDGE,"E18.bottom"),sQuery(id+"F3.wireOp",EDGE,"E18.top"),sQuery(id+"F3.wireOp",EDGE,"E18.left"),sQuery(id+"F4.wireOp",EDGE,"E21"),sQuery(id+"F4.wireOp",EDGE,"E22"),sQuery(id+"F4.wireOp",EDGE,"E23")])]}),makeQuery(id+"F42.opRevolve","SWEPT_FACE",FACE,{"disambiguationData":[OSD([subQ1]),TDD([makeQuery(id+"F41.imprint","IMPRINT",EDGE,{"disambiguationData":[TD([[makeQuery(id+"F41.imprint","INTERSECT",VERTEX,{"disambiguationData":[OD(0.0)],"derivedFrom":[subQ1,subQ0]}),-1.0]])],"derivedFrom":subQ1})])]})]});}
            var Q84;
            {var subQ0=sQuery(id+"F4.wireOp",EDGE,"E26.1.3");var subQ1=sQuery(id+"F4.wireOp",EDGE,"E26.1.2");var subQ2=sQuery(id+"F4.wireOp",EDGE,"E26.1.0");var subQ3=sQuery(id+"F3.wireOp",EDGE,"E20.1.3");var subQ4=sQuery(id+"F3.wireOp",EDGE,"E20.1.1");var subQ5=sQuery(id+"F4.wireOp",EDGE,"E26.1.1");var subQ6=makeQuery(id+"F20.opLoft","SWEPT_FACE",FACE,{"disambiguationData":[OSD([subQ4,sQuery(id+"F3.wireOp",EDGE,"E20.1.2"),subQ3,subQ5,subQ1,subQ0])]});var subQ7=sQuery(id+"F41.wireOp",EDGE,"E34");var subQ8=sQuery(id+"F41.wireOp",EDGE,"E32");Q84=makeQuery(id+"F44.opFillet","BLEND_EDGE",EDGE,{"blendedFrom":[makeQuery(id+"F40.boolean.opBoolean","INTERSECT",EDGE,{"derivedFrom":[subQ6,makeQuery(id+"F40.opExtrude","CAP_FACE",FACE,{"disambiguationData":[OSD([sQuery(id+"F39.wireOp",EDGE,"E29"),sQuery(id+"F39.wireOp",EDGE,"E30")])],"isStart":false})]}),makeQuery(id+"F42.boolean.opBoolean","COPY",FACE,{"disambiguationData":[TD([makeQuery(id+"F20.opLoft","SWEPT_FACE",FACE,{"disambiguationData":[OSD([sQuery(id+"F3.wireOp",EDGE,"E20.1.0"),subQ4,subQ3,subQ2,subQ1,subQ0])]})])],"derivedFrom":makeQuery(id+"F42.opRevolve","SWEPT_FACE",FACE,{"disambiguationData":[OSD([subQ8]),TDD([makeQuery(id+"F41.imprint","IMPRINT",EDGE,{"disambiguationData":[TD([[makeQuery(id+"F41.imprint","INTERSECT",VERTEX,{"disambiguationData":[OD(0.0)],"derivedFrom":[subQ8,subQ7]}),-1.0]])],"derivedFrom":subQ8})])]})})],"blendedInto":[makeQuery(id+"F42.boolean.opBoolean","COPY",FACE,{"disambiguationData":[TD([makeQuery(id+"F20.opLoft","SWEPT_FACE",FACE,{"disambiguationData":[OSD([sQuery(id+"F3.wireOp",EDGE,"E20.1.0"),subQ4,subQ3,subQ2,subQ1,subQ0])]})])],"derivedFrom":makeQuery(id+"F42.opRevolve","SWEPT_FACE",FACE,{"disambiguationData":[OSD([subQ8]),TDD([makeQuery(id+"F41.imprint","IMPRINT",EDGE,{"disambiguationData":[TD([[makeQuery(id+"F41.imprint","INTERSECT",VERTEX,{"disambiguationData":[OD(0.0)],"derivedFrom":[subQ8,subQ7]}),-1.0]])],"derivedFrom":subQ8})])]})})]});}
            var Q85;
            {var subQ0=sQuery(id+"F41.wireOp",EDGE,"E34");var subQ1=sQuery(id+"F41.wireOp",EDGE,"E32");Q85=makeQuery(id+"F42.boolean.opBoolean","INTERSECT",EDGE,{"derivedFrom":[makeQuery(id+"F20.opLoft","SWEPT_FACE",FACE,{"disambiguationData":[OSD([sQuery(id+"F3.wireOp",EDGE,"E20.1.0"),sQuery(id+"F3.wireOp",EDGE,"E20.1.1"),sQuery(id+"F3.wireOp",EDGE,"E20.1.3"),sQuery(id+"F4.wireOp",EDGE,"E26.1.0"),sQuery(id+"F4.wireOp",EDGE,"E26.1.2"),sQuery(id+"F4.wireOp",EDGE,"E26.1.3")])]}),makeQuery(id+"F42.opRevolve","SWEPT_FACE",FACE,{"disambiguationData":[OSD([subQ1]),TDD([makeQuery(id+"F41.imprint","IMPRINT",EDGE,{"disambiguationData":[TD([[makeQuery(id+"F41.imprint","INTERSECT",VERTEX,{"disambiguationData":[OD(0.0)],"derivedFrom":[subQ1,subQ0]}),-1.0]])],"derivedFrom":subQ1})])]})]});}
            var Q86;
            {var subQ0=sQuery(id+"F4.wireOp",EDGE,"E26.2.3");var subQ1=sQuery(id+"F4.wireOp",EDGE,"E26.2.2");var subQ2=sQuery(id+"F4.wireOp",EDGE,"E26.2.1");var subQ3=sQuery(id+"F3.wireOp",EDGE,"E20.2.3");var subQ4=sQuery(id+"F3.wireOp",EDGE,"E20.2.1");var subQ5=makeQuery(id+"F19.opLoft","SWEPT_FACE",FACE,{"disambiguationData":[OSD([subQ4,sQuery(id+"F3.wireOp",EDGE,"E20.2.2"),subQ3,subQ2,subQ1,subQ0])]});var subQ6=sQuery(id+"F4.wireOp",EDGE,"E26.2.0");var subQ7=sQuery(id+"F41.wireOp",EDGE,"E34");var subQ8=sQuery(id+"F41.wireOp",EDGE,"E32");Q86=makeQuery(id+"F44.opFillet","BLEND_EDGE",EDGE,{"blendedFrom":[makeQuery(id+"F40.boolean.opBoolean","INTERSECT",EDGE,{"derivedFrom":[subQ5,makeQuery(id+"F40.opExtrude","CAP_FACE",FACE,{"disambiguationData":[OSD([sQuery(id+"F39.wireOp",EDGE,"E29"),sQuery(id+"F39.wireOp",EDGE,"E30")])],"isStart":false})]}),makeQuery(id+"F42.boolean.opBoolean","COPY",FACE,{"disambiguationData":[TD([makeQuery(id+"F19.opLoft","SWEPT_FACE",FACE,{"disambiguationData":[OSD([sQuery(id+"F3.wireOp",EDGE,"E20.2.0"),subQ4,subQ3,subQ6,subQ1,subQ0])]})])],"derivedFrom":makeQuery(id+"F42.opRevolve","SWEPT_FACE",FACE,{"disambiguationData":[OSD([subQ8]),TDD([makeQuery(id+"F41.imprint","IMPRINT",EDGE,{"disambiguationData":[TD([[makeQuery(id+"F41.imprint","INTERSECT",VERTEX,{"disambiguationData":[OD(0.0)],"derivedFrom":[subQ8,subQ7]}),-1.0]])],"derivedFrom":subQ8})])]})})],"blendedInto":[makeQuery(id+"F42.boolean.opBoolean","COPY",FACE,{"disambiguationData":[TD([makeQuery(id+"F19.opLoft","SWEPT_FACE",FACE,{"disambiguationData":[OSD([sQuery(id+"F3.wireOp",EDGE,"E20.2.0"),subQ4,subQ3,subQ6,subQ1,subQ0])]})])],"derivedFrom":makeQuery(id+"F42.opRevolve","SWEPT_FACE",FACE,{"disambiguationData":[OSD([subQ8]),TDD([makeQuery(id+"F41.imprint","IMPRINT",EDGE,{"disambiguationData":[TD([[makeQuery(id+"F41.imprint","INTERSECT",VERTEX,{"disambiguationData":[OD(0.0)],"derivedFrom":[subQ8,subQ7]}),-1.0]])],"derivedFrom":subQ8})])]})})]});}
            var Q87;
            {var subQ0=sQuery(id+"F41.wireOp",EDGE,"E34");var subQ1=sQuery(id+"F41.wireOp",EDGE,"E32");Q87=makeQuery(id+"F42.boolean.opBoolean","INTERSECT",EDGE,{"derivedFrom":[makeQuery(id+"F19.opLoft","SWEPT_FACE",FACE,{"disambiguationData":[OSD([sQuery(id+"F3.wireOp",EDGE,"E20.2.0"),sQuery(id+"F3.wireOp",EDGE,"E20.2.1"),sQuery(id+"F3.wireOp",EDGE,"E20.2.3"),sQuery(id+"F4.wireOp",EDGE,"E26.2.0"),sQuery(id+"F4.wireOp",EDGE,"E26.2.2"),sQuery(id+"F4.wireOp",EDGE,"E26.2.3")])]}),makeQuery(id+"F42.opRevolve","SWEPT_FACE",FACE,{"disambiguationData":[OSD([subQ1]),TDD([makeQuery(id+"F41.imprint","IMPRINT",EDGE,{"disambiguationData":[TD([[makeQuery(id+"F41.imprint","INTERSECT",VERTEX,{"disambiguationData":[OD(0.0)],"derivedFrom":[subQ1,subQ0]}),-1.0]])],"derivedFrom":subQ1})])]})]});}
            var Q88;
            {var subQ0=sQuery(id+"F4.wireOp",EDGE,"E26.3.0");var subQ1=sQuery(id+"F4.wireOp",EDGE,"E26.3.1");var subQ2=sQuery(id+"F4.wireOp",EDGE,"E26.3.2");var subQ3=sQuery(id+"F4.wireOp",EDGE,"E26.3.3");var subQ4=sQuery(id+"F3.wireOp",EDGE,"E20.3.3");var subQ5=sQuery(id+"F3.wireOp",EDGE,"E20.3.1");var subQ6=makeQuery(id+"F18.opLoft","SWEPT_FACE",FACE,{"disambiguationData":[OSD([subQ5,sQuery(id+"F3.wireOp",EDGE,"E20.3.2"),subQ4,subQ1,subQ2,subQ3])]});var subQ7=sQuery(id+"F41.wireOp",EDGE,"E34");var subQ8=sQuery(id+"F41.wireOp",EDGE,"E32");Q88=makeQuery(id+"F44.opFillet","BLEND_EDGE",EDGE,{"blendedFrom":[makeQuery(id+"F40.boolean.opBoolean","INTERSECT",EDGE,{"derivedFrom":[subQ6,makeQuery(id+"F40.opExtrude","CAP_FACE",FACE,{"disambiguationData":[OSD([sQuery(id+"F39.wireOp",EDGE,"E29"),sQuery(id+"F39.wireOp",EDGE,"E30")])],"isStart":false})]}),makeQuery(id+"F42.boolean.opBoolean","COPY",FACE,{"disambiguationData":[TD([makeQuery(id+"F18.opLoft","SWEPT_FACE",FACE,{"disambiguationData":[OSD([sQuery(id+"F3.wireOp",EDGE,"E20.3.0"),subQ5,subQ4,subQ0,subQ2,subQ3])]})])],"derivedFrom":makeQuery(id+"F42.opRevolve","SWEPT_FACE",FACE,{"disambiguationData":[OSD([subQ8]),TDD([makeQuery(id+"F41.imprint","IMPRINT",EDGE,{"disambiguationData":[TD([[makeQuery(id+"F41.imprint","INTERSECT",VERTEX,{"disambiguationData":[OD(0.0)],"derivedFrom":[subQ8,subQ7]}),-1.0]])],"derivedFrom":subQ8})])]})})],"blendedInto":[makeQuery(id+"F42.boolean.opBoolean","COPY",FACE,{"disambiguationData":[TD([makeQuery(id+"F18.opLoft","SWEPT_FACE",FACE,{"disambiguationData":[OSD([sQuery(id+"F3.wireOp",EDGE,"E20.3.0"),subQ5,subQ4,subQ0,subQ2,subQ3])]})])],"derivedFrom":makeQuery(id+"F42.opRevolve","SWEPT_FACE",FACE,{"disambiguationData":[OSD([subQ8]),TDD([makeQuery(id+"F41.imprint","IMPRINT",EDGE,{"disambiguationData":[TD([[makeQuery(id+"F41.imprint","INTERSECT",VERTEX,{"disambiguationData":[OD(0.0)],"derivedFrom":[subQ8,subQ7]}),-1.0]])],"derivedFrom":subQ8})])]})})]});}
            var Q89;
            {var subQ0=sQuery(id+"F41.wireOp",EDGE,"E34");var subQ1=sQuery(id+"F41.wireOp",EDGE,"E32");Q89=makeQuery(id+"F42.boolean.opBoolean","INTERSECT",EDGE,{"derivedFrom":[makeQuery(id+"F18.opLoft","SWEPT_FACE",FACE,{"disambiguationData":[OSD([sQuery(id+"F3.wireOp",EDGE,"E20.3.0"),sQuery(id+"F3.wireOp",EDGE,"E20.3.1"),sQuery(id+"F3.wireOp",EDGE,"E20.3.3"),sQuery(id+"F4.wireOp",EDGE,"E26.3.0"),sQuery(id+"F4.wireOp",EDGE,"E26.3.2"),sQuery(id+"F4.wireOp",EDGE,"E26.3.3")])]}),makeQuery(id+"F42.opRevolve","SWEPT_FACE",FACE,{"disambiguationData":[OSD([subQ1]),TDD([makeQuery(id+"F41.imprint","IMPRINT",EDGE,{"disambiguationData":[TD([[makeQuery(id+"F41.imprint","INTERSECT",VERTEX,{"disambiguationData":[OD(0.0)],"derivedFrom":[subQ1,subQ0]}),-1.0]])],"derivedFrom":subQ1})])]})]});}
            var Q90;
            {var subQ0=sQuery(id+"F4.wireOp",EDGE,"E26.4.3");var subQ1=sQuery(id+"F4.wireOp",EDGE,"E26.4.2");var subQ2=sQuery(id+"F4.wireOp",EDGE,"E26.4.1");var subQ3=sQuery(id+"F3.wireOp",EDGE,"E20.4.3");var subQ4=sQuery(id+"F3.wireOp",EDGE,"E20.4.1");var subQ5=makeQuery(id+"F17.opLoft","SWEPT_FACE",FACE,{"disambiguationData":[OSD([subQ4,sQuery(id+"F3.wireOp",EDGE,"E20.4.2"),subQ3,subQ2,subQ1,subQ0])]});var subQ6=sQuery(id+"F4.wireOp",EDGE,"E26.4.0");var subQ7=sQuery(id+"F41.wireOp",EDGE,"E34");var subQ8=sQuery(id+"F41.wireOp",EDGE,"E32");Q90=makeQuery(id+"F44.opFillet","BLEND_EDGE",EDGE,{"blendedFrom":[makeQuery(id+"F40.boolean.opBoolean","INTERSECT",EDGE,{"derivedFrom":[subQ5,makeQuery(id+"F40.opExtrude","CAP_FACE",FACE,{"disambiguationData":[OSD([sQuery(id+"F39.wireOp",EDGE,"E29"),sQuery(id+"F39.wireOp",EDGE,"E30")])],"isStart":false})]}),makeQuery(id+"F42.boolean.opBoolean","COPY",FACE,{"disambiguationData":[TD([makeQuery(id+"F17.opLoft","SWEPT_FACE",FACE,{"disambiguationData":[OSD([sQuery(id+"F3.wireOp",EDGE,"E20.4.0"),subQ4,subQ3,subQ6,subQ1,subQ0])]})])],"derivedFrom":makeQuery(id+"F42.opRevolve","SWEPT_FACE",FACE,{"disambiguationData":[OSD([subQ8]),TDD([makeQuery(id+"F41.imprint","IMPRINT",EDGE,{"disambiguationData":[TD([[makeQuery(id+"F41.imprint","INTERSECT",VERTEX,{"disambiguationData":[OD(0.0)],"derivedFrom":[subQ8,subQ7]}),-1.0]])],"derivedFrom":subQ8})])]})})],"blendedInto":[makeQuery(id+"F42.boolean.opBoolean","COPY",FACE,{"disambiguationData":[TD([makeQuery(id+"F17.opLoft","SWEPT_FACE",FACE,{"disambiguationData":[OSD([sQuery(id+"F3.wireOp",EDGE,"E20.4.0"),subQ4,subQ3,subQ6,subQ1,subQ0])]})])],"derivedFrom":makeQuery(id+"F42.opRevolve","SWEPT_FACE",FACE,{"disambiguationData":[OSD([subQ8]),TDD([makeQuery(id+"F41.imprint","IMPRINT",EDGE,{"disambiguationData":[TD([[makeQuery(id+"F41.imprint","INTERSECT",VERTEX,{"disambiguationData":[OD(0.0)],"derivedFrom":[subQ8,subQ7]}),-1.0]])],"derivedFrom":subQ8})])]})})]});}
            var Q91;
            {var subQ0=sQuery(id+"F41.wireOp",EDGE,"E34");var subQ1=sQuery(id+"F41.wireOp",EDGE,"E32");Q91=makeQuery(id+"F42.boolean.opBoolean","INTERSECT",EDGE,{"derivedFrom":[makeQuery(id+"F17.opLoft","SWEPT_FACE",FACE,{"disambiguationData":[OSD([sQuery(id+"F3.wireOp",EDGE,"E20.4.0"),sQuery(id+"F3.wireOp",EDGE,"E20.4.1"),sQuery(id+"F3.wireOp",EDGE,"E20.4.3"),sQuery(id+"F4.wireOp",EDGE,"E26.4.0"),sQuery(id+"F4.wireOp",EDGE,"E26.4.2"),sQuery(id+"F4.wireOp",EDGE,"E26.4.3")])]}),makeQuery(id+"F42.opRevolve","SWEPT_FACE",FACE,{"disambiguationData":[OSD([subQ1]),TDD([makeQuery(id+"F41.imprint","IMPRINT",EDGE,{"disambiguationData":[TD([[makeQuery(id+"F41.imprint","INTERSECT",VERTEX,{"disambiguationData":[OD(0.0)],"derivedFrom":[subQ1,subQ0]}),-1.0]])],"derivedFrom":subQ1})])]})]});}
            var Q92;
            {var subQ0=sQuery(id+"F4.wireOp",EDGE,"E26.5.3");var subQ1=sQuery(id+"F4.wireOp",EDGE,"E26.5.2");var subQ2=sQuery(id+"F4.wireOp",EDGE,"E26.5.1");var subQ3=sQuery(id+"F3.wireOp",EDGE,"E20.5.3");var subQ4=sQuery(id+"F3.wireOp",EDGE,"E20.5.1");var subQ5=makeQuery(id+"F16.opLoft","SWEPT_FACE",FACE,{"disambiguationData":[OSD([subQ4,sQuery(id+"F3.wireOp",EDGE,"E20.5.2"),subQ3,subQ2,subQ1,subQ0])]});var subQ6=sQuery(id+"F4.wireOp",EDGE,"E26.5.0");var subQ7=sQuery(id+"F41.wireOp",EDGE,"E34");var subQ8=sQuery(id+"F41.wireOp",EDGE,"E32");Q92=makeQuery(id+"F44.opFillet","BLEND_EDGE",EDGE,{"blendedFrom":[makeQuery(id+"F40.boolean.opBoolean","INTERSECT",EDGE,{"derivedFrom":[subQ5,makeQuery(id+"F40.opExtrude","CAP_FACE",FACE,{"disambiguationData":[OSD([sQuery(id+"F39.wireOp",EDGE,"E29"),sQuery(id+"F39.wireOp",EDGE,"E30")])],"isStart":false})]}),makeQuery(id+"F42.boolean.opBoolean","COPY",FACE,{"disambiguationData":[TD([makeQuery(id+"F16.opLoft","SWEPT_FACE",FACE,{"disambiguationData":[OSD([sQuery(id+"F3.wireOp",EDGE,"E20.5.0"),subQ4,subQ3,subQ6,subQ1,subQ0])]})])],"derivedFrom":makeQuery(id+"F42.opRevolve","SWEPT_FACE",FACE,{"disambiguationData":[OSD([subQ8]),TDD([makeQuery(id+"F41.imprint","IMPRINT",EDGE,{"disambiguationData":[TD([[makeQuery(id+"F41.imprint","INTERSECT",VERTEX,{"disambiguationData":[OD(0.0)],"derivedFrom":[subQ8,subQ7]}),-1.0]])],"derivedFrom":subQ8})])]})})],"blendedInto":[makeQuery(id+"F42.boolean.opBoolean","COPY",FACE,{"disambiguationData":[TD([makeQuery(id+"F16.opLoft","SWEPT_FACE",FACE,{"disambiguationData":[OSD([sQuery(id+"F3.wireOp",EDGE,"E20.5.0"),subQ4,subQ3,subQ6,subQ1,subQ0])]})])],"derivedFrom":makeQuery(id+"F42.opRevolve","SWEPT_FACE",FACE,{"disambiguationData":[OSD([subQ8]),TDD([makeQuery(id+"F41.imprint","IMPRINT",EDGE,{"disambiguationData":[TD([[makeQuery(id+"F41.imprint","INTERSECT",VERTEX,{"disambiguationData":[OD(0.0)],"derivedFrom":[subQ8,subQ7]}),-1.0]])],"derivedFrom":subQ8})])]})})]});}
            var Q93;
            {var subQ0=sQuery(id+"F41.wireOp",EDGE,"E34");var subQ1=sQuery(id+"F41.wireOp",EDGE,"E32");Q93=makeQuery(id+"F42.boolean.opBoolean","INTERSECT",EDGE,{"derivedFrom":[makeQuery(id+"F16.opLoft","SWEPT_FACE",FACE,{"disambiguationData":[OSD([sQuery(id+"F3.wireOp",EDGE,"E20.5.0"),sQuery(id+"F3.wireOp",EDGE,"E20.5.1"),sQuery(id+"F3.wireOp",EDGE,"E20.5.3"),sQuery(id+"F4.wireOp",EDGE,"E26.5.0"),sQuery(id+"F4.wireOp",EDGE,"E26.5.2"),sQuery(id+"F4.wireOp",EDGE,"E26.5.3")])]}),makeQuery(id+"F42.opRevolve","SWEPT_FACE",FACE,{"disambiguationData":[OSD([subQ1]),TDD([makeQuery(id+"F41.imprint","IMPRINT",EDGE,{"disambiguationData":[TD([[makeQuery(id+"F41.imprint","INTERSECT",VERTEX,{"disambiguationData":[OD(0.0)],"derivedFrom":[subQ1,subQ0]}),-1.0]])],"derivedFrom":subQ1})])]})]});}
            var Q94;
            {var subQ0=sQuery(id+"F4.wireOp",EDGE,"E26.6.3");var subQ1=sQuery(id+"F4.wireOp",EDGE,"E26.6.2");var subQ2=sQuery(id+"F4.wireOp",EDGE,"E26.6.0");var subQ3=sQuery(id+"F3.wireOp",EDGE,"E20.6.3");var subQ4=sQuery(id+"F3.wireOp",EDGE,"E20.6.1");var subQ5=sQuery(id+"F4.wireOp",EDGE,"E26.6.1");var subQ6=makeQuery(id+"F15.opLoft","SWEPT_FACE",FACE,{"disambiguationData":[OSD([subQ4,sQuery(id+"F3.wireOp",EDGE,"E20.6.2"),subQ3,subQ5,subQ1,subQ0])]});var subQ7=sQuery(id+"F41.wireOp",EDGE,"E34");var subQ8=sQuery(id+"F41.wireOp",EDGE,"E32");Q94=makeQuery(id+"F44.opFillet","BLEND_EDGE",EDGE,{"blendedFrom":[makeQuery(id+"F40.boolean.opBoolean","INTERSECT",EDGE,{"derivedFrom":[subQ6,makeQuery(id+"F40.opExtrude","CAP_FACE",FACE,{"disambiguationData":[OSD([sQuery(id+"F39.wireOp",EDGE,"E29"),sQuery(id+"F39.wireOp",EDGE,"E30")])],"isStart":false})]}),makeQuery(id+"F42.boolean.opBoolean","COPY",FACE,{"disambiguationData":[TD([makeQuery(id+"F15.opLoft","SWEPT_FACE",FACE,{"disambiguationData":[OSD([sQuery(id+"F3.wireOp",EDGE,"E20.6.0"),subQ4,subQ3,subQ2,subQ1,subQ0])]})])],"derivedFrom":makeQuery(id+"F42.opRevolve","SWEPT_FACE",FACE,{"disambiguationData":[OSD([subQ8]),TDD([makeQuery(id+"F41.imprint","IMPRINT",EDGE,{"disambiguationData":[TD([[makeQuery(id+"F41.imprint","INTERSECT",VERTEX,{"disambiguationData":[OD(0.0)],"derivedFrom":[subQ8,subQ7]}),-1.0]])],"derivedFrom":subQ8})])]})})],"blendedInto":[makeQuery(id+"F42.boolean.opBoolean","COPY",FACE,{"disambiguationData":[TD([makeQuery(id+"F15.opLoft","SWEPT_FACE",FACE,{"disambiguationData":[OSD([sQuery(id+"F3.wireOp",EDGE,"E20.6.0"),subQ4,subQ3,subQ2,subQ1,subQ0])]})])],"derivedFrom":makeQuery(id+"F42.opRevolve","SWEPT_FACE",FACE,{"disambiguationData":[OSD([subQ8]),TDD([makeQuery(id+"F41.imprint","IMPRINT",EDGE,{"disambiguationData":[TD([[makeQuery(id+"F41.imprint","INTERSECT",VERTEX,{"disambiguationData":[OD(0.0)],"derivedFrom":[subQ8,subQ7]}),-1.0]])],"derivedFrom":subQ8})])]})})]});}
            var Q95;
            {var subQ0=sQuery(id+"F41.wireOp",EDGE,"E34");var subQ1=sQuery(id+"F41.wireOp",EDGE,"E32");Q95=makeQuery(id+"F42.boolean.opBoolean","INTERSECT",EDGE,{"derivedFrom":[makeQuery(id+"F15.opLoft","SWEPT_FACE",FACE,{"disambiguationData":[OSD([sQuery(id+"F3.wireOp",EDGE,"E20.6.0"),sQuery(id+"F3.wireOp",EDGE,"E20.6.1"),sQuery(id+"F3.wireOp",EDGE,"E20.6.3"),sQuery(id+"F4.wireOp",EDGE,"E26.6.0"),sQuery(id+"F4.wireOp",EDGE,"E26.6.2"),sQuery(id+"F4.wireOp",EDGE,"E26.6.3")])]}),makeQuery(id+"F42.opRevolve","SWEPT_FACE",FACE,{"disambiguationData":[OSD([subQ1]),TDD([makeQuery(id+"F41.imprint","IMPRINT",EDGE,{"disambiguationData":[TD([[makeQuery(id+"F41.imprint","INTERSECT",VERTEX,{"disambiguationData":[OD(0.0)],"derivedFrom":[subQ1,subQ0]}),-1.0]])],"derivedFrom":subQ1})])]})]});}
            fillet(context, id + "F49", {"entities" : qUnion([Q0, Q1, Q2, Q3, Q4, Q5, Q6, Q7, Q8, Q9, Q10, Q11, Q12, Q13, Q14, Q15, Q16, Q17, Q18, Q19, Q20, Q21, Q22, Q23, Q24, Q25, Q26, Q27, Q28, Q29, Q30, Q31, Q32, Q33, Q34, Q35, Q36, Q37, Q38, Q39, Q40, Q41, Q42, Q43, Q44, Q45, Q46, Q47, Q48, Q49, Q50, Q51, Q52, Q53, Q54, Q55, Q56, Q57, Q58, Q59, Q60, Q61, Q62, Q63, Q64, Q65, Q66, Q67, Q68, Q69, Q70, Q71, Q72, Q73, Q74, Q75, Q76, Q77, Q78, Q79, Q80, Q81, Q82, Q83, Q84, Q85, Q86, Q87, Q88, Q89, Q90, Q91, Q92, Q93, Q94, Q95]), "radius" : 0.5 * mm, "tangentPropagation" : true, "allowEdgeOverflow" : false});
        }
        {
            var Q0;
            Q0=makeQuery(id+"F1.opRevolve","SWEPT_EDGE",EDGE,{"disambiguationData":[OSD([sQuery(id+"F0.wireOp",EDGE,"E9"),sQuery(id+"F0.wireOp",EDGE,"E10")])]});
            var Q1;
            Q1=makeQuery(id+"F1.opRevolve","SWEPT_EDGE",EDGE,{"disambiguationData":[OSD([sQuery(id+"F0.wireOp",EDGE,"E10"),sQuery(id+"F0.wireOp",EDGE,"E11")])]});
            var Q2;
            Q2=makeQuery(id+"F1.opRevolve","SWEPT_EDGE",EDGE,{"disambiguationData":[OSD([sQuery(id+"F0.wireOp",EDGE,"E13"),sQuery(id+"F0.wireOp",EDGE,"E14")])]});
            var Q3;
            Q3=makeQuery(id+"F1.opRevolve","SWEPT_EDGE",EDGE,{"disambiguationData":[OSD([sQuery(id+"F0.wireOp",EDGE,"E14"),sQuery(id+"F0.wireOp",EDGE,"E15")])]});
            chamfer(context, id + "F50", {"entities" : qUnion([Q0, Q1, Q2, Q3]), "width" : 2 * mm, "tangentPropagation" : true});
        }
        {
            var Q0;
            {var subQ0=sQuery(id+"F0.wireOp",EDGE,"E5");Q0=makeQuery(id+"F46.opChamfer","BLEND_EDGE",EDGE,{"blendedFrom":[makeQuery(id+"F1.opRevolve","SWEPT_EDGE",EDGE,{"disambiguationData":[OSD([subQ0,sQuery(id+"F0.wireOp",EDGE,"E8")])]}),makeQuery(id+"F20.boolean.opBoolean","MERGE",FACE,{"derivedFrom":[makeQuery(id+"F19.boolean.opBoolean","MERGE",FACE,{"derivedFrom":[makeQuery(id+"F18.boolean.opBoolean","MERGE",FACE,{"derivedFrom":[makeQuery(id+"F17.boolean.opBoolean","MERGE",FACE,{"derivedFrom":[makeQuery(id+"F16.boolean.opBoolean","MERGE",FACE,{"derivedFrom":[makeQuery(id+"F15.boolean.opBoolean","MERGE",FACE,{"derivedFrom":[makeQuery(id+"F14.boolean.opBoolean","MERGE",FACE,{"derivedFrom":[makeQuery(id+"F13.boolean.opBoolean","MERGE",FACE,{"derivedFrom":[makeQuery(id+"F12.boolean.opBoolean","MERGE",FACE,{"derivedFrom":[makeQuery(id+"F11.boolean.opBoolean","MERGE",FACE,{"derivedFrom":[makeQuery(id+"F10.boolean.opBoolean","MERGE",FACE,{"derivedFrom":[makeQuery(id+"F9.boolean.opBoolean","MERGE",FACE,{"derivedFrom":[makeQuery(id+"F8.boolean.opBoolean","MERGE",FACE,{"derivedFrom":[makeQuery(id+"F7.boolean.opBoolean","MERGE",FACE,{"derivedFrom":[makeQuery(id+"F6.boolean.opBoolean","MERGE",FACE,{"derivedFrom":[makeQuery(id+"F5.boolean.opBoolean","MERGE",FACE,{"derivedFrom":[makeQuery(id+"F1.opRevolve","SWEPT_FACE",FACE,{"disambiguationData":[OSD([subQ0])]}),makeQuery(id+"F5.opLoft","CAP_FACE",FACE,{"disambiguationData":[OSD([makeQuery(id+"F4.imprint","IMPRINT",FACE,{"disambiguationData":[TD([[makeQuery(id+"F4.imprint","IMPRINT",EDGE,{"derivedFrom":sQuery(id+"F4.wireOp",EDGE,"E21")}),1.0]])]})])],"isStart":true})]}),makeQuery(id+"F6.opLoft","CAP_FACE",FACE,{"disambiguationData":[OSD([makeQuery(id+"F4.imprint","IMPRINT",FACE,{"disambiguationData":[TD([[makeQuery(id+"F4.imprint","IMPRINT",EDGE,{"derivedFrom":sQuery(id+"F4.wireOp",EDGE,"E26.15.0")}),1.0]])]})])],"isStart":true})]}),makeQuery(id+"F7.opLoft","CAP_FACE",FACE,{"disambiguationData":[OSD([makeQuery(id+"F4.imprint","IMPRINT",FACE,{"disambiguationData":[TD([[makeQuery(id+"F4.imprint","IMPRINT",EDGE,{"derivedFrom":sQuery(id+"F4.wireOp",EDGE,"E26.14.0")}),1.0]])]})])],"isStart":true})]}),makeQuery(id+"F8.opLoft","CAP_FACE",FACE,{"disambiguationData":[OSD([makeQuery(id+"F4.imprint","IMPRINT",FACE,{"disambiguationData":[TD([[makeQuery(id+"F4.imprint","IMPRINT",EDGE,{"derivedFrom":sQuery(id+"F4.wireOp",EDGE,"E26.13.0")}),1.0]])]})])],"isStart":true})]}),makeQuery(id+"F9.opLoft","CAP_FACE",FACE,{"disambiguationData":[OSD([makeQuery(id+"F4.imprint","IMPRINT",FACE,{"disambiguationData":[TD([[makeQuery(id+"F4.imprint","IMPRINT",EDGE,{"derivedFrom":sQuery(id+"F4.wireOp",EDGE,"E26.12.0")}),1.0]])]})])],"isStart":true})]}),makeQuery(id+"F10.opLoft","CAP_FACE",FACE,{"disambiguationData":[OSD([makeQuery(id+"F4.imprint","IMPRINT",FACE,{"disambiguationData":[TD([[makeQuery(id+"F4.imprint","IMPRINT",EDGE,{"derivedFrom":sQuery(id+"F4.wireOp",EDGE,"E26.11.0")}),1.0]])]})])],"isStart":true})]}),makeQuery(id+"F11.opLoft","CAP_FACE",FACE,{"disambiguationData":[OSD([makeQuery(id+"F4.imprint","IMPRINT",FACE,{"disambiguationData":[TD([[makeQuery(id+"F4.imprint","IMPRINT",EDGE,{"derivedFrom":sQuery(id+"F4.wireOp",EDGE,"E26.10.0")}),1.0]])]})])],"isStart":true})]}),makeQuery(id+"F12.opLoft","CAP_FACE",FACE,{"disambiguationData":[OSD([makeQuery(id+"F4.imprint","IMPRINT",FACE,{"disambiguationData":[TD([[makeQuery(id+"F4.imprint","IMPRINT",EDGE,{"derivedFrom":sQuery(id+"F4.wireOp",EDGE,"E26.9.0")}),1.0]])]})])],"isStart":true})]}),makeQuery(id+"F13.opLoft","CAP_FACE",FACE,{"disambiguationData":[OSD([makeQuery(id+"F4.imprint","IMPRINT",FACE,{"disambiguationData":[TD([[makeQuery(id+"F4.imprint","IMPRINT",EDGE,{"derivedFrom":sQuery(id+"F4.wireOp",EDGE,"E26.8.0")}),1.0]])]})])],"isStart":true})]}),makeQuery(id+"F14.opLoft","CAP_FACE",FACE,{"disambiguationData":[OSD([makeQuery(id+"F4.imprint","IMPRINT",FACE,{"disambiguationData":[TD([[makeQuery(id+"F4.imprint","IMPRINT",EDGE,{"derivedFrom":sQuery(id+"F4.wireOp",EDGE,"E26.7.0")}),1.0]])]})])],"isStart":true})]}),makeQuery(id+"F15.opLoft","CAP_FACE",FACE,{"disambiguationData":[OSD([makeQuery(id+"F4.imprint","IMPRINT",FACE,{"disambiguationData":[TD([[makeQuery(id+"F4.imprint","IMPRINT",EDGE,{"derivedFrom":sQuery(id+"F4.wireOp",EDGE,"E26.6.0")}),1.0]])]})])],"isStart":true})]}),makeQuery(id+"F16.opLoft","CAP_FACE",FACE,{"disambiguationData":[OSD([makeQuery(id+"F4.imprint","IMPRINT",FACE,{"disambiguationData":[TD([[makeQuery(id+"F4.imprint","IMPRINT",EDGE,{"derivedFrom":sQuery(id+"F4.wireOp",EDGE,"E26.5.0")}),1.0]])]})])],"isStart":true})]}),makeQuery(id+"F17.opLoft","CAP_FACE",FACE,{"disambiguationData":[OSD([makeQuery(id+"F4.imprint","IMPRINT",FACE,{"disambiguationData":[TD([[makeQuery(id+"F4.imprint","IMPRINT",EDGE,{"derivedFrom":sQuery(id+"F4.wireOp",EDGE,"E26.4.0")}),1.0]])]})])],"isStart":true})]}),makeQuery(id+"F18.opLoft","CAP_FACE",FACE,{"disambiguationData":[OSD([makeQuery(id+"F4.imprint","IMPRINT",FACE,{"disambiguationData":[TD([[makeQuery(id+"F4.imprint","IMPRINT",EDGE,{"derivedFrom":sQuery(id+"F4.wireOp",EDGE,"E26.3.0")}),1.0]])]})])],"isStart":true})]}),makeQuery(id+"F19.opLoft","CAP_FACE",FACE,{"disambiguationData":[OSD([makeQuery(id+"F4.imprint","IMPRINT",FACE,{"disambiguationData":[TD([[makeQuery(id+"F4.imprint","IMPRINT",EDGE,{"derivedFrom":sQuery(id+"F4.wireOp",EDGE,"E26.2.0")}),1.0]])]})])],"isStart":true})]}),makeQuery(id+"F20.opLoft","CAP_FACE",FACE,{"disambiguationData":[OSD([makeQuery(id+"F4.imprint","IMPRINT",FACE,{"disambiguationData":[TD([[makeQuery(id+"F4.imprint","IMPRINT",EDGE,{"derivedFrom":sQuery(id+"F4.wireOp",EDGE,"E26.1.0")}),1.0]])]})])],"isStart":true})]})],"blendedInto":[makeQuery(id+"F20.boolean.opBoolean","MERGE",FACE,{"derivedFrom":[makeQuery(id+"F19.boolean.opBoolean","MERGE",FACE,{"derivedFrom":[makeQuery(id+"F18.boolean.opBoolean","MERGE",FACE,{"derivedFrom":[makeQuery(id+"F17.boolean.opBoolean","MERGE",FACE,{"derivedFrom":[makeQuery(id+"F16.boolean.opBoolean","MERGE",FACE,{"derivedFrom":[makeQuery(id+"F15.boolean.opBoolean","MERGE",FACE,{"derivedFrom":[makeQuery(id+"F14.boolean.opBoolean","MERGE",FACE,{"derivedFrom":[makeQuery(id+"F13.boolean.opBoolean","MERGE",FACE,{"derivedFrom":[makeQuery(id+"F12.boolean.opBoolean","MERGE",FACE,{"derivedFrom":[makeQuery(id+"F11.boolean.opBoolean","MERGE",FACE,{"derivedFrom":[makeQuery(id+"F10.boolean.opBoolean","MERGE",FACE,{"derivedFrom":[makeQuery(id+"F9.boolean.opBoolean","MERGE",FACE,{"derivedFrom":[makeQuery(id+"F8.boolean.opBoolean","MERGE",FACE,{"derivedFrom":[makeQuery(id+"F7.boolean.opBoolean","MERGE",FACE,{"derivedFrom":[makeQuery(id+"F6.boolean.opBoolean","MERGE",FACE,{"derivedFrom":[makeQuery(id+"F5.boolean.opBoolean","MERGE",FACE,{"derivedFrom":[makeQuery(id+"F1.opRevolve","SWEPT_FACE",FACE,{"disambiguationData":[OSD([subQ0])]}),makeQuery(id+"F5.opLoft","CAP_FACE",FACE,{"disambiguationData":[OSD([makeQuery(id+"F4.imprint","IMPRINT",FACE,{"disambiguationData":[TD([[makeQuery(id+"F4.imprint","IMPRINT",EDGE,{"derivedFrom":sQuery(id+"F4.wireOp",EDGE,"E21")}),1.0]])]})])],"isStart":true})]}),makeQuery(id+"F6.opLoft","CAP_FACE",FACE,{"disambiguationData":[OSD([makeQuery(id+"F4.imprint","IMPRINT",FACE,{"disambiguationData":[TD([[makeQuery(id+"F4.imprint","IMPRINT",EDGE,{"derivedFrom":sQuery(id+"F4.wireOp",EDGE,"E26.15.0")}),1.0]])]})])],"isStart":true})]}),makeQuery(id+"F7.opLoft","CAP_FACE",FACE,{"disambiguationData":[OSD([makeQuery(id+"F4.imprint","IMPRINT",FACE,{"disambiguationData":[TD([[makeQuery(id+"F4.imprint","IMPRINT",EDGE,{"derivedFrom":sQuery(id+"F4.wireOp",EDGE,"E26.14.0")}),1.0]])]})])],"isStart":true})]}),makeQuery(id+"F8.opLoft","CAP_FACE",FACE,{"disambiguationData":[OSD([makeQuery(id+"F4.imprint","IMPRINT",FACE,{"disambiguationData":[TD([[makeQuery(id+"F4.imprint","IMPRINT",EDGE,{"derivedFrom":sQuery(id+"F4.wireOp",EDGE,"E26.13.0")}),1.0]])]})])],"isStart":true})]}),makeQuery(id+"F9.opLoft","CAP_FACE",FACE,{"disambiguationData":[OSD([makeQuery(id+"F4.imprint","IMPRINT",FACE,{"disambiguationData":[TD([[makeQuery(id+"F4.imprint","IMPRINT",EDGE,{"derivedFrom":sQuery(id+"F4.wireOp",EDGE,"E26.12.0")}),1.0]])]})])],"isStart":true})]}),makeQuery(id+"F10.opLoft","CAP_FACE",FACE,{"disambiguationData":[OSD([makeQuery(id+"F4.imprint","IMPRINT",FACE,{"disambiguationData":[TD([[makeQuery(id+"F4.imprint","IMPRINT",EDGE,{"derivedFrom":sQuery(id+"F4.wireOp",EDGE,"E26.11.0")}),1.0]])]})])],"isStart":true})]}),makeQuery(id+"F11.opLoft","CAP_FACE",FACE,{"disambiguationData":[OSD([makeQuery(id+"F4.imprint","IMPRINT",FACE,{"disambiguationData":[TD([[makeQuery(id+"F4.imprint","IMPRINT",EDGE,{"derivedFrom":sQuery(id+"F4.wireOp",EDGE,"E26.10.0")}),1.0]])]})])],"isStart":true})]}),makeQuery(id+"F12.opLoft","CAP_FACE",FACE,{"disambiguationData":[OSD([makeQuery(id+"F4.imprint","IMPRINT",FACE,{"disambiguationData":[TD([[makeQuery(id+"F4.imprint","IMPRINT",EDGE,{"derivedFrom":sQuery(id+"F4.wireOp",EDGE,"E26.9.0")}),1.0]])]})])],"isStart":true})]}),makeQuery(id+"F13.opLoft","CAP_FACE",FACE,{"disambiguationData":[OSD([makeQuery(id+"F4.imprint","IMPRINT",FACE,{"disambiguationData":[TD([[makeQuery(id+"F4.imprint","IMPRINT",EDGE,{"derivedFrom":sQuery(id+"F4.wireOp",EDGE,"E26.8.0")}),1.0]])]})])],"isStart":true})]}),makeQuery(id+"F14.opLoft","CAP_FACE",FACE,{"disambiguationData":[OSD([makeQuery(id+"F4.imprint","IMPRINT",FACE,{"disambiguationData":[TD([[makeQuery(id+"F4.imprint","IMPRINT",EDGE,{"derivedFrom":sQuery(id+"F4.wireOp",EDGE,"E26.7.0")}),1.0]])]})])],"isStart":true})]}),makeQuery(id+"F15.opLoft","CAP_FACE",FACE,{"disambiguationData":[OSD([makeQuery(id+"F4.imprint","IMPRINT",FACE,{"disambiguationData":[TD([[makeQuery(id+"F4.imprint","IMPRINT",EDGE,{"derivedFrom":sQuery(id+"F4.wireOp",EDGE,"E26.6.0")}),1.0]])]})])],"isStart":true})]}),makeQuery(id+"F16.opLoft","CAP_FACE",FACE,{"disambiguationData":[OSD([makeQuery(id+"F4.imprint","IMPRINT",FACE,{"disambiguationData":[TD([[makeQuery(id+"F4.imprint","IMPRINT",EDGE,{"derivedFrom":sQuery(id+"F4.wireOp",EDGE,"E26.5.0")}),1.0]])]})])],"isStart":true})]}),makeQuery(id+"F17.opLoft","CAP_FACE",FACE,{"disambiguationData":[OSD([makeQuery(id+"F4.imprint","IMPRINT",FACE,{"disambiguationData":[TD([[makeQuery(id+"F4.imprint","IMPRINT",EDGE,{"derivedFrom":sQuery(id+"F4.wireOp",EDGE,"E26.4.0")}),1.0]])]})])],"isStart":true})]}),makeQuery(id+"F18.opLoft","CAP_FACE",FACE,{"disambiguationData":[OSD([makeQuery(id+"F4.imprint","IMPRINT",FACE,{"disambiguationData":[TD([[makeQuery(id+"F4.imprint","IMPRINT",EDGE,{"derivedFrom":sQuery(id+"F4.wireOp",EDGE,"E26.3.0")}),1.0]])]})])],"isStart":true})]}),makeQuery(id+"F19.opLoft","CAP_FACE",FACE,{"disambiguationData":[OSD([makeQuery(id+"F4.imprint","IMPRINT",FACE,{"disambiguationData":[TD([[makeQuery(id+"F4.imprint","IMPRINT",EDGE,{"derivedFrom":sQuery(id+"F4.wireOp",EDGE,"E26.2.0")}),1.0]])]})])],"isStart":true})]}),makeQuery(id+"F20.opLoft","CAP_FACE",FACE,{"disambiguationData":[OSD([makeQuery(id+"F4.imprint","IMPRINT",FACE,{"disambiguationData":[TD([[makeQuery(id+"F4.imprint","IMPRINT",EDGE,{"derivedFrom":sQuery(id+"F4.wireOp",EDGE,"E26.1.0")}),1.0]])]})])],"isStart":true})]})]});}
            fillet(context, id + "F51", {"entities" : qUnion([Q0]), "radius" : 6 * mm, "tangentPropagation" : true, "allowEdgeOverflow" : false});
        }
    });
